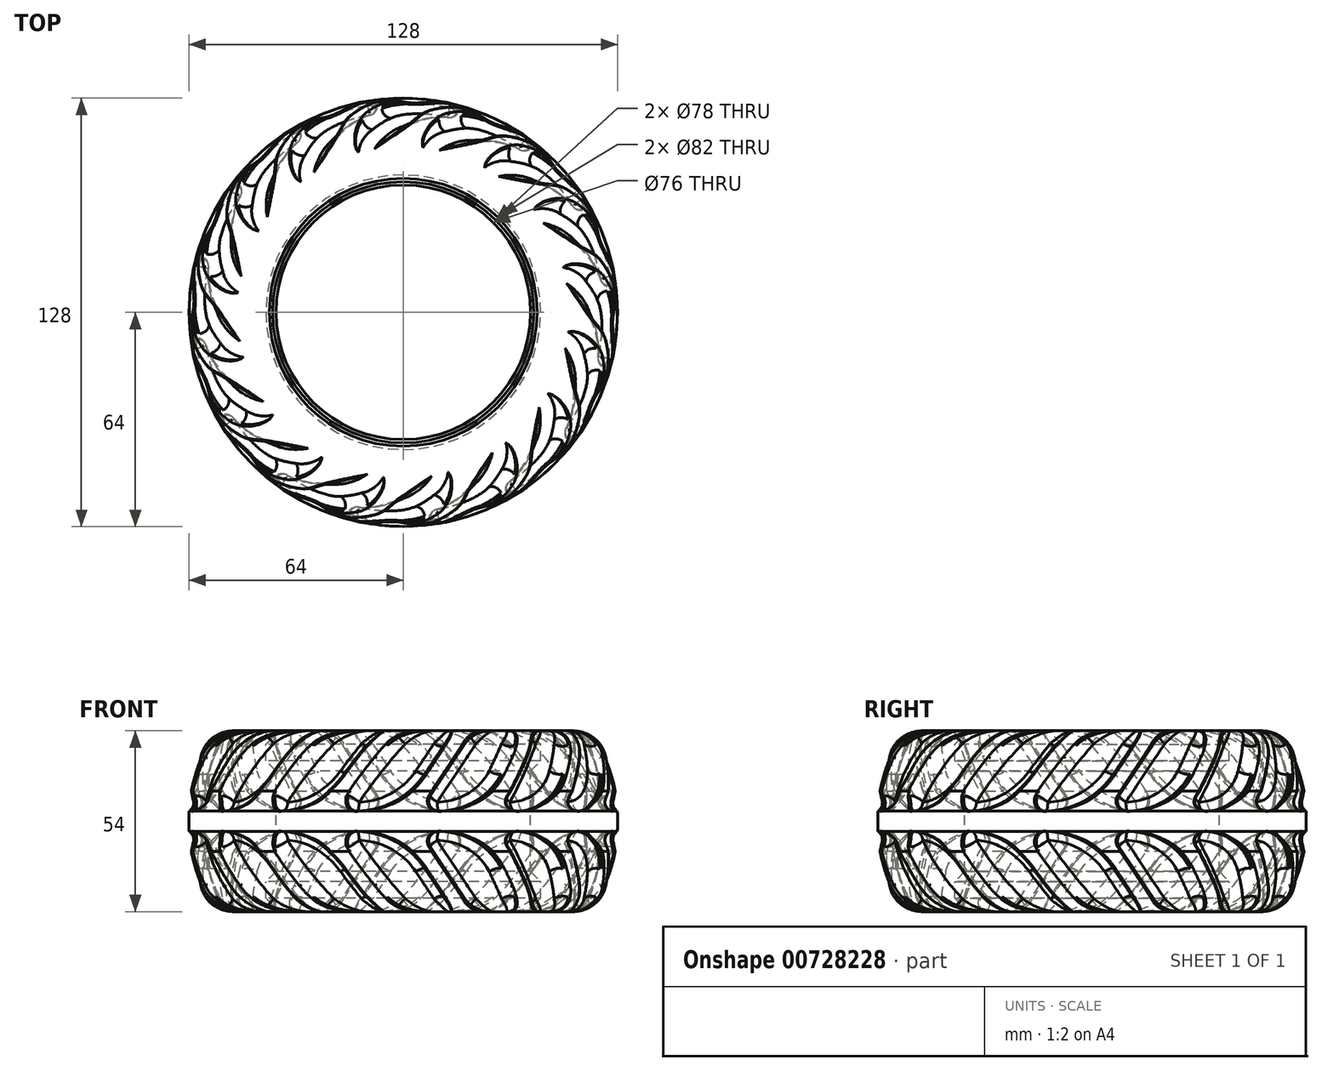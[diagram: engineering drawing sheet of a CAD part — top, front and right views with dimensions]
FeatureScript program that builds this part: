
annotation { "Feature Type Name" : "Feature", "Feature Type Description" : "" }
export const myFeature = defineFeature(function(context is Context, id is Id, definition is map)
    precondition{}
    {
        {
            var Q0;
            Q0=qCreatedBy(makeId("Front.planeOp"),FACE);
            var sketch = newSketch(context, id + "F0", { "sketchPlane" : qUnion([Q0])});
            skLineSegment(sketch, "E0", {"start": v(-39, 25) * mm, "end": v(-39, 27) * mm});
            skLineSegment(sketch, "E1", {"start": v(-39, 25) * mm, "end": v(-41, 23) * mm});
            skLineSegment(sketch, "E2", {"start": v(-41, 23) * mm, "end": v(-41, 18) * mm});
            skLineSegment(sketch, "E3", {"start": v(-41, 18) * mm, "end": v(-38, 15) * mm});
            skLineSegment(sketch, "E4", {"start": v(-38, -15) * mm, "end": v(-41, -18) * mm});
            skLineSegment(sketch, "E5", {"start": v(-41, -18) * mm, "end": v(-41, -23) * mm});
            skLineSegment(sketch, "E6", {"start": v(-41, -23) * mm, "end": v(-39, -25) * mm});
            skLineSegment(sketch, "E7", {"start": v(-39, -25) * mm, "end": v(-39, -27) * mm});
            skLineSegment(sketch, "E8", {"start": v(-38, 15) * mm, "end": v(-38, -15) * mm});
            skLineSegment(sketch, "E9", {"start": v(-38, 0) * mm, "end": v(-62.9, 0) * mm, "construction": true});
            skCircle(sketch, "E10", {"center": v(-49.58, 20.75) * mm, "radius": 6.25 * mm});
            skCircle(sketch, "E11", {"center": v(0, 0) * mm, "radius": 66 * mm});
            skCircle(sketch, "E12", {"center": v(-49.58, -20.75) * mm, "radius": 6.25 * mm});
            skCircle(sketch, "E13", {"center": v(0, 0) * mm, "radius": 60 * mm});
            skLineSegment(sketch, "E14", {"start": v(-39, 27) * mm, "end": v(-49.58, 27) * mm});
            skLineSegment(sketch, "E15", {"start": v(-39, -27) * mm, "end": v(-49.58, -27) * mm});
            skLineSegment(sketch, "E16", {"start": v(0, 89.19) * mm, "end": v(0, -93.9) * mm, "construction": true});
            skCircle(sketch, "E17", {"center": v(-49.58, 20.75) * mm, "radius": 12.25 * mm});
            skSolve(sketch);
        }
        {
            var Q0;
            Q0=makeQuery(id+"F0.imprint","IMPRINT",FACE,{"disambiguationData":[TD([[makeQuery(id+"F0.imprint","IMPRINT",EDGE,{"derivedFrom":sQuery(id+"F0.wireOp",EDGE,"E0")}),1.0]])]});
            var Q1;
            {var subQ0=sQuery(id+"F0.wireOp",EDGE,"E10");var subQ1=makeQuery(id+"F0.imprint","INTERSECT",VERTEX,{"derivedFrom":[subQ0,sQuery(id+"F0.wireOp",EDGE,"E14")]});Q1=makeQuery(id+"F0.imprint","IMPRINT",FACE,{"disambiguationData":[TD([[makeQuery(id+"F0.imprint","IMPRINT",EDGE,{"disambiguationData":[TD([[subQ1,-1.0]])],"derivedFrom":subQ0}),1.0]])]});}
            var Q2;
            {var subQ0=sQuery(id+"F0.wireOp",EDGE,"E12");var subQ1=makeQuery(id+"F0.imprint","INTERSECT",VERTEX,{"derivedFrom":[subQ0,sQuery(id+"F0.wireOp",EDGE,"E15")]});Q2=makeQuery(id+"F0.imprint","IMPRINT",FACE,{"disambiguationData":[TD([[makeQuery(id+"F0.imprint","IMPRINT",EDGE,{"disambiguationData":[TD([[subQ1,1.0]])],"derivedFrom":subQ0}),1.0]])]});}
            var Q3;
            {var subQ6=sQuery(id+"F0.wireOp",EDGE,"E2");Q3=makeQuery(id+"F0.imprint","IMPRINT",FACE,{"disambiguationData":[TD([[makeQuery(id+"F0.imprint","IMPRINT",EDGE,{"derivedFrom":subQ6}),-1.0]])]});}
            var Q4;
            Q4=makeQuery(id+"F0.imprint","IMPRINT",FACE,{"disambiguationData":[TD([[makeQuery(id+"F0.imprint","IMPRINT",EDGE,{"derivedFrom":sQuery(id+"F0.wireOp",EDGE,"E4")}),-1.0]])]});
            var Q5;
            Q5=sQuery(id+"F0.wireOp",EDGE,"E16");
            revolve(context, id + "F1", {"entities" : qUnion([Q0, Q1, Q2, Q3, Q4]), "axis" : qUnion([Q5]), "revolveType" : RevolveType.FULL});
        }
        {
            var Q0;
            Q0=qCreatedBy(makeId("Top.planeOp"),FACE);
            cPlane(context, id + "F2", {"entities" : qUnion([Q0]), "cplaneType" : CPlaneType.OFFSET, "offset" : 27 * mm, "width" : 150 * mm, "height" : 150 * mm});
        }
        {
            var Q0;
            Q0=qCreatedBy(makeId("Top.planeOp"),FACE);
            var sketch = newSketch(context, id + "F3", { "sketchPlane" : qUnion([Q0])});
            skLineSegment(sketch, "E18.bottom", {"start": v(-3, 51) * mm, "end": v(3, 51) * mm});
            skLineSegment(sketch, "E18.top", {"start": v(-3, 66) * mm, "end": v(3, 66) * mm});
            skLineSegment(sketch, "E18.left", {"start": v(-3, 51) * mm, "end": v(-3, 66) * mm});
            skLineSegment(sketch, "E18.right", {"start": v(3, 51) * mm, "end": v(3, 66) * mm});
            skLineSegment(sketch, "E19", {"start": v(0, 113.7) * mm, "end": v(0, -99.56) * mm, "construction": true});
            skLineSegment(sketch, "E20.1.0", {"start": v(-22.29, 45.97) * mm, "end": v(-28.03, 59.83) * mm});
            skLineSegment(sketch, "E20.1.1", {"start": v(-28.03, 59.83) * mm, "end": v(-22.49, 62.12) * mm});
            skLineSegment(sketch, "E20.1.2", {"start": v(-16.75, 48.27) * mm, "end": v(-22.49, 62.12) * mm});
            skLineSegment(sketch, "E20.1.3", {"start": v(-22.29, 45.97) * mm, "end": v(-16.75, 48.27) * mm});
            skLineSegment(sketch, "E20.2.0", {"start": v(-38.18, 33.94) * mm, "end": v(-48.8, 44.55) * mm});
            skLineSegment(sketch, "E20.2.1", {"start": v(-48.8, 44.55) * mm, "end": v(-44.55, 48.8) * mm});
            skLineSegment(sketch, "E20.2.2", {"start": v(-33.94, 38.18) * mm, "end": v(-44.55, 48.8) * mm});
            skLineSegment(sketch, "E20.2.3", {"start": v(-38.18, 33.94) * mm, "end": v(-33.94, 38.18) * mm});
            skLineSegment(sketch, "E20.3.0", {"start": v(-48.27, 16.75) * mm, "end": v(-62.12, 22.49) * mm});
            skLineSegment(sketch, "E20.3.1", {"start": v(-62.12, 22.49) * mm, "end": v(-59.83, 28.03) * mm});
            skLineSegment(sketch, "E20.3.2", {"start": v(-45.97, 22.29) * mm, "end": v(-59.83, 28.03) * mm});
            skLineSegment(sketch, "E20.3.3", {"start": v(-48.27, 16.75) * mm, "end": v(-45.97, 22.29) * mm});
            skLineSegment(sketch, "E20.4.0", {"start": v(-51, -3) * mm, "end": v(-66, -3) * mm});
            skLineSegment(sketch, "E20.4.1", {"start": v(-66, -3) * mm, "end": v(-66, 3) * mm});
            skLineSegment(sketch, "E20.4.2", {"start": v(-51, 3) * mm, "end": v(-66, 3) * mm});
            skLineSegment(sketch, "E20.4.3", {"start": v(-51, -3) * mm, "end": v(-51, 3) * mm});
            skLineSegment(sketch, "E20.5.0", {"start": v(-45.97, -22.29) * mm, "end": v(-59.83, -28.03) * mm});
            skLineSegment(sketch, "E20.5.1", {"start": v(-59.83, -28.03) * mm, "end": v(-62.12, -22.49) * mm});
            skLineSegment(sketch, "E20.5.2", {"start": v(-48.27, -16.75) * mm, "end": v(-62.12, -22.49) * mm});
            skLineSegment(sketch, "E20.5.3", {"start": v(-45.97, -22.29) * mm, "end": v(-48.27, -16.75) * mm});
            skLineSegment(sketch, "E20.6.0", {"start": v(-33.94, -38.18) * mm, "end": v(-44.55, -48.8) * mm});
            skLineSegment(sketch, "E20.6.1", {"start": v(-44.55, -48.8) * mm, "end": v(-48.8, -44.55) * mm});
            skLineSegment(sketch, "E20.6.2", {"start": v(-38.18, -33.94) * mm, "end": v(-48.8, -44.55) * mm});
            skLineSegment(sketch, "E20.6.3", {"start": v(-33.94, -38.18) * mm, "end": v(-38.18, -33.94) * mm});
            skLineSegment(sketch, "E20.7.0", {"start": v(-16.75, -48.27) * mm, "end": v(-22.49, -62.12) * mm});
            skLineSegment(sketch, "E20.7.1", {"start": v(-22.49, -62.12) * mm, "end": v(-28.03, -59.83) * mm});
            skLineSegment(sketch, "E20.7.2", {"start": v(-22.29, -45.97) * mm, "end": v(-28.03, -59.83) * mm});
            skLineSegment(sketch, "E20.7.3", {"start": v(-16.75, -48.27) * mm, "end": v(-22.29, -45.97) * mm});
            skLineSegment(sketch, "E20.8.0", {"start": v(3, -51) * mm, "end": v(3, -66) * mm});
            skLineSegment(sketch, "E20.8.1", {"start": v(3, -66) * mm, "end": v(-3, -66) * mm});
            skLineSegment(sketch, "E20.8.2", {"start": v(-3, -51) * mm, "end": v(-3, -66) * mm});
            skLineSegment(sketch, "E20.8.3", {"start": v(3, -51) * mm, "end": v(-3, -51) * mm});
            skLineSegment(sketch, "E20.9.0", {"start": v(22.29, -45.97) * mm, "end": v(28.03, -59.83) * mm});
            skLineSegment(sketch, "E20.9.1", {"start": v(28.03, -59.83) * mm, "end": v(22.49, -62.12) * mm});
            skLineSegment(sketch, "E20.9.2", {"start": v(16.75, -48.27) * mm, "end": v(22.49, -62.12) * mm});
            skLineSegment(sketch, "E20.9.3", {"start": v(22.29, -45.97) * mm, "end": v(16.75, -48.27) * mm});
            skLineSegment(sketch, "E20.10.0", {"start": v(38.18, -33.94) * mm, "end": v(48.8, -44.55) * mm});
            skLineSegment(sketch, "E20.10.1", {"start": v(48.8, -44.55) * mm, "end": v(44.55, -48.8) * mm});
            skLineSegment(sketch, "E20.10.2", {"start": v(33.94, -38.18) * mm, "end": v(44.55, -48.8) * mm});
            skLineSegment(sketch, "E20.10.3", {"start": v(38.18, -33.94) * mm, "end": v(33.94, -38.18) * mm});
            skLineSegment(sketch, "E20.11.0", {"start": v(48.27, -16.75) * mm, "end": v(62.12, -22.49) * mm});
            skLineSegment(sketch, "E20.11.1", {"start": v(62.12, -22.49) * mm, "end": v(59.83, -28.03) * mm});
            skLineSegment(sketch, "E20.11.2", {"start": v(45.97, -22.29) * mm, "end": v(59.83, -28.03) * mm});
            skLineSegment(sketch, "E20.11.3", {"start": v(48.27, -16.75) * mm, "end": v(45.97, -22.29) * mm});
            skLineSegment(sketch, "E20.12.0", {"start": v(51, 3) * mm, "end": v(66, 3) * mm});
            skLineSegment(sketch, "E20.12.1", {"start": v(66, 3) * mm, "end": v(66, -3) * mm});
            skLineSegment(sketch, "E20.12.2", {"start": v(51, -3) * mm, "end": v(66, -3) * mm});
            skLineSegment(sketch, "E20.12.3", {"start": v(51, 3) * mm, "end": v(51, -3) * mm});
            skLineSegment(sketch, "E20.13.0", {"start": v(45.97, 22.29) * mm, "end": v(59.83, 28.03) * mm});
            skLineSegment(sketch, "E20.13.1", {"start": v(59.83, 28.03) * mm, "end": v(62.12, 22.49) * mm});
            skLineSegment(sketch, "E20.13.2", {"start": v(48.27, 16.75) * mm, "end": v(62.12, 22.49) * mm});
            skLineSegment(sketch, "E20.13.3", {"start": v(45.97, 22.29) * mm, "end": v(48.27, 16.75) * mm});
            skLineSegment(sketch, "E20.14.0", {"start": v(33.94, 38.18) * mm, "end": v(44.55, 48.8) * mm});
            skLineSegment(sketch, "E20.14.1", {"start": v(44.55, 48.8) * mm, "end": v(48.8, 44.55) * mm});
            skLineSegment(sketch, "E20.14.2", {"start": v(38.18, 33.94) * mm, "end": v(48.8, 44.55) * mm});
            skLineSegment(sketch, "E20.14.3", {"start": v(33.94, 38.18) * mm, "end": v(38.18, 33.94) * mm});
            skLineSegment(sketch, "E20.15.0", {"start": v(16.75, 48.27) * mm, "end": v(22.49, 62.12) * mm});
            skLineSegment(sketch, "E20.15.1", {"start": v(22.49, 62.12) * mm, "end": v(28.03, 59.83) * mm});
            skLineSegment(sketch, "E20.15.2", {"start": v(22.29, 45.97) * mm, "end": v(28.03, 59.83) * mm});
            skLineSegment(sketch, "E20.15.3", {"start": v(16.75, 48.27) * mm, "end": v(22.29, 45.97) * mm});
            skPoint(sketch, "E20.center", {"position": v(0, 0) * mm});
            skSolve(sketch);
        }
        {
            var Q0;
            Q0=qCreatedBy(id+"F2.planeOp",FACE);
            var sketch = newSketch(context, id + "F4", { "sketchPlane" : qUnion([Q0])});
            skLineSegment(sketch, "E21", {"start": v(-21, 70) * mm, "end": v(-21, 45) * mm});
            skLineSegment(sketch, "E22", {"start": v(-21, 45) * mm, "end": v(-15, 45) * mm});
            skLineSegment(sketch, "E23", {"start": v(-21, 70) * mm, "end": v(-15, 70) * mm});
            skLineSegment(sketch, "E24", {"start": v(-15, 70) * mm, "end": v(-15, 45) * mm});
            skLineSegment(sketch, "E25", {"start": v(0, 99.7) * mm, "end": v(0, -107.8) * mm, "construction": true});
            skLineSegment(sketch, "E26.1.0", {"start": v(-46.19, 56.64) * mm, "end": v(-36.62, 33.54) * mm});
            skLineSegment(sketch, "E26.1.1", {"start": v(-40.65, 58.93) * mm, "end": v(-31.08, 35.83) * mm});
            skLineSegment(sketch, "E26.1.2", {"start": v(-36.62, 33.54) * mm, "end": v(-31.08, 35.83) * mm});
            skLineSegment(sketch, "E26.1.3", {"start": v(-46.19, 56.64) * mm, "end": v(-40.65, 58.93) * mm});
            skLineSegment(sketch, "E26.2.0", {"start": v(-64.35, 34.65) * mm, "end": v(-46.67, 16.97) * mm});
            skLineSegment(sketch, "E26.2.1", {"start": v(-60.1, 38.9) * mm, "end": v(-42.43, 21.21) * mm});
            skLineSegment(sketch, "E26.2.2", {"start": v(-46.67, 16.97) * mm, "end": v(-42.43, 21.21) * mm});
            skLineSegment(sketch, "E26.2.3", {"start": v(-64.35, 34.65) * mm, "end": v(-60.1, 38.9) * mm});
            skLineSegment(sketch, "E26.3.0", {"start": v(-72.7, 7.39) * mm, "end": v(-49.61, -2.18) * mm});
            skLineSegment(sketch, "E26.3.1", {"start": v(-70.41, 12.93) * mm, "end": v(-47.31, 3.36) * mm});
            skLineSegment(sketch, "E26.3.2", {"start": v(-49.61, -2.18) * mm, "end": v(-47.31, 3.36) * mm});
            skLineSegment(sketch, "E26.3.3", {"start": v(-72.7, 7.39) * mm, "end": v(-70.41, 12.93) * mm});
            skLineSegment(sketch, "E26.4.0", {"start": v(-70, -21) * mm, "end": v(-45, -21) * mm});
            skLineSegment(sketch, "E26.4.1", {"start": v(-70, -15) * mm, "end": v(-45, -15) * mm});
            skLineSegment(sketch, "E26.4.2", {"start": v(-45, -21) * mm, "end": v(-45, -15) * mm});
            skLineSegment(sketch, "E26.4.3", {"start": v(-70, -21) * mm, "end": v(-70, -15) * mm});
            skLineSegment(sketch, "E26.5.0", {"start": v(-56.64, -46.19) * mm, "end": v(-33.54, -36.62) * mm});
            skLineSegment(sketch, "E26.5.1", {"start": v(-58.93, -40.65) * mm, "end": v(-35.83, -31.08) * mm});
            skLineSegment(sketch, "E26.5.2", {"start": v(-33.54, -36.62) * mm, "end": v(-35.83, -31.08) * mm});
            skLineSegment(sketch, "E26.5.3", {"start": v(-56.64, -46.19) * mm, "end": v(-58.93, -40.65) * mm});
            skLineSegment(sketch, "E26.6.0", {"start": v(-34.65, -64.35) * mm, "end": v(-16.97, -46.67) * mm});
            skLineSegment(sketch, "E26.6.1", {"start": v(-38.9, -60.1) * mm, "end": v(-21.21, -42.43) * mm});
            skLineSegment(sketch, "E26.6.2", {"start": v(-16.97, -46.67) * mm, "end": v(-21.21, -42.43) * mm});
            skLineSegment(sketch, "E26.6.3", {"start": v(-34.65, -64.35) * mm, "end": v(-38.9, -60.1) * mm});
            skLineSegment(sketch, "E26.7.0", {"start": v(-7.39, -72.7) * mm, "end": v(2.18, -49.61) * mm});
            skLineSegment(sketch, "E26.7.1", {"start": v(-12.93, -70.41) * mm, "end": v(-3.36, -47.31) * mm});
            skLineSegment(sketch, "E26.7.2", {"start": v(2.18, -49.61) * mm, "end": v(-3.36, -47.31) * mm});
            skLineSegment(sketch, "E26.7.3", {"start": v(-7.39, -72.7) * mm, "end": v(-12.93, -70.41) * mm});
            skLineSegment(sketch, "E26.8.0", {"start": v(21, -70) * mm, "end": v(21, -45) * mm});
            skLineSegment(sketch, "E26.8.1", {"start": v(15, -70) * mm, "end": v(15, -45) * mm});
            skLineSegment(sketch, "E26.8.2", {"start": v(21, -45) * mm, "end": v(15, -45) * mm});
            skLineSegment(sketch, "E26.8.3", {"start": v(21, -70) * mm, "end": v(15, -70) * mm});
            skLineSegment(sketch, "E26.9.0", {"start": v(46.19, -56.64) * mm, "end": v(36.62, -33.54) * mm});
            skLineSegment(sketch, "E26.9.1", {"start": v(40.65, -58.93) * mm, "end": v(31.08, -35.83) * mm});
            skLineSegment(sketch, "E26.9.2", {"start": v(36.62, -33.54) * mm, "end": v(31.08, -35.83) * mm});
            skLineSegment(sketch, "E26.9.3", {"start": v(46.19, -56.64) * mm, "end": v(40.65, -58.93) * mm});
            skLineSegment(sketch, "E26.10.0", {"start": v(64.35, -34.65) * mm, "end": v(46.67, -16.97) * mm});
            skLineSegment(sketch, "E26.10.1", {"start": v(60.1, -38.9) * mm, "end": v(42.43, -21.21) * mm});
            skLineSegment(sketch, "E26.10.2", {"start": v(46.67, -16.97) * mm, "end": v(42.43, -21.21) * mm});
            skLineSegment(sketch, "E26.10.3", {"start": v(64.35, -34.65) * mm, "end": v(60.1, -38.9) * mm});
            skLineSegment(sketch, "E26.11.0", {"start": v(72.7, -7.39) * mm, "end": v(49.61, 2.18) * mm});
            skLineSegment(sketch, "E26.11.1", {"start": v(70.41, -12.93) * mm, "end": v(47.31, -3.36) * mm});
            skLineSegment(sketch, "E26.11.2", {"start": v(49.61, 2.18) * mm, "end": v(47.31, -3.36) * mm});
            skLineSegment(sketch, "E26.11.3", {"start": v(72.7, -7.39) * mm, "end": v(70.41, -12.93) * mm});
            skLineSegment(sketch, "E26.12.0", {"start": v(70, 21) * mm, "end": v(45, 21) * mm});
            skLineSegment(sketch, "E26.12.1", {"start": v(70, 15) * mm, "end": v(45, 15) * mm});
            skLineSegment(sketch, "E26.12.2", {"start": v(45, 21) * mm, "end": v(45, 15) * mm});
            skLineSegment(sketch, "E26.12.3", {"start": v(70, 21) * mm, "end": v(70, 15) * mm});
            skLineSegment(sketch, "E26.13.0", {"start": v(56.64, 46.19) * mm, "end": v(33.54, 36.62) * mm});
            skLineSegment(sketch, "E26.13.1", {"start": v(58.93, 40.65) * mm, "end": v(35.83, 31.08) * mm});
            skLineSegment(sketch, "E26.13.2", {"start": v(33.54, 36.62) * mm, "end": v(35.83, 31.08) * mm});
            skLineSegment(sketch, "E26.13.3", {"start": v(56.64, 46.19) * mm, "end": v(58.93, 40.65) * mm});
            skLineSegment(sketch, "E26.14.0", {"start": v(34.65, 64.35) * mm, "end": v(16.97, 46.67) * mm});
            skLineSegment(sketch, "E26.14.1", {"start": v(38.9, 60.1) * mm, "end": v(21.21, 42.43) * mm});
            skLineSegment(sketch, "E26.14.2", {"start": v(16.97, 46.67) * mm, "end": v(21.21, 42.43) * mm});
            skLineSegment(sketch, "E26.14.3", {"start": v(34.65, 64.35) * mm, "end": v(38.9, 60.1) * mm});
            skLineSegment(sketch, "E26.15.0", {"start": v(7.39, 72.7) * mm, "end": v(-2.18, 49.61) * mm});
            skLineSegment(sketch, "E26.15.1", {"start": v(12.93, 70.41) * mm, "end": v(3.36, 47.31) * mm});
            skLineSegment(sketch, "E26.15.2", {"start": v(-2.18, 49.61) * mm, "end": v(3.36, 47.31) * mm});
            skLineSegment(sketch, "E26.15.3", {"start": v(7.39, 72.7) * mm, "end": v(12.93, 70.41) * mm});
            skPoint(sketch, "E26.center", {"position": v(0, 0) * mm});
            skSolve(sketch);
        }
        {
            var Q1;
            Q1=makeQuery(id+"F3.imprint","IMPRINT",FACE,{"disambiguationData":[TD([[makeQuery(id+"F3.imprint","IMPRINT",EDGE,{"derivedFrom":sQuery(id+"F3.wireOp",EDGE,"E18.bottom")}),1.0]])]});
            var Q2;
            Q2=makeQuery(id+"F4.imprint","IMPRINT",FACE,{"disambiguationData":[TD([[makeQuery(id+"F4.imprint","IMPRINT",EDGE,{"derivedFrom":sQuery(id+"F4.wireOp",EDGE,"E21")}),1.0]])]});
            loft(context, id + "F5", {"operationType" : NewBodyOperationType.ADD, "sheetProfilesArray" : [{ "sheetProfileEntities" : qUnion([Q1]) }, { "sheetProfileEntities" : qUnion([Q2]) }]});
        }
        {
            var Q1;
            Q1=makeQuery(id+"F3.imprint","IMPRINT",FACE,{"disambiguationData":[TD([[makeQuery(id+"F3.imprint","IMPRINT",EDGE,{"derivedFrom":sQuery(id+"F3.wireOp",EDGE,"E20.15.0")}),-1.0]])]});
            var Q2;
            Q2=makeQuery(id+"F4.imprint","IMPRINT",FACE,{"disambiguationData":[TD([[makeQuery(id+"F4.imprint","IMPRINT",EDGE,{"derivedFrom":sQuery(id+"F4.wireOp",EDGE,"E26.15.0")}),1.0]])]});
            loft(context, id + "F6", {"operationType" : NewBodyOperationType.ADD, "sheetProfilesArray" : [{ "sheetProfileEntities" : qUnion([Q1]) }, { "sheetProfileEntities" : qUnion([Q2]) }]});
        }
        {
            var Q1;
            Q1=makeQuery(id+"F3.imprint","IMPRINT",FACE,{"disambiguationData":[TD([[makeQuery(id+"F3.imprint","IMPRINT",EDGE,{"derivedFrom":sQuery(id+"F3.wireOp",EDGE,"E20.14.0")}),-1.0]])]});
            var Q2;
            Q2=makeQuery(id+"F4.imprint","IMPRINT",FACE,{"disambiguationData":[TD([[makeQuery(id+"F4.imprint","IMPRINT",EDGE,{"derivedFrom":sQuery(id+"F4.wireOp",EDGE,"E26.14.0")}),1.0]])]});
            loft(context, id + "F7", {"operationType" : NewBodyOperationType.ADD, "sheetProfilesArray" : [{ "sheetProfileEntities" : qUnion([Q1]) }, { "sheetProfileEntities" : qUnion([Q2]) }]});
        }
        {
            var Q1;
            Q1=makeQuery(id+"F3.imprint","IMPRINT",FACE,{"disambiguationData":[TD([[makeQuery(id+"F3.imprint","IMPRINT",EDGE,{"derivedFrom":sQuery(id+"F3.wireOp",EDGE,"E20.13.0")}),-1.0]])]});
            var Q2;
            Q2=makeQuery(id+"F4.imprint","IMPRINT",FACE,{"disambiguationData":[TD([[makeQuery(id+"F4.imprint","IMPRINT",EDGE,{"derivedFrom":sQuery(id+"F4.wireOp",EDGE,"E26.13.0")}),1.0]])]});
            loft(context, id + "F8", {"operationType" : NewBodyOperationType.ADD, "sheetProfilesArray" : [{ "sheetProfileEntities" : qUnion([Q1]) }, { "sheetProfileEntities" : qUnion([Q2]) }]});
        }
        {
            var Q1;
            Q1=makeQuery(id+"F3.imprint","IMPRINT",FACE,{"disambiguationData":[TD([[makeQuery(id+"F3.imprint","IMPRINT",EDGE,{"derivedFrom":sQuery(id+"F3.wireOp",EDGE,"E20.12.0")}),-1.0]])]});
            var Q2;
            Q2=makeQuery(id+"F4.imprint","IMPRINT",FACE,{"disambiguationData":[TD([[makeQuery(id+"F4.imprint","IMPRINT",EDGE,{"derivedFrom":sQuery(id+"F4.wireOp",EDGE,"E26.12.0")}),1.0]])]});
            loft(context, id + "F9", {"operationType" : NewBodyOperationType.ADD, "sheetProfilesArray" : [{ "sheetProfileEntities" : qUnion([Q1]) }, { "sheetProfileEntities" : qUnion([Q2]) }]});
        }
        {
            var Q1;
            Q1=makeQuery(id+"F3.imprint","IMPRINT",FACE,{"disambiguationData":[TD([[makeQuery(id+"F3.imprint","IMPRINT",EDGE,{"derivedFrom":sQuery(id+"F3.wireOp",EDGE,"E20.11.0")}),-1.0]])]});
            var Q2;
            Q2=makeQuery(id+"F4.imprint","IMPRINT",FACE,{"disambiguationData":[TD([[makeQuery(id+"F4.imprint","IMPRINT",EDGE,{"derivedFrom":sQuery(id+"F4.wireOp",EDGE,"E26.11.0")}),1.0]])]});
            loft(context, id + "F10", {"operationType" : NewBodyOperationType.ADD, "sheetProfilesArray" : [{ "sheetProfileEntities" : qUnion([Q1]) }, { "sheetProfileEntities" : qUnion([Q2]) }]});
        }
        {
            var Q1;
            Q1=makeQuery(id+"F3.imprint","IMPRINT",FACE,{"disambiguationData":[TD([[makeQuery(id+"F3.imprint","IMPRINT",EDGE,{"derivedFrom":sQuery(id+"F3.wireOp",EDGE,"E20.10.0")}),-1.0]])]});
            var Q2;
            Q2=makeQuery(id+"F4.imprint","IMPRINT",FACE,{"disambiguationData":[TD([[makeQuery(id+"F4.imprint","IMPRINT",EDGE,{"derivedFrom":sQuery(id+"F4.wireOp",EDGE,"E26.10.0")}),1.0]])]});
            loft(context, id + "F11", {"operationType" : NewBodyOperationType.ADD, "sheetProfilesArray" : [{ "sheetProfileEntities" : qUnion([Q1]) }, { "sheetProfileEntities" : qUnion([Q2]) }]});
        }
        {
            var Q1;
            Q1=makeQuery(id+"F3.imprint","IMPRINT",FACE,{"disambiguationData":[TD([[makeQuery(id+"F3.imprint","IMPRINT",EDGE,{"derivedFrom":sQuery(id+"F3.wireOp",EDGE,"E20.9.0")}),-1.0]])]});
            var Q2;
            Q2=makeQuery(id+"F4.imprint","IMPRINT",FACE,{"disambiguationData":[TD([[makeQuery(id+"F4.imprint","IMPRINT",EDGE,{"derivedFrom":sQuery(id+"F4.wireOp",EDGE,"E26.9.0")}),1.0]])]});
            loft(context, id + "F12", {"operationType" : NewBodyOperationType.ADD, "sheetProfilesArray" : [{ "sheetProfileEntities" : qUnion([Q1]) }, { "sheetProfileEntities" : qUnion([Q2]) }]});
        }
        {
            var Q1;
            Q1=makeQuery(id+"F3.imprint","IMPRINT",FACE,{"disambiguationData":[TD([[makeQuery(id+"F3.imprint","IMPRINT",EDGE,{"derivedFrom":sQuery(id+"F3.wireOp",EDGE,"E20.8.0")}),-1.0]])]});
            var Q2;
            Q2=makeQuery(id+"F4.imprint","IMPRINT",FACE,{"disambiguationData":[TD([[makeQuery(id+"F4.imprint","IMPRINT",EDGE,{"derivedFrom":sQuery(id+"F4.wireOp",EDGE,"E26.8.0")}),1.0]])]});
            loft(context, id + "F13", {"operationType" : NewBodyOperationType.ADD, "sheetProfilesArray" : [{ "sheetProfileEntities" : qUnion([Q1]) }, { "sheetProfileEntities" : qUnion([Q2]) }]});
        }
        {
            var Q1;
            Q1=makeQuery(id+"F3.imprint","IMPRINT",FACE,{"disambiguationData":[TD([[makeQuery(id+"F3.imprint","IMPRINT",EDGE,{"derivedFrom":sQuery(id+"F3.wireOp",EDGE,"E20.7.0")}),-1.0]])]});
            var Q2;
            Q2=makeQuery(id+"F4.imprint","IMPRINT",FACE,{"disambiguationData":[TD([[makeQuery(id+"F4.imprint","IMPRINT",EDGE,{"derivedFrom":sQuery(id+"F4.wireOp",EDGE,"E26.7.0")}),1.0]])]});
            loft(context, id + "F14", {"operationType" : NewBodyOperationType.ADD, "sheetProfilesArray" : [{ "sheetProfileEntities" : qUnion([Q1]) }, { "sheetProfileEntities" : qUnion([Q2]) }]});
        }
        {
            var Q1;
            Q1=makeQuery(id+"F3.imprint","IMPRINT",FACE,{"disambiguationData":[TD([[makeQuery(id+"F3.imprint","IMPRINT",EDGE,{"derivedFrom":sQuery(id+"F3.wireOp",EDGE,"E20.6.0")}),-1.0]])]});
            var Q2;
            Q2=makeQuery(id+"F4.imprint","IMPRINT",FACE,{"disambiguationData":[TD([[makeQuery(id+"F4.imprint","IMPRINT",EDGE,{"derivedFrom":sQuery(id+"F4.wireOp",EDGE,"E26.6.0")}),1.0]])]});
            loft(context, id + "F15", {"operationType" : NewBodyOperationType.ADD, "sheetProfilesArray" : [{ "sheetProfileEntities" : qUnion([Q1]) }, { "sheetProfileEntities" : qUnion([Q2]) }]});
        }
        {
            var Q1;
            Q1=makeQuery(id+"F3.imprint","IMPRINT",FACE,{"disambiguationData":[TD([[makeQuery(id+"F3.imprint","IMPRINT",EDGE,{"derivedFrom":sQuery(id+"F3.wireOp",EDGE,"E20.5.0")}),-1.0]])]});
            var Q2;
            Q2=makeQuery(id+"F4.imprint","IMPRINT",FACE,{"disambiguationData":[TD([[makeQuery(id+"F4.imprint","IMPRINT",EDGE,{"derivedFrom":sQuery(id+"F4.wireOp",EDGE,"E26.5.0")}),1.0]])]});
            loft(context, id + "F16", {"operationType" : NewBodyOperationType.ADD, "sheetProfilesArray" : [{ "sheetProfileEntities" : qUnion([Q1]) }, { "sheetProfileEntities" : qUnion([Q2]) }]});
        }
        {
            var Q1;
            Q1=makeQuery(id+"F4.imprint","IMPRINT",FACE,{"disambiguationData":[TD([[makeQuery(id+"F4.imprint","IMPRINT",EDGE,{"derivedFrom":sQuery(id+"F4.wireOp",EDGE,"E26.4.0")}),1.0]])]});
            var Q2;
            Q2=makeQuery(id+"F3.imprint","IMPRINT",FACE,{"disambiguationData":[TD([[makeQuery(id+"F3.imprint","IMPRINT",EDGE,{"derivedFrom":sQuery(id+"F3.wireOp",EDGE,"E20.4.0")}),-1.0]])]});
            loft(context, id + "F17", {"operationType" : NewBodyOperationType.ADD, "sheetProfilesArray" : [{ "sheetProfileEntities" : qUnion([Q1]) }, { "sheetProfileEntities" : qUnion([Q2]) }]});
        }
        {
            var Q1;
            Q1=makeQuery(id+"F3.imprint","IMPRINT",FACE,{"disambiguationData":[TD([[makeQuery(id+"F3.imprint","IMPRINT",EDGE,{"derivedFrom":sQuery(id+"F3.wireOp",EDGE,"E20.3.0")}),-1.0]])]});
            var Q2;
            Q2=makeQuery(id+"F4.imprint","IMPRINT",FACE,{"disambiguationData":[TD([[makeQuery(id+"F4.imprint","IMPRINT",EDGE,{"derivedFrom":sQuery(id+"F4.wireOp",EDGE,"E26.3.0")}),1.0]])]});
            loft(context, id + "F18", {"operationType" : NewBodyOperationType.ADD, "sheetProfilesArray" : [{ "sheetProfileEntities" : qUnion([Q1]) }, { "sheetProfileEntities" : qUnion([Q2]) }]});
        }
        {
            var Q1;
            Q1=makeQuery(id+"F3.imprint","IMPRINT",FACE,{"disambiguationData":[TD([[makeQuery(id+"F3.imprint","IMPRINT",EDGE,{"derivedFrom":sQuery(id+"F3.wireOp",EDGE,"E20.2.0")}),-1.0]])]});
            var Q2;
            Q2=makeQuery(id+"F4.imprint","IMPRINT",FACE,{"disambiguationData":[TD([[makeQuery(id+"F4.imprint","IMPRINT",EDGE,{"derivedFrom":sQuery(id+"F4.wireOp",EDGE,"E26.2.0")}),1.0]])]});
            loft(context, id + "F19", {"operationType" : NewBodyOperationType.ADD, "sheetProfilesArray" : [{ "sheetProfileEntities" : qUnion([Q1]) }, { "sheetProfileEntities" : qUnion([Q2]) }]});
        }
        {
            var Q1;
            Q1=makeQuery(id+"F3.imprint","IMPRINT",FACE,{"disambiguationData":[TD([[makeQuery(id+"F3.imprint","IMPRINT",EDGE,{"derivedFrom":sQuery(id+"F3.wireOp",EDGE,"E20.1.0")}),-1.0]])]});
            var Q2;
            Q2=makeQuery(id+"F4.imprint","IMPRINT",FACE,{"disambiguationData":[TD([[makeQuery(id+"F4.imprint","IMPRINT",EDGE,{"derivedFrom":sQuery(id+"F4.wireOp",EDGE,"E26.1.0")}),1.0]])]});
            loft(context, id + "F20", {"operationType" : NewBodyOperationType.ADD, "sheetProfilesArray" : [{ "sheetProfileEntities" : qUnion([Q1]) }, { "sheetProfileEntities" : qUnion([Q2]) }]});
        }
        {
            var Q0;
            Q0=qCreatedBy(makeId("Top.planeOp"),FACE);
            cPlane(context, id + "F21", {"entities" : qUnion([Q0]), "cplaneType" : CPlaneType.OFFSET, "offset" : 27 * mm, "oppositeDirection" : true, "width" : 150 * mm, "height" : 150 * mm});
        }
        {
            var Q0;
            Q0=qCreatedBy(id+"F21.planeOp",FACE);
            var sketch = newSketch(context, id + "F22", { "sketchPlane" : qUnion([Q0])});
            skLineSegment(sketch, "E27.bottom", {"start": v(15, -70) * mm, "end": v(21, -70) * mm});
            skLineSegment(sketch, "E27.top", {"start": v(15, -45) * mm, "end": v(21, -45) * mm});
            skLineSegment(sketch, "E27.left", {"start": v(15, -70) * mm, "end": v(15, -45) * mm});
            skLineSegment(sketch, "E27.right", {"start": v(21, -70) * mm, "end": v(21, -45) * mm});
            skLineSegment(sketch, "E28.1.0", {"start": v(40.65, -58.93) * mm, "end": v(31.08, -35.83) * mm});
            skLineSegment(sketch, "E28.1.1", {"start": v(46.19, -56.64) * mm, "end": v(36.62, -33.54) * mm});
            skLineSegment(sketch, "E28.1.2", {"start": v(40.65, -58.93) * mm, "end": v(46.19, -56.64) * mm});
            skLineSegment(sketch, "E28.1.3", {"start": v(31.08, -35.83) * mm, "end": v(36.62, -33.54) * mm});
            skLineSegment(sketch, "E28.2.0", {"start": v(60.1, -38.9) * mm, "end": v(42.43, -21.21) * mm});
            skLineSegment(sketch, "E28.2.1", {"start": v(64.35, -34.65) * mm, "end": v(46.67, -16.97) * mm});
            skLineSegment(sketch, "E28.2.2", {"start": v(60.1, -38.9) * mm, "end": v(64.35, -34.65) * mm});
            skLineSegment(sketch, "E28.2.3", {"start": v(42.43, -21.21) * mm, "end": v(46.67, -16.97) * mm});
            skLineSegment(sketch, "E28.3.0", {"start": v(70.41, -12.93) * mm, "end": v(47.31, -3.36) * mm});
            skLineSegment(sketch, "E28.3.1", {"start": v(72.7, -7.39) * mm, "end": v(49.61, 2.18) * mm});
            skLineSegment(sketch, "E28.3.2", {"start": v(70.41, -12.93) * mm, "end": v(72.7, -7.39) * mm});
            skLineSegment(sketch, "E28.3.3", {"start": v(47.31, -3.36) * mm, "end": v(49.61, 2.18) * mm});
            skLineSegment(sketch, "E28.4.0", {"start": v(70, 15) * mm, "end": v(45, 15) * mm});
            skLineSegment(sketch, "E28.4.1", {"start": v(70, 21) * mm, "end": v(45, 21) * mm});
            skLineSegment(sketch, "E28.4.2", {"start": v(70, 15) * mm, "end": v(70, 21) * mm});
            skLineSegment(sketch, "E28.4.3", {"start": v(45, 15) * mm, "end": v(45, 21) * mm});
            skLineSegment(sketch, "E28.5.0", {"start": v(58.93, 40.65) * mm, "end": v(35.83, 31.08) * mm});
            skLineSegment(sketch, "E28.5.1", {"start": v(56.64, 46.19) * mm, "end": v(33.54, 36.62) * mm});
            skLineSegment(sketch, "E28.5.2", {"start": v(58.93, 40.65) * mm, "end": v(56.64, 46.19) * mm});
            skLineSegment(sketch, "E28.5.3", {"start": v(35.83, 31.08) * mm, "end": v(33.54, 36.62) * mm});
            skLineSegment(sketch, "E28.6.0", {"start": v(38.9, 60.1) * mm, "end": v(21.21, 42.43) * mm});
            skLineSegment(sketch, "E28.6.1", {"start": v(34.65, 64.35) * mm, "end": v(16.97, 46.67) * mm});
            skLineSegment(sketch, "E28.6.2", {"start": v(38.9, 60.1) * mm, "end": v(34.65, 64.35) * mm});
            skLineSegment(sketch, "E28.6.3", {"start": v(21.21, 42.43) * mm, "end": v(16.97, 46.67) * mm});
            skLineSegment(sketch, "E28.7.0", {"start": v(12.93, 70.41) * mm, "end": v(3.36, 47.31) * mm});
            skLineSegment(sketch, "E28.7.1", {"start": v(7.39, 72.7) * mm, "end": v(-2.18, 49.61) * mm});
            skLineSegment(sketch, "E28.7.2", {"start": v(12.93, 70.41) * mm, "end": v(7.39, 72.7) * mm});
            skLineSegment(sketch, "E28.7.3", {"start": v(3.36, 47.31) * mm, "end": v(-2.18, 49.61) * mm});
            skLineSegment(sketch, "E28.8.0", {"start": v(-15, 70) * mm, "end": v(-15, 45) * mm});
            skLineSegment(sketch, "E28.8.1", {"start": v(-21, 70) * mm, "end": v(-21, 45) * mm});
            skLineSegment(sketch, "E28.8.2", {"start": v(-15, 70) * mm, "end": v(-21, 70) * mm});
            skLineSegment(sketch, "E28.8.3", {"start": v(-15, 45) * mm, "end": v(-21, 45) * mm});
            skLineSegment(sketch, "E28.9.0", {"start": v(-40.65, 58.93) * mm, "end": v(-31.08, 35.83) * mm});
            skLineSegment(sketch, "E28.9.1", {"start": v(-46.19, 56.64) * mm, "end": v(-36.62, 33.54) * mm});
            skLineSegment(sketch, "E28.9.2", {"start": v(-40.65, 58.93) * mm, "end": v(-46.19, 56.64) * mm});
            skLineSegment(sketch, "E28.9.3", {"start": v(-31.08, 35.83) * mm, "end": v(-36.62, 33.54) * mm});
            skLineSegment(sketch, "E28.10.0", {"start": v(-60.1, 38.9) * mm, "end": v(-42.43, 21.21) * mm});
            skLineSegment(sketch, "E28.10.1", {"start": v(-64.35, 34.65) * mm, "end": v(-46.67, 16.97) * mm});
            skLineSegment(sketch, "E28.10.2", {"start": v(-60.1, 38.9) * mm, "end": v(-64.35, 34.65) * mm});
            skLineSegment(sketch, "E28.10.3", {"start": v(-42.43, 21.21) * mm, "end": v(-46.67, 16.97) * mm});
            skLineSegment(sketch, "E28.11.0", {"start": v(-70.41, 12.93) * mm, "end": v(-47.31, 3.36) * mm});
            skLineSegment(sketch, "E28.11.1", {"start": v(-72.7, 7.39) * mm, "end": v(-49.61, -2.18) * mm});
            skLineSegment(sketch, "E28.11.2", {"start": v(-70.41, 12.93) * mm, "end": v(-72.7, 7.39) * mm});
            skLineSegment(sketch, "E28.11.3", {"start": v(-47.31, 3.36) * mm, "end": v(-49.61, -2.18) * mm});
            skLineSegment(sketch, "E28.12.0", {"start": v(-70, -15) * mm, "end": v(-45, -15) * mm});
            skLineSegment(sketch, "E28.12.1", {"start": v(-70, -21) * mm, "end": v(-45, -21) * mm});
            skLineSegment(sketch, "E28.12.2", {"start": v(-70, -15) * mm, "end": v(-70, -21) * mm});
            skLineSegment(sketch, "E28.12.3", {"start": v(-45, -15) * mm, "end": v(-45, -21) * mm});
            skLineSegment(sketch, "E28.13.0", {"start": v(-58.93, -40.65) * mm, "end": v(-35.83, -31.08) * mm});
            skLineSegment(sketch, "E28.13.1", {"start": v(-56.64, -46.19) * mm, "end": v(-33.54, -36.62) * mm});
            skLineSegment(sketch, "E28.13.2", {"start": v(-58.93, -40.65) * mm, "end": v(-56.64, -46.19) * mm});
            skLineSegment(sketch, "E28.13.3", {"start": v(-35.83, -31.08) * mm, "end": v(-33.54, -36.62) * mm});
            skLineSegment(sketch, "E28.14.0", {"start": v(-38.9, -60.1) * mm, "end": v(-21.21, -42.43) * mm});
            skLineSegment(sketch, "E28.14.1", {"start": v(-34.65, -64.35) * mm, "end": v(-16.97, -46.67) * mm});
            skLineSegment(sketch, "E28.14.2", {"start": v(-38.9, -60.1) * mm, "end": v(-34.65, -64.35) * mm});
            skLineSegment(sketch, "E28.14.3", {"start": v(-21.21, -42.43) * mm, "end": v(-16.97, -46.67) * mm});
            skLineSegment(sketch, "E28.15.0", {"start": v(-12.93, -70.41) * mm, "end": v(-3.36, -47.31) * mm});
            skLineSegment(sketch, "E28.15.1", {"start": v(-7.39, -72.7) * mm, "end": v(2.18, -49.61) * mm});
            skLineSegment(sketch, "E28.15.2", {"start": v(-12.93, -70.41) * mm, "end": v(-7.39, -72.7) * mm});
            skLineSegment(sketch, "E28.15.3", {"start": v(-3.36, -47.31) * mm, "end": v(2.18, -49.61) * mm});
            skPoint(sketch, "E28.center", {"position": v(0, 0) * mm});
            skSolve(sketch);
        }
        {
            var Q1;
            Q1=makeQuery(id+"F22.imprint","IMPRINT",FACE,{"disambiguationData":[TD([[makeQuery(id+"F22.imprint","IMPRINT",EDGE,{"derivedFrom":sQuery(id+"F22.wireOp",EDGE,"E27.bottom")}),1.0]])]});
            var Q2;
            Q2=makeQuery(id+"F3.imprint","IMPRINT",FACE,{"disambiguationData":[TD([[makeQuery(id+"F3.imprint","IMPRINT",EDGE,{"derivedFrom":sQuery(id+"F3.wireOp",EDGE,"E20.8.0")}),-1.0]])]});
            loft(context, id + "F23", {"operationType" : NewBodyOperationType.ADD, "sheetProfilesArray" : [{ "sheetProfileEntities" : qUnion([Q1]) }, { "sheetProfileEntities" : qUnion([Q2]) }]});
        }
        {
            var Q1;
            Q1=makeQuery(id+"F22.imprint","IMPRINT",FACE,{"disambiguationData":[TD([[makeQuery(id+"F22.imprint","IMPRINT",EDGE,{"derivedFrom":sQuery(id+"F22.wireOp",EDGE,"E28.1.0")}),-1.0]])]});
            var Q2;
            Q2=makeQuery(id+"F3.imprint","IMPRINT",FACE,{"disambiguationData":[TD([[makeQuery(id+"F3.imprint","IMPRINT",EDGE,{"derivedFrom":sQuery(id+"F3.wireOp",EDGE,"E20.9.0")}),-1.0]])]});
            loft(context, id + "F24", {"operationType" : NewBodyOperationType.ADD, "sheetProfilesArray" : [{ "sheetProfileEntities" : qUnion([Q1]) }, { "sheetProfileEntities" : qUnion([Q2]) }]});
        }
        {
            var Q1;
            Q1=makeQuery(id+"F22.imprint","IMPRINT",FACE,{"disambiguationData":[TD([[makeQuery(id+"F22.imprint","IMPRINT",EDGE,{"derivedFrom":sQuery(id+"F22.wireOp",EDGE,"E28.2.0")}),-1.0]])]});
            var Q2;
            Q2=makeQuery(id+"F3.imprint","IMPRINT",FACE,{"disambiguationData":[TD([[makeQuery(id+"F3.imprint","IMPRINT",EDGE,{"derivedFrom":sQuery(id+"F3.wireOp",EDGE,"E20.10.0")}),-1.0]])]});
            loft(context, id + "F25", {"operationType" : NewBodyOperationType.ADD, "sheetProfilesArray" : [{ "sheetProfileEntities" : qUnion([Q1]) }, { "sheetProfileEntities" : qUnion([Q2]) }]});
        }
        {
            var Q1;
            Q1=makeQuery(id+"F22.imprint","IMPRINT",FACE,{"disambiguationData":[TD([[makeQuery(id+"F22.imprint","IMPRINT",EDGE,{"derivedFrom":sQuery(id+"F22.wireOp",EDGE,"E28.3.0")}),-1.0]])]});
            var Q2;
            Q2=makeQuery(id+"F3.imprint","IMPRINT",FACE,{"disambiguationData":[TD([[makeQuery(id+"F3.imprint","IMPRINT",EDGE,{"derivedFrom":sQuery(id+"F3.wireOp",EDGE,"E20.11.0")}),-1.0]])]});
            loft(context, id + "F26", {"operationType" : NewBodyOperationType.ADD, "sheetProfilesArray" : [{ "sheetProfileEntities" : qUnion([Q1]) }, { "sheetProfileEntities" : qUnion([Q2]) }]});
        }
        {
            var Q1;
            Q1=makeQuery(id+"F22.imprint","IMPRINT",FACE,{"disambiguationData":[TD([[makeQuery(id+"F22.imprint","IMPRINT",EDGE,{"derivedFrom":sQuery(id+"F22.wireOp",EDGE,"E28.4.0")}),-1.0]])]});
            var Q2;
            Q2=makeQuery(id+"F3.imprint","IMPRINT",FACE,{"disambiguationData":[TD([[makeQuery(id+"F3.imprint","IMPRINT",EDGE,{"derivedFrom":sQuery(id+"F3.wireOp",EDGE,"E20.12.0")}),-1.0]])]});
            loft(context, id + "F27", {"operationType" : NewBodyOperationType.ADD, "sheetProfilesArray" : [{ "sheetProfileEntities" : qUnion([Q1]) }, { "sheetProfileEntities" : qUnion([Q2]) }]});
        }
        {
            var Q1;
            Q1=makeQuery(id+"F22.imprint","IMPRINT",FACE,{"disambiguationData":[TD([[makeQuery(id+"F22.imprint","IMPRINT",EDGE,{"derivedFrom":sQuery(id+"F22.wireOp",EDGE,"E28.5.0")}),-1.0]])]});
            var Q2;
            Q2=makeQuery(id+"F3.imprint","IMPRINT",FACE,{"disambiguationData":[TD([[makeQuery(id+"F3.imprint","IMPRINT",EDGE,{"derivedFrom":sQuery(id+"F3.wireOp",EDGE,"E20.13.0")}),-1.0]])]});
            loft(context, id + "F28", {"operationType" : NewBodyOperationType.ADD, "sheetProfilesArray" : [{ "sheetProfileEntities" : qUnion([Q1]) }, { "sheetProfileEntities" : qUnion([Q2]) }]});
        }
        {
            var Q1;
            Q1=makeQuery(id+"F22.imprint","IMPRINT",FACE,{"disambiguationData":[TD([[makeQuery(id+"F22.imprint","IMPRINT",EDGE,{"derivedFrom":sQuery(id+"F22.wireOp",EDGE,"E28.6.0")}),-1.0]])]});
            var Q2;
            Q2=makeQuery(id+"F3.imprint","IMPRINT",FACE,{"disambiguationData":[TD([[makeQuery(id+"F3.imprint","IMPRINT",EDGE,{"derivedFrom":sQuery(id+"F3.wireOp",EDGE,"E20.14.0")}),-1.0]])]});
            loft(context, id + "F29", {"operationType" : NewBodyOperationType.ADD, "sheetProfilesArray" : [{ "sheetProfileEntities" : qUnion([Q1]) }, { "sheetProfileEntities" : qUnion([Q2]) }]});
        }
        {
            var Q1;
            Q1=makeQuery(id+"F22.imprint","IMPRINT",FACE,{"disambiguationData":[TD([[makeQuery(id+"F22.imprint","IMPRINT",EDGE,{"derivedFrom":sQuery(id+"F22.wireOp",EDGE,"E28.7.0")}),-1.0]])]});
            var Q2;
            Q2=makeQuery(id+"F3.imprint","IMPRINT",FACE,{"disambiguationData":[TD([[makeQuery(id+"F3.imprint","IMPRINT",EDGE,{"derivedFrom":sQuery(id+"F3.wireOp",EDGE,"E20.15.0")}),-1.0]])]});
            loft(context, id + "F30", {"operationType" : NewBodyOperationType.ADD, "sheetProfilesArray" : [{ "sheetProfileEntities" : qUnion([Q1]) }, { "sheetProfileEntities" : qUnion([Q2]) }]});
        }
        {
            var Q1;
            Q1=makeQuery(id+"F22.imprint","IMPRINT",FACE,{"disambiguationData":[TD([[makeQuery(id+"F22.imprint","IMPRINT",EDGE,{"derivedFrom":sQuery(id+"F22.wireOp",EDGE,"E28.8.0")}),-1.0]])]});
            var Q2;
            Q2=makeQuery(id+"F3.imprint","IMPRINT",FACE,{"disambiguationData":[TD([[makeQuery(id+"F3.imprint","IMPRINT",EDGE,{"derivedFrom":sQuery(id+"F3.wireOp",EDGE,"E18.bottom")}),1.0]])]});
            loft(context, id + "F31", {"operationType" : NewBodyOperationType.ADD, "sheetProfilesArray" : [{ "sheetProfileEntities" : qUnion([Q1]) }, { "sheetProfileEntities" : qUnion([Q2]) }]});
        }
        {
            var Q1;
            Q1=makeQuery(id+"F22.imprint","IMPRINT",FACE,{"disambiguationData":[TD([[makeQuery(id+"F22.imprint","IMPRINT",EDGE,{"derivedFrom":sQuery(id+"F22.wireOp",EDGE,"E28.9.0")}),-1.0]])]});
            var Q2;
            Q2=makeQuery(id+"F3.imprint","IMPRINT",FACE,{"disambiguationData":[TD([[makeQuery(id+"F3.imprint","IMPRINT",EDGE,{"derivedFrom":sQuery(id+"F3.wireOp",EDGE,"E20.1.0")}),-1.0]])]});
            loft(context, id + "F32", {"operationType" : NewBodyOperationType.ADD, "sheetProfilesArray" : [{ "sheetProfileEntities" : qUnion([Q1]) }, { "sheetProfileEntities" : qUnion([Q2]) }]});
        }
        {
            var Q1;
            Q1=makeQuery(id+"F22.imprint","IMPRINT",FACE,{"disambiguationData":[TD([[makeQuery(id+"F22.imprint","IMPRINT",EDGE,{"derivedFrom":sQuery(id+"F22.wireOp",EDGE,"E28.10.0")}),-1.0]])]});
            var Q2;
            Q2=makeQuery(id+"F3.imprint","IMPRINT",FACE,{"disambiguationData":[TD([[makeQuery(id+"F3.imprint","IMPRINT",EDGE,{"derivedFrom":sQuery(id+"F3.wireOp",EDGE,"E20.2.0")}),-1.0]])]});
            loft(context, id + "F33", {"operationType" : NewBodyOperationType.ADD, "sheetProfilesArray" : [{ "sheetProfileEntities" : qUnion([Q1]) }, { "sheetProfileEntities" : qUnion([Q2]) }]});
        }
        {
            var Q1;
            Q1=makeQuery(id+"F22.imprint","IMPRINT",FACE,{"disambiguationData":[TD([[makeQuery(id+"F22.imprint","IMPRINT",EDGE,{"derivedFrom":sQuery(id+"F22.wireOp",EDGE,"E28.11.0")}),-1.0]])]});
            var Q2;
            Q2=makeQuery(id+"F3.imprint","IMPRINT",FACE,{"disambiguationData":[TD([[makeQuery(id+"F3.imprint","IMPRINT",EDGE,{"derivedFrom":sQuery(id+"F3.wireOp",EDGE,"E20.3.0")}),-1.0]])]});
            loft(context, id + "F34", {"operationType" : NewBodyOperationType.ADD, "sheetProfilesArray" : [{ "sheetProfileEntities" : qUnion([Q1]) }, { "sheetProfileEntities" : qUnion([Q2]) }]});
        }
        {
            var Q1;
            Q1=makeQuery(id+"F22.imprint","IMPRINT",FACE,{"disambiguationData":[TD([[makeQuery(id+"F22.imprint","IMPRINT",EDGE,{"derivedFrom":sQuery(id+"F22.wireOp",EDGE,"E28.12.0")}),-1.0]])]});
            var Q2;
            Q2=makeQuery(id+"F3.imprint","IMPRINT",FACE,{"disambiguationData":[TD([[makeQuery(id+"F3.imprint","IMPRINT",EDGE,{"derivedFrom":sQuery(id+"F3.wireOp",EDGE,"E20.4.0")}),-1.0]])]});
            loft(context, id + "F35", {"operationType" : NewBodyOperationType.ADD, "sheetProfilesArray" : [{ "sheetProfileEntities" : qUnion([Q1]) }, { "sheetProfileEntities" : qUnion([Q2]) }]});
        }
        {
            var Q1;
            Q1=makeQuery(id+"F22.imprint","IMPRINT",FACE,{"disambiguationData":[TD([[makeQuery(id+"F22.imprint","IMPRINT",EDGE,{"derivedFrom":sQuery(id+"F22.wireOp",EDGE,"E28.13.0")}),-1.0]])]});
            var Q2;
            Q2=makeQuery(id+"F3.imprint","IMPRINT",FACE,{"disambiguationData":[TD([[makeQuery(id+"F3.imprint","IMPRINT",EDGE,{"derivedFrom":sQuery(id+"F3.wireOp",EDGE,"E20.5.0")}),-1.0]])]});
            loft(context, id + "F36", {"operationType" : NewBodyOperationType.ADD, "sheetProfilesArray" : [{ "sheetProfileEntities" : qUnion([Q1]) }, { "sheetProfileEntities" : qUnion([Q2]) }]});
        }
        {
            var Q1;
            Q1=makeQuery(id+"F22.imprint","IMPRINT",FACE,{"disambiguationData":[TD([[makeQuery(id+"F22.imprint","IMPRINT",EDGE,{"derivedFrom":sQuery(id+"F22.wireOp",EDGE,"E28.14.0")}),-1.0]])]});
            var Q2;
            Q2=makeQuery(id+"F3.imprint","IMPRINT",FACE,{"disambiguationData":[TD([[makeQuery(id+"F3.imprint","IMPRINT",EDGE,{"derivedFrom":sQuery(id+"F3.wireOp",EDGE,"E20.6.0")}),-1.0]])]});
            loft(context, id + "F37", {"operationType" : NewBodyOperationType.ADD, "sheetProfilesArray" : [{ "sheetProfileEntities" : qUnion([Q1]) }, { "sheetProfileEntities" : qUnion([Q2]) }]});
        }
        {
            var Q1;
            Q1=makeQuery(id+"F22.imprint","IMPRINT",FACE,{"disambiguationData":[TD([[makeQuery(id+"F22.imprint","IMPRINT",EDGE,{"derivedFrom":sQuery(id+"F22.wireOp",EDGE,"E28.15.0")}),-1.0]])]});
            var Q2;
            Q2=makeQuery(id+"F3.imprint","IMPRINT",FACE,{"disambiguationData":[TD([[makeQuery(id+"F3.imprint","IMPRINT",EDGE,{"derivedFrom":sQuery(id+"F3.wireOp",EDGE,"E20.7.0")}),-1.0]])]});
            loft(context, id + "F38", {"operationType" : NewBodyOperationType.ADD, "sheetProfilesArray" : [{ "sheetProfileEntities" : qUnion([Q1]) }, { "sheetProfileEntities" : qUnion([Q2]) }]});
        }
        {
            var Q0;
            Q0=qCreatedBy(makeId("Top.planeOp"),FACE);
            var sketch = newSketch(context, id + "F39", { "sketchPlane" : qUnion([Q0])});
            skCircle(sketch, "E29", {"center": v(0, 0) * mm, "radius": 57.35 * mm});
            skCircle(sketch, "E30", {"center": v(0, 0) * mm, "radius": 67.35 * mm});
            skSolve(sketch);
        }
        {
            var Q0;
            Q0=makeQuery(id+"F39.imprint","IMPRINT",FACE,{"disambiguationData":[TD([[makeQuery(id+"F39.imprint","IMPRINT",EDGE,{"derivedFrom":sQuery(id+"F39.wireOp",EDGE,"E29")}),-1.0]])]});
            extrude(context, id + "F40", {"entities" : qUnion([Q0]), "operationType" : NewBodyOperationType.ADD, "endBound" : BoundingType.SYMMETRIC, "depth" : 6 * mm});
        }
        {
            var Q0;
            Q0=qCreatedBy(makeId("Right.planeOp"),FACE);
            var sketch = newSketch(context, id + "F41", { "sketchPlane" : qUnion([Q0])});
            skLineSegment(sketch, "E31", {"start": v(0, 27) * mm, "end": v(0, -27) * mm, "construction": true});
            skCircle(sketch, "E32", {"center": v(0, 0) * mm, "radius": 64 * mm});
            skCircle(sketch, "E33", {"center": v(0, 0) * mm, "radius": 85 * mm});
            skLineSegment(sketch, "E34", {"start": v(0, 85) * mm, "end": v(0, -85) * mm});
            skLineSegment(sketch, "E35", {"start": v(63.36, 9) * mm, "end": v(61.93, 3) * mm});
            skLineSegment(sketch, "E36", {"start": v(61.93, 3) * mm, "end": v(63.93, 3) * mm});
            skLineSegment(sketch, "E37", {"start": v(63.93, -3) * mm, "end": v(61.93, -3) * mm});
            skLineSegment(sketch, "E38", {"start": v(61.93, -3) * mm, "end": v(63.36, -9) * mm});
            skSolve(sketch);
        }
        {
            var Q0;
            {var subQ0=sQuery(id+"F41.wireOp",EDGE,"E34");var subQ1=sQuery(id+"F41.wireOp",EDGE,"E32");var subQ2=makeQuery(id+"F41.imprint","INTERSECT",VERTEX,{"disambiguationData":[OD(0.0)],"derivedFrom":[subQ1,subQ0]});Q0=makeQuery(id+"F41.imprint","IMPRINT",FACE,{"disambiguationData":[TD([[makeQuery(id+"F41.imprint","IMPRINT",EDGE,{"disambiguationData":[TD([[subQ2,-1.0]])],"derivedFrom":subQ1}),-1.0]])]});}
            var Q1;
            {var subQ0=sQuery(id+"F41.wireOp",EDGE,"E37");Q1=makeQuery(id+"F41.imprint","IMPRINT",FACE,{"disambiguationData":[TD([[makeQuery(id+"F41.imprint","IMPRINT",EDGE,{"derivedFrom":subQ0}),1.0]])]});}
            var Q2;
            {var subQ0=sQuery(id+"F41.wireOp",EDGE,"E35");Q2=makeQuery(id+"F41.imprint","IMPRINT",FACE,{"disambiguationData":[TD([[makeQuery(id+"F41.imprint","IMPRINT",EDGE,{"derivedFrom":subQ0}),1.0]])]});}
            var Q3;
            Q3=sQuery(id+"F41.wireOp",EDGE,"E31");
            revolve(context, id + "F42", {"operationType" : NewBodyOperationType.REMOVE, "entities" : qUnion([Q0, Q1, Q2]), "axis" : qUnion([Q3]), "revolveType" : RevolveType.FULL, "oppositeDirection" : true});
        }
        {
            var Q0;
            Q0=makeQuery(id+"F42.boolean.opBoolean","INTERSECT",EDGE,{"disambiguationData":[OD(5.0)],"derivedFrom":[makeQuery(id+"F20.boolean.opBoolean","MERGE",FACE,{"derivedFrom":[makeQuery(id+"F19.boolean.opBoolean","MERGE",FACE,{"derivedFrom":[makeQuery(id+"F18.boolean.opBoolean","MERGE",FACE,{"derivedFrom":[makeQuery(id+"F17.boolean.opBoolean","MERGE",FACE,{"derivedFrom":[makeQuery(id+"F16.boolean.opBoolean","MERGE",FACE,{"derivedFrom":[makeQuery(id+"F15.boolean.opBoolean","MERGE",FACE,{"derivedFrom":[makeQuery(id+"F14.boolean.opBoolean","MERGE",FACE,{"derivedFrom":[makeQuery(id+"F13.boolean.opBoolean","MERGE",FACE,{"derivedFrom":[makeQuery(id+"F12.boolean.opBoolean","MERGE",FACE,{"derivedFrom":[makeQuery(id+"F11.boolean.opBoolean","MERGE",FACE,{"derivedFrom":[makeQuery(id+"F10.boolean.opBoolean","MERGE",FACE,{"derivedFrom":[makeQuery(id+"F9.boolean.opBoolean","MERGE",FACE,{"derivedFrom":[makeQuery(id+"F8.boolean.opBoolean","MERGE",FACE,{"derivedFrom":[makeQuery(id+"F7.boolean.opBoolean","MERGE",FACE,{"derivedFrom":[makeQuery(id+"F6.boolean.opBoolean","MERGE",FACE,{"derivedFrom":[makeQuery(id+"F5.boolean.opBoolean","MERGE",FACE,{"derivedFrom":[makeQuery(id+"F1.opRevolve","SWEPT_FACE",FACE,{"disambiguationData":[OSD([sQuery(id+"F0.wireOp",EDGE,"E14")])]}),makeQuery(id+"F5.opLoft","CAP_FACE",FACE,{"disambiguationData":[OSD([makeQuery(id+"F4.imprint","IMPRINT",FACE,{"disambiguationData":[TD([[makeQuery(id+"F4.imprint","IMPRINT",EDGE,{"derivedFrom":sQuery(id+"F4.wireOp",EDGE,"E21")}),1.0]])]})])],"isStart":true})]}),makeQuery(id+"F6.opLoft","CAP_FACE",FACE,{"disambiguationData":[OSD([makeQuery(id+"F4.imprint","IMPRINT",FACE,{"disambiguationData":[TD([[makeQuery(id+"F4.imprint","IMPRINT",EDGE,{"derivedFrom":sQuery(id+"F4.wireOp",EDGE,"E26.15.0")}),1.0]])]})])],"isStart":true})]}),makeQuery(id+"F7.opLoft","CAP_FACE",FACE,{"disambiguationData":[OSD([makeQuery(id+"F4.imprint","IMPRINT",FACE,{"disambiguationData":[TD([[makeQuery(id+"F4.imprint","IMPRINT",EDGE,{"derivedFrom":sQuery(id+"F4.wireOp",EDGE,"E26.14.0")}),1.0]])]})])],"isStart":true})]}),makeQuery(id+"F8.opLoft","CAP_FACE",FACE,{"disambiguationData":[OSD([makeQuery(id+"F4.imprint","IMPRINT",FACE,{"disambiguationData":[TD([[makeQuery(id+"F4.imprint","IMPRINT",EDGE,{"derivedFrom":sQuery(id+"F4.wireOp",EDGE,"E26.13.0")}),1.0]])]})])],"isStart":true})]}),makeQuery(id+"F9.opLoft","CAP_FACE",FACE,{"disambiguationData":[OSD([makeQuery(id+"F4.imprint","IMPRINT",FACE,{"disambiguationData":[TD([[makeQuery(id+"F4.imprint","IMPRINT",EDGE,{"derivedFrom":sQuery(id+"F4.wireOp",EDGE,"E26.12.0")}),1.0]])]})])],"isStart":true})]}),makeQuery(id+"F10.opLoft","CAP_FACE",FACE,{"disambiguationData":[OSD([makeQuery(id+"F4.imprint","IMPRINT",FACE,{"disambiguationData":[TD([[makeQuery(id+"F4.imprint","IMPRINT",EDGE,{"derivedFrom":sQuery(id+"F4.wireOp",EDGE,"E26.11.0")}),1.0]])]})])],"isStart":true})]}),makeQuery(id+"F11.opLoft","CAP_FACE",FACE,{"disambiguationData":[OSD([makeQuery(id+"F4.imprint","IMPRINT",FACE,{"disambiguationData":[TD([[makeQuery(id+"F4.imprint","IMPRINT",EDGE,{"derivedFrom":sQuery(id+"F4.wireOp",EDGE,"E26.10.0")}),1.0]])]})])],"isStart":true})]}),makeQuery(id+"F12.opLoft","CAP_FACE",FACE,{"disambiguationData":[OSD([makeQuery(id+"F4.imprint","IMPRINT",FACE,{"disambiguationData":[TD([[makeQuery(id+"F4.imprint","IMPRINT",EDGE,{"derivedFrom":sQuery(id+"F4.wireOp",EDGE,"E26.9.0")}),1.0]])]})])],"isStart":true})]}),makeQuery(id+"F13.opLoft","CAP_FACE",FACE,{"disambiguationData":[OSD([makeQuery(id+"F4.imprint","IMPRINT",FACE,{"disambiguationData":[TD([[makeQuery(id+"F4.imprint","IMPRINT",EDGE,{"derivedFrom":sQuery(id+"F4.wireOp",EDGE,"E26.8.0")}),1.0]])]})])],"isStart":true})]}),makeQuery(id+"F14.opLoft","CAP_FACE",FACE,{"disambiguationData":[OSD([makeQuery(id+"F4.imprint","IMPRINT",FACE,{"disambiguationData":[TD([[makeQuery(id+"F4.imprint","IMPRINT",EDGE,{"derivedFrom":sQuery(id+"F4.wireOp",EDGE,"E26.7.0")}),1.0]])]})])],"isStart":true})]}),makeQuery(id+"F15.opLoft","CAP_FACE",FACE,{"disambiguationData":[OSD([makeQuery(id+"F4.imprint","IMPRINT",FACE,{"disambiguationData":[TD([[makeQuery(id+"F4.imprint","IMPRINT",EDGE,{"derivedFrom":sQuery(id+"F4.wireOp",EDGE,"E26.6.0")}),1.0]])]})])],"isStart":true})]}),makeQuery(id+"F16.opLoft","CAP_FACE",FACE,{"disambiguationData":[OSD([makeQuery(id+"F4.imprint","IMPRINT",FACE,{"disambiguationData":[TD([[makeQuery(id+"F4.imprint","IMPRINT",EDGE,{"derivedFrom":sQuery(id+"F4.wireOp",EDGE,"E26.5.0")}),1.0]])]})])],"isStart":true})]}),makeQuery(id+"F17.opLoft","CAP_FACE",FACE,{"disambiguationData":[OSD([makeQuery(id+"F4.imprint","IMPRINT",FACE,{"disambiguationData":[TD([[makeQuery(id+"F4.imprint","IMPRINT",EDGE,{"derivedFrom":sQuery(id+"F4.wireOp",EDGE,"E26.4.0")}),1.0]])]})])],"isStart":true})]}),makeQuery(id+"F18.opLoft","CAP_FACE",FACE,{"disambiguationData":[OSD([makeQuery(id+"F4.imprint","IMPRINT",FACE,{"disambiguationData":[TD([[makeQuery(id+"F4.imprint","IMPRINT",EDGE,{"derivedFrom":sQuery(id+"F4.wireOp",EDGE,"E26.3.0")}),1.0]])]})])],"isStart":true})]}),makeQuery(id+"F19.opLoft","CAP_FACE",FACE,{"disambiguationData":[OSD([makeQuery(id+"F4.imprint","IMPRINT",FACE,{"disambiguationData":[TD([[makeQuery(id+"F4.imprint","IMPRINT",EDGE,{"derivedFrom":sQuery(id+"F4.wireOp",EDGE,"E26.2.0")}),1.0]])]})])],"isStart":true})]}),makeQuery(id+"F20.opLoft","CAP_FACE",FACE,{"disambiguationData":[OSD([makeQuery(id+"F4.imprint","IMPRINT",FACE,{"disambiguationData":[TD([[makeQuery(id+"F4.imprint","IMPRINT",EDGE,{"derivedFrom":sQuery(id+"F4.wireOp",EDGE,"E26.1.0")}),1.0]])]})])],"isStart":true})]}),makeQuery(id+"F42.opRevolve","SWEPT_FACE",FACE,{"disambiguationData":[OSD([sQuery(id+"F41.wireOp",EDGE,"E32")])]})]});
            var Q1;
            Q1=makeQuery(id+"F42.boolean.opBoolean","INTERSECT",EDGE,{"disambiguationData":[OD(4.0)],"derivedFrom":[makeQuery(id+"F20.boolean.opBoolean","MERGE",FACE,{"derivedFrom":[makeQuery(id+"F19.boolean.opBoolean","MERGE",FACE,{"derivedFrom":[makeQuery(id+"F18.boolean.opBoolean","MERGE",FACE,{"derivedFrom":[makeQuery(id+"F17.boolean.opBoolean","MERGE",FACE,{"derivedFrom":[makeQuery(id+"F16.boolean.opBoolean","MERGE",FACE,{"derivedFrom":[makeQuery(id+"F15.boolean.opBoolean","MERGE",FACE,{"derivedFrom":[makeQuery(id+"F14.boolean.opBoolean","MERGE",FACE,{"derivedFrom":[makeQuery(id+"F13.boolean.opBoolean","MERGE",FACE,{"derivedFrom":[makeQuery(id+"F12.boolean.opBoolean","MERGE",FACE,{"derivedFrom":[makeQuery(id+"F11.boolean.opBoolean","MERGE",FACE,{"derivedFrom":[makeQuery(id+"F10.boolean.opBoolean","MERGE",FACE,{"derivedFrom":[makeQuery(id+"F9.boolean.opBoolean","MERGE",FACE,{"derivedFrom":[makeQuery(id+"F8.boolean.opBoolean","MERGE",FACE,{"derivedFrom":[makeQuery(id+"F7.boolean.opBoolean","MERGE",FACE,{"derivedFrom":[makeQuery(id+"F6.boolean.opBoolean","MERGE",FACE,{"derivedFrom":[makeQuery(id+"F5.boolean.opBoolean","MERGE",FACE,{"derivedFrom":[makeQuery(id+"F1.opRevolve","SWEPT_FACE",FACE,{"disambiguationData":[OSD([sQuery(id+"F0.wireOp",EDGE,"E14")])]}),makeQuery(id+"F5.opLoft","CAP_FACE",FACE,{"disambiguationData":[OSD([makeQuery(id+"F4.imprint","IMPRINT",FACE,{"disambiguationData":[TD([[makeQuery(id+"F4.imprint","IMPRINT",EDGE,{"derivedFrom":sQuery(id+"F4.wireOp",EDGE,"E21")}),1.0]])]})])],"isStart":true})]}),makeQuery(id+"F6.opLoft","CAP_FACE",FACE,{"disambiguationData":[OSD([makeQuery(id+"F4.imprint","IMPRINT",FACE,{"disambiguationData":[TD([[makeQuery(id+"F4.imprint","IMPRINT",EDGE,{"derivedFrom":sQuery(id+"F4.wireOp",EDGE,"E26.15.0")}),1.0]])]})])],"isStart":true})]}),makeQuery(id+"F7.opLoft","CAP_FACE",FACE,{"disambiguationData":[OSD([makeQuery(id+"F4.imprint","IMPRINT",FACE,{"disambiguationData":[TD([[makeQuery(id+"F4.imprint","IMPRINT",EDGE,{"derivedFrom":sQuery(id+"F4.wireOp",EDGE,"E26.14.0")}),1.0]])]})])],"isStart":true})]}),makeQuery(id+"F8.opLoft","CAP_FACE",FACE,{"disambiguationData":[OSD([makeQuery(id+"F4.imprint","IMPRINT",FACE,{"disambiguationData":[TD([[makeQuery(id+"F4.imprint","IMPRINT",EDGE,{"derivedFrom":sQuery(id+"F4.wireOp",EDGE,"E26.13.0")}),1.0]])]})])],"isStart":true})]}),makeQuery(id+"F9.opLoft","CAP_FACE",FACE,{"disambiguationData":[OSD([makeQuery(id+"F4.imprint","IMPRINT",FACE,{"disambiguationData":[TD([[makeQuery(id+"F4.imprint","IMPRINT",EDGE,{"derivedFrom":sQuery(id+"F4.wireOp",EDGE,"E26.12.0")}),1.0]])]})])],"isStart":true})]}),makeQuery(id+"F10.opLoft","CAP_FACE",FACE,{"disambiguationData":[OSD([makeQuery(id+"F4.imprint","IMPRINT",FACE,{"disambiguationData":[TD([[makeQuery(id+"F4.imprint","IMPRINT",EDGE,{"derivedFrom":sQuery(id+"F4.wireOp",EDGE,"E26.11.0")}),1.0]])]})])],"isStart":true})]}),makeQuery(id+"F11.opLoft","CAP_FACE",FACE,{"disambiguationData":[OSD([makeQuery(id+"F4.imprint","IMPRINT",FACE,{"disambiguationData":[TD([[makeQuery(id+"F4.imprint","IMPRINT",EDGE,{"derivedFrom":sQuery(id+"F4.wireOp",EDGE,"E26.10.0")}),1.0]])]})])],"isStart":true})]}),makeQuery(id+"F12.opLoft","CAP_FACE",FACE,{"disambiguationData":[OSD([makeQuery(id+"F4.imprint","IMPRINT",FACE,{"disambiguationData":[TD([[makeQuery(id+"F4.imprint","IMPRINT",EDGE,{"derivedFrom":sQuery(id+"F4.wireOp",EDGE,"E26.9.0")}),1.0]])]})])],"isStart":true})]}),makeQuery(id+"F13.opLoft","CAP_FACE",FACE,{"disambiguationData":[OSD([makeQuery(id+"F4.imprint","IMPRINT",FACE,{"disambiguationData":[TD([[makeQuery(id+"F4.imprint","IMPRINT",EDGE,{"derivedFrom":sQuery(id+"F4.wireOp",EDGE,"E26.8.0")}),1.0]])]})])],"isStart":true})]}),makeQuery(id+"F14.opLoft","CAP_FACE",FACE,{"disambiguationData":[OSD([makeQuery(id+"F4.imprint","IMPRINT",FACE,{"disambiguationData":[TD([[makeQuery(id+"F4.imprint","IMPRINT",EDGE,{"derivedFrom":sQuery(id+"F4.wireOp",EDGE,"E26.7.0")}),1.0]])]})])],"isStart":true})]}),makeQuery(id+"F15.opLoft","CAP_FACE",FACE,{"disambiguationData":[OSD([makeQuery(id+"F4.imprint","IMPRINT",FACE,{"disambiguationData":[TD([[makeQuery(id+"F4.imprint","IMPRINT",EDGE,{"derivedFrom":sQuery(id+"F4.wireOp",EDGE,"E26.6.0")}),1.0]])]})])],"isStart":true})]}),makeQuery(id+"F16.opLoft","CAP_FACE",FACE,{"disambiguationData":[OSD([makeQuery(id+"F4.imprint","IMPRINT",FACE,{"disambiguationData":[TD([[makeQuery(id+"F4.imprint","IMPRINT",EDGE,{"derivedFrom":sQuery(id+"F4.wireOp",EDGE,"E26.5.0")}),1.0]])]})])],"isStart":true})]}),makeQuery(id+"F17.opLoft","CAP_FACE",FACE,{"disambiguationData":[OSD([makeQuery(id+"F4.imprint","IMPRINT",FACE,{"disambiguationData":[TD([[makeQuery(id+"F4.imprint","IMPRINT",EDGE,{"derivedFrom":sQuery(id+"F4.wireOp",EDGE,"E26.4.0")}),1.0]])]})])],"isStart":true})]}),makeQuery(id+"F18.opLoft","CAP_FACE",FACE,{"disambiguationData":[OSD([makeQuery(id+"F4.imprint","IMPRINT",FACE,{"disambiguationData":[TD([[makeQuery(id+"F4.imprint","IMPRINT",EDGE,{"derivedFrom":sQuery(id+"F4.wireOp",EDGE,"E26.3.0")}),1.0]])]})])],"isStart":true})]}),makeQuery(id+"F19.opLoft","CAP_FACE",FACE,{"disambiguationData":[OSD([makeQuery(id+"F4.imprint","IMPRINT",FACE,{"disambiguationData":[TD([[makeQuery(id+"F4.imprint","IMPRINT",EDGE,{"derivedFrom":sQuery(id+"F4.wireOp",EDGE,"E26.2.0")}),1.0]])]})])],"isStart":true})]}),makeQuery(id+"F20.opLoft","CAP_FACE",FACE,{"disambiguationData":[OSD([makeQuery(id+"F4.imprint","IMPRINT",FACE,{"disambiguationData":[TD([[makeQuery(id+"F4.imprint","IMPRINT",EDGE,{"derivedFrom":sQuery(id+"F4.wireOp",EDGE,"E26.1.0")}),1.0]])]})])],"isStart":true})]}),makeQuery(id+"F42.opRevolve","SWEPT_FACE",FACE,{"disambiguationData":[OSD([sQuery(id+"F41.wireOp",EDGE,"E32")])]})]});
            var Q2;
            Q2=makeQuery(id+"F42.boolean.opBoolean","INTERSECT",EDGE,{"disambiguationData":[OD(3.0)],"derivedFrom":[makeQuery(id+"F20.boolean.opBoolean","MERGE",FACE,{"derivedFrom":[makeQuery(id+"F19.boolean.opBoolean","MERGE",FACE,{"derivedFrom":[makeQuery(id+"F18.boolean.opBoolean","MERGE",FACE,{"derivedFrom":[makeQuery(id+"F17.boolean.opBoolean","MERGE",FACE,{"derivedFrom":[makeQuery(id+"F16.boolean.opBoolean","MERGE",FACE,{"derivedFrom":[makeQuery(id+"F15.boolean.opBoolean","MERGE",FACE,{"derivedFrom":[makeQuery(id+"F14.boolean.opBoolean","MERGE",FACE,{"derivedFrom":[makeQuery(id+"F13.boolean.opBoolean","MERGE",FACE,{"derivedFrom":[makeQuery(id+"F12.boolean.opBoolean","MERGE",FACE,{"derivedFrom":[makeQuery(id+"F11.boolean.opBoolean","MERGE",FACE,{"derivedFrom":[makeQuery(id+"F10.boolean.opBoolean","MERGE",FACE,{"derivedFrom":[makeQuery(id+"F9.boolean.opBoolean","MERGE",FACE,{"derivedFrom":[makeQuery(id+"F8.boolean.opBoolean","MERGE",FACE,{"derivedFrom":[makeQuery(id+"F7.boolean.opBoolean","MERGE",FACE,{"derivedFrom":[makeQuery(id+"F6.boolean.opBoolean","MERGE",FACE,{"derivedFrom":[makeQuery(id+"F5.boolean.opBoolean","MERGE",FACE,{"derivedFrom":[makeQuery(id+"F1.opRevolve","SWEPT_FACE",FACE,{"disambiguationData":[OSD([sQuery(id+"F0.wireOp",EDGE,"E14")])]}),makeQuery(id+"F5.opLoft","CAP_FACE",FACE,{"disambiguationData":[OSD([makeQuery(id+"F4.imprint","IMPRINT",FACE,{"disambiguationData":[TD([[makeQuery(id+"F4.imprint","IMPRINT",EDGE,{"derivedFrom":sQuery(id+"F4.wireOp",EDGE,"E21")}),1.0]])]})])],"isStart":true})]}),makeQuery(id+"F6.opLoft","CAP_FACE",FACE,{"disambiguationData":[OSD([makeQuery(id+"F4.imprint","IMPRINT",FACE,{"disambiguationData":[TD([[makeQuery(id+"F4.imprint","IMPRINT",EDGE,{"derivedFrom":sQuery(id+"F4.wireOp",EDGE,"E26.15.0")}),1.0]])]})])],"isStart":true})]}),makeQuery(id+"F7.opLoft","CAP_FACE",FACE,{"disambiguationData":[OSD([makeQuery(id+"F4.imprint","IMPRINT",FACE,{"disambiguationData":[TD([[makeQuery(id+"F4.imprint","IMPRINT",EDGE,{"derivedFrom":sQuery(id+"F4.wireOp",EDGE,"E26.14.0")}),1.0]])]})])],"isStart":true})]}),makeQuery(id+"F8.opLoft","CAP_FACE",FACE,{"disambiguationData":[OSD([makeQuery(id+"F4.imprint","IMPRINT",FACE,{"disambiguationData":[TD([[makeQuery(id+"F4.imprint","IMPRINT",EDGE,{"derivedFrom":sQuery(id+"F4.wireOp",EDGE,"E26.13.0")}),1.0]])]})])],"isStart":true})]}),makeQuery(id+"F9.opLoft","CAP_FACE",FACE,{"disambiguationData":[OSD([makeQuery(id+"F4.imprint","IMPRINT",FACE,{"disambiguationData":[TD([[makeQuery(id+"F4.imprint","IMPRINT",EDGE,{"derivedFrom":sQuery(id+"F4.wireOp",EDGE,"E26.12.0")}),1.0]])]})])],"isStart":true})]}),makeQuery(id+"F10.opLoft","CAP_FACE",FACE,{"disambiguationData":[OSD([makeQuery(id+"F4.imprint","IMPRINT",FACE,{"disambiguationData":[TD([[makeQuery(id+"F4.imprint","IMPRINT",EDGE,{"derivedFrom":sQuery(id+"F4.wireOp",EDGE,"E26.11.0")}),1.0]])]})])],"isStart":true})]}),makeQuery(id+"F11.opLoft","CAP_FACE",FACE,{"disambiguationData":[OSD([makeQuery(id+"F4.imprint","IMPRINT",FACE,{"disambiguationData":[TD([[makeQuery(id+"F4.imprint","IMPRINT",EDGE,{"derivedFrom":sQuery(id+"F4.wireOp",EDGE,"E26.10.0")}),1.0]])]})])],"isStart":true})]}),makeQuery(id+"F12.opLoft","CAP_FACE",FACE,{"disambiguationData":[OSD([makeQuery(id+"F4.imprint","IMPRINT",FACE,{"disambiguationData":[TD([[makeQuery(id+"F4.imprint","IMPRINT",EDGE,{"derivedFrom":sQuery(id+"F4.wireOp",EDGE,"E26.9.0")}),1.0]])]})])],"isStart":true})]}),makeQuery(id+"F13.opLoft","CAP_FACE",FACE,{"disambiguationData":[OSD([makeQuery(id+"F4.imprint","IMPRINT",FACE,{"disambiguationData":[TD([[makeQuery(id+"F4.imprint","IMPRINT",EDGE,{"derivedFrom":sQuery(id+"F4.wireOp",EDGE,"E26.8.0")}),1.0]])]})])],"isStart":true})]}),makeQuery(id+"F14.opLoft","CAP_FACE",FACE,{"disambiguationData":[OSD([makeQuery(id+"F4.imprint","IMPRINT",FACE,{"disambiguationData":[TD([[makeQuery(id+"F4.imprint","IMPRINT",EDGE,{"derivedFrom":sQuery(id+"F4.wireOp",EDGE,"E26.7.0")}),1.0]])]})])],"isStart":true})]}),makeQuery(id+"F15.opLoft","CAP_FACE",FACE,{"disambiguationData":[OSD([makeQuery(id+"F4.imprint","IMPRINT",FACE,{"disambiguationData":[TD([[makeQuery(id+"F4.imprint","IMPRINT",EDGE,{"derivedFrom":sQuery(id+"F4.wireOp",EDGE,"E26.6.0")}),1.0]])]})])],"isStart":true})]}),makeQuery(id+"F16.opLoft","CAP_FACE",FACE,{"disambiguationData":[OSD([makeQuery(id+"F4.imprint","IMPRINT",FACE,{"disambiguationData":[TD([[makeQuery(id+"F4.imprint","IMPRINT",EDGE,{"derivedFrom":sQuery(id+"F4.wireOp",EDGE,"E26.5.0")}),1.0]])]})])],"isStart":true})]}),makeQuery(id+"F17.opLoft","CAP_FACE",FACE,{"disambiguationData":[OSD([makeQuery(id+"F4.imprint","IMPRINT",FACE,{"disambiguationData":[TD([[makeQuery(id+"F4.imprint","IMPRINT",EDGE,{"derivedFrom":sQuery(id+"F4.wireOp",EDGE,"E26.4.0")}),1.0]])]})])],"isStart":true})]}),makeQuery(id+"F18.opLoft","CAP_FACE",FACE,{"disambiguationData":[OSD([makeQuery(id+"F4.imprint","IMPRINT",FACE,{"disambiguationData":[TD([[makeQuery(id+"F4.imprint","IMPRINT",EDGE,{"derivedFrom":sQuery(id+"F4.wireOp",EDGE,"E26.3.0")}),1.0]])]})])],"isStart":true})]}),makeQuery(id+"F19.opLoft","CAP_FACE",FACE,{"disambiguationData":[OSD([makeQuery(id+"F4.imprint","IMPRINT",FACE,{"disambiguationData":[TD([[makeQuery(id+"F4.imprint","IMPRINT",EDGE,{"derivedFrom":sQuery(id+"F4.wireOp",EDGE,"E26.2.0")}),1.0]])]})])],"isStart":true})]}),makeQuery(id+"F20.opLoft","CAP_FACE",FACE,{"disambiguationData":[OSD([makeQuery(id+"F4.imprint","IMPRINT",FACE,{"disambiguationData":[TD([[makeQuery(id+"F4.imprint","IMPRINT",EDGE,{"derivedFrom":sQuery(id+"F4.wireOp",EDGE,"E26.1.0")}),1.0]])]})])],"isStart":true})]}),makeQuery(id+"F42.opRevolve","SWEPT_FACE",FACE,{"disambiguationData":[OSD([sQuery(id+"F41.wireOp",EDGE,"E32")])]})]});
            var Q3;
            Q3=makeQuery(id+"F42.boolean.opBoolean","INTERSECT",EDGE,{"disambiguationData":[OD(2.0)],"derivedFrom":[makeQuery(id+"F20.boolean.opBoolean","MERGE",FACE,{"derivedFrom":[makeQuery(id+"F19.boolean.opBoolean","MERGE",FACE,{"derivedFrom":[makeQuery(id+"F18.boolean.opBoolean","MERGE",FACE,{"derivedFrom":[makeQuery(id+"F17.boolean.opBoolean","MERGE",FACE,{"derivedFrom":[makeQuery(id+"F16.boolean.opBoolean","MERGE",FACE,{"derivedFrom":[makeQuery(id+"F15.boolean.opBoolean","MERGE",FACE,{"derivedFrom":[makeQuery(id+"F14.boolean.opBoolean","MERGE",FACE,{"derivedFrom":[makeQuery(id+"F13.boolean.opBoolean","MERGE",FACE,{"derivedFrom":[makeQuery(id+"F12.boolean.opBoolean","MERGE",FACE,{"derivedFrom":[makeQuery(id+"F11.boolean.opBoolean","MERGE",FACE,{"derivedFrom":[makeQuery(id+"F10.boolean.opBoolean","MERGE",FACE,{"derivedFrom":[makeQuery(id+"F9.boolean.opBoolean","MERGE",FACE,{"derivedFrom":[makeQuery(id+"F8.boolean.opBoolean","MERGE",FACE,{"derivedFrom":[makeQuery(id+"F7.boolean.opBoolean","MERGE",FACE,{"derivedFrom":[makeQuery(id+"F6.boolean.opBoolean","MERGE",FACE,{"derivedFrom":[makeQuery(id+"F5.boolean.opBoolean","MERGE",FACE,{"derivedFrom":[makeQuery(id+"F1.opRevolve","SWEPT_FACE",FACE,{"disambiguationData":[OSD([sQuery(id+"F0.wireOp",EDGE,"E14")])]}),makeQuery(id+"F5.opLoft","CAP_FACE",FACE,{"disambiguationData":[OSD([makeQuery(id+"F4.imprint","IMPRINT",FACE,{"disambiguationData":[TD([[makeQuery(id+"F4.imprint","IMPRINT",EDGE,{"derivedFrom":sQuery(id+"F4.wireOp",EDGE,"E21")}),1.0]])]})])],"isStart":true})]}),makeQuery(id+"F6.opLoft","CAP_FACE",FACE,{"disambiguationData":[OSD([makeQuery(id+"F4.imprint","IMPRINT",FACE,{"disambiguationData":[TD([[makeQuery(id+"F4.imprint","IMPRINT",EDGE,{"derivedFrom":sQuery(id+"F4.wireOp",EDGE,"E26.15.0")}),1.0]])]})])],"isStart":true})]}),makeQuery(id+"F7.opLoft","CAP_FACE",FACE,{"disambiguationData":[OSD([makeQuery(id+"F4.imprint","IMPRINT",FACE,{"disambiguationData":[TD([[makeQuery(id+"F4.imprint","IMPRINT",EDGE,{"derivedFrom":sQuery(id+"F4.wireOp",EDGE,"E26.14.0")}),1.0]])]})])],"isStart":true})]}),makeQuery(id+"F8.opLoft","CAP_FACE",FACE,{"disambiguationData":[OSD([makeQuery(id+"F4.imprint","IMPRINT",FACE,{"disambiguationData":[TD([[makeQuery(id+"F4.imprint","IMPRINT",EDGE,{"derivedFrom":sQuery(id+"F4.wireOp",EDGE,"E26.13.0")}),1.0]])]})])],"isStart":true})]}),makeQuery(id+"F9.opLoft","CAP_FACE",FACE,{"disambiguationData":[OSD([makeQuery(id+"F4.imprint","IMPRINT",FACE,{"disambiguationData":[TD([[makeQuery(id+"F4.imprint","IMPRINT",EDGE,{"derivedFrom":sQuery(id+"F4.wireOp",EDGE,"E26.12.0")}),1.0]])]})])],"isStart":true})]}),makeQuery(id+"F10.opLoft","CAP_FACE",FACE,{"disambiguationData":[OSD([makeQuery(id+"F4.imprint","IMPRINT",FACE,{"disambiguationData":[TD([[makeQuery(id+"F4.imprint","IMPRINT",EDGE,{"derivedFrom":sQuery(id+"F4.wireOp",EDGE,"E26.11.0")}),1.0]])]})])],"isStart":true})]}),makeQuery(id+"F11.opLoft","CAP_FACE",FACE,{"disambiguationData":[OSD([makeQuery(id+"F4.imprint","IMPRINT",FACE,{"disambiguationData":[TD([[makeQuery(id+"F4.imprint","IMPRINT",EDGE,{"derivedFrom":sQuery(id+"F4.wireOp",EDGE,"E26.10.0")}),1.0]])]})])],"isStart":true})]}),makeQuery(id+"F12.opLoft","CAP_FACE",FACE,{"disambiguationData":[OSD([makeQuery(id+"F4.imprint","IMPRINT",FACE,{"disambiguationData":[TD([[makeQuery(id+"F4.imprint","IMPRINT",EDGE,{"derivedFrom":sQuery(id+"F4.wireOp",EDGE,"E26.9.0")}),1.0]])]})])],"isStart":true})]}),makeQuery(id+"F13.opLoft","CAP_FACE",FACE,{"disambiguationData":[OSD([makeQuery(id+"F4.imprint","IMPRINT",FACE,{"disambiguationData":[TD([[makeQuery(id+"F4.imprint","IMPRINT",EDGE,{"derivedFrom":sQuery(id+"F4.wireOp",EDGE,"E26.8.0")}),1.0]])]})])],"isStart":true})]}),makeQuery(id+"F14.opLoft","CAP_FACE",FACE,{"disambiguationData":[OSD([makeQuery(id+"F4.imprint","IMPRINT",FACE,{"disambiguationData":[TD([[makeQuery(id+"F4.imprint","IMPRINT",EDGE,{"derivedFrom":sQuery(id+"F4.wireOp",EDGE,"E26.7.0")}),1.0]])]})])],"isStart":true})]}),makeQuery(id+"F15.opLoft","CAP_FACE",FACE,{"disambiguationData":[OSD([makeQuery(id+"F4.imprint","IMPRINT",FACE,{"disambiguationData":[TD([[makeQuery(id+"F4.imprint","IMPRINT",EDGE,{"derivedFrom":sQuery(id+"F4.wireOp",EDGE,"E26.6.0")}),1.0]])]})])],"isStart":true})]}),makeQuery(id+"F16.opLoft","CAP_FACE",FACE,{"disambiguationData":[OSD([makeQuery(id+"F4.imprint","IMPRINT",FACE,{"disambiguationData":[TD([[makeQuery(id+"F4.imprint","IMPRINT",EDGE,{"derivedFrom":sQuery(id+"F4.wireOp",EDGE,"E26.5.0")}),1.0]])]})])],"isStart":true})]}),makeQuery(id+"F17.opLoft","CAP_FACE",FACE,{"disambiguationData":[OSD([makeQuery(id+"F4.imprint","IMPRINT",FACE,{"disambiguationData":[TD([[makeQuery(id+"F4.imprint","IMPRINT",EDGE,{"derivedFrom":sQuery(id+"F4.wireOp",EDGE,"E26.4.0")}),1.0]])]})])],"isStart":true})]}),makeQuery(id+"F18.opLoft","CAP_FACE",FACE,{"disambiguationData":[OSD([makeQuery(id+"F4.imprint","IMPRINT",FACE,{"disambiguationData":[TD([[makeQuery(id+"F4.imprint","IMPRINT",EDGE,{"derivedFrom":sQuery(id+"F4.wireOp",EDGE,"E26.3.0")}),1.0]])]})])],"isStart":true})]}),makeQuery(id+"F19.opLoft","CAP_FACE",FACE,{"disambiguationData":[OSD([makeQuery(id+"F4.imprint","IMPRINT",FACE,{"disambiguationData":[TD([[makeQuery(id+"F4.imprint","IMPRINT",EDGE,{"derivedFrom":sQuery(id+"F4.wireOp",EDGE,"E26.2.0")}),1.0]])]})])],"isStart":true})]}),makeQuery(id+"F20.opLoft","CAP_FACE",FACE,{"disambiguationData":[OSD([makeQuery(id+"F4.imprint","IMPRINT",FACE,{"disambiguationData":[TD([[makeQuery(id+"F4.imprint","IMPRINT",EDGE,{"derivedFrom":sQuery(id+"F4.wireOp",EDGE,"E26.1.0")}),1.0]])]})])],"isStart":true})]}),makeQuery(id+"F42.opRevolve","SWEPT_FACE",FACE,{"disambiguationData":[OSD([sQuery(id+"F41.wireOp",EDGE,"E32")])]})]});
            var Q4;
            Q4=makeQuery(id+"F42.boolean.opBoolean","INTERSECT",EDGE,{"disambiguationData":[OD(1.0)],"derivedFrom":[makeQuery(id+"F20.boolean.opBoolean","MERGE",FACE,{"derivedFrom":[makeQuery(id+"F19.boolean.opBoolean","MERGE",FACE,{"derivedFrom":[makeQuery(id+"F18.boolean.opBoolean","MERGE",FACE,{"derivedFrom":[makeQuery(id+"F17.boolean.opBoolean","MERGE",FACE,{"derivedFrom":[makeQuery(id+"F16.boolean.opBoolean","MERGE",FACE,{"derivedFrom":[makeQuery(id+"F15.boolean.opBoolean","MERGE",FACE,{"derivedFrom":[makeQuery(id+"F14.boolean.opBoolean","MERGE",FACE,{"derivedFrom":[makeQuery(id+"F13.boolean.opBoolean","MERGE",FACE,{"derivedFrom":[makeQuery(id+"F12.boolean.opBoolean","MERGE",FACE,{"derivedFrom":[makeQuery(id+"F11.boolean.opBoolean","MERGE",FACE,{"derivedFrom":[makeQuery(id+"F10.boolean.opBoolean","MERGE",FACE,{"derivedFrom":[makeQuery(id+"F9.boolean.opBoolean","MERGE",FACE,{"derivedFrom":[makeQuery(id+"F8.boolean.opBoolean","MERGE",FACE,{"derivedFrom":[makeQuery(id+"F7.boolean.opBoolean","MERGE",FACE,{"derivedFrom":[makeQuery(id+"F6.boolean.opBoolean","MERGE",FACE,{"derivedFrom":[makeQuery(id+"F5.boolean.opBoolean","MERGE",FACE,{"derivedFrom":[makeQuery(id+"F1.opRevolve","SWEPT_FACE",FACE,{"disambiguationData":[OSD([sQuery(id+"F0.wireOp",EDGE,"E14")])]}),makeQuery(id+"F5.opLoft","CAP_FACE",FACE,{"disambiguationData":[OSD([makeQuery(id+"F4.imprint","IMPRINT",FACE,{"disambiguationData":[TD([[makeQuery(id+"F4.imprint","IMPRINT",EDGE,{"derivedFrom":sQuery(id+"F4.wireOp",EDGE,"E21")}),1.0]])]})])],"isStart":true})]}),makeQuery(id+"F6.opLoft","CAP_FACE",FACE,{"disambiguationData":[OSD([makeQuery(id+"F4.imprint","IMPRINT",FACE,{"disambiguationData":[TD([[makeQuery(id+"F4.imprint","IMPRINT",EDGE,{"derivedFrom":sQuery(id+"F4.wireOp",EDGE,"E26.15.0")}),1.0]])]})])],"isStart":true})]}),makeQuery(id+"F7.opLoft","CAP_FACE",FACE,{"disambiguationData":[OSD([makeQuery(id+"F4.imprint","IMPRINT",FACE,{"disambiguationData":[TD([[makeQuery(id+"F4.imprint","IMPRINT",EDGE,{"derivedFrom":sQuery(id+"F4.wireOp",EDGE,"E26.14.0")}),1.0]])]})])],"isStart":true})]}),makeQuery(id+"F8.opLoft","CAP_FACE",FACE,{"disambiguationData":[OSD([makeQuery(id+"F4.imprint","IMPRINT",FACE,{"disambiguationData":[TD([[makeQuery(id+"F4.imprint","IMPRINT",EDGE,{"derivedFrom":sQuery(id+"F4.wireOp",EDGE,"E26.13.0")}),1.0]])]})])],"isStart":true})]}),makeQuery(id+"F9.opLoft","CAP_FACE",FACE,{"disambiguationData":[OSD([makeQuery(id+"F4.imprint","IMPRINT",FACE,{"disambiguationData":[TD([[makeQuery(id+"F4.imprint","IMPRINT",EDGE,{"derivedFrom":sQuery(id+"F4.wireOp",EDGE,"E26.12.0")}),1.0]])]})])],"isStart":true})]}),makeQuery(id+"F10.opLoft","CAP_FACE",FACE,{"disambiguationData":[OSD([makeQuery(id+"F4.imprint","IMPRINT",FACE,{"disambiguationData":[TD([[makeQuery(id+"F4.imprint","IMPRINT",EDGE,{"derivedFrom":sQuery(id+"F4.wireOp",EDGE,"E26.11.0")}),1.0]])]})])],"isStart":true})]}),makeQuery(id+"F11.opLoft","CAP_FACE",FACE,{"disambiguationData":[OSD([makeQuery(id+"F4.imprint","IMPRINT",FACE,{"disambiguationData":[TD([[makeQuery(id+"F4.imprint","IMPRINT",EDGE,{"derivedFrom":sQuery(id+"F4.wireOp",EDGE,"E26.10.0")}),1.0]])]})])],"isStart":true})]}),makeQuery(id+"F12.opLoft","CAP_FACE",FACE,{"disambiguationData":[OSD([makeQuery(id+"F4.imprint","IMPRINT",FACE,{"disambiguationData":[TD([[makeQuery(id+"F4.imprint","IMPRINT",EDGE,{"derivedFrom":sQuery(id+"F4.wireOp",EDGE,"E26.9.0")}),1.0]])]})])],"isStart":true})]}),makeQuery(id+"F13.opLoft","CAP_FACE",FACE,{"disambiguationData":[OSD([makeQuery(id+"F4.imprint","IMPRINT",FACE,{"disambiguationData":[TD([[makeQuery(id+"F4.imprint","IMPRINT",EDGE,{"derivedFrom":sQuery(id+"F4.wireOp",EDGE,"E26.8.0")}),1.0]])]})])],"isStart":true})]}),makeQuery(id+"F14.opLoft","CAP_FACE",FACE,{"disambiguationData":[OSD([makeQuery(id+"F4.imprint","IMPRINT",FACE,{"disambiguationData":[TD([[makeQuery(id+"F4.imprint","IMPRINT",EDGE,{"derivedFrom":sQuery(id+"F4.wireOp",EDGE,"E26.7.0")}),1.0]])]})])],"isStart":true})]}),makeQuery(id+"F15.opLoft","CAP_FACE",FACE,{"disambiguationData":[OSD([makeQuery(id+"F4.imprint","IMPRINT",FACE,{"disambiguationData":[TD([[makeQuery(id+"F4.imprint","IMPRINT",EDGE,{"derivedFrom":sQuery(id+"F4.wireOp",EDGE,"E26.6.0")}),1.0]])]})])],"isStart":true})]}),makeQuery(id+"F16.opLoft","CAP_FACE",FACE,{"disambiguationData":[OSD([makeQuery(id+"F4.imprint","IMPRINT",FACE,{"disambiguationData":[TD([[makeQuery(id+"F4.imprint","IMPRINT",EDGE,{"derivedFrom":sQuery(id+"F4.wireOp",EDGE,"E26.5.0")}),1.0]])]})])],"isStart":true})]}),makeQuery(id+"F17.opLoft","CAP_FACE",FACE,{"disambiguationData":[OSD([makeQuery(id+"F4.imprint","IMPRINT",FACE,{"disambiguationData":[TD([[makeQuery(id+"F4.imprint","IMPRINT",EDGE,{"derivedFrom":sQuery(id+"F4.wireOp",EDGE,"E26.4.0")}),1.0]])]})])],"isStart":true})]}),makeQuery(id+"F18.opLoft","CAP_FACE",FACE,{"disambiguationData":[OSD([makeQuery(id+"F4.imprint","IMPRINT",FACE,{"disambiguationData":[TD([[makeQuery(id+"F4.imprint","IMPRINT",EDGE,{"derivedFrom":sQuery(id+"F4.wireOp",EDGE,"E26.3.0")}),1.0]])]})])],"isStart":true})]}),makeQuery(id+"F19.opLoft","CAP_FACE",FACE,{"disambiguationData":[OSD([makeQuery(id+"F4.imprint","IMPRINT",FACE,{"disambiguationData":[TD([[makeQuery(id+"F4.imprint","IMPRINT",EDGE,{"derivedFrom":sQuery(id+"F4.wireOp",EDGE,"E26.2.0")}),1.0]])]})])],"isStart":true})]}),makeQuery(id+"F20.opLoft","CAP_FACE",FACE,{"disambiguationData":[OSD([makeQuery(id+"F4.imprint","IMPRINT",FACE,{"disambiguationData":[TD([[makeQuery(id+"F4.imprint","IMPRINT",EDGE,{"derivedFrom":sQuery(id+"F4.wireOp",EDGE,"E26.1.0")}),1.0]])]})])],"isStart":true})]}),makeQuery(id+"F42.opRevolve","SWEPT_FACE",FACE,{"disambiguationData":[OSD([sQuery(id+"F41.wireOp",EDGE,"E32")])]})]});
            var Q5;
            Q5=makeQuery(id+"F42.boolean.opBoolean","INTERSECT",EDGE,{"disambiguationData":[OD(0.0)],"derivedFrom":[makeQuery(id+"F20.boolean.opBoolean","MERGE",FACE,{"derivedFrom":[makeQuery(id+"F19.boolean.opBoolean","MERGE",FACE,{"derivedFrom":[makeQuery(id+"F18.boolean.opBoolean","MERGE",FACE,{"derivedFrom":[makeQuery(id+"F17.boolean.opBoolean","MERGE",FACE,{"derivedFrom":[makeQuery(id+"F16.boolean.opBoolean","MERGE",FACE,{"derivedFrom":[makeQuery(id+"F15.boolean.opBoolean","MERGE",FACE,{"derivedFrom":[makeQuery(id+"F14.boolean.opBoolean","MERGE",FACE,{"derivedFrom":[makeQuery(id+"F13.boolean.opBoolean","MERGE",FACE,{"derivedFrom":[makeQuery(id+"F12.boolean.opBoolean","MERGE",FACE,{"derivedFrom":[makeQuery(id+"F11.boolean.opBoolean","MERGE",FACE,{"derivedFrom":[makeQuery(id+"F10.boolean.opBoolean","MERGE",FACE,{"derivedFrom":[makeQuery(id+"F9.boolean.opBoolean","MERGE",FACE,{"derivedFrom":[makeQuery(id+"F8.boolean.opBoolean","MERGE",FACE,{"derivedFrom":[makeQuery(id+"F7.boolean.opBoolean","MERGE",FACE,{"derivedFrom":[makeQuery(id+"F6.boolean.opBoolean","MERGE",FACE,{"derivedFrom":[makeQuery(id+"F5.boolean.opBoolean","MERGE",FACE,{"derivedFrom":[makeQuery(id+"F1.opRevolve","SWEPT_FACE",FACE,{"disambiguationData":[OSD([sQuery(id+"F0.wireOp",EDGE,"E14")])]}),makeQuery(id+"F5.opLoft","CAP_FACE",FACE,{"disambiguationData":[OSD([makeQuery(id+"F4.imprint","IMPRINT",FACE,{"disambiguationData":[TD([[makeQuery(id+"F4.imprint","IMPRINT",EDGE,{"derivedFrom":sQuery(id+"F4.wireOp",EDGE,"E21")}),1.0]])]})])],"isStart":true})]}),makeQuery(id+"F6.opLoft","CAP_FACE",FACE,{"disambiguationData":[OSD([makeQuery(id+"F4.imprint","IMPRINT",FACE,{"disambiguationData":[TD([[makeQuery(id+"F4.imprint","IMPRINT",EDGE,{"derivedFrom":sQuery(id+"F4.wireOp",EDGE,"E26.15.0")}),1.0]])]})])],"isStart":true})]}),makeQuery(id+"F7.opLoft","CAP_FACE",FACE,{"disambiguationData":[OSD([makeQuery(id+"F4.imprint","IMPRINT",FACE,{"disambiguationData":[TD([[makeQuery(id+"F4.imprint","IMPRINT",EDGE,{"derivedFrom":sQuery(id+"F4.wireOp",EDGE,"E26.14.0")}),1.0]])]})])],"isStart":true})]}),makeQuery(id+"F8.opLoft","CAP_FACE",FACE,{"disambiguationData":[OSD([makeQuery(id+"F4.imprint","IMPRINT",FACE,{"disambiguationData":[TD([[makeQuery(id+"F4.imprint","IMPRINT",EDGE,{"derivedFrom":sQuery(id+"F4.wireOp",EDGE,"E26.13.0")}),1.0]])]})])],"isStart":true})]}),makeQuery(id+"F9.opLoft","CAP_FACE",FACE,{"disambiguationData":[OSD([makeQuery(id+"F4.imprint","IMPRINT",FACE,{"disambiguationData":[TD([[makeQuery(id+"F4.imprint","IMPRINT",EDGE,{"derivedFrom":sQuery(id+"F4.wireOp",EDGE,"E26.12.0")}),1.0]])]})])],"isStart":true})]}),makeQuery(id+"F10.opLoft","CAP_FACE",FACE,{"disambiguationData":[OSD([makeQuery(id+"F4.imprint","IMPRINT",FACE,{"disambiguationData":[TD([[makeQuery(id+"F4.imprint","IMPRINT",EDGE,{"derivedFrom":sQuery(id+"F4.wireOp",EDGE,"E26.11.0")}),1.0]])]})])],"isStart":true})]}),makeQuery(id+"F11.opLoft","CAP_FACE",FACE,{"disambiguationData":[OSD([makeQuery(id+"F4.imprint","IMPRINT",FACE,{"disambiguationData":[TD([[makeQuery(id+"F4.imprint","IMPRINT",EDGE,{"derivedFrom":sQuery(id+"F4.wireOp",EDGE,"E26.10.0")}),1.0]])]})])],"isStart":true})]}),makeQuery(id+"F12.opLoft","CAP_FACE",FACE,{"disambiguationData":[OSD([makeQuery(id+"F4.imprint","IMPRINT",FACE,{"disambiguationData":[TD([[makeQuery(id+"F4.imprint","IMPRINT",EDGE,{"derivedFrom":sQuery(id+"F4.wireOp",EDGE,"E26.9.0")}),1.0]])]})])],"isStart":true})]}),makeQuery(id+"F13.opLoft","CAP_FACE",FACE,{"disambiguationData":[OSD([makeQuery(id+"F4.imprint","IMPRINT",FACE,{"disambiguationData":[TD([[makeQuery(id+"F4.imprint","IMPRINT",EDGE,{"derivedFrom":sQuery(id+"F4.wireOp",EDGE,"E26.8.0")}),1.0]])]})])],"isStart":true})]}),makeQuery(id+"F14.opLoft","CAP_FACE",FACE,{"disambiguationData":[OSD([makeQuery(id+"F4.imprint","IMPRINT",FACE,{"disambiguationData":[TD([[makeQuery(id+"F4.imprint","IMPRINT",EDGE,{"derivedFrom":sQuery(id+"F4.wireOp",EDGE,"E26.7.0")}),1.0]])]})])],"isStart":true})]}),makeQuery(id+"F15.opLoft","CAP_FACE",FACE,{"disambiguationData":[OSD([makeQuery(id+"F4.imprint","IMPRINT",FACE,{"disambiguationData":[TD([[makeQuery(id+"F4.imprint","IMPRINT",EDGE,{"derivedFrom":sQuery(id+"F4.wireOp",EDGE,"E26.6.0")}),1.0]])]})])],"isStart":true})]}),makeQuery(id+"F16.opLoft","CAP_FACE",FACE,{"disambiguationData":[OSD([makeQuery(id+"F4.imprint","IMPRINT",FACE,{"disambiguationData":[TD([[makeQuery(id+"F4.imprint","IMPRINT",EDGE,{"derivedFrom":sQuery(id+"F4.wireOp",EDGE,"E26.5.0")}),1.0]])]})])],"isStart":true})]}),makeQuery(id+"F17.opLoft","CAP_FACE",FACE,{"disambiguationData":[OSD([makeQuery(id+"F4.imprint","IMPRINT",FACE,{"disambiguationData":[TD([[makeQuery(id+"F4.imprint","IMPRINT",EDGE,{"derivedFrom":sQuery(id+"F4.wireOp",EDGE,"E26.4.0")}),1.0]])]})])],"isStart":true})]}),makeQuery(id+"F18.opLoft","CAP_FACE",FACE,{"disambiguationData":[OSD([makeQuery(id+"F4.imprint","IMPRINT",FACE,{"disambiguationData":[TD([[makeQuery(id+"F4.imprint","IMPRINT",EDGE,{"derivedFrom":sQuery(id+"F4.wireOp",EDGE,"E26.3.0")}),1.0]])]})])],"isStart":true})]}),makeQuery(id+"F19.opLoft","CAP_FACE",FACE,{"disambiguationData":[OSD([makeQuery(id+"F4.imprint","IMPRINT",FACE,{"disambiguationData":[TD([[makeQuery(id+"F4.imprint","IMPRINT",EDGE,{"derivedFrom":sQuery(id+"F4.wireOp",EDGE,"E26.2.0")}),1.0]])]})])],"isStart":true})]}),makeQuery(id+"F20.opLoft","CAP_FACE",FACE,{"disambiguationData":[OSD([makeQuery(id+"F4.imprint","IMPRINT",FACE,{"disambiguationData":[TD([[makeQuery(id+"F4.imprint","IMPRINT",EDGE,{"derivedFrom":sQuery(id+"F4.wireOp",EDGE,"E26.1.0")}),1.0]])]})])],"isStart":true})]}),makeQuery(id+"F42.opRevolve","SWEPT_FACE",FACE,{"disambiguationData":[OSD([sQuery(id+"F41.wireOp",EDGE,"E32")])]})]});
            var Q6;
            Q6=makeQuery(id+"F42.boolean.opBoolean","INTERSECT",EDGE,{"disambiguationData":[OD(15.0)],"derivedFrom":[makeQuery(id+"F20.boolean.opBoolean","MERGE",FACE,{"derivedFrom":[makeQuery(id+"F19.boolean.opBoolean","MERGE",FACE,{"derivedFrom":[makeQuery(id+"F18.boolean.opBoolean","MERGE",FACE,{"derivedFrom":[makeQuery(id+"F17.boolean.opBoolean","MERGE",FACE,{"derivedFrom":[makeQuery(id+"F16.boolean.opBoolean","MERGE",FACE,{"derivedFrom":[makeQuery(id+"F15.boolean.opBoolean","MERGE",FACE,{"derivedFrom":[makeQuery(id+"F14.boolean.opBoolean","MERGE",FACE,{"derivedFrom":[makeQuery(id+"F13.boolean.opBoolean","MERGE",FACE,{"derivedFrom":[makeQuery(id+"F12.boolean.opBoolean","MERGE",FACE,{"derivedFrom":[makeQuery(id+"F11.boolean.opBoolean","MERGE",FACE,{"derivedFrom":[makeQuery(id+"F10.boolean.opBoolean","MERGE",FACE,{"derivedFrom":[makeQuery(id+"F9.boolean.opBoolean","MERGE",FACE,{"derivedFrom":[makeQuery(id+"F8.boolean.opBoolean","MERGE",FACE,{"derivedFrom":[makeQuery(id+"F7.boolean.opBoolean","MERGE",FACE,{"derivedFrom":[makeQuery(id+"F6.boolean.opBoolean","MERGE",FACE,{"derivedFrom":[makeQuery(id+"F5.boolean.opBoolean","MERGE",FACE,{"derivedFrom":[makeQuery(id+"F1.opRevolve","SWEPT_FACE",FACE,{"disambiguationData":[OSD([sQuery(id+"F0.wireOp",EDGE,"E14")])]}),makeQuery(id+"F5.opLoft","CAP_FACE",FACE,{"disambiguationData":[OSD([makeQuery(id+"F4.imprint","IMPRINT",FACE,{"disambiguationData":[TD([[makeQuery(id+"F4.imprint","IMPRINT",EDGE,{"derivedFrom":sQuery(id+"F4.wireOp",EDGE,"E21")}),1.0]])]})])],"isStart":true})]}),makeQuery(id+"F6.opLoft","CAP_FACE",FACE,{"disambiguationData":[OSD([makeQuery(id+"F4.imprint","IMPRINT",FACE,{"disambiguationData":[TD([[makeQuery(id+"F4.imprint","IMPRINT",EDGE,{"derivedFrom":sQuery(id+"F4.wireOp",EDGE,"E26.15.0")}),1.0]])]})])],"isStart":true})]}),makeQuery(id+"F7.opLoft","CAP_FACE",FACE,{"disambiguationData":[OSD([makeQuery(id+"F4.imprint","IMPRINT",FACE,{"disambiguationData":[TD([[makeQuery(id+"F4.imprint","IMPRINT",EDGE,{"derivedFrom":sQuery(id+"F4.wireOp",EDGE,"E26.14.0")}),1.0]])]})])],"isStart":true})]}),makeQuery(id+"F8.opLoft","CAP_FACE",FACE,{"disambiguationData":[OSD([makeQuery(id+"F4.imprint","IMPRINT",FACE,{"disambiguationData":[TD([[makeQuery(id+"F4.imprint","IMPRINT",EDGE,{"derivedFrom":sQuery(id+"F4.wireOp",EDGE,"E26.13.0")}),1.0]])]})])],"isStart":true})]}),makeQuery(id+"F9.opLoft","CAP_FACE",FACE,{"disambiguationData":[OSD([makeQuery(id+"F4.imprint","IMPRINT",FACE,{"disambiguationData":[TD([[makeQuery(id+"F4.imprint","IMPRINT",EDGE,{"derivedFrom":sQuery(id+"F4.wireOp",EDGE,"E26.12.0")}),1.0]])]})])],"isStart":true})]}),makeQuery(id+"F10.opLoft","CAP_FACE",FACE,{"disambiguationData":[OSD([makeQuery(id+"F4.imprint","IMPRINT",FACE,{"disambiguationData":[TD([[makeQuery(id+"F4.imprint","IMPRINT",EDGE,{"derivedFrom":sQuery(id+"F4.wireOp",EDGE,"E26.11.0")}),1.0]])]})])],"isStart":true})]}),makeQuery(id+"F11.opLoft","CAP_FACE",FACE,{"disambiguationData":[OSD([makeQuery(id+"F4.imprint","IMPRINT",FACE,{"disambiguationData":[TD([[makeQuery(id+"F4.imprint","IMPRINT",EDGE,{"derivedFrom":sQuery(id+"F4.wireOp",EDGE,"E26.10.0")}),1.0]])]})])],"isStart":true})]}),makeQuery(id+"F12.opLoft","CAP_FACE",FACE,{"disambiguationData":[OSD([makeQuery(id+"F4.imprint","IMPRINT",FACE,{"disambiguationData":[TD([[makeQuery(id+"F4.imprint","IMPRINT",EDGE,{"derivedFrom":sQuery(id+"F4.wireOp",EDGE,"E26.9.0")}),1.0]])]})])],"isStart":true})]}),makeQuery(id+"F13.opLoft","CAP_FACE",FACE,{"disambiguationData":[OSD([makeQuery(id+"F4.imprint","IMPRINT",FACE,{"disambiguationData":[TD([[makeQuery(id+"F4.imprint","IMPRINT",EDGE,{"derivedFrom":sQuery(id+"F4.wireOp",EDGE,"E26.8.0")}),1.0]])]})])],"isStart":true})]}),makeQuery(id+"F14.opLoft","CAP_FACE",FACE,{"disambiguationData":[OSD([makeQuery(id+"F4.imprint","IMPRINT",FACE,{"disambiguationData":[TD([[makeQuery(id+"F4.imprint","IMPRINT",EDGE,{"derivedFrom":sQuery(id+"F4.wireOp",EDGE,"E26.7.0")}),1.0]])]})])],"isStart":true})]}),makeQuery(id+"F15.opLoft","CAP_FACE",FACE,{"disambiguationData":[OSD([makeQuery(id+"F4.imprint","IMPRINT",FACE,{"disambiguationData":[TD([[makeQuery(id+"F4.imprint","IMPRINT",EDGE,{"derivedFrom":sQuery(id+"F4.wireOp",EDGE,"E26.6.0")}),1.0]])]})])],"isStart":true})]}),makeQuery(id+"F16.opLoft","CAP_FACE",FACE,{"disambiguationData":[OSD([makeQuery(id+"F4.imprint","IMPRINT",FACE,{"disambiguationData":[TD([[makeQuery(id+"F4.imprint","IMPRINT",EDGE,{"derivedFrom":sQuery(id+"F4.wireOp",EDGE,"E26.5.0")}),1.0]])]})])],"isStart":true})]}),makeQuery(id+"F17.opLoft","CAP_FACE",FACE,{"disambiguationData":[OSD([makeQuery(id+"F4.imprint","IMPRINT",FACE,{"disambiguationData":[TD([[makeQuery(id+"F4.imprint","IMPRINT",EDGE,{"derivedFrom":sQuery(id+"F4.wireOp",EDGE,"E26.4.0")}),1.0]])]})])],"isStart":true})]}),makeQuery(id+"F18.opLoft","CAP_FACE",FACE,{"disambiguationData":[OSD([makeQuery(id+"F4.imprint","IMPRINT",FACE,{"disambiguationData":[TD([[makeQuery(id+"F4.imprint","IMPRINT",EDGE,{"derivedFrom":sQuery(id+"F4.wireOp",EDGE,"E26.3.0")}),1.0]])]})])],"isStart":true})]}),makeQuery(id+"F19.opLoft","CAP_FACE",FACE,{"disambiguationData":[OSD([makeQuery(id+"F4.imprint","IMPRINT",FACE,{"disambiguationData":[TD([[makeQuery(id+"F4.imprint","IMPRINT",EDGE,{"derivedFrom":sQuery(id+"F4.wireOp",EDGE,"E26.2.0")}),1.0]])]})])],"isStart":true})]}),makeQuery(id+"F20.opLoft","CAP_FACE",FACE,{"disambiguationData":[OSD([makeQuery(id+"F4.imprint","IMPRINT",FACE,{"disambiguationData":[TD([[makeQuery(id+"F4.imprint","IMPRINT",EDGE,{"derivedFrom":sQuery(id+"F4.wireOp",EDGE,"E26.1.0")}),1.0]])]})])],"isStart":true})]}),makeQuery(id+"F42.opRevolve","SWEPT_FACE",FACE,{"disambiguationData":[OSD([sQuery(id+"F41.wireOp",EDGE,"E32")])]})]});
            var Q7;
            Q7=makeQuery(id+"F42.boolean.opBoolean","INTERSECT",EDGE,{"disambiguationData":[OD(14.0)],"derivedFrom":[makeQuery(id+"F20.boolean.opBoolean","MERGE",FACE,{"derivedFrom":[makeQuery(id+"F19.boolean.opBoolean","MERGE",FACE,{"derivedFrom":[makeQuery(id+"F18.boolean.opBoolean","MERGE",FACE,{"derivedFrom":[makeQuery(id+"F17.boolean.opBoolean","MERGE",FACE,{"derivedFrom":[makeQuery(id+"F16.boolean.opBoolean","MERGE",FACE,{"derivedFrom":[makeQuery(id+"F15.boolean.opBoolean","MERGE",FACE,{"derivedFrom":[makeQuery(id+"F14.boolean.opBoolean","MERGE",FACE,{"derivedFrom":[makeQuery(id+"F13.boolean.opBoolean","MERGE",FACE,{"derivedFrom":[makeQuery(id+"F12.boolean.opBoolean","MERGE",FACE,{"derivedFrom":[makeQuery(id+"F11.boolean.opBoolean","MERGE",FACE,{"derivedFrom":[makeQuery(id+"F10.boolean.opBoolean","MERGE",FACE,{"derivedFrom":[makeQuery(id+"F9.boolean.opBoolean","MERGE",FACE,{"derivedFrom":[makeQuery(id+"F8.boolean.opBoolean","MERGE",FACE,{"derivedFrom":[makeQuery(id+"F7.boolean.opBoolean","MERGE",FACE,{"derivedFrom":[makeQuery(id+"F6.boolean.opBoolean","MERGE",FACE,{"derivedFrom":[makeQuery(id+"F5.boolean.opBoolean","MERGE",FACE,{"derivedFrom":[makeQuery(id+"F1.opRevolve","SWEPT_FACE",FACE,{"disambiguationData":[OSD([sQuery(id+"F0.wireOp",EDGE,"E14")])]}),makeQuery(id+"F5.opLoft","CAP_FACE",FACE,{"disambiguationData":[OSD([makeQuery(id+"F4.imprint","IMPRINT",FACE,{"disambiguationData":[TD([[makeQuery(id+"F4.imprint","IMPRINT",EDGE,{"derivedFrom":sQuery(id+"F4.wireOp",EDGE,"E21")}),1.0]])]})])],"isStart":true})]}),makeQuery(id+"F6.opLoft","CAP_FACE",FACE,{"disambiguationData":[OSD([makeQuery(id+"F4.imprint","IMPRINT",FACE,{"disambiguationData":[TD([[makeQuery(id+"F4.imprint","IMPRINT",EDGE,{"derivedFrom":sQuery(id+"F4.wireOp",EDGE,"E26.15.0")}),1.0]])]})])],"isStart":true})]}),makeQuery(id+"F7.opLoft","CAP_FACE",FACE,{"disambiguationData":[OSD([makeQuery(id+"F4.imprint","IMPRINT",FACE,{"disambiguationData":[TD([[makeQuery(id+"F4.imprint","IMPRINT",EDGE,{"derivedFrom":sQuery(id+"F4.wireOp",EDGE,"E26.14.0")}),1.0]])]})])],"isStart":true})]}),makeQuery(id+"F8.opLoft","CAP_FACE",FACE,{"disambiguationData":[OSD([makeQuery(id+"F4.imprint","IMPRINT",FACE,{"disambiguationData":[TD([[makeQuery(id+"F4.imprint","IMPRINT",EDGE,{"derivedFrom":sQuery(id+"F4.wireOp",EDGE,"E26.13.0")}),1.0]])]})])],"isStart":true})]}),makeQuery(id+"F9.opLoft","CAP_FACE",FACE,{"disambiguationData":[OSD([makeQuery(id+"F4.imprint","IMPRINT",FACE,{"disambiguationData":[TD([[makeQuery(id+"F4.imprint","IMPRINT",EDGE,{"derivedFrom":sQuery(id+"F4.wireOp",EDGE,"E26.12.0")}),1.0]])]})])],"isStart":true})]}),makeQuery(id+"F10.opLoft","CAP_FACE",FACE,{"disambiguationData":[OSD([makeQuery(id+"F4.imprint","IMPRINT",FACE,{"disambiguationData":[TD([[makeQuery(id+"F4.imprint","IMPRINT",EDGE,{"derivedFrom":sQuery(id+"F4.wireOp",EDGE,"E26.11.0")}),1.0]])]})])],"isStart":true})]}),makeQuery(id+"F11.opLoft","CAP_FACE",FACE,{"disambiguationData":[OSD([makeQuery(id+"F4.imprint","IMPRINT",FACE,{"disambiguationData":[TD([[makeQuery(id+"F4.imprint","IMPRINT",EDGE,{"derivedFrom":sQuery(id+"F4.wireOp",EDGE,"E26.10.0")}),1.0]])]})])],"isStart":true})]}),makeQuery(id+"F12.opLoft","CAP_FACE",FACE,{"disambiguationData":[OSD([makeQuery(id+"F4.imprint","IMPRINT",FACE,{"disambiguationData":[TD([[makeQuery(id+"F4.imprint","IMPRINT",EDGE,{"derivedFrom":sQuery(id+"F4.wireOp",EDGE,"E26.9.0")}),1.0]])]})])],"isStart":true})]}),makeQuery(id+"F13.opLoft","CAP_FACE",FACE,{"disambiguationData":[OSD([makeQuery(id+"F4.imprint","IMPRINT",FACE,{"disambiguationData":[TD([[makeQuery(id+"F4.imprint","IMPRINT",EDGE,{"derivedFrom":sQuery(id+"F4.wireOp",EDGE,"E26.8.0")}),1.0]])]})])],"isStart":true})]}),makeQuery(id+"F14.opLoft","CAP_FACE",FACE,{"disambiguationData":[OSD([makeQuery(id+"F4.imprint","IMPRINT",FACE,{"disambiguationData":[TD([[makeQuery(id+"F4.imprint","IMPRINT",EDGE,{"derivedFrom":sQuery(id+"F4.wireOp",EDGE,"E26.7.0")}),1.0]])]})])],"isStart":true})]}),makeQuery(id+"F15.opLoft","CAP_FACE",FACE,{"disambiguationData":[OSD([makeQuery(id+"F4.imprint","IMPRINT",FACE,{"disambiguationData":[TD([[makeQuery(id+"F4.imprint","IMPRINT",EDGE,{"derivedFrom":sQuery(id+"F4.wireOp",EDGE,"E26.6.0")}),1.0]])]})])],"isStart":true})]}),makeQuery(id+"F16.opLoft","CAP_FACE",FACE,{"disambiguationData":[OSD([makeQuery(id+"F4.imprint","IMPRINT",FACE,{"disambiguationData":[TD([[makeQuery(id+"F4.imprint","IMPRINT",EDGE,{"derivedFrom":sQuery(id+"F4.wireOp",EDGE,"E26.5.0")}),1.0]])]})])],"isStart":true})]}),makeQuery(id+"F17.opLoft","CAP_FACE",FACE,{"disambiguationData":[OSD([makeQuery(id+"F4.imprint","IMPRINT",FACE,{"disambiguationData":[TD([[makeQuery(id+"F4.imprint","IMPRINT",EDGE,{"derivedFrom":sQuery(id+"F4.wireOp",EDGE,"E26.4.0")}),1.0]])]})])],"isStart":true})]}),makeQuery(id+"F18.opLoft","CAP_FACE",FACE,{"disambiguationData":[OSD([makeQuery(id+"F4.imprint","IMPRINT",FACE,{"disambiguationData":[TD([[makeQuery(id+"F4.imprint","IMPRINT",EDGE,{"derivedFrom":sQuery(id+"F4.wireOp",EDGE,"E26.3.0")}),1.0]])]})])],"isStart":true})]}),makeQuery(id+"F19.opLoft","CAP_FACE",FACE,{"disambiguationData":[OSD([makeQuery(id+"F4.imprint","IMPRINT",FACE,{"disambiguationData":[TD([[makeQuery(id+"F4.imprint","IMPRINT",EDGE,{"derivedFrom":sQuery(id+"F4.wireOp",EDGE,"E26.2.0")}),1.0]])]})])],"isStart":true})]}),makeQuery(id+"F20.opLoft","CAP_FACE",FACE,{"disambiguationData":[OSD([makeQuery(id+"F4.imprint","IMPRINT",FACE,{"disambiguationData":[TD([[makeQuery(id+"F4.imprint","IMPRINT",EDGE,{"derivedFrom":sQuery(id+"F4.wireOp",EDGE,"E26.1.0")}),1.0]])]})])],"isStart":true})]}),makeQuery(id+"F42.opRevolve","SWEPT_FACE",FACE,{"disambiguationData":[OSD([sQuery(id+"F41.wireOp",EDGE,"E32")])]})]});
            var Q8;
            Q8=makeQuery(id+"F42.boolean.opBoolean","INTERSECT",EDGE,{"disambiguationData":[OD(13.0)],"derivedFrom":[makeQuery(id+"F20.boolean.opBoolean","MERGE",FACE,{"derivedFrom":[makeQuery(id+"F19.boolean.opBoolean","MERGE",FACE,{"derivedFrom":[makeQuery(id+"F18.boolean.opBoolean","MERGE",FACE,{"derivedFrom":[makeQuery(id+"F17.boolean.opBoolean","MERGE",FACE,{"derivedFrom":[makeQuery(id+"F16.boolean.opBoolean","MERGE",FACE,{"derivedFrom":[makeQuery(id+"F15.boolean.opBoolean","MERGE",FACE,{"derivedFrom":[makeQuery(id+"F14.boolean.opBoolean","MERGE",FACE,{"derivedFrom":[makeQuery(id+"F13.boolean.opBoolean","MERGE",FACE,{"derivedFrom":[makeQuery(id+"F12.boolean.opBoolean","MERGE",FACE,{"derivedFrom":[makeQuery(id+"F11.boolean.opBoolean","MERGE",FACE,{"derivedFrom":[makeQuery(id+"F10.boolean.opBoolean","MERGE",FACE,{"derivedFrom":[makeQuery(id+"F9.boolean.opBoolean","MERGE",FACE,{"derivedFrom":[makeQuery(id+"F8.boolean.opBoolean","MERGE",FACE,{"derivedFrom":[makeQuery(id+"F7.boolean.opBoolean","MERGE",FACE,{"derivedFrom":[makeQuery(id+"F6.boolean.opBoolean","MERGE",FACE,{"derivedFrom":[makeQuery(id+"F5.boolean.opBoolean","MERGE",FACE,{"derivedFrom":[makeQuery(id+"F1.opRevolve","SWEPT_FACE",FACE,{"disambiguationData":[OSD([sQuery(id+"F0.wireOp",EDGE,"E14")])]}),makeQuery(id+"F5.opLoft","CAP_FACE",FACE,{"disambiguationData":[OSD([makeQuery(id+"F4.imprint","IMPRINT",FACE,{"disambiguationData":[TD([[makeQuery(id+"F4.imprint","IMPRINT",EDGE,{"derivedFrom":sQuery(id+"F4.wireOp",EDGE,"E21")}),1.0]])]})])],"isStart":true})]}),makeQuery(id+"F6.opLoft","CAP_FACE",FACE,{"disambiguationData":[OSD([makeQuery(id+"F4.imprint","IMPRINT",FACE,{"disambiguationData":[TD([[makeQuery(id+"F4.imprint","IMPRINT",EDGE,{"derivedFrom":sQuery(id+"F4.wireOp",EDGE,"E26.15.0")}),1.0]])]})])],"isStart":true})]}),makeQuery(id+"F7.opLoft","CAP_FACE",FACE,{"disambiguationData":[OSD([makeQuery(id+"F4.imprint","IMPRINT",FACE,{"disambiguationData":[TD([[makeQuery(id+"F4.imprint","IMPRINT",EDGE,{"derivedFrom":sQuery(id+"F4.wireOp",EDGE,"E26.14.0")}),1.0]])]})])],"isStart":true})]}),makeQuery(id+"F8.opLoft","CAP_FACE",FACE,{"disambiguationData":[OSD([makeQuery(id+"F4.imprint","IMPRINT",FACE,{"disambiguationData":[TD([[makeQuery(id+"F4.imprint","IMPRINT",EDGE,{"derivedFrom":sQuery(id+"F4.wireOp",EDGE,"E26.13.0")}),1.0]])]})])],"isStart":true})]}),makeQuery(id+"F9.opLoft","CAP_FACE",FACE,{"disambiguationData":[OSD([makeQuery(id+"F4.imprint","IMPRINT",FACE,{"disambiguationData":[TD([[makeQuery(id+"F4.imprint","IMPRINT",EDGE,{"derivedFrom":sQuery(id+"F4.wireOp",EDGE,"E26.12.0")}),1.0]])]})])],"isStart":true})]}),makeQuery(id+"F10.opLoft","CAP_FACE",FACE,{"disambiguationData":[OSD([makeQuery(id+"F4.imprint","IMPRINT",FACE,{"disambiguationData":[TD([[makeQuery(id+"F4.imprint","IMPRINT",EDGE,{"derivedFrom":sQuery(id+"F4.wireOp",EDGE,"E26.11.0")}),1.0]])]})])],"isStart":true})]}),makeQuery(id+"F11.opLoft","CAP_FACE",FACE,{"disambiguationData":[OSD([makeQuery(id+"F4.imprint","IMPRINT",FACE,{"disambiguationData":[TD([[makeQuery(id+"F4.imprint","IMPRINT",EDGE,{"derivedFrom":sQuery(id+"F4.wireOp",EDGE,"E26.10.0")}),1.0]])]})])],"isStart":true})]}),makeQuery(id+"F12.opLoft","CAP_FACE",FACE,{"disambiguationData":[OSD([makeQuery(id+"F4.imprint","IMPRINT",FACE,{"disambiguationData":[TD([[makeQuery(id+"F4.imprint","IMPRINT",EDGE,{"derivedFrom":sQuery(id+"F4.wireOp",EDGE,"E26.9.0")}),1.0]])]})])],"isStart":true})]}),makeQuery(id+"F13.opLoft","CAP_FACE",FACE,{"disambiguationData":[OSD([makeQuery(id+"F4.imprint","IMPRINT",FACE,{"disambiguationData":[TD([[makeQuery(id+"F4.imprint","IMPRINT",EDGE,{"derivedFrom":sQuery(id+"F4.wireOp",EDGE,"E26.8.0")}),1.0]])]})])],"isStart":true})]}),makeQuery(id+"F14.opLoft","CAP_FACE",FACE,{"disambiguationData":[OSD([makeQuery(id+"F4.imprint","IMPRINT",FACE,{"disambiguationData":[TD([[makeQuery(id+"F4.imprint","IMPRINT",EDGE,{"derivedFrom":sQuery(id+"F4.wireOp",EDGE,"E26.7.0")}),1.0]])]})])],"isStart":true})]}),makeQuery(id+"F15.opLoft","CAP_FACE",FACE,{"disambiguationData":[OSD([makeQuery(id+"F4.imprint","IMPRINT",FACE,{"disambiguationData":[TD([[makeQuery(id+"F4.imprint","IMPRINT",EDGE,{"derivedFrom":sQuery(id+"F4.wireOp",EDGE,"E26.6.0")}),1.0]])]})])],"isStart":true})]}),makeQuery(id+"F16.opLoft","CAP_FACE",FACE,{"disambiguationData":[OSD([makeQuery(id+"F4.imprint","IMPRINT",FACE,{"disambiguationData":[TD([[makeQuery(id+"F4.imprint","IMPRINT",EDGE,{"derivedFrom":sQuery(id+"F4.wireOp",EDGE,"E26.5.0")}),1.0]])]})])],"isStart":true})]}),makeQuery(id+"F17.opLoft","CAP_FACE",FACE,{"disambiguationData":[OSD([makeQuery(id+"F4.imprint","IMPRINT",FACE,{"disambiguationData":[TD([[makeQuery(id+"F4.imprint","IMPRINT",EDGE,{"derivedFrom":sQuery(id+"F4.wireOp",EDGE,"E26.4.0")}),1.0]])]})])],"isStart":true})]}),makeQuery(id+"F18.opLoft","CAP_FACE",FACE,{"disambiguationData":[OSD([makeQuery(id+"F4.imprint","IMPRINT",FACE,{"disambiguationData":[TD([[makeQuery(id+"F4.imprint","IMPRINT",EDGE,{"derivedFrom":sQuery(id+"F4.wireOp",EDGE,"E26.3.0")}),1.0]])]})])],"isStart":true})]}),makeQuery(id+"F19.opLoft","CAP_FACE",FACE,{"disambiguationData":[OSD([makeQuery(id+"F4.imprint","IMPRINT",FACE,{"disambiguationData":[TD([[makeQuery(id+"F4.imprint","IMPRINT",EDGE,{"derivedFrom":sQuery(id+"F4.wireOp",EDGE,"E26.2.0")}),1.0]])]})])],"isStart":true})]}),makeQuery(id+"F20.opLoft","CAP_FACE",FACE,{"disambiguationData":[OSD([makeQuery(id+"F4.imprint","IMPRINT",FACE,{"disambiguationData":[TD([[makeQuery(id+"F4.imprint","IMPRINT",EDGE,{"derivedFrom":sQuery(id+"F4.wireOp",EDGE,"E26.1.0")}),1.0]])]})])],"isStart":true})]}),makeQuery(id+"F42.opRevolve","SWEPT_FACE",FACE,{"disambiguationData":[OSD([sQuery(id+"F41.wireOp",EDGE,"E32")])]})]});
            var Q9;
            Q9=makeQuery(id+"F42.boolean.opBoolean","INTERSECT",EDGE,{"disambiguationData":[OD(12.0)],"derivedFrom":[makeQuery(id+"F20.boolean.opBoolean","MERGE",FACE,{"derivedFrom":[makeQuery(id+"F19.boolean.opBoolean","MERGE",FACE,{"derivedFrom":[makeQuery(id+"F18.boolean.opBoolean","MERGE",FACE,{"derivedFrom":[makeQuery(id+"F17.boolean.opBoolean","MERGE",FACE,{"derivedFrom":[makeQuery(id+"F16.boolean.opBoolean","MERGE",FACE,{"derivedFrom":[makeQuery(id+"F15.boolean.opBoolean","MERGE",FACE,{"derivedFrom":[makeQuery(id+"F14.boolean.opBoolean","MERGE",FACE,{"derivedFrom":[makeQuery(id+"F13.boolean.opBoolean","MERGE",FACE,{"derivedFrom":[makeQuery(id+"F12.boolean.opBoolean","MERGE",FACE,{"derivedFrom":[makeQuery(id+"F11.boolean.opBoolean","MERGE",FACE,{"derivedFrom":[makeQuery(id+"F10.boolean.opBoolean","MERGE",FACE,{"derivedFrom":[makeQuery(id+"F9.boolean.opBoolean","MERGE",FACE,{"derivedFrom":[makeQuery(id+"F8.boolean.opBoolean","MERGE",FACE,{"derivedFrom":[makeQuery(id+"F7.boolean.opBoolean","MERGE",FACE,{"derivedFrom":[makeQuery(id+"F6.boolean.opBoolean","MERGE",FACE,{"derivedFrom":[makeQuery(id+"F5.boolean.opBoolean","MERGE",FACE,{"derivedFrom":[makeQuery(id+"F1.opRevolve","SWEPT_FACE",FACE,{"disambiguationData":[OSD([sQuery(id+"F0.wireOp",EDGE,"E14")])]}),makeQuery(id+"F5.opLoft","CAP_FACE",FACE,{"disambiguationData":[OSD([makeQuery(id+"F4.imprint","IMPRINT",FACE,{"disambiguationData":[TD([[makeQuery(id+"F4.imprint","IMPRINT",EDGE,{"derivedFrom":sQuery(id+"F4.wireOp",EDGE,"E21")}),1.0]])]})])],"isStart":true})]}),makeQuery(id+"F6.opLoft","CAP_FACE",FACE,{"disambiguationData":[OSD([makeQuery(id+"F4.imprint","IMPRINT",FACE,{"disambiguationData":[TD([[makeQuery(id+"F4.imprint","IMPRINT",EDGE,{"derivedFrom":sQuery(id+"F4.wireOp",EDGE,"E26.15.0")}),1.0]])]})])],"isStart":true})]}),makeQuery(id+"F7.opLoft","CAP_FACE",FACE,{"disambiguationData":[OSD([makeQuery(id+"F4.imprint","IMPRINT",FACE,{"disambiguationData":[TD([[makeQuery(id+"F4.imprint","IMPRINT",EDGE,{"derivedFrom":sQuery(id+"F4.wireOp",EDGE,"E26.14.0")}),1.0]])]})])],"isStart":true})]}),makeQuery(id+"F8.opLoft","CAP_FACE",FACE,{"disambiguationData":[OSD([makeQuery(id+"F4.imprint","IMPRINT",FACE,{"disambiguationData":[TD([[makeQuery(id+"F4.imprint","IMPRINT",EDGE,{"derivedFrom":sQuery(id+"F4.wireOp",EDGE,"E26.13.0")}),1.0]])]})])],"isStart":true})]}),makeQuery(id+"F9.opLoft","CAP_FACE",FACE,{"disambiguationData":[OSD([makeQuery(id+"F4.imprint","IMPRINT",FACE,{"disambiguationData":[TD([[makeQuery(id+"F4.imprint","IMPRINT",EDGE,{"derivedFrom":sQuery(id+"F4.wireOp",EDGE,"E26.12.0")}),1.0]])]})])],"isStart":true})]}),makeQuery(id+"F10.opLoft","CAP_FACE",FACE,{"disambiguationData":[OSD([makeQuery(id+"F4.imprint","IMPRINT",FACE,{"disambiguationData":[TD([[makeQuery(id+"F4.imprint","IMPRINT",EDGE,{"derivedFrom":sQuery(id+"F4.wireOp",EDGE,"E26.11.0")}),1.0]])]})])],"isStart":true})]}),makeQuery(id+"F11.opLoft","CAP_FACE",FACE,{"disambiguationData":[OSD([makeQuery(id+"F4.imprint","IMPRINT",FACE,{"disambiguationData":[TD([[makeQuery(id+"F4.imprint","IMPRINT",EDGE,{"derivedFrom":sQuery(id+"F4.wireOp",EDGE,"E26.10.0")}),1.0]])]})])],"isStart":true})]}),makeQuery(id+"F12.opLoft","CAP_FACE",FACE,{"disambiguationData":[OSD([makeQuery(id+"F4.imprint","IMPRINT",FACE,{"disambiguationData":[TD([[makeQuery(id+"F4.imprint","IMPRINT",EDGE,{"derivedFrom":sQuery(id+"F4.wireOp",EDGE,"E26.9.0")}),1.0]])]})])],"isStart":true})]}),makeQuery(id+"F13.opLoft","CAP_FACE",FACE,{"disambiguationData":[OSD([makeQuery(id+"F4.imprint","IMPRINT",FACE,{"disambiguationData":[TD([[makeQuery(id+"F4.imprint","IMPRINT",EDGE,{"derivedFrom":sQuery(id+"F4.wireOp",EDGE,"E26.8.0")}),1.0]])]})])],"isStart":true})]}),makeQuery(id+"F14.opLoft","CAP_FACE",FACE,{"disambiguationData":[OSD([makeQuery(id+"F4.imprint","IMPRINT",FACE,{"disambiguationData":[TD([[makeQuery(id+"F4.imprint","IMPRINT",EDGE,{"derivedFrom":sQuery(id+"F4.wireOp",EDGE,"E26.7.0")}),1.0]])]})])],"isStart":true})]}),makeQuery(id+"F15.opLoft","CAP_FACE",FACE,{"disambiguationData":[OSD([makeQuery(id+"F4.imprint","IMPRINT",FACE,{"disambiguationData":[TD([[makeQuery(id+"F4.imprint","IMPRINT",EDGE,{"derivedFrom":sQuery(id+"F4.wireOp",EDGE,"E26.6.0")}),1.0]])]})])],"isStart":true})]}),makeQuery(id+"F16.opLoft","CAP_FACE",FACE,{"disambiguationData":[OSD([makeQuery(id+"F4.imprint","IMPRINT",FACE,{"disambiguationData":[TD([[makeQuery(id+"F4.imprint","IMPRINT",EDGE,{"derivedFrom":sQuery(id+"F4.wireOp",EDGE,"E26.5.0")}),1.0]])]})])],"isStart":true})]}),makeQuery(id+"F17.opLoft","CAP_FACE",FACE,{"disambiguationData":[OSD([makeQuery(id+"F4.imprint","IMPRINT",FACE,{"disambiguationData":[TD([[makeQuery(id+"F4.imprint","IMPRINT",EDGE,{"derivedFrom":sQuery(id+"F4.wireOp",EDGE,"E26.4.0")}),1.0]])]})])],"isStart":true})]}),makeQuery(id+"F18.opLoft","CAP_FACE",FACE,{"disambiguationData":[OSD([makeQuery(id+"F4.imprint","IMPRINT",FACE,{"disambiguationData":[TD([[makeQuery(id+"F4.imprint","IMPRINT",EDGE,{"derivedFrom":sQuery(id+"F4.wireOp",EDGE,"E26.3.0")}),1.0]])]})])],"isStart":true})]}),makeQuery(id+"F19.opLoft","CAP_FACE",FACE,{"disambiguationData":[OSD([makeQuery(id+"F4.imprint","IMPRINT",FACE,{"disambiguationData":[TD([[makeQuery(id+"F4.imprint","IMPRINT",EDGE,{"derivedFrom":sQuery(id+"F4.wireOp",EDGE,"E26.2.0")}),1.0]])]})])],"isStart":true})]}),makeQuery(id+"F20.opLoft","CAP_FACE",FACE,{"disambiguationData":[OSD([makeQuery(id+"F4.imprint","IMPRINT",FACE,{"disambiguationData":[TD([[makeQuery(id+"F4.imprint","IMPRINT",EDGE,{"derivedFrom":sQuery(id+"F4.wireOp",EDGE,"E26.1.0")}),1.0]])]})])],"isStart":true})]}),makeQuery(id+"F42.opRevolve","SWEPT_FACE",FACE,{"disambiguationData":[OSD([sQuery(id+"F41.wireOp",EDGE,"E32")])]})]});
            var Q10;
            Q10=makeQuery(id+"F42.boolean.opBoolean","INTERSECT",EDGE,{"disambiguationData":[OD(11.0)],"derivedFrom":[makeQuery(id+"F20.boolean.opBoolean","MERGE",FACE,{"derivedFrom":[makeQuery(id+"F19.boolean.opBoolean","MERGE",FACE,{"derivedFrom":[makeQuery(id+"F18.boolean.opBoolean","MERGE",FACE,{"derivedFrom":[makeQuery(id+"F17.boolean.opBoolean","MERGE",FACE,{"derivedFrom":[makeQuery(id+"F16.boolean.opBoolean","MERGE",FACE,{"derivedFrom":[makeQuery(id+"F15.boolean.opBoolean","MERGE",FACE,{"derivedFrom":[makeQuery(id+"F14.boolean.opBoolean","MERGE",FACE,{"derivedFrom":[makeQuery(id+"F13.boolean.opBoolean","MERGE",FACE,{"derivedFrom":[makeQuery(id+"F12.boolean.opBoolean","MERGE",FACE,{"derivedFrom":[makeQuery(id+"F11.boolean.opBoolean","MERGE",FACE,{"derivedFrom":[makeQuery(id+"F10.boolean.opBoolean","MERGE",FACE,{"derivedFrom":[makeQuery(id+"F9.boolean.opBoolean","MERGE",FACE,{"derivedFrom":[makeQuery(id+"F8.boolean.opBoolean","MERGE",FACE,{"derivedFrom":[makeQuery(id+"F7.boolean.opBoolean","MERGE",FACE,{"derivedFrom":[makeQuery(id+"F6.boolean.opBoolean","MERGE",FACE,{"derivedFrom":[makeQuery(id+"F5.boolean.opBoolean","MERGE",FACE,{"derivedFrom":[makeQuery(id+"F1.opRevolve","SWEPT_FACE",FACE,{"disambiguationData":[OSD([sQuery(id+"F0.wireOp",EDGE,"E14")])]}),makeQuery(id+"F5.opLoft","CAP_FACE",FACE,{"disambiguationData":[OSD([makeQuery(id+"F4.imprint","IMPRINT",FACE,{"disambiguationData":[TD([[makeQuery(id+"F4.imprint","IMPRINT",EDGE,{"derivedFrom":sQuery(id+"F4.wireOp",EDGE,"E21")}),1.0]])]})])],"isStart":true})]}),makeQuery(id+"F6.opLoft","CAP_FACE",FACE,{"disambiguationData":[OSD([makeQuery(id+"F4.imprint","IMPRINT",FACE,{"disambiguationData":[TD([[makeQuery(id+"F4.imprint","IMPRINT",EDGE,{"derivedFrom":sQuery(id+"F4.wireOp",EDGE,"E26.15.0")}),1.0]])]})])],"isStart":true})]}),makeQuery(id+"F7.opLoft","CAP_FACE",FACE,{"disambiguationData":[OSD([makeQuery(id+"F4.imprint","IMPRINT",FACE,{"disambiguationData":[TD([[makeQuery(id+"F4.imprint","IMPRINT",EDGE,{"derivedFrom":sQuery(id+"F4.wireOp",EDGE,"E26.14.0")}),1.0]])]})])],"isStart":true})]}),makeQuery(id+"F8.opLoft","CAP_FACE",FACE,{"disambiguationData":[OSD([makeQuery(id+"F4.imprint","IMPRINT",FACE,{"disambiguationData":[TD([[makeQuery(id+"F4.imprint","IMPRINT",EDGE,{"derivedFrom":sQuery(id+"F4.wireOp",EDGE,"E26.13.0")}),1.0]])]})])],"isStart":true})]}),makeQuery(id+"F9.opLoft","CAP_FACE",FACE,{"disambiguationData":[OSD([makeQuery(id+"F4.imprint","IMPRINT",FACE,{"disambiguationData":[TD([[makeQuery(id+"F4.imprint","IMPRINT",EDGE,{"derivedFrom":sQuery(id+"F4.wireOp",EDGE,"E26.12.0")}),1.0]])]})])],"isStart":true})]}),makeQuery(id+"F10.opLoft","CAP_FACE",FACE,{"disambiguationData":[OSD([makeQuery(id+"F4.imprint","IMPRINT",FACE,{"disambiguationData":[TD([[makeQuery(id+"F4.imprint","IMPRINT",EDGE,{"derivedFrom":sQuery(id+"F4.wireOp",EDGE,"E26.11.0")}),1.0]])]})])],"isStart":true})]}),makeQuery(id+"F11.opLoft","CAP_FACE",FACE,{"disambiguationData":[OSD([makeQuery(id+"F4.imprint","IMPRINT",FACE,{"disambiguationData":[TD([[makeQuery(id+"F4.imprint","IMPRINT",EDGE,{"derivedFrom":sQuery(id+"F4.wireOp",EDGE,"E26.10.0")}),1.0]])]})])],"isStart":true})]}),makeQuery(id+"F12.opLoft","CAP_FACE",FACE,{"disambiguationData":[OSD([makeQuery(id+"F4.imprint","IMPRINT",FACE,{"disambiguationData":[TD([[makeQuery(id+"F4.imprint","IMPRINT",EDGE,{"derivedFrom":sQuery(id+"F4.wireOp",EDGE,"E26.9.0")}),1.0]])]})])],"isStart":true})]}),makeQuery(id+"F13.opLoft","CAP_FACE",FACE,{"disambiguationData":[OSD([makeQuery(id+"F4.imprint","IMPRINT",FACE,{"disambiguationData":[TD([[makeQuery(id+"F4.imprint","IMPRINT",EDGE,{"derivedFrom":sQuery(id+"F4.wireOp",EDGE,"E26.8.0")}),1.0]])]})])],"isStart":true})]}),makeQuery(id+"F14.opLoft","CAP_FACE",FACE,{"disambiguationData":[OSD([makeQuery(id+"F4.imprint","IMPRINT",FACE,{"disambiguationData":[TD([[makeQuery(id+"F4.imprint","IMPRINT",EDGE,{"derivedFrom":sQuery(id+"F4.wireOp",EDGE,"E26.7.0")}),1.0]])]})])],"isStart":true})]}),makeQuery(id+"F15.opLoft","CAP_FACE",FACE,{"disambiguationData":[OSD([makeQuery(id+"F4.imprint","IMPRINT",FACE,{"disambiguationData":[TD([[makeQuery(id+"F4.imprint","IMPRINT",EDGE,{"derivedFrom":sQuery(id+"F4.wireOp",EDGE,"E26.6.0")}),1.0]])]})])],"isStart":true})]}),makeQuery(id+"F16.opLoft","CAP_FACE",FACE,{"disambiguationData":[OSD([makeQuery(id+"F4.imprint","IMPRINT",FACE,{"disambiguationData":[TD([[makeQuery(id+"F4.imprint","IMPRINT",EDGE,{"derivedFrom":sQuery(id+"F4.wireOp",EDGE,"E26.5.0")}),1.0]])]})])],"isStart":true})]}),makeQuery(id+"F17.opLoft","CAP_FACE",FACE,{"disambiguationData":[OSD([makeQuery(id+"F4.imprint","IMPRINT",FACE,{"disambiguationData":[TD([[makeQuery(id+"F4.imprint","IMPRINT",EDGE,{"derivedFrom":sQuery(id+"F4.wireOp",EDGE,"E26.4.0")}),1.0]])]})])],"isStart":true})]}),makeQuery(id+"F18.opLoft","CAP_FACE",FACE,{"disambiguationData":[OSD([makeQuery(id+"F4.imprint","IMPRINT",FACE,{"disambiguationData":[TD([[makeQuery(id+"F4.imprint","IMPRINT",EDGE,{"derivedFrom":sQuery(id+"F4.wireOp",EDGE,"E26.3.0")}),1.0]])]})])],"isStart":true})]}),makeQuery(id+"F19.opLoft","CAP_FACE",FACE,{"disambiguationData":[OSD([makeQuery(id+"F4.imprint","IMPRINT",FACE,{"disambiguationData":[TD([[makeQuery(id+"F4.imprint","IMPRINT",EDGE,{"derivedFrom":sQuery(id+"F4.wireOp",EDGE,"E26.2.0")}),1.0]])]})])],"isStart":true})]}),makeQuery(id+"F20.opLoft","CAP_FACE",FACE,{"disambiguationData":[OSD([makeQuery(id+"F4.imprint","IMPRINT",FACE,{"disambiguationData":[TD([[makeQuery(id+"F4.imprint","IMPRINT",EDGE,{"derivedFrom":sQuery(id+"F4.wireOp",EDGE,"E26.1.0")}),1.0]])]})])],"isStart":true})]}),makeQuery(id+"F42.opRevolve","SWEPT_FACE",FACE,{"disambiguationData":[OSD([sQuery(id+"F41.wireOp",EDGE,"E32")])]})]});
            var Q11;
            Q11=makeQuery(id+"F42.boolean.opBoolean","INTERSECT",EDGE,{"disambiguationData":[OD(10.0)],"derivedFrom":[makeQuery(id+"F20.boolean.opBoolean","MERGE",FACE,{"derivedFrom":[makeQuery(id+"F19.boolean.opBoolean","MERGE",FACE,{"derivedFrom":[makeQuery(id+"F18.boolean.opBoolean","MERGE",FACE,{"derivedFrom":[makeQuery(id+"F17.boolean.opBoolean","MERGE",FACE,{"derivedFrom":[makeQuery(id+"F16.boolean.opBoolean","MERGE",FACE,{"derivedFrom":[makeQuery(id+"F15.boolean.opBoolean","MERGE",FACE,{"derivedFrom":[makeQuery(id+"F14.boolean.opBoolean","MERGE",FACE,{"derivedFrom":[makeQuery(id+"F13.boolean.opBoolean","MERGE",FACE,{"derivedFrom":[makeQuery(id+"F12.boolean.opBoolean","MERGE",FACE,{"derivedFrom":[makeQuery(id+"F11.boolean.opBoolean","MERGE",FACE,{"derivedFrom":[makeQuery(id+"F10.boolean.opBoolean","MERGE",FACE,{"derivedFrom":[makeQuery(id+"F9.boolean.opBoolean","MERGE",FACE,{"derivedFrom":[makeQuery(id+"F8.boolean.opBoolean","MERGE",FACE,{"derivedFrom":[makeQuery(id+"F7.boolean.opBoolean","MERGE",FACE,{"derivedFrom":[makeQuery(id+"F6.boolean.opBoolean","MERGE",FACE,{"derivedFrom":[makeQuery(id+"F5.boolean.opBoolean","MERGE",FACE,{"derivedFrom":[makeQuery(id+"F1.opRevolve","SWEPT_FACE",FACE,{"disambiguationData":[OSD([sQuery(id+"F0.wireOp",EDGE,"E14")])]}),makeQuery(id+"F5.opLoft","CAP_FACE",FACE,{"disambiguationData":[OSD([makeQuery(id+"F4.imprint","IMPRINT",FACE,{"disambiguationData":[TD([[makeQuery(id+"F4.imprint","IMPRINT",EDGE,{"derivedFrom":sQuery(id+"F4.wireOp",EDGE,"E21")}),1.0]])]})])],"isStart":true})]}),makeQuery(id+"F6.opLoft","CAP_FACE",FACE,{"disambiguationData":[OSD([makeQuery(id+"F4.imprint","IMPRINT",FACE,{"disambiguationData":[TD([[makeQuery(id+"F4.imprint","IMPRINT",EDGE,{"derivedFrom":sQuery(id+"F4.wireOp",EDGE,"E26.15.0")}),1.0]])]})])],"isStart":true})]}),makeQuery(id+"F7.opLoft","CAP_FACE",FACE,{"disambiguationData":[OSD([makeQuery(id+"F4.imprint","IMPRINT",FACE,{"disambiguationData":[TD([[makeQuery(id+"F4.imprint","IMPRINT",EDGE,{"derivedFrom":sQuery(id+"F4.wireOp",EDGE,"E26.14.0")}),1.0]])]})])],"isStart":true})]}),makeQuery(id+"F8.opLoft","CAP_FACE",FACE,{"disambiguationData":[OSD([makeQuery(id+"F4.imprint","IMPRINT",FACE,{"disambiguationData":[TD([[makeQuery(id+"F4.imprint","IMPRINT",EDGE,{"derivedFrom":sQuery(id+"F4.wireOp",EDGE,"E26.13.0")}),1.0]])]})])],"isStart":true})]}),makeQuery(id+"F9.opLoft","CAP_FACE",FACE,{"disambiguationData":[OSD([makeQuery(id+"F4.imprint","IMPRINT",FACE,{"disambiguationData":[TD([[makeQuery(id+"F4.imprint","IMPRINT",EDGE,{"derivedFrom":sQuery(id+"F4.wireOp",EDGE,"E26.12.0")}),1.0]])]})])],"isStart":true})]}),makeQuery(id+"F10.opLoft","CAP_FACE",FACE,{"disambiguationData":[OSD([makeQuery(id+"F4.imprint","IMPRINT",FACE,{"disambiguationData":[TD([[makeQuery(id+"F4.imprint","IMPRINT",EDGE,{"derivedFrom":sQuery(id+"F4.wireOp",EDGE,"E26.11.0")}),1.0]])]})])],"isStart":true})]}),makeQuery(id+"F11.opLoft","CAP_FACE",FACE,{"disambiguationData":[OSD([makeQuery(id+"F4.imprint","IMPRINT",FACE,{"disambiguationData":[TD([[makeQuery(id+"F4.imprint","IMPRINT",EDGE,{"derivedFrom":sQuery(id+"F4.wireOp",EDGE,"E26.10.0")}),1.0]])]})])],"isStart":true})]}),makeQuery(id+"F12.opLoft","CAP_FACE",FACE,{"disambiguationData":[OSD([makeQuery(id+"F4.imprint","IMPRINT",FACE,{"disambiguationData":[TD([[makeQuery(id+"F4.imprint","IMPRINT",EDGE,{"derivedFrom":sQuery(id+"F4.wireOp",EDGE,"E26.9.0")}),1.0]])]})])],"isStart":true})]}),makeQuery(id+"F13.opLoft","CAP_FACE",FACE,{"disambiguationData":[OSD([makeQuery(id+"F4.imprint","IMPRINT",FACE,{"disambiguationData":[TD([[makeQuery(id+"F4.imprint","IMPRINT",EDGE,{"derivedFrom":sQuery(id+"F4.wireOp",EDGE,"E26.8.0")}),1.0]])]})])],"isStart":true})]}),makeQuery(id+"F14.opLoft","CAP_FACE",FACE,{"disambiguationData":[OSD([makeQuery(id+"F4.imprint","IMPRINT",FACE,{"disambiguationData":[TD([[makeQuery(id+"F4.imprint","IMPRINT",EDGE,{"derivedFrom":sQuery(id+"F4.wireOp",EDGE,"E26.7.0")}),1.0]])]})])],"isStart":true})]}),makeQuery(id+"F15.opLoft","CAP_FACE",FACE,{"disambiguationData":[OSD([makeQuery(id+"F4.imprint","IMPRINT",FACE,{"disambiguationData":[TD([[makeQuery(id+"F4.imprint","IMPRINT",EDGE,{"derivedFrom":sQuery(id+"F4.wireOp",EDGE,"E26.6.0")}),1.0]])]})])],"isStart":true})]}),makeQuery(id+"F16.opLoft","CAP_FACE",FACE,{"disambiguationData":[OSD([makeQuery(id+"F4.imprint","IMPRINT",FACE,{"disambiguationData":[TD([[makeQuery(id+"F4.imprint","IMPRINT",EDGE,{"derivedFrom":sQuery(id+"F4.wireOp",EDGE,"E26.5.0")}),1.0]])]})])],"isStart":true})]}),makeQuery(id+"F17.opLoft","CAP_FACE",FACE,{"disambiguationData":[OSD([makeQuery(id+"F4.imprint","IMPRINT",FACE,{"disambiguationData":[TD([[makeQuery(id+"F4.imprint","IMPRINT",EDGE,{"derivedFrom":sQuery(id+"F4.wireOp",EDGE,"E26.4.0")}),1.0]])]})])],"isStart":true})]}),makeQuery(id+"F18.opLoft","CAP_FACE",FACE,{"disambiguationData":[OSD([makeQuery(id+"F4.imprint","IMPRINT",FACE,{"disambiguationData":[TD([[makeQuery(id+"F4.imprint","IMPRINT",EDGE,{"derivedFrom":sQuery(id+"F4.wireOp",EDGE,"E26.3.0")}),1.0]])]})])],"isStart":true})]}),makeQuery(id+"F19.opLoft","CAP_FACE",FACE,{"disambiguationData":[OSD([makeQuery(id+"F4.imprint","IMPRINT",FACE,{"disambiguationData":[TD([[makeQuery(id+"F4.imprint","IMPRINT",EDGE,{"derivedFrom":sQuery(id+"F4.wireOp",EDGE,"E26.2.0")}),1.0]])]})])],"isStart":true})]}),makeQuery(id+"F20.opLoft","CAP_FACE",FACE,{"disambiguationData":[OSD([makeQuery(id+"F4.imprint","IMPRINT",FACE,{"disambiguationData":[TD([[makeQuery(id+"F4.imprint","IMPRINT",EDGE,{"derivedFrom":sQuery(id+"F4.wireOp",EDGE,"E26.1.0")}),1.0]])]})])],"isStart":true})]}),makeQuery(id+"F42.opRevolve","SWEPT_FACE",FACE,{"disambiguationData":[OSD([sQuery(id+"F41.wireOp",EDGE,"E32")])]})]});
            var Q12;
            Q12=makeQuery(id+"F42.boolean.opBoolean","INTERSECT",EDGE,{"disambiguationData":[OD(9.0)],"derivedFrom":[makeQuery(id+"F20.boolean.opBoolean","MERGE",FACE,{"derivedFrom":[makeQuery(id+"F19.boolean.opBoolean","MERGE",FACE,{"derivedFrom":[makeQuery(id+"F18.boolean.opBoolean","MERGE",FACE,{"derivedFrom":[makeQuery(id+"F17.boolean.opBoolean","MERGE",FACE,{"derivedFrom":[makeQuery(id+"F16.boolean.opBoolean","MERGE",FACE,{"derivedFrom":[makeQuery(id+"F15.boolean.opBoolean","MERGE",FACE,{"derivedFrom":[makeQuery(id+"F14.boolean.opBoolean","MERGE",FACE,{"derivedFrom":[makeQuery(id+"F13.boolean.opBoolean","MERGE",FACE,{"derivedFrom":[makeQuery(id+"F12.boolean.opBoolean","MERGE",FACE,{"derivedFrom":[makeQuery(id+"F11.boolean.opBoolean","MERGE",FACE,{"derivedFrom":[makeQuery(id+"F10.boolean.opBoolean","MERGE",FACE,{"derivedFrom":[makeQuery(id+"F9.boolean.opBoolean","MERGE",FACE,{"derivedFrom":[makeQuery(id+"F8.boolean.opBoolean","MERGE",FACE,{"derivedFrom":[makeQuery(id+"F7.boolean.opBoolean","MERGE",FACE,{"derivedFrom":[makeQuery(id+"F6.boolean.opBoolean","MERGE",FACE,{"derivedFrom":[makeQuery(id+"F5.boolean.opBoolean","MERGE",FACE,{"derivedFrom":[makeQuery(id+"F1.opRevolve","SWEPT_FACE",FACE,{"disambiguationData":[OSD([sQuery(id+"F0.wireOp",EDGE,"E14")])]}),makeQuery(id+"F5.opLoft","CAP_FACE",FACE,{"disambiguationData":[OSD([makeQuery(id+"F4.imprint","IMPRINT",FACE,{"disambiguationData":[TD([[makeQuery(id+"F4.imprint","IMPRINT",EDGE,{"derivedFrom":sQuery(id+"F4.wireOp",EDGE,"E21")}),1.0]])]})])],"isStart":true})]}),makeQuery(id+"F6.opLoft","CAP_FACE",FACE,{"disambiguationData":[OSD([makeQuery(id+"F4.imprint","IMPRINT",FACE,{"disambiguationData":[TD([[makeQuery(id+"F4.imprint","IMPRINT",EDGE,{"derivedFrom":sQuery(id+"F4.wireOp",EDGE,"E26.15.0")}),1.0]])]})])],"isStart":true})]}),makeQuery(id+"F7.opLoft","CAP_FACE",FACE,{"disambiguationData":[OSD([makeQuery(id+"F4.imprint","IMPRINT",FACE,{"disambiguationData":[TD([[makeQuery(id+"F4.imprint","IMPRINT",EDGE,{"derivedFrom":sQuery(id+"F4.wireOp",EDGE,"E26.14.0")}),1.0]])]})])],"isStart":true})]}),makeQuery(id+"F8.opLoft","CAP_FACE",FACE,{"disambiguationData":[OSD([makeQuery(id+"F4.imprint","IMPRINT",FACE,{"disambiguationData":[TD([[makeQuery(id+"F4.imprint","IMPRINT",EDGE,{"derivedFrom":sQuery(id+"F4.wireOp",EDGE,"E26.13.0")}),1.0]])]})])],"isStart":true})]}),makeQuery(id+"F9.opLoft","CAP_FACE",FACE,{"disambiguationData":[OSD([makeQuery(id+"F4.imprint","IMPRINT",FACE,{"disambiguationData":[TD([[makeQuery(id+"F4.imprint","IMPRINT",EDGE,{"derivedFrom":sQuery(id+"F4.wireOp",EDGE,"E26.12.0")}),1.0]])]})])],"isStart":true})]}),makeQuery(id+"F10.opLoft","CAP_FACE",FACE,{"disambiguationData":[OSD([makeQuery(id+"F4.imprint","IMPRINT",FACE,{"disambiguationData":[TD([[makeQuery(id+"F4.imprint","IMPRINT",EDGE,{"derivedFrom":sQuery(id+"F4.wireOp",EDGE,"E26.11.0")}),1.0]])]})])],"isStart":true})]}),makeQuery(id+"F11.opLoft","CAP_FACE",FACE,{"disambiguationData":[OSD([makeQuery(id+"F4.imprint","IMPRINT",FACE,{"disambiguationData":[TD([[makeQuery(id+"F4.imprint","IMPRINT",EDGE,{"derivedFrom":sQuery(id+"F4.wireOp",EDGE,"E26.10.0")}),1.0]])]})])],"isStart":true})]}),makeQuery(id+"F12.opLoft","CAP_FACE",FACE,{"disambiguationData":[OSD([makeQuery(id+"F4.imprint","IMPRINT",FACE,{"disambiguationData":[TD([[makeQuery(id+"F4.imprint","IMPRINT",EDGE,{"derivedFrom":sQuery(id+"F4.wireOp",EDGE,"E26.9.0")}),1.0]])]})])],"isStart":true})]}),makeQuery(id+"F13.opLoft","CAP_FACE",FACE,{"disambiguationData":[OSD([makeQuery(id+"F4.imprint","IMPRINT",FACE,{"disambiguationData":[TD([[makeQuery(id+"F4.imprint","IMPRINT",EDGE,{"derivedFrom":sQuery(id+"F4.wireOp",EDGE,"E26.8.0")}),1.0]])]})])],"isStart":true})]}),makeQuery(id+"F14.opLoft","CAP_FACE",FACE,{"disambiguationData":[OSD([makeQuery(id+"F4.imprint","IMPRINT",FACE,{"disambiguationData":[TD([[makeQuery(id+"F4.imprint","IMPRINT",EDGE,{"derivedFrom":sQuery(id+"F4.wireOp",EDGE,"E26.7.0")}),1.0]])]})])],"isStart":true})]}),makeQuery(id+"F15.opLoft","CAP_FACE",FACE,{"disambiguationData":[OSD([makeQuery(id+"F4.imprint","IMPRINT",FACE,{"disambiguationData":[TD([[makeQuery(id+"F4.imprint","IMPRINT",EDGE,{"derivedFrom":sQuery(id+"F4.wireOp",EDGE,"E26.6.0")}),1.0]])]})])],"isStart":true})]}),makeQuery(id+"F16.opLoft","CAP_FACE",FACE,{"disambiguationData":[OSD([makeQuery(id+"F4.imprint","IMPRINT",FACE,{"disambiguationData":[TD([[makeQuery(id+"F4.imprint","IMPRINT",EDGE,{"derivedFrom":sQuery(id+"F4.wireOp",EDGE,"E26.5.0")}),1.0]])]})])],"isStart":true})]}),makeQuery(id+"F17.opLoft","CAP_FACE",FACE,{"disambiguationData":[OSD([makeQuery(id+"F4.imprint","IMPRINT",FACE,{"disambiguationData":[TD([[makeQuery(id+"F4.imprint","IMPRINT",EDGE,{"derivedFrom":sQuery(id+"F4.wireOp",EDGE,"E26.4.0")}),1.0]])]})])],"isStart":true})]}),makeQuery(id+"F18.opLoft","CAP_FACE",FACE,{"disambiguationData":[OSD([makeQuery(id+"F4.imprint","IMPRINT",FACE,{"disambiguationData":[TD([[makeQuery(id+"F4.imprint","IMPRINT",EDGE,{"derivedFrom":sQuery(id+"F4.wireOp",EDGE,"E26.3.0")}),1.0]])]})])],"isStart":true})]}),makeQuery(id+"F19.opLoft","CAP_FACE",FACE,{"disambiguationData":[OSD([makeQuery(id+"F4.imprint","IMPRINT",FACE,{"disambiguationData":[TD([[makeQuery(id+"F4.imprint","IMPRINT",EDGE,{"derivedFrom":sQuery(id+"F4.wireOp",EDGE,"E26.2.0")}),1.0]])]})])],"isStart":true})]}),makeQuery(id+"F20.opLoft","CAP_FACE",FACE,{"disambiguationData":[OSD([makeQuery(id+"F4.imprint","IMPRINT",FACE,{"disambiguationData":[TD([[makeQuery(id+"F4.imprint","IMPRINT",EDGE,{"derivedFrom":sQuery(id+"F4.wireOp",EDGE,"E26.1.0")}),1.0]])]})])],"isStart":true})]}),makeQuery(id+"F42.opRevolve","SWEPT_FACE",FACE,{"disambiguationData":[OSD([sQuery(id+"F41.wireOp",EDGE,"E32")])]})]});
            var Q13;
            Q13=makeQuery(id+"F42.boolean.opBoolean","INTERSECT",EDGE,{"disambiguationData":[OD(8.0)],"derivedFrom":[makeQuery(id+"F20.boolean.opBoolean","MERGE",FACE,{"derivedFrom":[makeQuery(id+"F19.boolean.opBoolean","MERGE",FACE,{"derivedFrom":[makeQuery(id+"F18.boolean.opBoolean","MERGE",FACE,{"derivedFrom":[makeQuery(id+"F17.boolean.opBoolean","MERGE",FACE,{"derivedFrom":[makeQuery(id+"F16.boolean.opBoolean","MERGE",FACE,{"derivedFrom":[makeQuery(id+"F15.boolean.opBoolean","MERGE",FACE,{"derivedFrom":[makeQuery(id+"F14.boolean.opBoolean","MERGE",FACE,{"derivedFrom":[makeQuery(id+"F13.boolean.opBoolean","MERGE",FACE,{"derivedFrom":[makeQuery(id+"F12.boolean.opBoolean","MERGE",FACE,{"derivedFrom":[makeQuery(id+"F11.boolean.opBoolean","MERGE",FACE,{"derivedFrom":[makeQuery(id+"F10.boolean.opBoolean","MERGE",FACE,{"derivedFrom":[makeQuery(id+"F9.boolean.opBoolean","MERGE",FACE,{"derivedFrom":[makeQuery(id+"F8.boolean.opBoolean","MERGE",FACE,{"derivedFrom":[makeQuery(id+"F7.boolean.opBoolean","MERGE",FACE,{"derivedFrom":[makeQuery(id+"F6.boolean.opBoolean","MERGE",FACE,{"derivedFrom":[makeQuery(id+"F5.boolean.opBoolean","MERGE",FACE,{"derivedFrom":[makeQuery(id+"F1.opRevolve","SWEPT_FACE",FACE,{"disambiguationData":[OSD([sQuery(id+"F0.wireOp",EDGE,"E14")])]}),makeQuery(id+"F5.opLoft","CAP_FACE",FACE,{"disambiguationData":[OSD([makeQuery(id+"F4.imprint","IMPRINT",FACE,{"disambiguationData":[TD([[makeQuery(id+"F4.imprint","IMPRINT",EDGE,{"derivedFrom":sQuery(id+"F4.wireOp",EDGE,"E21")}),1.0]])]})])],"isStart":true})]}),makeQuery(id+"F6.opLoft","CAP_FACE",FACE,{"disambiguationData":[OSD([makeQuery(id+"F4.imprint","IMPRINT",FACE,{"disambiguationData":[TD([[makeQuery(id+"F4.imprint","IMPRINT",EDGE,{"derivedFrom":sQuery(id+"F4.wireOp",EDGE,"E26.15.0")}),1.0]])]})])],"isStart":true})]}),makeQuery(id+"F7.opLoft","CAP_FACE",FACE,{"disambiguationData":[OSD([makeQuery(id+"F4.imprint","IMPRINT",FACE,{"disambiguationData":[TD([[makeQuery(id+"F4.imprint","IMPRINT",EDGE,{"derivedFrom":sQuery(id+"F4.wireOp",EDGE,"E26.14.0")}),1.0]])]})])],"isStart":true})]}),makeQuery(id+"F8.opLoft","CAP_FACE",FACE,{"disambiguationData":[OSD([makeQuery(id+"F4.imprint","IMPRINT",FACE,{"disambiguationData":[TD([[makeQuery(id+"F4.imprint","IMPRINT",EDGE,{"derivedFrom":sQuery(id+"F4.wireOp",EDGE,"E26.13.0")}),1.0]])]})])],"isStart":true})]}),makeQuery(id+"F9.opLoft","CAP_FACE",FACE,{"disambiguationData":[OSD([makeQuery(id+"F4.imprint","IMPRINT",FACE,{"disambiguationData":[TD([[makeQuery(id+"F4.imprint","IMPRINT",EDGE,{"derivedFrom":sQuery(id+"F4.wireOp",EDGE,"E26.12.0")}),1.0]])]})])],"isStart":true})]}),makeQuery(id+"F10.opLoft","CAP_FACE",FACE,{"disambiguationData":[OSD([makeQuery(id+"F4.imprint","IMPRINT",FACE,{"disambiguationData":[TD([[makeQuery(id+"F4.imprint","IMPRINT",EDGE,{"derivedFrom":sQuery(id+"F4.wireOp",EDGE,"E26.11.0")}),1.0]])]})])],"isStart":true})]}),makeQuery(id+"F11.opLoft","CAP_FACE",FACE,{"disambiguationData":[OSD([makeQuery(id+"F4.imprint","IMPRINT",FACE,{"disambiguationData":[TD([[makeQuery(id+"F4.imprint","IMPRINT",EDGE,{"derivedFrom":sQuery(id+"F4.wireOp",EDGE,"E26.10.0")}),1.0]])]})])],"isStart":true})]}),makeQuery(id+"F12.opLoft","CAP_FACE",FACE,{"disambiguationData":[OSD([makeQuery(id+"F4.imprint","IMPRINT",FACE,{"disambiguationData":[TD([[makeQuery(id+"F4.imprint","IMPRINT",EDGE,{"derivedFrom":sQuery(id+"F4.wireOp",EDGE,"E26.9.0")}),1.0]])]})])],"isStart":true})]}),makeQuery(id+"F13.opLoft","CAP_FACE",FACE,{"disambiguationData":[OSD([makeQuery(id+"F4.imprint","IMPRINT",FACE,{"disambiguationData":[TD([[makeQuery(id+"F4.imprint","IMPRINT",EDGE,{"derivedFrom":sQuery(id+"F4.wireOp",EDGE,"E26.8.0")}),1.0]])]})])],"isStart":true})]}),makeQuery(id+"F14.opLoft","CAP_FACE",FACE,{"disambiguationData":[OSD([makeQuery(id+"F4.imprint","IMPRINT",FACE,{"disambiguationData":[TD([[makeQuery(id+"F4.imprint","IMPRINT",EDGE,{"derivedFrom":sQuery(id+"F4.wireOp",EDGE,"E26.7.0")}),1.0]])]})])],"isStart":true})]}),makeQuery(id+"F15.opLoft","CAP_FACE",FACE,{"disambiguationData":[OSD([makeQuery(id+"F4.imprint","IMPRINT",FACE,{"disambiguationData":[TD([[makeQuery(id+"F4.imprint","IMPRINT",EDGE,{"derivedFrom":sQuery(id+"F4.wireOp",EDGE,"E26.6.0")}),1.0]])]})])],"isStart":true})]}),makeQuery(id+"F16.opLoft","CAP_FACE",FACE,{"disambiguationData":[OSD([makeQuery(id+"F4.imprint","IMPRINT",FACE,{"disambiguationData":[TD([[makeQuery(id+"F4.imprint","IMPRINT",EDGE,{"derivedFrom":sQuery(id+"F4.wireOp",EDGE,"E26.5.0")}),1.0]])]})])],"isStart":true})]}),makeQuery(id+"F17.opLoft","CAP_FACE",FACE,{"disambiguationData":[OSD([makeQuery(id+"F4.imprint","IMPRINT",FACE,{"disambiguationData":[TD([[makeQuery(id+"F4.imprint","IMPRINT",EDGE,{"derivedFrom":sQuery(id+"F4.wireOp",EDGE,"E26.4.0")}),1.0]])]})])],"isStart":true})]}),makeQuery(id+"F18.opLoft","CAP_FACE",FACE,{"disambiguationData":[OSD([makeQuery(id+"F4.imprint","IMPRINT",FACE,{"disambiguationData":[TD([[makeQuery(id+"F4.imprint","IMPRINT",EDGE,{"derivedFrom":sQuery(id+"F4.wireOp",EDGE,"E26.3.0")}),1.0]])]})])],"isStart":true})]}),makeQuery(id+"F19.opLoft","CAP_FACE",FACE,{"disambiguationData":[OSD([makeQuery(id+"F4.imprint","IMPRINT",FACE,{"disambiguationData":[TD([[makeQuery(id+"F4.imprint","IMPRINT",EDGE,{"derivedFrom":sQuery(id+"F4.wireOp",EDGE,"E26.2.0")}),1.0]])]})])],"isStart":true})]}),makeQuery(id+"F20.opLoft","CAP_FACE",FACE,{"disambiguationData":[OSD([makeQuery(id+"F4.imprint","IMPRINT",FACE,{"disambiguationData":[TD([[makeQuery(id+"F4.imprint","IMPRINT",EDGE,{"derivedFrom":sQuery(id+"F4.wireOp",EDGE,"E26.1.0")}),1.0]])]})])],"isStart":true})]}),makeQuery(id+"F42.opRevolve","SWEPT_FACE",FACE,{"disambiguationData":[OSD([sQuery(id+"F41.wireOp",EDGE,"E32")])]})]});
            var Q14;
            Q14=makeQuery(id+"F42.boolean.opBoolean","INTERSECT",EDGE,{"disambiguationData":[OD(7.0)],"derivedFrom":[makeQuery(id+"F20.boolean.opBoolean","MERGE",FACE,{"derivedFrom":[makeQuery(id+"F19.boolean.opBoolean","MERGE",FACE,{"derivedFrom":[makeQuery(id+"F18.boolean.opBoolean","MERGE",FACE,{"derivedFrom":[makeQuery(id+"F17.boolean.opBoolean","MERGE",FACE,{"derivedFrom":[makeQuery(id+"F16.boolean.opBoolean","MERGE",FACE,{"derivedFrom":[makeQuery(id+"F15.boolean.opBoolean","MERGE",FACE,{"derivedFrom":[makeQuery(id+"F14.boolean.opBoolean","MERGE",FACE,{"derivedFrom":[makeQuery(id+"F13.boolean.opBoolean","MERGE",FACE,{"derivedFrom":[makeQuery(id+"F12.boolean.opBoolean","MERGE",FACE,{"derivedFrom":[makeQuery(id+"F11.boolean.opBoolean","MERGE",FACE,{"derivedFrom":[makeQuery(id+"F10.boolean.opBoolean","MERGE",FACE,{"derivedFrom":[makeQuery(id+"F9.boolean.opBoolean","MERGE",FACE,{"derivedFrom":[makeQuery(id+"F8.boolean.opBoolean","MERGE",FACE,{"derivedFrom":[makeQuery(id+"F7.boolean.opBoolean","MERGE",FACE,{"derivedFrom":[makeQuery(id+"F6.boolean.opBoolean","MERGE",FACE,{"derivedFrom":[makeQuery(id+"F5.boolean.opBoolean","MERGE",FACE,{"derivedFrom":[makeQuery(id+"F1.opRevolve","SWEPT_FACE",FACE,{"disambiguationData":[OSD([sQuery(id+"F0.wireOp",EDGE,"E14")])]}),makeQuery(id+"F5.opLoft","CAP_FACE",FACE,{"disambiguationData":[OSD([makeQuery(id+"F4.imprint","IMPRINT",FACE,{"disambiguationData":[TD([[makeQuery(id+"F4.imprint","IMPRINT",EDGE,{"derivedFrom":sQuery(id+"F4.wireOp",EDGE,"E21")}),1.0]])]})])],"isStart":true})]}),makeQuery(id+"F6.opLoft","CAP_FACE",FACE,{"disambiguationData":[OSD([makeQuery(id+"F4.imprint","IMPRINT",FACE,{"disambiguationData":[TD([[makeQuery(id+"F4.imprint","IMPRINT",EDGE,{"derivedFrom":sQuery(id+"F4.wireOp",EDGE,"E26.15.0")}),1.0]])]})])],"isStart":true})]}),makeQuery(id+"F7.opLoft","CAP_FACE",FACE,{"disambiguationData":[OSD([makeQuery(id+"F4.imprint","IMPRINT",FACE,{"disambiguationData":[TD([[makeQuery(id+"F4.imprint","IMPRINT",EDGE,{"derivedFrom":sQuery(id+"F4.wireOp",EDGE,"E26.14.0")}),1.0]])]})])],"isStart":true})]}),makeQuery(id+"F8.opLoft","CAP_FACE",FACE,{"disambiguationData":[OSD([makeQuery(id+"F4.imprint","IMPRINT",FACE,{"disambiguationData":[TD([[makeQuery(id+"F4.imprint","IMPRINT",EDGE,{"derivedFrom":sQuery(id+"F4.wireOp",EDGE,"E26.13.0")}),1.0]])]})])],"isStart":true})]}),makeQuery(id+"F9.opLoft","CAP_FACE",FACE,{"disambiguationData":[OSD([makeQuery(id+"F4.imprint","IMPRINT",FACE,{"disambiguationData":[TD([[makeQuery(id+"F4.imprint","IMPRINT",EDGE,{"derivedFrom":sQuery(id+"F4.wireOp",EDGE,"E26.12.0")}),1.0]])]})])],"isStart":true})]}),makeQuery(id+"F10.opLoft","CAP_FACE",FACE,{"disambiguationData":[OSD([makeQuery(id+"F4.imprint","IMPRINT",FACE,{"disambiguationData":[TD([[makeQuery(id+"F4.imprint","IMPRINT",EDGE,{"derivedFrom":sQuery(id+"F4.wireOp",EDGE,"E26.11.0")}),1.0]])]})])],"isStart":true})]}),makeQuery(id+"F11.opLoft","CAP_FACE",FACE,{"disambiguationData":[OSD([makeQuery(id+"F4.imprint","IMPRINT",FACE,{"disambiguationData":[TD([[makeQuery(id+"F4.imprint","IMPRINT",EDGE,{"derivedFrom":sQuery(id+"F4.wireOp",EDGE,"E26.10.0")}),1.0]])]})])],"isStart":true})]}),makeQuery(id+"F12.opLoft","CAP_FACE",FACE,{"disambiguationData":[OSD([makeQuery(id+"F4.imprint","IMPRINT",FACE,{"disambiguationData":[TD([[makeQuery(id+"F4.imprint","IMPRINT",EDGE,{"derivedFrom":sQuery(id+"F4.wireOp",EDGE,"E26.9.0")}),1.0]])]})])],"isStart":true})]}),makeQuery(id+"F13.opLoft","CAP_FACE",FACE,{"disambiguationData":[OSD([makeQuery(id+"F4.imprint","IMPRINT",FACE,{"disambiguationData":[TD([[makeQuery(id+"F4.imprint","IMPRINT",EDGE,{"derivedFrom":sQuery(id+"F4.wireOp",EDGE,"E26.8.0")}),1.0]])]})])],"isStart":true})]}),makeQuery(id+"F14.opLoft","CAP_FACE",FACE,{"disambiguationData":[OSD([makeQuery(id+"F4.imprint","IMPRINT",FACE,{"disambiguationData":[TD([[makeQuery(id+"F4.imprint","IMPRINT",EDGE,{"derivedFrom":sQuery(id+"F4.wireOp",EDGE,"E26.7.0")}),1.0]])]})])],"isStart":true})]}),makeQuery(id+"F15.opLoft","CAP_FACE",FACE,{"disambiguationData":[OSD([makeQuery(id+"F4.imprint","IMPRINT",FACE,{"disambiguationData":[TD([[makeQuery(id+"F4.imprint","IMPRINT",EDGE,{"derivedFrom":sQuery(id+"F4.wireOp",EDGE,"E26.6.0")}),1.0]])]})])],"isStart":true})]}),makeQuery(id+"F16.opLoft","CAP_FACE",FACE,{"disambiguationData":[OSD([makeQuery(id+"F4.imprint","IMPRINT",FACE,{"disambiguationData":[TD([[makeQuery(id+"F4.imprint","IMPRINT",EDGE,{"derivedFrom":sQuery(id+"F4.wireOp",EDGE,"E26.5.0")}),1.0]])]})])],"isStart":true})]}),makeQuery(id+"F17.opLoft","CAP_FACE",FACE,{"disambiguationData":[OSD([makeQuery(id+"F4.imprint","IMPRINT",FACE,{"disambiguationData":[TD([[makeQuery(id+"F4.imprint","IMPRINT",EDGE,{"derivedFrom":sQuery(id+"F4.wireOp",EDGE,"E26.4.0")}),1.0]])]})])],"isStart":true})]}),makeQuery(id+"F18.opLoft","CAP_FACE",FACE,{"disambiguationData":[OSD([makeQuery(id+"F4.imprint","IMPRINT",FACE,{"disambiguationData":[TD([[makeQuery(id+"F4.imprint","IMPRINT",EDGE,{"derivedFrom":sQuery(id+"F4.wireOp",EDGE,"E26.3.0")}),1.0]])]})])],"isStart":true})]}),makeQuery(id+"F19.opLoft","CAP_FACE",FACE,{"disambiguationData":[OSD([makeQuery(id+"F4.imprint","IMPRINT",FACE,{"disambiguationData":[TD([[makeQuery(id+"F4.imprint","IMPRINT",EDGE,{"derivedFrom":sQuery(id+"F4.wireOp",EDGE,"E26.2.0")}),1.0]])]})])],"isStart":true})]}),makeQuery(id+"F20.opLoft","CAP_FACE",FACE,{"disambiguationData":[OSD([makeQuery(id+"F4.imprint","IMPRINT",FACE,{"disambiguationData":[TD([[makeQuery(id+"F4.imprint","IMPRINT",EDGE,{"derivedFrom":sQuery(id+"F4.wireOp",EDGE,"E26.1.0")}),1.0]])]})])],"isStart":true})]}),makeQuery(id+"F42.opRevolve","SWEPT_FACE",FACE,{"disambiguationData":[OSD([sQuery(id+"F41.wireOp",EDGE,"E32")])]})]});
            var Q15;
            Q15=makeQuery(id+"F42.boolean.opBoolean","INTERSECT",EDGE,{"disambiguationData":[OD(6.0)],"derivedFrom":[makeQuery(id+"F20.boolean.opBoolean","MERGE",FACE,{"derivedFrom":[makeQuery(id+"F19.boolean.opBoolean","MERGE",FACE,{"derivedFrom":[makeQuery(id+"F18.boolean.opBoolean","MERGE",FACE,{"derivedFrom":[makeQuery(id+"F17.boolean.opBoolean","MERGE",FACE,{"derivedFrom":[makeQuery(id+"F16.boolean.opBoolean","MERGE",FACE,{"derivedFrom":[makeQuery(id+"F15.boolean.opBoolean","MERGE",FACE,{"derivedFrom":[makeQuery(id+"F14.boolean.opBoolean","MERGE",FACE,{"derivedFrom":[makeQuery(id+"F13.boolean.opBoolean","MERGE",FACE,{"derivedFrom":[makeQuery(id+"F12.boolean.opBoolean","MERGE",FACE,{"derivedFrom":[makeQuery(id+"F11.boolean.opBoolean","MERGE",FACE,{"derivedFrom":[makeQuery(id+"F10.boolean.opBoolean","MERGE",FACE,{"derivedFrom":[makeQuery(id+"F9.boolean.opBoolean","MERGE",FACE,{"derivedFrom":[makeQuery(id+"F8.boolean.opBoolean","MERGE",FACE,{"derivedFrom":[makeQuery(id+"F7.boolean.opBoolean","MERGE",FACE,{"derivedFrom":[makeQuery(id+"F6.boolean.opBoolean","MERGE",FACE,{"derivedFrom":[makeQuery(id+"F5.boolean.opBoolean","MERGE",FACE,{"derivedFrom":[makeQuery(id+"F1.opRevolve","SWEPT_FACE",FACE,{"disambiguationData":[OSD([sQuery(id+"F0.wireOp",EDGE,"E14")])]}),makeQuery(id+"F5.opLoft","CAP_FACE",FACE,{"disambiguationData":[OSD([makeQuery(id+"F4.imprint","IMPRINT",FACE,{"disambiguationData":[TD([[makeQuery(id+"F4.imprint","IMPRINT",EDGE,{"derivedFrom":sQuery(id+"F4.wireOp",EDGE,"E21")}),1.0]])]})])],"isStart":true})]}),makeQuery(id+"F6.opLoft","CAP_FACE",FACE,{"disambiguationData":[OSD([makeQuery(id+"F4.imprint","IMPRINT",FACE,{"disambiguationData":[TD([[makeQuery(id+"F4.imprint","IMPRINT",EDGE,{"derivedFrom":sQuery(id+"F4.wireOp",EDGE,"E26.15.0")}),1.0]])]})])],"isStart":true})]}),makeQuery(id+"F7.opLoft","CAP_FACE",FACE,{"disambiguationData":[OSD([makeQuery(id+"F4.imprint","IMPRINT",FACE,{"disambiguationData":[TD([[makeQuery(id+"F4.imprint","IMPRINT",EDGE,{"derivedFrom":sQuery(id+"F4.wireOp",EDGE,"E26.14.0")}),1.0]])]})])],"isStart":true})]}),makeQuery(id+"F8.opLoft","CAP_FACE",FACE,{"disambiguationData":[OSD([makeQuery(id+"F4.imprint","IMPRINT",FACE,{"disambiguationData":[TD([[makeQuery(id+"F4.imprint","IMPRINT",EDGE,{"derivedFrom":sQuery(id+"F4.wireOp",EDGE,"E26.13.0")}),1.0]])]})])],"isStart":true})]}),makeQuery(id+"F9.opLoft","CAP_FACE",FACE,{"disambiguationData":[OSD([makeQuery(id+"F4.imprint","IMPRINT",FACE,{"disambiguationData":[TD([[makeQuery(id+"F4.imprint","IMPRINT",EDGE,{"derivedFrom":sQuery(id+"F4.wireOp",EDGE,"E26.12.0")}),1.0]])]})])],"isStart":true})]}),makeQuery(id+"F10.opLoft","CAP_FACE",FACE,{"disambiguationData":[OSD([makeQuery(id+"F4.imprint","IMPRINT",FACE,{"disambiguationData":[TD([[makeQuery(id+"F4.imprint","IMPRINT",EDGE,{"derivedFrom":sQuery(id+"F4.wireOp",EDGE,"E26.11.0")}),1.0]])]})])],"isStart":true})]}),makeQuery(id+"F11.opLoft","CAP_FACE",FACE,{"disambiguationData":[OSD([makeQuery(id+"F4.imprint","IMPRINT",FACE,{"disambiguationData":[TD([[makeQuery(id+"F4.imprint","IMPRINT",EDGE,{"derivedFrom":sQuery(id+"F4.wireOp",EDGE,"E26.10.0")}),1.0]])]})])],"isStart":true})]}),makeQuery(id+"F12.opLoft","CAP_FACE",FACE,{"disambiguationData":[OSD([makeQuery(id+"F4.imprint","IMPRINT",FACE,{"disambiguationData":[TD([[makeQuery(id+"F4.imprint","IMPRINT",EDGE,{"derivedFrom":sQuery(id+"F4.wireOp",EDGE,"E26.9.0")}),1.0]])]})])],"isStart":true})]}),makeQuery(id+"F13.opLoft","CAP_FACE",FACE,{"disambiguationData":[OSD([makeQuery(id+"F4.imprint","IMPRINT",FACE,{"disambiguationData":[TD([[makeQuery(id+"F4.imprint","IMPRINT",EDGE,{"derivedFrom":sQuery(id+"F4.wireOp",EDGE,"E26.8.0")}),1.0]])]})])],"isStart":true})]}),makeQuery(id+"F14.opLoft","CAP_FACE",FACE,{"disambiguationData":[OSD([makeQuery(id+"F4.imprint","IMPRINT",FACE,{"disambiguationData":[TD([[makeQuery(id+"F4.imprint","IMPRINT",EDGE,{"derivedFrom":sQuery(id+"F4.wireOp",EDGE,"E26.7.0")}),1.0]])]})])],"isStart":true})]}),makeQuery(id+"F15.opLoft","CAP_FACE",FACE,{"disambiguationData":[OSD([makeQuery(id+"F4.imprint","IMPRINT",FACE,{"disambiguationData":[TD([[makeQuery(id+"F4.imprint","IMPRINT",EDGE,{"derivedFrom":sQuery(id+"F4.wireOp",EDGE,"E26.6.0")}),1.0]])]})])],"isStart":true})]}),makeQuery(id+"F16.opLoft","CAP_FACE",FACE,{"disambiguationData":[OSD([makeQuery(id+"F4.imprint","IMPRINT",FACE,{"disambiguationData":[TD([[makeQuery(id+"F4.imprint","IMPRINT",EDGE,{"derivedFrom":sQuery(id+"F4.wireOp",EDGE,"E26.5.0")}),1.0]])]})])],"isStart":true})]}),makeQuery(id+"F17.opLoft","CAP_FACE",FACE,{"disambiguationData":[OSD([makeQuery(id+"F4.imprint","IMPRINT",FACE,{"disambiguationData":[TD([[makeQuery(id+"F4.imprint","IMPRINT",EDGE,{"derivedFrom":sQuery(id+"F4.wireOp",EDGE,"E26.4.0")}),1.0]])]})])],"isStart":true})]}),makeQuery(id+"F18.opLoft","CAP_FACE",FACE,{"disambiguationData":[OSD([makeQuery(id+"F4.imprint","IMPRINT",FACE,{"disambiguationData":[TD([[makeQuery(id+"F4.imprint","IMPRINT",EDGE,{"derivedFrom":sQuery(id+"F4.wireOp",EDGE,"E26.3.0")}),1.0]])]})])],"isStart":true})]}),makeQuery(id+"F19.opLoft","CAP_FACE",FACE,{"disambiguationData":[OSD([makeQuery(id+"F4.imprint","IMPRINT",FACE,{"disambiguationData":[TD([[makeQuery(id+"F4.imprint","IMPRINT",EDGE,{"derivedFrom":sQuery(id+"F4.wireOp",EDGE,"E26.2.0")}),1.0]])]})])],"isStart":true})]}),makeQuery(id+"F20.opLoft","CAP_FACE",FACE,{"disambiguationData":[OSD([makeQuery(id+"F4.imprint","IMPRINT",FACE,{"disambiguationData":[TD([[makeQuery(id+"F4.imprint","IMPRINT",EDGE,{"derivedFrom":sQuery(id+"F4.wireOp",EDGE,"E26.1.0")}),1.0]])]})])],"isStart":true})]}),makeQuery(id+"F42.opRevolve","SWEPT_FACE",FACE,{"disambiguationData":[OSD([sQuery(id+"F41.wireOp",EDGE,"E32")])]})]});
            var Q16;
            Q16=makeQuery(id+"F42.boolean.opBoolean","INTERSECT",EDGE,{"derivedFrom":[makeQuery(id+"F27.opLoft","CAP_FACE",FACE,{"disambiguationData":[OSD([makeQuery(id+"F22.imprint","IMPRINT",FACE,{"disambiguationData":[TD([[makeQuery(id+"F22.imprint","IMPRINT",EDGE,{"derivedFrom":sQuery(id+"F22.wireOp",EDGE,"E28.4.0")}),-1.0]])]})])],"isStart":true}),makeQuery(id+"F42.opRevolve","SWEPT_FACE",FACE,{"disambiguationData":[OSD([sQuery(id+"F41.wireOp",EDGE,"E32")])]})]});
            var Q17;
            Q17=makeQuery(id+"F42.boolean.opBoolean","INTERSECT",EDGE,{"derivedFrom":[makeQuery(id+"F26.opLoft","CAP_FACE",FACE,{"disambiguationData":[OSD([makeQuery(id+"F22.imprint","IMPRINT",FACE,{"disambiguationData":[TD([[makeQuery(id+"F22.imprint","IMPRINT",EDGE,{"derivedFrom":sQuery(id+"F22.wireOp",EDGE,"E28.3.0")}),-1.0]])]})])],"isStart":true}),makeQuery(id+"F42.opRevolve","SWEPT_FACE",FACE,{"disambiguationData":[OSD([sQuery(id+"F41.wireOp",EDGE,"E32")])]})]});
            var Q18;
            Q18=makeQuery(id+"F42.boolean.opBoolean","INTERSECT",EDGE,{"derivedFrom":[makeQuery(id+"F25.opLoft","CAP_FACE",FACE,{"disambiguationData":[OSD([makeQuery(id+"F22.imprint","IMPRINT",FACE,{"disambiguationData":[TD([[makeQuery(id+"F22.imprint","IMPRINT",EDGE,{"derivedFrom":sQuery(id+"F22.wireOp",EDGE,"E28.2.0")}),-1.0]])]})])],"isStart":true}),makeQuery(id+"F42.opRevolve","SWEPT_FACE",FACE,{"disambiguationData":[OSD([sQuery(id+"F41.wireOp",EDGE,"E32")])]})]});
            var Q19;
            Q19=makeQuery(id+"F42.boolean.opBoolean","INTERSECT",EDGE,{"derivedFrom":[makeQuery(id+"F24.opLoft","CAP_FACE",FACE,{"disambiguationData":[OSD([makeQuery(id+"F22.imprint","IMPRINT",FACE,{"disambiguationData":[TD([[makeQuery(id+"F22.imprint","IMPRINT",EDGE,{"derivedFrom":sQuery(id+"F22.wireOp",EDGE,"E28.1.0")}),-1.0]])]})])],"isStart":true}),makeQuery(id+"F42.opRevolve","SWEPT_FACE",FACE,{"disambiguationData":[OSD([sQuery(id+"F41.wireOp",EDGE,"E32")])]})]});
            var Q20;
            Q20=makeQuery(id+"F42.boolean.opBoolean","INTERSECT",EDGE,{"derivedFrom":[makeQuery(id+"F23.opLoft","CAP_FACE",FACE,{"disambiguationData":[OSD([makeQuery(id+"F22.imprint","IMPRINT",FACE,{"disambiguationData":[TD([[makeQuery(id+"F22.imprint","IMPRINT",EDGE,{"derivedFrom":sQuery(id+"F22.wireOp",EDGE,"E27.bottom")}),1.0]])]})])],"isStart":true}),makeQuery(id+"F42.opRevolve","SWEPT_FACE",FACE,{"disambiguationData":[OSD([sQuery(id+"F41.wireOp",EDGE,"E32")])]})]});
            var Q21;
            Q21=makeQuery(id+"F42.boolean.opBoolean","INTERSECT",EDGE,{"derivedFrom":[makeQuery(id+"F38.opLoft","CAP_FACE",FACE,{"disambiguationData":[OSD([makeQuery(id+"F22.imprint","IMPRINT",FACE,{"disambiguationData":[TD([[makeQuery(id+"F22.imprint","IMPRINT",EDGE,{"derivedFrom":sQuery(id+"F22.wireOp",EDGE,"E28.15.0")}),-1.0]])]})])],"isStart":true}),makeQuery(id+"F42.opRevolve","SWEPT_FACE",FACE,{"disambiguationData":[OSD([sQuery(id+"F41.wireOp",EDGE,"E32")])]})]});
            var Q22;
            Q22=makeQuery(id+"F42.boolean.opBoolean","INTERSECT",EDGE,{"derivedFrom":[makeQuery(id+"F37.opLoft","CAP_FACE",FACE,{"disambiguationData":[OSD([makeQuery(id+"F22.imprint","IMPRINT",FACE,{"disambiguationData":[TD([[makeQuery(id+"F22.imprint","IMPRINT",EDGE,{"derivedFrom":sQuery(id+"F22.wireOp",EDGE,"E28.14.0")}),-1.0]])]})])],"isStart":true}),makeQuery(id+"F42.opRevolve","SWEPT_FACE",FACE,{"disambiguationData":[OSD([sQuery(id+"F41.wireOp",EDGE,"E32")])]})]});
            var Q23;
            Q23=makeQuery(id+"F42.boolean.opBoolean","INTERSECT",EDGE,{"derivedFrom":[makeQuery(id+"F36.opLoft","CAP_FACE",FACE,{"disambiguationData":[OSD([makeQuery(id+"F22.imprint","IMPRINT",FACE,{"disambiguationData":[TD([[makeQuery(id+"F22.imprint","IMPRINT",EDGE,{"derivedFrom":sQuery(id+"F22.wireOp",EDGE,"E28.13.0")}),-1.0]])]})])],"isStart":true}),makeQuery(id+"F42.opRevolve","SWEPT_FACE",FACE,{"disambiguationData":[OSD([sQuery(id+"F41.wireOp",EDGE,"E32")])]})]});
            var Q24;
            Q24=makeQuery(id+"F42.boolean.opBoolean","INTERSECT",EDGE,{"derivedFrom":[makeQuery(id+"F35.opLoft","CAP_FACE",FACE,{"disambiguationData":[OSD([makeQuery(id+"F22.imprint","IMPRINT",FACE,{"disambiguationData":[TD([[makeQuery(id+"F22.imprint","IMPRINT",EDGE,{"derivedFrom":sQuery(id+"F22.wireOp",EDGE,"E28.12.0")}),-1.0]])]})])],"isStart":true}),makeQuery(id+"F42.opRevolve","SWEPT_FACE",FACE,{"disambiguationData":[OSD([sQuery(id+"F41.wireOp",EDGE,"E32")])]})]});
            var Q25;
            Q25=makeQuery(id+"F42.boolean.opBoolean","INTERSECT",EDGE,{"derivedFrom":[makeQuery(id+"F34.opLoft","CAP_FACE",FACE,{"disambiguationData":[OSD([makeQuery(id+"F22.imprint","IMPRINT",FACE,{"disambiguationData":[TD([[makeQuery(id+"F22.imprint","IMPRINT",EDGE,{"derivedFrom":sQuery(id+"F22.wireOp",EDGE,"E28.11.0")}),-1.0]])]})])],"isStart":true}),makeQuery(id+"F42.opRevolve","SWEPT_FACE",FACE,{"disambiguationData":[OSD([sQuery(id+"F41.wireOp",EDGE,"E32")])]})]});
            var Q26;
            Q26=makeQuery(id+"F42.boolean.opBoolean","INTERSECT",EDGE,{"derivedFrom":[makeQuery(id+"F33.opLoft","CAP_FACE",FACE,{"disambiguationData":[OSD([makeQuery(id+"F22.imprint","IMPRINT",FACE,{"disambiguationData":[TD([[makeQuery(id+"F22.imprint","IMPRINT",EDGE,{"derivedFrom":sQuery(id+"F22.wireOp",EDGE,"E28.10.0")}),-1.0]])]})])],"isStart":true}),makeQuery(id+"F42.opRevolve","SWEPT_FACE",FACE,{"disambiguationData":[OSD([sQuery(id+"F41.wireOp",EDGE,"E32")])]})]});
            var Q27;
            Q27=makeQuery(id+"F42.boolean.opBoolean","INTERSECT",EDGE,{"derivedFrom":[makeQuery(id+"F32.opLoft","CAP_FACE",FACE,{"disambiguationData":[OSD([makeQuery(id+"F22.imprint","IMPRINT",FACE,{"disambiguationData":[TD([[makeQuery(id+"F22.imprint","IMPRINT",EDGE,{"derivedFrom":sQuery(id+"F22.wireOp",EDGE,"E28.9.0")}),-1.0]])]})])],"isStart":true}),makeQuery(id+"F42.opRevolve","SWEPT_FACE",FACE,{"disambiguationData":[OSD([sQuery(id+"F41.wireOp",EDGE,"E32")])]})]});
            var Q28;
            Q28=makeQuery(id+"F42.boolean.opBoolean","INTERSECT",EDGE,{"derivedFrom":[makeQuery(id+"F31.opLoft","CAP_FACE",FACE,{"disambiguationData":[OSD([makeQuery(id+"F22.imprint","IMPRINT",FACE,{"disambiguationData":[TD([[makeQuery(id+"F22.imprint","IMPRINT",EDGE,{"derivedFrom":sQuery(id+"F22.wireOp",EDGE,"E28.8.0")}),-1.0]])]})])],"isStart":true}),makeQuery(id+"F42.opRevolve","SWEPT_FACE",FACE,{"disambiguationData":[OSD([sQuery(id+"F41.wireOp",EDGE,"E32")])]})]});
            var Q29;
            Q29=makeQuery(id+"F42.boolean.opBoolean","INTERSECT",EDGE,{"derivedFrom":[makeQuery(id+"F30.opLoft","CAP_FACE",FACE,{"disambiguationData":[OSD([makeQuery(id+"F22.imprint","IMPRINT",FACE,{"disambiguationData":[TD([[makeQuery(id+"F22.imprint","IMPRINT",EDGE,{"derivedFrom":sQuery(id+"F22.wireOp",EDGE,"E28.7.0")}),-1.0]])]})])],"isStart":true}),makeQuery(id+"F42.opRevolve","SWEPT_FACE",FACE,{"disambiguationData":[OSD([sQuery(id+"F41.wireOp",EDGE,"E32")])]})]});
            var Q30;
            Q30=makeQuery(id+"F42.boolean.opBoolean","INTERSECT",EDGE,{"derivedFrom":[makeQuery(id+"F29.opLoft","CAP_FACE",FACE,{"disambiguationData":[OSD([makeQuery(id+"F22.imprint","IMPRINT",FACE,{"disambiguationData":[TD([[makeQuery(id+"F22.imprint","IMPRINT",EDGE,{"derivedFrom":sQuery(id+"F22.wireOp",EDGE,"E28.6.0")}),-1.0]])]})])],"isStart":true}),makeQuery(id+"F42.opRevolve","SWEPT_FACE",FACE,{"disambiguationData":[OSD([sQuery(id+"F41.wireOp",EDGE,"E32")])]})]});
            var Q31;
            Q31=makeQuery(id+"F42.boolean.opBoolean","INTERSECT",EDGE,{"derivedFrom":[makeQuery(id+"F28.opLoft","CAP_FACE",FACE,{"disambiguationData":[OSD([makeQuery(id+"F22.imprint","IMPRINT",FACE,{"disambiguationData":[TD([[makeQuery(id+"F22.imprint","IMPRINT",EDGE,{"derivedFrom":sQuery(id+"F22.wireOp",EDGE,"E28.5.0")}),-1.0]])]})])],"isStart":true}),makeQuery(id+"F42.opRevolve","SWEPT_FACE",FACE,{"disambiguationData":[OSD([sQuery(id+"F41.wireOp",EDGE,"E32")])]})]});
            fillet(context, id + "F43", {"entities" : qUnion([Q0, Q1, Q2, Q3, Q4, Q5, Q6, Q7, Q8, Q9, Q10, Q11, Q12, Q13, Q14, Q15, Q16, Q17, Q18, Q19, Q20, Q21, Q22, Q23, Q24, Q25, Q26, Q27, Q28, Q29, Q30, Q31]), "radius" : 11 * mm, "tangentPropagation" : true, "allowEdgeOverflow" : false});
        }
        {
            var Q0;
            Q0=makeQuery(id+"F40.boolean.opBoolean","INTERSECT",EDGE,{"derivedFrom":[makeQuery(id+"F20.opLoft","SWEPT_FACE",FACE,{"disambiguationData":[OSD([sQuery(id+"F3.wireOp",EDGE,"E20.1.1"),sQuery(id+"F3.wireOp",EDGE,"E20.1.2"),sQuery(id+"F3.wireOp",EDGE,"E20.1.3"),sQuery(id+"F4.wireOp",EDGE,"E26.1.1"),sQuery(id+"F4.wireOp",EDGE,"E26.1.2"),sQuery(id+"F4.wireOp",EDGE,"E26.1.3")])]}),makeQuery(id+"F40.opExtrude","CAP_FACE",FACE,{"disambiguationData":[OSD([sQuery(id+"F39.wireOp",EDGE,"E29"),sQuery(id+"F39.wireOp",EDGE,"E30")])],"isStart":false})]});
            var Q1;
            Q1=makeQuery(id+"F40.boolean.opBoolean","INTERSECT",EDGE,{"derivedFrom":[makeQuery(id+"F32.opLoft","SWEPT_FACE",FACE,{"disambiguationData":[OSD([sQuery(id+"F3.wireOp",EDGE,"E20.1.1"),sQuery(id+"F3.wireOp",EDGE,"E20.1.2"),sQuery(id+"F3.wireOp",EDGE,"E20.1.3"),sQuery(id+"F22.wireOp",EDGE,"E28.9.0"),sQuery(id+"F22.wireOp",EDGE,"E28.9.2"),sQuery(id+"F22.wireOp",EDGE,"E28.9.3")])]}),makeQuery(id+"F40.opExtrude","CAP_FACE",FACE,{"disambiguationData":[OSD([sQuery(id+"F39.wireOp",EDGE,"E29"),sQuery(id+"F39.wireOp",EDGE,"E30")])],"isStart":true})]});
            var Q2;
            Q2=makeQuery(id+"F40.boolean.opBoolean","INTERSECT",EDGE,{"derivedFrom":[makeQuery(id+"F5.opLoft","SWEPT_FACE",FACE,{"disambiguationData":[OSD([sQuery(id+"F3.wireOp",EDGE,"E18.bottom"),sQuery(id+"F3.wireOp",EDGE,"E18.top"),sQuery(id+"F3.wireOp",EDGE,"E18.right"),sQuery(id+"F4.wireOp",EDGE,"E22"),sQuery(id+"F4.wireOp",EDGE,"E23"),sQuery(id+"F4.wireOp",EDGE,"E24")])]}),makeQuery(id+"F40.opExtrude","CAP_FACE",FACE,{"disambiguationData":[OSD([sQuery(id+"F39.wireOp",EDGE,"E29"),sQuery(id+"F39.wireOp",EDGE,"E30")])],"isStart":false})]});
            var Q3;
            Q3=makeQuery(id+"F40.boolean.opBoolean","INTERSECT",EDGE,{"derivedFrom":[makeQuery(id+"F31.opLoft","SWEPT_FACE",FACE,{"disambiguationData":[OSD([sQuery(id+"F3.wireOp",EDGE,"E18.bottom"),sQuery(id+"F3.wireOp",EDGE,"E18.top"),sQuery(id+"F3.wireOp",EDGE,"E18.right"),sQuery(id+"F22.wireOp",EDGE,"E28.8.0"),sQuery(id+"F22.wireOp",EDGE,"E28.8.2"),sQuery(id+"F22.wireOp",EDGE,"E28.8.3")])]}),makeQuery(id+"F40.opExtrude","CAP_FACE",FACE,{"disambiguationData":[OSD([sQuery(id+"F39.wireOp",EDGE,"E29"),sQuery(id+"F39.wireOp",EDGE,"E30")])],"isStart":true})]});
            var Q4;
            Q4=makeQuery(id+"F40.boolean.opBoolean","INTERSECT",EDGE,{"derivedFrom":[makeQuery(id+"F6.opLoft","SWEPT_FACE",FACE,{"disambiguationData":[OSD([sQuery(id+"F3.wireOp",EDGE,"E20.15.1"),sQuery(id+"F3.wireOp",EDGE,"E20.15.2"),sQuery(id+"F3.wireOp",EDGE,"E20.15.3"),sQuery(id+"F4.wireOp",EDGE,"E26.15.1"),sQuery(id+"F4.wireOp",EDGE,"E26.15.2"),sQuery(id+"F4.wireOp",EDGE,"E26.15.3")])]}),makeQuery(id+"F40.opExtrude","CAP_FACE",FACE,{"disambiguationData":[OSD([sQuery(id+"F39.wireOp",EDGE,"E29"),sQuery(id+"F39.wireOp",EDGE,"E30")])],"isStart":false})]});
            var Q5;
            Q5=makeQuery(id+"F40.boolean.opBoolean","INTERSECT",EDGE,{"derivedFrom":[makeQuery(id+"F30.opLoft","SWEPT_FACE",FACE,{"disambiguationData":[OSD([sQuery(id+"F3.wireOp",EDGE,"E20.15.1"),sQuery(id+"F3.wireOp",EDGE,"E20.15.2"),sQuery(id+"F3.wireOp",EDGE,"E20.15.3"),sQuery(id+"F22.wireOp",EDGE,"E28.7.0"),sQuery(id+"F22.wireOp",EDGE,"E28.7.2"),sQuery(id+"F22.wireOp",EDGE,"E28.7.3")])]}),makeQuery(id+"F40.opExtrude","CAP_FACE",FACE,{"disambiguationData":[OSD([sQuery(id+"F39.wireOp",EDGE,"E29"),sQuery(id+"F39.wireOp",EDGE,"E30")])],"isStart":true})]});
            var Q6;
            Q6=makeQuery(id+"F40.boolean.opBoolean","INTERSECT",EDGE,{"derivedFrom":[makeQuery(id+"F29.opLoft","SWEPT_FACE",FACE,{"disambiguationData":[OSD([sQuery(id+"F3.wireOp",EDGE,"E20.14.1"),sQuery(id+"F3.wireOp",EDGE,"E20.14.2"),sQuery(id+"F3.wireOp",EDGE,"E20.14.3"),sQuery(id+"F22.wireOp",EDGE,"E28.6.0"),sQuery(id+"F22.wireOp",EDGE,"E28.6.2"),sQuery(id+"F22.wireOp",EDGE,"E28.6.3")])]}),makeQuery(id+"F40.opExtrude","CAP_FACE",FACE,{"disambiguationData":[OSD([sQuery(id+"F39.wireOp",EDGE,"E29"),sQuery(id+"F39.wireOp",EDGE,"E30")])],"isStart":true})]});
            var Q7;
            Q7=makeQuery(id+"F40.boolean.opBoolean","INTERSECT",EDGE,{"derivedFrom":[makeQuery(id+"F28.opLoft","SWEPT_FACE",FACE,{"disambiguationData":[OSD([sQuery(id+"F3.wireOp",EDGE,"E20.13.1"),sQuery(id+"F3.wireOp",EDGE,"E20.13.2"),sQuery(id+"F3.wireOp",EDGE,"E20.13.3"),sQuery(id+"F22.wireOp",EDGE,"E28.5.0"),sQuery(id+"F22.wireOp",EDGE,"E28.5.2"),sQuery(id+"F22.wireOp",EDGE,"E28.5.3")])]}),makeQuery(id+"F40.opExtrude","CAP_FACE",FACE,{"disambiguationData":[OSD([sQuery(id+"F39.wireOp",EDGE,"E29"),sQuery(id+"F39.wireOp",EDGE,"E30")])],"isStart":true})]});
            var Q8;
            Q8=makeQuery(id+"F40.boolean.opBoolean","INTERSECT",EDGE,{"derivedFrom":[makeQuery(id+"F27.opLoft","SWEPT_FACE",FACE,{"disambiguationData":[OSD([sQuery(id+"F3.wireOp",EDGE,"E20.12.1"),sQuery(id+"F3.wireOp",EDGE,"E20.12.2"),sQuery(id+"F3.wireOp",EDGE,"E20.12.3"),sQuery(id+"F22.wireOp",EDGE,"E28.4.0"),sQuery(id+"F22.wireOp",EDGE,"E28.4.2"),sQuery(id+"F22.wireOp",EDGE,"E28.4.3")])]}),makeQuery(id+"F40.opExtrude","CAP_FACE",FACE,{"disambiguationData":[OSD([sQuery(id+"F39.wireOp",EDGE,"E29"),sQuery(id+"F39.wireOp",EDGE,"E30")])],"isStart":true})]});
            var Q9;
            Q9=makeQuery(id+"F40.boolean.opBoolean","INTERSECT",EDGE,{"derivedFrom":[makeQuery(id+"F26.opLoft","SWEPT_FACE",FACE,{"disambiguationData":[OSD([sQuery(id+"F3.wireOp",EDGE,"E20.11.1"),sQuery(id+"F3.wireOp",EDGE,"E20.11.2"),sQuery(id+"F3.wireOp",EDGE,"E20.11.3"),sQuery(id+"F22.wireOp",EDGE,"E28.3.0"),sQuery(id+"F22.wireOp",EDGE,"E28.3.2"),sQuery(id+"F22.wireOp",EDGE,"E28.3.3")])]}),makeQuery(id+"F40.opExtrude","CAP_FACE",FACE,{"disambiguationData":[OSD([sQuery(id+"F39.wireOp",EDGE,"E29"),sQuery(id+"F39.wireOp",EDGE,"E30")])],"isStart":true})]});
            var Q10;
            Q10=makeQuery(id+"F40.boolean.opBoolean","INTERSECT",EDGE,{"derivedFrom":[makeQuery(id+"F25.opLoft","SWEPT_FACE",FACE,{"disambiguationData":[OSD([sQuery(id+"F3.wireOp",EDGE,"E20.10.1"),sQuery(id+"F3.wireOp",EDGE,"E20.10.2"),sQuery(id+"F3.wireOp",EDGE,"E20.10.3"),sQuery(id+"F22.wireOp",EDGE,"E28.2.0"),sQuery(id+"F22.wireOp",EDGE,"E28.2.2"),sQuery(id+"F22.wireOp",EDGE,"E28.2.3")])]}),makeQuery(id+"F40.opExtrude","CAP_FACE",FACE,{"disambiguationData":[OSD([sQuery(id+"F39.wireOp",EDGE,"E29"),sQuery(id+"F39.wireOp",EDGE,"E30")])],"isStart":true})]});
            var Q11;
            Q11=makeQuery(id+"F40.boolean.opBoolean","INTERSECT",EDGE,{"derivedFrom":[makeQuery(id+"F24.opLoft","SWEPT_FACE",FACE,{"disambiguationData":[OSD([sQuery(id+"F3.wireOp",EDGE,"E20.9.1"),sQuery(id+"F3.wireOp",EDGE,"E20.9.2"),sQuery(id+"F3.wireOp",EDGE,"E20.9.3"),sQuery(id+"F22.wireOp",EDGE,"E28.1.0"),sQuery(id+"F22.wireOp",EDGE,"E28.1.2"),sQuery(id+"F22.wireOp",EDGE,"E28.1.3")])]}),makeQuery(id+"F40.opExtrude","CAP_FACE",FACE,{"disambiguationData":[OSD([sQuery(id+"F39.wireOp",EDGE,"E29"),sQuery(id+"F39.wireOp",EDGE,"E30")])],"isStart":true})]});
            var Q12;
            Q12=makeQuery(id+"F40.boolean.opBoolean","INTERSECT",EDGE,{"derivedFrom":[makeQuery(id+"F23.opLoft","SWEPT_FACE",FACE,{"disambiguationData":[OSD([sQuery(id+"F3.wireOp",EDGE,"E20.8.1"),sQuery(id+"F3.wireOp",EDGE,"E20.8.2"),sQuery(id+"F3.wireOp",EDGE,"E20.8.3"),sQuery(id+"F22.wireOp",EDGE,"E27.bottom"),sQuery(id+"F22.wireOp",EDGE,"E27.top"),sQuery(id+"F22.wireOp",EDGE,"E27.left")])]}),makeQuery(id+"F40.opExtrude","CAP_FACE",FACE,{"disambiguationData":[OSD([sQuery(id+"F39.wireOp",EDGE,"E29"),sQuery(id+"F39.wireOp",EDGE,"E30")])],"isStart":true})]});
            var Q13;
            Q13=makeQuery(id+"F40.boolean.opBoolean","INTERSECT",EDGE,{"derivedFrom":[makeQuery(id+"F38.opLoft","SWEPT_FACE",FACE,{"disambiguationData":[OSD([sQuery(id+"F3.wireOp",EDGE,"E20.7.1"),sQuery(id+"F3.wireOp",EDGE,"E20.7.2"),sQuery(id+"F3.wireOp",EDGE,"E20.7.3"),sQuery(id+"F22.wireOp",EDGE,"E28.15.0"),sQuery(id+"F22.wireOp",EDGE,"E28.15.2"),sQuery(id+"F22.wireOp",EDGE,"E28.15.3")])]}),makeQuery(id+"F40.opExtrude","CAP_FACE",FACE,{"disambiguationData":[OSD([sQuery(id+"F39.wireOp",EDGE,"E29"),sQuery(id+"F39.wireOp",EDGE,"E30")])],"isStart":true})]});
            var Q14;
            Q14=makeQuery(id+"F40.boolean.opBoolean","INTERSECT",EDGE,{"derivedFrom":[makeQuery(id+"F37.opLoft","SWEPT_FACE",FACE,{"disambiguationData":[OSD([sQuery(id+"F3.wireOp",EDGE,"E20.6.1"),sQuery(id+"F3.wireOp",EDGE,"E20.6.2"),sQuery(id+"F3.wireOp",EDGE,"E20.6.3"),sQuery(id+"F22.wireOp",EDGE,"E28.14.0"),sQuery(id+"F22.wireOp",EDGE,"E28.14.2"),sQuery(id+"F22.wireOp",EDGE,"E28.14.3")])]}),makeQuery(id+"F40.opExtrude","CAP_FACE",FACE,{"disambiguationData":[OSD([sQuery(id+"F39.wireOp",EDGE,"E29"),sQuery(id+"F39.wireOp",EDGE,"E30")])],"isStart":true})]});
            var Q15;
            Q15=makeQuery(id+"F40.boolean.opBoolean","INTERSECT",EDGE,{"derivedFrom":[makeQuery(id+"F36.opLoft","SWEPT_FACE",FACE,{"disambiguationData":[OSD([sQuery(id+"F3.wireOp",EDGE,"E20.5.1"),sQuery(id+"F3.wireOp",EDGE,"E20.5.2"),sQuery(id+"F3.wireOp",EDGE,"E20.5.3"),sQuery(id+"F22.wireOp",EDGE,"E28.13.0"),sQuery(id+"F22.wireOp",EDGE,"E28.13.2"),sQuery(id+"F22.wireOp",EDGE,"E28.13.3")])]}),makeQuery(id+"F40.opExtrude","CAP_FACE",FACE,{"disambiguationData":[OSD([sQuery(id+"F39.wireOp",EDGE,"E29"),sQuery(id+"F39.wireOp",EDGE,"E30")])],"isStart":true})]});
            var Q16;
            Q16=makeQuery(id+"F40.boolean.opBoolean","INTERSECT",EDGE,{"derivedFrom":[makeQuery(id+"F35.opLoft","SWEPT_FACE",FACE,{"disambiguationData":[OSD([sQuery(id+"F3.wireOp",EDGE,"E20.4.1"),sQuery(id+"F3.wireOp",EDGE,"E20.4.2"),sQuery(id+"F3.wireOp",EDGE,"E20.4.3"),sQuery(id+"F22.wireOp",EDGE,"E28.12.0"),sQuery(id+"F22.wireOp",EDGE,"E28.12.2"),sQuery(id+"F22.wireOp",EDGE,"E28.12.3")])]}),makeQuery(id+"F40.opExtrude","CAP_FACE",FACE,{"disambiguationData":[OSD([sQuery(id+"F39.wireOp",EDGE,"E29"),sQuery(id+"F39.wireOp",EDGE,"E30")])],"isStart":true})]});
            var Q17;
            Q17=makeQuery(id+"F40.boolean.opBoolean","INTERSECT",EDGE,{"derivedFrom":[makeQuery(id+"F34.opLoft","SWEPT_FACE",FACE,{"disambiguationData":[OSD([sQuery(id+"F3.wireOp",EDGE,"E20.3.1"),sQuery(id+"F3.wireOp",EDGE,"E20.3.2"),sQuery(id+"F3.wireOp",EDGE,"E20.3.3"),sQuery(id+"F22.wireOp",EDGE,"E28.11.0"),sQuery(id+"F22.wireOp",EDGE,"E28.11.2"),sQuery(id+"F22.wireOp",EDGE,"E28.11.3")])]}),makeQuery(id+"F40.opExtrude","CAP_FACE",FACE,{"disambiguationData":[OSD([sQuery(id+"F39.wireOp",EDGE,"E29"),sQuery(id+"F39.wireOp",EDGE,"E30")])],"isStart":true})]});
            var Q18;
            Q18=makeQuery(id+"F40.boolean.opBoolean","INTERSECT",EDGE,{"derivedFrom":[makeQuery(id+"F33.opLoft","SWEPT_FACE",FACE,{"disambiguationData":[OSD([sQuery(id+"F3.wireOp",EDGE,"E20.2.1"),sQuery(id+"F3.wireOp",EDGE,"E20.2.2"),sQuery(id+"F3.wireOp",EDGE,"E20.2.3"),sQuery(id+"F22.wireOp",EDGE,"E28.10.0"),sQuery(id+"F22.wireOp",EDGE,"E28.10.2"),sQuery(id+"F22.wireOp",EDGE,"E28.10.3")])]}),makeQuery(id+"F40.opExtrude","CAP_FACE",FACE,{"disambiguationData":[OSD([sQuery(id+"F39.wireOp",EDGE,"E29"),sQuery(id+"F39.wireOp",EDGE,"E30")])],"isStart":true})]});
            var Q19;
            Q19=makeQuery(id+"F40.boolean.opBoolean","INTERSECT",EDGE,{"derivedFrom":[makeQuery(id+"F19.opLoft","SWEPT_FACE",FACE,{"disambiguationData":[OSD([sQuery(id+"F3.wireOp",EDGE,"E20.2.1"),sQuery(id+"F3.wireOp",EDGE,"E20.2.2"),sQuery(id+"F3.wireOp",EDGE,"E20.2.3"),sQuery(id+"F4.wireOp",EDGE,"E26.2.1"),sQuery(id+"F4.wireOp",EDGE,"E26.2.2"),sQuery(id+"F4.wireOp",EDGE,"E26.2.3")])]}),makeQuery(id+"F40.opExtrude","CAP_FACE",FACE,{"disambiguationData":[OSD([sQuery(id+"F39.wireOp",EDGE,"E29"),sQuery(id+"F39.wireOp",EDGE,"E30")])],"isStart":false})]});
            var Q20;
            Q20=makeQuery(id+"F40.boolean.opBoolean","INTERSECT",EDGE,{"derivedFrom":[makeQuery(id+"F18.opLoft","SWEPT_FACE",FACE,{"disambiguationData":[OSD([sQuery(id+"F3.wireOp",EDGE,"E20.3.1"),sQuery(id+"F3.wireOp",EDGE,"E20.3.2"),sQuery(id+"F3.wireOp",EDGE,"E20.3.3"),sQuery(id+"F4.wireOp",EDGE,"E26.3.1"),sQuery(id+"F4.wireOp",EDGE,"E26.3.2"),sQuery(id+"F4.wireOp",EDGE,"E26.3.3")])]}),makeQuery(id+"F40.opExtrude","CAP_FACE",FACE,{"disambiguationData":[OSD([sQuery(id+"F39.wireOp",EDGE,"E29"),sQuery(id+"F39.wireOp",EDGE,"E30")])],"isStart":false})]});
            var Q21;
            Q21=makeQuery(id+"F40.boolean.opBoolean","INTERSECT",EDGE,{"derivedFrom":[makeQuery(id+"F17.opLoft","SWEPT_FACE",FACE,{"disambiguationData":[OSD([sQuery(id+"F3.wireOp",EDGE,"E20.4.1"),sQuery(id+"F3.wireOp",EDGE,"E20.4.2"),sQuery(id+"F3.wireOp",EDGE,"E20.4.3"),sQuery(id+"F4.wireOp",EDGE,"E26.4.1"),sQuery(id+"F4.wireOp",EDGE,"E26.4.2"),sQuery(id+"F4.wireOp",EDGE,"E26.4.3")])]}),makeQuery(id+"F40.opExtrude","CAP_FACE",FACE,{"disambiguationData":[OSD([sQuery(id+"F39.wireOp",EDGE,"E29"),sQuery(id+"F39.wireOp",EDGE,"E30")])],"isStart":false})]});
            var Q22;
            Q22=makeQuery(id+"F40.boolean.opBoolean","INTERSECT",EDGE,{"derivedFrom":[makeQuery(id+"F16.opLoft","SWEPT_FACE",FACE,{"disambiguationData":[OSD([sQuery(id+"F3.wireOp",EDGE,"E20.5.1"),sQuery(id+"F3.wireOp",EDGE,"E20.5.2"),sQuery(id+"F3.wireOp",EDGE,"E20.5.3"),sQuery(id+"F4.wireOp",EDGE,"E26.5.1"),sQuery(id+"F4.wireOp",EDGE,"E26.5.2"),sQuery(id+"F4.wireOp",EDGE,"E26.5.3")])]}),makeQuery(id+"F40.opExtrude","CAP_FACE",FACE,{"disambiguationData":[OSD([sQuery(id+"F39.wireOp",EDGE,"E29"),sQuery(id+"F39.wireOp",EDGE,"E30")])],"isStart":false})]});
            var Q23;
            Q23=makeQuery(id+"F40.boolean.opBoolean","INTERSECT",EDGE,{"derivedFrom":[makeQuery(id+"F15.opLoft","SWEPT_FACE",FACE,{"disambiguationData":[OSD([sQuery(id+"F3.wireOp",EDGE,"E20.6.1"),sQuery(id+"F3.wireOp",EDGE,"E20.6.2"),sQuery(id+"F3.wireOp",EDGE,"E20.6.3"),sQuery(id+"F4.wireOp",EDGE,"E26.6.1"),sQuery(id+"F4.wireOp",EDGE,"E26.6.2"),sQuery(id+"F4.wireOp",EDGE,"E26.6.3")])]}),makeQuery(id+"F40.opExtrude","CAP_FACE",FACE,{"disambiguationData":[OSD([sQuery(id+"F39.wireOp",EDGE,"E29"),sQuery(id+"F39.wireOp",EDGE,"E30")])],"isStart":false})]});
            var Q24;
            Q24=makeQuery(id+"F40.boolean.opBoolean","INTERSECT",EDGE,{"derivedFrom":[makeQuery(id+"F14.opLoft","SWEPT_FACE",FACE,{"disambiguationData":[OSD([sQuery(id+"F3.wireOp",EDGE,"E20.7.1"),sQuery(id+"F3.wireOp",EDGE,"E20.7.2"),sQuery(id+"F3.wireOp",EDGE,"E20.7.3"),sQuery(id+"F4.wireOp",EDGE,"E26.7.1"),sQuery(id+"F4.wireOp",EDGE,"E26.7.2"),sQuery(id+"F4.wireOp",EDGE,"E26.7.3")])]}),makeQuery(id+"F40.opExtrude","CAP_FACE",FACE,{"disambiguationData":[OSD([sQuery(id+"F39.wireOp",EDGE,"E29"),sQuery(id+"F39.wireOp",EDGE,"E30")])],"isStart":false})]});
            var Q25;
            Q25=makeQuery(id+"F40.boolean.opBoolean","INTERSECT",EDGE,{"derivedFrom":[makeQuery(id+"F13.opLoft","SWEPT_FACE",FACE,{"disambiguationData":[OSD([sQuery(id+"F3.wireOp",EDGE,"E20.8.1"),sQuery(id+"F3.wireOp",EDGE,"E20.8.2"),sQuery(id+"F3.wireOp",EDGE,"E20.8.3"),sQuery(id+"F4.wireOp",EDGE,"E26.8.1"),sQuery(id+"F4.wireOp",EDGE,"E26.8.2"),sQuery(id+"F4.wireOp",EDGE,"E26.8.3")])]}),makeQuery(id+"F40.opExtrude","CAP_FACE",FACE,{"disambiguationData":[OSD([sQuery(id+"F39.wireOp",EDGE,"E29"),sQuery(id+"F39.wireOp",EDGE,"E30")])],"isStart":false})]});
            var Q26;
            Q26=makeQuery(id+"F40.boolean.opBoolean","INTERSECT",EDGE,{"derivedFrom":[makeQuery(id+"F12.opLoft","SWEPT_FACE",FACE,{"disambiguationData":[OSD([sQuery(id+"F3.wireOp",EDGE,"E20.9.1"),sQuery(id+"F3.wireOp",EDGE,"E20.9.2"),sQuery(id+"F3.wireOp",EDGE,"E20.9.3"),sQuery(id+"F4.wireOp",EDGE,"E26.9.1"),sQuery(id+"F4.wireOp",EDGE,"E26.9.2"),sQuery(id+"F4.wireOp",EDGE,"E26.9.3")])]}),makeQuery(id+"F40.opExtrude","CAP_FACE",FACE,{"disambiguationData":[OSD([sQuery(id+"F39.wireOp",EDGE,"E29"),sQuery(id+"F39.wireOp",EDGE,"E30")])],"isStart":false})]});
            var Q27;
            Q27=makeQuery(id+"F40.boolean.opBoolean","INTERSECT",EDGE,{"derivedFrom":[makeQuery(id+"F11.opLoft","SWEPT_FACE",FACE,{"disambiguationData":[OSD([sQuery(id+"F3.wireOp",EDGE,"E20.10.1"),sQuery(id+"F3.wireOp",EDGE,"E20.10.2"),sQuery(id+"F3.wireOp",EDGE,"E20.10.3"),sQuery(id+"F4.wireOp",EDGE,"E26.10.1"),sQuery(id+"F4.wireOp",EDGE,"E26.10.2"),sQuery(id+"F4.wireOp",EDGE,"E26.10.3")])]}),makeQuery(id+"F40.opExtrude","CAP_FACE",FACE,{"disambiguationData":[OSD([sQuery(id+"F39.wireOp",EDGE,"E29"),sQuery(id+"F39.wireOp",EDGE,"E30")])],"isStart":false})]});
            var Q28;
            Q28=makeQuery(id+"F40.boolean.opBoolean","INTERSECT",EDGE,{"derivedFrom":[makeQuery(id+"F10.opLoft","SWEPT_FACE",FACE,{"disambiguationData":[OSD([sQuery(id+"F3.wireOp",EDGE,"E20.11.1"),sQuery(id+"F3.wireOp",EDGE,"E20.11.2"),sQuery(id+"F3.wireOp",EDGE,"E20.11.3"),sQuery(id+"F4.wireOp",EDGE,"E26.11.1"),sQuery(id+"F4.wireOp",EDGE,"E26.11.2"),sQuery(id+"F4.wireOp",EDGE,"E26.11.3")])]}),makeQuery(id+"F40.opExtrude","CAP_FACE",FACE,{"disambiguationData":[OSD([sQuery(id+"F39.wireOp",EDGE,"E29"),sQuery(id+"F39.wireOp",EDGE,"E30")])],"isStart":false})]});
            var Q29;
            Q29=makeQuery(id+"F40.boolean.opBoolean","INTERSECT",EDGE,{"derivedFrom":[makeQuery(id+"F9.opLoft","SWEPT_FACE",FACE,{"disambiguationData":[OSD([sQuery(id+"F3.wireOp",EDGE,"E20.12.1"),sQuery(id+"F3.wireOp",EDGE,"E20.12.2"),sQuery(id+"F3.wireOp",EDGE,"E20.12.3"),sQuery(id+"F4.wireOp",EDGE,"E26.12.1"),sQuery(id+"F4.wireOp",EDGE,"E26.12.2"),sQuery(id+"F4.wireOp",EDGE,"E26.12.3")])]}),makeQuery(id+"F40.opExtrude","CAP_FACE",FACE,{"disambiguationData":[OSD([sQuery(id+"F39.wireOp",EDGE,"E29"),sQuery(id+"F39.wireOp",EDGE,"E30")])],"isStart":false})]});
            var Q30;
            Q30=makeQuery(id+"F40.boolean.opBoolean","INTERSECT",EDGE,{"derivedFrom":[makeQuery(id+"F8.opLoft","SWEPT_FACE",FACE,{"disambiguationData":[OSD([sQuery(id+"F3.wireOp",EDGE,"E20.13.1"),sQuery(id+"F3.wireOp",EDGE,"E20.13.2"),sQuery(id+"F3.wireOp",EDGE,"E20.13.3"),sQuery(id+"F4.wireOp",EDGE,"E26.13.1"),sQuery(id+"F4.wireOp",EDGE,"E26.13.2"),sQuery(id+"F4.wireOp",EDGE,"E26.13.3")])]}),makeQuery(id+"F40.opExtrude","CAP_FACE",FACE,{"disambiguationData":[OSD([sQuery(id+"F39.wireOp",EDGE,"E29"),sQuery(id+"F39.wireOp",EDGE,"E30")])],"isStart":false})]});
            var Q31;
            Q31=makeQuery(id+"F40.boolean.opBoolean","INTERSECT",EDGE,{"derivedFrom":[makeQuery(id+"F7.opLoft","SWEPT_FACE",FACE,{"disambiguationData":[OSD([sQuery(id+"F3.wireOp",EDGE,"E20.14.1"),sQuery(id+"F3.wireOp",EDGE,"E20.14.2"),sQuery(id+"F3.wireOp",EDGE,"E20.14.3"),sQuery(id+"F4.wireOp",EDGE,"E26.14.1"),sQuery(id+"F4.wireOp",EDGE,"E26.14.2"),sQuery(id+"F4.wireOp",EDGE,"E26.14.3")])]}),makeQuery(id+"F40.opExtrude","CAP_FACE",FACE,{"disambiguationData":[OSD([sQuery(id+"F39.wireOp",EDGE,"E29"),sQuery(id+"F39.wireOp",EDGE,"E30")])],"isStart":false})]});
            fillet(context, id + "F44", {"entities" : qUnion([Q0, Q1, Q2, Q3, Q4, Q5, Q6, Q7, Q8, Q9, Q10, Q11, Q12, Q13, Q14, Q15, Q16, Q17, Q18, Q19, Q20, Q21, Q22, Q23, Q24, Q25, Q26, Q27, Q28, Q29, Q30, Q31]), "radius" : 25 * mm, "tangentPropagation" : true, "allowEdgeOverflow" : false});
        }
        {
            var Q0;
            Q0=makeQuery(id+"F19.boolean.opBoolean","INTERSECT",EDGE,{"derivedFrom":[makeQuery(id+"F1.opRevolve","SWEPT_FACE",FACE,{"disambiguationData":[OSD([sQuery(id+"F0.wireOp",EDGE,"E13")])]}),makeQuery(id+"F19.opLoft","SWEPT_FACE",FACE,{"disambiguationData":[OSD([sQuery(id+"F3.wireOp",EDGE,"E20.2.0"),sQuery(id+"F3.wireOp",EDGE,"E20.2.1"),sQuery(id+"F3.wireOp",EDGE,"E20.2.3"),sQuery(id+"F4.wireOp",EDGE,"E26.2.0"),sQuery(id+"F4.wireOp",EDGE,"E26.2.2"),sQuery(id+"F4.wireOp",EDGE,"E26.2.3")])]})]});
            var Q1;
            Q1=makeQuery(id+"F20.boolean.opBoolean","INTERSECT",EDGE,{"derivedFrom":[makeQuery(id+"F1.opRevolve","SWEPT_FACE",FACE,{"disambiguationData":[OSD([sQuery(id+"F0.wireOp",EDGE,"E13")])]}),makeQuery(id+"F20.opLoft","SWEPT_FACE",FACE,{"disambiguationData":[OSD([sQuery(id+"F3.wireOp",EDGE,"E20.1.0"),sQuery(id+"F3.wireOp",EDGE,"E20.1.1"),sQuery(id+"F3.wireOp",EDGE,"E20.1.3"),sQuery(id+"F4.wireOp",EDGE,"E26.1.0"),sQuery(id+"F4.wireOp",EDGE,"E26.1.2"),sQuery(id+"F4.wireOp",EDGE,"E26.1.3")])]})]});
            var Q2;
            {var subQ0=sQuery(id+"F3.wireOp",EDGE,"E20.1.3");var subQ1=sQuery(id+"F3.wireOp",EDGE,"E20.1.1");var subQ2=sQuery(id+"F3.wireOp",EDGE,"E20.1.0");var subQ51=sQuery(id+"F3.wireOp",EDGE,"E18.bottom");var subQ62=sQuery(id+"F3.wireOp",EDGE,"E20.7.0");var subQ70=makeQuery(id+"F14.opLoft","CAP_FACE",FACE,{"disambiguationData":[OSD([makeQuery(id+"F3.imprint","IMPRINT",FACE,{"disambiguationData":[TD([[makeQuery(id+"F3.imprint","IMPRINT",EDGE,{"derivedFrom":subQ62}),-1.0]])]})])],"isStart":true});var subQ78=makeQuery(id+"F5.opLoft","CAP_FACE",FACE,{"disambiguationData":[OSD([makeQuery(id+"F3.imprint","IMPRINT",FACE,{"disambiguationData":[TD([[makeQuery(id+"F3.imprint","IMPRINT",EDGE,{"derivedFrom":subQ51}),1.0]])]})])],"isStart":true});Q2=makeQuery(id+"F32.boolean.opBoolean","INTERSECT",EDGE,{"derivedFrom":[makeQuery(id+"F31.boolean.opBoolean","SPLIT",FACE,{"disambiguationData":[TD([subQ70])],"derivedFrom":makeQuery(id+"F30.boolean.opBoolean","SPLIT",FACE,{"disambiguationData":[TD([subQ78])],"derivedFrom":makeQuery(id+"F29.boolean.opBoolean","SPLIT",FACE,{"disambiguationData":[TD([subQ78])],"derivedFrom":makeQuery(id+"F28.boolean.opBoolean","SPLIT",FACE,{"disambiguationData":[TD([subQ78])],"derivedFrom":makeQuery(id+"F27.boolean.opBoolean","SPLIT",FACE,{"disambiguationData":[TD([subQ78])],"derivedFrom":makeQuery(id+"F26.boolean.opBoolean","SPLIT",FACE,{"disambiguationData":[TD([subQ78])],"derivedFrom":makeQuery(id+"F25.boolean.opBoolean","SPLIT",FACE,{"disambiguationData":[TD([subQ78])],"derivedFrom":makeQuery(id+"F24.boolean.opBoolean","SPLIT",FACE,{"disambiguationData":[TD([subQ78])],"derivedFrom":makeQuery(id+"F1.opRevolve","SWEPT_FACE",FACE,{"disambiguationData":[OSD([sQuery(id+"F0.wireOp",EDGE,"E13")])]})})})})})})})})}),makeQuery(id+"F32.opLoft","SWEPT_FACE",FACE,{"disambiguationData":[OSD([subQ2,subQ1,subQ0,sQuery(id+"F22.wireOp",EDGE,"E28.9.1"),sQuery(id+"F22.wireOp",EDGE,"E28.9.2"),sQuery(id+"F22.wireOp",EDGE,"E28.9.3")])]})]});}
            var Q3;
            {var subQ0=sQuery(id+"F3.wireOp",EDGE,"E20.2.3");var subQ1=sQuery(id+"F3.wireOp",EDGE,"E20.2.1");var subQ2=sQuery(id+"F3.wireOp",EDGE,"E20.2.0");var subQ51=sQuery(id+"F3.wireOp",EDGE,"E20.7.0");var subQ60=makeQuery(id+"F14.opLoft","CAP_FACE",FACE,{"disambiguationData":[OSD([makeQuery(id+"F3.imprint","IMPRINT",FACE,{"disambiguationData":[TD([[makeQuery(id+"F3.imprint","IMPRINT",EDGE,{"derivedFrom":subQ51}),-1.0]])]})])],"isStart":true});var subQ73=sQuery(id+"F3.wireOp",EDGE,"E18.bottom");var subQ78=makeQuery(id+"F5.opLoft","CAP_FACE",FACE,{"disambiguationData":[OSD([makeQuery(id+"F3.imprint","IMPRINT",FACE,{"disambiguationData":[TD([[makeQuery(id+"F3.imprint","IMPRINT",EDGE,{"derivedFrom":subQ73}),1.0]])]})])],"isStart":true});Q3=makeQuery(id+"F33.boolean.opBoolean","INTERSECT",EDGE,{"derivedFrom":[makeQuery(id+"F32.boolean.opBoolean","SPLIT",FACE,{"disambiguationData":[TD([subQ60])],"derivedFrom":makeQuery(id+"F31.boolean.opBoolean","SPLIT",FACE,{"disambiguationData":[TD([subQ60])],"derivedFrom":makeQuery(id+"F30.boolean.opBoolean","SPLIT",FACE,{"disambiguationData":[TD([subQ78])],"derivedFrom":makeQuery(id+"F29.boolean.opBoolean","SPLIT",FACE,{"disambiguationData":[TD([subQ78])],"derivedFrom":makeQuery(id+"F28.boolean.opBoolean","SPLIT",FACE,{"disambiguationData":[TD([subQ78])],"derivedFrom":makeQuery(id+"F27.boolean.opBoolean","SPLIT",FACE,{"disambiguationData":[TD([subQ78])],"derivedFrom":makeQuery(id+"F26.boolean.opBoolean","SPLIT",FACE,{"disambiguationData":[TD([subQ78])],"derivedFrom":makeQuery(id+"F25.boolean.opBoolean","SPLIT",FACE,{"disambiguationData":[TD([subQ78])],"derivedFrom":makeQuery(id+"F24.boolean.opBoolean","SPLIT",FACE,{"disambiguationData":[TD([subQ78])],"derivedFrom":makeQuery(id+"F1.opRevolve","SWEPT_FACE",FACE,{"disambiguationData":[OSD([sQuery(id+"F0.wireOp",EDGE,"E13")])]})})})})})})})})})}),makeQuery(id+"F33.opLoft","SWEPT_FACE",FACE,{"disambiguationData":[OSD([subQ2,subQ1,subQ0,sQuery(id+"F22.wireOp",EDGE,"E28.10.1"),sQuery(id+"F22.wireOp",EDGE,"E28.10.2"),sQuery(id+"F22.wireOp",EDGE,"E28.10.3")])]})]});}
            var Q4;
            {var subQ0=sQuery(id+"F3.wireOp",EDGE,"E20.3.3");var subQ1=sQuery(id+"F3.wireOp",EDGE,"E20.3.1");var subQ2=sQuery(id+"F3.wireOp",EDGE,"E20.3.0");var subQ22=sQuery(id+"F3.wireOp",EDGE,"E20.7.0");var subQ26=makeQuery(id+"F14.opLoft","CAP_FACE",FACE,{"disambiguationData":[OSD([makeQuery(id+"F3.imprint","IMPRINT",FACE,{"disambiguationData":[TD([[makeQuery(id+"F3.imprint","IMPRINT",EDGE,{"derivedFrom":subQ22}),-1.0]])]})])],"isStart":true});var subQ73=sQuery(id+"F3.wireOp",EDGE,"E18.bottom");var subQ78=makeQuery(id+"F5.opLoft","CAP_FACE",FACE,{"disambiguationData":[OSD([makeQuery(id+"F3.imprint","IMPRINT",FACE,{"disambiguationData":[TD([[makeQuery(id+"F3.imprint","IMPRINT",EDGE,{"derivedFrom":subQ73}),1.0]])]})])],"isStart":true});Q4=makeQuery(id+"F34.boolean.opBoolean","INTERSECT",EDGE,{"derivedFrom":[makeQuery(id+"F33.boolean.opBoolean","SPLIT",FACE,{"disambiguationData":[TD([subQ26])],"derivedFrom":makeQuery(id+"F32.boolean.opBoolean","SPLIT",FACE,{"disambiguationData":[TD([subQ26])],"derivedFrom":makeQuery(id+"F31.boolean.opBoolean","SPLIT",FACE,{"disambiguationData":[TD([subQ26])],"derivedFrom":makeQuery(id+"F30.boolean.opBoolean","SPLIT",FACE,{"disambiguationData":[TD([subQ78])],"derivedFrom":makeQuery(id+"F29.boolean.opBoolean","SPLIT",FACE,{"disambiguationData":[TD([subQ78])],"derivedFrom":makeQuery(id+"F28.boolean.opBoolean","SPLIT",FACE,{"disambiguationData":[TD([subQ78])],"derivedFrom":makeQuery(id+"F27.boolean.opBoolean","SPLIT",FACE,{"disambiguationData":[TD([subQ78])],"derivedFrom":makeQuery(id+"F26.boolean.opBoolean","SPLIT",FACE,{"disambiguationData":[TD([subQ78])],"derivedFrom":makeQuery(id+"F25.boolean.opBoolean","SPLIT",FACE,{"disambiguationData":[TD([subQ78])],"derivedFrom":makeQuery(id+"F24.boolean.opBoolean","SPLIT",FACE,{"disambiguationData":[TD([subQ78])],"derivedFrom":makeQuery(id+"F1.opRevolve","SWEPT_FACE",FACE,{"disambiguationData":[OSD([sQuery(id+"F0.wireOp",EDGE,"E13")])]})})})})})})})})})})}),makeQuery(id+"F34.opLoft","SWEPT_FACE",FACE,{"disambiguationData":[OSD([subQ2,subQ1,subQ0,sQuery(id+"F22.wireOp",EDGE,"E28.11.1"),sQuery(id+"F22.wireOp",EDGE,"E28.11.2"),sQuery(id+"F22.wireOp",EDGE,"E28.11.3")])]})]});}
            var Q5;
            {var subQ0=sQuery(id+"F3.wireOp",EDGE,"E20.4.3");var subQ1=sQuery(id+"F3.wireOp",EDGE,"E20.4.1");var subQ2=sQuery(id+"F3.wireOp",EDGE,"E20.4.0");var subQ19=sQuery(id+"F3.wireOp",EDGE,"E20.7.0");var subQ23=makeQuery(id+"F14.opLoft","CAP_FACE",FACE,{"disambiguationData":[OSD([makeQuery(id+"F3.imprint","IMPRINT",FACE,{"disambiguationData":[TD([[makeQuery(id+"F3.imprint","IMPRINT",EDGE,{"derivedFrom":subQ19}),-1.0]])]})])],"isStart":true});var subQ73=sQuery(id+"F3.wireOp",EDGE,"E18.bottom");var subQ78=makeQuery(id+"F5.opLoft","CAP_FACE",FACE,{"disambiguationData":[OSD([makeQuery(id+"F3.imprint","IMPRINT",FACE,{"disambiguationData":[TD([[makeQuery(id+"F3.imprint","IMPRINT",EDGE,{"derivedFrom":subQ73}),1.0]])]})])],"isStart":true});Q5=makeQuery(id+"F35.boolean.opBoolean","INTERSECT",EDGE,{"derivedFrom":[makeQuery(id+"F34.boolean.opBoolean","SPLIT",FACE,{"disambiguationData":[TD([subQ23])],"derivedFrom":makeQuery(id+"F33.boolean.opBoolean","SPLIT",FACE,{"disambiguationData":[TD([subQ23])],"derivedFrom":makeQuery(id+"F32.boolean.opBoolean","SPLIT",FACE,{"disambiguationData":[TD([subQ23])],"derivedFrom":makeQuery(id+"F31.boolean.opBoolean","SPLIT",FACE,{"disambiguationData":[TD([subQ23])],"derivedFrom":makeQuery(id+"F30.boolean.opBoolean","SPLIT",FACE,{"disambiguationData":[TD([subQ78])],"derivedFrom":makeQuery(id+"F29.boolean.opBoolean","SPLIT",FACE,{"disambiguationData":[TD([subQ78])],"derivedFrom":makeQuery(id+"F28.boolean.opBoolean","SPLIT",FACE,{"disambiguationData":[TD([subQ78])],"derivedFrom":makeQuery(id+"F27.boolean.opBoolean","SPLIT",FACE,{"disambiguationData":[TD([subQ78])],"derivedFrom":makeQuery(id+"F26.boolean.opBoolean","SPLIT",FACE,{"disambiguationData":[TD([subQ78])],"derivedFrom":makeQuery(id+"F25.boolean.opBoolean","SPLIT",FACE,{"disambiguationData":[TD([subQ78])],"derivedFrom":makeQuery(id+"F24.boolean.opBoolean","SPLIT",FACE,{"disambiguationData":[TD([subQ78])],"derivedFrom":makeQuery(id+"F1.opRevolve","SWEPT_FACE",FACE,{"disambiguationData":[OSD([sQuery(id+"F0.wireOp",EDGE,"E13")])]})})})})})})})})})})})}),makeQuery(id+"F35.opLoft","SWEPT_FACE",FACE,{"disambiguationData":[OSD([subQ2,subQ1,subQ0,sQuery(id+"F22.wireOp",EDGE,"E28.12.1"),sQuery(id+"F22.wireOp",EDGE,"E28.12.2"),sQuery(id+"F22.wireOp",EDGE,"E28.12.3")])]})]});}
            var Q6;
            {var subQ0=sQuery(id+"F3.wireOp",EDGE,"E20.5.3");var subQ1=sQuery(id+"F3.wireOp",EDGE,"E20.5.1");var subQ2=sQuery(id+"F3.wireOp",EDGE,"E20.5.0");var subQ14=sQuery(id+"F3.wireOp",EDGE,"E20.7.0");var subQ18=makeQuery(id+"F14.opLoft","CAP_FACE",FACE,{"disambiguationData":[OSD([makeQuery(id+"F3.imprint","IMPRINT",FACE,{"disambiguationData":[TD([[makeQuery(id+"F3.imprint","IMPRINT",EDGE,{"derivedFrom":subQ14}),-1.0]])]})])],"isStart":true});var subQ73=sQuery(id+"F3.wireOp",EDGE,"E18.bottom");var subQ78=makeQuery(id+"F5.opLoft","CAP_FACE",FACE,{"disambiguationData":[OSD([makeQuery(id+"F3.imprint","IMPRINT",FACE,{"disambiguationData":[TD([[makeQuery(id+"F3.imprint","IMPRINT",EDGE,{"derivedFrom":subQ73}),1.0]])]})])],"isStart":true});Q6=makeQuery(id+"F36.boolean.opBoolean","INTERSECT",EDGE,{"derivedFrom":[makeQuery(id+"F35.boolean.opBoolean","SPLIT",FACE,{"disambiguationData":[TD([subQ18])],"derivedFrom":makeQuery(id+"F34.boolean.opBoolean","SPLIT",FACE,{"disambiguationData":[TD([subQ18])],"derivedFrom":makeQuery(id+"F33.boolean.opBoolean","SPLIT",FACE,{"disambiguationData":[TD([subQ18])],"derivedFrom":makeQuery(id+"F32.boolean.opBoolean","SPLIT",FACE,{"disambiguationData":[TD([subQ18])],"derivedFrom":makeQuery(id+"F31.boolean.opBoolean","SPLIT",FACE,{"disambiguationData":[TD([subQ18])],"derivedFrom":makeQuery(id+"F30.boolean.opBoolean","SPLIT",FACE,{"disambiguationData":[TD([subQ78])],"derivedFrom":makeQuery(id+"F29.boolean.opBoolean","SPLIT",FACE,{"disambiguationData":[TD([subQ78])],"derivedFrom":makeQuery(id+"F28.boolean.opBoolean","SPLIT",FACE,{"disambiguationData":[TD([subQ78])],"derivedFrom":makeQuery(id+"F27.boolean.opBoolean","SPLIT",FACE,{"disambiguationData":[TD([subQ78])],"derivedFrom":makeQuery(id+"F26.boolean.opBoolean","SPLIT",FACE,{"disambiguationData":[TD([subQ78])],"derivedFrom":makeQuery(id+"F25.boolean.opBoolean","SPLIT",FACE,{"disambiguationData":[TD([subQ78])],"derivedFrom":makeQuery(id+"F24.boolean.opBoolean","SPLIT",FACE,{"disambiguationData":[TD([subQ78])],"derivedFrom":makeQuery(id+"F1.opRevolve","SWEPT_FACE",FACE,{"disambiguationData":[OSD([sQuery(id+"F0.wireOp",EDGE,"E13")])]})})})})})})})})})})})})}),makeQuery(id+"F36.opLoft","SWEPT_FACE",FACE,{"disambiguationData":[OSD([subQ2,subQ1,subQ0,sQuery(id+"F22.wireOp",EDGE,"E28.13.1"),sQuery(id+"F22.wireOp",EDGE,"E28.13.2"),sQuery(id+"F22.wireOp",EDGE,"E28.13.3")])]})]});}
            var Q7;
            {var subQ0=sQuery(id+"F3.wireOp",EDGE,"E20.6.3");var subQ1=sQuery(id+"F3.wireOp",EDGE,"E20.6.1");var subQ2=sQuery(id+"F3.wireOp",EDGE,"E20.6.0");var subQ14=sQuery(id+"F3.wireOp",EDGE,"E20.7.0");var subQ18=makeQuery(id+"F14.opLoft","CAP_FACE",FACE,{"disambiguationData":[OSD([makeQuery(id+"F3.imprint","IMPRINT",FACE,{"disambiguationData":[TD([[makeQuery(id+"F3.imprint","IMPRINT",EDGE,{"derivedFrom":subQ14}),-1.0]])]})])],"isStart":true});var subQ73=sQuery(id+"F3.wireOp",EDGE,"E18.bottom");var subQ78=makeQuery(id+"F5.opLoft","CAP_FACE",FACE,{"disambiguationData":[OSD([makeQuery(id+"F3.imprint","IMPRINT",FACE,{"disambiguationData":[TD([[makeQuery(id+"F3.imprint","IMPRINT",EDGE,{"derivedFrom":subQ73}),1.0]])]})])],"isStart":true});Q7=makeQuery(id+"F37.boolean.opBoolean","INTERSECT",EDGE,{"derivedFrom":[makeQuery(id+"F36.boolean.opBoolean","SPLIT",FACE,{"disambiguationData":[TD([subQ18])],"derivedFrom":makeQuery(id+"F35.boolean.opBoolean","SPLIT",FACE,{"disambiguationData":[TD([subQ18])],"derivedFrom":makeQuery(id+"F34.boolean.opBoolean","SPLIT",FACE,{"disambiguationData":[TD([subQ18])],"derivedFrom":makeQuery(id+"F33.boolean.opBoolean","SPLIT",FACE,{"disambiguationData":[TD([subQ18])],"derivedFrom":makeQuery(id+"F32.boolean.opBoolean","SPLIT",FACE,{"disambiguationData":[TD([subQ18])],"derivedFrom":makeQuery(id+"F31.boolean.opBoolean","SPLIT",FACE,{"disambiguationData":[TD([subQ18])],"derivedFrom":makeQuery(id+"F30.boolean.opBoolean","SPLIT",FACE,{"disambiguationData":[TD([subQ78])],"derivedFrom":makeQuery(id+"F29.boolean.opBoolean","SPLIT",FACE,{"disambiguationData":[TD([subQ78])],"derivedFrom":makeQuery(id+"F28.boolean.opBoolean","SPLIT",FACE,{"disambiguationData":[TD([subQ78])],"derivedFrom":makeQuery(id+"F27.boolean.opBoolean","SPLIT",FACE,{"disambiguationData":[TD([subQ78])],"derivedFrom":makeQuery(id+"F26.boolean.opBoolean","SPLIT",FACE,{"disambiguationData":[TD([subQ78])],"derivedFrom":makeQuery(id+"F25.boolean.opBoolean","SPLIT",FACE,{"disambiguationData":[TD([subQ78])],"derivedFrom":makeQuery(id+"F24.boolean.opBoolean","SPLIT",FACE,{"disambiguationData":[TD([subQ78])],"derivedFrom":makeQuery(id+"F1.opRevolve","SWEPT_FACE",FACE,{"disambiguationData":[OSD([sQuery(id+"F0.wireOp",EDGE,"E13")])]})})})})})})})})})})})})})}),makeQuery(id+"F37.opLoft","SWEPT_FACE",FACE,{"disambiguationData":[OSD([subQ2,subQ1,subQ0,sQuery(id+"F22.wireOp",EDGE,"E28.14.1"),sQuery(id+"F22.wireOp",EDGE,"E28.14.2"),sQuery(id+"F22.wireOp",EDGE,"E28.14.3")])]})]});}
            var Q8;
            {var subQ0=sQuery(id+"F3.wireOp",EDGE,"E20.7.3");var subQ1=sQuery(id+"F3.wireOp",EDGE,"E20.7.1");var subQ2=sQuery(id+"F3.wireOp",EDGE,"E20.7.0");var subQ14=makeQuery(id+"F14.opLoft","CAP_FACE",FACE,{"disambiguationData":[OSD([makeQuery(id+"F3.imprint","IMPRINT",FACE,{"disambiguationData":[TD([[makeQuery(id+"F3.imprint","IMPRINT",EDGE,{"derivedFrom":subQ2}),-1.0]])]})])],"isStart":true});var subQ73=sQuery(id+"F3.wireOp",EDGE,"E18.bottom");var subQ78=makeQuery(id+"F5.opLoft","CAP_FACE",FACE,{"disambiguationData":[OSD([makeQuery(id+"F3.imprint","IMPRINT",FACE,{"disambiguationData":[TD([[makeQuery(id+"F3.imprint","IMPRINT",EDGE,{"derivedFrom":subQ73}),1.0]])]})])],"isStart":true});Q8=makeQuery(id+"F38.boolean.opBoolean","INTERSECT",EDGE,{"derivedFrom":[makeQuery(id+"F37.boolean.opBoolean","SPLIT",FACE,{"disambiguationData":[TD([subQ14])],"derivedFrom":makeQuery(id+"F36.boolean.opBoolean","SPLIT",FACE,{"disambiguationData":[TD([subQ14])],"derivedFrom":makeQuery(id+"F35.boolean.opBoolean","SPLIT",FACE,{"disambiguationData":[TD([subQ14])],"derivedFrom":makeQuery(id+"F34.boolean.opBoolean","SPLIT",FACE,{"disambiguationData":[TD([subQ14])],"derivedFrom":makeQuery(id+"F33.boolean.opBoolean","SPLIT",FACE,{"disambiguationData":[TD([subQ14])],"derivedFrom":makeQuery(id+"F32.boolean.opBoolean","SPLIT",FACE,{"disambiguationData":[TD([subQ14])],"derivedFrom":makeQuery(id+"F31.boolean.opBoolean","SPLIT",FACE,{"disambiguationData":[TD([subQ14])],"derivedFrom":makeQuery(id+"F30.boolean.opBoolean","SPLIT",FACE,{"disambiguationData":[TD([subQ78])],"derivedFrom":makeQuery(id+"F29.boolean.opBoolean","SPLIT",FACE,{"disambiguationData":[TD([subQ78])],"derivedFrom":makeQuery(id+"F28.boolean.opBoolean","SPLIT",FACE,{"disambiguationData":[TD([subQ78])],"derivedFrom":makeQuery(id+"F27.boolean.opBoolean","SPLIT",FACE,{"disambiguationData":[TD([subQ78])],"derivedFrom":makeQuery(id+"F26.boolean.opBoolean","SPLIT",FACE,{"disambiguationData":[TD([subQ78])],"derivedFrom":makeQuery(id+"F25.boolean.opBoolean","SPLIT",FACE,{"disambiguationData":[TD([subQ78])],"derivedFrom":makeQuery(id+"F24.boolean.opBoolean","SPLIT",FACE,{"disambiguationData":[TD([subQ78])],"derivedFrom":makeQuery(id+"F1.opRevolve","SWEPT_FACE",FACE,{"disambiguationData":[OSD([sQuery(id+"F0.wireOp",EDGE,"E13")])]})})})})})})})})})})})})})})}),makeQuery(id+"F38.opLoft","SWEPT_FACE",FACE,{"disambiguationData":[OSD([subQ2,subQ1,subQ0,sQuery(id+"F22.wireOp",EDGE,"E28.15.1"),sQuery(id+"F22.wireOp",EDGE,"E28.15.2"),sQuery(id+"F22.wireOp",EDGE,"E28.15.3")])]})]});}
            var Q9;
            Q9=makeQuery(id+"F23.boolean.opBoolean","INTERSECT",EDGE,{"derivedFrom":[makeQuery(id+"F1.opRevolve","SWEPT_FACE",FACE,{"disambiguationData":[OSD([sQuery(id+"F0.wireOp",EDGE,"E13")])]}),makeQuery(id+"F23.opLoft","SWEPT_FACE",FACE,{"disambiguationData":[OSD([sQuery(id+"F3.wireOp",EDGE,"E20.8.0"),sQuery(id+"F3.wireOp",EDGE,"E20.8.1"),sQuery(id+"F3.wireOp",EDGE,"E20.8.3"),sQuery(id+"F22.wireOp",EDGE,"E27.bottom"),sQuery(id+"F22.wireOp",EDGE,"E27.top"),sQuery(id+"F22.wireOp",EDGE,"E27.right")])]})]});
            var Q10;
            Q10=makeQuery(id+"F24.boolean.opBoolean","INTERSECT",EDGE,{"derivedFrom":[makeQuery(id+"F1.opRevolve","SWEPT_FACE",FACE,{"disambiguationData":[OSD([sQuery(id+"F0.wireOp",EDGE,"E13")])]}),makeQuery(id+"F24.opLoft","SWEPT_FACE",FACE,{"disambiguationData":[OSD([sQuery(id+"F3.wireOp",EDGE,"E20.9.0"),sQuery(id+"F3.wireOp",EDGE,"E20.9.1"),sQuery(id+"F3.wireOp",EDGE,"E20.9.3"),sQuery(id+"F22.wireOp",EDGE,"E28.1.1"),sQuery(id+"F22.wireOp",EDGE,"E28.1.2"),sQuery(id+"F22.wireOp",EDGE,"E28.1.3")])]})]});
            var Q11;
            {var subQ0=sQuery(id+"F3.wireOp",EDGE,"E20.10.3");var subQ1=sQuery(id+"F3.wireOp",EDGE,"E20.10.1");var subQ2=sQuery(id+"F3.wireOp",EDGE,"E20.10.0");var subQ81=sQuery(id+"F3.wireOp",EDGE,"E18.bottom");Q11=makeQuery(id+"F25.boolean.opBoolean","INTERSECT",EDGE,{"derivedFrom":[makeQuery(id+"F24.boolean.opBoolean","SPLIT",FACE,{"disambiguationData":[TD([makeQuery(id+"F5.opLoft","CAP_FACE",FACE,{"disambiguationData":[OSD([makeQuery(id+"F3.imprint","IMPRINT",FACE,{"disambiguationData":[TD([[makeQuery(id+"F3.imprint","IMPRINT",EDGE,{"derivedFrom":subQ81}),1.0]])]})])],"isStart":true})])],"derivedFrom":makeQuery(id+"F1.opRevolve","SWEPT_FACE",FACE,{"disambiguationData":[OSD([sQuery(id+"F0.wireOp",EDGE,"E13")])]})}),makeQuery(id+"F25.opLoft","SWEPT_FACE",FACE,{"disambiguationData":[OSD([subQ2,subQ1,subQ0,sQuery(id+"F22.wireOp",EDGE,"E28.2.1"),sQuery(id+"F22.wireOp",EDGE,"E28.2.2"),sQuery(id+"F22.wireOp",EDGE,"E28.2.3")])]})]});}
            var Q12;
            {var subQ0=sQuery(id+"F3.wireOp",EDGE,"E20.11.3");var subQ1=sQuery(id+"F3.wireOp",EDGE,"E20.11.1");var subQ2=sQuery(id+"F3.wireOp",EDGE,"E20.11.0");var subQ74=sQuery(id+"F3.wireOp",EDGE,"E18.bottom");var subQ77=makeQuery(id+"F5.opLoft","CAP_FACE",FACE,{"disambiguationData":[OSD([makeQuery(id+"F3.imprint","IMPRINT",FACE,{"disambiguationData":[TD([[makeQuery(id+"F3.imprint","IMPRINT",EDGE,{"derivedFrom":subQ74}),1.0]])]})])],"isStart":true});Q12=makeQuery(id+"F26.boolean.opBoolean","INTERSECT",EDGE,{"derivedFrom":[makeQuery(id+"F25.boolean.opBoolean","SPLIT",FACE,{"disambiguationData":[TD([subQ77])],"derivedFrom":makeQuery(id+"F24.boolean.opBoolean","SPLIT",FACE,{"disambiguationData":[TD([subQ77])],"derivedFrom":makeQuery(id+"F1.opRevolve","SWEPT_FACE",FACE,{"disambiguationData":[OSD([sQuery(id+"F0.wireOp",EDGE,"E13")])]})})}),makeQuery(id+"F26.opLoft","SWEPT_FACE",FACE,{"disambiguationData":[OSD([subQ2,subQ1,subQ0,sQuery(id+"F22.wireOp",EDGE,"E28.3.1"),sQuery(id+"F22.wireOp",EDGE,"E28.3.2"),sQuery(id+"F22.wireOp",EDGE,"E28.3.3")])]})]});}
            var Q13;
            {var subQ0=sQuery(id+"F3.wireOp",EDGE,"E20.12.3");var subQ1=sQuery(id+"F3.wireOp",EDGE,"E20.12.1");var subQ2=sQuery(id+"F3.wireOp",EDGE,"E20.12.0");var subQ70=sQuery(id+"F3.wireOp",EDGE,"E18.bottom");var subQ73=makeQuery(id+"F5.opLoft","CAP_FACE",FACE,{"disambiguationData":[OSD([makeQuery(id+"F3.imprint","IMPRINT",FACE,{"disambiguationData":[TD([[makeQuery(id+"F3.imprint","IMPRINT",EDGE,{"derivedFrom":subQ70}),1.0]])]})])],"isStart":true});Q13=makeQuery(id+"F27.boolean.opBoolean","INTERSECT",EDGE,{"derivedFrom":[makeQuery(id+"F26.boolean.opBoolean","SPLIT",FACE,{"disambiguationData":[TD([subQ73])],"derivedFrom":makeQuery(id+"F25.boolean.opBoolean","SPLIT",FACE,{"disambiguationData":[TD([subQ73])],"derivedFrom":makeQuery(id+"F24.boolean.opBoolean","SPLIT",FACE,{"disambiguationData":[TD([subQ73])],"derivedFrom":makeQuery(id+"F1.opRevolve","SWEPT_FACE",FACE,{"disambiguationData":[OSD([sQuery(id+"F0.wireOp",EDGE,"E13")])]})})})}),makeQuery(id+"F27.opLoft","SWEPT_FACE",FACE,{"disambiguationData":[OSD([subQ2,subQ1,subQ0,sQuery(id+"F22.wireOp",EDGE,"E28.4.1"),sQuery(id+"F22.wireOp",EDGE,"E28.4.2"),sQuery(id+"F22.wireOp",EDGE,"E28.4.3")])]})]});}
            var Q14;
            {var subQ0=sQuery(id+"F3.wireOp",EDGE,"E20.13.3");var subQ1=sQuery(id+"F3.wireOp",EDGE,"E20.13.1");var subQ2=sQuery(id+"F3.wireOp",EDGE,"E20.13.0");var subQ52=sQuery(id+"F3.wireOp",EDGE,"E18.bottom");var subQ55=makeQuery(id+"F5.opLoft","CAP_FACE",FACE,{"disambiguationData":[OSD([makeQuery(id+"F3.imprint","IMPRINT",FACE,{"disambiguationData":[TD([[makeQuery(id+"F3.imprint","IMPRINT",EDGE,{"derivedFrom":subQ52}),1.0]])]})])],"isStart":true});Q14=makeQuery(id+"F28.boolean.opBoolean","INTERSECT",EDGE,{"derivedFrom":[makeQuery(id+"F27.boolean.opBoolean","SPLIT",FACE,{"disambiguationData":[TD([subQ55])],"derivedFrom":makeQuery(id+"F26.boolean.opBoolean","SPLIT",FACE,{"disambiguationData":[TD([subQ55])],"derivedFrom":makeQuery(id+"F25.boolean.opBoolean","SPLIT",FACE,{"disambiguationData":[TD([subQ55])],"derivedFrom":makeQuery(id+"F24.boolean.opBoolean","SPLIT",FACE,{"disambiguationData":[TD([subQ55])],"derivedFrom":makeQuery(id+"F1.opRevolve","SWEPT_FACE",FACE,{"disambiguationData":[OSD([sQuery(id+"F0.wireOp",EDGE,"E13")])]})})})})}),makeQuery(id+"F28.opLoft","SWEPT_FACE",FACE,{"disambiguationData":[OSD([subQ2,subQ1,subQ0,sQuery(id+"F22.wireOp",EDGE,"E28.5.1"),sQuery(id+"F22.wireOp",EDGE,"E28.5.2"),sQuery(id+"F22.wireOp",EDGE,"E28.5.3")])]})]});}
            var Q15;
            {var subQ0=sQuery(id+"F3.wireOp",EDGE,"E20.14.3");var subQ1=sQuery(id+"F3.wireOp",EDGE,"E20.14.1");var subQ2=sQuery(id+"F3.wireOp",EDGE,"E20.14.0");var subQ41=sQuery(id+"F3.wireOp",EDGE,"E18.bottom");var subQ44=makeQuery(id+"F5.opLoft","CAP_FACE",FACE,{"disambiguationData":[OSD([makeQuery(id+"F3.imprint","IMPRINT",FACE,{"disambiguationData":[TD([[makeQuery(id+"F3.imprint","IMPRINT",EDGE,{"derivedFrom":subQ41}),1.0]])]})])],"isStart":true});Q15=makeQuery(id+"F29.boolean.opBoolean","INTERSECT",EDGE,{"derivedFrom":[makeQuery(id+"F28.boolean.opBoolean","SPLIT",FACE,{"disambiguationData":[TD([subQ44])],"derivedFrom":makeQuery(id+"F27.boolean.opBoolean","SPLIT",FACE,{"disambiguationData":[TD([subQ44])],"derivedFrom":makeQuery(id+"F26.boolean.opBoolean","SPLIT",FACE,{"disambiguationData":[TD([subQ44])],"derivedFrom":makeQuery(id+"F25.boolean.opBoolean","SPLIT",FACE,{"disambiguationData":[TD([subQ44])],"derivedFrom":makeQuery(id+"F24.boolean.opBoolean","SPLIT",FACE,{"disambiguationData":[TD([subQ44])],"derivedFrom":makeQuery(id+"F1.opRevolve","SWEPT_FACE",FACE,{"disambiguationData":[OSD([sQuery(id+"F0.wireOp",EDGE,"E13")])]})})})})})}),makeQuery(id+"F29.opLoft","SWEPT_FACE",FACE,{"disambiguationData":[OSD([subQ2,subQ1,subQ0,sQuery(id+"F22.wireOp",EDGE,"E28.6.1"),sQuery(id+"F22.wireOp",EDGE,"E28.6.2"),sQuery(id+"F22.wireOp",EDGE,"E28.6.3")])]})]});}
            var Q16;
            {var subQ0=sQuery(id+"F3.wireOp",EDGE,"E20.15.3");var subQ1=sQuery(id+"F3.wireOp",EDGE,"E20.15.1");var subQ2=sQuery(id+"F3.wireOp",EDGE,"E20.15.0");var subQ34=sQuery(id+"F3.wireOp",EDGE,"E18.bottom");var subQ37=makeQuery(id+"F5.opLoft","CAP_FACE",FACE,{"disambiguationData":[OSD([makeQuery(id+"F3.imprint","IMPRINT",FACE,{"disambiguationData":[TD([[makeQuery(id+"F3.imprint","IMPRINT",EDGE,{"derivedFrom":subQ34}),1.0]])]})])],"isStart":true});Q16=makeQuery(id+"F30.boolean.opBoolean","INTERSECT",EDGE,{"derivedFrom":[makeQuery(id+"F29.boolean.opBoolean","SPLIT",FACE,{"disambiguationData":[TD([subQ37])],"derivedFrom":makeQuery(id+"F28.boolean.opBoolean","SPLIT",FACE,{"disambiguationData":[TD([subQ37])],"derivedFrom":makeQuery(id+"F27.boolean.opBoolean","SPLIT",FACE,{"disambiguationData":[TD([subQ37])],"derivedFrom":makeQuery(id+"F26.boolean.opBoolean","SPLIT",FACE,{"disambiguationData":[TD([subQ37])],"derivedFrom":makeQuery(id+"F25.boolean.opBoolean","SPLIT",FACE,{"disambiguationData":[TD([subQ37])],"derivedFrom":makeQuery(id+"F24.boolean.opBoolean","SPLIT",FACE,{"disambiguationData":[TD([subQ37])],"derivedFrom":makeQuery(id+"F1.opRevolve","SWEPT_FACE",FACE,{"disambiguationData":[OSD([sQuery(id+"F0.wireOp",EDGE,"E13")])]})})})})})})}),makeQuery(id+"F30.opLoft","SWEPT_FACE",FACE,{"disambiguationData":[OSD([subQ2,subQ1,subQ0,sQuery(id+"F22.wireOp",EDGE,"E28.7.1"),sQuery(id+"F22.wireOp",EDGE,"E28.7.2"),sQuery(id+"F22.wireOp",EDGE,"E28.7.3")])]})]});}
            var Q17;
            {var subQ0=sQuery(id+"F3.wireOp",EDGE,"E18.left");var subQ1=sQuery(id+"F3.wireOp",EDGE,"E18.top");var subQ2=sQuery(id+"F3.wireOp",EDGE,"E18.bottom");var subQ48=makeQuery(id+"F5.opLoft","CAP_FACE",FACE,{"disambiguationData":[OSD([makeQuery(id+"F3.imprint","IMPRINT",FACE,{"disambiguationData":[TD([[makeQuery(id+"F3.imprint","IMPRINT",EDGE,{"derivedFrom":subQ2}),1.0]])]})])],"isStart":true});Q17=makeQuery(id+"F31.boolean.opBoolean","INTERSECT",EDGE,{"derivedFrom":[makeQuery(id+"F30.boolean.opBoolean","SPLIT",FACE,{"disambiguationData":[TD([subQ48])],"derivedFrom":makeQuery(id+"F29.boolean.opBoolean","SPLIT",FACE,{"disambiguationData":[TD([subQ48])],"derivedFrom":makeQuery(id+"F28.boolean.opBoolean","SPLIT",FACE,{"disambiguationData":[TD([subQ48])],"derivedFrom":makeQuery(id+"F27.boolean.opBoolean","SPLIT",FACE,{"disambiguationData":[TD([subQ48])],"derivedFrom":makeQuery(id+"F26.boolean.opBoolean","SPLIT",FACE,{"disambiguationData":[TD([subQ48])],"derivedFrom":makeQuery(id+"F25.boolean.opBoolean","SPLIT",FACE,{"disambiguationData":[TD([subQ48])],"derivedFrom":makeQuery(id+"F24.boolean.opBoolean","SPLIT",FACE,{"disambiguationData":[TD([subQ48])],"derivedFrom":makeQuery(id+"F1.opRevolve","SWEPT_FACE",FACE,{"disambiguationData":[OSD([sQuery(id+"F0.wireOp",EDGE,"E13")])]})})})})})})})}),makeQuery(id+"F31.opLoft","SWEPT_FACE",FACE,{"disambiguationData":[OSD([subQ2,subQ1,subQ0,sQuery(id+"F22.wireOp",EDGE,"E28.8.1"),sQuery(id+"F22.wireOp",EDGE,"E28.8.2"),sQuery(id+"F22.wireOp",EDGE,"E28.8.3")])]})]});}
            var Q18;
            Q18=makeQuery(id+"F5.boolean.opBoolean","INTERSECT",EDGE,{"derivedFrom":[makeQuery(id+"F1.opRevolve","SWEPT_FACE",FACE,{"disambiguationData":[OSD([sQuery(id+"F0.wireOp",EDGE,"E13")])]}),makeQuery(id+"F5.opLoft","SWEPT_FACE",FACE,{"disambiguationData":[OSD([sQuery(id+"F3.wireOp",EDGE,"E18.bottom"),sQuery(id+"F3.wireOp",EDGE,"E18.top"),sQuery(id+"F3.wireOp",EDGE,"E18.left"),sQuery(id+"F4.wireOp",EDGE,"E21"),sQuery(id+"F4.wireOp",EDGE,"E22"),sQuery(id+"F4.wireOp",EDGE,"E23")])]})]});
            var Q19;
            Q19=makeQuery(id+"F6.boolean.opBoolean","INTERSECT",EDGE,{"derivedFrom":[makeQuery(id+"F1.opRevolve","SWEPT_FACE",FACE,{"disambiguationData":[OSD([sQuery(id+"F0.wireOp",EDGE,"E13")])]}),makeQuery(id+"F6.opLoft","SWEPT_FACE",FACE,{"disambiguationData":[OSD([sQuery(id+"F3.wireOp",EDGE,"E20.15.0"),sQuery(id+"F3.wireOp",EDGE,"E20.15.1"),sQuery(id+"F3.wireOp",EDGE,"E20.15.3"),sQuery(id+"F4.wireOp",EDGE,"E26.15.0"),sQuery(id+"F4.wireOp",EDGE,"E26.15.2"),sQuery(id+"F4.wireOp",EDGE,"E26.15.3")])]})]});
            var Q20;
            Q20=makeQuery(id+"F7.boolean.opBoolean","INTERSECT",EDGE,{"derivedFrom":[makeQuery(id+"F1.opRevolve","SWEPT_FACE",FACE,{"disambiguationData":[OSD([sQuery(id+"F0.wireOp",EDGE,"E13")])]}),makeQuery(id+"F7.opLoft","SWEPT_FACE",FACE,{"disambiguationData":[OSD([sQuery(id+"F3.wireOp",EDGE,"E20.14.0"),sQuery(id+"F3.wireOp",EDGE,"E20.14.1"),sQuery(id+"F3.wireOp",EDGE,"E20.14.3"),sQuery(id+"F4.wireOp",EDGE,"E26.14.0"),sQuery(id+"F4.wireOp",EDGE,"E26.14.2"),sQuery(id+"F4.wireOp",EDGE,"E26.14.3")])]})]});
            var Q21;
            Q21=makeQuery(id+"F8.boolean.opBoolean","INTERSECT",EDGE,{"derivedFrom":[makeQuery(id+"F1.opRevolve","SWEPT_FACE",FACE,{"disambiguationData":[OSD([sQuery(id+"F0.wireOp",EDGE,"E13")])]}),makeQuery(id+"F8.opLoft","SWEPT_FACE",FACE,{"disambiguationData":[OSD([sQuery(id+"F3.wireOp",EDGE,"E20.13.0"),sQuery(id+"F3.wireOp",EDGE,"E20.13.1"),sQuery(id+"F3.wireOp",EDGE,"E20.13.3"),sQuery(id+"F4.wireOp",EDGE,"E26.13.0"),sQuery(id+"F4.wireOp",EDGE,"E26.13.2"),sQuery(id+"F4.wireOp",EDGE,"E26.13.3")])]})]});
            var Q22;
            Q22=makeQuery(id+"F9.boolean.opBoolean","INTERSECT",EDGE,{"derivedFrom":[makeQuery(id+"F1.opRevolve","SWEPT_FACE",FACE,{"disambiguationData":[OSD([sQuery(id+"F0.wireOp",EDGE,"E13")])]}),makeQuery(id+"F9.opLoft","SWEPT_FACE",FACE,{"disambiguationData":[OSD([sQuery(id+"F3.wireOp",EDGE,"E20.12.0"),sQuery(id+"F3.wireOp",EDGE,"E20.12.1"),sQuery(id+"F3.wireOp",EDGE,"E20.12.3"),sQuery(id+"F4.wireOp",EDGE,"E26.12.0"),sQuery(id+"F4.wireOp",EDGE,"E26.12.2"),sQuery(id+"F4.wireOp",EDGE,"E26.12.3")])]})]});
            var Q23;
            Q23=makeQuery(id+"F10.boolean.opBoolean","INTERSECT",EDGE,{"derivedFrom":[makeQuery(id+"F1.opRevolve","SWEPT_FACE",FACE,{"disambiguationData":[OSD([sQuery(id+"F0.wireOp",EDGE,"E13")])]}),makeQuery(id+"F10.opLoft","SWEPT_FACE",FACE,{"disambiguationData":[OSD([sQuery(id+"F3.wireOp",EDGE,"E20.11.0"),sQuery(id+"F3.wireOp",EDGE,"E20.11.1"),sQuery(id+"F3.wireOp",EDGE,"E20.11.3"),sQuery(id+"F4.wireOp",EDGE,"E26.11.0"),sQuery(id+"F4.wireOp",EDGE,"E26.11.2"),sQuery(id+"F4.wireOp",EDGE,"E26.11.3")])]})]});
            var Q24;
            Q24=makeQuery(id+"F11.boolean.opBoolean","INTERSECT",EDGE,{"derivedFrom":[makeQuery(id+"F1.opRevolve","SWEPT_FACE",FACE,{"disambiguationData":[OSD([sQuery(id+"F0.wireOp",EDGE,"E13")])]}),makeQuery(id+"F11.opLoft","SWEPT_FACE",FACE,{"disambiguationData":[OSD([sQuery(id+"F3.wireOp",EDGE,"E20.10.0"),sQuery(id+"F3.wireOp",EDGE,"E20.10.1"),sQuery(id+"F3.wireOp",EDGE,"E20.10.3"),sQuery(id+"F4.wireOp",EDGE,"E26.10.0"),sQuery(id+"F4.wireOp",EDGE,"E26.10.2"),sQuery(id+"F4.wireOp",EDGE,"E26.10.3")])]})]});
            var Q25;
            Q25=makeQuery(id+"F12.boolean.opBoolean","INTERSECT",EDGE,{"derivedFrom":[makeQuery(id+"F1.opRevolve","SWEPT_FACE",FACE,{"disambiguationData":[OSD([sQuery(id+"F0.wireOp",EDGE,"E13")])]}),makeQuery(id+"F12.opLoft","SWEPT_FACE",FACE,{"disambiguationData":[OSD([sQuery(id+"F3.wireOp",EDGE,"E20.9.0"),sQuery(id+"F3.wireOp",EDGE,"E20.9.1"),sQuery(id+"F3.wireOp",EDGE,"E20.9.3"),sQuery(id+"F4.wireOp",EDGE,"E26.9.0"),sQuery(id+"F4.wireOp",EDGE,"E26.9.2"),sQuery(id+"F4.wireOp",EDGE,"E26.9.3")])]})]});
            var Q26;
            Q26=makeQuery(id+"F13.boolean.opBoolean","INTERSECT",EDGE,{"derivedFrom":[makeQuery(id+"F1.opRevolve","SWEPT_FACE",FACE,{"disambiguationData":[OSD([sQuery(id+"F0.wireOp",EDGE,"E13")])]}),makeQuery(id+"F13.opLoft","SWEPT_FACE",FACE,{"disambiguationData":[OSD([sQuery(id+"F3.wireOp",EDGE,"E20.8.0"),sQuery(id+"F3.wireOp",EDGE,"E20.8.1"),sQuery(id+"F3.wireOp",EDGE,"E20.8.3"),sQuery(id+"F4.wireOp",EDGE,"E26.8.0"),sQuery(id+"F4.wireOp",EDGE,"E26.8.2"),sQuery(id+"F4.wireOp",EDGE,"E26.8.3")])]})]});
            var Q27;
            Q27=makeQuery(id+"F14.boolean.opBoolean","INTERSECT",EDGE,{"derivedFrom":[makeQuery(id+"F1.opRevolve","SWEPT_FACE",FACE,{"disambiguationData":[OSD([sQuery(id+"F0.wireOp",EDGE,"E13")])]}),makeQuery(id+"F14.opLoft","SWEPT_FACE",FACE,{"disambiguationData":[OSD([sQuery(id+"F3.wireOp",EDGE,"E20.7.0"),sQuery(id+"F3.wireOp",EDGE,"E20.7.1"),sQuery(id+"F3.wireOp",EDGE,"E20.7.3"),sQuery(id+"F4.wireOp",EDGE,"E26.7.0"),sQuery(id+"F4.wireOp",EDGE,"E26.7.2"),sQuery(id+"F4.wireOp",EDGE,"E26.7.3")])]})]});
            var Q28;
            Q28=makeQuery(id+"F15.boolean.opBoolean","INTERSECT",EDGE,{"derivedFrom":[makeQuery(id+"F1.opRevolve","SWEPT_FACE",FACE,{"disambiguationData":[OSD([sQuery(id+"F0.wireOp",EDGE,"E13")])]}),makeQuery(id+"F15.opLoft","SWEPT_FACE",FACE,{"disambiguationData":[OSD([sQuery(id+"F3.wireOp",EDGE,"E20.6.0"),sQuery(id+"F3.wireOp",EDGE,"E20.6.1"),sQuery(id+"F3.wireOp",EDGE,"E20.6.3"),sQuery(id+"F4.wireOp",EDGE,"E26.6.0"),sQuery(id+"F4.wireOp",EDGE,"E26.6.2"),sQuery(id+"F4.wireOp",EDGE,"E26.6.3")])]})]});
            var Q29;
            Q29=makeQuery(id+"F16.boolean.opBoolean","INTERSECT",EDGE,{"derivedFrom":[makeQuery(id+"F1.opRevolve","SWEPT_FACE",FACE,{"disambiguationData":[OSD([sQuery(id+"F0.wireOp",EDGE,"E13")])]}),makeQuery(id+"F16.opLoft","SWEPT_FACE",FACE,{"disambiguationData":[OSD([sQuery(id+"F3.wireOp",EDGE,"E20.5.0"),sQuery(id+"F3.wireOp",EDGE,"E20.5.1"),sQuery(id+"F3.wireOp",EDGE,"E20.5.3"),sQuery(id+"F4.wireOp",EDGE,"E26.5.0"),sQuery(id+"F4.wireOp",EDGE,"E26.5.2"),sQuery(id+"F4.wireOp",EDGE,"E26.5.3")])]})]});
            var Q30;
            Q30=makeQuery(id+"F17.boolean.opBoolean","INTERSECT",EDGE,{"derivedFrom":[makeQuery(id+"F1.opRevolve","SWEPT_FACE",FACE,{"disambiguationData":[OSD([sQuery(id+"F0.wireOp",EDGE,"E13")])]}),makeQuery(id+"F17.opLoft","SWEPT_FACE",FACE,{"disambiguationData":[OSD([sQuery(id+"F3.wireOp",EDGE,"E20.4.0"),sQuery(id+"F3.wireOp",EDGE,"E20.4.1"),sQuery(id+"F3.wireOp",EDGE,"E20.4.3"),sQuery(id+"F4.wireOp",EDGE,"E26.4.0"),sQuery(id+"F4.wireOp",EDGE,"E26.4.2"),sQuery(id+"F4.wireOp",EDGE,"E26.4.3")])]})]});
            var Q31;
            Q31=makeQuery(id+"F18.boolean.opBoolean","INTERSECT",EDGE,{"derivedFrom":[makeQuery(id+"F1.opRevolve","SWEPT_FACE",FACE,{"disambiguationData":[OSD([sQuery(id+"F0.wireOp",EDGE,"E13")])]}),makeQuery(id+"F18.opLoft","SWEPT_FACE",FACE,{"disambiguationData":[OSD([sQuery(id+"F3.wireOp",EDGE,"E20.3.0"),sQuery(id+"F3.wireOp",EDGE,"E20.3.1"),sQuery(id+"F3.wireOp",EDGE,"E20.3.3"),sQuery(id+"F4.wireOp",EDGE,"E26.3.0"),sQuery(id+"F4.wireOp",EDGE,"E26.3.2"),sQuery(id+"F4.wireOp",EDGE,"E26.3.3")])]})]});
            fillet(context, id + "F45", {"entities" : qUnion([Q0, Q1, Q2, Q3, Q4, Q5, Q6, Q7, Q8, Q9, Q10, Q11, Q12, Q13, Q14, Q15, Q16, Q17, Q18, Q19, Q20, Q21, Q22, Q23, Q24, Q25, Q26, Q27, Q28, Q29, Q30, Q31]), "radius" : 3 * mm, "tangentPropagation" : true, "allowEdgeOverflow" : false});
        }
        {
            var Q0;
            Q0=makeQuery(id+"F1.opRevolve","SWEPT_EDGE",EDGE,{"disambiguationData":[OSD([sQuery(id+"F0.wireOp",EDGE,"E0"),sQuery(id+"F0.wireOp",EDGE,"E14")])]});
            var Q1;
            Q1=makeQuery(id+"F1.opRevolve","SWEPT_EDGE",EDGE,{"disambiguationData":[OSD([sQuery(id+"F0.wireOp",EDGE,"E7"),sQuery(id+"F0.wireOp",EDGE,"E15")])]});
            chamfer(context, id + "F46", {"entities" : qUnion([Q0, Q1]), "width" : 1 * mm, "tangentPropagation" : true});
        }
        {
            var Q0;
            {var subQ0=sQuery(id+"F41.wireOp",EDGE,"E35");var subQ1=sQuery(id+"F4.wireOp",EDGE,"E26.3.3");var subQ2=sQuery(id+"F4.wireOp",EDGE,"E26.3.2");var subQ3=sQuery(id+"F3.wireOp",EDGE,"E20.3.3");var subQ4=sQuery(id+"F3.wireOp",EDGE,"E20.3.1");var subQ5=sQuery(id+"F41.wireOp",EDGE,"E36");Q0=makeQuery(id+"F42.boolean.opBoolean","COPY",EDGE,{"disambiguationData":[TD([makeQuery(id+"F18.opLoft","SWEPT_FACE",FACE,{"disambiguationData":[OSD([sQuery(id+"F3.wireOp",EDGE,"E20.3.0"),subQ4,subQ3,sQuery(id+"F4.wireOp",EDGE,"E26.3.0"),subQ2,subQ1])]})])],"derivedFrom":makeQuery(id+"F42.opRevolve","SWEPT_EDGE",EDGE,{"disambiguationData":[OSD([subQ0,subQ5])]})});}
            var Q1;
            {var subQ0=sQuery(id+"F4.wireOp",EDGE,"E26.2.3");var subQ1=sQuery(id+"F4.wireOp",EDGE,"E26.2.2");var subQ2=sQuery(id+"F3.wireOp",EDGE,"E20.2.3");var subQ3=sQuery(id+"F3.wireOp",EDGE,"E20.2.1");var subQ4=sQuery(id+"F41.wireOp",EDGE,"E36");var subQ5=sQuery(id+"F41.wireOp",EDGE,"E35");Q1=makeQuery(id+"F42.boolean.opBoolean","COPY",EDGE,{"disambiguationData":[TD([makeQuery(id+"F19.opLoft","SWEPT_FACE",FACE,{"disambiguationData":[OSD([sQuery(id+"F3.wireOp",EDGE,"E20.2.0"),subQ3,subQ2,sQuery(id+"F4.wireOp",EDGE,"E26.2.0"),subQ1,subQ0])]})])],"derivedFrom":makeQuery(id+"F42.opRevolve","SWEPT_EDGE",EDGE,{"disambiguationData":[OSD([subQ5,subQ4])]})});}
            var Q2;
            {var subQ0=sQuery(id+"F4.wireOp",EDGE,"E26.1.3");var subQ1=sQuery(id+"F4.wireOp",EDGE,"E26.1.2");var subQ2=sQuery(id+"F3.wireOp",EDGE,"E20.1.3");var subQ3=sQuery(id+"F3.wireOp",EDGE,"E20.1.1");var subQ4=sQuery(id+"F41.wireOp",EDGE,"E35");var subQ5=sQuery(id+"F41.wireOp",EDGE,"E36");Q2=makeQuery(id+"F42.boolean.opBoolean","COPY",EDGE,{"disambiguationData":[TD([makeQuery(id+"F20.opLoft","SWEPT_FACE",FACE,{"disambiguationData":[OSD([sQuery(id+"F3.wireOp",EDGE,"E20.1.0"),subQ3,subQ2,sQuery(id+"F4.wireOp",EDGE,"E26.1.0"),subQ1,subQ0])]})])],"derivedFrom":makeQuery(id+"F42.opRevolve","SWEPT_EDGE",EDGE,{"disambiguationData":[OSD([subQ4,subQ5])]})});}
            var Q3;
            {var subQ0=sQuery(id+"F41.wireOp",EDGE,"E35");var subQ1=sQuery(id+"F4.wireOp",EDGE,"E23");var subQ2=sQuery(id+"F4.wireOp",EDGE,"E22");var subQ3=sQuery(id+"F3.wireOp",EDGE,"E18.top");var subQ4=sQuery(id+"F3.wireOp",EDGE,"E18.bottom");var subQ5=sQuery(id+"F41.wireOp",EDGE,"E36");Q3=makeQuery(id+"F42.boolean.opBoolean","COPY",EDGE,{"disambiguationData":[TD([makeQuery(id+"F5.opLoft","SWEPT_FACE",FACE,{"disambiguationData":[OSD([subQ4,subQ3,sQuery(id+"F3.wireOp",EDGE,"E18.left"),sQuery(id+"F4.wireOp",EDGE,"E21"),subQ2,subQ1])]})])],"derivedFrom":makeQuery(id+"F42.opRevolve","SWEPT_EDGE",EDGE,{"disambiguationData":[OSD([subQ0,subQ5])]})});}
            var Q4;
            {var subQ0=sQuery(id+"F41.wireOp",EDGE,"E35");var subQ1=sQuery(id+"F4.wireOp",EDGE,"E26.4.3");var subQ2=sQuery(id+"F4.wireOp",EDGE,"E26.4.2");var subQ3=sQuery(id+"F3.wireOp",EDGE,"E20.4.3");var subQ4=sQuery(id+"F3.wireOp",EDGE,"E20.4.1");var subQ5=sQuery(id+"F41.wireOp",EDGE,"E36");Q4=makeQuery(id+"F42.boolean.opBoolean","COPY",EDGE,{"disambiguationData":[TD([makeQuery(id+"F17.opLoft","SWEPT_FACE",FACE,{"disambiguationData":[OSD([sQuery(id+"F3.wireOp",EDGE,"E20.4.0"),subQ4,subQ3,sQuery(id+"F4.wireOp",EDGE,"E26.4.0"),subQ2,subQ1])]})])],"derivedFrom":makeQuery(id+"F42.opRevolve","SWEPT_EDGE",EDGE,{"disambiguationData":[OSD([subQ0,subQ5])]})});}
            var Q5;
            {var subQ0=sQuery(id+"F41.wireOp",EDGE,"E35");var subQ1=sQuery(id+"F4.wireOp",EDGE,"E26.5.3");var subQ2=sQuery(id+"F4.wireOp",EDGE,"E26.5.2");var subQ3=sQuery(id+"F3.wireOp",EDGE,"E20.5.3");var subQ4=sQuery(id+"F3.wireOp",EDGE,"E20.5.1");var subQ5=sQuery(id+"F41.wireOp",EDGE,"E36");Q5=makeQuery(id+"F42.boolean.opBoolean","COPY",EDGE,{"disambiguationData":[TD([makeQuery(id+"F16.opLoft","SWEPT_FACE",FACE,{"disambiguationData":[OSD([sQuery(id+"F3.wireOp",EDGE,"E20.5.0"),subQ4,subQ3,sQuery(id+"F4.wireOp",EDGE,"E26.5.0"),subQ2,subQ1])]})])],"derivedFrom":makeQuery(id+"F42.opRevolve","SWEPT_EDGE",EDGE,{"disambiguationData":[OSD([subQ0,subQ5])]})});}
            var Q6;
            {var subQ0=sQuery(id+"F41.wireOp",EDGE,"E35");var subQ1=sQuery(id+"F4.wireOp",EDGE,"E26.6.3");var subQ2=sQuery(id+"F4.wireOp",EDGE,"E26.6.2");var subQ3=sQuery(id+"F3.wireOp",EDGE,"E20.6.3");var subQ4=sQuery(id+"F3.wireOp",EDGE,"E20.6.1");var subQ5=sQuery(id+"F41.wireOp",EDGE,"E36");Q6=makeQuery(id+"F42.boolean.opBoolean","COPY",EDGE,{"disambiguationData":[TD([makeQuery(id+"F15.opLoft","SWEPT_FACE",FACE,{"disambiguationData":[OSD([sQuery(id+"F3.wireOp",EDGE,"E20.6.0"),subQ4,subQ3,sQuery(id+"F4.wireOp",EDGE,"E26.6.0"),subQ2,subQ1])]})])],"derivedFrom":makeQuery(id+"F42.opRevolve","SWEPT_EDGE",EDGE,{"disambiguationData":[OSD([subQ0,subQ5])]})});}
            var Q7;
            {var subQ0=sQuery(id+"F41.wireOp",EDGE,"E35");var subQ1=sQuery(id+"F4.wireOp",EDGE,"E26.7.3");var subQ2=sQuery(id+"F4.wireOp",EDGE,"E26.7.2");var subQ3=sQuery(id+"F3.wireOp",EDGE,"E20.7.3");var subQ4=sQuery(id+"F3.wireOp",EDGE,"E20.7.1");var subQ5=sQuery(id+"F41.wireOp",EDGE,"E36");Q7=makeQuery(id+"F42.boolean.opBoolean","COPY",EDGE,{"disambiguationData":[TD([makeQuery(id+"F14.opLoft","SWEPT_FACE",FACE,{"disambiguationData":[OSD([sQuery(id+"F3.wireOp",EDGE,"E20.7.0"),subQ4,subQ3,sQuery(id+"F4.wireOp",EDGE,"E26.7.0"),subQ2,subQ1])]})])],"derivedFrom":makeQuery(id+"F42.opRevolve","SWEPT_EDGE",EDGE,{"disambiguationData":[OSD([subQ0,subQ5])]})});}
            var Q8;
            {var subQ0=sQuery(id+"F41.wireOp",EDGE,"E35");var subQ1=sQuery(id+"F4.wireOp",EDGE,"E26.8.3");var subQ2=sQuery(id+"F4.wireOp",EDGE,"E26.8.2");var subQ3=sQuery(id+"F3.wireOp",EDGE,"E20.8.3");var subQ4=sQuery(id+"F3.wireOp",EDGE,"E20.8.1");var subQ5=sQuery(id+"F41.wireOp",EDGE,"E36");Q8=makeQuery(id+"F42.boolean.opBoolean","COPY",EDGE,{"disambiguationData":[TD([makeQuery(id+"F13.opLoft","SWEPT_FACE",FACE,{"disambiguationData":[OSD([sQuery(id+"F3.wireOp",EDGE,"E20.8.0"),subQ4,subQ3,sQuery(id+"F4.wireOp",EDGE,"E26.8.0"),subQ2,subQ1])]})])],"derivedFrom":makeQuery(id+"F42.opRevolve","SWEPT_EDGE",EDGE,{"disambiguationData":[OSD([subQ0,subQ5])]})});}
            var Q9;
            {var subQ0=sQuery(id+"F41.wireOp",EDGE,"E35");var subQ1=sQuery(id+"F4.wireOp",EDGE,"E26.9.3");var subQ2=sQuery(id+"F4.wireOp",EDGE,"E26.9.2");var subQ3=sQuery(id+"F3.wireOp",EDGE,"E20.9.3");var subQ4=sQuery(id+"F3.wireOp",EDGE,"E20.9.1");var subQ5=sQuery(id+"F41.wireOp",EDGE,"E36");Q9=makeQuery(id+"F42.boolean.opBoolean","COPY",EDGE,{"disambiguationData":[TD([makeQuery(id+"F12.opLoft","SWEPT_FACE",FACE,{"disambiguationData":[OSD([sQuery(id+"F3.wireOp",EDGE,"E20.9.0"),subQ4,subQ3,sQuery(id+"F4.wireOp",EDGE,"E26.9.0"),subQ2,subQ1])]})])],"derivedFrom":makeQuery(id+"F42.opRevolve","SWEPT_EDGE",EDGE,{"disambiguationData":[OSD([subQ0,subQ5])]})});}
            var Q10;
            {var subQ0=sQuery(id+"F41.wireOp",EDGE,"E35");var subQ1=sQuery(id+"F4.wireOp",EDGE,"E26.10.3");var subQ2=sQuery(id+"F4.wireOp",EDGE,"E26.10.2");var subQ3=sQuery(id+"F3.wireOp",EDGE,"E20.10.3");var subQ4=sQuery(id+"F3.wireOp",EDGE,"E20.10.1");var subQ5=sQuery(id+"F41.wireOp",EDGE,"E36");Q10=makeQuery(id+"F42.boolean.opBoolean","COPY",EDGE,{"disambiguationData":[TD([makeQuery(id+"F11.opLoft","SWEPT_FACE",FACE,{"disambiguationData":[OSD([sQuery(id+"F3.wireOp",EDGE,"E20.10.0"),subQ4,subQ3,sQuery(id+"F4.wireOp",EDGE,"E26.10.0"),subQ2,subQ1])]})])],"derivedFrom":makeQuery(id+"F42.opRevolve","SWEPT_EDGE",EDGE,{"disambiguationData":[OSD([subQ0,subQ5])]})});}
            var Q11;
            {var subQ0=sQuery(id+"F4.wireOp",EDGE,"E26.11.3");var subQ1=sQuery(id+"F4.wireOp",EDGE,"E26.11.2");var subQ2=sQuery(id+"F3.wireOp",EDGE,"E20.11.3");var subQ3=sQuery(id+"F3.wireOp",EDGE,"E20.11.1");var subQ4=sQuery(id+"F41.wireOp",EDGE,"E35");var subQ5=sQuery(id+"F41.wireOp",EDGE,"E36");Q11=makeQuery(id+"F42.boolean.opBoolean","COPY",EDGE,{"disambiguationData":[TD([makeQuery(id+"F10.opLoft","SWEPT_FACE",FACE,{"disambiguationData":[OSD([sQuery(id+"F3.wireOp",EDGE,"E20.11.0"),subQ3,subQ2,sQuery(id+"F4.wireOp",EDGE,"E26.11.0"),subQ1,subQ0])]})])],"derivedFrom":makeQuery(id+"F42.opRevolve","SWEPT_EDGE",EDGE,{"disambiguationData":[OSD([subQ4,subQ5])]})});}
            var Q12;
            {var subQ0=sQuery(id+"F4.wireOp",EDGE,"E26.12.3");var subQ1=sQuery(id+"F4.wireOp",EDGE,"E26.12.2");var subQ2=sQuery(id+"F3.wireOp",EDGE,"E20.12.3");var subQ3=sQuery(id+"F3.wireOp",EDGE,"E20.12.1");var subQ4=sQuery(id+"F41.wireOp",EDGE,"E35");var subQ5=sQuery(id+"F41.wireOp",EDGE,"E36");Q12=makeQuery(id+"F42.boolean.opBoolean","COPY",EDGE,{"disambiguationData":[TD([makeQuery(id+"F9.opLoft","SWEPT_FACE",FACE,{"disambiguationData":[OSD([sQuery(id+"F3.wireOp",EDGE,"E20.12.0"),subQ3,subQ2,sQuery(id+"F4.wireOp",EDGE,"E26.12.0"),subQ1,subQ0])]})])],"derivedFrom":makeQuery(id+"F42.opRevolve","SWEPT_EDGE",EDGE,{"disambiguationData":[OSD([subQ4,subQ5])]})});}
            var Q13;
            {var subQ0=sQuery(id+"F41.wireOp",EDGE,"E35");var subQ1=sQuery(id+"F4.wireOp",EDGE,"E26.13.3");var subQ2=sQuery(id+"F4.wireOp",EDGE,"E26.13.2");var subQ3=sQuery(id+"F3.wireOp",EDGE,"E20.13.3");var subQ4=sQuery(id+"F3.wireOp",EDGE,"E20.13.1");var subQ5=sQuery(id+"F41.wireOp",EDGE,"E36");Q13=makeQuery(id+"F42.boolean.opBoolean","COPY",EDGE,{"disambiguationData":[TD([makeQuery(id+"F8.opLoft","SWEPT_FACE",FACE,{"disambiguationData":[OSD([sQuery(id+"F3.wireOp",EDGE,"E20.13.0"),subQ4,subQ3,sQuery(id+"F4.wireOp",EDGE,"E26.13.0"),subQ2,subQ1])]})])],"derivedFrom":makeQuery(id+"F42.opRevolve","SWEPT_EDGE",EDGE,{"disambiguationData":[OSD([subQ0,subQ5])]})});}
            var Q14;
            {var subQ0=sQuery(id+"F41.wireOp",EDGE,"E35");var subQ1=sQuery(id+"F4.wireOp",EDGE,"E26.14.3");var subQ2=sQuery(id+"F4.wireOp",EDGE,"E26.14.2");var subQ3=sQuery(id+"F3.wireOp",EDGE,"E20.14.3");var subQ4=sQuery(id+"F3.wireOp",EDGE,"E20.14.1");var subQ5=sQuery(id+"F41.wireOp",EDGE,"E36");Q14=makeQuery(id+"F42.boolean.opBoolean","COPY",EDGE,{"disambiguationData":[TD([makeQuery(id+"F7.opLoft","SWEPT_FACE",FACE,{"disambiguationData":[OSD([sQuery(id+"F3.wireOp",EDGE,"E20.14.0"),subQ4,subQ3,sQuery(id+"F4.wireOp",EDGE,"E26.14.0"),subQ2,subQ1])]})])],"derivedFrom":makeQuery(id+"F42.opRevolve","SWEPT_EDGE",EDGE,{"disambiguationData":[OSD([subQ0,subQ5])]})});}
            var Q15;
            {var subQ0=sQuery(id+"F4.wireOp",EDGE,"E26.15.3");var subQ1=sQuery(id+"F4.wireOp",EDGE,"E26.15.2");var subQ2=sQuery(id+"F3.wireOp",EDGE,"E20.15.3");var subQ3=sQuery(id+"F3.wireOp",EDGE,"E20.15.1");var subQ4=sQuery(id+"F41.wireOp",EDGE,"E35");var subQ5=sQuery(id+"F41.wireOp",EDGE,"E36");Q15=makeQuery(id+"F42.boolean.opBoolean","COPY",EDGE,{"disambiguationData":[TD([makeQuery(id+"F6.opLoft","SWEPT_FACE",FACE,{"disambiguationData":[OSD([sQuery(id+"F3.wireOp",EDGE,"E20.15.0"),subQ3,subQ2,sQuery(id+"F4.wireOp",EDGE,"E26.15.0"),subQ1,subQ0])]})])],"derivedFrom":makeQuery(id+"F42.opRevolve","SWEPT_EDGE",EDGE,{"disambiguationData":[OSD([subQ4,subQ5])]})});}
            var Q16;
            {var subQ0=sQuery(id+"F41.wireOp",EDGE,"E37");var subQ1=sQuery(id+"F22.wireOp",EDGE,"E28.7.3");var subQ2=sQuery(id+"F22.wireOp",EDGE,"E28.7.2");var subQ3=sQuery(id+"F3.wireOp",EDGE,"E20.15.3");var subQ4=sQuery(id+"F3.wireOp",EDGE,"E20.15.1");var subQ5=sQuery(id+"F41.wireOp",EDGE,"E38");Q16=makeQuery(id+"F42.boolean.opBoolean","COPY",EDGE,{"disambiguationData":[TD([makeQuery(id+"F30.opLoft","SWEPT_FACE",FACE,{"disambiguationData":[OSD([sQuery(id+"F3.wireOp",EDGE,"E20.15.0"),subQ4,subQ3,sQuery(id+"F22.wireOp",EDGE,"E28.7.1"),subQ2,subQ1])]})])],"derivedFrom":makeQuery(id+"F42.opRevolve","SWEPT_EDGE",EDGE,{"disambiguationData":[OSD([subQ0,subQ5])]})});}
            var Q17;
            {var subQ0=sQuery(id+"F41.wireOp",EDGE,"E37");var subQ1=sQuery(id+"F22.wireOp",EDGE,"E28.6.3");var subQ2=sQuery(id+"F22.wireOp",EDGE,"E28.6.2");var subQ3=sQuery(id+"F3.wireOp",EDGE,"E20.14.3");var subQ4=sQuery(id+"F3.wireOp",EDGE,"E20.14.1");var subQ5=sQuery(id+"F41.wireOp",EDGE,"E38");Q17=makeQuery(id+"F42.boolean.opBoolean","COPY",EDGE,{"disambiguationData":[TD([makeQuery(id+"F29.opLoft","SWEPT_FACE",FACE,{"disambiguationData":[OSD([sQuery(id+"F3.wireOp",EDGE,"E20.14.0"),subQ4,subQ3,sQuery(id+"F22.wireOp",EDGE,"E28.6.1"),subQ2,subQ1])]})])],"derivedFrom":makeQuery(id+"F42.opRevolve","SWEPT_EDGE",EDGE,{"disambiguationData":[OSD([subQ0,subQ5])]})});}
            var Q18;
            {var subQ0=sQuery(id+"F41.wireOp",EDGE,"E37");var subQ1=sQuery(id+"F22.wireOp",EDGE,"E28.5.3");var subQ2=sQuery(id+"F22.wireOp",EDGE,"E28.5.2");var subQ3=sQuery(id+"F3.wireOp",EDGE,"E20.13.3");var subQ4=sQuery(id+"F3.wireOp",EDGE,"E20.13.1");var subQ5=sQuery(id+"F41.wireOp",EDGE,"E38");Q18=makeQuery(id+"F42.boolean.opBoolean","COPY",EDGE,{"disambiguationData":[TD([makeQuery(id+"F28.opLoft","SWEPT_FACE",FACE,{"disambiguationData":[OSD([sQuery(id+"F3.wireOp",EDGE,"E20.13.0"),subQ4,subQ3,sQuery(id+"F22.wireOp",EDGE,"E28.5.1"),subQ2,subQ1])]})])],"derivedFrom":makeQuery(id+"F42.opRevolve","SWEPT_EDGE",EDGE,{"disambiguationData":[OSD([subQ0,subQ5])]})});}
            var Q19;
            {var subQ0=sQuery(id+"F41.wireOp",EDGE,"E37");var subQ1=sQuery(id+"F22.wireOp",EDGE,"E28.4.3");var subQ2=sQuery(id+"F22.wireOp",EDGE,"E28.4.2");var subQ3=sQuery(id+"F3.wireOp",EDGE,"E20.12.3");var subQ4=sQuery(id+"F3.wireOp",EDGE,"E20.12.1");var subQ5=sQuery(id+"F41.wireOp",EDGE,"E38");Q19=makeQuery(id+"F42.boolean.opBoolean","COPY",EDGE,{"disambiguationData":[TD([makeQuery(id+"F27.opLoft","SWEPT_FACE",FACE,{"disambiguationData":[OSD([sQuery(id+"F3.wireOp",EDGE,"E20.12.0"),subQ4,subQ3,sQuery(id+"F22.wireOp",EDGE,"E28.4.1"),subQ2,subQ1])]})])],"derivedFrom":makeQuery(id+"F42.opRevolve","SWEPT_EDGE",EDGE,{"disambiguationData":[OSD([subQ0,subQ5])]})});}
            var Q20;
            {var subQ0=sQuery(id+"F41.wireOp",EDGE,"E37");var subQ1=sQuery(id+"F22.wireOp",EDGE,"E28.3.3");var subQ2=sQuery(id+"F22.wireOp",EDGE,"E28.3.2");var subQ3=sQuery(id+"F3.wireOp",EDGE,"E20.11.3");var subQ4=sQuery(id+"F3.wireOp",EDGE,"E20.11.1");var subQ5=sQuery(id+"F41.wireOp",EDGE,"E38");Q20=makeQuery(id+"F42.boolean.opBoolean","COPY",EDGE,{"disambiguationData":[TD([makeQuery(id+"F26.opLoft","SWEPT_FACE",FACE,{"disambiguationData":[OSD([sQuery(id+"F3.wireOp",EDGE,"E20.11.0"),subQ4,subQ3,sQuery(id+"F22.wireOp",EDGE,"E28.3.1"),subQ2,subQ1])]})])],"derivedFrom":makeQuery(id+"F42.opRevolve","SWEPT_EDGE",EDGE,{"disambiguationData":[OSD([subQ0,subQ5])]})});}
            var Q21;
            {var subQ0=sQuery(id+"F41.wireOp",EDGE,"E37");var subQ1=sQuery(id+"F22.wireOp",EDGE,"E28.2.3");var subQ2=sQuery(id+"F22.wireOp",EDGE,"E28.2.2");var subQ3=sQuery(id+"F3.wireOp",EDGE,"E20.10.3");var subQ4=sQuery(id+"F3.wireOp",EDGE,"E20.10.1");var subQ5=sQuery(id+"F41.wireOp",EDGE,"E38");Q21=makeQuery(id+"F42.boolean.opBoolean","COPY",EDGE,{"disambiguationData":[TD([makeQuery(id+"F25.opLoft","SWEPT_FACE",FACE,{"disambiguationData":[OSD([sQuery(id+"F3.wireOp",EDGE,"E20.10.0"),subQ4,subQ3,sQuery(id+"F22.wireOp",EDGE,"E28.2.1"),subQ2,subQ1])]})])],"derivedFrom":makeQuery(id+"F42.opRevolve","SWEPT_EDGE",EDGE,{"disambiguationData":[OSD([subQ0,subQ5])]})});}
            var Q22;
            {var subQ0=sQuery(id+"F41.wireOp",EDGE,"E37");var subQ1=sQuery(id+"F22.wireOp",EDGE,"E28.1.3");var subQ2=sQuery(id+"F22.wireOp",EDGE,"E28.1.2");var subQ3=sQuery(id+"F3.wireOp",EDGE,"E20.9.3");var subQ4=sQuery(id+"F3.wireOp",EDGE,"E20.9.1");var subQ5=sQuery(id+"F41.wireOp",EDGE,"E38");Q22=makeQuery(id+"F42.boolean.opBoolean","COPY",EDGE,{"disambiguationData":[TD([makeQuery(id+"F24.opLoft","SWEPT_FACE",FACE,{"disambiguationData":[OSD([sQuery(id+"F3.wireOp",EDGE,"E20.9.0"),subQ4,subQ3,sQuery(id+"F22.wireOp",EDGE,"E28.1.1"),subQ2,subQ1])]})])],"derivedFrom":makeQuery(id+"F42.opRevolve","SWEPT_EDGE",EDGE,{"disambiguationData":[OSD([subQ0,subQ5])]})});}
            var Q23;
            {var subQ0=sQuery(id+"F22.wireOp",EDGE,"E27.top");var subQ1=sQuery(id+"F22.wireOp",EDGE,"E27.bottom");var subQ2=sQuery(id+"F3.wireOp",EDGE,"E20.8.3");var subQ3=sQuery(id+"F3.wireOp",EDGE,"E20.8.1");var subQ4=sQuery(id+"F41.wireOp",EDGE,"E37");var subQ5=sQuery(id+"F41.wireOp",EDGE,"E38");Q23=makeQuery(id+"F42.boolean.opBoolean","COPY",EDGE,{"disambiguationData":[TD([makeQuery(id+"F23.opLoft","SWEPT_FACE",FACE,{"disambiguationData":[OSD([sQuery(id+"F3.wireOp",EDGE,"E20.8.0"),subQ3,subQ2,subQ1,subQ0,sQuery(id+"F22.wireOp",EDGE,"E27.right")])]})])],"derivedFrom":makeQuery(id+"F42.opRevolve","SWEPT_EDGE",EDGE,{"disambiguationData":[OSD([subQ4,subQ5])]})});}
            var Q24;
            {var subQ0=sQuery(id+"F41.wireOp",EDGE,"E37");var subQ1=sQuery(id+"F22.wireOp",EDGE,"E28.15.3");var subQ2=sQuery(id+"F22.wireOp",EDGE,"E28.15.2");var subQ3=sQuery(id+"F3.wireOp",EDGE,"E20.7.3");var subQ4=sQuery(id+"F3.wireOp",EDGE,"E20.7.1");var subQ5=sQuery(id+"F41.wireOp",EDGE,"E38");Q24=makeQuery(id+"F42.boolean.opBoolean","COPY",EDGE,{"disambiguationData":[TD([makeQuery(id+"F38.opLoft","SWEPT_FACE",FACE,{"disambiguationData":[OSD([sQuery(id+"F3.wireOp",EDGE,"E20.7.0"),subQ4,subQ3,sQuery(id+"F22.wireOp",EDGE,"E28.15.1"),subQ2,subQ1])]})])],"derivedFrom":makeQuery(id+"F42.opRevolve","SWEPT_EDGE",EDGE,{"disambiguationData":[OSD([subQ0,subQ5])]})});}
            var Q25;
            {var subQ0=sQuery(id+"F41.wireOp",EDGE,"E37");var subQ1=sQuery(id+"F22.wireOp",EDGE,"E28.14.3");var subQ2=sQuery(id+"F22.wireOp",EDGE,"E28.14.2");var subQ3=sQuery(id+"F3.wireOp",EDGE,"E20.6.3");var subQ4=sQuery(id+"F3.wireOp",EDGE,"E20.6.1");var subQ5=sQuery(id+"F41.wireOp",EDGE,"E38");Q25=makeQuery(id+"F42.boolean.opBoolean","COPY",EDGE,{"disambiguationData":[TD([makeQuery(id+"F37.opLoft","SWEPT_FACE",FACE,{"disambiguationData":[OSD([sQuery(id+"F3.wireOp",EDGE,"E20.6.0"),subQ4,subQ3,sQuery(id+"F22.wireOp",EDGE,"E28.14.1"),subQ2,subQ1])]})])],"derivedFrom":makeQuery(id+"F42.opRevolve","SWEPT_EDGE",EDGE,{"disambiguationData":[OSD([subQ0,subQ5])]})});}
            var Q26;
            {var subQ0=sQuery(id+"F41.wireOp",EDGE,"E37");var subQ1=sQuery(id+"F22.wireOp",EDGE,"E28.13.3");var subQ2=sQuery(id+"F22.wireOp",EDGE,"E28.13.2");var subQ3=sQuery(id+"F3.wireOp",EDGE,"E20.5.3");var subQ4=sQuery(id+"F3.wireOp",EDGE,"E20.5.1");var subQ5=sQuery(id+"F41.wireOp",EDGE,"E38");Q26=makeQuery(id+"F42.boolean.opBoolean","COPY",EDGE,{"disambiguationData":[TD([makeQuery(id+"F36.opLoft","SWEPT_FACE",FACE,{"disambiguationData":[OSD([sQuery(id+"F3.wireOp",EDGE,"E20.5.0"),subQ4,subQ3,sQuery(id+"F22.wireOp",EDGE,"E28.13.1"),subQ2,subQ1])]})])],"derivedFrom":makeQuery(id+"F42.opRevolve","SWEPT_EDGE",EDGE,{"disambiguationData":[OSD([subQ0,subQ5])]})});}
            var Q27;
            {var subQ0=sQuery(id+"F41.wireOp",EDGE,"E37");var subQ1=sQuery(id+"F22.wireOp",EDGE,"E28.12.3");var subQ2=sQuery(id+"F22.wireOp",EDGE,"E28.12.2");var subQ3=sQuery(id+"F3.wireOp",EDGE,"E20.4.3");var subQ4=sQuery(id+"F3.wireOp",EDGE,"E20.4.1");var subQ5=sQuery(id+"F41.wireOp",EDGE,"E38");Q27=makeQuery(id+"F42.boolean.opBoolean","COPY",EDGE,{"disambiguationData":[TD([makeQuery(id+"F35.opLoft","SWEPT_FACE",FACE,{"disambiguationData":[OSD([sQuery(id+"F3.wireOp",EDGE,"E20.4.0"),subQ4,subQ3,sQuery(id+"F22.wireOp",EDGE,"E28.12.1"),subQ2,subQ1])]})])],"derivedFrom":makeQuery(id+"F42.opRevolve","SWEPT_EDGE",EDGE,{"disambiguationData":[OSD([subQ0,subQ5])]})});}
            var Q28;
            {var subQ0=sQuery(id+"F41.wireOp",EDGE,"E37");var subQ1=sQuery(id+"F22.wireOp",EDGE,"E28.11.3");var subQ2=sQuery(id+"F22.wireOp",EDGE,"E28.11.2");var subQ3=sQuery(id+"F3.wireOp",EDGE,"E20.3.3");var subQ4=sQuery(id+"F3.wireOp",EDGE,"E20.3.1");var subQ5=sQuery(id+"F41.wireOp",EDGE,"E38");Q28=makeQuery(id+"F42.boolean.opBoolean","COPY",EDGE,{"disambiguationData":[TD([makeQuery(id+"F34.opLoft","SWEPT_FACE",FACE,{"disambiguationData":[OSD([sQuery(id+"F3.wireOp",EDGE,"E20.3.0"),subQ4,subQ3,sQuery(id+"F22.wireOp",EDGE,"E28.11.1"),subQ2,subQ1])]})])],"derivedFrom":makeQuery(id+"F42.opRevolve","SWEPT_EDGE",EDGE,{"disambiguationData":[OSD([subQ0,subQ5])]})});}
            var Q29;
            {var subQ0=sQuery(id+"F41.wireOp",EDGE,"E37");var subQ1=sQuery(id+"F22.wireOp",EDGE,"E28.10.3");var subQ2=sQuery(id+"F22.wireOp",EDGE,"E28.10.2");var subQ3=sQuery(id+"F3.wireOp",EDGE,"E20.2.3");var subQ4=sQuery(id+"F3.wireOp",EDGE,"E20.2.1");var subQ5=sQuery(id+"F41.wireOp",EDGE,"E38");Q29=makeQuery(id+"F42.boolean.opBoolean","COPY",EDGE,{"disambiguationData":[TD([makeQuery(id+"F33.opLoft","SWEPT_FACE",FACE,{"disambiguationData":[OSD([sQuery(id+"F3.wireOp",EDGE,"E20.2.0"),subQ4,subQ3,sQuery(id+"F22.wireOp",EDGE,"E28.10.1"),subQ2,subQ1])]})])],"derivedFrom":makeQuery(id+"F42.opRevolve","SWEPT_EDGE",EDGE,{"disambiguationData":[OSD([subQ0,subQ5])]})});}
            var Q30;
            {var subQ0=sQuery(id+"F22.wireOp",EDGE,"E28.9.3");var subQ1=sQuery(id+"F22.wireOp",EDGE,"E28.9.2");var subQ2=sQuery(id+"F3.wireOp",EDGE,"E20.1.3");var subQ3=sQuery(id+"F3.wireOp",EDGE,"E20.1.1");var subQ4=sQuery(id+"F41.wireOp",EDGE,"E37");var subQ5=sQuery(id+"F41.wireOp",EDGE,"E38");Q30=makeQuery(id+"F42.boolean.opBoolean","COPY",EDGE,{"disambiguationData":[TD([makeQuery(id+"F32.opLoft","SWEPT_FACE",FACE,{"disambiguationData":[OSD([sQuery(id+"F3.wireOp",EDGE,"E20.1.0"),subQ3,subQ2,sQuery(id+"F22.wireOp",EDGE,"E28.9.1"),subQ1,subQ0])]})])],"derivedFrom":makeQuery(id+"F42.opRevolve","SWEPT_EDGE",EDGE,{"disambiguationData":[OSD([subQ4,subQ5])]})});}
            var Q31;
            {var subQ0=sQuery(id+"F22.wireOp",EDGE,"E28.8.3");var subQ1=sQuery(id+"F22.wireOp",EDGE,"E28.8.2");var subQ2=sQuery(id+"F3.wireOp",EDGE,"E18.top");var subQ3=sQuery(id+"F3.wireOp",EDGE,"E18.bottom");var subQ4=sQuery(id+"F41.wireOp",EDGE,"E37");var subQ5=sQuery(id+"F41.wireOp",EDGE,"E38");Q31=makeQuery(id+"F42.boolean.opBoolean","COPY",EDGE,{"disambiguationData":[TD([makeQuery(id+"F31.opLoft","SWEPT_FACE",FACE,{"disambiguationData":[OSD([subQ3,subQ2,sQuery(id+"F3.wireOp",EDGE,"E18.left"),sQuery(id+"F22.wireOp",EDGE,"E28.8.1"),subQ1,subQ0])]})])],"derivedFrom":makeQuery(id+"F42.opRevolve","SWEPT_EDGE",EDGE,{"disambiguationData":[OSD([subQ4,subQ5])]})});}
            fillet(context, id + "F47", {"entities" : qUnion([Q0, Q1, Q2, Q3, Q4, Q5, Q6, Q7, Q8, Q9, Q10, Q11, Q12, Q13, Q14, Q15, Q16, Q17, Q18, Q19, Q20, Q21, Q22, Q23, Q24, Q25, Q26, Q27, Q28, Q29, Q30, Q31]), "radius" : 3 * mm, "tangentPropagation" : true, "allowEdgeOverflow" : false});
        }
        {
            var Q0;
            {var subQ0=makeQuery(id+"F1.opRevolve","SWEPT_FACE",FACE,{"disambiguationData":[OSD([sQuery(id+"F0.wireOp",EDGE,"E10")])]});var subQ1=sQuery(id+"F3.wireOp",EDGE,"E20.9.3");var subQ2=sQuery(id+"F3.wireOp",EDGE,"E20.9.2");var subQ3=sQuery(id+"F3.wireOp",EDGE,"E20.9.1");var subQ4=makeQuery(id+"F12.opLoft","SWEPT_FACE",FACE,{"disambiguationData":[OSD([subQ3,subQ2,subQ1,sQuery(id+"F4.wireOp",EDGE,"E26.9.1"),sQuery(id+"F4.wireOp",EDGE,"E26.9.2"),sQuery(id+"F4.wireOp",EDGE,"E26.9.3")])]});var subQ9=makeQuery(id+"F40.opExtrude","CAP_FACE",FACE,{"disambiguationData":[OSD([sQuery(id+"F39.wireOp",EDGE,"E29"),sQuery(id+"F39.wireOp",EDGE,"E30")])],"isStart":false});Q0=makeQuery(id+"F44.opFillet","BLEND_EDGE",EDGE,{"blendedFrom":[makeQuery(id+"F40.boolean.opBoolean","INTERSECT",EDGE,{"derivedFrom":[subQ4,subQ9]}),makeQuery(id+"F40.boolean.opBoolean","SPLIT",FACE,{"disambiguationData":[TD([subQ0])],"derivedFrom":makeQuery(id+"F24.boolean.opBoolean","SPLIT",FACE,{"disambiguationData":[TD([subQ4])],"derivedFrom":makeQuery(id+"F1.opRevolve","SWEPT_FACE",FACE,{"disambiguationData":[OSD([sQuery(id+"F0.wireOp",EDGE,"E13")])]})})})],"blendedInto":[makeQuery(id+"F40.boolean.opBoolean","SPLIT",FACE,{"disambiguationData":[TD([subQ0])],"derivedFrom":makeQuery(id+"F24.boolean.opBoolean","SPLIT",FACE,{"disambiguationData":[TD([subQ4])],"derivedFrom":makeQuery(id+"F1.opRevolve","SWEPT_FACE",FACE,{"disambiguationData":[OSD([sQuery(id+"F0.wireOp",EDGE,"E13")])]})})})]});}
            var Q1;
            {var subQ0=makeQuery(id+"F1.opRevolve","SWEPT_FACE",FACE,{"disambiguationData":[OSD([sQuery(id+"F0.wireOp",EDGE,"E10")])]});var subQ1=sQuery(id+"F4.wireOp",EDGE,"E26.10.3");var subQ2=sQuery(id+"F4.wireOp",EDGE,"E26.10.2");var subQ3=sQuery(id+"F3.wireOp",EDGE,"E20.10.3");var subQ4=sQuery(id+"F3.wireOp",EDGE,"E20.10.2");var subQ5=sQuery(id+"F3.wireOp",EDGE,"E20.10.1");var subQ6=makeQuery(id+"F11.opLoft","SWEPT_FACE",FACE,{"disambiguationData":[OSD([subQ5,subQ4,subQ3,sQuery(id+"F4.wireOp",EDGE,"E26.10.1"),subQ2,subQ1])]});var subQ11=makeQuery(id+"F40.opExtrude","CAP_FACE",FACE,{"disambiguationData":[OSD([sQuery(id+"F39.wireOp",EDGE,"E29"),sQuery(id+"F39.wireOp",EDGE,"E30")])],"isStart":false});var subQ89=sQuery(id+"F3.wireOp",EDGE,"E18.bottom");Q1=makeQuery(id+"F44.opFillet","BLEND_EDGE",EDGE,{"blendedFrom":[makeQuery(id+"F40.boolean.opBoolean","INTERSECT",EDGE,{"derivedFrom":[subQ6,subQ11]}),makeQuery(id+"F40.boolean.opBoolean","SPLIT",FACE,{"disambiguationData":[TD([subQ0])],"derivedFrom":makeQuery(id+"F25.boolean.opBoolean","SPLIT",FACE,{"disambiguationData":[TD([subQ6])],"derivedFrom":makeQuery(id+"F24.boolean.opBoolean","SPLIT",FACE,{"disambiguationData":[TD([makeQuery(id+"F5.opLoft","CAP_FACE",FACE,{"disambiguationData":[OSD([makeQuery(id+"F3.imprint","IMPRINT",FACE,{"disambiguationData":[TD([[makeQuery(id+"F3.imprint","IMPRINT",EDGE,{"derivedFrom":subQ89}),1.0]])]})])],"isStart":true})])],"derivedFrom":makeQuery(id+"F1.opRevolve","SWEPT_FACE",FACE,{"disambiguationData":[OSD([sQuery(id+"F0.wireOp",EDGE,"E13")])]})})})})],"blendedInto":[makeQuery(id+"F40.boolean.opBoolean","SPLIT",FACE,{"disambiguationData":[TD([subQ0])],"derivedFrom":makeQuery(id+"F25.boolean.opBoolean","SPLIT",FACE,{"disambiguationData":[TD([subQ6])],"derivedFrom":makeQuery(id+"F24.boolean.opBoolean","SPLIT",FACE,{"disambiguationData":[TD([makeQuery(id+"F5.opLoft","CAP_FACE",FACE,{"disambiguationData":[OSD([makeQuery(id+"F3.imprint","IMPRINT",FACE,{"disambiguationData":[TD([[makeQuery(id+"F3.imprint","IMPRINT",EDGE,{"derivedFrom":subQ89}),1.0]])]})])],"isStart":true})])],"derivedFrom":makeQuery(id+"F1.opRevolve","SWEPT_FACE",FACE,{"disambiguationData":[OSD([sQuery(id+"F0.wireOp",EDGE,"E13")])]})})})})]});}
            var Q2;
            {var subQ0=makeQuery(id+"F1.opRevolve","SWEPT_FACE",FACE,{"disambiguationData":[OSD([sQuery(id+"F0.wireOp",EDGE,"E10")])]});var subQ1=sQuery(id+"F4.wireOp",EDGE,"E26.11.3");var subQ2=sQuery(id+"F4.wireOp",EDGE,"E26.11.2");var subQ3=sQuery(id+"F3.wireOp",EDGE,"E20.11.3");var subQ4=sQuery(id+"F3.wireOp",EDGE,"E20.11.2");var subQ5=sQuery(id+"F3.wireOp",EDGE,"E20.11.1");var subQ6=makeQuery(id+"F10.opLoft","SWEPT_FACE",FACE,{"disambiguationData":[OSD([subQ5,subQ4,subQ3,sQuery(id+"F4.wireOp",EDGE,"E26.11.1"),subQ2,subQ1])]});var subQ13=makeQuery(id+"F40.opExtrude","CAP_FACE",FACE,{"disambiguationData":[OSD([sQuery(id+"F39.wireOp",EDGE,"E29"),sQuery(id+"F39.wireOp",EDGE,"E30")])],"isStart":false});var subQ79=sQuery(id+"F3.wireOp",EDGE,"E18.bottom");var subQ82=makeQuery(id+"F5.opLoft","CAP_FACE",FACE,{"disambiguationData":[OSD([makeQuery(id+"F3.imprint","IMPRINT",FACE,{"disambiguationData":[TD([[makeQuery(id+"F3.imprint","IMPRINT",EDGE,{"derivedFrom":subQ79}),1.0]])]})])],"isStart":true});Q2=makeQuery(id+"F44.opFillet","BLEND_EDGE",EDGE,{"blendedFrom":[makeQuery(id+"F40.boolean.opBoolean","INTERSECT",EDGE,{"derivedFrom":[subQ6,subQ13]}),makeQuery(id+"F40.boolean.opBoolean","SPLIT",FACE,{"disambiguationData":[TD([subQ0])],"derivedFrom":makeQuery(id+"F26.boolean.opBoolean","SPLIT",FACE,{"disambiguationData":[TD([subQ6])],"derivedFrom":makeQuery(id+"F25.boolean.opBoolean","SPLIT",FACE,{"disambiguationData":[TD([subQ82])],"derivedFrom":makeQuery(id+"F24.boolean.opBoolean","SPLIT",FACE,{"disambiguationData":[TD([subQ82])],"derivedFrom":makeQuery(id+"F1.opRevolve","SWEPT_FACE",FACE,{"disambiguationData":[OSD([sQuery(id+"F0.wireOp",EDGE,"E13")])]})})})})})],"blendedInto":[makeQuery(id+"F40.boolean.opBoolean","SPLIT",FACE,{"disambiguationData":[TD([subQ0])],"derivedFrom":makeQuery(id+"F26.boolean.opBoolean","SPLIT",FACE,{"disambiguationData":[TD([subQ6])],"derivedFrom":makeQuery(id+"F25.boolean.opBoolean","SPLIT",FACE,{"disambiguationData":[TD([subQ82])],"derivedFrom":makeQuery(id+"F24.boolean.opBoolean","SPLIT",FACE,{"disambiguationData":[TD([subQ82])],"derivedFrom":makeQuery(id+"F1.opRevolve","SWEPT_FACE",FACE,{"disambiguationData":[OSD([sQuery(id+"F0.wireOp",EDGE,"E13")])]})})})})})]});}
            var Q3;
            {var subQ0=makeQuery(id+"F1.opRevolve","SWEPT_FACE",FACE,{"disambiguationData":[OSD([sQuery(id+"F0.wireOp",EDGE,"E10")])]});var subQ1=sQuery(id+"F4.wireOp",EDGE,"E26.12.3");var subQ2=sQuery(id+"F4.wireOp",EDGE,"E26.12.2");var subQ3=sQuery(id+"F3.wireOp",EDGE,"E20.12.3");var subQ4=sQuery(id+"F3.wireOp",EDGE,"E20.12.2");var subQ5=sQuery(id+"F3.wireOp",EDGE,"E20.12.1");var subQ6=makeQuery(id+"F9.opLoft","SWEPT_FACE",FACE,{"disambiguationData":[OSD([subQ5,subQ4,subQ3,sQuery(id+"F4.wireOp",EDGE,"E26.12.1"),subQ2,subQ1])]});var subQ7=makeQuery(id+"F40.opExtrude","CAP_FACE",FACE,{"disambiguationData":[OSD([sQuery(id+"F39.wireOp",EDGE,"E29"),sQuery(id+"F39.wireOp",EDGE,"E30")])],"isStart":false});var subQ74=sQuery(id+"F3.wireOp",EDGE,"E18.bottom");var subQ77=makeQuery(id+"F5.opLoft","CAP_FACE",FACE,{"disambiguationData":[OSD([makeQuery(id+"F3.imprint","IMPRINT",FACE,{"disambiguationData":[TD([[makeQuery(id+"F3.imprint","IMPRINT",EDGE,{"derivedFrom":subQ74}),1.0]])]})])],"isStart":true});Q3=makeQuery(id+"F44.opFillet","BLEND_EDGE",EDGE,{"blendedFrom":[makeQuery(id+"F40.boolean.opBoolean","INTERSECT",EDGE,{"derivedFrom":[subQ6,subQ7]}),makeQuery(id+"F40.boolean.opBoolean","SPLIT",FACE,{"disambiguationData":[TD([subQ0])],"derivedFrom":makeQuery(id+"F27.boolean.opBoolean","SPLIT",FACE,{"disambiguationData":[TD([subQ6])],"derivedFrom":makeQuery(id+"F26.boolean.opBoolean","SPLIT",FACE,{"disambiguationData":[TD([subQ77])],"derivedFrom":makeQuery(id+"F25.boolean.opBoolean","SPLIT",FACE,{"disambiguationData":[TD([subQ77])],"derivedFrom":makeQuery(id+"F24.boolean.opBoolean","SPLIT",FACE,{"disambiguationData":[TD([subQ77])],"derivedFrom":makeQuery(id+"F1.opRevolve","SWEPT_FACE",FACE,{"disambiguationData":[OSD([sQuery(id+"F0.wireOp",EDGE,"E13")])]})})})})})})],"blendedInto":[makeQuery(id+"F40.boolean.opBoolean","SPLIT",FACE,{"disambiguationData":[TD([subQ0])],"derivedFrom":makeQuery(id+"F27.boolean.opBoolean","SPLIT",FACE,{"disambiguationData":[TD([subQ6])],"derivedFrom":makeQuery(id+"F26.boolean.opBoolean","SPLIT",FACE,{"disambiguationData":[TD([subQ77])],"derivedFrom":makeQuery(id+"F25.boolean.opBoolean","SPLIT",FACE,{"disambiguationData":[TD([subQ77])],"derivedFrom":makeQuery(id+"F24.boolean.opBoolean","SPLIT",FACE,{"disambiguationData":[TD([subQ77])],"derivedFrom":makeQuery(id+"F1.opRevolve","SWEPT_FACE",FACE,{"disambiguationData":[OSD([sQuery(id+"F0.wireOp",EDGE,"E13")])]})})})})})})]});}
            var Q4;
            {var subQ0=makeQuery(id+"F1.opRevolve","SWEPT_FACE",FACE,{"disambiguationData":[OSD([sQuery(id+"F0.wireOp",EDGE,"E10")])]});var subQ1=sQuery(id+"F4.wireOp",EDGE,"E26.13.3");var subQ2=sQuery(id+"F4.wireOp",EDGE,"E26.13.2");var subQ3=sQuery(id+"F3.wireOp",EDGE,"E20.13.3");var subQ4=sQuery(id+"F3.wireOp",EDGE,"E20.13.2");var subQ5=sQuery(id+"F3.wireOp",EDGE,"E20.13.1");var subQ6=makeQuery(id+"F8.opLoft","SWEPT_FACE",FACE,{"disambiguationData":[OSD([subQ5,subQ4,subQ3,sQuery(id+"F4.wireOp",EDGE,"E26.13.1"),subQ2,subQ1])]});var subQ13=makeQuery(id+"F40.opExtrude","CAP_FACE",FACE,{"disambiguationData":[OSD([sQuery(id+"F39.wireOp",EDGE,"E29"),sQuery(id+"F39.wireOp",EDGE,"E30")])],"isStart":false});var subQ56=sQuery(id+"F3.wireOp",EDGE,"E18.bottom");var subQ59=makeQuery(id+"F5.opLoft","CAP_FACE",FACE,{"disambiguationData":[OSD([makeQuery(id+"F3.imprint","IMPRINT",FACE,{"disambiguationData":[TD([[makeQuery(id+"F3.imprint","IMPRINT",EDGE,{"derivedFrom":subQ56}),1.0]])]})])],"isStart":true});Q4=makeQuery(id+"F44.opFillet","BLEND_EDGE",EDGE,{"blendedFrom":[makeQuery(id+"F40.boolean.opBoolean","INTERSECT",EDGE,{"derivedFrom":[subQ6,subQ13]}),makeQuery(id+"F40.boolean.opBoolean","SPLIT",FACE,{"disambiguationData":[TD([subQ0])],"derivedFrom":makeQuery(id+"F28.boolean.opBoolean","SPLIT",FACE,{"disambiguationData":[TD([subQ6])],"derivedFrom":makeQuery(id+"F27.boolean.opBoolean","SPLIT",FACE,{"disambiguationData":[TD([subQ59])],"derivedFrom":makeQuery(id+"F26.boolean.opBoolean","SPLIT",FACE,{"disambiguationData":[TD([subQ59])],"derivedFrom":makeQuery(id+"F25.boolean.opBoolean","SPLIT",FACE,{"disambiguationData":[TD([subQ59])],"derivedFrom":makeQuery(id+"F24.boolean.opBoolean","SPLIT",FACE,{"disambiguationData":[TD([subQ59])],"derivedFrom":makeQuery(id+"F1.opRevolve","SWEPT_FACE",FACE,{"disambiguationData":[OSD([sQuery(id+"F0.wireOp",EDGE,"E13")])]})})})})})})})],"blendedInto":[makeQuery(id+"F40.boolean.opBoolean","SPLIT",FACE,{"disambiguationData":[TD([subQ0])],"derivedFrom":makeQuery(id+"F28.boolean.opBoolean","SPLIT",FACE,{"disambiguationData":[TD([subQ6])],"derivedFrom":makeQuery(id+"F27.boolean.opBoolean","SPLIT",FACE,{"disambiguationData":[TD([subQ59])],"derivedFrom":makeQuery(id+"F26.boolean.opBoolean","SPLIT",FACE,{"disambiguationData":[TD([subQ59])],"derivedFrom":makeQuery(id+"F25.boolean.opBoolean","SPLIT",FACE,{"disambiguationData":[TD([subQ59])],"derivedFrom":makeQuery(id+"F24.boolean.opBoolean","SPLIT",FACE,{"disambiguationData":[TD([subQ59])],"derivedFrom":makeQuery(id+"F1.opRevolve","SWEPT_FACE",FACE,{"disambiguationData":[OSD([sQuery(id+"F0.wireOp",EDGE,"E13")])]})})})})})})})]});}
            var Q5;
            {var subQ0=makeQuery(id+"F1.opRevolve","SWEPT_FACE",FACE,{"disambiguationData":[OSD([sQuery(id+"F0.wireOp",EDGE,"E10")])]});var subQ1=sQuery(id+"F4.wireOp",EDGE,"E26.14.3");var subQ2=sQuery(id+"F4.wireOp",EDGE,"E26.14.2");var subQ3=sQuery(id+"F3.wireOp",EDGE,"E20.14.3");var subQ4=sQuery(id+"F3.wireOp",EDGE,"E20.14.2");var subQ5=sQuery(id+"F3.wireOp",EDGE,"E20.14.1");var subQ6=makeQuery(id+"F7.opLoft","SWEPT_FACE",FACE,{"disambiguationData":[OSD([subQ5,subQ4,subQ3,sQuery(id+"F4.wireOp",EDGE,"E26.14.1"),subQ2,subQ1])]});var subQ13=makeQuery(id+"F40.opExtrude","CAP_FACE",FACE,{"disambiguationData":[OSD([sQuery(id+"F39.wireOp",EDGE,"E29"),sQuery(id+"F39.wireOp",EDGE,"E30")])],"isStart":false});var subQ48=sQuery(id+"F3.wireOp",EDGE,"E18.bottom");var subQ51=makeQuery(id+"F5.opLoft","CAP_FACE",FACE,{"disambiguationData":[OSD([makeQuery(id+"F3.imprint","IMPRINT",FACE,{"disambiguationData":[TD([[makeQuery(id+"F3.imprint","IMPRINT",EDGE,{"derivedFrom":subQ48}),1.0]])]})])],"isStart":true});Q5=makeQuery(id+"F44.opFillet","BLEND_EDGE",EDGE,{"blendedFrom":[makeQuery(id+"F40.boolean.opBoolean","INTERSECT",EDGE,{"derivedFrom":[subQ6,subQ13]}),makeQuery(id+"F40.boolean.opBoolean","SPLIT",FACE,{"disambiguationData":[TD([subQ0])],"derivedFrom":makeQuery(id+"F29.boolean.opBoolean","SPLIT",FACE,{"disambiguationData":[TD([subQ6])],"derivedFrom":makeQuery(id+"F28.boolean.opBoolean","SPLIT",FACE,{"disambiguationData":[TD([subQ51])],"derivedFrom":makeQuery(id+"F27.boolean.opBoolean","SPLIT",FACE,{"disambiguationData":[TD([subQ51])],"derivedFrom":makeQuery(id+"F26.boolean.opBoolean","SPLIT",FACE,{"disambiguationData":[TD([subQ51])],"derivedFrom":makeQuery(id+"F25.boolean.opBoolean","SPLIT",FACE,{"disambiguationData":[TD([subQ51])],"derivedFrom":makeQuery(id+"F24.boolean.opBoolean","SPLIT",FACE,{"disambiguationData":[TD([subQ51])],"derivedFrom":makeQuery(id+"F1.opRevolve","SWEPT_FACE",FACE,{"disambiguationData":[OSD([sQuery(id+"F0.wireOp",EDGE,"E13")])]})})})})})})})})],"blendedInto":[makeQuery(id+"F40.boolean.opBoolean","SPLIT",FACE,{"disambiguationData":[TD([subQ0])],"derivedFrom":makeQuery(id+"F29.boolean.opBoolean","SPLIT",FACE,{"disambiguationData":[TD([subQ6])],"derivedFrom":makeQuery(id+"F28.boolean.opBoolean","SPLIT",FACE,{"disambiguationData":[TD([subQ51])],"derivedFrom":makeQuery(id+"F27.boolean.opBoolean","SPLIT",FACE,{"disambiguationData":[TD([subQ51])],"derivedFrom":makeQuery(id+"F26.boolean.opBoolean","SPLIT",FACE,{"disambiguationData":[TD([subQ51])],"derivedFrom":makeQuery(id+"F25.boolean.opBoolean","SPLIT",FACE,{"disambiguationData":[TD([subQ51])],"derivedFrom":makeQuery(id+"F24.boolean.opBoolean","SPLIT",FACE,{"disambiguationData":[TD([subQ51])],"derivedFrom":makeQuery(id+"F1.opRevolve","SWEPT_FACE",FACE,{"disambiguationData":[OSD([sQuery(id+"F0.wireOp",EDGE,"E13")])]})})})})})})})})]});}
            var Q6;
            {var subQ0=makeQuery(id+"F1.opRevolve","SWEPT_FACE",FACE,{"disambiguationData":[OSD([sQuery(id+"F0.wireOp",EDGE,"E10")])]});var subQ7=sQuery(id+"F4.wireOp",EDGE,"E26.15.3");var subQ8=sQuery(id+"F4.wireOp",EDGE,"E26.15.2");var subQ9=sQuery(id+"F3.wireOp",EDGE,"E20.15.3");var subQ10=sQuery(id+"F3.wireOp",EDGE,"E20.15.2");var subQ11=sQuery(id+"F3.wireOp",EDGE,"E20.15.1");var subQ12=makeQuery(id+"F6.opLoft","SWEPT_FACE",FACE,{"disambiguationData":[OSD([subQ11,subQ10,subQ9,sQuery(id+"F4.wireOp",EDGE,"E26.15.1"),subQ8,subQ7])]});var subQ13=makeQuery(id+"F40.opExtrude","CAP_FACE",FACE,{"disambiguationData":[OSD([sQuery(id+"F39.wireOp",EDGE,"E29"),sQuery(id+"F39.wireOp",EDGE,"E30")])],"isStart":false});var subQ47=sQuery(id+"F3.wireOp",EDGE,"E18.bottom");var subQ50=makeQuery(id+"F5.opLoft","CAP_FACE",FACE,{"disambiguationData":[OSD([makeQuery(id+"F3.imprint","IMPRINT",FACE,{"disambiguationData":[TD([[makeQuery(id+"F3.imprint","IMPRINT",EDGE,{"derivedFrom":subQ47}),1.0]])]})])],"isStart":true});Q6=makeQuery(id+"F44.opFillet","BLEND_EDGE",EDGE,{"blendedFrom":[makeQuery(id+"F40.boolean.opBoolean","INTERSECT",EDGE,{"derivedFrom":[subQ12,subQ13]}),makeQuery(id+"F40.boolean.opBoolean","SPLIT",FACE,{"disambiguationData":[TD([subQ0])],"derivedFrom":makeQuery(id+"F30.boolean.opBoolean","SPLIT",FACE,{"disambiguationData":[TD([subQ12])],"derivedFrom":makeQuery(id+"F29.boolean.opBoolean","SPLIT",FACE,{"disambiguationData":[TD([subQ50])],"derivedFrom":makeQuery(id+"F28.boolean.opBoolean","SPLIT",FACE,{"disambiguationData":[TD([subQ50])],"derivedFrom":makeQuery(id+"F27.boolean.opBoolean","SPLIT",FACE,{"disambiguationData":[TD([subQ50])],"derivedFrom":makeQuery(id+"F26.boolean.opBoolean","SPLIT",FACE,{"disambiguationData":[TD([subQ50])],"derivedFrom":makeQuery(id+"F25.boolean.opBoolean","SPLIT",FACE,{"disambiguationData":[TD([subQ50])],"derivedFrom":makeQuery(id+"F24.boolean.opBoolean","SPLIT",FACE,{"disambiguationData":[TD([subQ50])],"derivedFrom":makeQuery(id+"F1.opRevolve","SWEPT_FACE",FACE,{"disambiguationData":[OSD([sQuery(id+"F0.wireOp",EDGE,"E13")])]})})})})})})})})})],"blendedInto":[makeQuery(id+"F40.boolean.opBoolean","SPLIT",FACE,{"disambiguationData":[TD([subQ0])],"derivedFrom":makeQuery(id+"F30.boolean.opBoolean","SPLIT",FACE,{"disambiguationData":[TD([subQ12])],"derivedFrom":makeQuery(id+"F29.boolean.opBoolean","SPLIT",FACE,{"disambiguationData":[TD([subQ50])],"derivedFrom":makeQuery(id+"F28.boolean.opBoolean","SPLIT",FACE,{"disambiguationData":[TD([subQ50])],"derivedFrom":makeQuery(id+"F27.boolean.opBoolean","SPLIT",FACE,{"disambiguationData":[TD([subQ50])],"derivedFrom":makeQuery(id+"F26.boolean.opBoolean","SPLIT",FACE,{"disambiguationData":[TD([subQ50])],"derivedFrom":makeQuery(id+"F25.boolean.opBoolean","SPLIT",FACE,{"disambiguationData":[TD([subQ50])],"derivedFrom":makeQuery(id+"F24.boolean.opBoolean","SPLIT",FACE,{"disambiguationData":[TD([subQ50])],"derivedFrom":makeQuery(id+"F1.opRevolve","SWEPT_FACE",FACE,{"disambiguationData":[OSD([sQuery(id+"F0.wireOp",EDGE,"E13")])]})})})})})})})})})]});}
            var Q7;
            {var subQ0=makeQuery(id+"F1.opRevolve","SWEPT_FACE",FACE,{"disambiguationData":[OSD([sQuery(id+"F0.wireOp",EDGE,"E10")])]});var subQ1=sQuery(id+"F4.wireOp",EDGE,"E23");var subQ2=sQuery(id+"F4.wireOp",EDGE,"E22");var subQ3=sQuery(id+"F3.wireOp",EDGE,"E18.right");var subQ4=sQuery(id+"F3.wireOp",EDGE,"E18.top");var subQ5=sQuery(id+"F3.wireOp",EDGE,"E18.bottom");var subQ6=makeQuery(id+"F5.opLoft","SWEPT_FACE",FACE,{"disambiguationData":[OSD([subQ5,subQ4,subQ3,subQ2,subQ1,sQuery(id+"F4.wireOp",EDGE,"E24")])]});var subQ13=makeQuery(id+"F40.opExtrude","CAP_FACE",FACE,{"disambiguationData":[OSD([sQuery(id+"F39.wireOp",EDGE,"E29"),sQuery(id+"F39.wireOp",EDGE,"E30")])],"isStart":false});var subQ58=makeQuery(id+"F5.opLoft","CAP_FACE",FACE,{"disambiguationData":[OSD([makeQuery(id+"F3.imprint","IMPRINT",FACE,{"disambiguationData":[TD([[makeQuery(id+"F3.imprint","IMPRINT",EDGE,{"derivedFrom":subQ5}),1.0]])]})])],"isStart":true});Q7=makeQuery(id+"F44.opFillet","BLEND_EDGE",EDGE,{"blendedFrom":[makeQuery(id+"F40.boolean.opBoolean","INTERSECT",EDGE,{"derivedFrom":[subQ6,subQ13]}),makeQuery(id+"F40.boolean.opBoolean","SPLIT",FACE,{"disambiguationData":[TD([subQ0])],"derivedFrom":makeQuery(id+"F31.boolean.opBoolean","SPLIT",FACE,{"disambiguationData":[TD([subQ6])],"derivedFrom":makeQuery(id+"F30.boolean.opBoolean","SPLIT",FACE,{"disambiguationData":[TD([subQ58])],"derivedFrom":makeQuery(id+"F29.boolean.opBoolean","SPLIT",FACE,{"disambiguationData":[TD([subQ58])],"derivedFrom":makeQuery(id+"F28.boolean.opBoolean","SPLIT",FACE,{"disambiguationData":[TD([subQ58])],"derivedFrom":makeQuery(id+"F27.boolean.opBoolean","SPLIT",FACE,{"disambiguationData":[TD([subQ58])],"derivedFrom":makeQuery(id+"F26.boolean.opBoolean","SPLIT",FACE,{"disambiguationData":[TD([subQ58])],"derivedFrom":makeQuery(id+"F25.boolean.opBoolean","SPLIT",FACE,{"disambiguationData":[TD([subQ58])],"derivedFrom":makeQuery(id+"F24.boolean.opBoolean","SPLIT",FACE,{"disambiguationData":[TD([subQ58])],"derivedFrom":makeQuery(id+"F1.opRevolve","SWEPT_FACE",FACE,{"disambiguationData":[OSD([sQuery(id+"F0.wireOp",EDGE,"E13")])]})})})})})})})})})})],"blendedInto":[makeQuery(id+"F40.boolean.opBoolean","SPLIT",FACE,{"disambiguationData":[TD([subQ0])],"derivedFrom":makeQuery(id+"F31.boolean.opBoolean","SPLIT",FACE,{"disambiguationData":[TD([subQ6])],"derivedFrom":makeQuery(id+"F30.boolean.opBoolean","SPLIT",FACE,{"disambiguationData":[TD([subQ58])],"derivedFrom":makeQuery(id+"F29.boolean.opBoolean","SPLIT",FACE,{"disambiguationData":[TD([subQ58])],"derivedFrom":makeQuery(id+"F28.boolean.opBoolean","SPLIT",FACE,{"disambiguationData":[TD([subQ58])],"derivedFrom":makeQuery(id+"F27.boolean.opBoolean","SPLIT",FACE,{"disambiguationData":[TD([subQ58])],"derivedFrom":makeQuery(id+"F26.boolean.opBoolean","SPLIT",FACE,{"disambiguationData":[TD([subQ58])],"derivedFrom":makeQuery(id+"F25.boolean.opBoolean","SPLIT",FACE,{"disambiguationData":[TD([subQ58])],"derivedFrom":makeQuery(id+"F24.boolean.opBoolean","SPLIT",FACE,{"disambiguationData":[TD([subQ58])],"derivedFrom":makeQuery(id+"F1.opRevolve","SWEPT_FACE",FACE,{"disambiguationData":[OSD([sQuery(id+"F0.wireOp",EDGE,"E13")])]})})})})})})})})})})]});}
            var Q8;
            {var subQ0=makeQuery(id+"F1.opRevolve","SWEPT_FACE",FACE,{"disambiguationData":[OSD([sQuery(id+"F0.wireOp",EDGE,"E10")])]});var subQ1=sQuery(id+"F4.wireOp",EDGE,"E23");var subQ2=sQuery(id+"F4.wireOp",EDGE,"E22");var subQ3=sQuery(id+"F3.wireOp",EDGE,"E18.left");var subQ4=sQuery(id+"F3.wireOp",EDGE,"E18.top");var subQ5=sQuery(id+"F3.wireOp",EDGE,"E18.bottom");var subQ6=makeQuery(id+"F5.opLoft","SWEPT_FACE",FACE,{"disambiguationData":[OSD([subQ5,subQ4,subQ3,sQuery(id+"F4.wireOp",EDGE,"E21"),subQ2,subQ1])]});var subQ7=sQuery(id+"F4.wireOp",EDGE,"E26.1.3");var subQ8=sQuery(id+"F4.wireOp",EDGE,"E26.1.2");var subQ9=sQuery(id+"F3.wireOp",EDGE,"E20.1.3");var subQ10=sQuery(id+"F3.wireOp",EDGE,"E20.1.2");var subQ11=sQuery(id+"F3.wireOp",EDGE,"E20.1.1");var subQ12=makeQuery(id+"F20.opLoft","SWEPT_FACE",FACE,{"disambiguationData":[OSD([subQ11,subQ10,subQ9,sQuery(id+"F4.wireOp",EDGE,"E26.1.1"),subQ8,subQ7])]});var subQ13=makeQuery(id+"F40.opExtrude","CAP_FACE",FACE,{"disambiguationData":[OSD([sQuery(id+"F39.wireOp",EDGE,"E29"),sQuery(id+"F39.wireOp",EDGE,"E30")])],"isStart":false});var subQ64=sQuery(id+"F3.wireOp",EDGE,"E20.7.0");var subQ72=makeQuery(id+"F14.opLoft","CAP_FACE",FACE,{"disambiguationData":[OSD([makeQuery(id+"F3.imprint","IMPRINT",FACE,{"disambiguationData":[TD([[makeQuery(id+"F3.imprint","IMPRINT",EDGE,{"derivedFrom":subQ64}),-1.0]])]})])],"isStart":true});var subQ80=makeQuery(id+"F5.opLoft","CAP_FACE",FACE,{"disambiguationData":[OSD([makeQuery(id+"F3.imprint","IMPRINT",FACE,{"disambiguationData":[TD([[makeQuery(id+"F3.imprint","IMPRINT",EDGE,{"derivedFrom":subQ5}),1.0]])]})])],"isStart":true});Q8=makeQuery(id+"F44.opFillet","BLEND_EDGE",EDGE,{"blendedFrom":[makeQuery(id+"F40.boolean.opBoolean","INTERSECT",EDGE,{"derivedFrom":[subQ12,subQ13]}),makeQuery(id+"F40.boolean.opBoolean","SPLIT",FACE,{"disambiguationData":[TD([subQ0])],"derivedFrom":makeQuery(id+"F32.boolean.opBoolean","SPLIT",FACE,{"disambiguationData":[TD([subQ6])],"derivedFrom":makeQuery(id+"F31.boolean.opBoolean","SPLIT",FACE,{"disambiguationData":[TD([subQ72])],"derivedFrom":makeQuery(id+"F30.boolean.opBoolean","SPLIT",FACE,{"disambiguationData":[TD([subQ80])],"derivedFrom":makeQuery(id+"F29.boolean.opBoolean","SPLIT",FACE,{"disambiguationData":[TD([subQ80])],"derivedFrom":makeQuery(id+"F28.boolean.opBoolean","SPLIT",FACE,{"disambiguationData":[TD([subQ80])],"derivedFrom":makeQuery(id+"F27.boolean.opBoolean","SPLIT",FACE,{"disambiguationData":[TD([subQ80])],"derivedFrom":makeQuery(id+"F26.boolean.opBoolean","SPLIT",FACE,{"disambiguationData":[TD([subQ80])],"derivedFrom":makeQuery(id+"F25.boolean.opBoolean","SPLIT",FACE,{"disambiguationData":[TD([subQ80])],"derivedFrom":makeQuery(id+"F24.boolean.opBoolean","SPLIT",FACE,{"disambiguationData":[TD([subQ80])],"derivedFrom":makeQuery(id+"F1.opRevolve","SWEPT_FACE",FACE,{"disambiguationData":[OSD([sQuery(id+"F0.wireOp",EDGE,"E13")])]})})})})})})})})})})})],"blendedInto":[makeQuery(id+"F40.boolean.opBoolean","SPLIT",FACE,{"disambiguationData":[TD([subQ0])],"derivedFrom":makeQuery(id+"F32.boolean.opBoolean","SPLIT",FACE,{"disambiguationData":[TD([subQ6])],"derivedFrom":makeQuery(id+"F31.boolean.opBoolean","SPLIT",FACE,{"disambiguationData":[TD([subQ72])],"derivedFrom":makeQuery(id+"F30.boolean.opBoolean","SPLIT",FACE,{"disambiguationData":[TD([subQ80])],"derivedFrom":makeQuery(id+"F29.boolean.opBoolean","SPLIT",FACE,{"disambiguationData":[TD([subQ80])],"derivedFrom":makeQuery(id+"F28.boolean.opBoolean","SPLIT",FACE,{"disambiguationData":[TD([subQ80])],"derivedFrom":makeQuery(id+"F27.boolean.opBoolean","SPLIT",FACE,{"disambiguationData":[TD([subQ80])],"derivedFrom":makeQuery(id+"F26.boolean.opBoolean","SPLIT",FACE,{"disambiguationData":[TD([subQ80])],"derivedFrom":makeQuery(id+"F25.boolean.opBoolean","SPLIT",FACE,{"disambiguationData":[TD([subQ80])],"derivedFrom":makeQuery(id+"F24.boolean.opBoolean","SPLIT",FACE,{"disambiguationData":[TD([subQ80])],"derivedFrom":makeQuery(id+"F1.opRevolve","SWEPT_FACE",FACE,{"disambiguationData":[OSD([sQuery(id+"F0.wireOp",EDGE,"E13")])]})})})})})})})})})})})]});}
            var Q9;
            {var subQ0=makeQuery(id+"F1.opRevolve","SWEPT_FACE",FACE,{"disambiguationData":[OSD([sQuery(id+"F0.wireOp",EDGE,"E10")])]});var subQ1=sQuery(id+"F4.wireOp",EDGE,"E26.2.3");var subQ2=sQuery(id+"F4.wireOp",EDGE,"E26.2.2");var subQ3=sQuery(id+"F3.wireOp",EDGE,"E20.2.3");var subQ4=sQuery(id+"F3.wireOp",EDGE,"E20.2.2");var subQ5=sQuery(id+"F3.wireOp",EDGE,"E20.2.1");var subQ6=makeQuery(id+"F19.opLoft","SWEPT_FACE",FACE,{"disambiguationData":[OSD([subQ5,subQ4,subQ3,sQuery(id+"F4.wireOp",EDGE,"E26.2.1"),subQ2,subQ1])]});var subQ13=makeQuery(id+"F40.opExtrude","CAP_FACE",FACE,{"disambiguationData":[OSD([sQuery(id+"F39.wireOp",EDGE,"E29"),sQuery(id+"F39.wireOp",EDGE,"E30")])],"isStart":false});var subQ55=sQuery(id+"F3.wireOp",EDGE,"E20.7.0");var subQ62=makeQuery(id+"F14.opLoft","CAP_FACE",FACE,{"disambiguationData":[OSD([makeQuery(id+"F3.imprint","IMPRINT",FACE,{"disambiguationData":[TD([[makeQuery(id+"F3.imprint","IMPRINT",EDGE,{"derivedFrom":subQ55}),-1.0]])]})])],"isStart":true});var subQ75=sQuery(id+"F3.wireOp",EDGE,"E18.bottom");var subQ80=makeQuery(id+"F5.opLoft","CAP_FACE",FACE,{"disambiguationData":[OSD([makeQuery(id+"F3.imprint","IMPRINT",FACE,{"disambiguationData":[TD([[makeQuery(id+"F3.imprint","IMPRINT",EDGE,{"derivedFrom":subQ75}),1.0]])]})])],"isStart":true});Q9=makeQuery(id+"F44.opFillet","BLEND_EDGE",EDGE,{"blendedFrom":[makeQuery(id+"F40.boolean.opBoolean","INTERSECT",EDGE,{"derivedFrom":[subQ6,subQ13]}),makeQuery(id+"F40.boolean.opBoolean","SPLIT",FACE,{"disambiguationData":[TD([subQ0])],"derivedFrom":makeQuery(id+"F33.boolean.opBoolean","SPLIT",FACE,{"disambiguationData":[TD([subQ6])],"derivedFrom":makeQuery(id+"F32.boolean.opBoolean","SPLIT",FACE,{"disambiguationData":[TD([subQ62])],"derivedFrom":makeQuery(id+"F31.boolean.opBoolean","SPLIT",FACE,{"disambiguationData":[TD([subQ62])],"derivedFrom":makeQuery(id+"F30.boolean.opBoolean","SPLIT",FACE,{"disambiguationData":[TD([subQ80])],"derivedFrom":makeQuery(id+"F29.boolean.opBoolean","SPLIT",FACE,{"disambiguationData":[TD([subQ80])],"derivedFrom":makeQuery(id+"F28.boolean.opBoolean","SPLIT",FACE,{"disambiguationData":[TD([subQ80])],"derivedFrom":makeQuery(id+"F27.boolean.opBoolean","SPLIT",FACE,{"disambiguationData":[TD([subQ80])],"derivedFrom":makeQuery(id+"F26.boolean.opBoolean","SPLIT",FACE,{"disambiguationData":[TD([subQ80])],"derivedFrom":makeQuery(id+"F25.boolean.opBoolean","SPLIT",FACE,{"disambiguationData":[TD([subQ80])],"derivedFrom":makeQuery(id+"F24.boolean.opBoolean","SPLIT",FACE,{"disambiguationData":[TD([subQ80])],"derivedFrom":makeQuery(id+"F1.opRevolve","SWEPT_FACE",FACE,{"disambiguationData":[OSD([sQuery(id+"F0.wireOp",EDGE,"E13")])]})})})})})})})})})})})})],"blendedInto":[makeQuery(id+"F40.boolean.opBoolean","SPLIT",FACE,{"disambiguationData":[TD([subQ0])],"derivedFrom":makeQuery(id+"F33.boolean.opBoolean","SPLIT",FACE,{"disambiguationData":[TD([subQ6])],"derivedFrom":makeQuery(id+"F32.boolean.opBoolean","SPLIT",FACE,{"disambiguationData":[TD([subQ62])],"derivedFrom":makeQuery(id+"F31.boolean.opBoolean","SPLIT",FACE,{"disambiguationData":[TD([subQ62])],"derivedFrom":makeQuery(id+"F30.boolean.opBoolean","SPLIT",FACE,{"disambiguationData":[TD([subQ80])],"derivedFrom":makeQuery(id+"F29.boolean.opBoolean","SPLIT",FACE,{"disambiguationData":[TD([subQ80])],"derivedFrom":makeQuery(id+"F28.boolean.opBoolean","SPLIT",FACE,{"disambiguationData":[TD([subQ80])],"derivedFrom":makeQuery(id+"F27.boolean.opBoolean","SPLIT",FACE,{"disambiguationData":[TD([subQ80])],"derivedFrom":makeQuery(id+"F26.boolean.opBoolean","SPLIT",FACE,{"disambiguationData":[TD([subQ80])],"derivedFrom":makeQuery(id+"F25.boolean.opBoolean","SPLIT",FACE,{"disambiguationData":[TD([subQ80])],"derivedFrom":makeQuery(id+"F24.boolean.opBoolean","SPLIT",FACE,{"disambiguationData":[TD([subQ80])],"derivedFrom":makeQuery(id+"F1.opRevolve","SWEPT_FACE",FACE,{"disambiguationData":[OSD([sQuery(id+"F0.wireOp",EDGE,"E13")])]})})})})})})})})})})})})]});}
            var Q10;
            {var subQ0=makeQuery(id+"F1.opRevolve","SWEPT_FACE",FACE,{"disambiguationData":[OSD([sQuery(id+"F0.wireOp",EDGE,"E10")])]});var subQ1=sQuery(id+"F4.wireOp",EDGE,"E26.3.3");var subQ2=sQuery(id+"F4.wireOp",EDGE,"E26.3.2");var subQ3=sQuery(id+"F3.wireOp",EDGE,"E20.3.3");var subQ4=sQuery(id+"F3.wireOp",EDGE,"E20.3.2");var subQ5=sQuery(id+"F3.wireOp",EDGE,"E20.3.1");var subQ6=makeQuery(id+"F18.opLoft","SWEPT_FACE",FACE,{"disambiguationData":[OSD([subQ5,subQ4,subQ3,sQuery(id+"F4.wireOp",EDGE,"E26.3.1"),subQ2,subQ1])]});var subQ13=makeQuery(id+"F40.opExtrude","CAP_FACE",FACE,{"disambiguationData":[OSD([sQuery(id+"F39.wireOp",EDGE,"E29"),sQuery(id+"F39.wireOp",EDGE,"E30")])],"isStart":false});var subQ35=sQuery(id+"F3.wireOp",EDGE,"E20.7.0");var subQ39=makeQuery(id+"F14.opLoft","CAP_FACE",FACE,{"disambiguationData":[OSD([makeQuery(id+"F3.imprint","IMPRINT",FACE,{"disambiguationData":[TD([[makeQuery(id+"F3.imprint","IMPRINT",EDGE,{"derivedFrom":subQ35}),-1.0]])]})])],"isStart":true});var subQ75=sQuery(id+"F3.wireOp",EDGE,"E18.bottom");var subQ80=makeQuery(id+"F5.opLoft","CAP_FACE",FACE,{"disambiguationData":[OSD([makeQuery(id+"F3.imprint","IMPRINT",FACE,{"disambiguationData":[TD([[makeQuery(id+"F3.imprint","IMPRINT",EDGE,{"derivedFrom":subQ75}),1.0]])]})])],"isStart":true});Q10=makeQuery(id+"F44.opFillet","BLEND_EDGE",EDGE,{"blendedFrom":[makeQuery(id+"F40.boolean.opBoolean","INTERSECT",EDGE,{"derivedFrom":[subQ6,subQ13]}),makeQuery(id+"F40.boolean.opBoolean","SPLIT",FACE,{"disambiguationData":[TD([subQ0])],"derivedFrom":makeQuery(id+"F34.boolean.opBoolean","SPLIT",FACE,{"disambiguationData":[TD([subQ6])],"derivedFrom":makeQuery(id+"F33.boolean.opBoolean","SPLIT",FACE,{"disambiguationData":[TD([subQ39])],"derivedFrom":makeQuery(id+"F32.boolean.opBoolean","SPLIT",FACE,{"disambiguationData":[TD([subQ39])],"derivedFrom":makeQuery(id+"F31.boolean.opBoolean","SPLIT",FACE,{"disambiguationData":[TD([subQ39])],"derivedFrom":makeQuery(id+"F30.boolean.opBoolean","SPLIT",FACE,{"disambiguationData":[TD([subQ80])],"derivedFrom":makeQuery(id+"F29.boolean.opBoolean","SPLIT",FACE,{"disambiguationData":[TD([subQ80])],"derivedFrom":makeQuery(id+"F28.boolean.opBoolean","SPLIT",FACE,{"disambiguationData":[TD([subQ80])],"derivedFrom":makeQuery(id+"F27.boolean.opBoolean","SPLIT",FACE,{"disambiguationData":[TD([subQ80])],"derivedFrom":makeQuery(id+"F26.boolean.opBoolean","SPLIT",FACE,{"disambiguationData":[TD([subQ80])],"derivedFrom":makeQuery(id+"F25.boolean.opBoolean","SPLIT",FACE,{"disambiguationData":[TD([subQ80])],"derivedFrom":makeQuery(id+"F24.boolean.opBoolean","SPLIT",FACE,{"disambiguationData":[TD([subQ80])],"derivedFrom":makeQuery(id+"F1.opRevolve","SWEPT_FACE",FACE,{"disambiguationData":[OSD([sQuery(id+"F0.wireOp",EDGE,"E13")])]})})})})})})})})})})})})})],"blendedInto":[makeQuery(id+"F40.boolean.opBoolean","SPLIT",FACE,{"disambiguationData":[TD([subQ0])],"derivedFrom":makeQuery(id+"F34.boolean.opBoolean","SPLIT",FACE,{"disambiguationData":[TD([subQ6])],"derivedFrom":makeQuery(id+"F33.boolean.opBoolean","SPLIT",FACE,{"disambiguationData":[TD([subQ39])],"derivedFrom":makeQuery(id+"F32.boolean.opBoolean","SPLIT",FACE,{"disambiguationData":[TD([subQ39])],"derivedFrom":makeQuery(id+"F31.boolean.opBoolean","SPLIT",FACE,{"disambiguationData":[TD([subQ39])],"derivedFrom":makeQuery(id+"F30.boolean.opBoolean","SPLIT",FACE,{"disambiguationData":[TD([subQ80])],"derivedFrom":makeQuery(id+"F29.boolean.opBoolean","SPLIT",FACE,{"disambiguationData":[TD([subQ80])],"derivedFrom":makeQuery(id+"F28.boolean.opBoolean","SPLIT",FACE,{"disambiguationData":[TD([subQ80])],"derivedFrom":makeQuery(id+"F27.boolean.opBoolean","SPLIT",FACE,{"disambiguationData":[TD([subQ80])],"derivedFrom":makeQuery(id+"F26.boolean.opBoolean","SPLIT",FACE,{"disambiguationData":[TD([subQ80])],"derivedFrom":makeQuery(id+"F25.boolean.opBoolean","SPLIT",FACE,{"disambiguationData":[TD([subQ80])],"derivedFrom":makeQuery(id+"F24.boolean.opBoolean","SPLIT",FACE,{"disambiguationData":[TD([subQ80])],"derivedFrom":makeQuery(id+"F1.opRevolve","SWEPT_FACE",FACE,{"disambiguationData":[OSD([sQuery(id+"F0.wireOp",EDGE,"E13")])]})})})})})})})})})})})})})]});}
            var Q11;
            {var subQ0=makeQuery(id+"F1.opRevolve","SWEPT_FACE",FACE,{"disambiguationData":[OSD([sQuery(id+"F0.wireOp",EDGE,"E10")])]});var subQ7=sQuery(id+"F4.wireOp",EDGE,"E26.4.3");var subQ8=sQuery(id+"F4.wireOp",EDGE,"E26.4.2");var subQ9=sQuery(id+"F3.wireOp",EDGE,"E20.4.3");var subQ10=sQuery(id+"F3.wireOp",EDGE,"E20.4.2");var subQ11=sQuery(id+"F3.wireOp",EDGE,"E20.4.1");var subQ12=makeQuery(id+"F17.opLoft","SWEPT_FACE",FACE,{"disambiguationData":[OSD([subQ11,subQ10,subQ9,sQuery(id+"F4.wireOp",EDGE,"E26.4.1"),subQ8,subQ7])]});var subQ13=makeQuery(id+"F40.opExtrude","CAP_FACE",FACE,{"disambiguationData":[OSD([sQuery(id+"F39.wireOp",EDGE,"E29"),sQuery(id+"F39.wireOp",EDGE,"E30")])],"isStart":false});var subQ32=sQuery(id+"F3.wireOp",EDGE,"E20.7.0");var subQ36=makeQuery(id+"F14.opLoft","CAP_FACE",FACE,{"disambiguationData":[OSD([makeQuery(id+"F3.imprint","IMPRINT",FACE,{"disambiguationData":[TD([[makeQuery(id+"F3.imprint","IMPRINT",EDGE,{"derivedFrom":subQ32}),-1.0]])]})])],"isStart":true});var subQ75=sQuery(id+"F3.wireOp",EDGE,"E18.bottom");var subQ80=makeQuery(id+"F5.opLoft","CAP_FACE",FACE,{"disambiguationData":[OSD([makeQuery(id+"F3.imprint","IMPRINT",FACE,{"disambiguationData":[TD([[makeQuery(id+"F3.imprint","IMPRINT",EDGE,{"derivedFrom":subQ75}),1.0]])]})])],"isStart":true});Q11=makeQuery(id+"F44.opFillet","BLEND_EDGE",EDGE,{"blendedFrom":[makeQuery(id+"F40.boolean.opBoolean","INTERSECT",EDGE,{"derivedFrom":[subQ12,subQ13]}),makeQuery(id+"F40.boolean.opBoolean","SPLIT",FACE,{"disambiguationData":[TD([subQ0])],"derivedFrom":makeQuery(id+"F35.boolean.opBoolean","SPLIT",FACE,{"disambiguationData":[TD([subQ12])],"derivedFrom":makeQuery(id+"F34.boolean.opBoolean","SPLIT",FACE,{"disambiguationData":[TD([subQ36])],"derivedFrom":makeQuery(id+"F33.boolean.opBoolean","SPLIT",FACE,{"disambiguationData":[TD([subQ36])],"derivedFrom":makeQuery(id+"F32.boolean.opBoolean","SPLIT",FACE,{"disambiguationData":[TD([subQ36])],"derivedFrom":makeQuery(id+"F31.boolean.opBoolean","SPLIT",FACE,{"disambiguationData":[TD([subQ36])],"derivedFrom":makeQuery(id+"F30.boolean.opBoolean","SPLIT",FACE,{"disambiguationData":[TD([subQ80])],"derivedFrom":makeQuery(id+"F29.boolean.opBoolean","SPLIT",FACE,{"disambiguationData":[TD([subQ80])],"derivedFrom":makeQuery(id+"F28.boolean.opBoolean","SPLIT",FACE,{"disambiguationData":[TD([subQ80])],"derivedFrom":makeQuery(id+"F27.boolean.opBoolean","SPLIT",FACE,{"disambiguationData":[TD([subQ80])],"derivedFrom":makeQuery(id+"F26.boolean.opBoolean","SPLIT",FACE,{"disambiguationData":[TD([subQ80])],"derivedFrom":makeQuery(id+"F25.boolean.opBoolean","SPLIT",FACE,{"disambiguationData":[TD([subQ80])],"derivedFrom":makeQuery(id+"F24.boolean.opBoolean","SPLIT",FACE,{"disambiguationData":[TD([subQ80])],"derivedFrom":makeQuery(id+"F1.opRevolve","SWEPT_FACE",FACE,{"disambiguationData":[OSD([sQuery(id+"F0.wireOp",EDGE,"E13")])]})})})})})})})})})})})})})})],"blendedInto":[makeQuery(id+"F40.boolean.opBoolean","SPLIT",FACE,{"disambiguationData":[TD([subQ0])],"derivedFrom":makeQuery(id+"F35.boolean.opBoolean","SPLIT",FACE,{"disambiguationData":[TD([subQ12])],"derivedFrom":makeQuery(id+"F34.boolean.opBoolean","SPLIT",FACE,{"disambiguationData":[TD([subQ36])],"derivedFrom":makeQuery(id+"F33.boolean.opBoolean","SPLIT",FACE,{"disambiguationData":[TD([subQ36])],"derivedFrom":makeQuery(id+"F32.boolean.opBoolean","SPLIT",FACE,{"disambiguationData":[TD([subQ36])],"derivedFrom":makeQuery(id+"F31.boolean.opBoolean","SPLIT",FACE,{"disambiguationData":[TD([subQ36])],"derivedFrom":makeQuery(id+"F30.boolean.opBoolean","SPLIT",FACE,{"disambiguationData":[TD([subQ80])],"derivedFrom":makeQuery(id+"F29.boolean.opBoolean","SPLIT",FACE,{"disambiguationData":[TD([subQ80])],"derivedFrom":makeQuery(id+"F28.boolean.opBoolean","SPLIT",FACE,{"disambiguationData":[TD([subQ80])],"derivedFrom":makeQuery(id+"F27.boolean.opBoolean","SPLIT",FACE,{"disambiguationData":[TD([subQ80])],"derivedFrom":makeQuery(id+"F26.boolean.opBoolean","SPLIT",FACE,{"disambiguationData":[TD([subQ80])],"derivedFrom":makeQuery(id+"F25.boolean.opBoolean","SPLIT",FACE,{"disambiguationData":[TD([subQ80])],"derivedFrom":makeQuery(id+"F24.boolean.opBoolean","SPLIT",FACE,{"disambiguationData":[TD([subQ80])],"derivedFrom":makeQuery(id+"F1.opRevolve","SWEPT_FACE",FACE,{"disambiguationData":[OSD([sQuery(id+"F0.wireOp",EDGE,"E13")])]})})})})})})})})})})})})})})]});}
            var Q12;
            {var subQ0=makeQuery(id+"F1.opRevolve","SWEPT_FACE",FACE,{"disambiguationData":[OSD([sQuery(id+"F0.wireOp",EDGE,"E10")])]});var subQ7=sQuery(id+"F4.wireOp",EDGE,"E26.5.3");var subQ8=sQuery(id+"F4.wireOp",EDGE,"E26.5.2");var subQ9=sQuery(id+"F3.wireOp",EDGE,"E20.5.3");var subQ10=sQuery(id+"F3.wireOp",EDGE,"E20.5.2");var subQ11=sQuery(id+"F3.wireOp",EDGE,"E20.5.1");var subQ12=makeQuery(id+"F16.opLoft","SWEPT_FACE",FACE,{"disambiguationData":[OSD([subQ11,subQ10,subQ9,sQuery(id+"F4.wireOp",EDGE,"E26.5.1"),subQ8,subQ7])]});var subQ13=makeQuery(id+"F40.opExtrude","CAP_FACE",FACE,{"disambiguationData":[OSD([sQuery(id+"F39.wireOp",EDGE,"E29"),sQuery(id+"F39.wireOp",EDGE,"E30")])],"isStart":false});var subQ26=sQuery(id+"F3.wireOp",EDGE,"E20.7.0");var subQ30=makeQuery(id+"F14.opLoft","CAP_FACE",FACE,{"disambiguationData":[OSD([makeQuery(id+"F3.imprint","IMPRINT",FACE,{"disambiguationData":[TD([[makeQuery(id+"F3.imprint","IMPRINT",EDGE,{"derivedFrom":subQ26}),-1.0]])]})])],"isStart":true});var subQ75=sQuery(id+"F3.wireOp",EDGE,"E18.bottom");var subQ80=makeQuery(id+"F5.opLoft","CAP_FACE",FACE,{"disambiguationData":[OSD([makeQuery(id+"F3.imprint","IMPRINT",FACE,{"disambiguationData":[TD([[makeQuery(id+"F3.imprint","IMPRINT",EDGE,{"derivedFrom":subQ75}),1.0]])]})])],"isStart":true});Q12=makeQuery(id+"F44.opFillet","BLEND_EDGE",EDGE,{"blendedFrom":[makeQuery(id+"F40.boolean.opBoolean","INTERSECT",EDGE,{"derivedFrom":[subQ12,subQ13]}),makeQuery(id+"F40.boolean.opBoolean","SPLIT",FACE,{"disambiguationData":[TD([subQ0])],"derivedFrom":makeQuery(id+"F36.boolean.opBoolean","SPLIT",FACE,{"disambiguationData":[TD([subQ12])],"derivedFrom":makeQuery(id+"F35.boolean.opBoolean","SPLIT",FACE,{"disambiguationData":[TD([subQ30])],"derivedFrom":makeQuery(id+"F34.boolean.opBoolean","SPLIT",FACE,{"disambiguationData":[TD([subQ30])],"derivedFrom":makeQuery(id+"F33.boolean.opBoolean","SPLIT",FACE,{"disambiguationData":[TD([subQ30])],"derivedFrom":makeQuery(id+"F32.boolean.opBoolean","SPLIT",FACE,{"disambiguationData":[TD([subQ30])],"derivedFrom":makeQuery(id+"F31.boolean.opBoolean","SPLIT",FACE,{"disambiguationData":[TD([subQ30])],"derivedFrom":makeQuery(id+"F30.boolean.opBoolean","SPLIT",FACE,{"disambiguationData":[TD([subQ80])],"derivedFrom":makeQuery(id+"F29.boolean.opBoolean","SPLIT",FACE,{"disambiguationData":[TD([subQ80])],"derivedFrom":makeQuery(id+"F28.boolean.opBoolean","SPLIT",FACE,{"disambiguationData":[TD([subQ80])],"derivedFrom":makeQuery(id+"F27.boolean.opBoolean","SPLIT",FACE,{"disambiguationData":[TD([subQ80])],"derivedFrom":makeQuery(id+"F26.boolean.opBoolean","SPLIT",FACE,{"disambiguationData":[TD([subQ80])],"derivedFrom":makeQuery(id+"F25.boolean.opBoolean","SPLIT",FACE,{"disambiguationData":[TD([subQ80])],"derivedFrom":makeQuery(id+"F24.boolean.opBoolean","SPLIT",FACE,{"disambiguationData":[TD([subQ80])],"derivedFrom":makeQuery(id+"F1.opRevolve","SWEPT_FACE",FACE,{"disambiguationData":[OSD([sQuery(id+"F0.wireOp",EDGE,"E13")])]})})})})})})})})})})})})})})})],"blendedInto":[makeQuery(id+"F40.boolean.opBoolean","SPLIT",FACE,{"disambiguationData":[TD([subQ0])],"derivedFrom":makeQuery(id+"F36.boolean.opBoolean","SPLIT",FACE,{"disambiguationData":[TD([subQ12])],"derivedFrom":makeQuery(id+"F35.boolean.opBoolean","SPLIT",FACE,{"disambiguationData":[TD([subQ30])],"derivedFrom":makeQuery(id+"F34.boolean.opBoolean","SPLIT",FACE,{"disambiguationData":[TD([subQ30])],"derivedFrom":makeQuery(id+"F33.boolean.opBoolean","SPLIT",FACE,{"disambiguationData":[TD([subQ30])],"derivedFrom":makeQuery(id+"F32.boolean.opBoolean","SPLIT",FACE,{"disambiguationData":[TD([subQ30])],"derivedFrom":makeQuery(id+"F31.boolean.opBoolean","SPLIT",FACE,{"disambiguationData":[TD([subQ30])],"derivedFrom":makeQuery(id+"F30.boolean.opBoolean","SPLIT",FACE,{"disambiguationData":[TD([subQ80])],"derivedFrom":makeQuery(id+"F29.boolean.opBoolean","SPLIT",FACE,{"disambiguationData":[TD([subQ80])],"derivedFrom":makeQuery(id+"F28.boolean.opBoolean","SPLIT",FACE,{"disambiguationData":[TD([subQ80])],"derivedFrom":makeQuery(id+"F27.boolean.opBoolean","SPLIT",FACE,{"disambiguationData":[TD([subQ80])],"derivedFrom":makeQuery(id+"F26.boolean.opBoolean","SPLIT",FACE,{"disambiguationData":[TD([subQ80])],"derivedFrom":makeQuery(id+"F25.boolean.opBoolean","SPLIT",FACE,{"disambiguationData":[TD([subQ80])],"derivedFrom":makeQuery(id+"F24.boolean.opBoolean","SPLIT",FACE,{"disambiguationData":[TD([subQ80])],"derivedFrom":makeQuery(id+"F1.opRevolve","SWEPT_FACE",FACE,{"disambiguationData":[OSD([sQuery(id+"F0.wireOp",EDGE,"E13")])]})})})})})})})})})})})})})})})]});}
            var Q13;
            {var subQ0=makeQuery(id+"F1.opRevolve","SWEPT_FACE",FACE,{"disambiguationData":[OSD([sQuery(id+"F0.wireOp",EDGE,"E10")])]});var subQ1=sQuery(id+"F4.wireOp",EDGE,"E26.6.3");var subQ2=sQuery(id+"F4.wireOp",EDGE,"E26.6.2");var subQ3=sQuery(id+"F3.wireOp",EDGE,"E20.6.3");var subQ4=sQuery(id+"F3.wireOp",EDGE,"E20.6.2");var subQ5=sQuery(id+"F3.wireOp",EDGE,"E20.6.1");var subQ6=makeQuery(id+"F15.opLoft","SWEPT_FACE",FACE,{"disambiguationData":[OSD([subQ5,subQ4,subQ3,sQuery(id+"F4.wireOp",EDGE,"E26.6.1"),subQ2,subQ1])]});var subQ13=makeQuery(id+"F40.opExtrude","CAP_FACE",FACE,{"disambiguationData":[OSD([sQuery(id+"F39.wireOp",EDGE,"E29"),sQuery(id+"F39.wireOp",EDGE,"E30")])],"isStart":false});var subQ19=sQuery(id+"F3.wireOp",EDGE,"E20.7.0");var subQ23=makeQuery(id+"F14.opLoft","CAP_FACE",FACE,{"disambiguationData":[OSD([makeQuery(id+"F3.imprint","IMPRINT",FACE,{"disambiguationData":[TD([[makeQuery(id+"F3.imprint","IMPRINT",EDGE,{"derivedFrom":subQ19}),-1.0]])]})])],"isStart":true});var subQ75=sQuery(id+"F3.wireOp",EDGE,"E18.bottom");var subQ80=makeQuery(id+"F5.opLoft","CAP_FACE",FACE,{"disambiguationData":[OSD([makeQuery(id+"F3.imprint","IMPRINT",FACE,{"disambiguationData":[TD([[makeQuery(id+"F3.imprint","IMPRINT",EDGE,{"derivedFrom":subQ75}),1.0]])]})])],"isStart":true});Q13=makeQuery(id+"F44.opFillet","BLEND_EDGE",EDGE,{"blendedFrom":[makeQuery(id+"F40.boolean.opBoolean","INTERSECT",EDGE,{"derivedFrom":[subQ6,subQ13]}),makeQuery(id+"F40.boolean.opBoolean","SPLIT",FACE,{"disambiguationData":[TD([subQ0])],"derivedFrom":makeQuery(id+"F37.boolean.opBoolean","SPLIT",FACE,{"disambiguationData":[TD([subQ6])],"derivedFrom":makeQuery(id+"F36.boolean.opBoolean","SPLIT",FACE,{"disambiguationData":[TD([subQ23])],"derivedFrom":makeQuery(id+"F35.boolean.opBoolean","SPLIT",FACE,{"disambiguationData":[TD([subQ23])],"derivedFrom":makeQuery(id+"F34.boolean.opBoolean","SPLIT",FACE,{"disambiguationData":[TD([subQ23])],"derivedFrom":makeQuery(id+"F33.boolean.opBoolean","SPLIT",FACE,{"disambiguationData":[TD([subQ23])],"derivedFrom":makeQuery(id+"F32.boolean.opBoolean","SPLIT",FACE,{"disambiguationData":[TD([subQ23])],"derivedFrom":makeQuery(id+"F31.boolean.opBoolean","SPLIT",FACE,{"disambiguationData":[TD([subQ23])],"derivedFrom":makeQuery(id+"F30.boolean.opBoolean","SPLIT",FACE,{"disambiguationData":[TD([subQ80])],"derivedFrom":makeQuery(id+"F29.boolean.opBoolean","SPLIT",FACE,{"disambiguationData":[TD([subQ80])],"derivedFrom":makeQuery(id+"F28.boolean.opBoolean","SPLIT",FACE,{"disambiguationData":[TD([subQ80])],"derivedFrom":makeQuery(id+"F27.boolean.opBoolean","SPLIT",FACE,{"disambiguationData":[TD([subQ80])],"derivedFrom":makeQuery(id+"F26.boolean.opBoolean","SPLIT",FACE,{"disambiguationData":[TD([subQ80])],"derivedFrom":makeQuery(id+"F25.boolean.opBoolean","SPLIT",FACE,{"disambiguationData":[TD([subQ80])],"derivedFrom":makeQuery(id+"F24.boolean.opBoolean","SPLIT",FACE,{"disambiguationData":[TD([subQ80])],"derivedFrom":makeQuery(id+"F1.opRevolve","SWEPT_FACE",FACE,{"disambiguationData":[OSD([sQuery(id+"F0.wireOp",EDGE,"E13")])]})})})})})})})})})})})})})})})})],"blendedInto":[makeQuery(id+"F40.boolean.opBoolean","SPLIT",FACE,{"disambiguationData":[TD([subQ0])],"derivedFrom":makeQuery(id+"F37.boolean.opBoolean","SPLIT",FACE,{"disambiguationData":[TD([subQ6])],"derivedFrom":makeQuery(id+"F36.boolean.opBoolean","SPLIT",FACE,{"disambiguationData":[TD([subQ23])],"derivedFrom":makeQuery(id+"F35.boolean.opBoolean","SPLIT",FACE,{"disambiguationData":[TD([subQ23])],"derivedFrom":makeQuery(id+"F34.boolean.opBoolean","SPLIT",FACE,{"disambiguationData":[TD([subQ23])],"derivedFrom":makeQuery(id+"F33.boolean.opBoolean","SPLIT",FACE,{"disambiguationData":[TD([subQ23])],"derivedFrom":makeQuery(id+"F32.boolean.opBoolean","SPLIT",FACE,{"disambiguationData":[TD([subQ23])],"derivedFrom":makeQuery(id+"F31.boolean.opBoolean","SPLIT",FACE,{"disambiguationData":[TD([subQ23])],"derivedFrom":makeQuery(id+"F30.boolean.opBoolean","SPLIT",FACE,{"disambiguationData":[TD([subQ80])],"derivedFrom":makeQuery(id+"F29.boolean.opBoolean","SPLIT",FACE,{"disambiguationData":[TD([subQ80])],"derivedFrom":makeQuery(id+"F28.boolean.opBoolean","SPLIT",FACE,{"disambiguationData":[TD([subQ80])],"derivedFrom":makeQuery(id+"F27.boolean.opBoolean","SPLIT",FACE,{"disambiguationData":[TD([subQ80])],"derivedFrom":makeQuery(id+"F26.boolean.opBoolean","SPLIT",FACE,{"disambiguationData":[TD([subQ80])],"derivedFrom":makeQuery(id+"F25.boolean.opBoolean","SPLIT",FACE,{"disambiguationData":[TD([subQ80])],"derivedFrom":makeQuery(id+"F24.boolean.opBoolean","SPLIT",FACE,{"disambiguationData":[TD([subQ80])],"derivedFrom":makeQuery(id+"F1.opRevolve","SWEPT_FACE",FACE,{"disambiguationData":[OSD([sQuery(id+"F0.wireOp",EDGE,"E13")])]})})})})})})})})})})})})})})})})]});}
            var Q14;
            {var subQ0=makeQuery(id+"F1.opRevolve","SWEPT_FACE",FACE,{"disambiguationData":[OSD([sQuery(id+"F0.wireOp",EDGE,"E10")])]});var subQ7=sQuery(id+"F4.wireOp",EDGE,"E26.5.3");var subQ8=sQuery(id+"F4.wireOp",EDGE,"E26.5.2");var subQ9=sQuery(id+"F3.wireOp",EDGE,"E20.5.3");var subQ10=sQuery(id+"F3.wireOp",EDGE,"E20.5.2");var subQ11=sQuery(id+"F3.wireOp",EDGE,"E20.5.1");var subQ12=makeQuery(id+"F16.opLoft","SWEPT_FACE",FACE,{"disambiguationData":[OSD([subQ11,subQ10,subQ9,sQuery(id+"F4.wireOp",EDGE,"E26.5.1"),subQ8,subQ7])]});var subQ13=makeQuery(id+"F40.opExtrude","CAP_FACE",FACE,{"disambiguationData":[OSD([sQuery(id+"F39.wireOp",EDGE,"E29"),sQuery(id+"F39.wireOp",EDGE,"E30")])],"isStart":false});var subQ26=sQuery(id+"F3.wireOp",EDGE,"E20.7.0");var subQ30=makeQuery(id+"F14.opLoft","CAP_FACE",FACE,{"disambiguationData":[OSD([makeQuery(id+"F3.imprint","IMPRINT",FACE,{"disambiguationData":[TD([[makeQuery(id+"F3.imprint","IMPRINT",EDGE,{"derivedFrom":subQ26}),-1.0]])]})])],"isStart":true});var subQ75=sQuery(id+"F3.wireOp",EDGE,"E18.bottom");var subQ80=makeQuery(id+"F5.opLoft","CAP_FACE",FACE,{"disambiguationData":[OSD([makeQuery(id+"F3.imprint","IMPRINT",FACE,{"disambiguationData":[TD([[makeQuery(id+"F3.imprint","IMPRINT",EDGE,{"derivedFrom":subQ75}),1.0]])]})])],"isStart":true});Q14=makeQuery(id+"F44.opFillet","BLEND_EDGE",EDGE,{"blendedFrom":[makeQuery(id+"F40.boolean.opBoolean","INTERSECT",EDGE,{"derivedFrom":[subQ12,subQ13]}),makeQuery(id+"F40.boolean.opBoolean","SPLIT",FACE,{"disambiguationData":[TD([subQ0])],"derivedFrom":makeQuery(id+"F36.boolean.opBoolean","SPLIT",FACE,{"disambiguationData":[TD([subQ12])],"derivedFrom":makeQuery(id+"F35.boolean.opBoolean","SPLIT",FACE,{"disambiguationData":[TD([subQ30])],"derivedFrom":makeQuery(id+"F34.boolean.opBoolean","SPLIT",FACE,{"disambiguationData":[TD([subQ30])],"derivedFrom":makeQuery(id+"F33.boolean.opBoolean","SPLIT",FACE,{"disambiguationData":[TD([subQ30])],"derivedFrom":makeQuery(id+"F32.boolean.opBoolean","SPLIT",FACE,{"disambiguationData":[TD([subQ30])],"derivedFrom":makeQuery(id+"F31.boolean.opBoolean","SPLIT",FACE,{"disambiguationData":[TD([subQ30])],"derivedFrom":makeQuery(id+"F30.boolean.opBoolean","SPLIT",FACE,{"disambiguationData":[TD([subQ80])],"derivedFrom":makeQuery(id+"F29.boolean.opBoolean","SPLIT",FACE,{"disambiguationData":[TD([subQ80])],"derivedFrom":makeQuery(id+"F28.boolean.opBoolean","SPLIT",FACE,{"disambiguationData":[TD([subQ80])],"derivedFrom":makeQuery(id+"F27.boolean.opBoolean","SPLIT",FACE,{"disambiguationData":[TD([subQ80])],"derivedFrom":makeQuery(id+"F26.boolean.opBoolean","SPLIT",FACE,{"disambiguationData":[TD([subQ80])],"derivedFrom":makeQuery(id+"F25.boolean.opBoolean","SPLIT",FACE,{"disambiguationData":[TD([subQ80])],"derivedFrom":makeQuery(id+"F24.boolean.opBoolean","SPLIT",FACE,{"disambiguationData":[TD([subQ80])],"derivedFrom":makeQuery(id+"F1.opRevolve","SWEPT_FACE",FACE,{"disambiguationData":[OSD([sQuery(id+"F0.wireOp",EDGE,"E13")])]})})})})})})})})})})})})})})})],"blendedInto":[makeQuery(id+"F40.boolean.opBoolean","SPLIT",FACE,{"disambiguationData":[TD([subQ0])],"derivedFrom":makeQuery(id+"F36.boolean.opBoolean","SPLIT",FACE,{"disambiguationData":[TD([subQ12])],"derivedFrom":makeQuery(id+"F35.boolean.opBoolean","SPLIT",FACE,{"disambiguationData":[TD([subQ30])],"derivedFrom":makeQuery(id+"F34.boolean.opBoolean","SPLIT",FACE,{"disambiguationData":[TD([subQ30])],"derivedFrom":makeQuery(id+"F33.boolean.opBoolean","SPLIT",FACE,{"disambiguationData":[TD([subQ30])],"derivedFrom":makeQuery(id+"F32.boolean.opBoolean","SPLIT",FACE,{"disambiguationData":[TD([subQ30])],"derivedFrom":makeQuery(id+"F31.boolean.opBoolean","SPLIT",FACE,{"disambiguationData":[TD([subQ30])],"derivedFrom":makeQuery(id+"F30.boolean.opBoolean","SPLIT",FACE,{"disambiguationData":[TD([subQ80])],"derivedFrom":makeQuery(id+"F29.boolean.opBoolean","SPLIT",FACE,{"disambiguationData":[TD([subQ80])],"derivedFrom":makeQuery(id+"F28.boolean.opBoolean","SPLIT",FACE,{"disambiguationData":[TD([subQ80])],"derivedFrom":makeQuery(id+"F27.boolean.opBoolean","SPLIT",FACE,{"disambiguationData":[TD([subQ80])],"derivedFrom":makeQuery(id+"F26.boolean.opBoolean","SPLIT",FACE,{"disambiguationData":[TD([subQ80])],"derivedFrom":makeQuery(id+"F25.boolean.opBoolean","SPLIT",FACE,{"disambiguationData":[TD([subQ80])],"derivedFrom":makeQuery(id+"F24.boolean.opBoolean","SPLIT",FACE,{"disambiguationData":[TD([subQ80])],"derivedFrom":makeQuery(id+"F1.opRevolve","SWEPT_FACE",FACE,{"disambiguationData":[OSD([sQuery(id+"F0.wireOp",EDGE,"E13")])]})})})})})})})})})})})})})})})]});}
            var Q15;
            {var subQ0=makeQuery(id+"F1.opRevolve","SWEPT_FACE",FACE,{"disambiguationData":[OSD([sQuery(id+"F0.wireOp",EDGE,"E10")])]});var subQ1=sQuery(id+"F4.wireOp",EDGE,"E26.7.3");var subQ2=sQuery(id+"F4.wireOp",EDGE,"E26.7.2");var subQ3=sQuery(id+"F3.wireOp",EDGE,"E20.7.3");var subQ4=sQuery(id+"F3.wireOp",EDGE,"E20.7.2");var subQ5=sQuery(id+"F3.wireOp",EDGE,"E20.7.1");var subQ6=makeQuery(id+"F14.opLoft","SWEPT_FACE",FACE,{"disambiguationData":[OSD([subQ5,subQ4,subQ3,sQuery(id+"F4.wireOp",EDGE,"E26.7.1"),subQ2,subQ1])]});var subQ13=makeQuery(id+"F40.opExtrude","CAP_FACE",FACE,{"disambiguationData":[OSD([sQuery(id+"F39.wireOp",EDGE,"E29"),sQuery(id+"F39.wireOp",EDGE,"E30")])],"isStart":false});var subQ20=sQuery(id+"F3.wireOp",EDGE,"E20.7.0");var subQ22=makeQuery(id+"F14.opLoft","CAP_FACE",FACE,{"disambiguationData":[OSD([makeQuery(id+"F3.imprint","IMPRINT",FACE,{"disambiguationData":[TD([[makeQuery(id+"F3.imprint","IMPRINT",EDGE,{"derivedFrom":subQ20}),-1.0]])]})])],"isStart":true});var subQ75=sQuery(id+"F3.wireOp",EDGE,"E18.bottom");var subQ80=makeQuery(id+"F5.opLoft","CAP_FACE",FACE,{"disambiguationData":[OSD([makeQuery(id+"F3.imprint","IMPRINT",FACE,{"disambiguationData":[TD([[makeQuery(id+"F3.imprint","IMPRINT",EDGE,{"derivedFrom":subQ75}),1.0]])]})])],"isStart":true});Q15=makeQuery(id+"F44.opFillet","BLEND_EDGE",EDGE,{"blendedFrom":[makeQuery(id+"F40.boolean.opBoolean","INTERSECT",EDGE,{"derivedFrom":[subQ6,subQ13]}),makeQuery(id+"F40.boolean.opBoolean","SPLIT",FACE,{"disambiguationData":[TD([subQ0])],"derivedFrom":makeQuery(id+"F38.boolean.opBoolean","SPLIT",FACE,{"disambiguationData":[TD([subQ6])],"derivedFrom":makeQuery(id+"F37.boolean.opBoolean","SPLIT",FACE,{"disambiguationData":[TD([subQ22])],"derivedFrom":makeQuery(id+"F36.boolean.opBoolean","SPLIT",FACE,{"disambiguationData":[TD([subQ22])],"derivedFrom":makeQuery(id+"F35.boolean.opBoolean","SPLIT",FACE,{"disambiguationData":[TD([subQ22])],"derivedFrom":makeQuery(id+"F34.boolean.opBoolean","SPLIT",FACE,{"disambiguationData":[TD([subQ22])],"derivedFrom":makeQuery(id+"F33.boolean.opBoolean","SPLIT",FACE,{"disambiguationData":[TD([subQ22])],"derivedFrom":makeQuery(id+"F32.boolean.opBoolean","SPLIT",FACE,{"disambiguationData":[TD([subQ22])],"derivedFrom":makeQuery(id+"F31.boolean.opBoolean","SPLIT",FACE,{"disambiguationData":[TD([subQ22])],"derivedFrom":makeQuery(id+"F30.boolean.opBoolean","SPLIT",FACE,{"disambiguationData":[TD([subQ80])],"derivedFrom":makeQuery(id+"F29.boolean.opBoolean","SPLIT",FACE,{"disambiguationData":[TD([subQ80])],"derivedFrom":makeQuery(id+"F28.boolean.opBoolean","SPLIT",FACE,{"disambiguationData":[TD([subQ80])],"derivedFrom":makeQuery(id+"F27.boolean.opBoolean","SPLIT",FACE,{"disambiguationData":[TD([subQ80])],"derivedFrom":makeQuery(id+"F26.boolean.opBoolean","SPLIT",FACE,{"disambiguationData":[TD([subQ80])],"derivedFrom":makeQuery(id+"F25.boolean.opBoolean","SPLIT",FACE,{"disambiguationData":[TD([subQ80])],"derivedFrom":makeQuery(id+"F24.boolean.opBoolean","SPLIT",FACE,{"disambiguationData":[TD([subQ80])],"derivedFrom":makeQuery(id+"F1.opRevolve","SWEPT_FACE",FACE,{"disambiguationData":[OSD([sQuery(id+"F0.wireOp",EDGE,"E13")])]})})})})})})})})})})})})})})})})})],"blendedInto":[makeQuery(id+"F40.boolean.opBoolean","SPLIT",FACE,{"disambiguationData":[TD([subQ0])],"derivedFrom":makeQuery(id+"F38.boolean.opBoolean","SPLIT",FACE,{"disambiguationData":[TD([subQ6])],"derivedFrom":makeQuery(id+"F37.boolean.opBoolean","SPLIT",FACE,{"disambiguationData":[TD([subQ22])],"derivedFrom":makeQuery(id+"F36.boolean.opBoolean","SPLIT",FACE,{"disambiguationData":[TD([subQ22])],"derivedFrom":makeQuery(id+"F35.boolean.opBoolean","SPLIT",FACE,{"disambiguationData":[TD([subQ22])],"derivedFrom":makeQuery(id+"F34.boolean.opBoolean","SPLIT",FACE,{"disambiguationData":[TD([subQ22])],"derivedFrom":makeQuery(id+"F33.boolean.opBoolean","SPLIT",FACE,{"disambiguationData":[TD([subQ22])],"derivedFrom":makeQuery(id+"F32.boolean.opBoolean","SPLIT",FACE,{"disambiguationData":[TD([subQ22])],"derivedFrom":makeQuery(id+"F31.boolean.opBoolean","SPLIT",FACE,{"disambiguationData":[TD([subQ22])],"derivedFrom":makeQuery(id+"F30.boolean.opBoolean","SPLIT",FACE,{"disambiguationData":[TD([subQ80])],"derivedFrom":makeQuery(id+"F29.boolean.opBoolean","SPLIT",FACE,{"disambiguationData":[TD([subQ80])],"derivedFrom":makeQuery(id+"F28.boolean.opBoolean","SPLIT",FACE,{"disambiguationData":[TD([subQ80])],"derivedFrom":makeQuery(id+"F27.boolean.opBoolean","SPLIT",FACE,{"disambiguationData":[TD([subQ80])],"derivedFrom":makeQuery(id+"F26.boolean.opBoolean","SPLIT",FACE,{"disambiguationData":[TD([subQ80])],"derivedFrom":makeQuery(id+"F25.boolean.opBoolean","SPLIT",FACE,{"disambiguationData":[TD([subQ80])],"derivedFrom":makeQuery(id+"F24.boolean.opBoolean","SPLIT",FACE,{"disambiguationData":[TD([subQ80])],"derivedFrom":makeQuery(id+"F1.opRevolve","SWEPT_FACE",FACE,{"disambiguationData":[OSD([sQuery(id+"F0.wireOp",EDGE,"E13")])]})})})})})})})})})})})})})})})})})]});}
            var Q16;
            {var subQ0=makeQuery(id+"F1.opRevolve","SWEPT_FACE",FACE,{"disambiguationData":[OSD([sQuery(id+"F0.wireOp",EDGE,"E10")])]});var subQ1=sQuery(id+"F3.wireOp",EDGE,"E20.8.3");var subQ2=sQuery(id+"F3.wireOp",EDGE,"E20.8.2");var subQ3=sQuery(id+"F3.wireOp",EDGE,"E20.8.1");var subQ4=makeQuery(id+"F13.opLoft","SWEPT_FACE",FACE,{"disambiguationData":[OSD([subQ3,subQ2,subQ1,sQuery(id+"F4.wireOp",EDGE,"E26.8.1"),sQuery(id+"F4.wireOp",EDGE,"E26.8.2"),sQuery(id+"F4.wireOp",EDGE,"E26.8.3")])]});var subQ5=makeQuery(id+"F40.opExtrude","CAP_FACE",FACE,{"disambiguationData":[OSD([sQuery(id+"F39.wireOp",EDGE,"E29"),sQuery(id+"F39.wireOp",EDGE,"E30")])],"isStart":false});var subQ10=sQuery(id+"F3.wireOp",EDGE,"E20.7.0");var subQ16=makeQuery(id+"F14.opLoft","CAP_FACE",FACE,{"disambiguationData":[OSD([makeQuery(id+"F3.imprint","IMPRINT",FACE,{"disambiguationData":[TD([[makeQuery(id+"F3.imprint","IMPRINT",EDGE,{"derivedFrom":subQ10}),-1.0]])]})])],"isStart":true});var subQ74=sQuery(id+"F3.wireOp",EDGE,"E18.bottom");var subQ79=makeQuery(id+"F5.opLoft","CAP_FACE",FACE,{"disambiguationData":[OSD([makeQuery(id+"F3.imprint","IMPRINT",FACE,{"disambiguationData":[TD([[makeQuery(id+"F3.imprint","IMPRINT",EDGE,{"derivedFrom":subQ74}),1.0]])]})])],"isStart":true});Q16=makeQuery(id+"F44.opFillet","BLEND_EDGE",EDGE,{"blendedFrom":[makeQuery(id+"F40.boolean.opBoolean","INTERSECT",EDGE,{"derivedFrom":[subQ4,subQ5]}),makeQuery(id+"F40.boolean.opBoolean","SPLIT",FACE,{"disambiguationData":[TD([subQ0])],"derivedFrom":makeQuery(id+"F38.boolean.opBoolean","SPLIT",FACE,{"disambiguationData":[TD([subQ4])],"derivedFrom":makeQuery(id+"F37.boolean.opBoolean","SPLIT",FACE,{"disambiguationData":[TD([subQ16])],"derivedFrom":makeQuery(id+"F36.boolean.opBoolean","SPLIT",FACE,{"disambiguationData":[TD([subQ16])],"derivedFrom":makeQuery(id+"F35.boolean.opBoolean","SPLIT",FACE,{"disambiguationData":[TD([subQ16])],"derivedFrom":makeQuery(id+"F34.boolean.opBoolean","SPLIT",FACE,{"disambiguationData":[TD([subQ16])],"derivedFrom":makeQuery(id+"F33.boolean.opBoolean","SPLIT",FACE,{"disambiguationData":[TD([subQ16])],"derivedFrom":makeQuery(id+"F32.boolean.opBoolean","SPLIT",FACE,{"disambiguationData":[TD([subQ16])],"derivedFrom":makeQuery(id+"F31.boolean.opBoolean","SPLIT",FACE,{"disambiguationData":[TD([subQ16])],"derivedFrom":makeQuery(id+"F30.boolean.opBoolean","SPLIT",FACE,{"disambiguationData":[TD([subQ79])],"derivedFrom":makeQuery(id+"F29.boolean.opBoolean","SPLIT",FACE,{"disambiguationData":[TD([subQ79])],"derivedFrom":makeQuery(id+"F28.boolean.opBoolean","SPLIT",FACE,{"disambiguationData":[TD([subQ79])],"derivedFrom":makeQuery(id+"F27.boolean.opBoolean","SPLIT",FACE,{"disambiguationData":[TD([subQ79])],"derivedFrom":makeQuery(id+"F26.boolean.opBoolean","SPLIT",FACE,{"disambiguationData":[TD([subQ79])],"derivedFrom":makeQuery(id+"F25.boolean.opBoolean","SPLIT",FACE,{"disambiguationData":[TD([subQ79])],"derivedFrom":makeQuery(id+"F24.boolean.opBoolean","SPLIT",FACE,{"disambiguationData":[TD([subQ79])],"derivedFrom":makeQuery(id+"F1.opRevolve","SWEPT_FACE",FACE,{"disambiguationData":[OSD([sQuery(id+"F0.wireOp",EDGE,"E13")])]})})})})})})})})})})})})})})})})})],"blendedInto":[makeQuery(id+"F40.boolean.opBoolean","SPLIT",FACE,{"disambiguationData":[TD([subQ0])],"derivedFrom":makeQuery(id+"F38.boolean.opBoolean","SPLIT",FACE,{"disambiguationData":[TD([subQ4])],"derivedFrom":makeQuery(id+"F37.boolean.opBoolean","SPLIT",FACE,{"disambiguationData":[TD([subQ16])],"derivedFrom":makeQuery(id+"F36.boolean.opBoolean","SPLIT",FACE,{"disambiguationData":[TD([subQ16])],"derivedFrom":makeQuery(id+"F35.boolean.opBoolean","SPLIT",FACE,{"disambiguationData":[TD([subQ16])],"derivedFrom":makeQuery(id+"F34.boolean.opBoolean","SPLIT",FACE,{"disambiguationData":[TD([subQ16])],"derivedFrom":makeQuery(id+"F33.boolean.opBoolean","SPLIT",FACE,{"disambiguationData":[TD([subQ16])],"derivedFrom":makeQuery(id+"F32.boolean.opBoolean","SPLIT",FACE,{"disambiguationData":[TD([subQ16])],"derivedFrom":makeQuery(id+"F31.boolean.opBoolean","SPLIT",FACE,{"disambiguationData":[TD([subQ16])],"derivedFrom":makeQuery(id+"F30.boolean.opBoolean","SPLIT",FACE,{"disambiguationData":[TD([subQ79])],"derivedFrom":makeQuery(id+"F29.boolean.opBoolean","SPLIT",FACE,{"disambiguationData":[TD([subQ79])],"derivedFrom":makeQuery(id+"F28.boolean.opBoolean","SPLIT",FACE,{"disambiguationData":[TD([subQ79])],"derivedFrom":makeQuery(id+"F27.boolean.opBoolean","SPLIT",FACE,{"disambiguationData":[TD([subQ79])],"derivedFrom":makeQuery(id+"F26.boolean.opBoolean","SPLIT",FACE,{"disambiguationData":[TD([subQ79])],"derivedFrom":makeQuery(id+"F25.boolean.opBoolean","SPLIT",FACE,{"disambiguationData":[TD([subQ79])],"derivedFrom":makeQuery(id+"F24.boolean.opBoolean","SPLIT",FACE,{"disambiguationData":[TD([subQ79])],"derivedFrom":makeQuery(id+"F1.opRevolve","SWEPT_FACE",FACE,{"disambiguationData":[OSD([sQuery(id+"F0.wireOp",EDGE,"E13")])]})})})})})})})})})})})})})})})})})]});}
            var Q17;
            {var subQ0=makeQuery(id+"F1.opRevolve","SWEPT_FACE",FACE,{"disambiguationData":[OSD([sQuery(id+"F0.wireOp",EDGE,"E12")])]});var subQ1=sQuery(id+"F3.wireOp",EDGE,"E20.8.3");var subQ2=sQuery(id+"F3.wireOp",EDGE,"E20.8.2");var subQ3=sQuery(id+"F3.wireOp",EDGE,"E20.8.1");var subQ4=makeQuery(id+"F23.opLoft","SWEPT_FACE",FACE,{"disambiguationData":[OSD([subQ3,subQ2,subQ1,sQuery(id+"F22.wireOp",EDGE,"E27.bottom"),sQuery(id+"F22.wireOp",EDGE,"E27.top"),sQuery(id+"F22.wireOp",EDGE,"E27.left")])]});var subQ7=sQuery(id+"F3.wireOp",EDGE,"E20.7.0");var subQ9=makeQuery(id+"F40.opExtrude","CAP_FACE",FACE,{"disambiguationData":[OSD([sQuery(id+"F39.wireOp",EDGE,"E29"),sQuery(id+"F39.wireOp",EDGE,"E30")])],"isStart":true});var subQ10=makeQuery(id+"F13.opLoft","SWEPT_FACE",FACE,{"disambiguationData":[OSD([subQ3,subQ2,subQ1,sQuery(id+"F4.wireOp",EDGE,"E26.8.1"),sQuery(id+"F4.wireOp",EDGE,"E26.8.2"),sQuery(id+"F4.wireOp",EDGE,"E26.8.3")])]});var subQ17=makeQuery(id+"F14.opLoft","CAP_FACE",FACE,{"disambiguationData":[OSD([makeQuery(id+"F3.imprint","IMPRINT",FACE,{"disambiguationData":[TD([[makeQuery(id+"F3.imprint","IMPRINT",EDGE,{"derivedFrom":subQ7}),-1.0]])]})])],"isStart":true});var subQ75=sQuery(id+"F3.wireOp",EDGE,"E18.bottom");var subQ80=makeQuery(id+"F5.opLoft","CAP_FACE",FACE,{"disambiguationData":[OSD([makeQuery(id+"F3.imprint","IMPRINT",FACE,{"disambiguationData":[TD([[makeQuery(id+"F3.imprint","IMPRINT",EDGE,{"derivedFrom":subQ75}),1.0]])]})])],"isStart":true});Q17=makeQuery(id+"F44.opFillet","BLEND_EDGE",EDGE,{"blendedFrom":[makeQuery(id+"F40.boolean.opBoolean","INTERSECT",EDGE,{"derivedFrom":[subQ4,subQ9]}),makeQuery(id+"F40.boolean.opBoolean","SPLIT",FACE,{"disambiguationData":[TD([subQ0])],"derivedFrom":makeQuery(id+"F38.boolean.opBoolean","SPLIT",FACE,{"disambiguationData":[TD([subQ10])],"derivedFrom":makeQuery(id+"F37.boolean.opBoolean","SPLIT",FACE,{"disambiguationData":[TD([subQ17])],"derivedFrom":makeQuery(id+"F36.boolean.opBoolean","SPLIT",FACE,{"disambiguationData":[TD([subQ17])],"derivedFrom":makeQuery(id+"F35.boolean.opBoolean","SPLIT",FACE,{"disambiguationData":[TD([subQ17])],"derivedFrom":makeQuery(id+"F34.boolean.opBoolean","SPLIT",FACE,{"disambiguationData":[TD([subQ17])],"derivedFrom":makeQuery(id+"F33.boolean.opBoolean","SPLIT",FACE,{"disambiguationData":[TD([subQ17])],"derivedFrom":makeQuery(id+"F32.boolean.opBoolean","SPLIT",FACE,{"disambiguationData":[TD([subQ17])],"derivedFrom":makeQuery(id+"F31.boolean.opBoolean","SPLIT",FACE,{"disambiguationData":[TD([subQ17])],"derivedFrom":makeQuery(id+"F30.boolean.opBoolean","SPLIT",FACE,{"disambiguationData":[TD([subQ80])],"derivedFrom":makeQuery(id+"F29.boolean.opBoolean","SPLIT",FACE,{"disambiguationData":[TD([subQ80])],"derivedFrom":makeQuery(id+"F28.boolean.opBoolean","SPLIT",FACE,{"disambiguationData":[TD([subQ80])],"derivedFrom":makeQuery(id+"F27.boolean.opBoolean","SPLIT",FACE,{"disambiguationData":[TD([subQ80])],"derivedFrom":makeQuery(id+"F26.boolean.opBoolean","SPLIT",FACE,{"disambiguationData":[TD([subQ80])],"derivedFrom":makeQuery(id+"F25.boolean.opBoolean","SPLIT",FACE,{"disambiguationData":[TD([subQ80])],"derivedFrom":makeQuery(id+"F24.boolean.opBoolean","SPLIT",FACE,{"disambiguationData":[TD([subQ80])],"derivedFrom":makeQuery(id+"F1.opRevolve","SWEPT_FACE",FACE,{"disambiguationData":[OSD([sQuery(id+"F0.wireOp",EDGE,"E13")])]})})})})})})})})})})})})})})})})})],"blendedInto":[makeQuery(id+"F40.boolean.opBoolean","SPLIT",FACE,{"disambiguationData":[TD([subQ0])],"derivedFrom":makeQuery(id+"F38.boolean.opBoolean","SPLIT",FACE,{"disambiguationData":[TD([subQ10])],"derivedFrom":makeQuery(id+"F37.boolean.opBoolean","SPLIT",FACE,{"disambiguationData":[TD([subQ17])],"derivedFrom":makeQuery(id+"F36.boolean.opBoolean","SPLIT",FACE,{"disambiguationData":[TD([subQ17])],"derivedFrom":makeQuery(id+"F35.boolean.opBoolean","SPLIT",FACE,{"disambiguationData":[TD([subQ17])],"derivedFrom":makeQuery(id+"F34.boolean.opBoolean","SPLIT",FACE,{"disambiguationData":[TD([subQ17])],"derivedFrom":makeQuery(id+"F33.boolean.opBoolean","SPLIT",FACE,{"disambiguationData":[TD([subQ17])],"derivedFrom":makeQuery(id+"F32.boolean.opBoolean","SPLIT",FACE,{"disambiguationData":[TD([subQ17])],"derivedFrom":makeQuery(id+"F31.boolean.opBoolean","SPLIT",FACE,{"disambiguationData":[TD([subQ17])],"derivedFrom":makeQuery(id+"F30.boolean.opBoolean","SPLIT",FACE,{"disambiguationData":[TD([subQ80])],"derivedFrom":makeQuery(id+"F29.boolean.opBoolean","SPLIT",FACE,{"disambiguationData":[TD([subQ80])],"derivedFrom":makeQuery(id+"F28.boolean.opBoolean","SPLIT",FACE,{"disambiguationData":[TD([subQ80])],"derivedFrom":makeQuery(id+"F27.boolean.opBoolean","SPLIT",FACE,{"disambiguationData":[TD([subQ80])],"derivedFrom":makeQuery(id+"F26.boolean.opBoolean","SPLIT",FACE,{"disambiguationData":[TD([subQ80])],"derivedFrom":makeQuery(id+"F25.boolean.opBoolean","SPLIT",FACE,{"disambiguationData":[TD([subQ80])],"derivedFrom":makeQuery(id+"F24.boolean.opBoolean","SPLIT",FACE,{"disambiguationData":[TD([subQ80])],"derivedFrom":makeQuery(id+"F1.opRevolve","SWEPT_FACE",FACE,{"disambiguationData":[OSD([sQuery(id+"F0.wireOp",EDGE,"E13")])]})})})})})})})})})})})})})})})})})]});}
            var Q18;
            {var subQ0=makeQuery(id+"F1.opRevolve","SWEPT_FACE",FACE,{"disambiguationData":[OSD([sQuery(id+"F0.wireOp",EDGE,"E12")])]});var subQ5=sQuery(id+"F3.wireOp",EDGE,"E20.7.3");var subQ6=sQuery(id+"F3.wireOp",EDGE,"E20.7.2");var subQ7=sQuery(id+"F3.wireOp",EDGE,"E20.7.1");var subQ8=makeQuery(id+"F38.opLoft","SWEPT_FACE",FACE,{"disambiguationData":[OSD([subQ7,subQ6,subQ5,sQuery(id+"F22.wireOp",EDGE,"E28.15.0"),sQuery(id+"F22.wireOp",EDGE,"E28.15.2"),sQuery(id+"F22.wireOp",EDGE,"E28.15.3")])]});var subQ9=makeQuery(id+"F40.opExtrude","CAP_FACE",FACE,{"disambiguationData":[OSD([sQuery(id+"F39.wireOp",EDGE,"E29"),sQuery(id+"F39.wireOp",EDGE,"E30")])],"isStart":true});var subQ13=sQuery(id+"F4.wireOp",EDGE,"E26.7.3");var subQ14=sQuery(id+"F4.wireOp",EDGE,"E26.7.2");var subQ15=makeQuery(id+"F14.opLoft","SWEPT_FACE",FACE,{"disambiguationData":[OSD([subQ7,subQ6,subQ5,sQuery(id+"F4.wireOp",EDGE,"E26.7.1"),subQ14,subQ13])]});var subQ21=sQuery(id+"F3.wireOp",EDGE,"E20.7.0");var subQ23=makeQuery(id+"F14.opLoft","CAP_FACE",FACE,{"disambiguationData":[OSD([makeQuery(id+"F3.imprint","IMPRINT",FACE,{"disambiguationData":[TD([[makeQuery(id+"F3.imprint","IMPRINT",EDGE,{"derivedFrom":subQ21}),-1.0]])]})])],"isStart":true});var subQ76=sQuery(id+"F3.wireOp",EDGE,"E18.bottom");var subQ81=makeQuery(id+"F5.opLoft","CAP_FACE",FACE,{"disambiguationData":[OSD([makeQuery(id+"F3.imprint","IMPRINT",FACE,{"disambiguationData":[TD([[makeQuery(id+"F3.imprint","IMPRINT",EDGE,{"derivedFrom":subQ76}),1.0]])]})])],"isStart":true});Q18=makeQuery(id+"F44.opFillet","BLEND_EDGE",EDGE,{"blendedFrom":[makeQuery(id+"F40.boolean.opBoolean","INTERSECT",EDGE,{"derivedFrom":[subQ8,subQ9]}),makeQuery(id+"F40.boolean.opBoolean","SPLIT",FACE,{"disambiguationData":[TD([subQ0])],"derivedFrom":makeQuery(id+"F38.boolean.opBoolean","SPLIT",FACE,{"disambiguationData":[TD([subQ15])],"derivedFrom":makeQuery(id+"F37.boolean.opBoolean","SPLIT",FACE,{"disambiguationData":[TD([subQ23])],"derivedFrom":makeQuery(id+"F36.boolean.opBoolean","SPLIT",FACE,{"disambiguationData":[TD([subQ23])],"derivedFrom":makeQuery(id+"F35.boolean.opBoolean","SPLIT",FACE,{"disambiguationData":[TD([subQ23])],"derivedFrom":makeQuery(id+"F34.boolean.opBoolean","SPLIT",FACE,{"disambiguationData":[TD([subQ23])],"derivedFrom":makeQuery(id+"F33.boolean.opBoolean","SPLIT",FACE,{"disambiguationData":[TD([subQ23])],"derivedFrom":makeQuery(id+"F32.boolean.opBoolean","SPLIT",FACE,{"disambiguationData":[TD([subQ23])],"derivedFrom":makeQuery(id+"F31.boolean.opBoolean","SPLIT",FACE,{"disambiguationData":[TD([subQ23])],"derivedFrom":makeQuery(id+"F30.boolean.opBoolean","SPLIT",FACE,{"disambiguationData":[TD([subQ81])],"derivedFrom":makeQuery(id+"F29.boolean.opBoolean","SPLIT",FACE,{"disambiguationData":[TD([subQ81])],"derivedFrom":makeQuery(id+"F28.boolean.opBoolean","SPLIT",FACE,{"disambiguationData":[TD([subQ81])],"derivedFrom":makeQuery(id+"F27.boolean.opBoolean","SPLIT",FACE,{"disambiguationData":[TD([subQ81])],"derivedFrom":makeQuery(id+"F26.boolean.opBoolean","SPLIT",FACE,{"disambiguationData":[TD([subQ81])],"derivedFrom":makeQuery(id+"F25.boolean.opBoolean","SPLIT",FACE,{"disambiguationData":[TD([subQ81])],"derivedFrom":makeQuery(id+"F24.boolean.opBoolean","SPLIT",FACE,{"disambiguationData":[TD([subQ81])],"derivedFrom":makeQuery(id+"F1.opRevolve","SWEPT_FACE",FACE,{"disambiguationData":[OSD([sQuery(id+"F0.wireOp",EDGE,"E13")])]})})})})})})})})})})})})})})})})})],"blendedInto":[makeQuery(id+"F40.boolean.opBoolean","SPLIT",FACE,{"disambiguationData":[TD([subQ0])],"derivedFrom":makeQuery(id+"F38.boolean.opBoolean","SPLIT",FACE,{"disambiguationData":[TD([subQ15])],"derivedFrom":makeQuery(id+"F37.boolean.opBoolean","SPLIT",FACE,{"disambiguationData":[TD([subQ23])],"derivedFrom":makeQuery(id+"F36.boolean.opBoolean","SPLIT",FACE,{"disambiguationData":[TD([subQ23])],"derivedFrom":makeQuery(id+"F35.boolean.opBoolean","SPLIT",FACE,{"disambiguationData":[TD([subQ23])],"derivedFrom":makeQuery(id+"F34.boolean.opBoolean","SPLIT",FACE,{"disambiguationData":[TD([subQ23])],"derivedFrom":makeQuery(id+"F33.boolean.opBoolean","SPLIT",FACE,{"disambiguationData":[TD([subQ23])],"derivedFrom":makeQuery(id+"F32.boolean.opBoolean","SPLIT",FACE,{"disambiguationData":[TD([subQ23])],"derivedFrom":makeQuery(id+"F31.boolean.opBoolean","SPLIT",FACE,{"disambiguationData":[TD([subQ23])],"derivedFrom":makeQuery(id+"F30.boolean.opBoolean","SPLIT",FACE,{"disambiguationData":[TD([subQ81])],"derivedFrom":makeQuery(id+"F29.boolean.opBoolean","SPLIT",FACE,{"disambiguationData":[TD([subQ81])],"derivedFrom":makeQuery(id+"F28.boolean.opBoolean","SPLIT",FACE,{"disambiguationData":[TD([subQ81])],"derivedFrom":makeQuery(id+"F27.boolean.opBoolean","SPLIT",FACE,{"disambiguationData":[TD([subQ81])],"derivedFrom":makeQuery(id+"F26.boolean.opBoolean","SPLIT",FACE,{"disambiguationData":[TD([subQ81])],"derivedFrom":makeQuery(id+"F25.boolean.opBoolean","SPLIT",FACE,{"disambiguationData":[TD([subQ81])],"derivedFrom":makeQuery(id+"F24.boolean.opBoolean","SPLIT",FACE,{"disambiguationData":[TD([subQ81])],"derivedFrom":makeQuery(id+"F1.opRevolve","SWEPT_FACE",FACE,{"disambiguationData":[OSD([sQuery(id+"F0.wireOp",EDGE,"E13")])]})})})})})})})})})})})})})})})})})]});}
            var Q19;
            {var subQ0=makeQuery(id+"F1.opRevolve","SWEPT_FACE",FACE,{"disambiguationData":[OSD([sQuery(id+"F0.wireOp",EDGE,"E12")])]});var subQ5=sQuery(id+"F3.wireOp",EDGE,"E20.6.3");var subQ6=sQuery(id+"F3.wireOp",EDGE,"E20.6.2");var subQ7=sQuery(id+"F3.wireOp",EDGE,"E20.6.1");var subQ8=makeQuery(id+"F37.opLoft","SWEPT_FACE",FACE,{"disambiguationData":[OSD([subQ7,subQ6,subQ5,sQuery(id+"F22.wireOp",EDGE,"E28.14.0"),sQuery(id+"F22.wireOp",EDGE,"E28.14.2"),sQuery(id+"F22.wireOp",EDGE,"E28.14.3")])]});var subQ9=makeQuery(id+"F40.opExtrude","CAP_FACE",FACE,{"disambiguationData":[OSD([sQuery(id+"F39.wireOp",EDGE,"E29"),sQuery(id+"F39.wireOp",EDGE,"E30")])],"isStart":true});var subQ13=sQuery(id+"F4.wireOp",EDGE,"E26.6.3");var subQ14=sQuery(id+"F4.wireOp",EDGE,"E26.6.2");var subQ15=makeQuery(id+"F15.opLoft","SWEPT_FACE",FACE,{"disambiguationData":[OSD([subQ7,subQ6,subQ5,sQuery(id+"F4.wireOp",EDGE,"E26.6.1"),subQ14,subQ13])]});var subQ20=sQuery(id+"F3.wireOp",EDGE,"E20.7.0");var subQ24=makeQuery(id+"F14.opLoft","CAP_FACE",FACE,{"disambiguationData":[OSD([makeQuery(id+"F3.imprint","IMPRINT",FACE,{"disambiguationData":[TD([[makeQuery(id+"F3.imprint","IMPRINT",EDGE,{"derivedFrom":subQ20}),-1.0]])]})])],"isStart":true});var subQ76=sQuery(id+"F3.wireOp",EDGE,"E18.bottom");var subQ81=makeQuery(id+"F5.opLoft","CAP_FACE",FACE,{"disambiguationData":[OSD([makeQuery(id+"F3.imprint","IMPRINT",FACE,{"disambiguationData":[TD([[makeQuery(id+"F3.imprint","IMPRINT",EDGE,{"derivedFrom":subQ76}),1.0]])]})])],"isStart":true});Q19=makeQuery(id+"F44.opFillet","BLEND_EDGE",EDGE,{"blendedFrom":[makeQuery(id+"F40.boolean.opBoolean","INTERSECT",EDGE,{"derivedFrom":[subQ8,subQ9]}),makeQuery(id+"F40.boolean.opBoolean","SPLIT",FACE,{"disambiguationData":[TD([subQ0])],"derivedFrom":makeQuery(id+"F37.boolean.opBoolean","SPLIT",FACE,{"disambiguationData":[TD([subQ15])],"derivedFrom":makeQuery(id+"F36.boolean.opBoolean","SPLIT",FACE,{"disambiguationData":[TD([subQ24])],"derivedFrom":makeQuery(id+"F35.boolean.opBoolean","SPLIT",FACE,{"disambiguationData":[TD([subQ24])],"derivedFrom":makeQuery(id+"F34.boolean.opBoolean","SPLIT",FACE,{"disambiguationData":[TD([subQ24])],"derivedFrom":makeQuery(id+"F33.boolean.opBoolean","SPLIT",FACE,{"disambiguationData":[TD([subQ24])],"derivedFrom":makeQuery(id+"F32.boolean.opBoolean","SPLIT",FACE,{"disambiguationData":[TD([subQ24])],"derivedFrom":makeQuery(id+"F31.boolean.opBoolean","SPLIT",FACE,{"disambiguationData":[TD([subQ24])],"derivedFrom":makeQuery(id+"F30.boolean.opBoolean","SPLIT",FACE,{"disambiguationData":[TD([subQ81])],"derivedFrom":makeQuery(id+"F29.boolean.opBoolean","SPLIT",FACE,{"disambiguationData":[TD([subQ81])],"derivedFrom":makeQuery(id+"F28.boolean.opBoolean","SPLIT",FACE,{"disambiguationData":[TD([subQ81])],"derivedFrom":makeQuery(id+"F27.boolean.opBoolean","SPLIT",FACE,{"disambiguationData":[TD([subQ81])],"derivedFrom":makeQuery(id+"F26.boolean.opBoolean","SPLIT",FACE,{"disambiguationData":[TD([subQ81])],"derivedFrom":makeQuery(id+"F25.boolean.opBoolean","SPLIT",FACE,{"disambiguationData":[TD([subQ81])],"derivedFrom":makeQuery(id+"F24.boolean.opBoolean","SPLIT",FACE,{"disambiguationData":[TD([subQ81])],"derivedFrom":makeQuery(id+"F1.opRevolve","SWEPT_FACE",FACE,{"disambiguationData":[OSD([sQuery(id+"F0.wireOp",EDGE,"E13")])]})})})})})})})})})})})})})})})})],"blendedInto":[makeQuery(id+"F40.boolean.opBoolean","SPLIT",FACE,{"disambiguationData":[TD([subQ0])],"derivedFrom":makeQuery(id+"F37.boolean.opBoolean","SPLIT",FACE,{"disambiguationData":[TD([subQ15])],"derivedFrom":makeQuery(id+"F36.boolean.opBoolean","SPLIT",FACE,{"disambiguationData":[TD([subQ24])],"derivedFrom":makeQuery(id+"F35.boolean.opBoolean","SPLIT",FACE,{"disambiguationData":[TD([subQ24])],"derivedFrom":makeQuery(id+"F34.boolean.opBoolean","SPLIT",FACE,{"disambiguationData":[TD([subQ24])],"derivedFrom":makeQuery(id+"F33.boolean.opBoolean","SPLIT",FACE,{"disambiguationData":[TD([subQ24])],"derivedFrom":makeQuery(id+"F32.boolean.opBoolean","SPLIT",FACE,{"disambiguationData":[TD([subQ24])],"derivedFrom":makeQuery(id+"F31.boolean.opBoolean","SPLIT",FACE,{"disambiguationData":[TD([subQ24])],"derivedFrom":makeQuery(id+"F30.boolean.opBoolean","SPLIT",FACE,{"disambiguationData":[TD([subQ81])],"derivedFrom":makeQuery(id+"F29.boolean.opBoolean","SPLIT",FACE,{"disambiguationData":[TD([subQ81])],"derivedFrom":makeQuery(id+"F28.boolean.opBoolean","SPLIT",FACE,{"disambiguationData":[TD([subQ81])],"derivedFrom":makeQuery(id+"F27.boolean.opBoolean","SPLIT",FACE,{"disambiguationData":[TD([subQ81])],"derivedFrom":makeQuery(id+"F26.boolean.opBoolean","SPLIT",FACE,{"disambiguationData":[TD([subQ81])],"derivedFrom":makeQuery(id+"F25.boolean.opBoolean","SPLIT",FACE,{"disambiguationData":[TD([subQ81])],"derivedFrom":makeQuery(id+"F24.boolean.opBoolean","SPLIT",FACE,{"disambiguationData":[TD([subQ81])],"derivedFrom":makeQuery(id+"F1.opRevolve","SWEPT_FACE",FACE,{"disambiguationData":[OSD([sQuery(id+"F0.wireOp",EDGE,"E13")])]})})})})})})})})})})})})})})})})]});}
            var Q20;
            {var subQ0=makeQuery(id+"F1.opRevolve","SWEPT_FACE",FACE,{"disambiguationData":[OSD([sQuery(id+"F0.wireOp",EDGE,"E12")])]});var subQ1=sQuery(id+"F3.wireOp",EDGE,"E20.5.3");var subQ2=sQuery(id+"F3.wireOp",EDGE,"E20.5.2");var subQ3=sQuery(id+"F3.wireOp",EDGE,"E20.5.1");var subQ4=makeQuery(id+"F36.opLoft","SWEPT_FACE",FACE,{"disambiguationData":[OSD([subQ3,subQ2,subQ1,sQuery(id+"F22.wireOp",EDGE,"E28.13.0"),sQuery(id+"F22.wireOp",EDGE,"E28.13.2"),sQuery(id+"F22.wireOp",EDGE,"E28.13.3")])]});var subQ9=makeQuery(id+"F40.opExtrude","CAP_FACE",FACE,{"disambiguationData":[OSD([sQuery(id+"F39.wireOp",EDGE,"E29"),sQuery(id+"F39.wireOp",EDGE,"E30")])],"isStart":true});var subQ10=sQuery(id+"F4.wireOp",EDGE,"E26.5.3");var subQ11=sQuery(id+"F4.wireOp",EDGE,"E26.5.2");var subQ12=makeQuery(id+"F16.opLoft","SWEPT_FACE",FACE,{"disambiguationData":[OSD([subQ3,subQ2,subQ1,sQuery(id+"F4.wireOp",EDGE,"E26.5.1"),subQ11,subQ10])]});var subQ27=sQuery(id+"F3.wireOp",EDGE,"E20.7.0");var subQ31=makeQuery(id+"F14.opLoft","CAP_FACE",FACE,{"disambiguationData":[OSD([makeQuery(id+"F3.imprint","IMPRINT",FACE,{"disambiguationData":[TD([[makeQuery(id+"F3.imprint","IMPRINT",EDGE,{"derivedFrom":subQ27}),-1.0]])]})])],"isStart":true});var subQ76=sQuery(id+"F3.wireOp",EDGE,"E18.bottom");var subQ81=makeQuery(id+"F5.opLoft","CAP_FACE",FACE,{"disambiguationData":[OSD([makeQuery(id+"F3.imprint","IMPRINT",FACE,{"disambiguationData":[TD([[makeQuery(id+"F3.imprint","IMPRINT",EDGE,{"derivedFrom":subQ76}),1.0]])]})])],"isStart":true});Q20=makeQuery(id+"F44.opFillet","BLEND_EDGE",EDGE,{"blendedFrom":[makeQuery(id+"F40.boolean.opBoolean","INTERSECT",EDGE,{"derivedFrom":[subQ4,subQ9]}),makeQuery(id+"F40.boolean.opBoolean","SPLIT",FACE,{"disambiguationData":[TD([subQ0])],"derivedFrom":makeQuery(id+"F36.boolean.opBoolean","SPLIT",FACE,{"disambiguationData":[TD([subQ12])],"derivedFrom":makeQuery(id+"F35.boolean.opBoolean","SPLIT",FACE,{"disambiguationData":[TD([subQ31])],"derivedFrom":makeQuery(id+"F34.boolean.opBoolean","SPLIT",FACE,{"disambiguationData":[TD([subQ31])],"derivedFrom":makeQuery(id+"F33.boolean.opBoolean","SPLIT",FACE,{"disambiguationData":[TD([subQ31])],"derivedFrom":makeQuery(id+"F32.boolean.opBoolean","SPLIT",FACE,{"disambiguationData":[TD([subQ31])],"derivedFrom":makeQuery(id+"F31.boolean.opBoolean","SPLIT",FACE,{"disambiguationData":[TD([subQ31])],"derivedFrom":makeQuery(id+"F30.boolean.opBoolean","SPLIT",FACE,{"disambiguationData":[TD([subQ81])],"derivedFrom":makeQuery(id+"F29.boolean.opBoolean","SPLIT",FACE,{"disambiguationData":[TD([subQ81])],"derivedFrom":makeQuery(id+"F28.boolean.opBoolean","SPLIT",FACE,{"disambiguationData":[TD([subQ81])],"derivedFrom":makeQuery(id+"F27.boolean.opBoolean","SPLIT",FACE,{"disambiguationData":[TD([subQ81])],"derivedFrom":makeQuery(id+"F26.boolean.opBoolean","SPLIT",FACE,{"disambiguationData":[TD([subQ81])],"derivedFrom":makeQuery(id+"F25.boolean.opBoolean","SPLIT",FACE,{"disambiguationData":[TD([subQ81])],"derivedFrom":makeQuery(id+"F24.boolean.opBoolean","SPLIT",FACE,{"disambiguationData":[TD([subQ81])],"derivedFrom":makeQuery(id+"F1.opRevolve","SWEPT_FACE",FACE,{"disambiguationData":[OSD([sQuery(id+"F0.wireOp",EDGE,"E13")])]})})})})})})})})})})})})})})})],"blendedInto":[makeQuery(id+"F40.boolean.opBoolean","SPLIT",FACE,{"disambiguationData":[TD([subQ0])],"derivedFrom":makeQuery(id+"F36.boolean.opBoolean","SPLIT",FACE,{"disambiguationData":[TD([subQ12])],"derivedFrom":makeQuery(id+"F35.boolean.opBoolean","SPLIT",FACE,{"disambiguationData":[TD([subQ31])],"derivedFrom":makeQuery(id+"F34.boolean.opBoolean","SPLIT",FACE,{"disambiguationData":[TD([subQ31])],"derivedFrom":makeQuery(id+"F33.boolean.opBoolean","SPLIT",FACE,{"disambiguationData":[TD([subQ31])],"derivedFrom":makeQuery(id+"F32.boolean.opBoolean","SPLIT",FACE,{"disambiguationData":[TD([subQ31])],"derivedFrom":makeQuery(id+"F31.boolean.opBoolean","SPLIT",FACE,{"disambiguationData":[TD([subQ31])],"derivedFrom":makeQuery(id+"F30.boolean.opBoolean","SPLIT",FACE,{"disambiguationData":[TD([subQ81])],"derivedFrom":makeQuery(id+"F29.boolean.opBoolean","SPLIT",FACE,{"disambiguationData":[TD([subQ81])],"derivedFrom":makeQuery(id+"F28.boolean.opBoolean","SPLIT",FACE,{"disambiguationData":[TD([subQ81])],"derivedFrom":makeQuery(id+"F27.boolean.opBoolean","SPLIT",FACE,{"disambiguationData":[TD([subQ81])],"derivedFrom":makeQuery(id+"F26.boolean.opBoolean","SPLIT",FACE,{"disambiguationData":[TD([subQ81])],"derivedFrom":makeQuery(id+"F25.boolean.opBoolean","SPLIT",FACE,{"disambiguationData":[TD([subQ81])],"derivedFrom":makeQuery(id+"F24.boolean.opBoolean","SPLIT",FACE,{"disambiguationData":[TD([subQ81])],"derivedFrom":makeQuery(id+"F1.opRevolve","SWEPT_FACE",FACE,{"disambiguationData":[OSD([sQuery(id+"F0.wireOp",EDGE,"E13")])]})})})})})})})})})})})})})})})]});}
            var Q21;
            {var subQ0=makeQuery(id+"F1.opRevolve","SWEPT_FACE",FACE,{"disambiguationData":[OSD([sQuery(id+"F0.wireOp",EDGE,"E12")])]});var subQ5=sQuery(id+"F3.wireOp",EDGE,"E20.4.3");var subQ6=sQuery(id+"F3.wireOp",EDGE,"E20.4.2");var subQ7=sQuery(id+"F3.wireOp",EDGE,"E20.4.1");var subQ8=makeQuery(id+"F35.opLoft","SWEPT_FACE",FACE,{"disambiguationData":[OSD([subQ7,subQ6,subQ5,sQuery(id+"F22.wireOp",EDGE,"E28.12.0"),sQuery(id+"F22.wireOp",EDGE,"E28.12.2"),sQuery(id+"F22.wireOp",EDGE,"E28.12.3")])]});var subQ9=makeQuery(id+"F40.opExtrude","CAP_FACE",FACE,{"disambiguationData":[OSD([sQuery(id+"F39.wireOp",EDGE,"E29"),sQuery(id+"F39.wireOp",EDGE,"E30")])],"isStart":true});var subQ10=sQuery(id+"F4.wireOp",EDGE,"E26.4.3");var subQ11=sQuery(id+"F4.wireOp",EDGE,"E26.4.2");var subQ12=makeQuery(id+"F17.opLoft","SWEPT_FACE",FACE,{"disambiguationData":[OSD([subQ7,subQ6,subQ5,sQuery(id+"F4.wireOp",EDGE,"E26.4.1"),subQ11,subQ10])]});var subQ33=sQuery(id+"F3.wireOp",EDGE,"E20.7.0");var subQ37=makeQuery(id+"F14.opLoft","CAP_FACE",FACE,{"disambiguationData":[OSD([makeQuery(id+"F3.imprint","IMPRINT",FACE,{"disambiguationData":[TD([[makeQuery(id+"F3.imprint","IMPRINT",EDGE,{"derivedFrom":subQ33}),-1.0]])]})])],"isStart":true});var subQ76=sQuery(id+"F3.wireOp",EDGE,"E18.bottom");var subQ81=makeQuery(id+"F5.opLoft","CAP_FACE",FACE,{"disambiguationData":[OSD([makeQuery(id+"F3.imprint","IMPRINT",FACE,{"disambiguationData":[TD([[makeQuery(id+"F3.imprint","IMPRINT",EDGE,{"derivedFrom":subQ76}),1.0]])]})])],"isStart":true});Q21=makeQuery(id+"F44.opFillet","BLEND_EDGE",EDGE,{"blendedFrom":[makeQuery(id+"F40.boolean.opBoolean","INTERSECT",EDGE,{"derivedFrom":[subQ8,subQ9]}),makeQuery(id+"F40.boolean.opBoolean","SPLIT",FACE,{"disambiguationData":[TD([subQ0])],"derivedFrom":makeQuery(id+"F35.boolean.opBoolean","SPLIT",FACE,{"disambiguationData":[TD([subQ12])],"derivedFrom":makeQuery(id+"F34.boolean.opBoolean","SPLIT",FACE,{"disambiguationData":[TD([subQ37])],"derivedFrom":makeQuery(id+"F33.boolean.opBoolean","SPLIT",FACE,{"disambiguationData":[TD([subQ37])],"derivedFrom":makeQuery(id+"F32.boolean.opBoolean","SPLIT",FACE,{"disambiguationData":[TD([subQ37])],"derivedFrom":makeQuery(id+"F31.boolean.opBoolean","SPLIT",FACE,{"disambiguationData":[TD([subQ37])],"derivedFrom":makeQuery(id+"F30.boolean.opBoolean","SPLIT",FACE,{"disambiguationData":[TD([subQ81])],"derivedFrom":makeQuery(id+"F29.boolean.opBoolean","SPLIT",FACE,{"disambiguationData":[TD([subQ81])],"derivedFrom":makeQuery(id+"F28.boolean.opBoolean","SPLIT",FACE,{"disambiguationData":[TD([subQ81])],"derivedFrom":makeQuery(id+"F27.boolean.opBoolean","SPLIT",FACE,{"disambiguationData":[TD([subQ81])],"derivedFrom":makeQuery(id+"F26.boolean.opBoolean","SPLIT",FACE,{"disambiguationData":[TD([subQ81])],"derivedFrom":makeQuery(id+"F25.boolean.opBoolean","SPLIT",FACE,{"disambiguationData":[TD([subQ81])],"derivedFrom":makeQuery(id+"F24.boolean.opBoolean","SPLIT",FACE,{"disambiguationData":[TD([subQ81])],"derivedFrom":makeQuery(id+"F1.opRevolve","SWEPT_FACE",FACE,{"disambiguationData":[OSD([sQuery(id+"F0.wireOp",EDGE,"E13")])]})})})})})})})})})})})})})})],"blendedInto":[makeQuery(id+"F40.boolean.opBoolean","SPLIT",FACE,{"disambiguationData":[TD([subQ0])],"derivedFrom":makeQuery(id+"F35.boolean.opBoolean","SPLIT",FACE,{"disambiguationData":[TD([subQ12])],"derivedFrom":makeQuery(id+"F34.boolean.opBoolean","SPLIT",FACE,{"disambiguationData":[TD([subQ37])],"derivedFrom":makeQuery(id+"F33.boolean.opBoolean","SPLIT",FACE,{"disambiguationData":[TD([subQ37])],"derivedFrom":makeQuery(id+"F32.boolean.opBoolean","SPLIT",FACE,{"disambiguationData":[TD([subQ37])],"derivedFrom":makeQuery(id+"F31.boolean.opBoolean","SPLIT",FACE,{"disambiguationData":[TD([subQ37])],"derivedFrom":makeQuery(id+"F30.boolean.opBoolean","SPLIT",FACE,{"disambiguationData":[TD([subQ81])],"derivedFrom":makeQuery(id+"F29.boolean.opBoolean","SPLIT",FACE,{"disambiguationData":[TD([subQ81])],"derivedFrom":makeQuery(id+"F28.boolean.opBoolean","SPLIT",FACE,{"disambiguationData":[TD([subQ81])],"derivedFrom":makeQuery(id+"F27.boolean.opBoolean","SPLIT",FACE,{"disambiguationData":[TD([subQ81])],"derivedFrom":makeQuery(id+"F26.boolean.opBoolean","SPLIT",FACE,{"disambiguationData":[TD([subQ81])],"derivedFrom":makeQuery(id+"F25.boolean.opBoolean","SPLIT",FACE,{"disambiguationData":[TD([subQ81])],"derivedFrom":makeQuery(id+"F24.boolean.opBoolean","SPLIT",FACE,{"disambiguationData":[TD([subQ81])],"derivedFrom":makeQuery(id+"F1.opRevolve","SWEPT_FACE",FACE,{"disambiguationData":[OSD([sQuery(id+"F0.wireOp",EDGE,"E13")])]})})})})})})})})})})})})})})]});}
            var Q22;
            {var subQ0=makeQuery(id+"F1.opRevolve","SWEPT_FACE",FACE,{"disambiguationData":[OSD([sQuery(id+"F0.wireOp",EDGE,"E12")])]});var subQ5=makeQuery(id+"F40.opExtrude","CAP_FACE",FACE,{"disambiguationData":[OSD([sQuery(id+"F39.wireOp",EDGE,"E29"),sQuery(id+"F39.wireOp",EDGE,"E30")])],"isStart":true});var subQ6=sQuery(id+"F3.wireOp",EDGE,"E20.3.3");var subQ7=sQuery(id+"F3.wireOp",EDGE,"E20.3.2");var subQ8=sQuery(id+"F3.wireOp",EDGE,"E20.3.1");var subQ9=makeQuery(id+"F34.opLoft","SWEPT_FACE",FACE,{"disambiguationData":[OSD([subQ8,subQ7,subQ6,sQuery(id+"F22.wireOp",EDGE,"E28.11.0"),sQuery(id+"F22.wireOp",EDGE,"E28.11.2"),sQuery(id+"F22.wireOp",EDGE,"E28.11.3")])]});var subQ13=sQuery(id+"F4.wireOp",EDGE,"E26.3.3");var subQ14=sQuery(id+"F4.wireOp",EDGE,"E26.3.2");var subQ15=makeQuery(id+"F18.opLoft","SWEPT_FACE",FACE,{"disambiguationData":[OSD([subQ8,subQ7,subQ6,sQuery(id+"F4.wireOp",EDGE,"E26.3.1"),subQ14,subQ13])]});var subQ36=sQuery(id+"F3.wireOp",EDGE,"E20.7.0");var subQ40=makeQuery(id+"F14.opLoft","CAP_FACE",FACE,{"disambiguationData":[OSD([makeQuery(id+"F3.imprint","IMPRINT",FACE,{"disambiguationData":[TD([[makeQuery(id+"F3.imprint","IMPRINT",EDGE,{"derivedFrom":subQ36}),-1.0]])]})])],"isStart":true});var subQ76=sQuery(id+"F3.wireOp",EDGE,"E18.bottom");var subQ81=makeQuery(id+"F5.opLoft","CAP_FACE",FACE,{"disambiguationData":[OSD([makeQuery(id+"F3.imprint","IMPRINT",FACE,{"disambiguationData":[TD([[makeQuery(id+"F3.imprint","IMPRINT",EDGE,{"derivedFrom":subQ76}),1.0]])]})])],"isStart":true});Q22=makeQuery(id+"F44.opFillet","BLEND_EDGE",EDGE,{"blendedFrom":[makeQuery(id+"F40.boolean.opBoolean","INTERSECT",EDGE,{"derivedFrom":[subQ9,subQ5]}),makeQuery(id+"F40.boolean.opBoolean","SPLIT",FACE,{"disambiguationData":[TD([subQ0])],"derivedFrom":makeQuery(id+"F34.boolean.opBoolean","SPLIT",FACE,{"disambiguationData":[TD([subQ15])],"derivedFrom":makeQuery(id+"F33.boolean.opBoolean","SPLIT",FACE,{"disambiguationData":[TD([subQ40])],"derivedFrom":makeQuery(id+"F32.boolean.opBoolean","SPLIT",FACE,{"disambiguationData":[TD([subQ40])],"derivedFrom":makeQuery(id+"F31.boolean.opBoolean","SPLIT",FACE,{"disambiguationData":[TD([subQ40])],"derivedFrom":makeQuery(id+"F30.boolean.opBoolean","SPLIT",FACE,{"disambiguationData":[TD([subQ81])],"derivedFrom":makeQuery(id+"F29.boolean.opBoolean","SPLIT",FACE,{"disambiguationData":[TD([subQ81])],"derivedFrom":makeQuery(id+"F28.boolean.opBoolean","SPLIT",FACE,{"disambiguationData":[TD([subQ81])],"derivedFrom":makeQuery(id+"F27.boolean.opBoolean","SPLIT",FACE,{"disambiguationData":[TD([subQ81])],"derivedFrom":makeQuery(id+"F26.boolean.opBoolean","SPLIT",FACE,{"disambiguationData":[TD([subQ81])],"derivedFrom":makeQuery(id+"F25.boolean.opBoolean","SPLIT",FACE,{"disambiguationData":[TD([subQ81])],"derivedFrom":makeQuery(id+"F24.boolean.opBoolean","SPLIT",FACE,{"disambiguationData":[TD([subQ81])],"derivedFrom":makeQuery(id+"F1.opRevolve","SWEPT_FACE",FACE,{"disambiguationData":[OSD([sQuery(id+"F0.wireOp",EDGE,"E13")])]})})})})})})})})})})})})})],"blendedInto":[makeQuery(id+"F40.boolean.opBoolean","SPLIT",FACE,{"disambiguationData":[TD([subQ0])],"derivedFrom":makeQuery(id+"F34.boolean.opBoolean","SPLIT",FACE,{"disambiguationData":[TD([subQ15])],"derivedFrom":makeQuery(id+"F33.boolean.opBoolean","SPLIT",FACE,{"disambiguationData":[TD([subQ40])],"derivedFrom":makeQuery(id+"F32.boolean.opBoolean","SPLIT",FACE,{"disambiguationData":[TD([subQ40])],"derivedFrom":makeQuery(id+"F31.boolean.opBoolean","SPLIT",FACE,{"disambiguationData":[TD([subQ40])],"derivedFrom":makeQuery(id+"F30.boolean.opBoolean","SPLIT",FACE,{"disambiguationData":[TD([subQ81])],"derivedFrom":makeQuery(id+"F29.boolean.opBoolean","SPLIT",FACE,{"disambiguationData":[TD([subQ81])],"derivedFrom":makeQuery(id+"F28.boolean.opBoolean","SPLIT",FACE,{"disambiguationData":[TD([subQ81])],"derivedFrom":makeQuery(id+"F27.boolean.opBoolean","SPLIT",FACE,{"disambiguationData":[TD([subQ81])],"derivedFrom":makeQuery(id+"F26.boolean.opBoolean","SPLIT",FACE,{"disambiguationData":[TD([subQ81])],"derivedFrom":makeQuery(id+"F25.boolean.opBoolean","SPLIT",FACE,{"disambiguationData":[TD([subQ81])],"derivedFrom":makeQuery(id+"F24.boolean.opBoolean","SPLIT",FACE,{"disambiguationData":[TD([subQ81])],"derivedFrom":makeQuery(id+"F1.opRevolve","SWEPT_FACE",FACE,{"disambiguationData":[OSD([sQuery(id+"F0.wireOp",EDGE,"E13")])]})})})})})})})})})})})})})]});}
            var Q23;
            {var subQ0=makeQuery(id+"F1.opRevolve","SWEPT_FACE",FACE,{"disambiguationData":[OSD([sQuery(id+"F0.wireOp",EDGE,"E12")])]});var subQ5=sQuery(id+"F3.wireOp",EDGE,"E20.2.3");var subQ6=sQuery(id+"F3.wireOp",EDGE,"E20.2.2");var subQ7=sQuery(id+"F3.wireOp",EDGE,"E20.2.1");var subQ8=makeQuery(id+"F33.opLoft","SWEPT_FACE",FACE,{"disambiguationData":[OSD([subQ7,subQ6,subQ5,sQuery(id+"F22.wireOp",EDGE,"E28.10.0"),sQuery(id+"F22.wireOp",EDGE,"E28.10.2"),sQuery(id+"F22.wireOp",EDGE,"E28.10.3")])]});var subQ9=makeQuery(id+"F40.opExtrude","CAP_FACE",FACE,{"disambiguationData":[OSD([sQuery(id+"F39.wireOp",EDGE,"E29"),sQuery(id+"F39.wireOp",EDGE,"E30")])],"isStart":true});var subQ13=sQuery(id+"F4.wireOp",EDGE,"E26.2.3");var subQ14=sQuery(id+"F4.wireOp",EDGE,"E26.2.2");var subQ15=makeQuery(id+"F19.opLoft","SWEPT_FACE",FACE,{"disambiguationData":[OSD([subQ7,subQ6,subQ5,sQuery(id+"F4.wireOp",EDGE,"E26.2.1"),subQ14,subQ13])]});var subQ56=sQuery(id+"F3.wireOp",EDGE,"E20.7.0");var subQ63=makeQuery(id+"F14.opLoft","CAP_FACE",FACE,{"disambiguationData":[OSD([makeQuery(id+"F3.imprint","IMPRINT",FACE,{"disambiguationData":[TD([[makeQuery(id+"F3.imprint","IMPRINT",EDGE,{"derivedFrom":subQ56}),-1.0]])]})])],"isStart":true});var subQ76=sQuery(id+"F3.wireOp",EDGE,"E18.bottom");var subQ81=makeQuery(id+"F5.opLoft","CAP_FACE",FACE,{"disambiguationData":[OSD([makeQuery(id+"F3.imprint","IMPRINT",FACE,{"disambiguationData":[TD([[makeQuery(id+"F3.imprint","IMPRINT",EDGE,{"derivedFrom":subQ76}),1.0]])]})])],"isStart":true});Q23=makeQuery(id+"F44.opFillet","BLEND_EDGE",EDGE,{"blendedFrom":[makeQuery(id+"F40.boolean.opBoolean","INTERSECT",EDGE,{"derivedFrom":[subQ8,subQ9]}),makeQuery(id+"F40.boolean.opBoolean","SPLIT",FACE,{"disambiguationData":[TD([subQ0])],"derivedFrom":makeQuery(id+"F33.boolean.opBoolean","SPLIT",FACE,{"disambiguationData":[TD([subQ15])],"derivedFrom":makeQuery(id+"F32.boolean.opBoolean","SPLIT",FACE,{"disambiguationData":[TD([subQ63])],"derivedFrom":makeQuery(id+"F31.boolean.opBoolean","SPLIT",FACE,{"disambiguationData":[TD([subQ63])],"derivedFrom":makeQuery(id+"F30.boolean.opBoolean","SPLIT",FACE,{"disambiguationData":[TD([subQ81])],"derivedFrom":makeQuery(id+"F29.boolean.opBoolean","SPLIT",FACE,{"disambiguationData":[TD([subQ81])],"derivedFrom":makeQuery(id+"F28.boolean.opBoolean","SPLIT",FACE,{"disambiguationData":[TD([subQ81])],"derivedFrom":makeQuery(id+"F27.boolean.opBoolean","SPLIT",FACE,{"disambiguationData":[TD([subQ81])],"derivedFrom":makeQuery(id+"F26.boolean.opBoolean","SPLIT",FACE,{"disambiguationData":[TD([subQ81])],"derivedFrom":makeQuery(id+"F25.boolean.opBoolean","SPLIT",FACE,{"disambiguationData":[TD([subQ81])],"derivedFrom":makeQuery(id+"F24.boolean.opBoolean","SPLIT",FACE,{"disambiguationData":[TD([subQ81])],"derivedFrom":makeQuery(id+"F1.opRevolve","SWEPT_FACE",FACE,{"disambiguationData":[OSD([sQuery(id+"F0.wireOp",EDGE,"E13")])]})})})})})})})})})})})})],"blendedInto":[makeQuery(id+"F40.boolean.opBoolean","SPLIT",FACE,{"disambiguationData":[TD([subQ0])],"derivedFrom":makeQuery(id+"F33.boolean.opBoolean","SPLIT",FACE,{"disambiguationData":[TD([subQ15])],"derivedFrom":makeQuery(id+"F32.boolean.opBoolean","SPLIT",FACE,{"disambiguationData":[TD([subQ63])],"derivedFrom":makeQuery(id+"F31.boolean.opBoolean","SPLIT",FACE,{"disambiguationData":[TD([subQ63])],"derivedFrom":makeQuery(id+"F30.boolean.opBoolean","SPLIT",FACE,{"disambiguationData":[TD([subQ81])],"derivedFrom":makeQuery(id+"F29.boolean.opBoolean","SPLIT",FACE,{"disambiguationData":[TD([subQ81])],"derivedFrom":makeQuery(id+"F28.boolean.opBoolean","SPLIT",FACE,{"disambiguationData":[TD([subQ81])],"derivedFrom":makeQuery(id+"F27.boolean.opBoolean","SPLIT",FACE,{"disambiguationData":[TD([subQ81])],"derivedFrom":makeQuery(id+"F26.boolean.opBoolean","SPLIT",FACE,{"disambiguationData":[TD([subQ81])],"derivedFrom":makeQuery(id+"F25.boolean.opBoolean","SPLIT",FACE,{"disambiguationData":[TD([subQ81])],"derivedFrom":makeQuery(id+"F24.boolean.opBoolean","SPLIT",FACE,{"disambiguationData":[TD([subQ81])],"derivedFrom":makeQuery(id+"F1.opRevolve","SWEPT_FACE",FACE,{"disambiguationData":[OSD([sQuery(id+"F0.wireOp",EDGE,"E13")])]})})})})})})})})})})})})]});}
            var Q24;
            {var subQ0=makeQuery(id+"F1.opRevolve","SWEPT_FACE",FACE,{"disambiguationData":[OSD([sQuery(id+"F0.wireOp",EDGE,"E12")])]});var subQ1=sQuery(id+"F3.wireOp",EDGE,"E20.1.3");var subQ2=sQuery(id+"F3.wireOp",EDGE,"E20.1.2");var subQ3=sQuery(id+"F3.wireOp",EDGE,"E20.1.1");var subQ4=makeQuery(id+"F32.opLoft","SWEPT_FACE",FACE,{"disambiguationData":[OSD([subQ3,subQ2,subQ1,sQuery(id+"F22.wireOp",EDGE,"E28.9.0"),sQuery(id+"F22.wireOp",EDGE,"E28.9.2"),sQuery(id+"F22.wireOp",EDGE,"E28.9.3")])]});var subQ5=sQuery(id+"F3.wireOp",EDGE,"E18.left");var subQ6=sQuery(id+"F3.wireOp",EDGE,"E18.top");var subQ7=sQuery(id+"F3.wireOp",EDGE,"E18.bottom");var subQ9=makeQuery(id+"F40.opExtrude","CAP_FACE",FACE,{"disambiguationData":[OSD([sQuery(id+"F39.wireOp",EDGE,"E29"),sQuery(id+"F39.wireOp",EDGE,"E30")])],"isStart":true});var subQ13=sQuery(id+"F4.wireOp",EDGE,"E23");var subQ14=sQuery(id+"F4.wireOp",EDGE,"E22");var subQ15=makeQuery(id+"F5.opLoft","SWEPT_FACE",FACE,{"disambiguationData":[OSD([subQ7,subQ6,subQ5,sQuery(id+"F4.wireOp",EDGE,"E21"),subQ14,subQ13])]});var subQ65=sQuery(id+"F3.wireOp",EDGE,"E20.7.0");var subQ73=makeQuery(id+"F14.opLoft","CAP_FACE",FACE,{"disambiguationData":[OSD([makeQuery(id+"F3.imprint","IMPRINT",FACE,{"disambiguationData":[TD([[makeQuery(id+"F3.imprint","IMPRINT",EDGE,{"derivedFrom":subQ65}),-1.0]])]})])],"isStart":true});var subQ81=makeQuery(id+"F5.opLoft","CAP_FACE",FACE,{"disambiguationData":[OSD([makeQuery(id+"F3.imprint","IMPRINT",FACE,{"disambiguationData":[TD([[makeQuery(id+"F3.imprint","IMPRINT",EDGE,{"derivedFrom":subQ7}),1.0]])]})])],"isStart":true});Q24=makeQuery(id+"F44.opFillet","BLEND_EDGE",EDGE,{"blendedFrom":[makeQuery(id+"F40.boolean.opBoolean","INTERSECT",EDGE,{"derivedFrom":[subQ4,subQ9]}),makeQuery(id+"F40.boolean.opBoolean","SPLIT",FACE,{"disambiguationData":[TD([subQ0])],"derivedFrom":makeQuery(id+"F32.boolean.opBoolean","SPLIT",FACE,{"disambiguationData":[TD([subQ15])],"derivedFrom":makeQuery(id+"F31.boolean.opBoolean","SPLIT",FACE,{"disambiguationData":[TD([subQ73])],"derivedFrom":makeQuery(id+"F30.boolean.opBoolean","SPLIT",FACE,{"disambiguationData":[TD([subQ81])],"derivedFrom":makeQuery(id+"F29.boolean.opBoolean","SPLIT",FACE,{"disambiguationData":[TD([subQ81])],"derivedFrom":makeQuery(id+"F28.boolean.opBoolean","SPLIT",FACE,{"disambiguationData":[TD([subQ81])],"derivedFrom":makeQuery(id+"F27.boolean.opBoolean","SPLIT",FACE,{"disambiguationData":[TD([subQ81])],"derivedFrom":makeQuery(id+"F26.boolean.opBoolean","SPLIT",FACE,{"disambiguationData":[TD([subQ81])],"derivedFrom":makeQuery(id+"F25.boolean.opBoolean","SPLIT",FACE,{"disambiguationData":[TD([subQ81])],"derivedFrom":makeQuery(id+"F24.boolean.opBoolean","SPLIT",FACE,{"disambiguationData":[TD([subQ81])],"derivedFrom":makeQuery(id+"F1.opRevolve","SWEPT_FACE",FACE,{"disambiguationData":[OSD([sQuery(id+"F0.wireOp",EDGE,"E13")])]})})})})})})})})})})})],"blendedInto":[makeQuery(id+"F40.boolean.opBoolean","SPLIT",FACE,{"disambiguationData":[TD([subQ0])],"derivedFrom":makeQuery(id+"F32.boolean.opBoolean","SPLIT",FACE,{"disambiguationData":[TD([subQ15])],"derivedFrom":makeQuery(id+"F31.boolean.opBoolean","SPLIT",FACE,{"disambiguationData":[TD([subQ73])],"derivedFrom":makeQuery(id+"F30.boolean.opBoolean","SPLIT",FACE,{"disambiguationData":[TD([subQ81])],"derivedFrom":makeQuery(id+"F29.boolean.opBoolean","SPLIT",FACE,{"disambiguationData":[TD([subQ81])],"derivedFrom":makeQuery(id+"F28.boolean.opBoolean","SPLIT",FACE,{"disambiguationData":[TD([subQ81])],"derivedFrom":makeQuery(id+"F27.boolean.opBoolean","SPLIT",FACE,{"disambiguationData":[TD([subQ81])],"derivedFrom":makeQuery(id+"F26.boolean.opBoolean","SPLIT",FACE,{"disambiguationData":[TD([subQ81])],"derivedFrom":makeQuery(id+"F25.boolean.opBoolean","SPLIT",FACE,{"disambiguationData":[TD([subQ81])],"derivedFrom":makeQuery(id+"F24.boolean.opBoolean","SPLIT",FACE,{"disambiguationData":[TD([subQ81])],"derivedFrom":makeQuery(id+"F1.opRevolve","SWEPT_FACE",FACE,{"disambiguationData":[OSD([sQuery(id+"F0.wireOp",EDGE,"E13")])]})})})})})})})})})})})]});}
            var Q25;
            {var subQ0=makeQuery(id+"F1.opRevolve","SWEPT_FACE",FACE,{"disambiguationData":[OSD([sQuery(id+"F0.wireOp",EDGE,"E12")])]});var subQ1=sQuery(id+"F3.wireOp",EDGE,"E18.right");var subQ2=sQuery(id+"F3.wireOp",EDGE,"E18.top");var subQ3=sQuery(id+"F3.wireOp",EDGE,"E18.bottom");var subQ4=makeQuery(id+"F31.opLoft","SWEPT_FACE",FACE,{"disambiguationData":[OSD([subQ3,subQ2,subQ1,sQuery(id+"F22.wireOp",EDGE,"E28.8.0"),sQuery(id+"F22.wireOp",EDGE,"E28.8.2"),sQuery(id+"F22.wireOp",EDGE,"E28.8.3")])]});var subQ9=makeQuery(id+"F40.opExtrude","CAP_FACE",FACE,{"disambiguationData":[OSD([sQuery(id+"F39.wireOp",EDGE,"E29"),sQuery(id+"F39.wireOp",EDGE,"E30")])],"isStart":true});var subQ13=sQuery(id+"F4.wireOp",EDGE,"E23");var subQ14=sQuery(id+"F4.wireOp",EDGE,"E22");var subQ15=makeQuery(id+"F5.opLoft","SWEPT_FACE",FACE,{"disambiguationData":[OSD([subQ3,subQ2,subQ1,subQ14,subQ13,sQuery(id+"F4.wireOp",EDGE,"E24")])]});var subQ59=makeQuery(id+"F5.opLoft","CAP_FACE",FACE,{"disambiguationData":[OSD([makeQuery(id+"F3.imprint","IMPRINT",FACE,{"disambiguationData":[TD([[makeQuery(id+"F3.imprint","IMPRINT",EDGE,{"derivedFrom":subQ3}),1.0]])]})])],"isStart":true});Q25=makeQuery(id+"F44.opFillet","BLEND_EDGE",EDGE,{"blendedFrom":[makeQuery(id+"F40.boolean.opBoolean","INTERSECT",EDGE,{"derivedFrom":[subQ4,subQ9]}),makeQuery(id+"F40.boolean.opBoolean","SPLIT",FACE,{"disambiguationData":[TD([subQ0])],"derivedFrom":makeQuery(id+"F31.boolean.opBoolean","SPLIT",FACE,{"disambiguationData":[TD([subQ15])],"derivedFrom":makeQuery(id+"F30.boolean.opBoolean","SPLIT",FACE,{"disambiguationData":[TD([subQ59])],"derivedFrom":makeQuery(id+"F29.boolean.opBoolean","SPLIT",FACE,{"disambiguationData":[TD([subQ59])],"derivedFrom":makeQuery(id+"F28.boolean.opBoolean","SPLIT",FACE,{"disambiguationData":[TD([subQ59])],"derivedFrom":makeQuery(id+"F27.boolean.opBoolean","SPLIT",FACE,{"disambiguationData":[TD([subQ59])],"derivedFrom":makeQuery(id+"F26.boolean.opBoolean","SPLIT",FACE,{"disambiguationData":[TD([subQ59])],"derivedFrom":makeQuery(id+"F25.boolean.opBoolean","SPLIT",FACE,{"disambiguationData":[TD([subQ59])],"derivedFrom":makeQuery(id+"F24.boolean.opBoolean","SPLIT",FACE,{"disambiguationData":[TD([subQ59])],"derivedFrom":makeQuery(id+"F1.opRevolve","SWEPT_FACE",FACE,{"disambiguationData":[OSD([sQuery(id+"F0.wireOp",EDGE,"E13")])]})})})})})})})})})})],"blendedInto":[makeQuery(id+"F40.boolean.opBoolean","SPLIT",FACE,{"disambiguationData":[TD([subQ0])],"derivedFrom":makeQuery(id+"F31.boolean.opBoolean","SPLIT",FACE,{"disambiguationData":[TD([subQ15])],"derivedFrom":makeQuery(id+"F30.boolean.opBoolean","SPLIT",FACE,{"disambiguationData":[TD([subQ59])],"derivedFrom":makeQuery(id+"F29.boolean.opBoolean","SPLIT",FACE,{"disambiguationData":[TD([subQ59])],"derivedFrom":makeQuery(id+"F28.boolean.opBoolean","SPLIT",FACE,{"disambiguationData":[TD([subQ59])],"derivedFrom":makeQuery(id+"F27.boolean.opBoolean","SPLIT",FACE,{"disambiguationData":[TD([subQ59])],"derivedFrom":makeQuery(id+"F26.boolean.opBoolean","SPLIT",FACE,{"disambiguationData":[TD([subQ59])],"derivedFrom":makeQuery(id+"F25.boolean.opBoolean","SPLIT",FACE,{"disambiguationData":[TD([subQ59])],"derivedFrom":makeQuery(id+"F24.boolean.opBoolean","SPLIT",FACE,{"disambiguationData":[TD([subQ59])],"derivedFrom":makeQuery(id+"F1.opRevolve","SWEPT_FACE",FACE,{"disambiguationData":[OSD([sQuery(id+"F0.wireOp",EDGE,"E13")])]})})})})})})})})})})]});}
            var Q26;
            {var subQ0=makeQuery(id+"F1.opRevolve","SWEPT_FACE",FACE,{"disambiguationData":[OSD([sQuery(id+"F0.wireOp",EDGE,"E12")])]});var subQ5=sQuery(id+"F3.wireOp",EDGE,"E20.15.3");var subQ6=sQuery(id+"F3.wireOp",EDGE,"E20.15.2");var subQ7=sQuery(id+"F3.wireOp",EDGE,"E20.15.1");var subQ8=makeQuery(id+"F30.opLoft","SWEPT_FACE",FACE,{"disambiguationData":[OSD([subQ7,subQ6,subQ5,sQuery(id+"F22.wireOp",EDGE,"E28.7.0"),sQuery(id+"F22.wireOp",EDGE,"E28.7.2"),sQuery(id+"F22.wireOp",EDGE,"E28.7.3")])]});var subQ9=makeQuery(id+"F40.opExtrude","CAP_FACE",FACE,{"disambiguationData":[OSD([sQuery(id+"F39.wireOp",EDGE,"E29"),sQuery(id+"F39.wireOp",EDGE,"E30")])],"isStart":true});var subQ10=sQuery(id+"F4.wireOp",EDGE,"E26.15.3");var subQ11=sQuery(id+"F4.wireOp",EDGE,"E26.15.2");var subQ12=makeQuery(id+"F6.opLoft","SWEPT_FACE",FACE,{"disambiguationData":[OSD([subQ7,subQ6,subQ5,sQuery(id+"F4.wireOp",EDGE,"E26.15.1"),subQ11,subQ10])]});var subQ48=sQuery(id+"F3.wireOp",EDGE,"E18.bottom");var subQ51=makeQuery(id+"F5.opLoft","CAP_FACE",FACE,{"disambiguationData":[OSD([makeQuery(id+"F3.imprint","IMPRINT",FACE,{"disambiguationData":[TD([[makeQuery(id+"F3.imprint","IMPRINT",EDGE,{"derivedFrom":subQ48}),1.0]])]})])],"isStart":true});Q26=makeQuery(id+"F44.opFillet","BLEND_EDGE",EDGE,{"blendedFrom":[makeQuery(id+"F40.boolean.opBoolean","INTERSECT",EDGE,{"derivedFrom":[subQ8,subQ9]}),makeQuery(id+"F40.boolean.opBoolean","SPLIT",FACE,{"disambiguationData":[TD([subQ0])],"derivedFrom":makeQuery(id+"F30.boolean.opBoolean","SPLIT",FACE,{"disambiguationData":[TD([subQ12])],"derivedFrom":makeQuery(id+"F29.boolean.opBoolean","SPLIT",FACE,{"disambiguationData":[TD([subQ51])],"derivedFrom":makeQuery(id+"F28.boolean.opBoolean","SPLIT",FACE,{"disambiguationData":[TD([subQ51])],"derivedFrom":makeQuery(id+"F27.boolean.opBoolean","SPLIT",FACE,{"disambiguationData":[TD([subQ51])],"derivedFrom":makeQuery(id+"F26.boolean.opBoolean","SPLIT",FACE,{"disambiguationData":[TD([subQ51])],"derivedFrom":makeQuery(id+"F25.boolean.opBoolean","SPLIT",FACE,{"disambiguationData":[TD([subQ51])],"derivedFrom":makeQuery(id+"F24.boolean.opBoolean","SPLIT",FACE,{"disambiguationData":[TD([subQ51])],"derivedFrom":makeQuery(id+"F1.opRevolve","SWEPT_FACE",FACE,{"disambiguationData":[OSD([sQuery(id+"F0.wireOp",EDGE,"E13")])]})})})})})})})})})],"blendedInto":[makeQuery(id+"F40.boolean.opBoolean","SPLIT",FACE,{"disambiguationData":[TD([subQ0])],"derivedFrom":makeQuery(id+"F30.boolean.opBoolean","SPLIT",FACE,{"disambiguationData":[TD([subQ12])],"derivedFrom":makeQuery(id+"F29.boolean.opBoolean","SPLIT",FACE,{"disambiguationData":[TD([subQ51])],"derivedFrom":makeQuery(id+"F28.boolean.opBoolean","SPLIT",FACE,{"disambiguationData":[TD([subQ51])],"derivedFrom":makeQuery(id+"F27.boolean.opBoolean","SPLIT",FACE,{"disambiguationData":[TD([subQ51])],"derivedFrom":makeQuery(id+"F26.boolean.opBoolean","SPLIT",FACE,{"disambiguationData":[TD([subQ51])],"derivedFrom":makeQuery(id+"F25.boolean.opBoolean","SPLIT",FACE,{"disambiguationData":[TD([subQ51])],"derivedFrom":makeQuery(id+"F24.boolean.opBoolean","SPLIT",FACE,{"disambiguationData":[TD([subQ51])],"derivedFrom":makeQuery(id+"F1.opRevolve","SWEPT_FACE",FACE,{"disambiguationData":[OSD([sQuery(id+"F0.wireOp",EDGE,"E13")])]})})})})})})})})})]});}
            var Q27;
            {var subQ0=makeQuery(id+"F1.opRevolve","SWEPT_FACE",FACE,{"disambiguationData":[OSD([sQuery(id+"F0.wireOp",EDGE,"E12")])]});var subQ5=sQuery(id+"F3.wireOp",EDGE,"E20.14.3");var subQ6=sQuery(id+"F3.wireOp",EDGE,"E20.14.2");var subQ7=sQuery(id+"F3.wireOp",EDGE,"E20.14.1");var subQ8=makeQuery(id+"F29.opLoft","SWEPT_FACE",FACE,{"disambiguationData":[OSD([subQ7,subQ6,subQ5,sQuery(id+"F22.wireOp",EDGE,"E28.6.0"),sQuery(id+"F22.wireOp",EDGE,"E28.6.2"),sQuery(id+"F22.wireOp",EDGE,"E28.6.3")])]});var subQ9=makeQuery(id+"F40.opExtrude","CAP_FACE",FACE,{"disambiguationData":[OSD([sQuery(id+"F39.wireOp",EDGE,"E29"),sQuery(id+"F39.wireOp",EDGE,"E30")])],"isStart":true});var subQ13=sQuery(id+"F4.wireOp",EDGE,"E26.14.3");var subQ14=sQuery(id+"F4.wireOp",EDGE,"E26.14.2");var subQ15=makeQuery(id+"F7.opLoft","SWEPT_FACE",FACE,{"disambiguationData":[OSD([subQ7,subQ6,subQ5,sQuery(id+"F4.wireOp",EDGE,"E26.14.1"),subQ14,subQ13])]});var subQ49=sQuery(id+"F3.wireOp",EDGE,"E18.bottom");var subQ52=makeQuery(id+"F5.opLoft","CAP_FACE",FACE,{"disambiguationData":[OSD([makeQuery(id+"F3.imprint","IMPRINT",FACE,{"disambiguationData":[TD([[makeQuery(id+"F3.imprint","IMPRINT",EDGE,{"derivedFrom":subQ49}),1.0]])]})])],"isStart":true});Q27=makeQuery(id+"F44.opFillet","BLEND_EDGE",EDGE,{"blendedFrom":[makeQuery(id+"F40.boolean.opBoolean","INTERSECT",EDGE,{"derivedFrom":[subQ8,subQ9]}),makeQuery(id+"F40.boolean.opBoolean","SPLIT",FACE,{"disambiguationData":[TD([subQ0])],"derivedFrom":makeQuery(id+"F29.boolean.opBoolean","SPLIT",FACE,{"disambiguationData":[TD([subQ15])],"derivedFrom":makeQuery(id+"F28.boolean.opBoolean","SPLIT",FACE,{"disambiguationData":[TD([subQ52])],"derivedFrom":makeQuery(id+"F27.boolean.opBoolean","SPLIT",FACE,{"disambiguationData":[TD([subQ52])],"derivedFrom":makeQuery(id+"F26.boolean.opBoolean","SPLIT",FACE,{"disambiguationData":[TD([subQ52])],"derivedFrom":makeQuery(id+"F25.boolean.opBoolean","SPLIT",FACE,{"disambiguationData":[TD([subQ52])],"derivedFrom":makeQuery(id+"F24.boolean.opBoolean","SPLIT",FACE,{"disambiguationData":[TD([subQ52])],"derivedFrom":makeQuery(id+"F1.opRevolve","SWEPT_FACE",FACE,{"disambiguationData":[OSD([sQuery(id+"F0.wireOp",EDGE,"E13")])]})})})})})})})})],"blendedInto":[makeQuery(id+"F40.boolean.opBoolean","SPLIT",FACE,{"disambiguationData":[TD([subQ0])],"derivedFrom":makeQuery(id+"F29.boolean.opBoolean","SPLIT",FACE,{"disambiguationData":[TD([subQ15])],"derivedFrom":makeQuery(id+"F28.boolean.opBoolean","SPLIT",FACE,{"disambiguationData":[TD([subQ52])],"derivedFrom":makeQuery(id+"F27.boolean.opBoolean","SPLIT",FACE,{"disambiguationData":[TD([subQ52])],"derivedFrom":makeQuery(id+"F26.boolean.opBoolean","SPLIT",FACE,{"disambiguationData":[TD([subQ52])],"derivedFrom":makeQuery(id+"F25.boolean.opBoolean","SPLIT",FACE,{"disambiguationData":[TD([subQ52])],"derivedFrom":makeQuery(id+"F24.boolean.opBoolean","SPLIT",FACE,{"disambiguationData":[TD([subQ52])],"derivedFrom":makeQuery(id+"F1.opRevolve","SWEPT_FACE",FACE,{"disambiguationData":[OSD([sQuery(id+"F0.wireOp",EDGE,"E13")])]})})})})})})})})]});}
            var Q28;
            {var subQ0=makeQuery(id+"F1.opRevolve","SWEPT_FACE",FACE,{"disambiguationData":[OSD([sQuery(id+"F0.wireOp",EDGE,"E12")])]});var subQ5=sQuery(id+"F3.wireOp",EDGE,"E20.13.3");var subQ6=sQuery(id+"F3.wireOp",EDGE,"E20.13.2");var subQ7=sQuery(id+"F3.wireOp",EDGE,"E20.13.1");var subQ8=makeQuery(id+"F28.opLoft","SWEPT_FACE",FACE,{"disambiguationData":[OSD([subQ7,subQ6,subQ5,sQuery(id+"F22.wireOp",EDGE,"E28.5.0"),sQuery(id+"F22.wireOp",EDGE,"E28.5.2"),sQuery(id+"F22.wireOp",EDGE,"E28.5.3")])]});var subQ9=makeQuery(id+"F40.opExtrude","CAP_FACE",FACE,{"disambiguationData":[OSD([sQuery(id+"F39.wireOp",EDGE,"E29"),sQuery(id+"F39.wireOp",EDGE,"E30")])],"isStart":true});var subQ13=sQuery(id+"F4.wireOp",EDGE,"E26.13.3");var subQ14=sQuery(id+"F4.wireOp",EDGE,"E26.13.2");var subQ15=makeQuery(id+"F8.opLoft","SWEPT_FACE",FACE,{"disambiguationData":[OSD([subQ7,subQ6,subQ5,sQuery(id+"F4.wireOp",EDGE,"E26.13.1"),subQ14,subQ13])]});var subQ57=sQuery(id+"F3.wireOp",EDGE,"E18.bottom");var subQ60=makeQuery(id+"F5.opLoft","CAP_FACE",FACE,{"disambiguationData":[OSD([makeQuery(id+"F3.imprint","IMPRINT",FACE,{"disambiguationData":[TD([[makeQuery(id+"F3.imprint","IMPRINT",EDGE,{"derivedFrom":subQ57}),1.0]])]})])],"isStart":true});Q28=makeQuery(id+"F44.opFillet","BLEND_EDGE",EDGE,{"blendedFrom":[makeQuery(id+"F40.boolean.opBoolean","INTERSECT",EDGE,{"derivedFrom":[subQ8,subQ9]}),makeQuery(id+"F40.boolean.opBoolean","SPLIT",FACE,{"disambiguationData":[TD([subQ0])],"derivedFrom":makeQuery(id+"F28.boolean.opBoolean","SPLIT",FACE,{"disambiguationData":[TD([subQ15])],"derivedFrom":makeQuery(id+"F27.boolean.opBoolean","SPLIT",FACE,{"disambiguationData":[TD([subQ60])],"derivedFrom":makeQuery(id+"F26.boolean.opBoolean","SPLIT",FACE,{"disambiguationData":[TD([subQ60])],"derivedFrom":makeQuery(id+"F25.boolean.opBoolean","SPLIT",FACE,{"disambiguationData":[TD([subQ60])],"derivedFrom":makeQuery(id+"F24.boolean.opBoolean","SPLIT",FACE,{"disambiguationData":[TD([subQ60])],"derivedFrom":makeQuery(id+"F1.opRevolve","SWEPT_FACE",FACE,{"disambiguationData":[OSD([sQuery(id+"F0.wireOp",EDGE,"E13")])]})})})})})})})],"blendedInto":[makeQuery(id+"F40.boolean.opBoolean","SPLIT",FACE,{"disambiguationData":[TD([subQ0])],"derivedFrom":makeQuery(id+"F28.boolean.opBoolean","SPLIT",FACE,{"disambiguationData":[TD([subQ15])],"derivedFrom":makeQuery(id+"F27.boolean.opBoolean","SPLIT",FACE,{"disambiguationData":[TD([subQ60])],"derivedFrom":makeQuery(id+"F26.boolean.opBoolean","SPLIT",FACE,{"disambiguationData":[TD([subQ60])],"derivedFrom":makeQuery(id+"F25.boolean.opBoolean","SPLIT",FACE,{"disambiguationData":[TD([subQ60])],"derivedFrom":makeQuery(id+"F24.boolean.opBoolean","SPLIT",FACE,{"disambiguationData":[TD([subQ60])],"derivedFrom":makeQuery(id+"F1.opRevolve","SWEPT_FACE",FACE,{"disambiguationData":[OSD([sQuery(id+"F0.wireOp",EDGE,"E13")])]})})})})})})})]});}
            var Q29;
            {var subQ0=makeQuery(id+"F1.opRevolve","SWEPT_FACE",FACE,{"disambiguationData":[OSD([sQuery(id+"F0.wireOp",EDGE,"E12")])]});var subQ5=sQuery(id+"F3.wireOp",EDGE,"E20.12.3");var subQ6=sQuery(id+"F3.wireOp",EDGE,"E20.12.2");var subQ7=sQuery(id+"F3.wireOp",EDGE,"E20.12.1");var subQ8=makeQuery(id+"F27.opLoft","SWEPT_FACE",FACE,{"disambiguationData":[OSD([subQ7,subQ6,subQ5,sQuery(id+"F22.wireOp",EDGE,"E28.4.0"),sQuery(id+"F22.wireOp",EDGE,"E28.4.2"),sQuery(id+"F22.wireOp",EDGE,"E28.4.3")])]});var subQ9=makeQuery(id+"F40.opExtrude","CAP_FACE",FACE,{"disambiguationData":[OSD([sQuery(id+"F39.wireOp",EDGE,"E29"),sQuery(id+"F39.wireOp",EDGE,"E30")])],"isStart":true});var subQ13=sQuery(id+"F4.wireOp",EDGE,"E26.12.3");var subQ14=sQuery(id+"F4.wireOp",EDGE,"E26.12.2");var subQ15=makeQuery(id+"F9.opLoft","SWEPT_FACE",FACE,{"disambiguationData":[OSD([subQ7,subQ6,subQ5,sQuery(id+"F4.wireOp",EDGE,"E26.12.1"),subQ14,subQ13])]});var subQ75=sQuery(id+"F3.wireOp",EDGE,"E18.bottom");var subQ78=makeQuery(id+"F5.opLoft","CAP_FACE",FACE,{"disambiguationData":[OSD([makeQuery(id+"F3.imprint","IMPRINT",FACE,{"disambiguationData":[TD([[makeQuery(id+"F3.imprint","IMPRINT",EDGE,{"derivedFrom":subQ75}),1.0]])]})])],"isStart":true});Q29=makeQuery(id+"F44.opFillet","BLEND_EDGE",EDGE,{"blendedFrom":[makeQuery(id+"F40.boolean.opBoolean","INTERSECT",EDGE,{"derivedFrom":[subQ8,subQ9]}),makeQuery(id+"F40.boolean.opBoolean","SPLIT",FACE,{"disambiguationData":[TD([subQ0])],"derivedFrom":makeQuery(id+"F27.boolean.opBoolean","SPLIT",FACE,{"disambiguationData":[TD([subQ15])],"derivedFrom":makeQuery(id+"F26.boolean.opBoolean","SPLIT",FACE,{"disambiguationData":[TD([subQ78])],"derivedFrom":makeQuery(id+"F25.boolean.opBoolean","SPLIT",FACE,{"disambiguationData":[TD([subQ78])],"derivedFrom":makeQuery(id+"F24.boolean.opBoolean","SPLIT",FACE,{"disambiguationData":[TD([subQ78])],"derivedFrom":makeQuery(id+"F1.opRevolve","SWEPT_FACE",FACE,{"disambiguationData":[OSD([sQuery(id+"F0.wireOp",EDGE,"E13")])]})})})})})})],"blendedInto":[makeQuery(id+"F40.boolean.opBoolean","SPLIT",FACE,{"disambiguationData":[TD([subQ0])],"derivedFrom":makeQuery(id+"F27.boolean.opBoolean","SPLIT",FACE,{"disambiguationData":[TD([subQ15])],"derivedFrom":makeQuery(id+"F26.boolean.opBoolean","SPLIT",FACE,{"disambiguationData":[TD([subQ78])],"derivedFrom":makeQuery(id+"F25.boolean.opBoolean","SPLIT",FACE,{"disambiguationData":[TD([subQ78])],"derivedFrom":makeQuery(id+"F24.boolean.opBoolean","SPLIT",FACE,{"disambiguationData":[TD([subQ78])],"derivedFrom":makeQuery(id+"F1.opRevolve","SWEPT_FACE",FACE,{"disambiguationData":[OSD([sQuery(id+"F0.wireOp",EDGE,"E13")])]})})})})})})]});}
            var Q30;
            {var subQ0=makeQuery(id+"F1.opRevolve","SWEPT_FACE",FACE,{"disambiguationData":[OSD([sQuery(id+"F0.wireOp",EDGE,"E12")])]});var subQ5=sQuery(id+"F3.wireOp",EDGE,"E20.11.3");var subQ6=sQuery(id+"F3.wireOp",EDGE,"E20.11.2");var subQ7=sQuery(id+"F3.wireOp",EDGE,"E20.11.1");var subQ8=makeQuery(id+"F26.opLoft","SWEPT_FACE",FACE,{"disambiguationData":[OSD([subQ7,subQ6,subQ5,sQuery(id+"F22.wireOp",EDGE,"E28.3.0"),sQuery(id+"F22.wireOp",EDGE,"E28.3.2"),sQuery(id+"F22.wireOp",EDGE,"E28.3.3")])]});var subQ9=makeQuery(id+"F40.opExtrude","CAP_FACE",FACE,{"disambiguationData":[OSD([sQuery(id+"F39.wireOp",EDGE,"E29"),sQuery(id+"F39.wireOp",EDGE,"E30")])],"isStart":true});var subQ13=sQuery(id+"F4.wireOp",EDGE,"E26.11.3");var subQ14=sQuery(id+"F4.wireOp",EDGE,"E26.11.2");var subQ15=makeQuery(id+"F10.opLoft","SWEPT_FACE",FACE,{"disambiguationData":[OSD([subQ7,subQ6,subQ5,sQuery(id+"F4.wireOp",EDGE,"E26.11.1"),subQ14,subQ13])]});var subQ80=sQuery(id+"F3.wireOp",EDGE,"E18.bottom");var subQ83=makeQuery(id+"F5.opLoft","CAP_FACE",FACE,{"disambiguationData":[OSD([makeQuery(id+"F3.imprint","IMPRINT",FACE,{"disambiguationData":[TD([[makeQuery(id+"F3.imprint","IMPRINT",EDGE,{"derivedFrom":subQ80}),1.0]])]})])],"isStart":true});Q30=makeQuery(id+"F44.opFillet","BLEND_EDGE",EDGE,{"blendedFrom":[makeQuery(id+"F40.boolean.opBoolean","INTERSECT",EDGE,{"derivedFrom":[subQ8,subQ9]}),makeQuery(id+"F40.boolean.opBoolean","SPLIT",FACE,{"disambiguationData":[TD([subQ0])],"derivedFrom":makeQuery(id+"F26.boolean.opBoolean","SPLIT",FACE,{"disambiguationData":[TD([subQ15])],"derivedFrom":makeQuery(id+"F25.boolean.opBoolean","SPLIT",FACE,{"disambiguationData":[TD([subQ83])],"derivedFrom":makeQuery(id+"F24.boolean.opBoolean","SPLIT",FACE,{"disambiguationData":[TD([subQ83])],"derivedFrom":makeQuery(id+"F1.opRevolve","SWEPT_FACE",FACE,{"disambiguationData":[OSD([sQuery(id+"F0.wireOp",EDGE,"E13")])]})})})})})],"blendedInto":[makeQuery(id+"F40.boolean.opBoolean","SPLIT",FACE,{"disambiguationData":[TD([subQ0])],"derivedFrom":makeQuery(id+"F26.boolean.opBoolean","SPLIT",FACE,{"disambiguationData":[TD([subQ15])],"derivedFrom":makeQuery(id+"F25.boolean.opBoolean","SPLIT",FACE,{"disambiguationData":[TD([subQ83])],"derivedFrom":makeQuery(id+"F24.boolean.opBoolean","SPLIT",FACE,{"disambiguationData":[TD([subQ83])],"derivedFrom":makeQuery(id+"F1.opRevolve","SWEPT_FACE",FACE,{"disambiguationData":[OSD([sQuery(id+"F0.wireOp",EDGE,"E13")])]})})})})})]});}
            var Q31;
            {var subQ0=makeQuery(id+"F1.opRevolve","SWEPT_FACE",FACE,{"disambiguationData":[OSD([sQuery(id+"F0.wireOp",EDGE,"E12")])]});var subQ5=sQuery(id+"F3.wireOp",EDGE,"E20.10.3");var subQ6=sQuery(id+"F3.wireOp",EDGE,"E20.10.2");var subQ7=sQuery(id+"F3.wireOp",EDGE,"E20.10.1");var subQ8=makeQuery(id+"F25.opLoft","SWEPT_FACE",FACE,{"disambiguationData":[OSD([subQ7,subQ6,subQ5,sQuery(id+"F22.wireOp",EDGE,"E28.2.0"),sQuery(id+"F22.wireOp",EDGE,"E28.2.2"),sQuery(id+"F22.wireOp",EDGE,"E28.2.3")])]});var subQ9=makeQuery(id+"F40.opExtrude","CAP_FACE",FACE,{"disambiguationData":[OSD([sQuery(id+"F39.wireOp",EDGE,"E29"),sQuery(id+"F39.wireOp",EDGE,"E30")])],"isStart":true});var subQ12=sQuery(id+"F4.wireOp",EDGE,"E26.10.3");var subQ13=sQuery(id+"F4.wireOp",EDGE,"E26.10.2");var subQ14=makeQuery(id+"F11.opLoft","SWEPT_FACE",FACE,{"disambiguationData":[OSD([subQ7,subQ6,subQ5,sQuery(id+"F4.wireOp",EDGE,"E26.10.1"),subQ13,subQ12])]});var subQ90=sQuery(id+"F3.wireOp",EDGE,"E18.bottom");Q31=makeQuery(id+"F44.opFillet","BLEND_EDGE",EDGE,{"blendedFrom":[makeQuery(id+"F40.boolean.opBoolean","INTERSECT",EDGE,{"derivedFrom":[subQ8,subQ9]}),makeQuery(id+"F40.boolean.opBoolean","SPLIT",FACE,{"disambiguationData":[TD([subQ0])],"derivedFrom":makeQuery(id+"F25.boolean.opBoolean","SPLIT",FACE,{"disambiguationData":[TD([subQ14])],"derivedFrom":makeQuery(id+"F24.boolean.opBoolean","SPLIT",FACE,{"disambiguationData":[TD([makeQuery(id+"F5.opLoft","CAP_FACE",FACE,{"disambiguationData":[OSD([makeQuery(id+"F3.imprint","IMPRINT",FACE,{"disambiguationData":[TD([[makeQuery(id+"F3.imprint","IMPRINT",EDGE,{"derivedFrom":subQ90}),1.0]])]})])],"isStart":true})])],"derivedFrom":makeQuery(id+"F1.opRevolve","SWEPT_FACE",FACE,{"disambiguationData":[OSD([sQuery(id+"F0.wireOp",EDGE,"E13")])]})})})})],"blendedInto":[makeQuery(id+"F40.boolean.opBoolean","SPLIT",FACE,{"disambiguationData":[TD([subQ0])],"derivedFrom":makeQuery(id+"F25.boolean.opBoolean","SPLIT",FACE,{"disambiguationData":[TD([subQ14])],"derivedFrom":makeQuery(id+"F24.boolean.opBoolean","SPLIT",FACE,{"disambiguationData":[TD([makeQuery(id+"F5.opLoft","CAP_FACE",FACE,{"disambiguationData":[OSD([makeQuery(id+"F3.imprint","IMPRINT",FACE,{"disambiguationData":[TD([[makeQuery(id+"F3.imprint","IMPRINT",EDGE,{"derivedFrom":subQ90}),1.0]])]})])],"isStart":true})])],"derivedFrom":makeQuery(id+"F1.opRevolve","SWEPT_FACE",FACE,{"disambiguationData":[OSD([sQuery(id+"F0.wireOp",EDGE,"E13")])]})})})})]});}
            var Q32;
            {var subQ0=makeQuery(id+"F1.opRevolve","SWEPT_FACE",FACE,{"disambiguationData":[OSD([sQuery(id+"F0.wireOp",EDGE,"E12")])]});var subQ1=sQuery(id+"F3.wireOp",EDGE,"E20.9.3");var subQ2=sQuery(id+"F3.wireOp",EDGE,"E20.9.2");var subQ3=sQuery(id+"F3.wireOp",EDGE,"E20.9.1");var subQ4=makeQuery(id+"F24.opLoft","SWEPT_FACE",FACE,{"disambiguationData":[OSD([subQ3,subQ2,subQ1,sQuery(id+"F22.wireOp",EDGE,"E28.1.0"),sQuery(id+"F22.wireOp",EDGE,"E28.1.2"),sQuery(id+"F22.wireOp",EDGE,"E28.1.3")])]});var subQ9=makeQuery(id+"F40.opExtrude","CAP_FACE",FACE,{"disambiguationData":[OSD([sQuery(id+"F39.wireOp",EDGE,"E29"),sQuery(id+"F39.wireOp",EDGE,"E30")])],"isStart":true});Q32=makeQuery(id+"F44.opFillet","BLEND_EDGE",EDGE,{"blendedFrom":[makeQuery(id+"F40.boolean.opBoolean","INTERSECT",EDGE,{"derivedFrom":[subQ4,subQ9]}),makeQuery(id+"F40.boolean.opBoolean","SPLIT",FACE,{"disambiguationData":[TD([subQ0])],"derivedFrom":makeQuery(id+"F24.boolean.opBoolean","SPLIT",FACE,{"disambiguationData":[TD([makeQuery(id+"F12.opLoft","SWEPT_FACE",FACE,{"disambiguationData":[OSD([subQ3,subQ2,subQ1,sQuery(id+"F4.wireOp",EDGE,"E26.9.1"),sQuery(id+"F4.wireOp",EDGE,"E26.9.2"),sQuery(id+"F4.wireOp",EDGE,"E26.9.3")])]})])],"derivedFrom":makeQuery(id+"F1.opRevolve","SWEPT_FACE",FACE,{"disambiguationData":[OSD([sQuery(id+"F0.wireOp",EDGE,"E13")])]})})})],"blendedInto":[makeQuery(id+"F40.boolean.opBoolean","SPLIT",FACE,{"disambiguationData":[TD([subQ0])],"derivedFrom":makeQuery(id+"F24.boolean.opBoolean","SPLIT",FACE,{"disambiguationData":[TD([makeQuery(id+"F12.opLoft","SWEPT_FACE",FACE,{"disambiguationData":[OSD([subQ3,subQ2,subQ1,sQuery(id+"F4.wireOp",EDGE,"E26.9.1"),sQuery(id+"F4.wireOp",EDGE,"E26.9.2"),sQuery(id+"F4.wireOp",EDGE,"E26.9.3")])]})])],"derivedFrom":makeQuery(id+"F1.opRevolve","SWEPT_FACE",FACE,{"disambiguationData":[OSD([sQuery(id+"F0.wireOp",EDGE,"E13")])]})})})]});}
            fillet(context, id + "F48", {"entities" : qUnion([Q0, Q1, Q2, Q3, Q4, Q5, Q6, Q7, Q8, Q9, Q10, Q11, Q12, Q13, Q14, Q15, Q16, Q17, Q18, Q19, Q20, Q21, Q22, Q23, Q24, Q25, Q26, Q27, Q28, Q29, Q30, Q31, Q32]), "radius" : 3 * mm, "tangentPropagation" : true, "allowEdgeOverflow" : false});
        }
        {
            var Q0;
            {var subQ0=sQuery(id+"F41.wireOp",EDGE,"E34");var subQ1=sQuery(id+"F41.wireOp",EDGE,"E32");Q0=makeQuery(id+"F42.boolean.opBoolean","INTERSECT",EDGE,{"derivedFrom":[makeQuery(id+"F35.opLoft","SWEPT_FACE",FACE,{"disambiguationData":[OSD([sQuery(id+"F3.wireOp",EDGE,"E20.4.0"),sQuery(id+"F3.wireOp",EDGE,"E20.4.1"),sQuery(id+"F3.wireOp",EDGE,"E20.4.3"),sQuery(id+"F22.wireOp",EDGE,"E28.12.1"),sQuery(id+"F22.wireOp",EDGE,"E28.12.2"),sQuery(id+"F22.wireOp",EDGE,"E28.12.3")])]}),makeQuery(id+"F42.opRevolve","SWEPT_FACE",FACE,{"disambiguationData":[OSD([subQ1]),TDD([makeQuery(id+"F41.imprint","IMPRINT",EDGE,{"disambiguationData":[TD([[makeQuery(id+"F41.imprint","INTERSECT",VERTEX,{"disambiguationData":[OD(0.0)],"derivedFrom":[subQ1,subQ0]}),-1.0]])],"derivedFrom":subQ1})])]})]});}
            var Q1;
            {var subQ0=sQuery(id+"F22.wireOp",EDGE,"E28.12.3");var subQ1=sQuery(id+"F22.wireOp",EDGE,"E28.12.2");var subQ2=sQuery(id+"F22.wireOp",EDGE,"E28.12.0");var subQ3=sQuery(id+"F3.wireOp",EDGE,"E20.4.3");var subQ4=sQuery(id+"F3.wireOp",EDGE,"E20.4.1");var subQ5=makeQuery(id+"F35.opLoft","SWEPT_FACE",FACE,{"disambiguationData":[OSD([subQ4,sQuery(id+"F3.wireOp",EDGE,"E20.4.2"),subQ3,subQ2,subQ1,subQ0])]});var subQ6=sQuery(id+"F22.wireOp",EDGE,"E28.12.1");var subQ7=sQuery(id+"F41.wireOp",EDGE,"E34");var subQ8=sQuery(id+"F41.wireOp",EDGE,"E32");Q1=makeQuery(id+"F44.opFillet","BLEND_EDGE",EDGE,{"blendedFrom":[makeQuery(id+"F40.boolean.opBoolean","INTERSECT",EDGE,{"derivedFrom":[subQ5,makeQuery(id+"F40.opExtrude","CAP_FACE",FACE,{"disambiguationData":[OSD([sQuery(id+"F39.wireOp",EDGE,"E29"),sQuery(id+"F39.wireOp",EDGE,"E30")])],"isStart":true})]}),makeQuery(id+"F42.boolean.opBoolean","COPY",FACE,{"disambiguationData":[TD([makeQuery(id+"F35.opLoft","SWEPT_FACE",FACE,{"disambiguationData":[OSD([sQuery(id+"F3.wireOp",EDGE,"E20.4.0"),subQ4,subQ3,subQ6,subQ1,subQ0])]})])],"derivedFrom":makeQuery(id+"F42.opRevolve","SWEPT_FACE",FACE,{"disambiguationData":[OSD([subQ8]),TDD([makeQuery(id+"F41.imprint","IMPRINT",EDGE,{"disambiguationData":[TD([[makeQuery(id+"F41.imprint","INTERSECT",VERTEX,{"disambiguationData":[OD(0.0)],"derivedFrom":[subQ8,subQ7]}),-1.0]])],"derivedFrom":subQ8})])]})})],"blendedInto":[makeQuery(id+"F42.boolean.opBoolean","COPY",FACE,{"disambiguationData":[TD([makeQuery(id+"F35.opLoft","SWEPT_FACE",FACE,{"disambiguationData":[OSD([sQuery(id+"F3.wireOp",EDGE,"E20.4.0"),subQ4,subQ3,subQ6,subQ1,subQ0])]})])],"derivedFrom":makeQuery(id+"F42.opRevolve","SWEPT_FACE",FACE,{"disambiguationData":[OSD([subQ8]),TDD([makeQuery(id+"F41.imprint","IMPRINT",EDGE,{"disambiguationData":[TD([[makeQuery(id+"F41.imprint","INTERSECT",VERTEX,{"disambiguationData":[OD(0.0)],"derivedFrom":[subQ8,subQ7]}),-1.0]])],"derivedFrom":subQ8})])]})})]});}
            var Q2;
            {var subQ0=sQuery(id+"F41.wireOp",EDGE,"E37");var subQ1=makeQuery(id+"F42.opRevolve","SWEPT_FACE",FACE,{"disambiguationData":[OSD([subQ0])]});var subQ2=makeQuery(id+"F40.opExtrude","CAP_FACE",FACE,{"disambiguationData":[OSD([sQuery(id+"F39.wireOp",EDGE,"E29"),sQuery(id+"F39.wireOp",EDGE,"E30")])],"isStart":true});var subQ3=sQuery(id+"F22.wireOp",EDGE,"E28.15.3");var subQ4=sQuery(id+"F22.wireOp",EDGE,"E28.15.2");var subQ5=sQuery(id+"F3.wireOp",EDGE,"E20.7.3");var subQ7=sQuery(id+"F3.wireOp",EDGE,"E20.7.1");var subQ8=sQuery(id+"F3.wireOp",EDGE,"E20.7.0");var subQ9=sQuery(id+"F41.wireOp",EDGE,"E38");var subQ10=makeQuery(id+"F42.opRevolve","SWEPT_FACE",FACE,{"disambiguationData":[OSD([subQ9])]});var subQ11=makeQuery(id+"F42.opRevolve","SWEPT_EDGE",EDGE,{"disambiguationData":[OSD([subQ0,subQ9])]});var subQ12=sQuery(id+"F22.wireOp",EDGE,"E28.14.3");var subQ13=sQuery(id+"F22.wireOp",EDGE,"E28.14.2");var subQ14=sQuery(id+"F3.wireOp",EDGE,"E20.6.3");var subQ15=sQuery(id+"F3.wireOp",EDGE,"E20.6.1");var subQ16=sQuery(id+"F3.wireOp",EDGE,"E20.6.0");var subQ18=sQuery(id+"F22.wireOp",EDGE,"E28.13.3");var subQ19=sQuery(id+"F22.wireOp",EDGE,"E28.13.2");var subQ20=sQuery(id+"F3.wireOp",EDGE,"E20.5.3");var subQ22=sQuery(id+"F3.wireOp",EDGE,"E20.5.1");var subQ23=sQuery(id+"F3.wireOp",EDGE,"E20.5.0");var subQ24=sQuery(id+"F22.wireOp",EDGE,"E28.12.3");var subQ25=sQuery(id+"F22.wireOp",EDGE,"E28.12.2");var subQ26=sQuery(id+"F3.wireOp",EDGE,"E20.4.3");var subQ28=sQuery(id+"F3.wireOp",EDGE,"E20.4.1");var subQ30=sQuery(id+"F3.wireOp",EDGE,"E20.4.0");var subQ31=makeQuery(id+"F35.opLoft","SWEPT_FACE",FACE,{"disambiguationData":[OSD([subQ30,subQ28,subQ26,sQuery(id+"F22.wireOp",EDGE,"E28.12.1"),subQ25,subQ24])]});var subQ32=sQuery(id+"F22.wireOp",EDGE,"E28.11.3");var subQ33=sQuery(id+"F22.wireOp",EDGE,"E28.11.2");var subQ34=sQuery(id+"F3.wireOp",EDGE,"E20.3.3");var subQ36=sQuery(id+"F3.wireOp",EDGE,"E20.3.1");var subQ37=sQuery(id+"F3.wireOp",EDGE,"E20.3.0");var subQ38=makeQuery(id+"F34.opLoft","SWEPT_FACE",FACE,{"disambiguationData":[OSD([subQ37,subQ36,subQ34,sQuery(id+"F22.wireOp",EDGE,"E28.11.1"),subQ33,subQ32])]});var subQ39=sQuery(id+"F22.wireOp",EDGE,"E28.10.3");var subQ40=sQuery(id+"F22.wireOp",EDGE,"E28.10.2");var subQ41=sQuery(id+"F3.wireOp",EDGE,"E20.2.3");var subQ43=sQuery(id+"F3.wireOp",EDGE,"E20.2.1");var subQ44=sQuery(id+"F3.wireOp",EDGE,"E20.2.0");var subQ45=makeQuery(id+"F33.opLoft","SWEPT_FACE",FACE,{"disambiguationData":[OSD([subQ44,subQ43,subQ41,sQuery(id+"F22.wireOp",EDGE,"E28.10.1"),subQ40,subQ39])]});var subQ46=sQuery(id+"F22.wireOp",EDGE,"E28.9.3");var subQ47=sQuery(id+"F22.wireOp",EDGE,"E28.9.2");var subQ48=sQuery(id+"F3.wireOp",EDGE,"E20.1.3");var subQ50=sQuery(id+"F3.wireOp",EDGE,"E20.1.1");var subQ51=sQuery(id+"F3.wireOp",EDGE,"E20.1.0");var subQ52=makeQuery(id+"F32.opLoft","SWEPT_FACE",FACE,{"disambiguationData":[OSD([subQ51,subQ50,subQ48,sQuery(id+"F22.wireOp",EDGE,"E28.9.1"),subQ47,subQ46])]});var subQ53=sQuery(id+"F22.wireOp",EDGE,"E28.8.3");var subQ54=sQuery(id+"F22.wireOp",EDGE,"E28.8.2");var subQ56=sQuery(id+"F3.wireOp",EDGE,"E18.top");var subQ57=sQuery(id+"F3.wireOp",EDGE,"E18.bottom");var subQ58=sQuery(id+"F3.wireOp",EDGE,"E18.left");var subQ59=makeQuery(id+"F31.opLoft","SWEPT_FACE",FACE,{"disambiguationData":[OSD([subQ57,subQ56,subQ58,sQuery(id+"F22.wireOp",EDGE,"E28.8.1"),subQ54,subQ53])]});var subQ60=sQuery(id+"F22.wireOp",EDGE,"E28.7.3");var subQ61=sQuery(id+"F22.wireOp",EDGE,"E28.7.2");var subQ62=sQuery(id+"F3.wireOp",EDGE,"E20.15.3");var subQ63=sQuery(id+"F3.wireOp",EDGE,"E20.15.1");var subQ64=sQuery(id+"F3.wireOp",EDGE,"E20.15.0");var subQ65=makeQuery(id+"F30.opLoft","SWEPT_FACE",FACE,{"disambiguationData":[OSD([subQ64,subQ63,subQ62,sQuery(id+"F22.wireOp",EDGE,"E28.7.1"),subQ61,subQ60])]});var subQ67=sQuery(id+"F22.wireOp",EDGE,"E28.6.3");var subQ68=sQuery(id+"F22.wireOp",EDGE,"E28.6.2");var subQ69=sQuery(id+"F3.wireOp",EDGE,"E20.14.3");var subQ71=sQuery(id+"F3.wireOp",EDGE,"E20.14.1");var subQ72=sQuery(id+"F3.wireOp",EDGE,"E20.14.0");var subQ73=makeQuery(id+"F29.opLoft","SWEPT_FACE",FACE,{"disambiguationData":[OSD([subQ72,subQ71,subQ69,sQuery(id+"F22.wireOp",EDGE,"E28.6.1"),subQ68,subQ67])]});var subQ74=sQuery(id+"F22.wireOp",EDGE,"E28.5.3");var subQ75=sQuery(id+"F22.wireOp",EDGE,"E28.5.2");var subQ76=sQuery(id+"F3.wireOp",EDGE,"E20.13.3");var subQ78=sQuery(id+"F3.wireOp",EDGE,"E20.13.1");var subQ79=sQuery(id+"F3.wireOp",EDGE,"E20.13.0");var subQ80=makeQuery(id+"F28.opLoft","SWEPT_FACE",FACE,{"disambiguationData":[OSD([subQ79,subQ78,subQ76,sQuery(id+"F22.wireOp",EDGE,"E28.5.1"),subQ75,subQ74])]});var subQ81=sQuery(id+"F22.wireOp",EDGE,"E28.4.3");var subQ82=sQuery(id+"F22.wireOp",EDGE,"E28.4.2");var subQ83=sQuery(id+"F3.wireOp",EDGE,"E20.12.3");var subQ85=sQuery(id+"F3.wireOp",EDGE,"E20.12.1");var subQ86=sQuery(id+"F3.wireOp",EDGE,"E20.12.0");var subQ87=makeQuery(id+"F27.opLoft","SWEPT_FACE",FACE,{"disambiguationData":[OSD([subQ86,subQ85,subQ83,sQuery(id+"F22.wireOp",EDGE,"E28.4.1"),subQ82,subQ81])]});var subQ88=sQuery(id+"F22.wireOp",EDGE,"E28.3.3");var subQ89=sQuery(id+"F22.wireOp",EDGE,"E28.3.2");var subQ90=sQuery(id+"F3.wireOp",EDGE,"E20.11.3");var subQ92=sQuery(id+"F3.wireOp",EDGE,"E20.11.1");var subQ93=sQuery(id+"F3.wireOp",EDGE,"E20.11.0");var subQ94=makeQuery(id+"F26.opLoft","SWEPT_FACE",FACE,{"disambiguationData":[OSD([subQ93,subQ92,subQ90,sQuery(id+"F22.wireOp",EDGE,"E28.3.1"),subQ89,subQ88])]});var subQ95=sQuery(id+"F22.wireOp",EDGE,"E28.2.3");var subQ96=sQuery(id+"F22.wireOp",EDGE,"E28.2.2");var subQ97=sQuery(id+"F3.wireOp",EDGE,"E20.10.3");var subQ98=sQuery(id+"F3.wireOp",EDGE,"E20.10.1");var subQ99=sQuery(id+"F3.wireOp",EDGE,"E20.10.0");var subQ100=makeQuery(id+"F25.opLoft","SWEPT_FACE",FACE,{"disambiguationData":[OSD([subQ99,subQ98,subQ97,sQuery(id+"F22.wireOp",EDGE,"E28.2.1"),subQ96,subQ95])]});var subQ102=sQuery(id+"F22.wireOp",EDGE,"E28.1.3");var subQ103=sQuery(id+"F22.wireOp",EDGE,"E28.1.2");var subQ104=sQuery(id+"F3.wireOp",EDGE,"E20.9.3");var subQ105=sQuery(id+"F3.wireOp",EDGE,"E20.9.1");var subQ106=sQuery(id+"F3.wireOp",EDGE,"E20.9.0");var subQ107=makeQuery(id+"F24.opLoft","SWEPT_FACE",FACE,{"disambiguationData":[OSD([subQ106,subQ105,subQ104,sQuery(id+"F22.wireOp",EDGE,"E28.1.1"),subQ103,subQ102])]});var subQ108=sQuery(id+"F22.wireOp",EDGE,"E27.top");var subQ109=sQuery(id+"F22.wireOp",EDGE,"E27.bottom");var subQ110=sQuery(id+"F3.wireOp",EDGE,"E20.8.3");var subQ112=sQuery(id+"F3.wireOp",EDGE,"E20.8.1");var subQ116=makeQuery(id+"F42.boolean.opBoolean","COPY",FACE,{"disambiguationData":[TD([subQ31])],"derivedFrom":subQ10});var subQ125=makeQuery(id+"F14.opLoft","CAP_FACE",FACE,{"disambiguationData":[OSD([makeQuery(id+"F3.imprint","IMPRINT",FACE,{"disambiguationData":[TD([[makeQuery(id+"F3.imprint","IMPRINT",EDGE,{"derivedFrom":subQ8}),-1.0]])]})])],"isStart":true});var subQ159=makeQuery(id+"F5.opLoft","CAP_FACE",FACE,{"disambiguationData":[OSD([makeQuery(id+"F3.imprint","IMPRINT",FACE,{"disambiguationData":[TD([[makeQuery(id+"F3.imprint","IMPRINT",EDGE,{"derivedFrom":subQ57}),1.0]])]})])],"isStart":true});var subQ188=makeQuery(id+"F35.boolean.opBoolean","INTERSECT",EDGE,{"derivedFrom":[makeQuery(id+"F34.boolean.opBoolean","SPLIT",FACE,{"disambiguationData":[TD([subQ125])],"derivedFrom":makeQuery(id+"F33.boolean.opBoolean","SPLIT",FACE,{"disambiguationData":[TD([subQ125])],"derivedFrom":makeQuery(id+"F32.boolean.opBoolean","SPLIT",FACE,{"disambiguationData":[TD([subQ125])],"derivedFrom":makeQuery(id+"F31.boolean.opBoolean","SPLIT",FACE,{"disambiguationData":[TD([subQ125])],"derivedFrom":makeQuery(id+"F30.boolean.opBoolean","SPLIT",FACE,{"disambiguationData":[TD([subQ159])],"derivedFrom":makeQuery(id+"F29.boolean.opBoolean","SPLIT",FACE,{"disambiguationData":[TD([subQ159])],"derivedFrom":makeQuery(id+"F28.boolean.opBoolean","SPLIT",FACE,{"disambiguationData":[TD([subQ159])],"derivedFrom":makeQuery(id+"F27.boolean.opBoolean","SPLIT",FACE,{"disambiguationData":[TD([subQ159])],"derivedFrom":makeQuery(id+"F26.boolean.opBoolean","SPLIT",FACE,{"disambiguationData":[TD([subQ159])],"derivedFrom":makeQuery(id+"F25.boolean.opBoolean","SPLIT",FACE,{"disambiguationData":[TD([subQ159])],"derivedFrom":makeQuery(id+"F24.boolean.opBoolean","SPLIT",FACE,{"disambiguationData":[TD([subQ159])],"derivedFrom":makeQuery(id+"F1.opRevolve","SWEPT_FACE",FACE,{"disambiguationData":[OSD([sQuery(id+"F0.wireOp",EDGE,"E13")])]})})})})})})})})})})})}),subQ31]});Q2=makeQuery(id+"F48.opFillet","BLEND_EDGE",EDGE,{"blendedFrom":[makeQuery(id+"F47.opFillet","TWEAK_EDGE",EDGE,{"derivedFrom":[makeQuery(id+"F45.opFillet","BLEND_VERTEX",VERTEX,{"blendedFrom":[subQ188,subQ31,subQ116],"blendedInto":[subQ31,subQ116]}),makeQuery(id+"F45.opFillet","BLEND_VERTEX",VERTEX,{"blendedFrom":[subQ188,makeQuery(id+"F42.boolean.opBoolean","MERGE",FACE,{"derivedFrom":[subQ2,subQ1]}),subQ116],"blendedInto":[makeQuery(id+"F42.boolean.opBoolean","MERGE",FACE,{"derivedFrom":[subQ2,subQ1]}),subQ116]})]}),makeQuery(id+"F47.opFillet","BLEND_FACE",FACE,{"disambiguationData":[OSD([subQ0,subQ9]),TDD([makeQuery(id+"F42.boolean.opBoolean","COPY",EDGE,{"disambiguationData":[TD([makeQuery(id+"F23.opLoft","SWEPT_FACE",FACE,{"disambiguationData":[OSD([sQuery(id+"F3.wireOp",EDGE,"E20.8.0"),subQ112,subQ110,subQ109,subQ108,sQuery(id+"F22.wireOp",EDGE,"E27.right")])]})])],"derivedFrom":subQ11})])]}),makeQuery(id+"F47.opFillet","BLEND_FACE",FACE,{"disambiguationData":[OSD([subQ0,subQ9]),TDD([makeQuery(id+"F42.boolean.opBoolean","COPY",EDGE,{"disambiguationData":[TD([subQ107])],"derivedFrom":subQ11})])]}),makeQuery(id+"F47.opFillet","BLEND_FACE",FACE,{"disambiguationData":[OSD([subQ0,subQ9]),TDD([makeQuery(id+"F42.boolean.opBoolean","COPY",EDGE,{"disambiguationData":[TD([subQ100])],"derivedFrom":subQ11})])]}),makeQuery(id+"F47.opFillet","BLEND_FACE",FACE,{"disambiguationData":[OSD([subQ0,subQ9]),TDD([makeQuery(id+"F42.boolean.opBoolean","COPY",EDGE,{"disambiguationData":[TD([subQ94])],"derivedFrom":subQ11})])]}),makeQuery(id+"F47.opFillet","BLEND_FACE",FACE,{"disambiguationData":[OSD([subQ0,subQ9]),TDD([makeQuery(id+"F42.boolean.opBoolean","COPY",EDGE,{"disambiguationData":[TD([subQ87])],"derivedFrom":subQ11})])]}),makeQuery(id+"F47.opFillet","BLEND_FACE",FACE,{"disambiguationData":[OSD([subQ0,subQ9]),TDD([makeQuery(id+"F42.boolean.opBoolean","COPY",EDGE,{"disambiguationData":[TD([subQ80])],"derivedFrom":subQ11})])]}),makeQuery(id+"F47.opFillet","BLEND_FACE",FACE,{"disambiguationData":[OSD([subQ0,subQ9]),TDD([makeQuery(id+"F42.boolean.opBoolean","COPY",EDGE,{"disambiguationData":[TD([subQ73])],"derivedFrom":subQ11})])]}),makeQuery(id+"F47.opFillet","BLEND_FACE",FACE,{"disambiguationData":[OSD([subQ0,subQ9]),TDD([makeQuery(id+"F42.boolean.opBoolean","COPY",EDGE,{"disambiguationData":[TD([subQ65])],"derivedFrom":subQ11})])]}),makeQuery(id+"F47.opFillet","BLEND_FACE",FACE,{"disambiguationData":[OSD([subQ0,subQ9]),TDD([makeQuery(id+"F42.boolean.opBoolean","COPY",EDGE,{"disambiguationData":[TD([subQ59])],"derivedFrom":subQ11})])]}),makeQuery(id+"F47.opFillet","BLEND_FACE",FACE,{"disambiguationData":[OSD([subQ0,subQ9]),TDD([makeQuery(id+"F42.boolean.opBoolean","COPY",EDGE,{"disambiguationData":[TD([subQ52])],"derivedFrom":subQ11})])]}),makeQuery(id+"F47.opFillet","BLEND_FACE",FACE,{"disambiguationData":[OSD([subQ0,subQ9]),TDD([makeQuery(id+"F42.boolean.opBoolean","COPY",EDGE,{"disambiguationData":[TD([subQ45])],"derivedFrom":subQ11})])]}),makeQuery(id+"F47.opFillet","BLEND_FACE",FACE,{"disambiguationData":[OSD([subQ0,subQ9]),TDD([makeQuery(id+"F42.boolean.opBoolean","COPY",EDGE,{"disambiguationData":[TD([subQ38])],"derivedFrom":subQ11})])]}),makeQuery(id+"F47.opFillet","BLEND_FACE",FACE,{"disambiguationData":[OSD([subQ0,subQ9]),TDD([makeQuery(id+"F42.boolean.opBoolean","COPY",EDGE,{"disambiguationData":[TD([subQ31])],"derivedFrom":subQ11})])]}),makeQuery(id+"F47.opFillet","BLEND_FACE",FACE,{"disambiguationData":[OSD([subQ0,subQ9]),TDD([makeQuery(id+"F42.boolean.opBoolean","COPY",EDGE,{"disambiguationData":[TD([makeQuery(id+"F36.opLoft","SWEPT_FACE",FACE,{"disambiguationData":[OSD([subQ23,subQ22,subQ20,sQuery(id+"F22.wireOp",EDGE,"E28.13.1"),subQ19,subQ18])]})])],"derivedFrom":subQ11})])]}),makeQuery(id+"F47.opFillet","BLEND_FACE",FACE,{"disambiguationData":[OSD([subQ0,subQ9]),TDD([makeQuery(id+"F42.boolean.opBoolean","COPY",EDGE,{"disambiguationData":[TD([makeQuery(id+"F37.opLoft","SWEPT_FACE",FACE,{"disambiguationData":[OSD([subQ16,subQ15,subQ14,sQuery(id+"F22.wireOp",EDGE,"E28.14.1"),subQ13,subQ12])]})])],"derivedFrom":subQ11})])]}),makeQuery(id+"F47.opFillet","BLEND_FACE",FACE,{"disambiguationData":[OSD([subQ0,subQ9]),TDD([makeQuery(id+"F42.boolean.opBoolean","COPY",EDGE,{"disambiguationData":[TD([makeQuery(id+"F38.opLoft","SWEPT_FACE",FACE,{"disambiguationData":[OSD([subQ8,subQ7,subQ5,sQuery(id+"F22.wireOp",EDGE,"E28.15.1"),subQ4,subQ3])]})])],"derivedFrom":subQ11})])]})],"blendedInto":[makeQuery(id+"F47.opFillet","BLEND_FACE",FACE,{"disambiguationData":[OSD([subQ0,subQ9]),TDD([makeQuery(id+"F42.boolean.opBoolean","COPY",EDGE,{"disambiguationData":[TD([makeQuery(id+"F23.opLoft","SWEPT_FACE",FACE,{"disambiguationData":[OSD([sQuery(id+"F3.wireOp",EDGE,"E20.8.0"),subQ112,subQ110,subQ109,subQ108,sQuery(id+"F22.wireOp",EDGE,"E27.right")])]})])],"derivedFrom":subQ11})])]}),makeQuery(id+"F47.opFillet","BLEND_FACE",FACE,{"disambiguationData":[OSD([subQ0,subQ9]),TDD([makeQuery(id+"F42.boolean.opBoolean","COPY",EDGE,{"disambiguationData":[TD([subQ107])],"derivedFrom":subQ11})])]}),makeQuery(id+"F47.opFillet","BLEND_FACE",FACE,{"disambiguationData":[OSD([subQ0,subQ9]),TDD([makeQuery(id+"F42.boolean.opBoolean","COPY",EDGE,{"disambiguationData":[TD([subQ100])],"derivedFrom":subQ11})])]}),makeQuery(id+"F47.opFillet","BLEND_FACE",FACE,{"disambiguationData":[OSD([subQ0,subQ9]),TDD([makeQuery(id+"F42.boolean.opBoolean","COPY",EDGE,{"disambiguationData":[TD([subQ94])],"derivedFrom":subQ11})])]}),makeQuery(id+"F47.opFillet","BLEND_FACE",FACE,{"disambiguationData":[OSD([subQ0,subQ9]),TDD([makeQuery(id+"F42.boolean.opBoolean","COPY",EDGE,{"disambiguationData":[TD([subQ87])],"derivedFrom":subQ11})])]}),makeQuery(id+"F47.opFillet","BLEND_FACE",FACE,{"disambiguationData":[OSD([subQ0,subQ9]),TDD([makeQuery(id+"F42.boolean.opBoolean","COPY",EDGE,{"disambiguationData":[TD([subQ80])],"derivedFrom":subQ11})])]}),makeQuery(id+"F47.opFillet","BLEND_FACE",FACE,{"disambiguationData":[OSD([subQ0,subQ9]),TDD([makeQuery(id+"F42.boolean.opBoolean","COPY",EDGE,{"disambiguationData":[TD([subQ73])],"derivedFrom":subQ11})])]}),makeQuery(id+"F47.opFillet","BLEND_FACE",FACE,{"disambiguationData":[OSD([subQ0,subQ9]),TDD([makeQuery(id+"F42.boolean.opBoolean","COPY",EDGE,{"disambiguationData":[TD([subQ65])],"derivedFrom":subQ11})])]}),makeQuery(id+"F47.opFillet","BLEND_FACE",FACE,{"disambiguationData":[OSD([subQ0,subQ9]),TDD([makeQuery(id+"F42.boolean.opBoolean","COPY",EDGE,{"disambiguationData":[TD([subQ59])],"derivedFrom":subQ11})])]}),makeQuery(id+"F47.opFillet","BLEND_FACE",FACE,{"disambiguationData":[OSD([subQ0,subQ9]),TDD([makeQuery(id+"F42.boolean.opBoolean","COPY",EDGE,{"disambiguationData":[TD([subQ52])],"derivedFrom":subQ11})])]}),makeQuery(id+"F47.opFillet","BLEND_FACE",FACE,{"disambiguationData":[OSD([subQ0,subQ9]),TDD([makeQuery(id+"F42.boolean.opBoolean","COPY",EDGE,{"disambiguationData":[TD([subQ45])],"derivedFrom":subQ11})])]}),makeQuery(id+"F47.opFillet","BLEND_FACE",FACE,{"disambiguationData":[OSD([subQ0,subQ9]),TDD([makeQuery(id+"F42.boolean.opBoolean","COPY",EDGE,{"disambiguationData":[TD([subQ38])],"derivedFrom":subQ11})])]}),makeQuery(id+"F47.opFillet","BLEND_FACE",FACE,{"disambiguationData":[OSD([subQ0,subQ9]),TDD([makeQuery(id+"F42.boolean.opBoolean","COPY",EDGE,{"disambiguationData":[TD([subQ31])],"derivedFrom":subQ11})])]}),makeQuery(id+"F47.opFillet","BLEND_FACE",FACE,{"disambiguationData":[OSD([subQ0,subQ9]),TDD([makeQuery(id+"F42.boolean.opBoolean","COPY",EDGE,{"disambiguationData":[TD([makeQuery(id+"F36.opLoft","SWEPT_FACE",FACE,{"disambiguationData":[OSD([subQ23,subQ22,subQ20,sQuery(id+"F22.wireOp",EDGE,"E28.13.1"),subQ19,subQ18])]})])],"derivedFrom":subQ11})])]}),makeQuery(id+"F47.opFillet","BLEND_FACE",FACE,{"disambiguationData":[OSD([subQ0,subQ9]),TDD([makeQuery(id+"F42.boolean.opBoolean","COPY",EDGE,{"disambiguationData":[TD([makeQuery(id+"F37.opLoft","SWEPT_FACE",FACE,{"disambiguationData":[OSD([subQ16,subQ15,subQ14,sQuery(id+"F22.wireOp",EDGE,"E28.14.1"),subQ13,subQ12])]})])],"derivedFrom":subQ11})])]}),makeQuery(id+"F47.opFillet","BLEND_FACE",FACE,{"disambiguationData":[OSD([subQ0,subQ9]),TDD([makeQuery(id+"F42.boolean.opBoolean","COPY",EDGE,{"disambiguationData":[TD([makeQuery(id+"F38.opLoft","SWEPT_FACE",FACE,{"disambiguationData":[OSD([subQ8,subQ7,subQ5,sQuery(id+"F22.wireOp",EDGE,"E28.15.1"),subQ4,subQ3])]})])],"derivedFrom":subQ11})])]})]});}
            var Q3;
            {var subQ0=sQuery(id+"F22.wireOp",EDGE,"E28.13.3");var subQ1=sQuery(id+"F22.wireOp",EDGE,"E28.13.2");var subQ2=sQuery(id+"F22.wireOp",EDGE,"E28.13.0");var subQ3=sQuery(id+"F3.wireOp",EDGE,"E20.5.3");var subQ4=sQuery(id+"F3.wireOp",EDGE,"E20.5.1");var subQ5=makeQuery(id+"F36.opLoft","SWEPT_FACE",FACE,{"disambiguationData":[OSD([subQ4,sQuery(id+"F3.wireOp",EDGE,"E20.5.2"),subQ3,subQ2,subQ1,subQ0])]});var subQ6=sQuery(id+"F22.wireOp",EDGE,"E28.13.1");var subQ7=sQuery(id+"F41.wireOp",EDGE,"E34");var subQ8=sQuery(id+"F41.wireOp",EDGE,"E32");Q3=makeQuery(id+"F44.opFillet","BLEND_EDGE",EDGE,{"blendedFrom":[makeQuery(id+"F40.boolean.opBoolean","INTERSECT",EDGE,{"derivedFrom":[subQ5,makeQuery(id+"F40.opExtrude","CAP_FACE",FACE,{"disambiguationData":[OSD([sQuery(id+"F39.wireOp",EDGE,"E29"),sQuery(id+"F39.wireOp",EDGE,"E30")])],"isStart":true})]}),makeQuery(id+"F42.boolean.opBoolean","COPY",FACE,{"disambiguationData":[TD([makeQuery(id+"F36.opLoft","SWEPT_FACE",FACE,{"disambiguationData":[OSD([sQuery(id+"F3.wireOp",EDGE,"E20.5.0"),subQ4,subQ3,subQ6,subQ1,subQ0])]})])],"derivedFrom":makeQuery(id+"F42.opRevolve","SWEPT_FACE",FACE,{"disambiguationData":[OSD([subQ8]),TDD([makeQuery(id+"F41.imprint","IMPRINT",EDGE,{"disambiguationData":[TD([[makeQuery(id+"F41.imprint","INTERSECT",VERTEX,{"disambiguationData":[OD(0.0)],"derivedFrom":[subQ8,subQ7]}),-1.0]])],"derivedFrom":subQ8})])]})})],"blendedInto":[makeQuery(id+"F42.boolean.opBoolean","COPY",FACE,{"disambiguationData":[TD([makeQuery(id+"F36.opLoft","SWEPT_FACE",FACE,{"disambiguationData":[OSD([sQuery(id+"F3.wireOp",EDGE,"E20.5.0"),subQ4,subQ3,subQ6,subQ1,subQ0])]})])],"derivedFrom":makeQuery(id+"F42.opRevolve","SWEPT_FACE",FACE,{"disambiguationData":[OSD([subQ8]),TDD([makeQuery(id+"F41.imprint","IMPRINT",EDGE,{"disambiguationData":[TD([[makeQuery(id+"F41.imprint","INTERSECT",VERTEX,{"disambiguationData":[OD(0.0)],"derivedFrom":[subQ8,subQ7]}),-1.0]])],"derivedFrom":subQ8})])]})})]});}
            var Q4;
            {var subQ0=sQuery(id+"F41.wireOp",EDGE,"E34");var subQ1=sQuery(id+"F41.wireOp",EDGE,"E32");Q4=makeQuery(id+"F42.boolean.opBoolean","INTERSECT",EDGE,{"derivedFrom":[makeQuery(id+"F36.opLoft","SWEPT_FACE",FACE,{"disambiguationData":[OSD([sQuery(id+"F3.wireOp",EDGE,"E20.5.0"),sQuery(id+"F3.wireOp",EDGE,"E20.5.1"),sQuery(id+"F3.wireOp",EDGE,"E20.5.3"),sQuery(id+"F22.wireOp",EDGE,"E28.13.1"),sQuery(id+"F22.wireOp",EDGE,"E28.13.2"),sQuery(id+"F22.wireOp",EDGE,"E28.13.3")])]}),makeQuery(id+"F42.opRevolve","SWEPT_FACE",FACE,{"disambiguationData":[OSD([subQ1]),TDD([makeQuery(id+"F41.imprint","IMPRINT",EDGE,{"disambiguationData":[TD([[makeQuery(id+"F41.imprint","INTERSECT",VERTEX,{"disambiguationData":[OD(0.0)],"derivedFrom":[subQ1,subQ0]}),-1.0]])],"derivedFrom":subQ1})])]})]});}
            var Q5;
            {var subQ0=sQuery(id+"F41.wireOp",EDGE,"E37");var subQ1=makeQuery(id+"F42.opRevolve","SWEPT_FACE",FACE,{"disambiguationData":[OSD([subQ0])]});var subQ2=makeQuery(id+"F40.opExtrude","CAP_FACE",FACE,{"disambiguationData":[OSD([sQuery(id+"F39.wireOp",EDGE,"E29"),sQuery(id+"F39.wireOp",EDGE,"E30")])],"isStart":true});var subQ3=sQuery(id+"F22.wireOp",EDGE,"E28.15.3");var subQ4=sQuery(id+"F22.wireOp",EDGE,"E28.15.2");var subQ5=sQuery(id+"F3.wireOp",EDGE,"E20.7.3");var subQ7=sQuery(id+"F3.wireOp",EDGE,"E20.7.1");var subQ8=sQuery(id+"F3.wireOp",EDGE,"E20.7.0");var subQ9=sQuery(id+"F41.wireOp",EDGE,"E38");var subQ10=makeQuery(id+"F42.opRevolve","SWEPT_FACE",FACE,{"disambiguationData":[OSD([subQ9])]});var subQ11=makeQuery(id+"F42.opRevolve","SWEPT_EDGE",EDGE,{"disambiguationData":[OSD([subQ0,subQ9])]});var subQ12=sQuery(id+"F22.wireOp",EDGE,"E28.14.3");var subQ13=sQuery(id+"F22.wireOp",EDGE,"E28.14.2");var subQ14=sQuery(id+"F3.wireOp",EDGE,"E20.6.3");var subQ15=sQuery(id+"F3.wireOp",EDGE,"E20.6.1");var subQ16=sQuery(id+"F3.wireOp",EDGE,"E20.6.0");var subQ18=sQuery(id+"F22.wireOp",EDGE,"E28.13.3");var subQ19=sQuery(id+"F22.wireOp",EDGE,"E28.13.2");var subQ20=sQuery(id+"F3.wireOp",EDGE,"E20.5.3");var subQ22=sQuery(id+"F3.wireOp",EDGE,"E20.5.1");var subQ24=sQuery(id+"F3.wireOp",EDGE,"E20.5.0");var subQ25=makeQuery(id+"F36.opLoft","SWEPT_FACE",FACE,{"disambiguationData":[OSD([subQ24,subQ22,subQ20,sQuery(id+"F22.wireOp",EDGE,"E28.13.1"),subQ19,subQ18])]});var subQ26=sQuery(id+"F22.wireOp",EDGE,"E28.12.3");var subQ27=sQuery(id+"F22.wireOp",EDGE,"E28.12.2");var subQ28=sQuery(id+"F3.wireOp",EDGE,"E20.4.3");var subQ30=sQuery(id+"F3.wireOp",EDGE,"E20.4.1");var subQ31=sQuery(id+"F3.wireOp",EDGE,"E20.4.0");var subQ32=makeQuery(id+"F35.opLoft","SWEPT_FACE",FACE,{"disambiguationData":[OSD([subQ31,subQ30,subQ28,sQuery(id+"F22.wireOp",EDGE,"E28.12.1"),subQ27,subQ26])]});var subQ33=sQuery(id+"F22.wireOp",EDGE,"E28.11.3");var subQ34=sQuery(id+"F22.wireOp",EDGE,"E28.11.2");var subQ35=sQuery(id+"F3.wireOp",EDGE,"E20.3.3");var subQ37=sQuery(id+"F3.wireOp",EDGE,"E20.3.1");var subQ38=sQuery(id+"F3.wireOp",EDGE,"E20.3.0");var subQ39=makeQuery(id+"F34.opLoft","SWEPT_FACE",FACE,{"disambiguationData":[OSD([subQ38,subQ37,subQ35,sQuery(id+"F22.wireOp",EDGE,"E28.11.1"),subQ34,subQ33])]});var subQ40=sQuery(id+"F22.wireOp",EDGE,"E28.10.3");var subQ41=sQuery(id+"F22.wireOp",EDGE,"E28.10.2");var subQ42=sQuery(id+"F3.wireOp",EDGE,"E20.2.3");var subQ44=sQuery(id+"F3.wireOp",EDGE,"E20.2.1");var subQ45=sQuery(id+"F3.wireOp",EDGE,"E20.2.0");var subQ46=makeQuery(id+"F33.opLoft","SWEPT_FACE",FACE,{"disambiguationData":[OSD([subQ45,subQ44,subQ42,sQuery(id+"F22.wireOp",EDGE,"E28.10.1"),subQ41,subQ40])]});var subQ47=sQuery(id+"F22.wireOp",EDGE,"E28.9.3");var subQ48=sQuery(id+"F22.wireOp",EDGE,"E28.9.2");var subQ49=sQuery(id+"F3.wireOp",EDGE,"E20.1.3");var subQ51=sQuery(id+"F3.wireOp",EDGE,"E20.1.1");var subQ52=sQuery(id+"F3.wireOp",EDGE,"E20.1.0");var subQ53=makeQuery(id+"F32.opLoft","SWEPT_FACE",FACE,{"disambiguationData":[OSD([subQ52,subQ51,subQ49,sQuery(id+"F22.wireOp",EDGE,"E28.9.1"),subQ48,subQ47])]});var subQ54=sQuery(id+"F22.wireOp",EDGE,"E28.8.3");var subQ55=sQuery(id+"F22.wireOp",EDGE,"E28.8.2");var subQ57=sQuery(id+"F3.wireOp",EDGE,"E18.top");var subQ58=sQuery(id+"F3.wireOp",EDGE,"E18.bottom");var subQ59=sQuery(id+"F3.wireOp",EDGE,"E18.left");var subQ60=makeQuery(id+"F31.opLoft","SWEPT_FACE",FACE,{"disambiguationData":[OSD([subQ58,subQ57,subQ59,sQuery(id+"F22.wireOp",EDGE,"E28.8.1"),subQ55,subQ54])]});var subQ61=sQuery(id+"F22.wireOp",EDGE,"E28.7.3");var subQ62=sQuery(id+"F22.wireOp",EDGE,"E28.7.2");var subQ63=sQuery(id+"F3.wireOp",EDGE,"E20.15.3");var subQ64=sQuery(id+"F3.wireOp",EDGE,"E20.15.1");var subQ65=sQuery(id+"F3.wireOp",EDGE,"E20.15.0");var subQ66=makeQuery(id+"F30.opLoft","SWEPT_FACE",FACE,{"disambiguationData":[OSD([subQ65,subQ64,subQ63,sQuery(id+"F22.wireOp",EDGE,"E28.7.1"),subQ62,subQ61])]});var subQ68=sQuery(id+"F22.wireOp",EDGE,"E28.6.3");var subQ69=sQuery(id+"F22.wireOp",EDGE,"E28.6.2");var subQ70=sQuery(id+"F3.wireOp",EDGE,"E20.14.3");var subQ72=sQuery(id+"F3.wireOp",EDGE,"E20.14.1");var subQ73=sQuery(id+"F3.wireOp",EDGE,"E20.14.0");var subQ74=makeQuery(id+"F29.opLoft","SWEPT_FACE",FACE,{"disambiguationData":[OSD([subQ73,subQ72,subQ70,sQuery(id+"F22.wireOp",EDGE,"E28.6.1"),subQ69,subQ68])]});var subQ75=sQuery(id+"F22.wireOp",EDGE,"E28.5.3");var subQ76=sQuery(id+"F22.wireOp",EDGE,"E28.5.2");var subQ77=sQuery(id+"F3.wireOp",EDGE,"E20.13.3");var subQ79=sQuery(id+"F3.wireOp",EDGE,"E20.13.1");var subQ80=sQuery(id+"F3.wireOp",EDGE,"E20.13.0");var subQ81=makeQuery(id+"F28.opLoft","SWEPT_FACE",FACE,{"disambiguationData":[OSD([subQ80,subQ79,subQ77,sQuery(id+"F22.wireOp",EDGE,"E28.5.1"),subQ76,subQ75])]});var subQ82=sQuery(id+"F22.wireOp",EDGE,"E28.4.3");var subQ83=sQuery(id+"F22.wireOp",EDGE,"E28.4.2");var subQ84=sQuery(id+"F3.wireOp",EDGE,"E20.12.3");var subQ86=sQuery(id+"F3.wireOp",EDGE,"E20.12.1");var subQ87=sQuery(id+"F3.wireOp",EDGE,"E20.12.0");var subQ88=makeQuery(id+"F27.opLoft","SWEPT_FACE",FACE,{"disambiguationData":[OSD([subQ87,subQ86,subQ84,sQuery(id+"F22.wireOp",EDGE,"E28.4.1"),subQ83,subQ82])]});var subQ89=sQuery(id+"F22.wireOp",EDGE,"E28.3.3");var subQ90=sQuery(id+"F22.wireOp",EDGE,"E28.3.2");var subQ91=sQuery(id+"F3.wireOp",EDGE,"E20.11.3");var subQ93=sQuery(id+"F3.wireOp",EDGE,"E20.11.1");var subQ94=sQuery(id+"F3.wireOp",EDGE,"E20.11.0");var subQ95=makeQuery(id+"F26.opLoft","SWEPT_FACE",FACE,{"disambiguationData":[OSD([subQ94,subQ93,subQ91,sQuery(id+"F22.wireOp",EDGE,"E28.3.1"),subQ90,subQ89])]});var subQ96=sQuery(id+"F22.wireOp",EDGE,"E28.2.3");var subQ97=sQuery(id+"F22.wireOp",EDGE,"E28.2.2");var subQ98=sQuery(id+"F3.wireOp",EDGE,"E20.10.3");var subQ99=sQuery(id+"F3.wireOp",EDGE,"E20.10.1");var subQ100=sQuery(id+"F3.wireOp",EDGE,"E20.10.0");var subQ101=makeQuery(id+"F25.opLoft","SWEPT_FACE",FACE,{"disambiguationData":[OSD([subQ100,subQ99,subQ98,sQuery(id+"F22.wireOp",EDGE,"E28.2.1"),subQ97,subQ96])]});var subQ103=sQuery(id+"F22.wireOp",EDGE,"E28.1.3");var subQ104=sQuery(id+"F22.wireOp",EDGE,"E28.1.2");var subQ105=sQuery(id+"F3.wireOp",EDGE,"E20.9.3");var subQ106=sQuery(id+"F3.wireOp",EDGE,"E20.9.1");var subQ107=sQuery(id+"F3.wireOp",EDGE,"E20.9.0");var subQ108=makeQuery(id+"F24.opLoft","SWEPT_FACE",FACE,{"disambiguationData":[OSD([subQ107,subQ106,subQ105,sQuery(id+"F22.wireOp",EDGE,"E28.1.1"),subQ104,subQ103])]});var subQ109=sQuery(id+"F22.wireOp",EDGE,"E27.top");var subQ110=sQuery(id+"F22.wireOp",EDGE,"E27.bottom");var subQ111=sQuery(id+"F3.wireOp",EDGE,"E20.8.3");var subQ113=sQuery(id+"F3.wireOp",EDGE,"E20.8.1");var subQ117=makeQuery(id+"F42.boolean.opBoolean","COPY",FACE,{"disambiguationData":[TD([subQ25])],"derivedFrom":subQ10});var subQ125=makeQuery(id+"F14.opLoft","CAP_FACE",FACE,{"disambiguationData":[OSD([makeQuery(id+"F3.imprint","IMPRINT",FACE,{"disambiguationData":[TD([[makeQuery(id+"F3.imprint","IMPRINT",EDGE,{"derivedFrom":subQ8}),-1.0]])]})])],"isStart":true});var subQ160=makeQuery(id+"F5.opLoft","CAP_FACE",FACE,{"disambiguationData":[OSD([makeQuery(id+"F3.imprint","IMPRINT",FACE,{"disambiguationData":[TD([[makeQuery(id+"F3.imprint","IMPRINT",EDGE,{"derivedFrom":subQ58}),1.0]])]})])],"isStart":true});var subQ189=makeQuery(id+"F36.boolean.opBoolean","INTERSECT",EDGE,{"derivedFrom":[makeQuery(id+"F35.boolean.opBoolean","SPLIT",FACE,{"disambiguationData":[TD([subQ125])],"derivedFrom":makeQuery(id+"F34.boolean.opBoolean","SPLIT",FACE,{"disambiguationData":[TD([subQ125])],"derivedFrom":makeQuery(id+"F33.boolean.opBoolean","SPLIT",FACE,{"disambiguationData":[TD([subQ125])],"derivedFrom":makeQuery(id+"F32.boolean.opBoolean","SPLIT",FACE,{"disambiguationData":[TD([subQ125])],"derivedFrom":makeQuery(id+"F31.boolean.opBoolean","SPLIT",FACE,{"disambiguationData":[TD([subQ125])],"derivedFrom":makeQuery(id+"F30.boolean.opBoolean","SPLIT",FACE,{"disambiguationData":[TD([subQ160])],"derivedFrom":makeQuery(id+"F29.boolean.opBoolean","SPLIT",FACE,{"disambiguationData":[TD([subQ160])],"derivedFrom":makeQuery(id+"F28.boolean.opBoolean","SPLIT",FACE,{"disambiguationData":[TD([subQ160])],"derivedFrom":makeQuery(id+"F27.boolean.opBoolean","SPLIT",FACE,{"disambiguationData":[TD([subQ160])],"derivedFrom":makeQuery(id+"F26.boolean.opBoolean","SPLIT",FACE,{"disambiguationData":[TD([subQ160])],"derivedFrom":makeQuery(id+"F25.boolean.opBoolean","SPLIT",FACE,{"disambiguationData":[TD([subQ160])],"derivedFrom":makeQuery(id+"F24.boolean.opBoolean","SPLIT",FACE,{"disambiguationData":[TD([subQ160])],"derivedFrom":makeQuery(id+"F1.opRevolve","SWEPT_FACE",FACE,{"disambiguationData":[OSD([sQuery(id+"F0.wireOp",EDGE,"E13")])]})})})})})})})})})})})})}),subQ25]});Q5=makeQuery(id+"F48.opFillet","BLEND_EDGE",EDGE,{"blendedFrom":[makeQuery(id+"F47.opFillet","TWEAK_EDGE",EDGE,{"derivedFrom":[makeQuery(id+"F45.opFillet","BLEND_VERTEX",VERTEX,{"blendedFrom":[subQ189,subQ25,subQ117],"blendedInto":[subQ25,subQ117]}),makeQuery(id+"F45.opFillet","BLEND_VERTEX",VERTEX,{"blendedFrom":[subQ189,makeQuery(id+"F42.boolean.opBoolean","MERGE",FACE,{"derivedFrom":[subQ2,subQ1]}),subQ117],"blendedInto":[makeQuery(id+"F42.boolean.opBoolean","MERGE",FACE,{"derivedFrom":[subQ2,subQ1]}),subQ117]})]}),makeQuery(id+"F47.opFillet","BLEND_FACE",FACE,{"disambiguationData":[OSD([subQ0,subQ9]),TDD([makeQuery(id+"F42.boolean.opBoolean","COPY",EDGE,{"disambiguationData":[TD([makeQuery(id+"F23.opLoft","SWEPT_FACE",FACE,{"disambiguationData":[OSD([sQuery(id+"F3.wireOp",EDGE,"E20.8.0"),subQ113,subQ111,subQ110,subQ109,sQuery(id+"F22.wireOp",EDGE,"E27.right")])]})])],"derivedFrom":subQ11})])]}),makeQuery(id+"F47.opFillet","BLEND_FACE",FACE,{"disambiguationData":[OSD([subQ0,subQ9]),TDD([makeQuery(id+"F42.boolean.opBoolean","COPY",EDGE,{"disambiguationData":[TD([subQ108])],"derivedFrom":subQ11})])]}),makeQuery(id+"F47.opFillet","BLEND_FACE",FACE,{"disambiguationData":[OSD([subQ0,subQ9]),TDD([makeQuery(id+"F42.boolean.opBoolean","COPY",EDGE,{"disambiguationData":[TD([subQ101])],"derivedFrom":subQ11})])]}),makeQuery(id+"F47.opFillet","BLEND_FACE",FACE,{"disambiguationData":[OSD([subQ0,subQ9]),TDD([makeQuery(id+"F42.boolean.opBoolean","COPY",EDGE,{"disambiguationData":[TD([subQ95])],"derivedFrom":subQ11})])]}),makeQuery(id+"F47.opFillet","BLEND_FACE",FACE,{"disambiguationData":[OSD([subQ0,subQ9]),TDD([makeQuery(id+"F42.boolean.opBoolean","COPY",EDGE,{"disambiguationData":[TD([subQ88])],"derivedFrom":subQ11})])]}),makeQuery(id+"F47.opFillet","BLEND_FACE",FACE,{"disambiguationData":[OSD([subQ0,subQ9]),TDD([makeQuery(id+"F42.boolean.opBoolean","COPY",EDGE,{"disambiguationData":[TD([subQ81])],"derivedFrom":subQ11})])]}),makeQuery(id+"F47.opFillet","BLEND_FACE",FACE,{"disambiguationData":[OSD([subQ0,subQ9]),TDD([makeQuery(id+"F42.boolean.opBoolean","COPY",EDGE,{"disambiguationData":[TD([subQ74])],"derivedFrom":subQ11})])]}),makeQuery(id+"F47.opFillet","BLEND_FACE",FACE,{"disambiguationData":[OSD([subQ0,subQ9]),TDD([makeQuery(id+"F42.boolean.opBoolean","COPY",EDGE,{"disambiguationData":[TD([subQ66])],"derivedFrom":subQ11})])]}),makeQuery(id+"F47.opFillet","BLEND_FACE",FACE,{"disambiguationData":[OSD([subQ0,subQ9]),TDD([makeQuery(id+"F42.boolean.opBoolean","COPY",EDGE,{"disambiguationData":[TD([subQ60])],"derivedFrom":subQ11})])]}),makeQuery(id+"F47.opFillet","BLEND_FACE",FACE,{"disambiguationData":[OSD([subQ0,subQ9]),TDD([makeQuery(id+"F42.boolean.opBoolean","COPY",EDGE,{"disambiguationData":[TD([subQ53])],"derivedFrom":subQ11})])]}),makeQuery(id+"F47.opFillet","BLEND_FACE",FACE,{"disambiguationData":[OSD([subQ0,subQ9]),TDD([makeQuery(id+"F42.boolean.opBoolean","COPY",EDGE,{"disambiguationData":[TD([subQ46])],"derivedFrom":subQ11})])]}),makeQuery(id+"F47.opFillet","BLEND_FACE",FACE,{"disambiguationData":[OSD([subQ0,subQ9]),TDD([makeQuery(id+"F42.boolean.opBoolean","COPY",EDGE,{"disambiguationData":[TD([subQ39])],"derivedFrom":subQ11})])]}),makeQuery(id+"F47.opFillet","BLEND_FACE",FACE,{"disambiguationData":[OSD([subQ0,subQ9]),TDD([makeQuery(id+"F42.boolean.opBoolean","COPY",EDGE,{"disambiguationData":[TD([subQ32])],"derivedFrom":subQ11})])]}),makeQuery(id+"F47.opFillet","BLEND_FACE",FACE,{"disambiguationData":[OSD([subQ0,subQ9]),TDD([makeQuery(id+"F42.boolean.opBoolean","COPY",EDGE,{"disambiguationData":[TD([subQ25])],"derivedFrom":subQ11})])]}),makeQuery(id+"F47.opFillet","BLEND_FACE",FACE,{"disambiguationData":[OSD([subQ0,subQ9]),TDD([makeQuery(id+"F42.boolean.opBoolean","COPY",EDGE,{"disambiguationData":[TD([makeQuery(id+"F37.opLoft","SWEPT_FACE",FACE,{"disambiguationData":[OSD([subQ16,subQ15,subQ14,sQuery(id+"F22.wireOp",EDGE,"E28.14.1"),subQ13,subQ12])]})])],"derivedFrom":subQ11})])]}),makeQuery(id+"F47.opFillet","BLEND_FACE",FACE,{"disambiguationData":[OSD([subQ0,subQ9]),TDD([makeQuery(id+"F42.boolean.opBoolean","COPY",EDGE,{"disambiguationData":[TD([makeQuery(id+"F38.opLoft","SWEPT_FACE",FACE,{"disambiguationData":[OSD([subQ8,subQ7,subQ5,sQuery(id+"F22.wireOp",EDGE,"E28.15.1"),subQ4,subQ3])]})])],"derivedFrom":subQ11})])]})],"blendedInto":[makeQuery(id+"F47.opFillet","BLEND_FACE",FACE,{"disambiguationData":[OSD([subQ0,subQ9]),TDD([makeQuery(id+"F42.boolean.opBoolean","COPY",EDGE,{"disambiguationData":[TD([makeQuery(id+"F23.opLoft","SWEPT_FACE",FACE,{"disambiguationData":[OSD([sQuery(id+"F3.wireOp",EDGE,"E20.8.0"),subQ113,subQ111,subQ110,subQ109,sQuery(id+"F22.wireOp",EDGE,"E27.right")])]})])],"derivedFrom":subQ11})])]}),makeQuery(id+"F47.opFillet","BLEND_FACE",FACE,{"disambiguationData":[OSD([subQ0,subQ9]),TDD([makeQuery(id+"F42.boolean.opBoolean","COPY",EDGE,{"disambiguationData":[TD([subQ108])],"derivedFrom":subQ11})])]}),makeQuery(id+"F47.opFillet","BLEND_FACE",FACE,{"disambiguationData":[OSD([subQ0,subQ9]),TDD([makeQuery(id+"F42.boolean.opBoolean","COPY",EDGE,{"disambiguationData":[TD([subQ101])],"derivedFrom":subQ11})])]}),makeQuery(id+"F47.opFillet","BLEND_FACE",FACE,{"disambiguationData":[OSD([subQ0,subQ9]),TDD([makeQuery(id+"F42.boolean.opBoolean","COPY",EDGE,{"disambiguationData":[TD([subQ95])],"derivedFrom":subQ11})])]}),makeQuery(id+"F47.opFillet","BLEND_FACE",FACE,{"disambiguationData":[OSD([subQ0,subQ9]),TDD([makeQuery(id+"F42.boolean.opBoolean","COPY",EDGE,{"disambiguationData":[TD([subQ88])],"derivedFrom":subQ11})])]}),makeQuery(id+"F47.opFillet","BLEND_FACE",FACE,{"disambiguationData":[OSD([subQ0,subQ9]),TDD([makeQuery(id+"F42.boolean.opBoolean","COPY",EDGE,{"disambiguationData":[TD([subQ81])],"derivedFrom":subQ11})])]}),makeQuery(id+"F47.opFillet","BLEND_FACE",FACE,{"disambiguationData":[OSD([subQ0,subQ9]),TDD([makeQuery(id+"F42.boolean.opBoolean","COPY",EDGE,{"disambiguationData":[TD([subQ74])],"derivedFrom":subQ11})])]}),makeQuery(id+"F47.opFillet","BLEND_FACE",FACE,{"disambiguationData":[OSD([subQ0,subQ9]),TDD([makeQuery(id+"F42.boolean.opBoolean","COPY",EDGE,{"disambiguationData":[TD([subQ66])],"derivedFrom":subQ11})])]}),makeQuery(id+"F47.opFillet","BLEND_FACE",FACE,{"disambiguationData":[OSD([subQ0,subQ9]),TDD([makeQuery(id+"F42.boolean.opBoolean","COPY",EDGE,{"disambiguationData":[TD([subQ60])],"derivedFrom":subQ11})])]}),makeQuery(id+"F47.opFillet","BLEND_FACE",FACE,{"disambiguationData":[OSD([subQ0,subQ9]),TDD([makeQuery(id+"F42.boolean.opBoolean","COPY",EDGE,{"disambiguationData":[TD([subQ53])],"derivedFrom":subQ11})])]}),makeQuery(id+"F47.opFillet","BLEND_FACE",FACE,{"disambiguationData":[OSD([subQ0,subQ9]),TDD([makeQuery(id+"F42.boolean.opBoolean","COPY",EDGE,{"disambiguationData":[TD([subQ46])],"derivedFrom":subQ11})])]}),makeQuery(id+"F47.opFillet","BLEND_FACE",FACE,{"disambiguationData":[OSD([subQ0,subQ9]),TDD([makeQuery(id+"F42.boolean.opBoolean","COPY",EDGE,{"disambiguationData":[TD([subQ39])],"derivedFrom":subQ11})])]}),makeQuery(id+"F47.opFillet","BLEND_FACE",FACE,{"disambiguationData":[OSD([subQ0,subQ9]),TDD([makeQuery(id+"F42.boolean.opBoolean","COPY",EDGE,{"disambiguationData":[TD([subQ32])],"derivedFrom":subQ11})])]}),makeQuery(id+"F47.opFillet","BLEND_FACE",FACE,{"disambiguationData":[OSD([subQ0,subQ9]),TDD([makeQuery(id+"F42.boolean.opBoolean","COPY",EDGE,{"disambiguationData":[TD([subQ25])],"derivedFrom":subQ11})])]}),makeQuery(id+"F47.opFillet","BLEND_FACE",FACE,{"disambiguationData":[OSD([subQ0,subQ9]),TDD([makeQuery(id+"F42.boolean.opBoolean","COPY",EDGE,{"disambiguationData":[TD([makeQuery(id+"F37.opLoft","SWEPT_FACE",FACE,{"disambiguationData":[OSD([subQ16,subQ15,subQ14,sQuery(id+"F22.wireOp",EDGE,"E28.14.1"),subQ13,subQ12])]})])],"derivedFrom":subQ11})])]}),makeQuery(id+"F47.opFillet","BLEND_FACE",FACE,{"disambiguationData":[OSD([subQ0,subQ9]),TDD([makeQuery(id+"F42.boolean.opBoolean","COPY",EDGE,{"disambiguationData":[TD([makeQuery(id+"F38.opLoft","SWEPT_FACE",FACE,{"disambiguationData":[OSD([subQ8,subQ7,subQ5,sQuery(id+"F22.wireOp",EDGE,"E28.15.1"),subQ4,subQ3])]})])],"derivedFrom":subQ11})])]})]});}
            var Q6;
            {var subQ0=sQuery(id+"F22.wireOp",EDGE,"E28.14.0");var subQ1=sQuery(id+"F22.wireOp",EDGE,"E28.14.3");var subQ2=sQuery(id+"F22.wireOp",EDGE,"E28.14.1");var subQ3=sQuery(id+"F22.wireOp",EDGE,"E28.14.2");var subQ4=sQuery(id+"F3.wireOp",EDGE,"E20.6.3");var subQ5=sQuery(id+"F3.wireOp",EDGE,"E20.6.1");var subQ6=makeQuery(id+"F37.opLoft","SWEPT_FACE",FACE,{"disambiguationData":[OSD([subQ5,sQuery(id+"F3.wireOp",EDGE,"E20.6.2"),subQ4,subQ0,subQ3,subQ1])]});var subQ7=sQuery(id+"F41.wireOp",EDGE,"E34");var subQ8=sQuery(id+"F41.wireOp",EDGE,"E32");Q6=makeQuery(id+"F44.opFillet","BLEND_EDGE",EDGE,{"blendedFrom":[makeQuery(id+"F40.boolean.opBoolean","INTERSECT",EDGE,{"derivedFrom":[subQ6,makeQuery(id+"F40.opExtrude","CAP_FACE",FACE,{"disambiguationData":[OSD([sQuery(id+"F39.wireOp",EDGE,"E29"),sQuery(id+"F39.wireOp",EDGE,"E30")])],"isStart":true})]}),makeQuery(id+"F42.boolean.opBoolean","COPY",FACE,{"disambiguationData":[TD([makeQuery(id+"F37.opLoft","SWEPT_FACE",FACE,{"disambiguationData":[OSD([sQuery(id+"F3.wireOp",EDGE,"E20.6.0"),subQ5,subQ4,subQ2,subQ3,subQ1])]})])],"derivedFrom":makeQuery(id+"F42.opRevolve","SWEPT_FACE",FACE,{"disambiguationData":[OSD([subQ8]),TDD([makeQuery(id+"F41.imprint","IMPRINT",EDGE,{"disambiguationData":[TD([[makeQuery(id+"F41.imprint","INTERSECT",VERTEX,{"disambiguationData":[OD(0.0)],"derivedFrom":[subQ8,subQ7]}),-1.0]])],"derivedFrom":subQ8})])]})})],"blendedInto":[makeQuery(id+"F42.boolean.opBoolean","COPY",FACE,{"disambiguationData":[TD([makeQuery(id+"F37.opLoft","SWEPT_FACE",FACE,{"disambiguationData":[OSD([sQuery(id+"F3.wireOp",EDGE,"E20.6.0"),subQ5,subQ4,subQ2,subQ3,subQ1])]})])],"derivedFrom":makeQuery(id+"F42.opRevolve","SWEPT_FACE",FACE,{"disambiguationData":[OSD([subQ8]),TDD([makeQuery(id+"F41.imprint","IMPRINT",EDGE,{"disambiguationData":[TD([[makeQuery(id+"F41.imprint","INTERSECT",VERTEX,{"disambiguationData":[OD(0.0)],"derivedFrom":[subQ8,subQ7]}),-1.0]])],"derivedFrom":subQ8})])]})})]});}
            var Q7;
            {var subQ0=sQuery(id+"F41.wireOp",EDGE,"E37");var subQ1=makeQuery(id+"F42.opRevolve","SWEPT_FACE",FACE,{"disambiguationData":[OSD([subQ0])]});var subQ2=makeQuery(id+"F40.opExtrude","CAP_FACE",FACE,{"disambiguationData":[OSD([sQuery(id+"F39.wireOp",EDGE,"E29"),sQuery(id+"F39.wireOp",EDGE,"E30")])],"isStart":true});var subQ3=sQuery(id+"F22.wireOp",EDGE,"E28.15.3");var subQ4=sQuery(id+"F22.wireOp",EDGE,"E28.15.2");var subQ5=sQuery(id+"F3.wireOp",EDGE,"E20.7.3");var subQ7=sQuery(id+"F3.wireOp",EDGE,"E20.7.1");var subQ8=sQuery(id+"F3.wireOp",EDGE,"E20.7.0");var subQ9=sQuery(id+"F41.wireOp",EDGE,"E38");var subQ10=makeQuery(id+"F42.opRevolve","SWEPT_FACE",FACE,{"disambiguationData":[OSD([subQ9])]});var subQ11=makeQuery(id+"F42.opRevolve","SWEPT_EDGE",EDGE,{"disambiguationData":[OSD([subQ0,subQ9])]});var subQ12=sQuery(id+"F22.wireOp",EDGE,"E28.14.3");var subQ13=sQuery(id+"F22.wireOp",EDGE,"E28.14.2");var subQ14=sQuery(id+"F3.wireOp",EDGE,"E20.6.3");var subQ15=sQuery(id+"F3.wireOp",EDGE,"E20.6.1");var subQ16=sQuery(id+"F3.wireOp",EDGE,"E20.6.0");var subQ18=sQuery(id+"F22.wireOp",EDGE,"E28.13.3");var subQ19=sQuery(id+"F22.wireOp",EDGE,"E28.13.2");var subQ20=sQuery(id+"F3.wireOp",EDGE,"E20.5.3");var subQ22=sQuery(id+"F3.wireOp",EDGE,"E20.5.1");var subQ23=sQuery(id+"F3.wireOp",EDGE,"E20.5.0");var subQ24=sQuery(id+"F22.wireOp",EDGE,"E28.12.3");var subQ25=sQuery(id+"F22.wireOp",EDGE,"E28.12.2");var subQ26=sQuery(id+"F3.wireOp",EDGE,"E20.4.3");var subQ28=sQuery(id+"F3.wireOp",EDGE,"E20.4.1");var subQ29=sQuery(id+"F3.wireOp",EDGE,"E20.4.0");var subQ30=sQuery(id+"F22.wireOp",EDGE,"E28.11.3");var subQ31=sQuery(id+"F22.wireOp",EDGE,"E28.11.2");var subQ32=sQuery(id+"F3.wireOp",EDGE,"E20.3.3");var subQ34=sQuery(id+"F3.wireOp",EDGE,"E20.3.1");var subQ36=sQuery(id+"F3.wireOp",EDGE,"E20.3.0");var subQ37=makeQuery(id+"F34.opLoft","SWEPT_FACE",FACE,{"disambiguationData":[OSD([subQ36,subQ34,subQ32,sQuery(id+"F22.wireOp",EDGE,"E28.11.1"),subQ31,subQ30])]});var subQ38=sQuery(id+"F22.wireOp",EDGE,"E28.10.3");var subQ39=sQuery(id+"F22.wireOp",EDGE,"E28.10.2");var subQ40=sQuery(id+"F3.wireOp",EDGE,"E20.2.3");var subQ42=sQuery(id+"F3.wireOp",EDGE,"E20.2.1");var subQ43=sQuery(id+"F3.wireOp",EDGE,"E20.2.0");var subQ44=makeQuery(id+"F33.opLoft","SWEPT_FACE",FACE,{"disambiguationData":[OSD([subQ43,subQ42,subQ40,sQuery(id+"F22.wireOp",EDGE,"E28.10.1"),subQ39,subQ38])]});var subQ45=sQuery(id+"F22.wireOp",EDGE,"E28.9.3");var subQ46=sQuery(id+"F22.wireOp",EDGE,"E28.9.2");var subQ47=sQuery(id+"F3.wireOp",EDGE,"E20.1.3");var subQ49=sQuery(id+"F3.wireOp",EDGE,"E20.1.1");var subQ50=sQuery(id+"F3.wireOp",EDGE,"E20.1.0");var subQ51=makeQuery(id+"F32.opLoft","SWEPT_FACE",FACE,{"disambiguationData":[OSD([subQ50,subQ49,subQ47,sQuery(id+"F22.wireOp",EDGE,"E28.9.1"),subQ46,subQ45])]});var subQ52=sQuery(id+"F22.wireOp",EDGE,"E28.8.3");var subQ53=sQuery(id+"F22.wireOp",EDGE,"E28.8.2");var subQ55=sQuery(id+"F3.wireOp",EDGE,"E18.top");var subQ56=sQuery(id+"F3.wireOp",EDGE,"E18.bottom");var subQ57=sQuery(id+"F3.wireOp",EDGE,"E18.left");var subQ58=makeQuery(id+"F31.opLoft","SWEPT_FACE",FACE,{"disambiguationData":[OSD([subQ56,subQ55,subQ57,sQuery(id+"F22.wireOp",EDGE,"E28.8.1"),subQ53,subQ52])]});var subQ59=sQuery(id+"F22.wireOp",EDGE,"E28.7.3");var subQ60=sQuery(id+"F22.wireOp",EDGE,"E28.7.2");var subQ61=sQuery(id+"F3.wireOp",EDGE,"E20.15.3");var subQ62=sQuery(id+"F3.wireOp",EDGE,"E20.15.1");var subQ63=sQuery(id+"F3.wireOp",EDGE,"E20.15.0");var subQ64=makeQuery(id+"F30.opLoft","SWEPT_FACE",FACE,{"disambiguationData":[OSD([subQ63,subQ62,subQ61,sQuery(id+"F22.wireOp",EDGE,"E28.7.1"),subQ60,subQ59])]});var subQ66=sQuery(id+"F22.wireOp",EDGE,"E28.6.3");var subQ67=sQuery(id+"F22.wireOp",EDGE,"E28.6.2");var subQ68=sQuery(id+"F3.wireOp",EDGE,"E20.14.3");var subQ70=sQuery(id+"F3.wireOp",EDGE,"E20.14.1");var subQ71=sQuery(id+"F3.wireOp",EDGE,"E20.14.0");var subQ72=makeQuery(id+"F29.opLoft","SWEPT_FACE",FACE,{"disambiguationData":[OSD([subQ71,subQ70,subQ68,sQuery(id+"F22.wireOp",EDGE,"E28.6.1"),subQ67,subQ66])]});var subQ73=sQuery(id+"F22.wireOp",EDGE,"E28.5.3");var subQ74=sQuery(id+"F22.wireOp",EDGE,"E28.5.2");var subQ75=sQuery(id+"F3.wireOp",EDGE,"E20.13.3");var subQ77=sQuery(id+"F3.wireOp",EDGE,"E20.13.1");var subQ78=sQuery(id+"F3.wireOp",EDGE,"E20.13.0");var subQ79=makeQuery(id+"F28.opLoft","SWEPT_FACE",FACE,{"disambiguationData":[OSD([subQ78,subQ77,subQ75,sQuery(id+"F22.wireOp",EDGE,"E28.5.1"),subQ74,subQ73])]});var subQ80=sQuery(id+"F22.wireOp",EDGE,"E28.4.3");var subQ81=sQuery(id+"F22.wireOp",EDGE,"E28.4.2");var subQ82=sQuery(id+"F3.wireOp",EDGE,"E20.12.3");var subQ84=sQuery(id+"F3.wireOp",EDGE,"E20.12.1");var subQ85=sQuery(id+"F3.wireOp",EDGE,"E20.12.0");var subQ86=makeQuery(id+"F27.opLoft","SWEPT_FACE",FACE,{"disambiguationData":[OSD([subQ85,subQ84,subQ82,sQuery(id+"F22.wireOp",EDGE,"E28.4.1"),subQ81,subQ80])]});var subQ87=sQuery(id+"F22.wireOp",EDGE,"E28.3.3");var subQ88=sQuery(id+"F22.wireOp",EDGE,"E28.3.2");var subQ89=sQuery(id+"F3.wireOp",EDGE,"E20.11.3");var subQ91=sQuery(id+"F3.wireOp",EDGE,"E20.11.1");var subQ92=sQuery(id+"F3.wireOp",EDGE,"E20.11.0");var subQ93=makeQuery(id+"F26.opLoft","SWEPT_FACE",FACE,{"disambiguationData":[OSD([subQ92,subQ91,subQ89,sQuery(id+"F22.wireOp",EDGE,"E28.3.1"),subQ88,subQ87])]});var subQ94=sQuery(id+"F22.wireOp",EDGE,"E28.2.3");var subQ95=sQuery(id+"F22.wireOp",EDGE,"E28.2.2");var subQ96=sQuery(id+"F3.wireOp",EDGE,"E20.10.3");var subQ97=sQuery(id+"F3.wireOp",EDGE,"E20.10.1");var subQ98=sQuery(id+"F3.wireOp",EDGE,"E20.10.0");var subQ99=makeQuery(id+"F25.opLoft","SWEPT_FACE",FACE,{"disambiguationData":[OSD([subQ98,subQ97,subQ96,sQuery(id+"F22.wireOp",EDGE,"E28.2.1"),subQ95,subQ94])]});var subQ101=sQuery(id+"F22.wireOp",EDGE,"E28.1.3");var subQ102=sQuery(id+"F22.wireOp",EDGE,"E28.1.2");var subQ103=sQuery(id+"F3.wireOp",EDGE,"E20.9.3");var subQ104=sQuery(id+"F3.wireOp",EDGE,"E20.9.1");var subQ105=sQuery(id+"F3.wireOp",EDGE,"E20.9.0");var subQ106=makeQuery(id+"F24.opLoft","SWEPT_FACE",FACE,{"disambiguationData":[OSD([subQ105,subQ104,subQ103,sQuery(id+"F22.wireOp",EDGE,"E28.1.1"),subQ102,subQ101])]});var subQ107=sQuery(id+"F22.wireOp",EDGE,"E27.top");var subQ108=sQuery(id+"F22.wireOp",EDGE,"E27.bottom");var subQ109=sQuery(id+"F3.wireOp",EDGE,"E20.8.3");var subQ111=sQuery(id+"F3.wireOp",EDGE,"E20.8.1");var subQ115=makeQuery(id+"F42.boolean.opBoolean","COPY",FACE,{"disambiguationData":[TD([subQ37])],"derivedFrom":subQ10});var subQ124=makeQuery(id+"F14.opLoft","CAP_FACE",FACE,{"disambiguationData":[OSD([makeQuery(id+"F3.imprint","IMPRINT",FACE,{"disambiguationData":[TD([[makeQuery(id+"F3.imprint","IMPRINT",EDGE,{"derivedFrom":subQ8}),-1.0]])]})])],"isStart":true});var subQ158=makeQuery(id+"F5.opLoft","CAP_FACE",FACE,{"disambiguationData":[OSD([makeQuery(id+"F3.imprint","IMPRINT",FACE,{"disambiguationData":[TD([[makeQuery(id+"F3.imprint","IMPRINT",EDGE,{"derivedFrom":subQ56}),1.0]])]})])],"isStart":true});var subQ187=makeQuery(id+"F34.boolean.opBoolean","INTERSECT",EDGE,{"derivedFrom":[makeQuery(id+"F33.boolean.opBoolean","SPLIT",FACE,{"disambiguationData":[TD([subQ124])],"derivedFrom":makeQuery(id+"F32.boolean.opBoolean","SPLIT",FACE,{"disambiguationData":[TD([subQ124])],"derivedFrom":makeQuery(id+"F31.boolean.opBoolean","SPLIT",FACE,{"disambiguationData":[TD([subQ124])],"derivedFrom":makeQuery(id+"F30.boolean.opBoolean","SPLIT",FACE,{"disambiguationData":[TD([subQ158])],"derivedFrom":makeQuery(id+"F29.boolean.opBoolean","SPLIT",FACE,{"disambiguationData":[TD([subQ158])],"derivedFrom":makeQuery(id+"F28.boolean.opBoolean","SPLIT",FACE,{"disambiguationData":[TD([subQ158])],"derivedFrom":makeQuery(id+"F27.boolean.opBoolean","SPLIT",FACE,{"disambiguationData":[TD([subQ158])],"derivedFrom":makeQuery(id+"F26.boolean.opBoolean","SPLIT",FACE,{"disambiguationData":[TD([subQ158])],"derivedFrom":makeQuery(id+"F25.boolean.opBoolean","SPLIT",FACE,{"disambiguationData":[TD([subQ158])],"derivedFrom":makeQuery(id+"F24.boolean.opBoolean","SPLIT",FACE,{"disambiguationData":[TD([subQ158])],"derivedFrom":makeQuery(id+"F1.opRevolve","SWEPT_FACE",FACE,{"disambiguationData":[OSD([sQuery(id+"F0.wireOp",EDGE,"E13")])]})})})})})})})})})})}),subQ37]});Q7=makeQuery(id+"F48.opFillet","BLEND_EDGE",EDGE,{"blendedFrom":[makeQuery(id+"F47.opFillet","TWEAK_EDGE",EDGE,{"derivedFrom":[makeQuery(id+"F45.opFillet","BLEND_VERTEX",VERTEX,{"blendedFrom":[subQ187,subQ37,subQ115],"blendedInto":[subQ37,subQ115]}),makeQuery(id+"F45.opFillet","BLEND_VERTEX",VERTEX,{"blendedFrom":[subQ187,makeQuery(id+"F42.boolean.opBoolean","MERGE",FACE,{"derivedFrom":[subQ2,subQ1]}),subQ115],"blendedInto":[makeQuery(id+"F42.boolean.opBoolean","MERGE",FACE,{"derivedFrom":[subQ2,subQ1]}),subQ115]})]}),makeQuery(id+"F47.opFillet","BLEND_FACE",FACE,{"disambiguationData":[OSD([subQ0,subQ9]),TDD([makeQuery(id+"F42.boolean.opBoolean","COPY",EDGE,{"disambiguationData":[TD([makeQuery(id+"F23.opLoft","SWEPT_FACE",FACE,{"disambiguationData":[OSD([sQuery(id+"F3.wireOp",EDGE,"E20.8.0"),subQ111,subQ109,subQ108,subQ107,sQuery(id+"F22.wireOp",EDGE,"E27.right")])]})])],"derivedFrom":subQ11})])]}),makeQuery(id+"F47.opFillet","BLEND_FACE",FACE,{"disambiguationData":[OSD([subQ0,subQ9]),TDD([makeQuery(id+"F42.boolean.opBoolean","COPY",EDGE,{"disambiguationData":[TD([subQ106])],"derivedFrom":subQ11})])]}),makeQuery(id+"F47.opFillet","BLEND_FACE",FACE,{"disambiguationData":[OSD([subQ0,subQ9]),TDD([makeQuery(id+"F42.boolean.opBoolean","COPY",EDGE,{"disambiguationData":[TD([subQ99])],"derivedFrom":subQ11})])]}),makeQuery(id+"F47.opFillet","BLEND_FACE",FACE,{"disambiguationData":[OSD([subQ0,subQ9]),TDD([makeQuery(id+"F42.boolean.opBoolean","COPY",EDGE,{"disambiguationData":[TD([subQ93])],"derivedFrom":subQ11})])]}),makeQuery(id+"F47.opFillet","BLEND_FACE",FACE,{"disambiguationData":[OSD([subQ0,subQ9]),TDD([makeQuery(id+"F42.boolean.opBoolean","COPY",EDGE,{"disambiguationData":[TD([subQ86])],"derivedFrom":subQ11})])]}),makeQuery(id+"F47.opFillet","BLEND_FACE",FACE,{"disambiguationData":[OSD([subQ0,subQ9]),TDD([makeQuery(id+"F42.boolean.opBoolean","COPY",EDGE,{"disambiguationData":[TD([subQ79])],"derivedFrom":subQ11})])]}),makeQuery(id+"F47.opFillet","BLEND_FACE",FACE,{"disambiguationData":[OSD([subQ0,subQ9]),TDD([makeQuery(id+"F42.boolean.opBoolean","COPY",EDGE,{"disambiguationData":[TD([subQ72])],"derivedFrom":subQ11})])]}),makeQuery(id+"F47.opFillet","BLEND_FACE",FACE,{"disambiguationData":[OSD([subQ0,subQ9]),TDD([makeQuery(id+"F42.boolean.opBoolean","COPY",EDGE,{"disambiguationData":[TD([subQ64])],"derivedFrom":subQ11})])]}),makeQuery(id+"F47.opFillet","BLEND_FACE",FACE,{"disambiguationData":[OSD([subQ0,subQ9]),TDD([makeQuery(id+"F42.boolean.opBoolean","COPY",EDGE,{"disambiguationData":[TD([subQ58])],"derivedFrom":subQ11})])]}),makeQuery(id+"F47.opFillet","BLEND_FACE",FACE,{"disambiguationData":[OSD([subQ0,subQ9]),TDD([makeQuery(id+"F42.boolean.opBoolean","COPY",EDGE,{"disambiguationData":[TD([subQ51])],"derivedFrom":subQ11})])]}),makeQuery(id+"F47.opFillet","BLEND_FACE",FACE,{"disambiguationData":[OSD([subQ0,subQ9]),TDD([makeQuery(id+"F42.boolean.opBoolean","COPY",EDGE,{"disambiguationData":[TD([subQ44])],"derivedFrom":subQ11})])]}),makeQuery(id+"F47.opFillet","BLEND_FACE",FACE,{"disambiguationData":[OSD([subQ0,subQ9]),TDD([makeQuery(id+"F42.boolean.opBoolean","COPY",EDGE,{"disambiguationData":[TD([subQ37])],"derivedFrom":subQ11})])]}),makeQuery(id+"F47.opFillet","BLEND_FACE",FACE,{"disambiguationData":[OSD([subQ0,subQ9]),TDD([makeQuery(id+"F42.boolean.opBoolean","COPY",EDGE,{"disambiguationData":[TD([makeQuery(id+"F35.opLoft","SWEPT_FACE",FACE,{"disambiguationData":[OSD([subQ29,subQ28,subQ26,sQuery(id+"F22.wireOp",EDGE,"E28.12.1"),subQ25,subQ24])]})])],"derivedFrom":subQ11})])]}),makeQuery(id+"F47.opFillet","BLEND_FACE",FACE,{"disambiguationData":[OSD([subQ0,subQ9]),TDD([makeQuery(id+"F42.boolean.opBoolean","COPY",EDGE,{"disambiguationData":[TD([makeQuery(id+"F36.opLoft","SWEPT_FACE",FACE,{"disambiguationData":[OSD([subQ23,subQ22,subQ20,sQuery(id+"F22.wireOp",EDGE,"E28.13.1"),subQ19,subQ18])]})])],"derivedFrom":subQ11})])]}),makeQuery(id+"F47.opFillet","BLEND_FACE",FACE,{"disambiguationData":[OSD([subQ0,subQ9]),TDD([makeQuery(id+"F42.boolean.opBoolean","COPY",EDGE,{"disambiguationData":[TD([makeQuery(id+"F37.opLoft","SWEPT_FACE",FACE,{"disambiguationData":[OSD([subQ16,subQ15,subQ14,sQuery(id+"F22.wireOp",EDGE,"E28.14.1"),subQ13,subQ12])]})])],"derivedFrom":subQ11})])]}),makeQuery(id+"F47.opFillet","BLEND_FACE",FACE,{"disambiguationData":[OSD([subQ0,subQ9]),TDD([makeQuery(id+"F42.boolean.opBoolean","COPY",EDGE,{"disambiguationData":[TD([makeQuery(id+"F38.opLoft","SWEPT_FACE",FACE,{"disambiguationData":[OSD([subQ8,subQ7,subQ5,sQuery(id+"F22.wireOp",EDGE,"E28.15.1"),subQ4,subQ3])]})])],"derivedFrom":subQ11})])]})],"blendedInto":[makeQuery(id+"F47.opFillet","BLEND_FACE",FACE,{"disambiguationData":[OSD([subQ0,subQ9]),TDD([makeQuery(id+"F42.boolean.opBoolean","COPY",EDGE,{"disambiguationData":[TD([makeQuery(id+"F23.opLoft","SWEPT_FACE",FACE,{"disambiguationData":[OSD([sQuery(id+"F3.wireOp",EDGE,"E20.8.0"),subQ111,subQ109,subQ108,subQ107,sQuery(id+"F22.wireOp",EDGE,"E27.right")])]})])],"derivedFrom":subQ11})])]}),makeQuery(id+"F47.opFillet","BLEND_FACE",FACE,{"disambiguationData":[OSD([subQ0,subQ9]),TDD([makeQuery(id+"F42.boolean.opBoolean","COPY",EDGE,{"disambiguationData":[TD([subQ106])],"derivedFrom":subQ11})])]}),makeQuery(id+"F47.opFillet","BLEND_FACE",FACE,{"disambiguationData":[OSD([subQ0,subQ9]),TDD([makeQuery(id+"F42.boolean.opBoolean","COPY",EDGE,{"disambiguationData":[TD([subQ99])],"derivedFrom":subQ11})])]}),makeQuery(id+"F47.opFillet","BLEND_FACE",FACE,{"disambiguationData":[OSD([subQ0,subQ9]),TDD([makeQuery(id+"F42.boolean.opBoolean","COPY",EDGE,{"disambiguationData":[TD([subQ93])],"derivedFrom":subQ11})])]}),makeQuery(id+"F47.opFillet","BLEND_FACE",FACE,{"disambiguationData":[OSD([subQ0,subQ9]),TDD([makeQuery(id+"F42.boolean.opBoolean","COPY",EDGE,{"disambiguationData":[TD([subQ86])],"derivedFrom":subQ11})])]}),makeQuery(id+"F47.opFillet","BLEND_FACE",FACE,{"disambiguationData":[OSD([subQ0,subQ9]),TDD([makeQuery(id+"F42.boolean.opBoolean","COPY",EDGE,{"disambiguationData":[TD([subQ79])],"derivedFrom":subQ11})])]}),makeQuery(id+"F47.opFillet","BLEND_FACE",FACE,{"disambiguationData":[OSD([subQ0,subQ9]),TDD([makeQuery(id+"F42.boolean.opBoolean","COPY",EDGE,{"disambiguationData":[TD([subQ72])],"derivedFrom":subQ11})])]}),makeQuery(id+"F47.opFillet","BLEND_FACE",FACE,{"disambiguationData":[OSD([subQ0,subQ9]),TDD([makeQuery(id+"F42.boolean.opBoolean","COPY",EDGE,{"disambiguationData":[TD([subQ64])],"derivedFrom":subQ11})])]}),makeQuery(id+"F47.opFillet","BLEND_FACE",FACE,{"disambiguationData":[OSD([subQ0,subQ9]),TDD([makeQuery(id+"F42.boolean.opBoolean","COPY",EDGE,{"disambiguationData":[TD([subQ58])],"derivedFrom":subQ11})])]}),makeQuery(id+"F47.opFillet","BLEND_FACE",FACE,{"disambiguationData":[OSD([subQ0,subQ9]),TDD([makeQuery(id+"F42.boolean.opBoolean","COPY",EDGE,{"disambiguationData":[TD([subQ51])],"derivedFrom":subQ11})])]}),makeQuery(id+"F47.opFillet","BLEND_FACE",FACE,{"disambiguationData":[OSD([subQ0,subQ9]),TDD([makeQuery(id+"F42.boolean.opBoolean","COPY",EDGE,{"disambiguationData":[TD([subQ44])],"derivedFrom":subQ11})])]}),makeQuery(id+"F47.opFillet","BLEND_FACE",FACE,{"disambiguationData":[OSD([subQ0,subQ9]),TDD([makeQuery(id+"F42.boolean.opBoolean","COPY",EDGE,{"disambiguationData":[TD([subQ37])],"derivedFrom":subQ11})])]}),makeQuery(id+"F47.opFillet","BLEND_FACE",FACE,{"disambiguationData":[OSD([subQ0,subQ9]),TDD([makeQuery(id+"F42.boolean.opBoolean","COPY",EDGE,{"disambiguationData":[TD([makeQuery(id+"F35.opLoft","SWEPT_FACE",FACE,{"disambiguationData":[OSD([subQ29,subQ28,subQ26,sQuery(id+"F22.wireOp",EDGE,"E28.12.1"),subQ25,subQ24])]})])],"derivedFrom":subQ11})])]}),makeQuery(id+"F47.opFillet","BLEND_FACE",FACE,{"disambiguationData":[OSD([subQ0,subQ9]),TDD([makeQuery(id+"F42.boolean.opBoolean","COPY",EDGE,{"disambiguationData":[TD([makeQuery(id+"F36.opLoft","SWEPT_FACE",FACE,{"disambiguationData":[OSD([subQ23,subQ22,subQ20,sQuery(id+"F22.wireOp",EDGE,"E28.13.1"),subQ19,subQ18])]})])],"derivedFrom":subQ11})])]}),makeQuery(id+"F47.opFillet","BLEND_FACE",FACE,{"disambiguationData":[OSD([subQ0,subQ9]),TDD([makeQuery(id+"F42.boolean.opBoolean","COPY",EDGE,{"disambiguationData":[TD([makeQuery(id+"F37.opLoft","SWEPT_FACE",FACE,{"disambiguationData":[OSD([subQ16,subQ15,subQ14,sQuery(id+"F22.wireOp",EDGE,"E28.14.1"),subQ13,subQ12])]})])],"derivedFrom":subQ11})])]}),makeQuery(id+"F47.opFillet","BLEND_FACE",FACE,{"disambiguationData":[OSD([subQ0,subQ9]),TDD([makeQuery(id+"F42.boolean.opBoolean","COPY",EDGE,{"disambiguationData":[TD([makeQuery(id+"F38.opLoft","SWEPT_FACE",FACE,{"disambiguationData":[OSD([subQ8,subQ7,subQ5,sQuery(id+"F22.wireOp",EDGE,"E28.15.1"),subQ4,subQ3])]})])],"derivedFrom":subQ11})])]})]});}
            var Q8;
            {var subQ0=sQuery(id+"F41.wireOp",EDGE,"E34");var subQ1=sQuery(id+"F41.wireOp",EDGE,"E32");Q8=makeQuery(id+"F42.boolean.opBoolean","INTERSECT",EDGE,{"derivedFrom":[makeQuery(id+"F34.opLoft","SWEPT_FACE",FACE,{"disambiguationData":[OSD([sQuery(id+"F3.wireOp",EDGE,"E20.3.0"),sQuery(id+"F3.wireOp",EDGE,"E20.3.1"),sQuery(id+"F3.wireOp",EDGE,"E20.3.3"),sQuery(id+"F22.wireOp",EDGE,"E28.11.1"),sQuery(id+"F22.wireOp",EDGE,"E28.11.2"),sQuery(id+"F22.wireOp",EDGE,"E28.11.3")])]}),makeQuery(id+"F42.opRevolve","SWEPT_FACE",FACE,{"disambiguationData":[OSD([subQ1]),TDD([makeQuery(id+"F41.imprint","IMPRINT",EDGE,{"disambiguationData":[TD([[makeQuery(id+"F41.imprint","INTERSECT",VERTEX,{"disambiguationData":[OD(0.0)],"derivedFrom":[subQ1,subQ0]}),-1.0]])],"derivedFrom":subQ1})])]})]});}
            var Q9;
            {var subQ0=sQuery(id+"F22.wireOp",EDGE,"E28.11.3");var subQ1=sQuery(id+"F22.wireOp",EDGE,"E28.11.2");var subQ2=sQuery(id+"F22.wireOp",EDGE,"E28.11.0");var subQ3=sQuery(id+"F3.wireOp",EDGE,"E20.3.3");var subQ4=sQuery(id+"F3.wireOp",EDGE,"E20.3.1");var subQ5=makeQuery(id+"F34.opLoft","SWEPT_FACE",FACE,{"disambiguationData":[OSD([subQ4,sQuery(id+"F3.wireOp",EDGE,"E20.3.2"),subQ3,subQ2,subQ1,subQ0])]});var subQ6=sQuery(id+"F22.wireOp",EDGE,"E28.11.1");var subQ7=sQuery(id+"F41.wireOp",EDGE,"E34");var subQ8=sQuery(id+"F41.wireOp",EDGE,"E32");Q9=makeQuery(id+"F44.opFillet","BLEND_EDGE",EDGE,{"blendedFrom":[makeQuery(id+"F40.boolean.opBoolean","INTERSECT",EDGE,{"derivedFrom":[subQ5,makeQuery(id+"F40.opExtrude","CAP_FACE",FACE,{"disambiguationData":[OSD([sQuery(id+"F39.wireOp",EDGE,"E29"),sQuery(id+"F39.wireOp",EDGE,"E30")])],"isStart":true})]}),makeQuery(id+"F42.boolean.opBoolean","COPY",FACE,{"disambiguationData":[TD([makeQuery(id+"F34.opLoft","SWEPT_FACE",FACE,{"disambiguationData":[OSD([sQuery(id+"F3.wireOp",EDGE,"E20.3.0"),subQ4,subQ3,subQ6,subQ1,subQ0])]})])],"derivedFrom":makeQuery(id+"F42.opRevolve","SWEPT_FACE",FACE,{"disambiguationData":[OSD([subQ8]),TDD([makeQuery(id+"F41.imprint","IMPRINT",EDGE,{"disambiguationData":[TD([[makeQuery(id+"F41.imprint","INTERSECT",VERTEX,{"disambiguationData":[OD(0.0)],"derivedFrom":[subQ8,subQ7]}),-1.0]])],"derivedFrom":subQ8})])]})})],"blendedInto":[makeQuery(id+"F42.boolean.opBoolean","COPY",FACE,{"disambiguationData":[TD([makeQuery(id+"F34.opLoft","SWEPT_FACE",FACE,{"disambiguationData":[OSD([sQuery(id+"F3.wireOp",EDGE,"E20.3.0"),subQ4,subQ3,subQ6,subQ1,subQ0])]})])],"derivedFrom":makeQuery(id+"F42.opRevolve","SWEPT_FACE",FACE,{"disambiguationData":[OSD([subQ8]),TDD([makeQuery(id+"F41.imprint","IMPRINT",EDGE,{"disambiguationData":[TD([[makeQuery(id+"F41.imprint","INTERSECT",VERTEX,{"disambiguationData":[OD(0.0)],"derivedFrom":[subQ8,subQ7]}),-1.0]])],"derivedFrom":subQ8})])]})})]});}
            var Q10;
            {var subQ0=sQuery(id+"F3.wireOp",EDGE,"E20.2.3");var subQ1=sQuery(id+"F3.wireOp",EDGE,"E20.2.1");var subQ2=sQuery(id+"F3.wireOp",EDGE,"E20.2.0");var subQ3=makeQuery(id+"F33.opLoft","SWEPT_FACE",FACE,{"disambiguationData":[OSD([subQ2,subQ1,subQ0,sQuery(id+"F22.wireOp",EDGE,"E28.10.1"),sQuery(id+"F22.wireOp",EDGE,"E28.10.2"),sQuery(id+"F22.wireOp",EDGE,"E28.10.3")])]});var subQ52=sQuery(id+"F3.wireOp",EDGE,"E20.7.0");var subQ61=makeQuery(id+"F14.opLoft","CAP_FACE",FACE,{"disambiguationData":[OSD([makeQuery(id+"F3.imprint","IMPRINT",FACE,{"disambiguationData":[TD([[makeQuery(id+"F3.imprint","IMPRINT",EDGE,{"derivedFrom":subQ52}),-1.0]])]})])],"isStart":true});var subQ74=sQuery(id+"F3.wireOp",EDGE,"E18.bottom");var subQ79=makeQuery(id+"F5.opLoft","CAP_FACE",FACE,{"disambiguationData":[OSD([makeQuery(id+"F3.imprint","IMPRINT",FACE,{"disambiguationData":[TD([[makeQuery(id+"F3.imprint","IMPRINT",EDGE,{"derivedFrom":subQ74}),1.0]])]})])],"isStart":true});Q10=makeQuery(id+"F45.opFillet","BLEND_EDGE",EDGE,{"blendedFrom":[makeQuery(id+"F33.boolean.opBoolean","INTERSECT",EDGE,{"derivedFrom":[makeQuery(id+"F32.boolean.opBoolean","SPLIT",FACE,{"disambiguationData":[TD([subQ61])],"derivedFrom":makeQuery(id+"F31.boolean.opBoolean","SPLIT",FACE,{"disambiguationData":[TD([subQ61])],"derivedFrom":makeQuery(id+"F30.boolean.opBoolean","SPLIT",FACE,{"disambiguationData":[TD([subQ79])],"derivedFrom":makeQuery(id+"F29.boolean.opBoolean","SPLIT",FACE,{"disambiguationData":[TD([subQ79])],"derivedFrom":makeQuery(id+"F28.boolean.opBoolean","SPLIT",FACE,{"disambiguationData":[TD([subQ79])],"derivedFrom":makeQuery(id+"F27.boolean.opBoolean","SPLIT",FACE,{"disambiguationData":[TD([subQ79])],"derivedFrom":makeQuery(id+"F26.boolean.opBoolean","SPLIT",FACE,{"disambiguationData":[TD([subQ79])],"derivedFrom":makeQuery(id+"F25.boolean.opBoolean","SPLIT",FACE,{"disambiguationData":[TD([subQ79])],"derivedFrom":makeQuery(id+"F24.boolean.opBoolean","SPLIT",FACE,{"disambiguationData":[TD([subQ79])],"derivedFrom":makeQuery(id+"F1.opRevolve","SWEPT_FACE",FACE,{"disambiguationData":[OSD([sQuery(id+"F0.wireOp",EDGE,"E13")])]})})})})})})})})})}),subQ3]}),subQ3],"blendedInto":[subQ3]});}
            var Q11;
            {var subQ0=sQuery(id+"F41.wireOp",EDGE,"E37");var subQ1=makeQuery(id+"F42.opRevolve","SWEPT_FACE",FACE,{"disambiguationData":[OSD([subQ0])]});var subQ2=makeQuery(id+"F40.opExtrude","CAP_FACE",FACE,{"disambiguationData":[OSD([sQuery(id+"F39.wireOp",EDGE,"E29"),sQuery(id+"F39.wireOp",EDGE,"E30")])],"isStart":true});var subQ3=sQuery(id+"F22.wireOp",EDGE,"E28.15.3");var subQ4=sQuery(id+"F22.wireOp",EDGE,"E28.15.2");var subQ5=sQuery(id+"F3.wireOp",EDGE,"E20.7.3");var subQ7=sQuery(id+"F3.wireOp",EDGE,"E20.7.1");var subQ8=sQuery(id+"F3.wireOp",EDGE,"E20.7.0");var subQ9=sQuery(id+"F41.wireOp",EDGE,"E38");var subQ10=makeQuery(id+"F42.opRevolve","SWEPT_FACE",FACE,{"disambiguationData":[OSD([subQ9])]});var subQ11=makeQuery(id+"F42.opRevolve","SWEPT_EDGE",EDGE,{"disambiguationData":[OSD([subQ0,subQ9])]});var subQ12=sQuery(id+"F22.wireOp",EDGE,"E28.14.3");var subQ13=sQuery(id+"F22.wireOp",EDGE,"E28.14.2");var subQ14=sQuery(id+"F3.wireOp",EDGE,"E20.6.3");var subQ15=sQuery(id+"F3.wireOp",EDGE,"E20.6.1");var subQ16=sQuery(id+"F3.wireOp",EDGE,"E20.6.0");var subQ18=sQuery(id+"F22.wireOp",EDGE,"E28.13.3");var subQ19=sQuery(id+"F22.wireOp",EDGE,"E28.13.2");var subQ20=sQuery(id+"F3.wireOp",EDGE,"E20.5.3");var subQ22=sQuery(id+"F3.wireOp",EDGE,"E20.5.1");var subQ23=sQuery(id+"F3.wireOp",EDGE,"E20.5.0");var subQ24=sQuery(id+"F22.wireOp",EDGE,"E28.12.3");var subQ25=sQuery(id+"F22.wireOp",EDGE,"E28.12.2");var subQ26=sQuery(id+"F3.wireOp",EDGE,"E20.4.3");var subQ28=sQuery(id+"F3.wireOp",EDGE,"E20.4.1");var subQ29=sQuery(id+"F3.wireOp",EDGE,"E20.4.0");var subQ30=sQuery(id+"F22.wireOp",EDGE,"E28.11.3");var subQ31=sQuery(id+"F22.wireOp",EDGE,"E28.11.2");var subQ32=sQuery(id+"F3.wireOp",EDGE,"E20.3.3");var subQ34=sQuery(id+"F3.wireOp",EDGE,"E20.3.1");var subQ35=sQuery(id+"F3.wireOp",EDGE,"E20.3.0");var subQ36=sQuery(id+"F22.wireOp",EDGE,"E28.10.3");var subQ37=sQuery(id+"F22.wireOp",EDGE,"E28.10.2");var subQ38=sQuery(id+"F3.wireOp",EDGE,"E20.2.3");var subQ40=sQuery(id+"F3.wireOp",EDGE,"E20.2.1");var subQ42=sQuery(id+"F3.wireOp",EDGE,"E20.2.0");var subQ43=makeQuery(id+"F33.opLoft","SWEPT_FACE",FACE,{"disambiguationData":[OSD([subQ42,subQ40,subQ38,sQuery(id+"F22.wireOp",EDGE,"E28.10.1"),subQ37,subQ36])]});var subQ44=sQuery(id+"F22.wireOp",EDGE,"E28.9.3");var subQ45=sQuery(id+"F22.wireOp",EDGE,"E28.9.2");var subQ46=sQuery(id+"F3.wireOp",EDGE,"E20.1.3");var subQ48=sQuery(id+"F3.wireOp",EDGE,"E20.1.1");var subQ49=sQuery(id+"F3.wireOp",EDGE,"E20.1.0");var subQ50=makeQuery(id+"F32.opLoft","SWEPT_FACE",FACE,{"disambiguationData":[OSD([subQ49,subQ48,subQ46,sQuery(id+"F22.wireOp",EDGE,"E28.9.1"),subQ45,subQ44])]});var subQ51=sQuery(id+"F22.wireOp",EDGE,"E28.8.3");var subQ52=sQuery(id+"F22.wireOp",EDGE,"E28.8.2");var subQ54=sQuery(id+"F3.wireOp",EDGE,"E18.top");var subQ55=sQuery(id+"F3.wireOp",EDGE,"E18.bottom");var subQ56=sQuery(id+"F3.wireOp",EDGE,"E18.left");var subQ57=makeQuery(id+"F31.opLoft","SWEPT_FACE",FACE,{"disambiguationData":[OSD([subQ55,subQ54,subQ56,sQuery(id+"F22.wireOp",EDGE,"E28.8.1"),subQ52,subQ51])]});var subQ58=sQuery(id+"F22.wireOp",EDGE,"E28.7.3");var subQ59=sQuery(id+"F22.wireOp",EDGE,"E28.7.2");var subQ60=sQuery(id+"F3.wireOp",EDGE,"E20.15.3");var subQ61=sQuery(id+"F3.wireOp",EDGE,"E20.15.1");var subQ62=sQuery(id+"F3.wireOp",EDGE,"E20.15.0");var subQ63=makeQuery(id+"F30.opLoft","SWEPT_FACE",FACE,{"disambiguationData":[OSD([subQ62,subQ61,subQ60,sQuery(id+"F22.wireOp",EDGE,"E28.7.1"),subQ59,subQ58])]});var subQ65=sQuery(id+"F22.wireOp",EDGE,"E28.6.3");var subQ66=sQuery(id+"F22.wireOp",EDGE,"E28.6.2");var subQ67=sQuery(id+"F3.wireOp",EDGE,"E20.14.3");var subQ69=sQuery(id+"F3.wireOp",EDGE,"E20.14.1");var subQ70=sQuery(id+"F3.wireOp",EDGE,"E20.14.0");var subQ71=makeQuery(id+"F29.opLoft","SWEPT_FACE",FACE,{"disambiguationData":[OSD([subQ70,subQ69,subQ67,sQuery(id+"F22.wireOp",EDGE,"E28.6.1"),subQ66,subQ65])]});var subQ72=sQuery(id+"F22.wireOp",EDGE,"E28.5.3");var subQ73=sQuery(id+"F22.wireOp",EDGE,"E28.5.2");var subQ74=sQuery(id+"F3.wireOp",EDGE,"E20.13.3");var subQ76=sQuery(id+"F3.wireOp",EDGE,"E20.13.1");var subQ77=sQuery(id+"F3.wireOp",EDGE,"E20.13.0");var subQ78=makeQuery(id+"F28.opLoft","SWEPT_FACE",FACE,{"disambiguationData":[OSD([subQ77,subQ76,subQ74,sQuery(id+"F22.wireOp",EDGE,"E28.5.1"),subQ73,subQ72])]});var subQ79=sQuery(id+"F22.wireOp",EDGE,"E28.4.3");var subQ80=sQuery(id+"F22.wireOp",EDGE,"E28.4.2");var subQ81=sQuery(id+"F3.wireOp",EDGE,"E20.12.3");var subQ83=sQuery(id+"F3.wireOp",EDGE,"E20.12.1");var subQ84=sQuery(id+"F3.wireOp",EDGE,"E20.12.0");var subQ85=makeQuery(id+"F27.opLoft","SWEPT_FACE",FACE,{"disambiguationData":[OSD([subQ84,subQ83,subQ81,sQuery(id+"F22.wireOp",EDGE,"E28.4.1"),subQ80,subQ79])]});var subQ86=sQuery(id+"F22.wireOp",EDGE,"E28.3.3");var subQ87=sQuery(id+"F22.wireOp",EDGE,"E28.3.2");var subQ88=sQuery(id+"F3.wireOp",EDGE,"E20.11.3");var subQ90=sQuery(id+"F3.wireOp",EDGE,"E20.11.1");var subQ91=sQuery(id+"F3.wireOp",EDGE,"E20.11.0");var subQ92=makeQuery(id+"F26.opLoft","SWEPT_FACE",FACE,{"disambiguationData":[OSD([subQ91,subQ90,subQ88,sQuery(id+"F22.wireOp",EDGE,"E28.3.1"),subQ87,subQ86])]});var subQ93=sQuery(id+"F22.wireOp",EDGE,"E28.2.3");var subQ94=sQuery(id+"F22.wireOp",EDGE,"E28.2.2");var subQ95=sQuery(id+"F3.wireOp",EDGE,"E20.10.3");var subQ96=sQuery(id+"F3.wireOp",EDGE,"E20.10.1");var subQ97=sQuery(id+"F3.wireOp",EDGE,"E20.10.0");var subQ98=makeQuery(id+"F25.opLoft","SWEPT_FACE",FACE,{"disambiguationData":[OSD([subQ97,subQ96,subQ95,sQuery(id+"F22.wireOp",EDGE,"E28.2.1"),subQ94,subQ93])]});var subQ100=sQuery(id+"F22.wireOp",EDGE,"E28.1.3");var subQ101=sQuery(id+"F22.wireOp",EDGE,"E28.1.2");var subQ102=sQuery(id+"F3.wireOp",EDGE,"E20.9.3");var subQ103=sQuery(id+"F3.wireOp",EDGE,"E20.9.1");var subQ104=sQuery(id+"F3.wireOp",EDGE,"E20.9.0");var subQ105=makeQuery(id+"F24.opLoft","SWEPT_FACE",FACE,{"disambiguationData":[OSD([subQ104,subQ103,subQ102,sQuery(id+"F22.wireOp",EDGE,"E28.1.1"),subQ101,subQ100])]});var subQ106=sQuery(id+"F22.wireOp",EDGE,"E27.top");var subQ107=sQuery(id+"F22.wireOp",EDGE,"E27.bottom");var subQ108=sQuery(id+"F3.wireOp",EDGE,"E20.8.3");var subQ110=sQuery(id+"F3.wireOp",EDGE,"E20.8.1");var subQ114=makeQuery(id+"F42.boolean.opBoolean","COPY",FACE,{"disambiguationData":[TD([subQ43])],"derivedFrom":subQ10});var subQ146=makeQuery(id+"F14.opLoft","CAP_FACE",FACE,{"disambiguationData":[OSD([makeQuery(id+"F3.imprint","IMPRINT",FACE,{"disambiguationData":[TD([[makeQuery(id+"F3.imprint","IMPRINT",EDGE,{"derivedFrom":subQ8}),-1.0]])]})])],"isStart":true});var subQ157=makeQuery(id+"F5.opLoft","CAP_FACE",FACE,{"disambiguationData":[OSD([makeQuery(id+"F3.imprint","IMPRINT",FACE,{"disambiguationData":[TD([[makeQuery(id+"F3.imprint","IMPRINT",EDGE,{"derivedFrom":subQ55}),1.0]])]})])],"isStart":true});var subQ186=makeQuery(id+"F33.boolean.opBoolean","INTERSECT",EDGE,{"derivedFrom":[makeQuery(id+"F32.boolean.opBoolean","SPLIT",FACE,{"disambiguationData":[TD([subQ146])],"derivedFrom":makeQuery(id+"F31.boolean.opBoolean","SPLIT",FACE,{"disambiguationData":[TD([subQ146])],"derivedFrom":makeQuery(id+"F30.boolean.opBoolean","SPLIT",FACE,{"disambiguationData":[TD([subQ157])],"derivedFrom":makeQuery(id+"F29.boolean.opBoolean","SPLIT",FACE,{"disambiguationData":[TD([subQ157])],"derivedFrom":makeQuery(id+"F28.boolean.opBoolean","SPLIT",FACE,{"disambiguationData":[TD([subQ157])],"derivedFrom":makeQuery(id+"F27.boolean.opBoolean","SPLIT",FACE,{"disambiguationData":[TD([subQ157])],"derivedFrom":makeQuery(id+"F26.boolean.opBoolean","SPLIT",FACE,{"disambiguationData":[TD([subQ157])],"derivedFrom":makeQuery(id+"F25.boolean.opBoolean","SPLIT",FACE,{"disambiguationData":[TD([subQ157])],"derivedFrom":makeQuery(id+"F24.boolean.opBoolean","SPLIT",FACE,{"disambiguationData":[TD([subQ157])],"derivedFrom":makeQuery(id+"F1.opRevolve","SWEPT_FACE",FACE,{"disambiguationData":[OSD([sQuery(id+"F0.wireOp",EDGE,"E13")])]})})})})})})})})})}),subQ43]});Q11=makeQuery(id+"F48.opFillet","BLEND_EDGE",EDGE,{"blendedFrom":[makeQuery(id+"F47.opFillet","TWEAK_EDGE",EDGE,{"derivedFrom":[makeQuery(id+"F45.opFillet","BLEND_VERTEX",VERTEX,{"blendedFrom":[subQ186,subQ43,subQ114],"blendedInto":[subQ43,subQ114]}),makeQuery(id+"F45.opFillet","BLEND_VERTEX",VERTEX,{"blendedFrom":[subQ186,makeQuery(id+"F42.boolean.opBoolean","MERGE",FACE,{"derivedFrom":[subQ2,subQ1]}),subQ114],"blendedInto":[makeQuery(id+"F42.boolean.opBoolean","MERGE",FACE,{"derivedFrom":[subQ2,subQ1]}),subQ114]})]}),makeQuery(id+"F47.opFillet","BLEND_FACE",FACE,{"disambiguationData":[OSD([subQ0,subQ9]),TDD([makeQuery(id+"F42.boolean.opBoolean","COPY",EDGE,{"disambiguationData":[TD([makeQuery(id+"F23.opLoft","SWEPT_FACE",FACE,{"disambiguationData":[OSD([sQuery(id+"F3.wireOp",EDGE,"E20.8.0"),subQ110,subQ108,subQ107,subQ106,sQuery(id+"F22.wireOp",EDGE,"E27.right")])]})])],"derivedFrom":subQ11})])]}),makeQuery(id+"F47.opFillet","BLEND_FACE",FACE,{"disambiguationData":[OSD([subQ0,subQ9]),TDD([makeQuery(id+"F42.boolean.opBoolean","COPY",EDGE,{"disambiguationData":[TD([subQ105])],"derivedFrom":subQ11})])]}),makeQuery(id+"F47.opFillet","BLEND_FACE",FACE,{"disambiguationData":[OSD([subQ0,subQ9]),TDD([makeQuery(id+"F42.boolean.opBoolean","COPY",EDGE,{"disambiguationData":[TD([subQ98])],"derivedFrom":subQ11})])]}),makeQuery(id+"F47.opFillet","BLEND_FACE",FACE,{"disambiguationData":[OSD([subQ0,subQ9]),TDD([makeQuery(id+"F42.boolean.opBoolean","COPY",EDGE,{"disambiguationData":[TD([subQ92])],"derivedFrom":subQ11})])]}),makeQuery(id+"F47.opFillet","BLEND_FACE",FACE,{"disambiguationData":[OSD([subQ0,subQ9]),TDD([makeQuery(id+"F42.boolean.opBoolean","COPY",EDGE,{"disambiguationData":[TD([subQ85])],"derivedFrom":subQ11})])]}),makeQuery(id+"F47.opFillet","BLEND_FACE",FACE,{"disambiguationData":[OSD([subQ0,subQ9]),TDD([makeQuery(id+"F42.boolean.opBoolean","COPY",EDGE,{"disambiguationData":[TD([subQ78])],"derivedFrom":subQ11})])]}),makeQuery(id+"F47.opFillet","BLEND_FACE",FACE,{"disambiguationData":[OSD([subQ0,subQ9]),TDD([makeQuery(id+"F42.boolean.opBoolean","COPY",EDGE,{"disambiguationData":[TD([subQ71])],"derivedFrom":subQ11})])]}),makeQuery(id+"F47.opFillet","BLEND_FACE",FACE,{"disambiguationData":[OSD([subQ0,subQ9]),TDD([makeQuery(id+"F42.boolean.opBoolean","COPY",EDGE,{"disambiguationData":[TD([subQ63])],"derivedFrom":subQ11})])]}),makeQuery(id+"F47.opFillet","BLEND_FACE",FACE,{"disambiguationData":[OSD([subQ0,subQ9]),TDD([makeQuery(id+"F42.boolean.opBoolean","COPY",EDGE,{"disambiguationData":[TD([subQ57])],"derivedFrom":subQ11})])]}),makeQuery(id+"F47.opFillet","BLEND_FACE",FACE,{"disambiguationData":[OSD([subQ0,subQ9]),TDD([makeQuery(id+"F42.boolean.opBoolean","COPY",EDGE,{"disambiguationData":[TD([subQ50])],"derivedFrom":subQ11})])]}),makeQuery(id+"F47.opFillet","BLEND_FACE",FACE,{"disambiguationData":[OSD([subQ0,subQ9]),TDD([makeQuery(id+"F42.boolean.opBoolean","COPY",EDGE,{"disambiguationData":[TD([subQ43])],"derivedFrom":subQ11})])]}),makeQuery(id+"F47.opFillet","BLEND_FACE",FACE,{"disambiguationData":[OSD([subQ0,subQ9]),TDD([makeQuery(id+"F42.boolean.opBoolean","COPY",EDGE,{"disambiguationData":[TD([makeQuery(id+"F34.opLoft","SWEPT_FACE",FACE,{"disambiguationData":[OSD([subQ35,subQ34,subQ32,sQuery(id+"F22.wireOp",EDGE,"E28.11.1"),subQ31,subQ30])]})])],"derivedFrom":subQ11})])]}),makeQuery(id+"F47.opFillet","BLEND_FACE",FACE,{"disambiguationData":[OSD([subQ0,subQ9]),TDD([makeQuery(id+"F42.boolean.opBoolean","COPY",EDGE,{"disambiguationData":[TD([makeQuery(id+"F35.opLoft","SWEPT_FACE",FACE,{"disambiguationData":[OSD([subQ29,subQ28,subQ26,sQuery(id+"F22.wireOp",EDGE,"E28.12.1"),subQ25,subQ24])]})])],"derivedFrom":subQ11})])]}),makeQuery(id+"F47.opFillet","BLEND_FACE",FACE,{"disambiguationData":[OSD([subQ0,subQ9]),TDD([makeQuery(id+"F42.boolean.opBoolean","COPY",EDGE,{"disambiguationData":[TD([makeQuery(id+"F36.opLoft","SWEPT_FACE",FACE,{"disambiguationData":[OSD([subQ23,subQ22,subQ20,sQuery(id+"F22.wireOp",EDGE,"E28.13.1"),subQ19,subQ18])]})])],"derivedFrom":subQ11})])]}),makeQuery(id+"F47.opFillet","BLEND_FACE",FACE,{"disambiguationData":[OSD([subQ0,subQ9]),TDD([makeQuery(id+"F42.boolean.opBoolean","COPY",EDGE,{"disambiguationData":[TD([makeQuery(id+"F37.opLoft","SWEPT_FACE",FACE,{"disambiguationData":[OSD([subQ16,subQ15,subQ14,sQuery(id+"F22.wireOp",EDGE,"E28.14.1"),subQ13,subQ12])]})])],"derivedFrom":subQ11})])]}),makeQuery(id+"F47.opFillet","BLEND_FACE",FACE,{"disambiguationData":[OSD([subQ0,subQ9]),TDD([makeQuery(id+"F42.boolean.opBoolean","COPY",EDGE,{"disambiguationData":[TD([makeQuery(id+"F38.opLoft","SWEPT_FACE",FACE,{"disambiguationData":[OSD([subQ8,subQ7,subQ5,sQuery(id+"F22.wireOp",EDGE,"E28.15.1"),subQ4,subQ3])]})])],"derivedFrom":subQ11})])]})],"blendedInto":[makeQuery(id+"F47.opFillet","BLEND_FACE",FACE,{"disambiguationData":[OSD([subQ0,subQ9]),TDD([makeQuery(id+"F42.boolean.opBoolean","COPY",EDGE,{"disambiguationData":[TD([makeQuery(id+"F23.opLoft","SWEPT_FACE",FACE,{"disambiguationData":[OSD([sQuery(id+"F3.wireOp",EDGE,"E20.8.0"),subQ110,subQ108,subQ107,subQ106,sQuery(id+"F22.wireOp",EDGE,"E27.right")])]})])],"derivedFrom":subQ11})])]}),makeQuery(id+"F47.opFillet","BLEND_FACE",FACE,{"disambiguationData":[OSD([subQ0,subQ9]),TDD([makeQuery(id+"F42.boolean.opBoolean","COPY",EDGE,{"disambiguationData":[TD([subQ105])],"derivedFrom":subQ11})])]}),makeQuery(id+"F47.opFillet","BLEND_FACE",FACE,{"disambiguationData":[OSD([subQ0,subQ9]),TDD([makeQuery(id+"F42.boolean.opBoolean","COPY",EDGE,{"disambiguationData":[TD([subQ98])],"derivedFrom":subQ11})])]}),makeQuery(id+"F47.opFillet","BLEND_FACE",FACE,{"disambiguationData":[OSD([subQ0,subQ9]),TDD([makeQuery(id+"F42.boolean.opBoolean","COPY",EDGE,{"disambiguationData":[TD([subQ92])],"derivedFrom":subQ11})])]}),makeQuery(id+"F47.opFillet","BLEND_FACE",FACE,{"disambiguationData":[OSD([subQ0,subQ9]),TDD([makeQuery(id+"F42.boolean.opBoolean","COPY",EDGE,{"disambiguationData":[TD([subQ85])],"derivedFrom":subQ11})])]}),makeQuery(id+"F47.opFillet","BLEND_FACE",FACE,{"disambiguationData":[OSD([subQ0,subQ9]),TDD([makeQuery(id+"F42.boolean.opBoolean","COPY",EDGE,{"disambiguationData":[TD([subQ78])],"derivedFrom":subQ11})])]}),makeQuery(id+"F47.opFillet","BLEND_FACE",FACE,{"disambiguationData":[OSD([subQ0,subQ9]),TDD([makeQuery(id+"F42.boolean.opBoolean","COPY",EDGE,{"disambiguationData":[TD([subQ71])],"derivedFrom":subQ11})])]}),makeQuery(id+"F47.opFillet","BLEND_FACE",FACE,{"disambiguationData":[OSD([subQ0,subQ9]),TDD([makeQuery(id+"F42.boolean.opBoolean","COPY",EDGE,{"disambiguationData":[TD([subQ63])],"derivedFrom":subQ11})])]}),makeQuery(id+"F47.opFillet","BLEND_FACE",FACE,{"disambiguationData":[OSD([subQ0,subQ9]),TDD([makeQuery(id+"F42.boolean.opBoolean","COPY",EDGE,{"disambiguationData":[TD([subQ57])],"derivedFrom":subQ11})])]}),makeQuery(id+"F47.opFillet","BLEND_FACE",FACE,{"disambiguationData":[OSD([subQ0,subQ9]),TDD([makeQuery(id+"F42.boolean.opBoolean","COPY",EDGE,{"disambiguationData":[TD([subQ50])],"derivedFrom":subQ11})])]}),makeQuery(id+"F47.opFillet","BLEND_FACE",FACE,{"disambiguationData":[OSD([subQ0,subQ9]),TDD([makeQuery(id+"F42.boolean.opBoolean","COPY",EDGE,{"disambiguationData":[TD([subQ43])],"derivedFrom":subQ11})])]}),makeQuery(id+"F47.opFillet","BLEND_FACE",FACE,{"disambiguationData":[OSD([subQ0,subQ9]),TDD([makeQuery(id+"F42.boolean.opBoolean","COPY",EDGE,{"disambiguationData":[TD([makeQuery(id+"F34.opLoft","SWEPT_FACE",FACE,{"disambiguationData":[OSD([subQ35,subQ34,subQ32,sQuery(id+"F22.wireOp",EDGE,"E28.11.1"),subQ31,subQ30])]})])],"derivedFrom":subQ11})])]}),makeQuery(id+"F47.opFillet","BLEND_FACE",FACE,{"disambiguationData":[OSD([subQ0,subQ9]),TDD([makeQuery(id+"F42.boolean.opBoolean","COPY",EDGE,{"disambiguationData":[TD([makeQuery(id+"F35.opLoft","SWEPT_FACE",FACE,{"disambiguationData":[OSD([subQ29,subQ28,subQ26,sQuery(id+"F22.wireOp",EDGE,"E28.12.1"),subQ25,subQ24])]})])],"derivedFrom":subQ11})])]}),makeQuery(id+"F47.opFillet","BLEND_FACE",FACE,{"disambiguationData":[OSD([subQ0,subQ9]),TDD([makeQuery(id+"F42.boolean.opBoolean","COPY",EDGE,{"disambiguationData":[TD([makeQuery(id+"F36.opLoft","SWEPT_FACE",FACE,{"disambiguationData":[OSD([subQ23,subQ22,subQ20,sQuery(id+"F22.wireOp",EDGE,"E28.13.1"),subQ19,subQ18])]})])],"derivedFrom":subQ11})])]}),makeQuery(id+"F47.opFillet","BLEND_FACE",FACE,{"disambiguationData":[OSD([subQ0,subQ9]),TDD([makeQuery(id+"F42.boolean.opBoolean","COPY",EDGE,{"disambiguationData":[TD([makeQuery(id+"F37.opLoft","SWEPT_FACE",FACE,{"disambiguationData":[OSD([subQ16,subQ15,subQ14,sQuery(id+"F22.wireOp",EDGE,"E28.14.1"),subQ13,subQ12])]})])],"derivedFrom":subQ11})])]}),makeQuery(id+"F47.opFillet","BLEND_FACE",FACE,{"disambiguationData":[OSD([subQ0,subQ9]),TDD([makeQuery(id+"F42.boolean.opBoolean","COPY",EDGE,{"disambiguationData":[TD([makeQuery(id+"F38.opLoft","SWEPT_FACE",FACE,{"disambiguationData":[OSD([subQ8,subQ7,subQ5,sQuery(id+"F22.wireOp",EDGE,"E28.15.1"),subQ4,subQ3])]})])],"derivedFrom":subQ11})])]})]});}
            var Q12;
            {var subQ0=sQuery(id+"F22.wireOp",EDGE,"E28.10.0");var subQ1=sQuery(id+"F22.wireOp",EDGE,"E28.10.1");var subQ2=sQuery(id+"F22.wireOp",EDGE,"E28.10.2");var subQ3=sQuery(id+"F22.wireOp",EDGE,"E28.10.3");var subQ4=sQuery(id+"F3.wireOp",EDGE,"E20.2.3");var subQ5=sQuery(id+"F3.wireOp",EDGE,"E20.2.1");var subQ6=makeQuery(id+"F33.opLoft","SWEPT_FACE",FACE,{"disambiguationData":[OSD([subQ5,sQuery(id+"F3.wireOp",EDGE,"E20.2.2"),subQ4,subQ0,subQ2,subQ3])]});var subQ7=sQuery(id+"F41.wireOp",EDGE,"E34");var subQ8=sQuery(id+"F41.wireOp",EDGE,"E32");Q12=makeQuery(id+"F44.opFillet","BLEND_EDGE",EDGE,{"blendedFrom":[makeQuery(id+"F40.boolean.opBoolean","INTERSECT",EDGE,{"derivedFrom":[subQ6,makeQuery(id+"F40.opExtrude","CAP_FACE",FACE,{"disambiguationData":[OSD([sQuery(id+"F39.wireOp",EDGE,"E29"),sQuery(id+"F39.wireOp",EDGE,"E30")])],"isStart":true})]}),makeQuery(id+"F42.boolean.opBoolean","COPY",FACE,{"disambiguationData":[TD([makeQuery(id+"F33.opLoft","SWEPT_FACE",FACE,{"disambiguationData":[OSD([sQuery(id+"F3.wireOp",EDGE,"E20.2.0"),subQ5,subQ4,subQ1,subQ2,subQ3])]})])],"derivedFrom":makeQuery(id+"F42.opRevolve","SWEPT_FACE",FACE,{"disambiguationData":[OSD([subQ8]),TDD([makeQuery(id+"F41.imprint","IMPRINT",EDGE,{"disambiguationData":[TD([[makeQuery(id+"F41.imprint","INTERSECT",VERTEX,{"disambiguationData":[OD(0.0)],"derivedFrom":[subQ8,subQ7]}),-1.0]])],"derivedFrom":subQ8})])]})})],"blendedInto":[makeQuery(id+"F42.boolean.opBoolean","COPY",FACE,{"disambiguationData":[TD([makeQuery(id+"F33.opLoft","SWEPT_FACE",FACE,{"disambiguationData":[OSD([sQuery(id+"F3.wireOp",EDGE,"E20.2.0"),subQ5,subQ4,subQ1,subQ2,subQ3])]})])],"derivedFrom":makeQuery(id+"F42.opRevolve","SWEPT_FACE",FACE,{"disambiguationData":[OSD([subQ8]),TDD([makeQuery(id+"F41.imprint","IMPRINT",EDGE,{"disambiguationData":[TD([[makeQuery(id+"F41.imprint","INTERSECT",VERTEX,{"disambiguationData":[OD(0.0)],"derivedFrom":[subQ8,subQ7]}),-1.0]])],"derivedFrom":subQ8})])]})})]});}
            var Q13;
            {var subQ0=sQuery(id+"F41.wireOp",EDGE,"E34");var subQ1=sQuery(id+"F41.wireOp",EDGE,"E32");Q13=makeQuery(id+"F42.boolean.opBoolean","INTERSECT",EDGE,{"derivedFrom":[makeQuery(id+"F32.opLoft","SWEPT_FACE",FACE,{"disambiguationData":[OSD([sQuery(id+"F3.wireOp",EDGE,"E20.1.0"),sQuery(id+"F3.wireOp",EDGE,"E20.1.1"),sQuery(id+"F3.wireOp",EDGE,"E20.1.3"),sQuery(id+"F22.wireOp",EDGE,"E28.9.1"),sQuery(id+"F22.wireOp",EDGE,"E28.9.2"),sQuery(id+"F22.wireOp",EDGE,"E28.9.3")])]}),makeQuery(id+"F42.opRevolve","SWEPT_FACE",FACE,{"disambiguationData":[OSD([subQ1]),TDD([makeQuery(id+"F41.imprint","IMPRINT",EDGE,{"disambiguationData":[TD([[makeQuery(id+"F41.imprint","INTERSECT",VERTEX,{"disambiguationData":[OD(0.0)],"derivedFrom":[subQ1,subQ0]}),-1.0]])],"derivedFrom":subQ1})])]})]});}
            var Q14;
            {var subQ0=sQuery(id+"F41.wireOp",EDGE,"E37");var subQ1=makeQuery(id+"F42.opRevolve","SWEPT_FACE",FACE,{"disambiguationData":[OSD([subQ0])]});var subQ2=makeQuery(id+"F40.opExtrude","CAP_FACE",FACE,{"disambiguationData":[OSD([sQuery(id+"F39.wireOp",EDGE,"E29"),sQuery(id+"F39.wireOp",EDGE,"E30")])],"isStart":true});var subQ3=sQuery(id+"F22.wireOp",EDGE,"E28.15.3");var subQ4=sQuery(id+"F22.wireOp",EDGE,"E28.15.2");var subQ5=sQuery(id+"F3.wireOp",EDGE,"E20.7.3");var subQ7=sQuery(id+"F3.wireOp",EDGE,"E20.7.1");var subQ8=sQuery(id+"F3.wireOp",EDGE,"E20.7.0");var subQ9=sQuery(id+"F41.wireOp",EDGE,"E38");var subQ10=makeQuery(id+"F42.opRevolve","SWEPT_FACE",FACE,{"disambiguationData":[OSD([subQ9])]});var subQ11=makeQuery(id+"F42.opRevolve","SWEPT_EDGE",EDGE,{"disambiguationData":[OSD([subQ0,subQ9])]});var subQ12=sQuery(id+"F22.wireOp",EDGE,"E28.14.3");var subQ13=sQuery(id+"F22.wireOp",EDGE,"E28.14.2");var subQ14=sQuery(id+"F3.wireOp",EDGE,"E20.6.3");var subQ15=sQuery(id+"F3.wireOp",EDGE,"E20.6.1");var subQ16=sQuery(id+"F3.wireOp",EDGE,"E20.6.0");var subQ18=sQuery(id+"F22.wireOp",EDGE,"E28.13.3");var subQ19=sQuery(id+"F22.wireOp",EDGE,"E28.13.2");var subQ20=sQuery(id+"F3.wireOp",EDGE,"E20.5.3");var subQ22=sQuery(id+"F3.wireOp",EDGE,"E20.5.1");var subQ23=sQuery(id+"F3.wireOp",EDGE,"E20.5.0");var subQ24=sQuery(id+"F22.wireOp",EDGE,"E28.12.3");var subQ25=sQuery(id+"F22.wireOp",EDGE,"E28.12.2");var subQ26=sQuery(id+"F3.wireOp",EDGE,"E20.4.3");var subQ28=sQuery(id+"F3.wireOp",EDGE,"E20.4.1");var subQ29=sQuery(id+"F3.wireOp",EDGE,"E20.4.0");var subQ30=sQuery(id+"F22.wireOp",EDGE,"E28.11.3");var subQ31=sQuery(id+"F22.wireOp",EDGE,"E28.11.2");var subQ32=sQuery(id+"F3.wireOp",EDGE,"E20.3.3");var subQ34=sQuery(id+"F3.wireOp",EDGE,"E20.3.1");var subQ35=sQuery(id+"F3.wireOp",EDGE,"E20.3.0");var subQ36=sQuery(id+"F22.wireOp",EDGE,"E28.10.3");var subQ37=sQuery(id+"F22.wireOp",EDGE,"E28.10.2");var subQ38=sQuery(id+"F3.wireOp",EDGE,"E20.2.3");var subQ40=sQuery(id+"F3.wireOp",EDGE,"E20.2.1");var subQ41=sQuery(id+"F3.wireOp",EDGE,"E20.2.0");var subQ42=sQuery(id+"F22.wireOp",EDGE,"E28.9.3");var subQ43=sQuery(id+"F22.wireOp",EDGE,"E28.9.2");var subQ44=sQuery(id+"F3.wireOp",EDGE,"E20.1.3");var subQ46=sQuery(id+"F3.wireOp",EDGE,"E20.1.1");var subQ48=sQuery(id+"F3.wireOp",EDGE,"E20.1.0");var subQ49=makeQuery(id+"F32.opLoft","SWEPT_FACE",FACE,{"disambiguationData":[OSD([subQ48,subQ46,subQ44,sQuery(id+"F22.wireOp",EDGE,"E28.9.1"),subQ43,subQ42])]});var subQ50=sQuery(id+"F22.wireOp",EDGE,"E28.8.3");var subQ51=sQuery(id+"F22.wireOp",EDGE,"E28.8.2");var subQ53=sQuery(id+"F3.wireOp",EDGE,"E18.top");var subQ54=sQuery(id+"F3.wireOp",EDGE,"E18.bottom");var subQ55=sQuery(id+"F3.wireOp",EDGE,"E18.left");var subQ56=makeQuery(id+"F31.opLoft","SWEPT_FACE",FACE,{"disambiguationData":[OSD([subQ54,subQ53,subQ55,sQuery(id+"F22.wireOp",EDGE,"E28.8.1"),subQ51,subQ50])]});var subQ57=sQuery(id+"F22.wireOp",EDGE,"E28.7.3");var subQ58=sQuery(id+"F22.wireOp",EDGE,"E28.7.2");var subQ59=sQuery(id+"F3.wireOp",EDGE,"E20.15.3");var subQ60=sQuery(id+"F3.wireOp",EDGE,"E20.15.1");var subQ61=sQuery(id+"F3.wireOp",EDGE,"E20.15.0");var subQ62=makeQuery(id+"F30.opLoft","SWEPT_FACE",FACE,{"disambiguationData":[OSD([subQ61,subQ60,subQ59,sQuery(id+"F22.wireOp",EDGE,"E28.7.1"),subQ58,subQ57])]});var subQ64=sQuery(id+"F22.wireOp",EDGE,"E28.6.3");var subQ65=sQuery(id+"F22.wireOp",EDGE,"E28.6.2");var subQ66=sQuery(id+"F3.wireOp",EDGE,"E20.14.3");var subQ68=sQuery(id+"F3.wireOp",EDGE,"E20.14.1");var subQ69=sQuery(id+"F3.wireOp",EDGE,"E20.14.0");var subQ70=makeQuery(id+"F29.opLoft","SWEPT_FACE",FACE,{"disambiguationData":[OSD([subQ69,subQ68,subQ66,sQuery(id+"F22.wireOp",EDGE,"E28.6.1"),subQ65,subQ64])]});var subQ71=sQuery(id+"F22.wireOp",EDGE,"E28.5.3");var subQ72=sQuery(id+"F22.wireOp",EDGE,"E28.5.2");var subQ73=sQuery(id+"F3.wireOp",EDGE,"E20.13.3");var subQ75=sQuery(id+"F3.wireOp",EDGE,"E20.13.1");var subQ76=sQuery(id+"F3.wireOp",EDGE,"E20.13.0");var subQ77=makeQuery(id+"F28.opLoft","SWEPT_FACE",FACE,{"disambiguationData":[OSD([subQ76,subQ75,subQ73,sQuery(id+"F22.wireOp",EDGE,"E28.5.1"),subQ72,subQ71])]});var subQ78=sQuery(id+"F22.wireOp",EDGE,"E28.4.3");var subQ79=sQuery(id+"F22.wireOp",EDGE,"E28.4.2");var subQ80=sQuery(id+"F3.wireOp",EDGE,"E20.12.3");var subQ82=sQuery(id+"F3.wireOp",EDGE,"E20.12.1");var subQ83=sQuery(id+"F3.wireOp",EDGE,"E20.12.0");var subQ84=makeQuery(id+"F27.opLoft","SWEPT_FACE",FACE,{"disambiguationData":[OSD([subQ83,subQ82,subQ80,sQuery(id+"F22.wireOp",EDGE,"E28.4.1"),subQ79,subQ78])]});var subQ85=sQuery(id+"F22.wireOp",EDGE,"E28.3.3");var subQ86=sQuery(id+"F22.wireOp",EDGE,"E28.3.2");var subQ87=sQuery(id+"F3.wireOp",EDGE,"E20.11.3");var subQ89=sQuery(id+"F3.wireOp",EDGE,"E20.11.1");var subQ90=sQuery(id+"F3.wireOp",EDGE,"E20.11.0");var subQ91=makeQuery(id+"F26.opLoft","SWEPT_FACE",FACE,{"disambiguationData":[OSD([subQ90,subQ89,subQ87,sQuery(id+"F22.wireOp",EDGE,"E28.3.1"),subQ86,subQ85])]});var subQ92=sQuery(id+"F22.wireOp",EDGE,"E28.2.3");var subQ93=sQuery(id+"F22.wireOp",EDGE,"E28.2.2");var subQ94=sQuery(id+"F3.wireOp",EDGE,"E20.10.3");var subQ95=sQuery(id+"F3.wireOp",EDGE,"E20.10.1");var subQ96=sQuery(id+"F3.wireOp",EDGE,"E20.10.0");var subQ97=makeQuery(id+"F25.opLoft","SWEPT_FACE",FACE,{"disambiguationData":[OSD([subQ96,subQ95,subQ94,sQuery(id+"F22.wireOp",EDGE,"E28.2.1"),subQ93,subQ92])]});var subQ99=sQuery(id+"F22.wireOp",EDGE,"E28.1.3");var subQ100=sQuery(id+"F22.wireOp",EDGE,"E28.1.2");var subQ101=sQuery(id+"F3.wireOp",EDGE,"E20.9.3");var subQ102=sQuery(id+"F3.wireOp",EDGE,"E20.9.1");var subQ103=sQuery(id+"F3.wireOp",EDGE,"E20.9.0");var subQ104=makeQuery(id+"F24.opLoft","SWEPT_FACE",FACE,{"disambiguationData":[OSD([subQ103,subQ102,subQ101,sQuery(id+"F22.wireOp",EDGE,"E28.1.1"),subQ100,subQ99])]});var subQ105=sQuery(id+"F22.wireOp",EDGE,"E27.top");var subQ106=sQuery(id+"F22.wireOp",EDGE,"E27.bottom");var subQ107=sQuery(id+"F3.wireOp",EDGE,"E20.8.3");var subQ109=sQuery(id+"F3.wireOp",EDGE,"E20.8.1");var subQ113=makeQuery(id+"F42.boolean.opBoolean","COPY",FACE,{"disambiguationData":[TD([subQ49])],"derivedFrom":subQ10});var subQ151=makeQuery(id+"F14.opLoft","CAP_FACE",FACE,{"disambiguationData":[OSD([makeQuery(id+"F3.imprint","IMPRINT",FACE,{"disambiguationData":[TD([[makeQuery(id+"F3.imprint","IMPRINT",EDGE,{"derivedFrom":subQ8}),-1.0]])]})])],"isStart":true});var subQ156=makeQuery(id+"F5.opLoft","CAP_FACE",FACE,{"disambiguationData":[OSD([makeQuery(id+"F3.imprint","IMPRINT",FACE,{"disambiguationData":[TD([[makeQuery(id+"F3.imprint","IMPRINT",EDGE,{"derivedFrom":subQ54}),1.0]])]})])],"isStart":true});var subQ185=makeQuery(id+"F32.boolean.opBoolean","INTERSECT",EDGE,{"derivedFrom":[makeQuery(id+"F31.boolean.opBoolean","SPLIT",FACE,{"disambiguationData":[TD([subQ151])],"derivedFrom":makeQuery(id+"F30.boolean.opBoolean","SPLIT",FACE,{"disambiguationData":[TD([subQ156])],"derivedFrom":makeQuery(id+"F29.boolean.opBoolean","SPLIT",FACE,{"disambiguationData":[TD([subQ156])],"derivedFrom":makeQuery(id+"F28.boolean.opBoolean","SPLIT",FACE,{"disambiguationData":[TD([subQ156])],"derivedFrom":makeQuery(id+"F27.boolean.opBoolean","SPLIT",FACE,{"disambiguationData":[TD([subQ156])],"derivedFrom":makeQuery(id+"F26.boolean.opBoolean","SPLIT",FACE,{"disambiguationData":[TD([subQ156])],"derivedFrom":makeQuery(id+"F25.boolean.opBoolean","SPLIT",FACE,{"disambiguationData":[TD([subQ156])],"derivedFrom":makeQuery(id+"F24.boolean.opBoolean","SPLIT",FACE,{"disambiguationData":[TD([subQ156])],"derivedFrom":makeQuery(id+"F1.opRevolve","SWEPT_FACE",FACE,{"disambiguationData":[OSD([sQuery(id+"F0.wireOp",EDGE,"E13")])]})})})})})})})})}),subQ49]});Q14=makeQuery(id+"F48.opFillet","BLEND_EDGE",EDGE,{"blendedFrom":[makeQuery(id+"F47.opFillet","TWEAK_EDGE",EDGE,{"derivedFrom":[makeQuery(id+"F45.opFillet","BLEND_VERTEX",VERTEX,{"blendedFrom":[subQ185,subQ49,subQ113],"blendedInto":[subQ49,subQ113]}),makeQuery(id+"F45.opFillet","BLEND_VERTEX",VERTEX,{"blendedFrom":[subQ185,makeQuery(id+"F42.boolean.opBoolean","MERGE",FACE,{"derivedFrom":[subQ2,subQ1]}),subQ113],"blendedInto":[makeQuery(id+"F42.boolean.opBoolean","MERGE",FACE,{"derivedFrom":[subQ2,subQ1]}),subQ113]})]}),makeQuery(id+"F47.opFillet","BLEND_FACE",FACE,{"disambiguationData":[OSD([subQ0,subQ9]),TDD([makeQuery(id+"F42.boolean.opBoolean","COPY",EDGE,{"disambiguationData":[TD([makeQuery(id+"F23.opLoft","SWEPT_FACE",FACE,{"disambiguationData":[OSD([sQuery(id+"F3.wireOp",EDGE,"E20.8.0"),subQ109,subQ107,subQ106,subQ105,sQuery(id+"F22.wireOp",EDGE,"E27.right")])]})])],"derivedFrom":subQ11})])]}),makeQuery(id+"F47.opFillet","BLEND_FACE",FACE,{"disambiguationData":[OSD([subQ0,subQ9]),TDD([makeQuery(id+"F42.boolean.opBoolean","COPY",EDGE,{"disambiguationData":[TD([subQ104])],"derivedFrom":subQ11})])]}),makeQuery(id+"F47.opFillet","BLEND_FACE",FACE,{"disambiguationData":[OSD([subQ0,subQ9]),TDD([makeQuery(id+"F42.boolean.opBoolean","COPY",EDGE,{"disambiguationData":[TD([subQ97])],"derivedFrom":subQ11})])]}),makeQuery(id+"F47.opFillet","BLEND_FACE",FACE,{"disambiguationData":[OSD([subQ0,subQ9]),TDD([makeQuery(id+"F42.boolean.opBoolean","COPY",EDGE,{"disambiguationData":[TD([subQ91])],"derivedFrom":subQ11})])]}),makeQuery(id+"F47.opFillet","BLEND_FACE",FACE,{"disambiguationData":[OSD([subQ0,subQ9]),TDD([makeQuery(id+"F42.boolean.opBoolean","COPY",EDGE,{"disambiguationData":[TD([subQ84])],"derivedFrom":subQ11})])]}),makeQuery(id+"F47.opFillet","BLEND_FACE",FACE,{"disambiguationData":[OSD([subQ0,subQ9]),TDD([makeQuery(id+"F42.boolean.opBoolean","COPY",EDGE,{"disambiguationData":[TD([subQ77])],"derivedFrom":subQ11})])]}),makeQuery(id+"F47.opFillet","BLEND_FACE",FACE,{"disambiguationData":[OSD([subQ0,subQ9]),TDD([makeQuery(id+"F42.boolean.opBoolean","COPY",EDGE,{"disambiguationData":[TD([subQ70])],"derivedFrom":subQ11})])]}),makeQuery(id+"F47.opFillet","BLEND_FACE",FACE,{"disambiguationData":[OSD([subQ0,subQ9]),TDD([makeQuery(id+"F42.boolean.opBoolean","COPY",EDGE,{"disambiguationData":[TD([subQ62])],"derivedFrom":subQ11})])]}),makeQuery(id+"F47.opFillet","BLEND_FACE",FACE,{"disambiguationData":[OSD([subQ0,subQ9]),TDD([makeQuery(id+"F42.boolean.opBoolean","COPY",EDGE,{"disambiguationData":[TD([subQ56])],"derivedFrom":subQ11})])]}),makeQuery(id+"F47.opFillet","BLEND_FACE",FACE,{"disambiguationData":[OSD([subQ0,subQ9]),TDD([makeQuery(id+"F42.boolean.opBoolean","COPY",EDGE,{"disambiguationData":[TD([subQ49])],"derivedFrom":subQ11})])]}),makeQuery(id+"F47.opFillet","BLEND_FACE",FACE,{"disambiguationData":[OSD([subQ0,subQ9]),TDD([makeQuery(id+"F42.boolean.opBoolean","COPY",EDGE,{"disambiguationData":[TD([makeQuery(id+"F33.opLoft","SWEPT_FACE",FACE,{"disambiguationData":[OSD([subQ41,subQ40,subQ38,sQuery(id+"F22.wireOp",EDGE,"E28.10.1"),subQ37,subQ36])]})])],"derivedFrom":subQ11})])]}),makeQuery(id+"F47.opFillet","BLEND_FACE",FACE,{"disambiguationData":[OSD([subQ0,subQ9]),TDD([makeQuery(id+"F42.boolean.opBoolean","COPY",EDGE,{"disambiguationData":[TD([makeQuery(id+"F34.opLoft","SWEPT_FACE",FACE,{"disambiguationData":[OSD([subQ35,subQ34,subQ32,sQuery(id+"F22.wireOp",EDGE,"E28.11.1"),subQ31,subQ30])]})])],"derivedFrom":subQ11})])]}),makeQuery(id+"F47.opFillet","BLEND_FACE",FACE,{"disambiguationData":[OSD([subQ0,subQ9]),TDD([makeQuery(id+"F42.boolean.opBoolean","COPY",EDGE,{"disambiguationData":[TD([makeQuery(id+"F35.opLoft","SWEPT_FACE",FACE,{"disambiguationData":[OSD([subQ29,subQ28,subQ26,sQuery(id+"F22.wireOp",EDGE,"E28.12.1"),subQ25,subQ24])]})])],"derivedFrom":subQ11})])]}),makeQuery(id+"F47.opFillet","BLEND_FACE",FACE,{"disambiguationData":[OSD([subQ0,subQ9]),TDD([makeQuery(id+"F42.boolean.opBoolean","COPY",EDGE,{"disambiguationData":[TD([makeQuery(id+"F36.opLoft","SWEPT_FACE",FACE,{"disambiguationData":[OSD([subQ23,subQ22,subQ20,sQuery(id+"F22.wireOp",EDGE,"E28.13.1"),subQ19,subQ18])]})])],"derivedFrom":subQ11})])]}),makeQuery(id+"F47.opFillet","BLEND_FACE",FACE,{"disambiguationData":[OSD([subQ0,subQ9]),TDD([makeQuery(id+"F42.boolean.opBoolean","COPY",EDGE,{"disambiguationData":[TD([makeQuery(id+"F37.opLoft","SWEPT_FACE",FACE,{"disambiguationData":[OSD([subQ16,subQ15,subQ14,sQuery(id+"F22.wireOp",EDGE,"E28.14.1"),subQ13,subQ12])]})])],"derivedFrom":subQ11})])]}),makeQuery(id+"F47.opFillet","BLEND_FACE",FACE,{"disambiguationData":[OSD([subQ0,subQ9]),TDD([makeQuery(id+"F42.boolean.opBoolean","COPY",EDGE,{"disambiguationData":[TD([makeQuery(id+"F38.opLoft","SWEPT_FACE",FACE,{"disambiguationData":[OSD([subQ8,subQ7,subQ5,sQuery(id+"F22.wireOp",EDGE,"E28.15.1"),subQ4,subQ3])]})])],"derivedFrom":subQ11})])]})],"blendedInto":[makeQuery(id+"F47.opFillet","BLEND_FACE",FACE,{"disambiguationData":[OSD([subQ0,subQ9]),TDD([makeQuery(id+"F42.boolean.opBoolean","COPY",EDGE,{"disambiguationData":[TD([makeQuery(id+"F23.opLoft","SWEPT_FACE",FACE,{"disambiguationData":[OSD([sQuery(id+"F3.wireOp",EDGE,"E20.8.0"),subQ109,subQ107,subQ106,subQ105,sQuery(id+"F22.wireOp",EDGE,"E27.right")])]})])],"derivedFrom":subQ11})])]}),makeQuery(id+"F47.opFillet","BLEND_FACE",FACE,{"disambiguationData":[OSD([subQ0,subQ9]),TDD([makeQuery(id+"F42.boolean.opBoolean","COPY",EDGE,{"disambiguationData":[TD([subQ104])],"derivedFrom":subQ11})])]}),makeQuery(id+"F47.opFillet","BLEND_FACE",FACE,{"disambiguationData":[OSD([subQ0,subQ9]),TDD([makeQuery(id+"F42.boolean.opBoolean","COPY",EDGE,{"disambiguationData":[TD([subQ97])],"derivedFrom":subQ11})])]}),makeQuery(id+"F47.opFillet","BLEND_FACE",FACE,{"disambiguationData":[OSD([subQ0,subQ9]),TDD([makeQuery(id+"F42.boolean.opBoolean","COPY",EDGE,{"disambiguationData":[TD([subQ91])],"derivedFrom":subQ11})])]}),makeQuery(id+"F47.opFillet","BLEND_FACE",FACE,{"disambiguationData":[OSD([subQ0,subQ9]),TDD([makeQuery(id+"F42.boolean.opBoolean","COPY",EDGE,{"disambiguationData":[TD([subQ84])],"derivedFrom":subQ11})])]}),makeQuery(id+"F47.opFillet","BLEND_FACE",FACE,{"disambiguationData":[OSD([subQ0,subQ9]),TDD([makeQuery(id+"F42.boolean.opBoolean","COPY",EDGE,{"disambiguationData":[TD([subQ77])],"derivedFrom":subQ11})])]}),makeQuery(id+"F47.opFillet","BLEND_FACE",FACE,{"disambiguationData":[OSD([subQ0,subQ9]),TDD([makeQuery(id+"F42.boolean.opBoolean","COPY",EDGE,{"disambiguationData":[TD([subQ70])],"derivedFrom":subQ11})])]}),makeQuery(id+"F47.opFillet","BLEND_FACE",FACE,{"disambiguationData":[OSD([subQ0,subQ9]),TDD([makeQuery(id+"F42.boolean.opBoolean","COPY",EDGE,{"disambiguationData":[TD([subQ62])],"derivedFrom":subQ11})])]}),makeQuery(id+"F47.opFillet","BLEND_FACE",FACE,{"disambiguationData":[OSD([subQ0,subQ9]),TDD([makeQuery(id+"F42.boolean.opBoolean","COPY",EDGE,{"disambiguationData":[TD([subQ56])],"derivedFrom":subQ11})])]}),makeQuery(id+"F47.opFillet","BLEND_FACE",FACE,{"disambiguationData":[OSD([subQ0,subQ9]),TDD([makeQuery(id+"F42.boolean.opBoolean","COPY",EDGE,{"disambiguationData":[TD([subQ49])],"derivedFrom":subQ11})])]}),makeQuery(id+"F47.opFillet","BLEND_FACE",FACE,{"disambiguationData":[OSD([subQ0,subQ9]),TDD([makeQuery(id+"F42.boolean.opBoolean","COPY",EDGE,{"disambiguationData":[TD([makeQuery(id+"F33.opLoft","SWEPT_FACE",FACE,{"disambiguationData":[OSD([subQ41,subQ40,subQ38,sQuery(id+"F22.wireOp",EDGE,"E28.10.1"),subQ37,subQ36])]})])],"derivedFrom":subQ11})])]}),makeQuery(id+"F47.opFillet","BLEND_FACE",FACE,{"disambiguationData":[OSD([subQ0,subQ9]),TDD([makeQuery(id+"F42.boolean.opBoolean","COPY",EDGE,{"disambiguationData":[TD([makeQuery(id+"F34.opLoft","SWEPT_FACE",FACE,{"disambiguationData":[OSD([subQ35,subQ34,subQ32,sQuery(id+"F22.wireOp",EDGE,"E28.11.1"),subQ31,subQ30])]})])],"derivedFrom":subQ11})])]}),makeQuery(id+"F47.opFillet","BLEND_FACE",FACE,{"disambiguationData":[OSD([subQ0,subQ9]),TDD([makeQuery(id+"F42.boolean.opBoolean","COPY",EDGE,{"disambiguationData":[TD([makeQuery(id+"F35.opLoft","SWEPT_FACE",FACE,{"disambiguationData":[OSD([subQ29,subQ28,subQ26,sQuery(id+"F22.wireOp",EDGE,"E28.12.1"),subQ25,subQ24])]})])],"derivedFrom":subQ11})])]}),makeQuery(id+"F47.opFillet","BLEND_FACE",FACE,{"disambiguationData":[OSD([subQ0,subQ9]),TDD([makeQuery(id+"F42.boolean.opBoolean","COPY",EDGE,{"disambiguationData":[TD([makeQuery(id+"F36.opLoft","SWEPT_FACE",FACE,{"disambiguationData":[OSD([subQ23,subQ22,subQ20,sQuery(id+"F22.wireOp",EDGE,"E28.13.1"),subQ19,subQ18])]})])],"derivedFrom":subQ11})])]}),makeQuery(id+"F47.opFillet","BLEND_FACE",FACE,{"disambiguationData":[OSD([subQ0,subQ9]),TDD([makeQuery(id+"F42.boolean.opBoolean","COPY",EDGE,{"disambiguationData":[TD([makeQuery(id+"F37.opLoft","SWEPT_FACE",FACE,{"disambiguationData":[OSD([subQ16,subQ15,subQ14,sQuery(id+"F22.wireOp",EDGE,"E28.14.1"),subQ13,subQ12])]})])],"derivedFrom":subQ11})])]}),makeQuery(id+"F47.opFillet","BLEND_FACE",FACE,{"disambiguationData":[OSD([subQ0,subQ9]),TDD([makeQuery(id+"F42.boolean.opBoolean","COPY",EDGE,{"disambiguationData":[TD([makeQuery(id+"F38.opLoft","SWEPT_FACE",FACE,{"disambiguationData":[OSD([subQ8,subQ7,subQ5,sQuery(id+"F22.wireOp",EDGE,"E28.15.1"),subQ4,subQ3])]})])],"derivedFrom":subQ11})])]})]});}
            var Q15;
            {var subQ0=sQuery(id+"F41.wireOp",EDGE,"E37");var subQ1=makeQuery(id+"F42.opRevolve","SWEPT_FACE",FACE,{"disambiguationData":[OSD([subQ0])]});var subQ2=makeQuery(id+"F40.opExtrude","CAP_FACE",FACE,{"disambiguationData":[OSD([sQuery(id+"F39.wireOp",EDGE,"E29"),sQuery(id+"F39.wireOp",EDGE,"E30")])],"isStart":true});var subQ3=sQuery(id+"F22.wireOp",EDGE,"E28.15.3");var subQ4=sQuery(id+"F22.wireOp",EDGE,"E28.15.2");var subQ5=sQuery(id+"F3.wireOp",EDGE,"E20.7.3");var subQ7=sQuery(id+"F3.wireOp",EDGE,"E20.7.1");var subQ8=sQuery(id+"F3.wireOp",EDGE,"E20.7.0");var subQ9=sQuery(id+"F41.wireOp",EDGE,"E38");var subQ10=makeQuery(id+"F42.opRevolve","SWEPT_FACE",FACE,{"disambiguationData":[OSD([subQ9])]});var subQ11=makeQuery(id+"F42.opRevolve","SWEPT_EDGE",EDGE,{"disambiguationData":[OSD([subQ0,subQ9])]});var subQ12=sQuery(id+"F22.wireOp",EDGE,"E28.14.3");var subQ13=sQuery(id+"F22.wireOp",EDGE,"E28.14.2");var subQ14=sQuery(id+"F3.wireOp",EDGE,"E20.6.3");var subQ15=sQuery(id+"F3.wireOp",EDGE,"E20.6.1");var subQ16=sQuery(id+"F3.wireOp",EDGE,"E20.6.0");var subQ18=sQuery(id+"F22.wireOp",EDGE,"E28.13.3");var subQ19=sQuery(id+"F22.wireOp",EDGE,"E28.13.2");var subQ20=sQuery(id+"F3.wireOp",EDGE,"E20.5.3");var subQ22=sQuery(id+"F3.wireOp",EDGE,"E20.5.1");var subQ23=sQuery(id+"F3.wireOp",EDGE,"E20.5.0");var subQ24=sQuery(id+"F22.wireOp",EDGE,"E28.12.3");var subQ25=sQuery(id+"F22.wireOp",EDGE,"E28.12.2");var subQ26=sQuery(id+"F3.wireOp",EDGE,"E20.4.3");var subQ28=sQuery(id+"F3.wireOp",EDGE,"E20.4.1");var subQ29=sQuery(id+"F3.wireOp",EDGE,"E20.4.0");var subQ30=sQuery(id+"F22.wireOp",EDGE,"E28.11.3");var subQ31=sQuery(id+"F22.wireOp",EDGE,"E28.11.2");var subQ32=sQuery(id+"F3.wireOp",EDGE,"E20.3.3");var subQ34=sQuery(id+"F3.wireOp",EDGE,"E20.3.1");var subQ35=sQuery(id+"F3.wireOp",EDGE,"E20.3.0");var subQ36=sQuery(id+"F22.wireOp",EDGE,"E28.10.3");var subQ37=sQuery(id+"F22.wireOp",EDGE,"E28.10.2");var subQ38=sQuery(id+"F3.wireOp",EDGE,"E20.2.3");var subQ40=sQuery(id+"F3.wireOp",EDGE,"E20.2.1");var subQ41=sQuery(id+"F3.wireOp",EDGE,"E20.2.0");var subQ42=sQuery(id+"F22.wireOp",EDGE,"E28.9.3");var subQ43=sQuery(id+"F22.wireOp",EDGE,"E28.9.2");var subQ44=sQuery(id+"F3.wireOp",EDGE,"E20.1.3");var subQ46=sQuery(id+"F3.wireOp",EDGE,"E20.1.1");var subQ47=sQuery(id+"F3.wireOp",EDGE,"E20.1.0");var subQ48=sQuery(id+"F22.wireOp",EDGE,"E28.8.3");var subQ49=sQuery(id+"F22.wireOp",EDGE,"E28.8.2");var subQ51=sQuery(id+"F3.wireOp",EDGE,"E18.top");var subQ52=sQuery(id+"F3.wireOp",EDGE,"E18.bottom");var subQ54=sQuery(id+"F3.wireOp",EDGE,"E18.left");var subQ55=makeQuery(id+"F31.opLoft","SWEPT_FACE",FACE,{"disambiguationData":[OSD([subQ52,subQ51,subQ54,sQuery(id+"F22.wireOp",EDGE,"E28.8.1"),subQ49,subQ48])]});var subQ56=sQuery(id+"F22.wireOp",EDGE,"E28.7.3");var subQ57=sQuery(id+"F22.wireOp",EDGE,"E28.7.2");var subQ58=sQuery(id+"F3.wireOp",EDGE,"E20.15.3");var subQ59=sQuery(id+"F3.wireOp",EDGE,"E20.15.1");var subQ60=sQuery(id+"F3.wireOp",EDGE,"E20.15.0");var subQ61=makeQuery(id+"F30.opLoft","SWEPT_FACE",FACE,{"disambiguationData":[OSD([subQ60,subQ59,subQ58,sQuery(id+"F22.wireOp",EDGE,"E28.7.1"),subQ57,subQ56])]});var subQ63=sQuery(id+"F22.wireOp",EDGE,"E28.6.3");var subQ64=sQuery(id+"F22.wireOp",EDGE,"E28.6.2");var subQ65=sQuery(id+"F3.wireOp",EDGE,"E20.14.3");var subQ67=sQuery(id+"F3.wireOp",EDGE,"E20.14.1");var subQ68=sQuery(id+"F3.wireOp",EDGE,"E20.14.0");var subQ69=makeQuery(id+"F29.opLoft","SWEPT_FACE",FACE,{"disambiguationData":[OSD([subQ68,subQ67,subQ65,sQuery(id+"F22.wireOp",EDGE,"E28.6.1"),subQ64,subQ63])]});var subQ70=sQuery(id+"F22.wireOp",EDGE,"E28.5.3");var subQ71=sQuery(id+"F22.wireOp",EDGE,"E28.5.2");var subQ72=sQuery(id+"F3.wireOp",EDGE,"E20.13.3");var subQ74=sQuery(id+"F3.wireOp",EDGE,"E20.13.1");var subQ75=sQuery(id+"F3.wireOp",EDGE,"E20.13.0");var subQ76=makeQuery(id+"F28.opLoft","SWEPT_FACE",FACE,{"disambiguationData":[OSD([subQ75,subQ74,subQ72,sQuery(id+"F22.wireOp",EDGE,"E28.5.1"),subQ71,subQ70])]});var subQ77=sQuery(id+"F22.wireOp",EDGE,"E28.4.3");var subQ78=sQuery(id+"F22.wireOp",EDGE,"E28.4.2");var subQ79=sQuery(id+"F3.wireOp",EDGE,"E20.12.3");var subQ81=sQuery(id+"F3.wireOp",EDGE,"E20.12.1");var subQ82=sQuery(id+"F3.wireOp",EDGE,"E20.12.0");var subQ83=makeQuery(id+"F27.opLoft","SWEPT_FACE",FACE,{"disambiguationData":[OSD([subQ82,subQ81,subQ79,sQuery(id+"F22.wireOp",EDGE,"E28.4.1"),subQ78,subQ77])]});var subQ84=sQuery(id+"F22.wireOp",EDGE,"E28.3.3");var subQ85=sQuery(id+"F22.wireOp",EDGE,"E28.3.2");var subQ86=sQuery(id+"F3.wireOp",EDGE,"E20.11.3");var subQ88=sQuery(id+"F3.wireOp",EDGE,"E20.11.1");var subQ89=sQuery(id+"F3.wireOp",EDGE,"E20.11.0");var subQ90=makeQuery(id+"F26.opLoft","SWEPT_FACE",FACE,{"disambiguationData":[OSD([subQ89,subQ88,subQ86,sQuery(id+"F22.wireOp",EDGE,"E28.3.1"),subQ85,subQ84])]});var subQ91=sQuery(id+"F22.wireOp",EDGE,"E28.2.3");var subQ92=sQuery(id+"F22.wireOp",EDGE,"E28.2.2");var subQ93=sQuery(id+"F3.wireOp",EDGE,"E20.10.3");var subQ94=sQuery(id+"F3.wireOp",EDGE,"E20.10.1");var subQ95=sQuery(id+"F3.wireOp",EDGE,"E20.10.0");var subQ96=makeQuery(id+"F25.opLoft","SWEPT_FACE",FACE,{"disambiguationData":[OSD([subQ95,subQ94,subQ93,sQuery(id+"F22.wireOp",EDGE,"E28.2.1"),subQ92,subQ91])]});var subQ98=sQuery(id+"F22.wireOp",EDGE,"E28.1.3");var subQ99=sQuery(id+"F22.wireOp",EDGE,"E28.1.2");var subQ100=sQuery(id+"F3.wireOp",EDGE,"E20.9.3");var subQ101=sQuery(id+"F3.wireOp",EDGE,"E20.9.1");var subQ102=sQuery(id+"F3.wireOp",EDGE,"E20.9.0");var subQ103=makeQuery(id+"F24.opLoft","SWEPT_FACE",FACE,{"disambiguationData":[OSD([subQ102,subQ101,subQ100,sQuery(id+"F22.wireOp",EDGE,"E28.1.1"),subQ99,subQ98])]});var subQ104=sQuery(id+"F22.wireOp",EDGE,"E27.top");var subQ105=sQuery(id+"F22.wireOp",EDGE,"E27.bottom");var subQ106=sQuery(id+"F3.wireOp",EDGE,"E20.8.3");var subQ108=sQuery(id+"F3.wireOp",EDGE,"E20.8.1");var subQ112=makeQuery(id+"F42.boolean.opBoolean","COPY",FACE,{"disambiguationData":[TD([subQ55])],"derivedFrom":subQ10});var subQ138=makeQuery(id+"F5.opLoft","CAP_FACE",FACE,{"disambiguationData":[OSD([makeQuery(id+"F3.imprint","IMPRINT",FACE,{"disambiguationData":[TD([[makeQuery(id+"F3.imprint","IMPRINT",EDGE,{"derivedFrom":subQ52}),1.0]])]})])],"isStart":true});var subQ184=makeQuery(id+"F31.boolean.opBoolean","INTERSECT",EDGE,{"derivedFrom":[makeQuery(id+"F30.boolean.opBoolean","SPLIT",FACE,{"disambiguationData":[TD([subQ138])],"derivedFrom":makeQuery(id+"F29.boolean.opBoolean","SPLIT",FACE,{"disambiguationData":[TD([subQ138])],"derivedFrom":makeQuery(id+"F28.boolean.opBoolean","SPLIT",FACE,{"disambiguationData":[TD([subQ138])],"derivedFrom":makeQuery(id+"F27.boolean.opBoolean","SPLIT",FACE,{"disambiguationData":[TD([subQ138])],"derivedFrom":makeQuery(id+"F26.boolean.opBoolean","SPLIT",FACE,{"disambiguationData":[TD([subQ138])],"derivedFrom":makeQuery(id+"F25.boolean.opBoolean","SPLIT",FACE,{"disambiguationData":[TD([subQ138])],"derivedFrom":makeQuery(id+"F24.boolean.opBoolean","SPLIT",FACE,{"disambiguationData":[TD([subQ138])],"derivedFrom":makeQuery(id+"F1.opRevolve","SWEPT_FACE",FACE,{"disambiguationData":[OSD([sQuery(id+"F0.wireOp",EDGE,"E13")])]})})})})})})})}),subQ55]});Q15=makeQuery(id+"F48.opFillet","BLEND_EDGE",EDGE,{"blendedFrom":[makeQuery(id+"F47.opFillet","TWEAK_EDGE",EDGE,{"derivedFrom":[makeQuery(id+"F45.opFillet","BLEND_VERTEX",VERTEX,{"blendedFrom":[subQ184,subQ55,subQ112],"blendedInto":[subQ55,subQ112]}),makeQuery(id+"F45.opFillet","BLEND_VERTEX",VERTEX,{"blendedFrom":[subQ184,makeQuery(id+"F42.boolean.opBoolean","MERGE",FACE,{"derivedFrom":[subQ2,subQ1]}),subQ112],"blendedInto":[makeQuery(id+"F42.boolean.opBoolean","MERGE",FACE,{"derivedFrom":[subQ2,subQ1]}),subQ112]})]}),makeQuery(id+"F47.opFillet","BLEND_FACE",FACE,{"disambiguationData":[OSD([subQ0,subQ9]),TDD([makeQuery(id+"F42.boolean.opBoolean","COPY",EDGE,{"disambiguationData":[TD([makeQuery(id+"F23.opLoft","SWEPT_FACE",FACE,{"disambiguationData":[OSD([sQuery(id+"F3.wireOp",EDGE,"E20.8.0"),subQ108,subQ106,subQ105,subQ104,sQuery(id+"F22.wireOp",EDGE,"E27.right")])]})])],"derivedFrom":subQ11})])]}),makeQuery(id+"F47.opFillet","BLEND_FACE",FACE,{"disambiguationData":[OSD([subQ0,subQ9]),TDD([makeQuery(id+"F42.boolean.opBoolean","COPY",EDGE,{"disambiguationData":[TD([subQ103])],"derivedFrom":subQ11})])]}),makeQuery(id+"F47.opFillet","BLEND_FACE",FACE,{"disambiguationData":[OSD([subQ0,subQ9]),TDD([makeQuery(id+"F42.boolean.opBoolean","COPY",EDGE,{"disambiguationData":[TD([subQ96])],"derivedFrom":subQ11})])]}),makeQuery(id+"F47.opFillet","BLEND_FACE",FACE,{"disambiguationData":[OSD([subQ0,subQ9]),TDD([makeQuery(id+"F42.boolean.opBoolean","COPY",EDGE,{"disambiguationData":[TD([subQ90])],"derivedFrom":subQ11})])]}),makeQuery(id+"F47.opFillet","BLEND_FACE",FACE,{"disambiguationData":[OSD([subQ0,subQ9]),TDD([makeQuery(id+"F42.boolean.opBoolean","COPY",EDGE,{"disambiguationData":[TD([subQ83])],"derivedFrom":subQ11})])]}),makeQuery(id+"F47.opFillet","BLEND_FACE",FACE,{"disambiguationData":[OSD([subQ0,subQ9]),TDD([makeQuery(id+"F42.boolean.opBoolean","COPY",EDGE,{"disambiguationData":[TD([subQ76])],"derivedFrom":subQ11})])]}),makeQuery(id+"F47.opFillet","BLEND_FACE",FACE,{"disambiguationData":[OSD([subQ0,subQ9]),TDD([makeQuery(id+"F42.boolean.opBoolean","COPY",EDGE,{"disambiguationData":[TD([subQ69])],"derivedFrom":subQ11})])]}),makeQuery(id+"F47.opFillet","BLEND_FACE",FACE,{"disambiguationData":[OSD([subQ0,subQ9]),TDD([makeQuery(id+"F42.boolean.opBoolean","COPY",EDGE,{"disambiguationData":[TD([subQ61])],"derivedFrom":subQ11})])]}),makeQuery(id+"F47.opFillet","BLEND_FACE",FACE,{"disambiguationData":[OSD([subQ0,subQ9]),TDD([makeQuery(id+"F42.boolean.opBoolean","COPY",EDGE,{"disambiguationData":[TD([subQ55])],"derivedFrom":subQ11})])]}),makeQuery(id+"F47.opFillet","BLEND_FACE",FACE,{"disambiguationData":[OSD([subQ0,subQ9]),TDD([makeQuery(id+"F42.boolean.opBoolean","COPY",EDGE,{"disambiguationData":[TD([makeQuery(id+"F32.opLoft","SWEPT_FACE",FACE,{"disambiguationData":[OSD([subQ47,subQ46,subQ44,sQuery(id+"F22.wireOp",EDGE,"E28.9.1"),subQ43,subQ42])]})])],"derivedFrom":subQ11})])]}),makeQuery(id+"F47.opFillet","BLEND_FACE",FACE,{"disambiguationData":[OSD([subQ0,subQ9]),TDD([makeQuery(id+"F42.boolean.opBoolean","COPY",EDGE,{"disambiguationData":[TD([makeQuery(id+"F33.opLoft","SWEPT_FACE",FACE,{"disambiguationData":[OSD([subQ41,subQ40,subQ38,sQuery(id+"F22.wireOp",EDGE,"E28.10.1"),subQ37,subQ36])]})])],"derivedFrom":subQ11})])]}),makeQuery(id+"F47.opFillet","BLEND_FACE",FACE,{"disambiguationData":[OSD([subQ0,subQ9]),TDD([makeQuery(id+"F42.boolean.opBoolean","COPY",EDGE,{"disambiguationData":[TD([makeQuery(id+"F34.opLoft","SWEPT_FACE",FACE,{"disambiguationData":[OSD([subQ35,subQ34,subQ32,sQuery(id+"F22.wireOp",EDGE,"E28.11.1"),subQ31,subQ30])]})])],"derivedFrom":subQ11})])]}),makeQuery(id+"F47.opFillet","BLEND_FACE",FACE,{"disambiguationData":[OSD([subQ0,subQ9]),TDD([makeQuery(id+"F42.boolean.opBoolean","COPY",EDGE,{"disambiguationData":[TD([makeQuery(id+"F35.opLoft","SWEPT_FACE",FACE,{"disambiguationData":[OSD([subQ29,subQ28,subQ26,sQuery(id+"F22.wireOp",EDGE,"E28.12.1"),subQ25,subQ24])]})])],"derivedFrom":subQ11})])]}),makeQuery(id+"F47.opFillet","BLEND_FACE",FACE,{"disambiguationData":[OSD([subQ0,subQ9]),TDD([makeQuery(id+"F42.boolean.opBoolean","COPY",EDGE,{"disambiguationData":[TD([makeQuery(id+"F36.opLoft","SWEPT_FACE",FACE,{"disambiguationData":[OSD([subQ23,subQ22,subQ20,sQuery(id+"F22.wireOp",EDGE,"E28.13.1"),subQ19,subQ18])]})])],"derivedFrom":subQ11})])]}),makeQuery(id+"F47.opFillet","BLEND_FACE",FACE,{"disambiguationData":[OSD([subQ0,subQ9]),TDD([makeQuery(id+"F42.boolean.opBoolean","COPY",EDGE,{"disambiguationData":[TD([makeQuery(id+"F37.opLoft","SWEPT_FACE",FACE,{"disambiguationData":[OSD([subQ16,subQ15,subQ14,sQuery(id+"F22.wireOp",EDGE,"E28.14.1"),subQ13,subQ12])]})])],"derivedFrom":subQ11})])]}),makeQuery(id+"F47.opFillet","BLEND_FACE",FACE,{"disambiguationData":[OSD([subQ0,subQ9]),TDD([makeQuery(id+"F42.boolean.opBoolean","COPY",EDGE,{"disambiguationData":[TD([makeQuery(id+"F38.opLoft","SWEPT_FACE",FACE,{"disambiguationData":[OSD([subQ8,subQ7,subQ5,sQuery(id+"F22.wireOp",EDGE,"E28.15.1"),subQ4,subQ3])]})])],"derivedFrom":subQ11})])]})],"blendedInto":[makeQuery(id+"F47.opFillet","BLEND_FACE",FACE,{"disambiguationData":[OSD([subQ0,subQ9]),TDD([makeQuery(id+"F42.boolean.opBoolean","COPY",EDGE,{"disambiguationData":[TD([makeQuery(id+"F23.opLoft","SWEPT_FACE",FACE,{"disambiguationData":[OSD([sQuery(id+"F3.wireOp",EDGE,"E20.8.0"),subQ108,subQ106,subQ105,subQ104,sQuery(id+"F22.wireOp",EDGE,"E27.right")])]})])],"derivedFrom":subQ11})])]}),makeQuery(id+"F47.opFillet","BLEND_FACE",FACE,{"disambiguationData":[OSD([subQ0,subQ9]),TDD([makeQuery(id+"F42.boolean.opBoolean","COPY",EDGE,{"disambiguationData":[TD([subQ103])],"derivedFrom":subQ11})])]}),makeQuery(id+"F47.opFillet","BLEND_FACE",FACE,{"disambiguationData":[OSD([subQ0,subQ9]),TDD([makeQuery(id+"F42.boolean.opBoolean","COPY",EDGE,{"disambiguationData":[TD([subQ96])],"derivedFrom":subQ11})])]}),makeQuery(id+"F47.opFillet","BLEND_FACE",FACE,{"disambiguationData":[OSD([subQ0,subQ9]),TDD([makeQuery(id+"F42.boolean.opBoolean","COPY",EDGE,{"disambiguationData":[TD([subQ90])],"derivedFrom":subQ11})])]}),makeQuery(id+"F47.opFillet","BLEND_FACE",FACE,{"disambiguationData":[OSD([subQ0,subQ9]),TDD([makeQuery(id+"F42.boolean.opBoolean","COPY",EDGE,{"disambiguationData":[TD([subQ83])],"derivedFrom":subQ11})])]}),makeQuery(id+"F47.opFillet","BLEND_FACE",FACE,{"disambiguationData":[OSD([subQ0,subQ9]),TDD([makeQuery(id+"F42.boolean.opBoolean","COPY",EDGE,{"disambiguationData":[TD([subQ76])],"derivedFrom":subQ11})])]}),makeQuery(id+"F47.opFillet","BLEND_FACE",FACE,{"disambiguationData":[OSD([subQ0,subQ9]),TDD([makeQuery(id+"F42.boolean.opBoolean","COPY",EDGE,{"disambiguationData":[TD([subQ69])],"derivedFrom":subQ11})])]}),makeQuery(id+"F47.opFillet","BLEND_FACE",FACE,{"disambiguationData":[OSD([subQ0,subQ9]),TDD([makeQuery(id+"F42.boolean.opBoolean","COPY",EDGE,{"disambiguationData":[TD([subQ61])],"derivedFrom":subQ11})])]}),makeQuery(id+"F47.opFillet","BLEND_FACE",FACE,{"disambiguationData":[OSD([subQ0,subQ9]),TDD([makeQuery(id+"F42.boolean.opBoolean","COPY",EDGE,{"disambiguationData":[TD([subQ55])],"derivedFrom":subQ11})])]}),makeQuery(id+"F47.opFillet","BLEND_FACE",FACE,{"disambiguationData":[OSD([subQ0,subQ9]),TDD([makeQuery(id+"F42.boolean.opBoolean","COPY",EDGE,{"disambiguationData":[TD([makeQuery(id+"F32.opLoft","SWEPT_FACE",FACE,{"disambiguationData":[OSD([subQ47,subQ46,subQ44,sQuery(id+"F22.wireOp",EDGE,"E28.9.1"),subQ43,subQ42])]})])],"derivedFrom":subQ11})])]}),makeQuery(id+"F47.opFillet","BLEND_FACE",FACE,{"disambiguationData":[OSD([subQ0,subQ9]),TDD([makeQuery(id+"F42.boolean.opBoolean","COPY",EDGE,{"disambiguationData":[TD([makeQuery(id+"F33.opLoft","SWEPT_FACE",FACE,{"disambiguationData":[OSD([subQ41,subQ40,subQ38,sQuery(id+"F22.wireOp",EDGE,"E28.10.1"),subQ37,subQ36])]})])],"derivedFrom":subQ11})])]}),makeQuery(id+"F47.opFillet","BLEND_FACE",FACE,{"disambiguationData":[OSD([subQ0,subQ9]),TDD([makeQuery(id+"F42.boolean.opBoolean","COPY",EDGE,{"disambiguationData":[TD([makeQuery(id+"F34.opLoft","SWEPT_FACE",FACE,{"disambiguationData":[OSD([subQ35,subQ34,subQ32,sQuery(id+"F22.wireOp",EDGE,"E28.11.1"),subQ31,subQ30])]})])],"derivedFrom":subQ11})])]}),makeQuery(id+"F47.opFillet","BLEND_FACE",FACE,{"disambiguationData":[OSD([subQ0,subQ9]),TDD([makeQuery(id+"F42.boolean.opBoolean","COPY",EDGE,{"disambiguationData":[TD([makeQuery(id+"F35.opLoft","SWEPT_FACE",FACE,{"disambiguationData":[OSD([subQ29,subQ28,subQ26,sQuery(id+"F22.wireOp",EDGE,"E28.12.1"),subQ25,subQ24])]})])],"derivedFrom":subQ11})])]}),makeQuery(id+"F47.opFillet","BLEND_FACE",FACE,{"disambiguationData":[OSD([subQ0,subQ9]),TDD([makeQuery(id+"F42.boolean.opBoolean","COPY",EDGE,{"disambiguationData":[TD([makeQuery(id+"F36.opLoft","SWEPT_FACE",FACE,{"disambiguationData":[OSD([subQ23,subQ22,subQ20,sQuery(id+"F22.wireOp",EDGE,"E28.13.1"),subQ19,subQ18])]})])],"derivedFrom":subQ11})])]}),makeQuery(id+"F47.opFillet","BLEND_FACE",FACE,{"disambiguationData":[OSD([subQ0,subQ9]),TDD([makeQuery(id+"F42.boolean.opBoolean","COPY",EDGE,{"disambiguationData":[TD([makeQuery(id+"F37.opLoft","SWEPT_FACE",FACE,{"disambiguationData":[OSD([subQ16,subQ15,subQ14,sQuery(id+"F22.wireOp",EDGE,"E28.14.1"),subQ13,subQ12])]})])],"derivedFrom":subQ11})])]}),makeQuery(id+"F47.opFillet","BLEND_FACE",FACE,{"disambiguationData":[OSD([subQ0,subQ9]),TDD([makeQuery(id+"F42.boolean.opBoolean","COPY",EDGE,{"disambiguationData":[TD([makeQuery(id+"F38.opLoft","SWEPT_FACE",FACE,{"disambiguationData":[OSD([subQ8,subQ7,subQ5,sQuery(id+"F22.wireOp",EDGE,"E28.15.1"),subQ4,subQ3])]})])],"derivedFrom":subQ11})])]})]});}
            var Q16;
            {var subQ0=sQuery(id+"F22.wireOp",EDGE,"E28.9.3");var subQ1=sQuery(id+"F22.wireOp",EDGE,"E28.9.2");var subQ2=sQuery(id+"F22.wireOp",EDGE,"E28.9.1");var subQ3=sQuery(id+"F3.wireOp",EDGE,"E20.1.3");var subQ4=sQuery(id+"F3.wireOp",EDGE,"E20.1.1");var subQ5=sQuery(id+"F22.wireOp",EDGE,"E28.9.0");var subQ6=makeQuery(id+"F32.opLoft","SWEPT_FACE",FACE,{"disambiguationData":[OSD([subQ4,sQuery(id+"F3.wireOp",EDGE,"E20.1.2"),subQ3,subQ5,subQ1,subQ0])]});var subQ7=sQuery(id+"F41.wireOp",EDGE,"E34");var subQ8=sQuery(id+"F41.wireOp",EDGE,"E32");Q16=makeQuery(id+"F44.opFillet","BLEND_EDGE",EDGE,{"blendedFrom":[makeQuery(id+"F40.boolean.opBoolean","INTERSECT",EDGE,{"derivedFrom":[subQ6,makeQuery(id+"F40.opExtrude","CAP_FACE",FACE,{"disambiguationData":[OSD([sQuery(id+"F39.wireOp",EDGE,"E29"),sQuery(id+"F39.wireOp",EDGE,"E30")])],"isStart":true})]}),makeQuery(id+"F42.boolean.opBoolean","COPY",FACE,{"disambiguationData":[TD([makeQuery(id+"F32.opLoft","SWEPT_FACE",FACE,{"disambiguationData":[OSD([sQuery(id+"F3.wireOp",EDGE,"E20.1.0"),subQ4,subQ3,subQ2,subQ1,subQ0])]})])],"derivedFrom":makeQuery(id+"F42.opRevolve","SWEPT_FACE",FACE,{"disambiguationData":[OSD([subQ8]),TDD([makeQuery(id+"F41.imprint","IMPRINT",EDGE,{"disambiguationData":[TD([[makeQuery(id+"F41.imprint","INTERSECT",VERTEX,{"disambiguationData":[OD(0.0)],"derivedFrom":[subQ8,subQ7]}),-1.0]])],"derivedFrom":subQ8})])]})})],"blendedInto":[makeQuery(id+"F42.boolean.opBoolean","COPY",FACE,{"disambiguationData":[TD([makeQuery(id+"F32.opLoft","SWEPT_FACE",FACE,{"disambiguationData":[OSD([sQuery(id+"F3.wireOp",EDGE,"E20.1.0"),subQ4,subQ3,subQ2,subQ1,subQ0])]})])],"derivedFrom":makeQuery(id+"F42.opRevolve","SWEPT_FACE",FACE,{"disambiguationData":[OSD([subQ8]),TDD([makeQuery(id+"F41.imprint","IMPRINT",EDGE,{"disambiguationData":[TD([[makeQuery(id+"F41.imprint","INTERSECT",VERTEX,{"disambiguationData":[OD(0.0)],"derivedFrom":[subQ8,subQ7]}),-1.0]])],"derivedFrom":subQ8})])]})})]});}
            var Q17;
            {var subQ0=sQuery(id+"F41.wireOp",EDGE,"E34");var subQ1=sQuery(id+"F41.wireOp",EDGE,"E32");Q17=makeQuery(id+"F42.boolean.opBoolean","INTERSECT",EDGE,{"derivedFrom":[makeQuery(id+"F31.opLoft","SWEPT_FACE",FACE,{"disambiguationData":[OSD([sQuery(id+"F3.wireOp",EDGE,"E18.bottom"),sQuery(id+"F3.wireOp",EDGE,"E18.top"),sQuery(id+"F3.wireOp",EDGE,"E18.left"),sQuery(id+"F22.wireOp",EDGE,"E28.8.1"),sQuery(id+"F22.wireOp",EDGE,"E28.8.2"),sQuery(id+"F22.wireOp",EDGE,"E28.8.3")])]}),makeQuery(id+"F42.opRevolve","SWEPT_FACE",FACE,{"disambiguationData":[OSD([subQ1]),TDD([makeQuery(id+"F41.imprint","IMPRINT",EDGE,{"disambiguationData":[TD([[makeQuery(id+"F41.imprint","INTERSECT",VERTEX,{"disambiguationData":[OD(0.0)],"derivedFrom":[subQ1,subQ0]}),-1.0]])],"derivedFrom":subQ1})])]})]});}
            var Q18;
            {var subQ0=sQuery(id+"F22.wireOp",EDGE,"E28.8.3");var subQ1=sQuery(id+"F22.wireOp",EDGE,"E28.8.2");var subQ2=sQuery(id+"F22.wireOp",EDGE,"E28.8.1");var subQ3=sQuery(id+"F3.wireOp",EDGE,"E18.top");var subQ4=sQuery(id+"F3.wireOp",EDGE,"E18.bottom");var subQ5=sQuery(id+"F22.wireOp",EDGE,"E28.8.0");var subQ6=makeQuery(id+"F31.opLoft","SWEPT_FACE",FACE,{"disambiguationData":[OSD([subQ4,subQ3,sQuery(id+"F3.wireOp",EDGE,"E18.right"),subQ5,subQ1,subQ0])]});var subQ7=sQuery(id+"F41.wireOp",EDGE,"E34");var subQ8=sQuery(id+"F41.wireOp",EDGE,"E32");Q18=makeQuery(id+"F44.opFillet","BLEND_EDGE",EDGE,{"blendedFrom":[makeQuery(id+"F40.boolean.opBoolean","INTERSECT",EDGE,{"derivedFrom":[subQ6,makeQuery(id+"F40.opExtrude","CAP_FACE",FACE,{"disambiguationData":[OSD([sQuery(id+"F39.wireOp",EDGE,"E29"),sQuery(id+"F39.wireOp",EDGE,"E30")])],"isStart":true})]}),makeQuery(id+"F42.boolean.opBoolean","COPY",FACE,{"disambiguationData":[TD([makeQuery(id+"F31.opLoft","SWEPT_FACE",FACE,{"disambiguationData":[OSD([subQ4,subQ3,sQuery(id+"F3.wireOp",EDGE,"E18.left"),subQ2,subQ1,subQ0])]})])],"derivedFrom":makeQuery(id+"F42.opRevolve","SWEPT_FACE",FACE,{"disambiguationData":[OSD([subQ8]),TDD([makeQuery(id+"F41.imprint","IMPRINT",EDGE,{"disambiguationData":[TD([[makeQuery(id+"F41.imprint","INTERSECT",VERTEX,{"disambiguationData":[OD(0.0)],"derivedFrom":[subQ8,subQ7]}),-1.0]])],"derivedFrom":subQ8})])]})})],"blendedInto":[makeQuery(id+"F42.boolean.opBoolean","COPY",FACE,{"disambiguationData":[TD([makeQuery(id+"F31.opLoft","SWEPT_FACE",FACE,{"disambiguationData":[OSD([subQ4,subQ3,sQuery(id+"F3.wireOp",EDGE,"E18.left"),subQ2,subQ1,subQ0])]})])],"derivedFrom":makeQuery(id+"F42.opRevolve","SWEPT_FACE",FACE,{"disambiguationData":[OSD([subQ8]),TDD([makeQuery(id+"F41.imprint","IMPRINT",EDGE,{"disambiguationData":[TD([[makeQuery(id+"F41.imprint","INTERSECT",VERTEX,{"disambiguationData":[OD(0.0)],"derivedFrom":[subQ8,subQ7]}),-1.0]])],"derivedFrom":subQ8})])]})})]});}
            var Q19;
            {var subQ0=sQuery(id+"F41.wireOp",EDGE,"E37");var subQ1=makeQuery(id+"F42.opRevolve","SWEPT_FACE",FACE,{"disambiguationData":[OSD([subQ0])]});var subQ2=makeQuery(id+"F40.opExtrude","CAP_FACE",FACE,{"disambiguationData":[OSD([sQuery(id+"F39.wireOp",EDGE,"E29"),sQuery(id+"F39.wireOp",EDGE,"E30")])],"isStart":true});var subQ3=sQuery(id+"F22.wireOp",EDGE,"E28.15.3");var subQ4=sQuery(id+"F22.wireOp",EDGE,"E28.15.2");var subQ5=sQuery(id+"F3.wireOp",EDGE,"E20.7.3");var subQ7=sQuery(id+"F3.wireOp",EDGE,"E20.7.1");var subQ8=sQuery(id+"F3.wireOp",EDGE,"E20.7.0");var subQ9=sQuery(id+"F41.wireOp",EDGE,"E38");var subQ10=makeQuery(id+"F42.opRevolve","SWEPT_FACE",FACE,{"disambiguationData":[OSD([subQ9])]});var subQ11=makeQuery(id+"F42.opRevolve","SWEPT_EDGE",EDGE,{"disambiguationData":[OSD([subQ0,subQ9])]});var subQ12=sQuery(id+"F22.wireOp",EDGE,"E28.14.3");var subQ13=sQuery(id+"F22.wireOp",EDGE,"E28.14.2");var subQ14=sQuery(id+"F3.wireOp",EDGE,"E20.6.3");var subQ15=sQuery(id+"F3.wireOp",EDGE,"E20.6.1");var subQ16=sQuery(id+"F3.wireOp",EDGE,"E20.6.0");var subQ18=sQuery(id+"F22.wireOp",EDGE,"E28.13.3");var subQ19=sQuery(id+"F22.wireOp",EDGE,"E28.13.2");var subQ20=sQuery(id+"F3.wireOp",EDGE,"E20.5.3");var subQ22=sQuery(id+"F3.wireOp",EDGE,"E20.5.1");var subQ23=sQuery(id+"F3.wireOp",EDGE,"E20.5.0");var subQ24=sQuery(id+"F22.wireOp",EDGE,"E28.12.3");var subQ25=sQuery(id+"F22.wireOp",EDGE,"E28.12.2");var subQ26=sQuery(id+"F3.wireOp",EDGE,"E20.4.3");var subQ28=sQuery(id+"F3.wireOp",EDGE,"E20.4.1");var subQ29=sQuery(id+"F3.wireOp",EDGE,"E20.4.0");var subQ30=sQuery(id+"F22.wireOp",EDGE,"E28.11.3");var subQ31=sQuery(id+"F22.wireOp",EDGE,"E28.11.2");var subQ32=sQuery(id+"F3.wireOp",EDGE,"E20.3.3");var subQ34=sQuery(id+"F3.wireOp",EDGE,"E20.3.1");var subQ35=sQuery(id+"F3.wireOp",EDGE,"E20.3.0");var subQ36=sQuery(id+"F22.wireOp",EDGE,"E28.10.3");var subQ37=sQuery(id+"F22.wireOp",EDGE,"E28.10.2");var subQ38=sQuery(id+"F3.wireOp",EDGE,"E20.2.3");var subQ40=sQuery(id+"F3.wireOp",EDGE,"E20.2.1");var subQ41=sQuery(id+"F3.wireOp",EDGE,"E20.2.0");var subQ42=sQuery(id+"F22.wireOp",EDGE,"E28.9.3");var subQ43=sQuery(id+"F22.wireOp",EDGE,"E28.9.2");var subQ44=sQuery(id+"F3.wireOp",EDGE,"E20.1.3");var subQ46=sQuery(id+"F3.wireOp",EDGE,"E20.1.1");var subQ47=sQuery(id+"F3.wireOp",EDGE,"E20.1.0");var subQ48=sQuery(id+"F22.wireOp",EDGE,"E28.8.3");var subQ49=sQuery(id+"F22.wireOp",EDGE,"E28.8.2");var subQ51=sQuery(id+"F3.wireOp",EDGE,"E18.top");var subQ52=sQuery(id+"F3.wireOp",EDGE,"E18.bottom");var subQ53=sQuery(id+"F3.wireOp",EDGE,"E18.left");var subQ54=sQuery(id+"F22.wireOp",EDGE,"E28.7.3");var subQ55=sQuery(id+"F22.wireOp",EDGE,"E28.7.2");var subQ56=sQuery(id+"F3.wireOp",EDGE,"E20.15.3");var subQ57=sQuery(id+"F3.wireOp",EDGE,"E20.15.1");var subQ58=sQuery(id+"F3.wireOp",EDGE,"E20.15.0");var subQ59=makeQuery(id+"F30.opLoft","SWEPT_FACE",FACE,{"disambiguationData":[OSD([subQ58,subQ57,subQ56,sQuery(id+"F22.wireOp",EDGE,"E28.7.1"),subQ55,subQ54])]});var subQ62=sQuery(id+"F22.wireOp",EDGE,"E28.6.3");var subQ63=sQuery(id+"F22.wireOp",EDGE,"E28.6.2");var subQ64=sQuery(id+"F3.wireOp",EDGE,"E20.14.3");var subQ66=sQuery(id+"F3.wireOp",EDGE,"E20.14.1");var subQ67=sQuery(id+"F3.wireOp",EDGE,"E20.14.0");var subQ68=makeQuery(id+"F29.opLoft","SWEPT_FACE",FACE,{"disambiguationData":[OSD([subQ67,subQ66,subQ64,sQuery(id+"F22.wireOp",EDGE,"E28.6.1"),subQ63,subQ62])]});var subQ69=sQuery(id+"F22.wireOp",EDGE,"E28.5.3");var subQ70=sQuery(id+"F22.wireOp",EDGE,"E28.5.2");var subQ71=sQuery(id+"F3.wireOp",EDGE,"E20.13.3");var subQ73=sQuery(id+"F3.wireOp",EDGE,"E20.13.1");var subQ74=sQuery(id+"F3.wireOp",EDGE,"E20.13.0");var subQ75=makeQuery(id+"F28.opLoft","SWEPT_FACE",FACE,{"disambiguationData":[OSD([subQ74,subQ73,subQ71,sQuery(id+"F22.wireOp",EDGE,"E28.5.1"),subQ70,subQ69])]});var subQ76=sQuery(id+"F22.wireOp",EDGE,"E28.4.3");var subQ77=sQuery(id+"F22.wireOp",EDGE,"E28.4.2");var subQ78=sQuery(id+"F3.wireOp",EDGE,"E20.12.3");var subQ80=sQuery(id+"F3.wireOp",EDGE,"E20.12.1");var subQ81=sQuery(id+"F3.wireOp",EDGE,"E20.12.0");var subQ82=makeQuery(id+"F27.opLoft","SWEPT_FACE",FACE,{"disambiguationData":[OSD([subQ81,subQ80,subQ78,sQuery(id+"F22.wireOp",EDGE,"E28.4.1"),subQ77,subQ76])]});var subQ83=sQuery(id+"F22.wireOp",EDGE,"E28.3.3");var subQ84=sQuery(id+"F22.wireOp",EDGE,"E28.3.2");var subQ85=sQuery(id+"F3.wireOp",EDGE,"E20.11.3");var subQ87=sQuery(id+"F3.wireOp",EDGE,"E20.11.1");var subQ88=sQuery(id+"F3.wireOp",EDGE,"E20.11.0");var subQ89=makeQuery(id+"F26.opLoft","SWEPT_FACE",FACE,{"disambiguationData":[OSD([subQ88,subQ87,subQ85,sQuery(id+"F22.wireOp",EDGE,"E28.3.1"),subQ84,subQ83])]});var subQ90=sQuery(id+"F22.wireOp",EDGE,"E28.2.3");var subQ91=sQuery(id+"F22.wireOp",EDGE,"E28.2.2");var subQ92=sQuery(id+"F3.wireOp",EDGE,"E20.10.3");var subQ93=sQuery(id+"F3.wireOp",EDGE,"E20.10.1");var subQ94=sQuery(id+"F3.wireOp",EDGE,"E20.10.0");var subQ95=makeQuery(id+"F25.opLoft","SWEPT_FACE",FACE,{"disambiguationData":[OSD([subQ94,subQ93,subQ92,sQuery(id+"F22.wireOp",EDGE,"E28.2.1"),subQ91,subQ90])]});var subQ97=sQuery(id+"F22.wireOp",EDGE,"E28.1.3");var subQ98=sQuery(id+"F22.wireOp",EDGE,"E28.1.2");var subQ99=sQuery(id+"F3.wireOp",EDGE,"E20.9.3");var subQ100=sQuery(id+"F3.wireOp",EDGE,"E20.9.1");var subQ101=sQuery(id+"F3.wireOp",EDGE,"E20.9.0");var subQ102=makeQuery(id+"F24.opLoft","SWEPT_FACE",FACE,{"disambiguationData":[OSD([subQ101,subQ100,subQ99,sQuery(id+"F22.wireOp",EDGE,"E28.1.1"),subQ98,subQ97])]});var subQ103=sQuery(id+"F22.wireOp",EDGE,"E27.top");var subQ104=sQuery(id+"F22.wireOp",EDGE,"E27.bottom");var subQ105=sQuery(id+"F3.wireOp",EDGE,"E20.8.3");var subQ107=sQuery(id+"F3.wireOp",EDGE,"E20.8.1");var subQ111=makeQuery(id+"F42.boolean.opBoolean","COPY",FACE,{"disambiguationData":[TD([subQ59])],"derivedFrom":subQ10});var subQ127=makeQuery(id+"F5.opLoft","CAP_FACE",FACE,{"disambiguationData":[OSD([makeQuery(id+"F3.imprint","IMPRINT",FACE,{"disambiguationData":[TD([[makeQuery(id+"F3.imprint","IMPRINT",EDGE,{"derivedFrom":subQ52}),1.0]])]})])],"isStart":true});var subQ183=makeQuery(id+"F30.boolean.opBoolean","INTERSECT",EDGE,{"derivedFrom":[makeQuery(id+"F29.boolean.opBoolean","SPLIT",FACE,{"disambiguationData":[TD([subQ127])],"derivedFrom":makeQuery(id+"F28.boolean.opBoolean","SPLIT",FACE,{"disambiguationData":[TD([subQ127])],"derivedFrom":makeQuery(id+"F27.boolean.opBoolean","SPLIT",FACE,{"disambiguationData":[TD([subQ127])],"derivedFrom":makeQuery(id+"F26.boolean.opBoolean","SPLIT",FACE,{"disambiguationData":[TD([subQ127])],"derivedFrom":makeQuery(id+"F25.boolean.opBoolean","SPLIT",FACE,{"disambiguationData":[TD([subQ127])],"derivedFrom":makeQuery(id+"F24.boolean.opBoolean","SPLIT",FACE,{"disambiguationData":[TD([subQ127])],"derivedFrom":makeQuery(id+"F1.opRevolve","SWEPT_FACE",FACE,{"disambiguationData":[OSD([sQuery(id+"F0.wireOp",EDGE,"E13")])]})})})})})})}),subQ59]});Q19=makeQuery(id+"F48.opFillet","BLEND_EDGE",EDGE,{"blendedFrom":[makeQuery(id+"F47.opFillet","TWEAK_EDGE",EDGE,{"derivedFrom":[makeQuery(id+"F45.opFillet","BLEND_VERTEX",VERTEX,{"blendedFrom":[subQ183,subQ59,subQ111],"blendedInto":[subQ59,subQ111]}),makeQuery(id+"F45.opFillet","BLEND_VERTEX",VERTEX,{"blendedFrom":[subQ183,makeQuery(id+"F42.boolean.opBoolean","MERGE",FACE,{"derivedFrom":[subQ2,subQ1]}),subQ111],"blendedInto":[makeQuery(id+"F42.boolean.opBoolean","MERGE",FACE,{"derivedFrom":[subQ2,subQ1]}),subQ111]})]}),makeQuery(id+"F47.opFillet","BLEND_FACE",FACE,{"disambiguationData":[OSD([subQ0,subQ9]),TDD([makeQuery(id+"F42.boolean.opBoolean","COPY",EDGE,{"disambiguationData":[TD([makeQuery(id+"F23.opLoft","SWEPT_FACE",FACE,{"disambiguationData":[OSD([sQuery(id+"F3.wireOp",EDGE,"E20.8.0"),subQ107,subQ105,subQ104,subQ103,sQuery(id+"F22.wireOp",EDGE,"E27.right")])]})])],"derivedFrom":subQ11})])]}),makeQuery(id+"F47.opFillet","BLEND_FACE",FACE,{"disambiguationData":[OSD([subQ0,subQ9]),TDD([makeQuery(id+"F42.boolean.opBoolean","COPY",EDGE,{"disambiguationData":[TD([subQ102])],"derivedFrom":subQ11})])]}),makeQuery(id+"F47.opFillet","BLEND_FACE",FACE,{"disambiguationData":[OSD([subQ0,subQ9]),TDD([makeQuery(id+"F42.boolean.opBoolean","COPY",EDGE,{"disambiguationData":[TD([subQ95])],"derivedFrom":subQ11})])]}),makeQuery(id+"F47.opFillet","BLEND_FACE",FACE,{"disambiguationData":[OSD([subQ0,subQ9]),TDD([makeQuery(id+"F42.boolean.opBoolean","COPY",EDGE,{"disambiguationData":[TD([subQ89])],"derivedFrom":subQ11})])]}),makeQuery(id+"F47.opFillet","BLEND_FACE",FACE,{"disambiguationData":[OSD([subQ0,subQ9]),TDD([makeQuery(id+"F42.boolean.opBoolean","COPY",EDGE,{"disambiguationData":[TD([subQ82])],"derivedFrom":subQ11})])]}),makeQuery(id+"F47.opFillet","BLEND_FACE",FACE,{"disambiguationData":[OSD([subQ0,subQ9]),TDD([makeQuery(id+"F42.boolean.opBoolean","COPY",EDGE,{"disambiguationData":[TD([subQ75])],"derivedFrom":subQ11})])]}),makeQuery(id+"F47.opFillet","BLEND_FACE",FACE,{"disambiguationData":[OSD([subQ0,subQ9]),TDD([makeQuery(id+"F42.boolean.opBoolean","COPY",EDGE,{"disambiguationData":[TD([subQ68])],"derivedFrom":subQ11})])]}),makeQuery(id+"F47.opFillet","BLEND_FACE",FACE,{"disambiguationData":[OSD([subQ0,subQ9]),TDD([makeQuery(id+"F42.boolean.opBoolean","COPY",EDGE,{"disambiguationData":[TD([subQ59])],"derivedFrom":subQ11})])]}),makeQuery(id+"F47.opFillet","BLEND_FACE",FACE,{"disambiguationData":[OSD([subQ0,subQ9]),TDD([makeQuery(id+"F42.boolean.opBoolean","COPY",EDGE,{"disambiguationData":[TD([makeQuery(id+"F31.opLoft","SWEPT_FACE",FACE,{"disambiguationData":[OSD([subQ52,subQ51,subQ53,sQuery(id+"F22.wireOp",EDGE,"E28.8.1"),subQ49,subQ48])]})])],"derivedFrom":subQ11})])]}),makeQuery(id+"F47.opFillet","BLEND_FACE",FACE,{"disambiguationData":[OSD([subQ0,subQ9]),TDD([makeQuery(id+"F42.boolean.opBoolean","COPY",EDGE,{"disambiguationData":[TD([makeQuery(id+"F32.opLoft","SWEPT_FACE",FACE,{"disambiguationData":[OSD([subQ47,subQ46,subQ44,sQuery(id+"F22.wireOp",EDGE,"E28.9.1"),subQ43,subQ42])]})])],"derivedFrom":subQ11})])]}),makeQuery(id+"F47.opFillet","BLEND_FACE",FACE,{"disambiguationData":[OSD([subQ0,subQ9]),TDD([makeQuery(id+"F42.boolean.opBoolean","COPY",EDGE,{"disambiguationData":[TD([makeQuery(id+"F33.opLoft","SWEPT_FACE",FACE,{"disambiguationData":[OSD([subQ41,subQ40,subQ38,sQuery(id+"F22.wireOp",EDGE,"E28.10.1"),subQ37,subQ36])]})])],"derivedFrom":subQ11})])]}),makeQuery(id+"F47.opFillet","BLEND_FACE",FACE,{"disambiguationData":[OSD([subQ0,subQ9]),TDD([makeQuery(id+"F42.boolean.opBoolean","COPY",EDGE,{"disambiguationData":[TD([makeQuery(id+"F34.opLoft","SWEPT_FACE",FACE,{"disambiguationData":[OSD([subQ35,subQ34,subQ32,sQuery(id+"F22.wireOp",EDGE,"E28.11.1"),subQ31,subQ30])]})])],"derivedFrom":subQ11})])]}),makeQuery(id+"F47.opFillet","BLEND_FACE",FACE,{"disambiguationData":[OSD([subQ0,subQ9]),TDD([makeQuery(id+"F42.boolean.opBoolean","COPY",EDGE,{"disambiguationData":[TD([makeQuery(id+"F35.opLoft","SWEPT_FACE",FACE,{"disambiguationData":[OSD([subQ29,subQ28,subQ26,sQuery(id+"F22.wireOp",EDGE,"E28.12.1"),subQ25,subQ24])]})])],"derivedFrom":subQ11})])]}),makeQuery(id+"F47.opFillet","BLEND_FACE",FACE,{"disambiguationData":[OSD([subQ0,subQ9]),TDD([makeQuery(id+"F42.boolean.opBoolean","COPY",EDGE,{"disambiguationData":[TD([makeQuery(id+"F36.opLoft","SWEPT_FACE",FACE,{"disambiguationData":[OSD([subQ23,subQ22,subQ20,sQuery(id+"F22.wireOp",EDGE,"E28.13.1"),subQ19,subQ18])]})])],"derivedFrom":subQ11})])]}),makeQuery(id+"F47.opFillet","BLEND_FACE",FACE,{"disambiguationData":[OSD([subQ0,subQ9]),TDD([makeQuery(id+"F42.boolean.opBoolean","COPY",EDGE,{"disambiguationData":[TD([makeQuery(id+"F37.opLoft","SWEPT_FACE",FACE,{"disambiguationData":[OSD([subQ16,subQ15,subQ14,sQuery(id+"F22.wireOp",EDGE,"E28.14.1"),subQ13,subQ12])]})])],"derivedFrom":subQ11})])]}),makeQuery(id+"F47.opFillet","BLEND_FACE",FACE,{"disambiguationData":[OSD([subQ0,subQ9]),TDD([makeQuery(id+"F42.boolean.opBoolean","COPY",EDGE,{"disambiguationData":[TD([makeQuery(id+"F38.opLoft","SWEPT_FACE",FACE,{"disambiguationData":[OSD([subQ8,subQ7,subQ5,sQuery(id+"F22.wireOp",EDGE,"E28.15.1"),subQ4,subQ3])]})])],"derivedFrom":subQ11})])]})],"blendedInto":[makeQuery(id+"F47.opFillet","BLEND_FACE",FACE,{"disambiguationData":[OSD([subQ0,subQ9]),TDD([makeQuery(id+"F42.boolean.opBoolean","COPY",EDGE,{"disambiguationData":[TD([makeQuery(id+"F23.opLoft","SWEPT_FACE",FACE,{"disambiguationData":[OSD([sQuery(id+"F3.wireOp",EDGE,"E20.8.0"),subQ107,subQ105,subQ104,subQ103,sQuery(id+"F22.wireOp",EDGE,"E27.right")])]})])],"derivedFrom":subQ11})])]}),makeQuery(id+"F47.opFillet","BLEND_FACE",FACE,{"disambiguationData":[OSD([subQ0,subQ9]),TDD([makeQuery(id+"F42.boolean.opBoolean","COPY",EDGE,{"disambiguationData":[TD([subQ102])],"derivedFrom":subQ11})])]}),makeQuery(id+"F47.opFillet","BLEND_FACE",FACE,{"disambiguationData":[OSD([subQ0,subQ9]),TDD([makeQuery(id+"F42.boolean.opBoolean","COPY",EDGE,{"disambiguationData":[TD([subQ95])],"derivedFrom":subQ11})])]}),makeQuery(id+"F47.opFillet","BLEND_FACE",FACE,{"disambiguationData":[OSD([subQ0,subQ9]),TDD([makeQuery(id+"F42.boolean.opBoolean","COPY",EDGE,{"disambiguationData":[TD([subQ89])],"derivedFrom":subQ11})])]}),makeQuery(id+"F47.opFillet","BLEND_FACE",FACE,{"disambiguationData":[OSD([subQ0,subQ9]),TDD([makeQuery(id+"F42.boolean.opBoolean","COPY",EDGE,{"disambiguationData":[TD([subQ82])],"derivedFrom":subQ11})])]}),makeQuery(id+"F47.opFillet","BLEND_FACE",FACE,{"disambiguationData":[OSD([subQ0,subQ9]),TDD([makeQuery(id+"F42.boolean.opBoolean","COPY",EDGE,{"disambiguationData":[TD([subQ75])],"derivedFrom":subQ11})])]}),makeQuery(id+"F47.opFillet","BLEND_FACE",FACE,{"disambiguationData":[OSD([subQ0,subQ9]),TDD([makeQuery(id+"F42.boolean.opBoolean","COPY",EDGE,{"disambiguationData":[TD([subQ68])],"derivedFrom":subQ11})])]}),makeQuery(id+"F47.opFillet","BLEND_FACE",FACE,{"disambiguationData":[OSD([subQ0,subQ9]),TDD([makeQuery(id+"F42.boolean.opBoolean","COPY",EDGE,{"disambiguationData":[TD([subQ59])],"derivedFrom":subQ11})])]}),makeQuery(id+"F47.opFillet","BLEND_FACE",FACE,{"disambiguationData":[OSD([subQ0,subQ9]),TDD([makeQuery(id+"F42.boolean.opBoolean","COPY",EDGE,{"disambiguationData":[TD([makeQuery(id+"F31.opLoft","SWEPT_FACE",FACE,{"disambiguationData":[OSD([subQ52,subQ51,subQ53,sQuery(id+"F22.wireOp",EDGE,"E28.8.1"),subQ49,subQ48])]})])],"derivedFrom":subQ11})])]}),makeQuery(id+"F47.opFillet","BLEND_FACE",FACE,{"disambiguationData":[OSD([subQ0,subQ9]),TDD([makeQuery(id+"F42.boolean.opBoolean","COPY",EDGE,{"disambiguationData":[TD([makeQuery(id+"F32.opLoft","SWEPT_FACE",FACE,{"disambiguationData":[OSD([subQ47,subQ46,subQ44,sQuery(id+"F22.wireOp",EDGE,"E28.9.1"),subQ43,subQ42])]})])],"derivedFrom":subQ11})])]}),makeQuery(id+"F47.opFillet","BLEND_FACE",FACE,{"disambiguationData":[OSD([subQ0,subQ9]),TDD([makeQuery(id+"F42.boolean.opBoolean","COPY",EDGE,{"disambiguationData":[TD([makeQuery(id+"F33.opLoft","SWEPT_FACE",FACE,{"disambiguationData":[OSD([subQ41,subQ40,subQ38,sQuery(id+"F22.wireOp",EDGE,"E28.10.1"),subQ37,subQ36])]})])],"derivedFrom":subQ11})])]}),makeQuery(id+"F47.opFillet","BLEND_FACE",FACE,{"disambiguationData":[OSD([subQ0,subQ9]),TDD([makeQuery(id+"F42.boolean.opBoolean","COPY",EDGE,{"disambiguationData":[TD([makeQuery(id+"F34.opLoft","SWEPT_FACE",FACE,{"disambiguationData":[OSD([subQ35,subQ34,subQ32,sQuery(id+"F22.wireOp",EDGE,"E28.11.1"),subQ31,subQ30])]})])],"derivedFrom":subQ11})])]}),makeQuery(id+"F47.opFillet","BLEND_FACE",FACE,{"disambiguationData":[OSD([subQ0,subQ9]),TDD([makeQuery(id+"F42.boolean.opBoolean","COPY",EDGE,{"disambiguationData":[TD([makeQuery(id+"F35.opLoft","SWEPT_FACE",FACE,{"disambiguationData":[OSD([subQ29,subQ28,subQ26,sQuery(id+"F22.wireOp",EDGE,"E28.12.1"),subQ25,subQ24])]})])],"derivedFrom":subQ11})])]}),makeQuery(id+"F47.opFillet","BLEND_FACE",FACE,{"disambiguationData":[OSD([subQ0,subQ9]),TDD([makeQuery(id+"F42.boolean.opBoolean","COPY",EDGE,{"disambiguationData":[TD([makeQuery(id+"F36.opLoft","SWEPT_FACE",FACE,{"disambiguationData":[OSD([subQ23,subQ22,subQ20,sQuery(id+"F22.wireOp",EDGE,"E28.13.1"),subQ19,subQ18])]})])],"derivedFrom":subQ11})])]}),makeQuery(id+"F47.opFillet","BLEND_FACE",FACE,{"disambiguationData":[OSD([subQ0,subQ9]),TDD([makeQuery(id+"F42.boolean.opBoolean","COPY",EDGE,{"disambiguationData":[TD([makeQuery(id+"F37.opLoft","SWEPT_FACE",FACE,{"disambiguationData":[OSD([subQ16,subQ15,subQ14,sQuery(id+"F22.wireOp",EDGE,"E28.14.1"),subQ13,subQ12])]})])],"derivedFrom":subQ11})])]}),makeQuery(id+"F47.opFillet","BLEND_FACE",FACE,{"disambiguationData":[OSD([subQ0,subQ9]),TDD([makeQuery(id+"F42.boolean.opBoolean","COPY",EDGE,{"disambiguationData":[TD([makeQuery(id+"F38.opLoft","SWEPT_FACE",FACE,{"disambiguationData":[OSD([subQ8,subQ7,subQ5,sQuery(id+"F22.wireOp",EDGE,"E28.15.1"),subQ4,subQ3])]})])],"derivedFrom":subQ11})])]})]});}
            var Q20;
            {var subQ0=sQuery(id+"F41.wireOp",EDGE,"E34");var subQ1=sQuery(id+"F41.wireOp",EDGE,"E32");Q20=makeQuery(id+"F42.boolean.opBoolean","INTERSECT",EDGE,{"derivedFrom":[makeQuery(id+"F30.opLoft","SWEPT_FACE",FACE,{"disambiguationData":[OSD([sQuery(id+"F3.wireOp",EDGE,"E20.15.0"),sQuery(id+"F3.wireOp",EDGE,"E20.15.1"),sQuery(id+"F3.wireOp",EDGE,"E20.15.3"),sQuery(id+"F22.wireOp",EDGE,"E28.7.1"),sQuery(id+"F22.wireOp",EDGE,"E28.7.2"),sQuery(id+"F22.wireOp",EDGE,"E28.7.3")])]}),makeQuery(id+"F42.opRevolve","SWEPT_FACE",FACE,{"disambiguationData":[OSD([subQ1]),TDD([makeQuery(id+"F41.imprint","IMPRINT",EDGE,{"disambiguationData":[TD([[makeQuery(id+"F41.imprint","INTERSECT",VERTEX,{"disambiguationData":[OD(0.0)],"derivedFrom":[subQ1,subQ0]}),-1.0]])],"derivedFrom":subQ1})])]})]});}
            var Q21;
            {var subQ0=sQuery(id+"F22.wireOp",EDGE,"E28.7.3");var subQ1=sQuery(id+"F22.wireOp",EDGE,"E28.7.2");var subQ2=sQuery(id+"F22.wireOp",EDGE,"E28.7.0");var subQ3=sQuery(id+"F3.wireOp",EDGE,"E20.15.3");var subQ4=sQuery(id+"F3.wireOp",EDGE,"E20.15.1");var subQ5=makeQuery(id+"F30.opLoft","SWEPT_FACE",FACE,{"disambiguationData":[OSD([subQ4,sQuery(id+"F3.wireOp",EDGE,"E20.15.2"),subQ3,subQ2,subQ1,subQ0])]});var subQ6=sQuery(id+"F22.wireOp",EDGE,"E28.7.1");var subQ7=sQuery(id+"F41.wireOp",EDGE,"E34");var subQ8=sQuery(id+"F41.wireOp",EDGE,"E32");Q21=makeQuery(id+"F44.opFillet","BLEND_EDGE",EDGE,{"blendedFrom":[makeQuery(id+"F40.boolean.opBoolean","INTERSECT",EDGE,{"derivedFrom":[subQ5,makeQuery(id+"F40.opExtrude","CAP_FACE",FACE,{"disambiguationData":[OSD([sQuery(id+"F39.wireOp",EDGE,"E29"),sQuery(id+"F39.wireOp",EDGE,"E30")])],"isStart":true})]}),makeQuery(id+"F42.boolean.opBoolean","COPY",FACE,{"disambiguationData":[TD([makeQuery(id+"F30.opLoft","SWEPT_FACE",FACE,{"disambiguationData":[OSD([sQuery(id+"F3.wireOp",EDGE,"E20.15.0"),subQ4,subQ3,subQ6,subQ1,subQ0])]})])],"derivedFrom":makeQuery(id+"F42.opRevolve","SWEPT_FACE",FACE,{"disambiguationData":[OSD([subQ8]),TDD([makeQuery(id+"F41.imprint","IMPRINT",EDGE,{"disambiguationData":[TD([[makeQuery(id+"F41.imprint","INTERSECT",VERTEX,{"disambiguationData":[OD(0.0)],"derivedFrom":[subQ8,subQ7]}),-1.0]])],"derivedFrom":subQ8})])]})})],"blendedInto":[makeQuery(id+"F42.boolean.opBoolean","COPY",FACE,{"disambiguationData":[TD([makeQuery(id+"F30.opLoft","SWEPT_FACE",FACE,{"disambiguationData":[OSD([sQuery(id+"F3.wireOp",EDGE,"E20.15.0"),subQ4,subQ3,subQ6,subQ1,subQ0])]})])],"derivedFrom":makeQuery(id+"F42.opRevolve","SWEPT_FACE",FACE,{"disambiguationData":[OSD([subQ8]),TDD([makeQuery(id+"F41.imprint","IMPRINT",EDGE,{"disambiguationData":[TD([[makeQuery(id+"F41.imprint","INTERSECT",VERTEX,{"disambiguationData":[OD(0.0)],"derivedFrom":[subQ8,subQ7]}),-1.0]])],"derivedFrom":subQ8})])]})})]});}
            var Q22;
            {var subQ0=sQuery(id+"F41.wireOp",EDGE,"E34");var subQ1=sQuery(id+"F41.wireOp",EDGE,"E32");Q22=makeQuery(id+"F42.boolean.opBoolean","INTERSECT",EDGE,{"derivedFrom":[makeQuery(id+"F29.opLoft","SWEPT_FACE",FACE,{"disambiguationData":[OSD([sQuery(id+"F3.wireOp",EDGE,"E20.14.0"),sQuery(id+"F3.wireOp",EDGE,"E20.14.1"),sQuery(id+"F3.wireOp",EDGE,"E20.14.3"),sQuery(id+"F22.wireOp",EDGE,"E28.6.1"),sQuery(id+"F22.wireOp",EDGE,"E28.6.2"),sQuery(id+"F22.wireOp",EDGE,"E28.6.3")])]}),makeQuery(id+"F42.opRevolve","SWEPT_FACE",FACE,{"disambiguationData":[OSD([subQ1]),TDD([makeQuery(id+"F41.imprint","IMPRINT",EDGE,{"disambiguationData":[TD([[makeQuery(id+"F41.imprint","INTERSECT",VERTEX,{"disambiguationData":[OD(0.0)],"derivedFrom":[subQ1,subQ0]}),-1.0]])],"derivedFrom":subQ1})])]})]});}
            var Q23;
            {var subQ0=sQuery(id+"F41.wireOp",EDGE,"E37");var subQ1=makeQuery(id+"F42.opRevolve","SWEPT_FACE",FACE,{"disambiguationData":[OSD([subQ0])]});var subQ2=makeQuery(id+"F40.opExtrude","CAP_FACE",FACE,{"disambiguationData":[OSD([sQuery(id+"F39.wireOp",EDGE,"E29"),sQuery(id+"F39.wireOp",EDGE,"E30")])],"isStart":true});var subQ3=sQuery(id+"F22.wireOp",EDGE,"E28.15.3");var subQ4=sQuery(id+"F22.wireOp",EDGE,"E28.15.2");var subQ5=sQuery(id+"F3.wireOp",EDGE,"E20.7.3");var subQ7=sQuery(id+"F3.wireOp",EDGE,"E20.7.1");var subQ8=sQuery(id+"F3.wireOp",EDGE,"E20.7.0");var subQ9=sQuery(id+"F41.wireOp",EDGE,"E38");var subQ10=makeQuery(id+"F42.opRevolve","SWEPT_FACE",FACE,{"disambiguationData":[OSD([subQ9])]});var subQ11=makeQuery(id+"F42.opRevolve","SWEPT_EDGE",EDGE,{"disambiguationData":[OSD([subQ0,subQ9])]});var subQ12=sQuery(id+"F22.wireOp",EDGE,"E28.14.3");var subQ13=sQuery(id+"F22.wireOp",EDGE,"E28.14.2");var subQ14=sQuery(id+"F3.wireOp",EDGE,"E20.6.3");var subQ15=sQuery(id+"F3.wireOp",EDGE,"E20.6.1");var subQ16=sQuery(id+"F3.wireOp",EDGE,"E20.6.0");var subQ18=sQuery(id+"F22.wireOp",EDGE,"E28.13.3");var subQ19=sQuery(id+"F22.wireOp",EDGE,"E28.13.2");var subQ20=sQuery(id+"F3.wireOp",EDGE,"E20.5.3");var subQ22=sQuery(id+"F3.wireOp",EDGE,"E20.5.1");var subQ23=sQuery(id+"F3.wireOp",EDGE,"E20.5.0");var subQ24=sQuery(id+"F22.wireOp",EDGE,"E28.12.3");var subQ25=sQuery(id+"F22.wireOp",EDGE,"E28.12.2");var subQ26=sQuery(id+"F3.wireOp",EDGE,"E20.4.3");var subQ28=sQuery(id+"F3.wireOp",EDGE,"E20.4.1");var subQ29=sQuery(id+"F3.wireOp",EDGE,"E20.4.0");var subQ30=sQuery(id+"F22.wireOp",EDGE,"E28.11.3");var subQ31=sQuery(id+"F22.wireOp",EDGE,"E28.11.2");var subQ32=sQuery(id+"F3.wireOp",EDGE,"E20.3.3");var subQ34=sQuery(id+"F3.wireOp",EDGE,"E20.3.1");var subQ35=sQuery(id+"F3.wireOp",EDGE,"E20.3.0");var subQ36=sQuery(id+"F22.wireOp",EDGE,"E28.10.3");var subQ37=sQuery(id+"F22.wireOp",EDGE,"E28.10.2");var subQ38=sQuery(id+"F3.wireOp",EDGE,"E20.2.3");var subQ40=sQuery(id+"F3.wireOp",EDGE,"E20.2.1");var subQ41=sQuery(id+"F3.wireOp",EDGE,"E20.2.0");var subQ42=sQuery(id+"F22.wireOp",EDGE,"E28.9.3");var subQ43=sQuery(id+"F22.wireOp",EDGE,"E28.9.2");var subQ44=sQuery(id+"F3.wireOp",EDGE,"E20.1.3");var subQ46=sQuery(id+"F3.wireOp",EDGE,"E20.1.1");var subQ47=sQuery(id+"F3.wireOp",EDGE,"E20.1.0");var subQ48=sQuery(id+"F22.wireOp",EDGE,"E28.8.3");var subQ49=sQuery(id+"F22.wireOp",EDGE,"E28.8.2");var subQ51=sQuery(id+"F3.wireOp",EDGE,"E18.top");var subQ52=sQuery(id+"F3.wireOp",EDGE,"E18.bottom");var subQ53=sQuery(id+"F3.wireOp",EDGE,"E18.left");var subQ54=sQuery(id+"F22.wireOp",EDGE,"E28.7.3");var subQ55=sQuery(id+"F22.wireOp",EDGE,"E28.7.2");var subQ56=sQuery(id+"F3.wireOp",EDGE,"E20.15.3");var subQ57=sQuery(id+"F3.wireOp",EDGE,"E20.15.1");var subQ58=sQuery(id+"F3.wireOp",EDGE,"E20.15.0");var subQ60=sQuery(id+"F22.wireOp",EDGE,"E28.6.3");var subQ61=sQuery(id+"F22.wireOp",EDGE,"E28.6.2");var subQ62=sQuery(id+"F3.wireOp",EDGE,"E20.14.3");var subQ64=sQuery(id+"F3.wireOp",EDGE,"E20.14.1");var subQ66=sQuery(id+"F3.wireOp",EDGE,"E20.14.0");var subQ67=makeQuery(id+"F29.opLoft","SWEPT_FACE",FACE,{"disambiguationData":[OSD([subQ66,subQ64,subQ62,sQuery(id+"F22.wireOp",EDGE,"E28.6.1"),subQ61,subQ60])]});var subQ68=sQuery(id+"F22.wireOp",EDGE,"E28.5.3");var subQ69=sQuery(id+"F22.wireOp",EDGE,"E28.5.2");var subQ70=sQuery(id+"F3.wireOp",EDGE,"E20.13.3");var subQ72=sQuery(id+"F3.wireOp",EDGE,"E20.13.1");var subQ73=sQuery(id+"F3.wireOp",EDGE,"E20.13.0");var subQ74=makeQuery(id+"F28.opLoft","SWEPT_FACE",FACE,{"disambiguationData":[OSD([subQ73,subQ72,subQ70,sQuery(id+"F22.wireOp",EDGE,"E28.5.1"),subQ69,subQ68])]});var subQ75=sQuery(id+"F22.wireOp",EDGE,"E28.4.3");var subQ76=sQuery(id+"F22.wireOp",EDGE,"E28.4.2");var subQ77=sQuery(id+"F3.wireOp",EDGE,"E20.12.3");var subQ79=sQuery(id+"F3.wireOp",EDGE,"E20.12.1");var subQ80=sQuery(id+"F3.wireOp",EDGE,"E20.12.0");var subQ81=makeQuery(id+"F27.opLoft","SWEPT_FACE",FACE,{"disambiguationData":[OSD([subQ80,subQ79,subQ77,sQuery(id+"F22.wireOp",EDGE,"E28.4.1"),subQ76,subQ75])]});var subQ82=sQuery(id+"F22.wireOp",EDGE,"E28.3.3");var subQ83=sQuery(id+"F22.wireOp",EDGE,"E28.3.2");var subQ84=sQuery(id+"F3.wireOp",EDGE,"E20.11.3");var subQ86=sQuery(id+"F3.wireOp",EDGE,"E20.11.1");var subQ87=sQuery(id+"F3.wireOp",EDGE,"E20.11.0");var subQ88=makeQuery(id+"F26.opLoft","SWEPT_FACE",FACE,{"disambiguationData":[OSD([subQ87,subQ86,subQ84,sQuery(id+"F22.wireOp",EDGE,"E28.3.1"),subQ83,subQ82])]});var subQ89=sQuery(id+"F22.wireOp",EDGE,"E28.2.3");var subQ90=sQuery(id+"F22.wireOp",EDGE,"E28.2.2");var subQ91=sQuery(id+"F3.wireOp",EDGE,"E20.10.3");var subQ92=sQuery(id+"F3.wireOp",EDGE,"E20.10.1");var subQ93=sQuery(id+"F3.wireOp",EDGE,"E20.10.0");var subQ94=makeQuery(id+"F25.opLoft","SWEPT_FACE",FACE,{"disambiguationData":[OSD([subQ93,subQ92,subQ91,sQuery(id+"F22.wireOp",EDGE,"E28.2.1"),subQ90,subQ89])]});var subQ96=sQuery(id+"F22.wireOp",EDGE,"E28.1.3");var subQ97=sQuery(id+"F22.wireOp",EDGE,"E28.1.2");var subQ98=sQuery(id+"F3.wireOp",EDGE,"E20.9.3");var subQ99=sQuery(id+"F3.wireOp",EDGE,"E20.9.1");var subQ100=sQuery(id+"F3.wireOp",EDGE,"E20.9.0");var subQ101=makeQuery(id+"F24.opLoft","SWEPT_FACE",FACE,{"disambiguationData":[OSD([subQ100,subQ99,subQ98,sQuery(id+"F22.wireOp",EDGE,"E28.1.1"),subQ97,subQ96])]});var subQ102=sQuery(id+"F22.wireOp",EDGE,"E27.top");var subQ103=sQuery(id+"F22.wireOp",EDGE,"E27.bottom");var subQ104=sQuery(id+"F3.wireOp",EDGE,"E20.8.3");var subQ106=sQuery(id+"F3.wireOp",EDGE,"E20.8.1");var subQ110=makeQuery(id+"F42.boolean.opBoolean","COPY",FACE,{"disambiguationData":[TD([subQ67])],"derivedFrom":subQ10});var subQ130=makeQuery(id+"F5.opLoft","CAP_FACE",FACE,{"disambiguationData":[OSD([makeQuery(id+"F3.imprint","IMPRINT",FACE,{"disambiguationData":[TD([[makeQuery(id+"F3.imprint","IMPRINT",EDGE,{"derivedFrom":subQ52}),1.0]])]})])],"isStart":true});var subQ182=makeQuery(id+"F29.boolean.opBoolean","INTERSECT",EDGE,{"derivedFrom":[makeQuery(id+"F28.boolean.opBoolean","SPLIT",FACE,{"disambiguationData":[TD([subQ130])],"derivedFrom":makeQuery(id+"F27.boolean.opBoolean","SPLIT",FACE,{"disambiguationData":[TD([subQ130])],"derivedFrom":makeQuery(id+"F26.boolean.opBoolean","SPLIT",FACE,{"disambiguationData":[TD([subQ130])],"derivedFrom":makeQuery(id+"F25.boolean.opBoolean","SPLIT",FACE,{"disambiguationData":[TD([subQ130])],"derivedFrom":makeQuery(id+"F24.boolean.opBoolean","SPLIT",FACE,{"disambiguationData":[TD([subQ130])],"derivedFrom":makeQuery(id+"F1.opRevolve","SWEPT_FACE",FACE,{"disambiguationData":[OSD([sQuery(id+"F0.wireOp",EDGE,"E13")])]})})})})})}),subQ67]});Q23=makeQuery(id+"F48.opFillet","BLEND_EDGE",EDGE,{"blendedFrom":[makeQuery(id+"F47.opFillet","TWEAK_EDGE",EDGE,{"derivedFrom":[makeQuery(id+"F45.opFillet","BLEND_VERTEX",VERTEX,{"blendedFrom":[subQ182,subQ67,subQ110],"blendedInto":[subQ67,subQ110]}),makeQuery(id+"F45.opFillet","BLEND_VERTEX",VERTEX,{"blendedFrom":[subQ182,makeQuery(id+"F42.boolean.opBoolean","MERGE",FACE,{"derivedFrom":[subQ2,subQ1]}),subQ110],"blendedInto":[makeQuery(id+"F42.boolean.opBoolean","MERGE",FACE,{"derivedFrom":[subQ2,subQ1]}),subQ110]})]}),makeQuery(id+"F47.opFillet","BLEND_FACE",FACE,{"disambiguationData":[OSD([subQ0,subQ9]),TDD([makeQuery(id+"F42.boolean.opBoolean","COPY",EDGE,{"disambiguationData":[TD([makeQuery(id+"F23.opLoft","SWEPT_FACE",FACE,{"disambiguationData":[OSD([sQuery(id+"F3.wireOp",EDGE,"E20.8.0"),subQ106,subQ104,subQ103,subQ102,sQuery(id+"F22.wireOp",EDGE,"E27.right")])]})])],"derivedFrom":subQ11})])]}),makeQuery(id+"F47.opFillet","BLEND_FACE",FACE,{"disambiguationData":[OSD([subQ0,subQ9]),TDD([makeQuery(id+"F42.boolean.opBoolean","COPY",EDGE,{"disambiguationData":[TD([subQ101])],"derivedFrom":subQ11})])]}),makeQuery(id+"F47.opFillet","BLEND_FACE",FACE,{"disambiguationData":[OSD([subQ0,subQ9]),TDD([makeQuery(id+"F42.boolean.opBoolean","COPY",EDGE,{"disambiguationData":[TD([subQ94])],"derivedFrom":subQ11})])]}),makeQuery(id+"F47.opFillet","BLEND_FACE",FACE,{"disambiguationData":[OSD([subQ0,subQ9]),TDD([makeQuery(id+"F42.boolean.opBoolean","COPY",EDGE,{"disambiguationData":[TD([subQ88])],"derivedFrom":subQ11})])]}),makeQuery(id+"F47.opFillet","BLEND_FACE",FACE,{"disambiguationData":[OSD([subQ0,subQ9]),TDD([makeQuery(id+"F42.boolean.opBoolean","COPY",EDGE,{"disambiguationData":[TD([subQ81])],"derivedFrom":subQ11})])]}),makeQuery(id+"F47.opFillet","BLEND_FACE",FACE,{"disambiguationData":[OSD([subQ0,subQ9]),TDD([makeQuery(id+"F42.boolean.opBoolean","COPY",EDGE,{"disambiguationData":[TD([subQ74])],"derivedFrom":subQ11})])]}),makeQuery(id+"F47.opFillet","BLEND_FACE",FACE,{"disambiguationData":[OSD([subQ0,subQ9]),TDD([makeQuery(id+"F42.boolean.opBoolean","COPY",EDGE,{"disambiguationData":[TD([subQ67])],"derivedFrom":subQ11})])]}),makeQuery(id+"F47.opFillet","BLEND_FACE",FACE,{"disambiguationData":[OSD([subQ0,subQ9]),TDD([makeQuery(id+"F42.boolean.opBoolean","COPY",EDGE,{"disambiguationData":[TD([makeQuery(id+"F30.opLoft","SWEPT_FACE",FACE,{"disambiguationData":[OSD([subQ58,subQ57,subQ56,sQuery(id+"F22.wireOp",EDGE,"E28.7.1"),subQ55,subQ54])]})])],"derivedFrom":subQ11})])]}),makeQuery(id+"F47.opFillet","BLEND_FACE",FACE,{"disambiguationData":[OSD([subQ0,subQ9]),TDD([makeQuery(id+"F42.boolean.opBoolean","COPY",EDGE,{"disambiguationData":[TD([makeQuery(id+"F31.opLoft","SWEPT_FACE",FACE,{"disambiguationData":[OSD([subQ52,subQ51,subQ53,sQuery(id+"F22.wireOp",EDGE,"E28.8.1"),subQ49,subQ48])]})])],"derivedFrom":subQ11})])]}),makeQuery(id+"F47.opFillet","BLEND_FACE",FACE,{"disambiguationData":[OSD([subQ0,subQ9]),TDD([makeQuery(id+"F42.boolean.opBoolean","COPY",EDGE,{"disambiguationData":[TD([makeQuery(id+"F32.opLoft","SWEPT_FACE",FACE,{"disambiguationData":[OSD([subQ47,subQ46,subQ44,sQuery(id+"F22.wireOp",EDGE,"E28.9.1"),subQ43,subQ42])]})])],"derivedFrom":subQ11})])]}),makeQuery(id+"F47.opFillet","BLEND_FACE",FACE,{"disambiguationData":[OSD([subQ0,subQ9]),TDD([makeQuery(id+"F42.boolean.opBoolean","COPY",EDGE,{"disambiguationData":[TD([makeQuery(id+"F33.opLoft","SWEPT_FACE",FACE,{"disambiguationData":[OSD([subQ41,subQ40,subQ38,sQuery(id+"F22.wireOp",EDGE,"E28.10.1"),subQ37,subQ36])]})])],"derivedFrom":subQ11})])]}),makeQuery(id+"F47.opFillet","BLEND_FACE",FACE,{"disambiguationData":[OSD([subQ0,subQ9]),TDD([makeQuery(id+"F42.boolean.opBoolean","COPY",EDGE,{"disambiguationData":[TD([makeQuery(id+"F34.opLoft","SWEPT_FACE",FACE,{"disambiguationData":[OSD([subQ35,subQ34,subQ32,sQuery(id+"F22.wireOp",EDGE,"E28.11.1"),subQ31,subQ30])]})])],"derivedFrom":subQ11})])]}),makeQuery(id+"F47.opFillet","BLEND_FACE",FACE,{"disambiguationData":[OSD([subQ0,subQ9]),TDD([makeQuery(id+"F42.boolean.opBoolean","COPY",EDGE,{"disambiguationData":[TD([makeQuery(id+"F35.opLoft","SWEPT_FACE",FACE,{"disambiguationData":[OSD([subQ29,subQ28,subQ26,sQuery(id+"F22.wireOp",EDGE,"E28.12.1"),subQ25,subQ24])]})])],"derivedFrom":subQ11})])]}),makeQuery(id+"F47.opFillet","BLEND_FACE",FACE,{"disambiguationData":[OSD([subQ0,subQ9]),TDD([makeQuery(id+"F42.boolean.opBoolean","COPY",EDGE,{"disambiguationData":[TD([makeQuery(id+"F36.opLoft","SWEPT_FACE",FACE,{"disambiguationData":[OSD([subQ23,subQ22,subQ20,sQuery(id+"F22.wireOp",EDGE,"E28.13.1"),subQ19,subQ18])]})])],"derivedFrom":subQ11})])]}),makeQuery(id+"F47.opFillet","BLEND_FACE",FACE,{"disambiguationData":[OSD([subQ0,subQ9]),TDD([makeQuery(id+"F42.boolean.opBoolean","COPY",EDGE,{"disambiguationData":[TD([makeQuery(id+"F37.opLoft","SWEPT_FACE",FACE,{"disambiguationData":[OSD([subQ16,subQ15,subQ14,sQuery(id+"F22.wireOp",EDGE,"E28.14.1"),subQ13,subQ12])]})])],"derivedFrom":subQ11})])]}),makeQuery(id+"F47.opFillet","BLEND_FACE",FACE,{"disambiguationData":[OSD([subQ0,subQ9]),TDD([makeQuery(id+"F42.boolean.opBoolean","COPY",EDGE,{"disambiguationData":[TD([makeQuery(id+"F38.opLoft","SWEPT_FACE",FACE,{"disambiguationData":[OSD([subQ8,subQ7,subQ5,sQuery(id+"F22.wireOp",EDGE,"E28.15.1"),subQ4,subQ3])]})])],"derivedFrom":subQ11})])]})],"blendedInto":[makeQuery(id+"F47.opFillet","BLEND_FACE",FACE,{"disambiguationData":[OSD([subQ0,subQ9]),TDD([makeQuery(id+"F42.boolean.opBoolean","COPY",EDGE,{"disambiguationData":[TD([makeQuery(id+"F23.opLoft","SWEPT_FACE",FACE,{"disambiguationData":[OSD([sQuery(id+"F3.wireOp",EDGE,"E20.8.0"),subQ106,subQ104,subQ103,subQ102,sQuery(id+"F22.wireOp",EDGE,"E27.right")])]})])],"derivedFrom":subQ11})])]}),makeQuery(id+"F47.opFillet","BLEND_FACE",FACE,{"disambiguationData":[OSD([subQ0,subQ9]),TDD([makeQuery(id+"F42.boolean.opBoolean","COPY",EDGE,{"disambiguationData":[TD([subQ101])],"derivedFrom":subQ11})])]}),makeQuery(id+"F47.opFillet","BLEND_FACE",FACE,{"disambiguationData":[OSD([subQ0,subQ9]),TDD([makeQuery(id+"F42.boolean.opBoolean","COPY",EDGE,{"disambiguationData":[TD([subQ94])],"derivedFrom":subQ11})])]}),makeQuery(id+"F47.opFillet","BLEND_FACE",FACE,{"disambiguationData":[OSD([subQ0,subQ9]),TDD([makeQuery(id+"F42.boolean.opBoolean","COPY",EDGE,{"disambiguationData":[TD([subQ88])],"derivedFrom":subQ11})])]}),makeQuery(id+"F47.opFillet","BLEND_FACE",FACE,{"disambiguationData":[OSD([subQ0,subQ9]),TDD([makeQuery(id+"F42.boolean.opBoolean","COPY",EDGE,{"disambiguationData":[TD([subQ81])],"derivedFrom":subQ11})])]}),makeQuery(id+"F47.opFillet","BLEND_FACE",FACE,{"disambiguationData":[OSD([subQ0,subQ9]),TDD([makeQuery(id+"F42.boolean.opBoolean","COPY",EDGE,{"disambiguationData":[TD([subQ74])],"derivedFrom":subQ11})])]}),makeQuery(id+"F47.opFillet","BLEND_FACE",FACE,{"disambiguationData":[OSD([subQ0,subQ9]),TDD([makeQuery(id+"F42.boolean.opBoolean","COPY",EDGE,{"disambiguationData":[TD([subQ67])],"derivedFrom":subQ11})])]}),makeQuery(id+"F47.opFillet","BLEND_FACE",FACE,{"disambiguationData":[OSD([subQ0,subQ9]),TDD([makeQuery(id+"F42.boolean.opBoolean","COPY",EDGE,{"disambiguationData":[TD([makeQuery(id+"F30.opLoft","SWEPT_FACE",FACE,{"disambiguationData":[OSD([subQ58,subQ57,subQ56,sQuery(id+"F22.wireOp",EDGE,"E28.7.1"),subQ55,subQ54])]})])],"derivedFrom":subQ11})])]}),makeQuery(id+"F47.opFillet","BLEND_FACE",FACE,{"disambiguationData":[OSD([subQ0,subQ9]),TDD([makeQuery(id+"F42.boolean.opBoolean","COPY",EDGE,{"disambiguationData":[TD([makeQuery(id+"F31.opLoft","SWEPT_FACE",FACE,{"disambiguationData":[OSD([subQ52,subQ51,subQ53,sQuery(id+"F22.wireOp",EDGE,"E28.8.1"),subQ49,subQ48])]})])],"derivedFrom":subQ11})])]}),makeQuery(id+"F47.opFillet","BLEND_FACE",FACE,{"disambiguationData":[OSD([subQ0,subQ9]),TDD([makeQuery(id+"F42.boolean.opBoolean","COPY",EDGE,{"disambiguationData":[TD([makeQuery(id+"F32.opLoft","SWEPT_FACE",FACE,{"disambiguationData":[OSD([subQ47,subQ46,subQ44,sQuery(id+"F22.wireOp",EDGE,"E28.9.1"),subQ43,subQ42])]})])],"derivedFrom":subQ11})])]}),makeQuery(id+"F47.opFillet","BLEND_FACE",FACE,{"disambiguationData":[OSD([subQ0,subQ9]),TDD([makeQuery(id+"F42.boolean.opBoolean","COPY",EDGE,{"disambiguationData":[TD([makeQuery(id+"F33.opLoft","SWEPT_FACE",FACE,{"disambiguationData":[OSD([subQ41,subQ40,subQ38,sQuery(id+"F22.wireOp",EDGE,"E28.10.1"),subQ37,subQ36])]})])],"derivedFrom":subQ11})])]}),makeQuery(id+"F47.opFillet","BLEND_FACE",FACE,{"disambiguationData":[OSD([subQ0,subQ9]),TDD([makeQuery(id+"F42.boolean.opBoolean","COPY",EDGE,{"disambiguationData":[TD([makeQuery(id+"F34.opLoft","SWEPT_FACE",FACE,{"disambiguationData":[OSD([subQ35,subQ34,subQ32,sQuery(id+"F22.wireOp",EDGE,"E28.11.1"),subQ31,subQ30])]})])],"derivedFrom":subQ11})])]}),makeQuery(id+"F47.opFillet","BLEND_FACE",FACE,{"disambiguationData":[OSD([subQ0,subQ9]),TDD([makeQuery(id+"F42.boolean.opBoolean","COPY",EDGE,{"disambiguationData":[TD([makeQuery(id+"F35.opLoft","SWEPT_FACE",FACE,{"disambiguationData":[OSD([subQ29,subQ28,subQ26,sQuery(id+"F22.wireOp",EDGE,"E28.12.1"),subQ25,subQ24])]})])],"derivedFrom":subQ11})])]}),makeQuery(id+"F47.opFillet","BLEND_FACE",FACE,{"disambiguationData":[OSD([subQ0,subQ9]),TDD([makeQuery(id+"F42.boolean.opBoolean","COPY",EDGE,{"disambiguationData":[TD([makeQuery(id+"F36.opLoft","SWEPT_FACE",FACE,{"disambiguationData":[OSD([subQ23,subQ22,subQ20,sQuery(id+"F22.wireOp",EDGE,"E28.13.1"),subQ19,subQ18])]})])],"derivedFrom":subQ11})])]}),makeQuery(id+"F47.opFillet","BLEND_FACE",FACE,{"disambiguationData":[OSD([subQ0,subQ9]),TDD([makeQuery(id+"F42.boolean.opBoolean","COPY",EDGE,{"disambiguationData":[TD([makeQuery(id+"F37.opLoft","SWEPT_FACE",FACE,{"disambiguationData":[OSD([subQ16,subQ15,subQ14,sQuery(id+"F22.wireOp",EDGE,"E28.14.1"),subQ13,subQ12])]})])],"derivedFrom":subQ11})])]}),makeQuery(id+"F47.opFillet","BLEND_FACE",FACE,{"disambiguationData":[OSD([subQ0,subQ9]),TDD([makeQuery(id+"F42.boolean.opBoolean","COPY",EDGE,{"disambiguationData":[TD([makeQuery(id+"F38.opLoft","SWEPT_FACE",FACE,{"disambiguationData":[OSD([subQ8,subQ7,subQ5,sQuery(id+"F22.wireOp",EDGE,"E28.15.1"),subQ4,subQ3])]})])],"derivedFrom":subQ11})])]})]});}
            var Q24;
            {var subQ0=sQuery(id+"F41.wireOp",EDGE,"E34");var subQ1=sQuery(id+"F41.wireOp",EDGE,"E32");Q24=makeQuery(id+"F42.boolean.opBoolean","INTERSECT",EDGE,{"derivedFrom":[makeQuery(id+"F28.opLoft","SWEPT_FACE",FACE,{"disambiguationData":[OSD([sQuery(id+"F3.wireOp",EDGE,"E20.13.0"),sQuery(id+"F3.wireOp",EDGE,"E20.13.1"),sQuery(id+"F3.wireOp",EDGE,"E20.13.3"),sQuery(id+"F22.wireOp",EDGE,"E28.5.1"),sQuery(id+"F22.wireOp",EDGE,"E28.5.2"),sQuery(id+"F22.wireOp",EDGE,"E28.5.3")])]}),makeQuery(id+"F42.opRevolve","SWEPT_FACE",FACE,{"disambiguationData":[OSD([subQ1]),TDD([makeQuery(id+"F41.imprint","IMPRINT",EDGE,{"disambiguationData":[TD([[makeQuery(id+"F41.imprint","INTERSECT",VERTEX,{"disambiguationData":[OD(0.0)],"derivedFrom":[subQ1,subQ0]}),-1.0]])],"derivedFrom":subQ1})])]})]});}
            var Q25;
            {var subQ0=sQuery(id+"F22.wireOp",EDGE,"E28.6.3");var subQ1=sQuery(id+"F22.wireOp",EDGE,"E28.6.2");var subQ2=sQuery(id+"F22.wireOp",EDGE,"E28.6.0");var subQ3=sQuery(id+"F3.wireOp",EDGE,"E20.14.3");var subQ4=sQuery(id+"F3.wireOp",EDGE,"E20.14.1");var subQ5=makeQuery(id+"F29.opLoft","SWEPT_FACE",FACE,{"disambiguationData":[OSD([subQ4,sQuery(id+"F3.wireOp",EDGE,"E20.14.2"),subQ3,subQ2,subQ1,subQ0])]});var subQ6=sQuery(id+"F22.wireOp",EDGE,"E28.6.1");var subQ7=sQuery(id+"F41.wireOp",EDGE,"E34");var subQ8=sQuery(id+"F41.wireOp",EDGE,"E32");Q25=makeQuery(id+"F44.opFillet","BLEND_EDGE",EDGE,{"blendedFrom":[makeQuery(id+"F40.boolean.opBoolean","INTERSECT",EDGE,{"derivedFrom":[subQ5,makeQuery(id+"F40.opExtrude","CAP_FACE",FACE,{"disambiguationData":[OSD([sQuery(id+"F39.wireOp",EDGE,"E29"),sQuery(id+"F39.wireOp",EDGE,"E30")])],"isStart":true})]}),makeQuery(id+"F42.boolean.opBoolean","COPY",FACE,{"disambiguationData":[TD([makeQuery(id+"F29.opLoft","SWEPT_FACE",FACE,{"disambiguationData":[OSD([sQuery(id+"F3.wireOp",EDGE,"E20.14.0"),subQ4,subQ3,subQ6,subQ1,subQ0])]})])],"derivedFrom":makeQuery(id+"F42.opRevolve","SWEPT_FACE",FACE,{"disambiguationData":[OSD([subQ8]),TDD([makeQuery(id+"F41.imprint","IMPRINT",EDGE,{"disambiguationData":[TD([[makeQuery(id+"F41.imprint","INTERSECT",VERTEX,{"disambiguationData":[OD(0.0)],"derivedFrom":[subQ8,subQ7]}),-1.0]])],"derivedFrom":subQ8})])]})})],"blendedInto":[makeQuery(id+"F42.boolean.opBoolean","COPY",FACE,{"disambiguationData":[TD([makeQuery(id+"F29.opLoft","SWEPT_FACE",FACE,{"disambiguationData":[OSD([sQuery(id+"F3.wireOp",EDGE,"E20.14.0"),subQ4,subQ3,subQ6,subQ1,subQ0])]})])],"derivedFrom":makeQuery(id+"F42.opRevolve","SWEPT_FACE",FACE,{"disambiguationData":[OSD([subQ8]),TDD([makeQuery(id+"F41.imprint","IMPRINT",EDGE,{"disambiguationData":[TD([[makeQuery(id+"F41.imprint","INTERSECT",VERTEX,{"disambiguationData":[OD(0.0)],"derivedFrom":[subQ8,subQ7]}),-1.0]])],"derivedFrom":subQ8})])]})})]});}
            var Q26;
            {var subQ0=sQuery(id+"F41.wireOp",EDGE,"E37");var subQ1=makeQuery(id+"F42.opRevolve","SWEPT_FACE",FACE,{"disambiguationData":[OSD([subQ0])]});var subQ2=makeQuery(id+"F40.opExtrude","CAP_FACE",FACE,{"disambiguationData":[OSD([sQuery(id+"F39.wireOp",EDGE,"E29"),sQuery(id+"F39.wireOp",EDGE,"E30")])],"isStart":true});var subQ3=sQuery(id+"F22.wireOp",EDGE,"E28.15.3");var subQ4=sQuery(id+"F22.wireOp",EDGE,"E28.15.2");var subQ5=sQuery(id+"F3.wireOp",EDGE,"E20.7.3");var subQ7=sQuery(id+"F3.wireOp",EDGE,"E20.7.1");var subQ8=sQuery(id+"F3.wireOp",EDGE,"E20.7.0");var subQ9=sQuery(id+"F41.wireOp",EDGE,"E38");var subQ10=makeQuery(id+"F42.opRevolve","SWEPT_FACE",FACE,{"disambiguationData":[OSD([subQ9])]});var subQ11=makeQuery(id+"F42.opRevolve","SWEPT_EDGE",EDGE,{"disambiguationData":[OSD([subQ0,subQ9])]});var subQ12=sQuery(id+"F22.wireOp",EDGE,"E28.14.3");var subQ13=sQuery(id+"F22.wireOp",EDGE,"E28.14.2");var subQ14=sQuery(id+"F3.wireOp",EDGE,"E20.6.3");var subQ15=sQuery(id+"F3.wireOp",EDGE,"E20.6.1");var subQ16=sQuery(id+"F3.wireOp",EDGE,"E20.6.0");var subQ18=sQuery(id+"F22.wireOp",EDGE,"E28.13.3");var subQ19=sQuery(id+"F22.wireOp",EDGE,"E28.13.2");var subQ20=sQuery(id+"F3.wireOp",EDGE,"E20.5.3");var subQ22=sQuery(id+"F3.wireOp",EDGE,"E20.5.1");var subQ23=sQuery(id+"F3.wireOp",EDGE,"E20.5.0");var subQ24=sQuery(id+"F22.wireOp",EDGE,"E28.12.3");var subQ25=sQuery(id+"F22.wireOp",EDGE,"E28.12.2");var subQ26=sQuery(id+"F3.wireOp",EDGE,"E20.4.3");var subQ28=sQuery(id+"F3.wireOp",EDGE,"E20.4.1");var subQ29=sQuery(id+"F3.wireOp",EDGE,"E20.4.0");var subQ30=sQuery(id+"F22.wireOp",EDGE,"E28.11.3");var subQ31=sQuery(id+"F22.wireOp",EDGE,"E28.11.2");var subQ32=sQuery(id+"F3.wireOp",EDGE,"E20.3.3");var subQ34=sQuery(id+"F3.wireOp",EDGE,"E20.3.1");var subQ35=sQuery(id+"F3.wireOp",EDGE,"E20.3.0");var subQ36=sQuery(id+"F22.wireOp",EDGE,"E28.10.3");var subQ37=sQuery(id+"F22.wireOp",EDGE,"E28.10.2");var subQ38=sQuery(id+"F3.wireOp",EDGE,"E20.2.3");var subQ40=sQuery(id+"F3.wireOp",EDGE,"E20.2.1");var subQ41=sQuery(id+"F3.wireOp",EDGE,"E20.2.0");var subQ42=sQuery(id+"F22.wireOp",EDGE,"E28.9.3");var subQ43=sQuery(id+"F22.wireOp",EDGE,"E28.9.2");var subQ44=sQuery(id+"F3.wireOp",EDGE,"E20.1.3");var subQ46=sQuery(id+"F3.wireOp",EDGE,"E20.1.1");var subQ47=sQuery(id+"F3.wireOp",EDGE,"E20.1.0");var subQ48=sQuery(id+"F22.wireOp",EDGE,"E28.8.3");var subQ49=sQuery(id+"F22.wireOp",EDGE,"E28.8.2");var subQ51=sQuery(id+"F3.wireOp",EDGE,"E18.top");var subQ52=sQuery(id+"F3.wireOp",EDGE,"E18.bottom");var subQ53=sQuery(id+"F3.wireOp",EDGE,"E18.left");var subQ54=sQuery(id+"F22.wireOp",EDGE,"E28.7.3");var subQ55=sQuery(id+"F22.wireOp",EDGE,"E28.7.2");var subQ56=sQuery(id+"F3.wireOp",EDGE,"E20.15.3");var subQ57=sQuery(id+"F3.wireOp",EDGE,"E20.15.1");var subQ58=sQuery(id+"F3.wireOp",EDGE,"E20.15.0");var subQ60=sQuery(id+"F22.wireOp",EDGE,"E28.6.3");var subQ61=sQuery(id+"F22.wireOp",EDGE,"E28.6.2");var subQ62=sQuery(id+"F3.wireOp",EDGE,"E20.14.3");var subQ64=sQuery(id+"F3.wireOp",EDGE,"E20.14.1");var subQ65=sQuery(id+"F3.wireOp",EDGE,"E20.14.0");var subQ66=sQuery(id+"F22.wireOp",EDGE,"E28.5.3");var subQ67=sQuery(id+"F22.wireOp",EDGE,"E28.5.2");var subQ68=sQuery(id+"F3.wireOp",EDGE,"E20.13.3");var subQ70=sQuery(id+"F3.wireOp",EDGE,"E20.13.1");var subQ72=sQuery(id+"F3.wireOp",EDGE,"E20.13.0");var subQ73=makeQuery(id+"F28.opLoft","SWEPT_FACE",FACE,{"disambiguationData":[OSD([subQ72,subQ70,subQ68,sQuery(id+"F22.wireOp",EDGE,"E28.5.1"),subQ67,subQ66])]});var subQ74=sQuery(id+"F22.wireOp",EDGE,"E28.4.3");var subQ75=sQuery(id+"F22.wireOp",EDGE,"E28.4.2");var subQ76=sQuery(id+"F3.wireOp",EDGE,"E20.12.3");var subQ78=sQuery(id+"F3.wireOp",EDGE,"E20.12.1");var subQ79=sQuery(id+"F3.wireOp",EDGE,"E20.12.0");var subQ80=makeQuery(id+"F27.opLoft","SWEPT_FACE",FACE,{"disambiguationData":[OSD([subQ79,subQ78,subQ76,sQuery(id+"F22.wireOp",EDGE,"E28.4.1"),subQ75,subQ74])]});var subQ81=sQuery(id+"F22.wireOp",EDGE,"E28.3.3");var subQ82=sQuery(id+"F22.wireOp",EDGE,"E28.3.2");var subQ83=sQuery(id+"F3.wireOp",EDGE,"E20.11.3");var subQ85=sQuery(id+"F3.wireOp",EDGE,"E20.11.1");var subQ86=sQuery(id+"F3.wireOp",EDGE,"E20.11.0");var subQ87=makeQuery(id+"F26.opLoft","SWEPT_FACE",FACE,{"disambiguationData":[OSD([subQ86,subQ85,subQ83,sQuery(id+"F22.wireOp",EDGE,"E28.3.1"),subQ82,subQ81])]});var subQ88=sQuery(id+"F22.wireOp",EDGE,"E28.2.3");var subQ89=sQuery(id+"F22.wireOp",EDGE,"E28.2.2");var subQ90=sQuery(id+"F3.wireOp",EDGE,"E20.10.3");var subQ91=sQuery(id+"F3.wireOp",EDGE,"E20.10.1");var subQ92=sQuery(id+"F3.wireOp",EDGE,"E20.10.0");var subQ93=makeQuery(id+"F25.opLoft","SWEPT_FACE",FACE,{"disambiguationData":[OSD([subQ92,subQ91,subQ90,sQuery(id+"F22.wireOp",EDGE,"E28.2.1"),subQ89,subQ88])]});var subQ95=sQuery(id+"F22.wireOp",EDGE,"E28.1.3");var subQ96=sQuery(id+"F22.wireOp",EDGE,"E28.1.2");var subQ97=sQuery(id+"F3.wireOp",EDGE,"E20.9.3");var subQ98=sQuery(id+"F3.wireOp",EDGE,"E20.9.1");var subQ99=sQuery(id+"F3.wireOp",EDGE,"E20.9.0");var subQ100=makeQuery(id+"F24.opLoft","SWEPT_FACE",FACE,{"disambiguationData":[OSD([subQ99,subQ98,subQ97,sQuery(id+"F22.wireOp",EDGE,"E28.1.1"),subQ96,subQ95])]});var subQ101=sQuery(id+"F22.wireOp",EDGE,"E27.top");var subQ102=sQuery(id+"F22.wireOp",EDGE,"E27.bottom");var subQ103=sQuery(id+"F3.wireOp",EDGE,"E20.8.3");var subQ105=sQuery(id+"F3.wireOp",EDGE,"E20.8.1");var subQ109=makeQuery(id+"F42.boolean.opBoolean","COPY",FACE,{"disambiguationData":[TD([subQ73])],"derivedFrom":subQ10});var subQ135=makeQuery(id+"F5.opLoft","CAP_FACE",FACE,{"disambiguationData":[OSD([makeQuery(id+"F3.imprint","IMPRINT",FACE,{"disambiguationData":[TD([[makeQuery(id+"F3.imprint","IMPRINT",EDGE,{"derivedFrom":subQ52}),1.0]])]})])],"isStart":true});var subQ181=makeQuery(id+"F28.boolean.opBoolean","INTERSECT",EDGE,{"derivedFrom":[makeQuery(id+"F27.boolean.opBoolean","SPLIT",FACE,{"disambiguationData":[TD([subQ135])],"derivedFrom":makeQuery(id+"F26.boolean.opBoolean","SPLIT",FACE,{"disambiguationData":[TD([subQ135])],"derivedFrom":makeQuery(id+"F25.boolean.opBoolean","SPLIT",FACE,{"disambiguationData":[TD([subQ135])],"derivedFrom":makeQuery(id+"F24.boolean.opBoolean","SPLIT",FACE,{"disambiguationData":[TD([subQ135])],"derivedFrom":makeQuery(id+"F1.opRevolve","SWEPT_FACE",FACE,{"disambiguationData":[OSD([sQuery(id+"F0.wireOp",EDGE,"E13")])]})})})})}),subQ73]});Q26=makeQuery(id+"F48.opFillet","BLEND_EDGE",EDGE,{"blendedFrom":[makeQuery(id+"F47.opFillet","TWEAK_EDGE",EDGE,{"derivedFrom":[makeQuery(id+"F45.opFillet","BLEND_VERTEX",VERTEX,{"blendedFrom":[subQ181,subQ73,subQ109],"blendedInto":[subQ73,subQ109]}),makeQuery(id+"F45.opFillet","BLEND_VERTEX",VERTEX,{"blendedFrom":[subQ181,makeQuery(id+"F42.boolean.opBoolean","MERGE",FACE,{"derivedFrom":[subQ2,subQ1]}),subQ109],"blendedInto":[makeQuery(id+"F42.boolean.opBoolean","MERGE",FACE,{"derivedFrom":[subQ2,subQ1]}),subQ109]})]}),makeQuery(id+"F47.opFillet","BLEND_FACE",FACE,{"disambiguationData":[OSD([subQ0,subQ9]),TDD([makeQuery(id+"F42.boolean.opBoolean","COPY",EDGE,{"disambiguationData":[TD([makeQuery(id+"F23.opLoft","SWEPT_FACE",FACE,{"disambiguationData":[OSD([sQuery(id+"F3.wireOp",EDGE,"E20.8.0"),subQ105,subQ103,subQ102,subQ101,sQuery(id+"F22.wireOp",EDGE,"E27.right")])]})])],"derivedFrom":subQ11})])]}),makeQuery(id+"F47.opFillet","BLEND_FACE",FACE,{"disambiguationData":[OSD([subQ0,subQ9]),TDD([makeQuery(id+"F42.boolean.opBoolean","COPY",EDGE,{"disambiguationData":[TD([subQ100])],"derivedFrom":subQ11})])]}),makeQuery(id+"F47.opFillet","BLEND_FACE",FACE,{"disambiguationData":[OSD([subQ0,subQ9]),TDD([makeQuery(id+"F42.boolean.opBoolean","COPY",EDGE,{"disambiguationData":[TD([subQ93])],"derivedFrom":subQ11})])]}),makeQuery(id+"F47.opFillet","BLEND_FACE",FACE,{"disambiguationData":[OSD([subQ0,subQ9]),TDD([makeQuery(id+"F42.boolean.opBoolean","COPY",EDGE,{"disambiguationData":[TD([subQ87])],"derivedFrom":subQ11})])]}),makeQuery(id+"F47.opFillet","BLEND_FACE",FACE,{"disambiguationData":[OSD([subQ0,subQ9]),TDD([makeQuery(id+"F42.boolean.opBoolean","COPY",EDGE,{"disambiguationData":[TD([subQ80])],"derivedFrom":subQ11})])]}),makeQuery(id+"F47.opFillet","BLEND_FACE",FACE,{"disambiguationData":[OSD([subQ0,subQ9]),TDD([makeQuery(id+"F42.boolean.opBoolean","COPY",EDGE,{"disambiguationData":[TD([subQ73])],"derivedFrom":subQ11})])]}),makeQuery(id+"F47.opFillet","BLEND_FACE",FACE,{"disambiguationData":[OSD([subQ0,subQ9]),TDD([makeQuery(id+"F42.boolean.opBoolean","COPY",EDGE,{"disambiguationData":[TD([makeQuery(id+"F29.opLoft","SWEPT_FACE",FACE,{"disambiguationData":[OSD([subQ65,subQ64,subQ62,sQuery(id+"F22.wireOp",EDGE,"E28.6.1"),subQ61,subQ60])]})])],"derivedFrom":subQ11})])]}),makeQuery(id+"F47.opFillet","BLEND_FACE",FACE,{"disambiguationData":[OSD([subQ0,subQ9]),TDD([makeQuery(id+"F42.boolean.opBoolean","COPY",EDGE,{"disambiguationData":[TD([makeQuery(id+"F30.opLoft","SWEPT_FACE",FACE,{"disambiguationData":[OSD([subQ58,subQ57,subQ56,sQuery(id+"F22.wireOp",EDGE,"E28.7.1"),subQ55,subQ54])]})])],"derivedFrom":subQ11})])]}),makeQuery(id+"F47.opFillet","BLEND_FACE",FACE,{"disambiguationData":[OSD([subQ0,subQ9]),TDD([makeQuery(id+"F42.boolean.opBoolean","COPY",EDGE,{"disambiguationData":[TD([makeQuery(id+"F31.opLoft","SWEPT_FACE",FACE,{"disambiguationData":[OSD([subQ52,subQ51,subQ53,sQuery(id+"F22.wireOp",EDGE,"E28.8.1"),subQ49,subQ48])]})])],"derivedFrom":subQ11})])]}),makeQuery(id+"F47.opFillet","BLEND_FACE",FACE,{"disambiguationData":[OSD([subQ0,subQ9]),TDD([makeQuery(id+"F42.boolean.opBoolean","COPY",EDGE,{"disambiguationData":[TD([makeQuery(id+"F32.opLoft","SWEPT_FACE",FACE,{"disambiguationData":[OSD([subQ47,subQ46,subQ44,sQuery(id+"F22.wireOp",EDGE,"E28.9.1"),subQ43,subQ42])]})])],"derivedFrom":subQ11})])]}),makeQuery(id+"F47.opFillet","BLEND_FACE",FACE,{"disambiguationData":[OSD([subQ0,subQ9]),TDD([makeQuery(id+"F42.boolean.opBoolean","COPY",EDGE,{"disambiguationData":[TD([makeQuery(id+"F33.opLoft","SWEPT_FACE",FACE,{"disambiguationData":[OSD([subQ41,subQ40,subQ38,sQuery(id+"F22.wireOp",EDGE,"E28.10.1"),subQ37,subQ36])]})])],"derivedFrom":subQ11})])]}),makeQuery(id+"F47.opFillet","BLEND_FACE",FACE,{"disambiguationData":[OSD([subQ0,subQ9]),TDD([makeQuery(id+"F42.boolean.opBoolean","COPY",EDGE,{"disambiguationData":[TD([makeQuery(id+"F34.opLoft","SWEPT_FACE",FACE,{"disambiguationData":[OSD([subQ35,subQ34,subQ32,sQuery(id+"F22.wireOp",EDGE,"E28.11.1"),subQ31,subQ30])]})])],"derivedFrom":subQ11})])]}),makeQuery(id+"F47.opFillet","BLEND_FACE",FACE,{"disambiguationData":[OSD([subQ0,subQ9]),TDD([makeQuery(id+"F42.boolean.opBoolean","COPY",EDGE,{"disambiguationData":[TD([makeQuery(id+"F35.opLoft","SWEPT_FACE",FACE,{"disambiguationData":[OSD([subQ29,subQ28,subQ26,sQuery(id+"F22.wireOp",EDGE,"E28.12.1"),subQ25,subQ24])]})])],"derivedFrom":subQ11})])]}),makeQuery(id+"F47.opFillet","BLEND_FACE",FACE,{"disambiguationData":[OSD([subQ0,subQ9]),TDD([makeQuery(id+"F42.boolean.opBoolean","COPY",EDGE,{"disambiguationData":[TD([makeQuery(id+"F36.opLoft","SWEPT_FACE",FACE,{"disambiguationData":[OSD([subQ23,subQ22,subQ20,sQuery(id+"F22.wireOp",EDGE,"E28.13.1"),subQ19,subQ18])]})])],"derivedFrom":subQ11})])]}),makeQuery(id+"F47.opFillet","BLEND_FACE",FACE,{"disambiguationData":[OSD([subQ0,subQ9]),TDD([makeQuery(id+"F42.boolean.opBoolean","COPY",EDGE,{"disambiguationData":[TD([makeQuery(id+"F37.opLoft","SWEPT_FACE",FACE,{"disambiguationData":[OSD([subQ16,subQ15,subQ14,sQuery(id+"F22.wireOp",EDGE,"E28.14.1"),subQ13,subQ12])]})])],"derivedFrom":subQ11})])]}),makeQuery(id+"F47.opFillet","BLEND_FACE",FACE,{"disambiguationData":[OSD([subQ0,subQ9]),TDD([makeQuery(id+"F42.boolean.opBoolean","COPY",EDGE,{"disambiguationData":[TD([makeQuery(id+"F38.opLoft","SWEPT_FACE",FACE,{"disambiguationData":[OSD([subQ8,subQ7,subQ5,sQuery(id+"F22.wireOp",EDGE,"E28.15.1"),subQ4,subQ3])]})])],"derivedFrom":subQ11})])]})],"blendedInto":[makeQuery(id+"F47.opFillet","BLEND_FACE",FACE,{"disambiguationData":[OSD([subQ0,subQ9]),TDD([makeQuery(id+"F42.boolean.opBoolean","COPY",EDGE,{"disambiguationData":[TD([makeQuery(id+"F23.opLoft","SWEPT_FACE",FACE,{"disambiguationData":[OSD([sQuery(id+"F3.wireOp",EDGE,"E20.8.0"),subQ105,subQ103,subQ102,subQ101,sQuery(id+"F22.wireOp",EDGE,"E27.right")])]})])],"derivedFrom":subQ11})])]}),makeQuery(id+"F47.opFillet","BLEND_FACE",FACE,{"disambiguationData":[OSD([subQ0,subQ9]),TDD([makeQuery(id+"F42.boolean.opBoolean","COPY",EDGE,{"disambiguationData":[TD([subQ100])],"derivedFrom":subQ11})])]}),makeQuery(id+"F47.opFillet","BLEND_FACE",FACE,{"disambiguationData":[OSD([subQ0,subQ9]),TDD([makeQuery(id+"F42.boolean.opBoolean","COPY",EDGE,{"disambiguationData":[TD([subQ93])],"derivedFrom":subQ11})])]}),makeQuery(id+"F47.opFillet","BLEND_FACE",FACE,{"disambiguationData":[OSD([subQ0,subQ9]),TDD([makeQuery(id+"F42.boolean.opBoolean","COPY",EDGE,{"disambiguationData":[TD([subQ87])],"derivedFrom":subQ11})])]}),makeQuery(id+"F47.opFillet","BLEND_FACE",FACE,{"disambiguationData":[OSD([subQ0,subQ9]),TDD([makeQuery(id+"F42.boolean.opBoolean","COPY",EDGE,{"disambiguationData":[TD([subQ80])],"derivedFrom":subQ11})])]}),makeQuery(id+"F47.opFillet","BLEND_FACE",FACE,{"disambiguationData":[OSD([subQ0,subQ9]),TDD([makeQuery(id+"F42.boolean.opBoolean","COPY",EDGE,{"disambiguationData":[TD([subQ73])],"derivedFrom":subQ11})])]}),makeQuery(id+"F47.opFillet","BLEND_FACE",FACE,{"disambiguationData":[OSD([subQ0,subQ9]),TDD([makeQuery(id+"F42.boolean.opBoolean","COPY",EDGE,{"disambiguationData":[TD([makeQuery(id+"F29.opLoft","SWEPT_FACE",FACE,{"disambiguationData":[OSD([subQ65,subQ64,subQ62,sQuery(id+"F22.wireOp",EDGE,"E28.6.1"),subQ61,subQ60])]})])],"derivedFrom":subQ11})])]}),makeQuery(id+"F47.opFillet","BLEND_FACE",FACE,{"disambiguationData":[OSD([subQ0,subQ9]),TDD([makeQuery(id+"F42.boolean.opBoolean","COPY",EDGE,{"disambiguationData":[TD([makeQuery(id+"F30.opLoft","SWEPT_FACE",FACE,{"disambiguationData":[OSD([subQ58,subQ57,subQ56,sQuery(id+"F22.wireOp",EDGE,"E28.7.1"),subQ55,subQ54])]})])],"derivedFrom":subQ11})])]}),makeQuery(id+"F47.opFillet","BLEND_FACE",FACE,{"disambiguationData":[OSD([subQ0,subQ9]),TDD([makeQuery(id+"F42.boolean.opBoolean","COPY",EDGE,{"disambiguationData":[TD([makeQuery(id+"F31.opLoft","SWEPT_FACE",FACE,{"disambiguationData":[OSD([subQ52,subQ51,subQ53,sQuery(id+"F22.wireOp",EDGE,"E28.8.1"),subQ49,subQ48])]})])],"derivedFrom":subQ11})])]}),makeQuery(id+"F47.opFillet","BLEND_FACE",FACE,{"disambiguationData":[OSD([subQ0,subQ9]),TDD([makeQuery(id+"F42.boolean.opBoolean","COPY",EDGE,{"disambiguationData":[TD([makeQuery(id+"F32.opLoft","SWEPT_FACE",FACE,{"disambiguationData":[OSD([subQ47,subQ46,subQ44,sQuery(id+"F22.wireOp",EDGE,"E28.9.1"),subQ43,subQ42])]})])],"derivedFrom":subQ11})])]}),makeQuery(id+"F47.opFillet","BLEND_FACE",FACE,{"disambiguationData":[OSD([subQ0,subQ9]),TDD([makeQuery(id+"F42.boolean.opBoolean","COPY",EDGE,{"disambiguationData":[TD([makeQuery(id+"F33.opLoft","SWEPT_FACE",FACE,{"disambiguationData":[OSD([subQ41,subQ40,subQ38,sQuery(id+"F22.wireOp",EDGE,"E28.10.1"),subQ37,subQ36])]})])],"derivedFrom":subQ11})])]}),makeQuery(id+"F47.opFillet","BLEND_FACE",FACE,{"disambiguationData":[OSD([subQ0,subQ9]),TDD([makeQuery(id+"F42.boolean.opBoolean","COPY",EDGE,{"disambiguationData":[TD([makeQuery(id+"F34.opLoft","SWEPT_FACE",FACE,{"disambiguationData":[OSD([subQ35,subQ34,subQ32,sQuery(id+"F22.wireOp",EDGE,"E28.11.1"),subQ31,subQ30])]})])],"derivedFrom":subQ11})])]}),makeQuery(id+"F47.opFillet","BLEND_FACE",FACE,{"disambiguationData":[OSD([subQ0,subQ9]),TDD([makeQuery(id+"F42.boolean.opBoolean","COPY",EDGE,{"disambiguationData":[TD([makeQuery(id+"F35.opLoft","SWEPT_FACE",FACE,{"disambiguationData":[OSD([subQ29,subQ28,subQ26,sQuery(id+"F22.wireOp",EDGE,"E28.12.1"),subQ25,subQ24])]})])],"derivedFrom":subQ11})])]}),makeQuery(id+"F47.opFillet","BLEND_FACE",FACE,{"disambiguationData":[OSD([subQ0,subQ9]),TDD([makeQuery(id+"F42.boolean.opBoolean","COPY",EDGE,{"disambiguationData":[TD([makeQuery(id+"F36.opLoft","SWEPT_FACE",FACE,{"disambiguationData":[OSD([subQ23,subQ22,subQ20,sQuery(id+"F22.wireOp",EDGE,"E28.13.1"),subQ19,subQ18])]})])],"derivedFrom":subQ11})])]}),makeQuery(id+"F47.opFillet","BLEND_FACE",FACE,{"disambiguationData":[OSD([subQ0,subQ9]),TDD([makeQuery(id+"F42.boolean.opBoolean","COPY",EDGE,{"disambiguationData":[TD([makeQuery(id+"F37.opLoft","SWEPT_FACE",FACE,{"disambiguationData":[OSD([subQ16,subQ15,subQ14,sQuery(id+"F22.wireOp",EDGE,"E28.14.1"),subQ13,subQ12])]})])],"derivedFrom":subQ11})])]}),makeQuery(id+"F47.opFillet","BLEND_FACE",FACE,{"disambiguationData":[OSD([subQ0,subQ9]),TDD([makeQuery(id+"F42.boolean.opBoolean","COPY",EDGE,{"disambiguationData":[TD([makeQuery(id+"F38.opLoft","SWEPT_FACE",FACE,{"disambiguationData":[OSD([subQ8,subQ7,subQ5,sQuery(id+"F22.wireOp",EDGE,"E28.15.1"),subQ4,subQ3])]})])],"derivedFrom":subQ11})])]})]});}
            var Q27;
            {var subQ0=sQuery(id+"F22.wireOp",EDGE,"E28.5.3");var subQ1=sQuery(id+"F22.wireOp",EDGE,"E28.5.2");var subQ2=sQuery(id+"F22.wireOp",EDGE,"E28.5.0");var subQ3=sQuery(id+"F3.wireOp",EDGE,"E20.13.3");var subQ4=sQuery(id+"F3.wireOp",EDGE,"E20.13.1");var subQ5=makeQuery(id+"F28.opLoft","SWEPT_FACE",FACE,{"disambiguationData":[OSD([subQ4,sQuery(id+"F3.wireOp",EDGE,"E20.13.2"),subQ3,subQ2,subQ1,subQ0])]});var subQ6=sQuery(id+"F22.wireOp",EDGE,"E28.5.1");var subQ7=sQuery(id+"F41.wireOp",EDGE,"E34");var subQ8=sQuery(id+"F41.wireOp",EDGE,"E32");Q27=makeQuery(id+"F44.opFillet","BLEND_EDGE",EDGE,{"blendedFrom":[makeQuery(id+"F40.boolean.opBoolean","INTERSECT",EDGE,{"derivedFrom":[subQ5,makeQuery(id+"F40.opExtrude","CAP_FACE",FACE,{"disambiguationData":[OSD([sQuery(id+"F39.wireOp",EDGE,"E29"),sQuery(id+"F39.wireOp",EDGE,"E30")])],"isStart":true})]}),makeQuery(id+"F42.boolean.opBoolean","COPY",FACE,{"disambiguationData":[TD([makeQuery(id+"F28.opLoft","SWEPT_FACE",FACE,{"disambiguationData":[OSD([sQuery(id+"F3.wireOp",EDGE,"E20.13.0"),subQ4,subQ3,subQ6,subQ1,subQ0])]})])],"derivedFrom":makeQuery(id+"F42.opRevolve","SWEPT_FACE",FACE,{"disambiguationData":[OSD([subQ8]),TDD([makeQuery(id+"F41.imprint","IMPRINT",EDGE,{"disambiguationData":[TD([[makeQuery(id+"F41.imprint","INTERSECT",VERTEX,{"disambiguationData":[OD(0.0)],"derivedFrom":[subQ8,subQ7]}),-1.0]])],"derivedFrom":subQ8})])]})})],"blendedInto":[makeQuery(id+"F42.boolean.opBoolean","COPY",FACE,{"disambiguationData":[TD([makeQuery(id+"F28.opLoft","SWEPT_FACE",FACE,{"disambiguationData":[OSD([sQuery(id+"F3.wireOp",EDGE,"E20.13.0"),subQ4,subQ3,subQ6,subQ1,subQ0])]})])],"derivedFrom":makeQuery(id+"F42.opRevolve","SWEPT_FACE",FACE,{"disambiguationData":[OSD([subQ8]),TDD([makeQuery(id+"F41.imprint","IMPRINT",EDGE,{"disambiguationData":[TD([[makeQuery(id+"F41.imprint","INTERSECT",VERTEX,{"disambiguationData":[OD(0.0)],"derivedFrom":[subQ8,subQ7]}),-1.0]])],"derivedFrom":subQ8})])]})})]});}
            var Q28;
            {var subQ0=sQuery(id+"F41.wireOp",EDGE,"E34");var subQ1=sQuery(id+"F41.wireOp",EDGE,"E32");Q28=makeQuery(id+"F42.boolean.opBoolean","INTERSECT",EDGE,{"derivedFrom":[makeQuery(id+"F27.opLoft","SWEPT_FACE",FACE,{"disambiguationData":[OSD([sQuery(id+"F3.wireOp",EDGE,"E20.12.0"),sQuery(id+"F3.wireOp",EDGE,"E20.12.1"),sQuery(id+"F3.wireOp",EDGE,"E20.12.3"),sQuery(id+"F22.wireOp",EDGE,"E28.4.1"),sQuery(id+"F22.wireOp",EDGE,"E28.4.2"),sQuery(id+"F22.wireOp",EDGE,"E28.4.3")])]}),makeQuery(id+"F42.opRevolve","SWEPT_FACE",FACE,{"disambiguationData":[OSD([subQ1]),TDD([makeQuery(id+"F41.imprint","IMPRINT",EDGE,{"disambiguationData":[TD([[makeQuery(id+"F41.imprint","INTERSECT",VERTEX,{"disambiguationData":[OD(0.0)],"derivedFrom":[subQ1,subQ0]}),-1.0]])],"derivedFrom":subQ1})])]})]});}
            var Q29;
            {var subQ0=sQuery(id+"F41.wireOp",EDGE,"E37");var subQ1=makeQuery(id+"F42.opRevolve","SWEPT_FACE",FACE,{"disambiguationData":[OSD([subQ0])]});var subQ2=makeQuery(id+"F40.opExtrude","CAP_FACE",FACE,{"disambiguationData":[OSD([sQuery(id+"F39.wireOp",EDGE,"E29"),sQuery(id+"F39.wireOp",EDGE,"E30")])],"isStart":true});var subQ3=sQuery(id+"F22.wireOp",EDGE,"E28.15.3");var subQ4=sQuery(id+"F22.wireOp",EDGE,"E28.15.2");var subQ5=sQuery(id+"F3.wireOp",EDGE,"E20.7.3");var subQ7=sQuery(id+"F3.wireOp",EDGE,"E20.7.1");var subQ8=sQuery(id+"F3.wireOp",EDGE,"E20.7.0");var subQ9=sQuery(id+"F41.wireOp",EDGE,"E38");var subQ10=makeQuery(id+"F42.opRevolve","SWEPT_FACE",FACE,{"disambiguationData":[OSD([subQ9])]});var subQ11=makeQuery(id+"F42.opRevolve","SWEPT_EDGE",EDGE,{"disambiguationData":[OSD([subQ0,subQ9])]});var subQ12=sQuery(id+"F22.wireOp",EDGE,"E28.14.3");var subQ13=sQuery(id+"F22.wireOp",EDGE,"E28.14.2");var subQ14=sQuery(id+"F3.wireOp",EDGE,"E20.6.3");var subQ15=sQuery(id+"F3.wireOp",EDGE,"E20.6.1");var subQ16=sQuery(id+"F3.wireOp",EDGE,"E20.6.0");var subQ18=sQuery(id+"F22.wireOp",EDGE,"E28.13.3");var subQ19=sQuery(id+"F22.wireOp",EDGE,"E28.13.2");var subQ20=sQuery(id+"F3.wireOp",EDGE,"E20.5.3");var subQ22=sQuery(id+"F3.wireOp",EDGE,"E20.5.1");var subQ23=sQuery(id+"F3.wireOp",EDGE,"E20.5.0");var subQ24=sQuery(id+"F22.wireOp",EDGE,"E28.12.3");var subQ25=sQuery(id+"F22.wireOp",EDGE,"E28.12.2");var subQ26=sQuery(id+"F3.wireOp",EDGE,"E20.4.3");var subQ28=sQuery(id+"F3.wireOp",EDGE,"E20.4.1");var subQ29=sQuery(id+"F3.wireOp",EDGE,"E20.4.0");var subQ30=sQuery(id+"F22.wireOp",EDGE,"E28.11.3");var subQ31=sQuery(id+"F22.wireOp",EDGE,"E28.11.2");var subQ32=sQuery(id+"F3.wireOp",EDGE,"E20.3.3");var subQ34=sQuery(id+"F3.wireOp",EDGE,"E20.3.1");var subQ35=sQuery(id+"F3.wireOp",EDGE,"E20.3.0");var subQ36=sQuery(id+"F22.wireOp",EDGE,"E28.10.3");var subQ37=sQuery(id+"F22.wireOp",EDGE,"E28.10.2");var subQ38=sQuery(id+"F3.wireOp",EDGE,"E20.2.3");var subQ40=sQuery(id+"F3.wireOp",EDGE,"E20.2.1");var subQ41=sQuery(id+"F3.wireOp",EDGE,"E20.2.0");var subQ42=sQuery(id+"F22.wireOp",EDGE,"E28.9.3");var subQ43=sQuery(id+"F22.wireOp",EDGE,"E28.9.2");var subQ44=sQuery(id+"F3.wireOp",EDGE,"E20.1.3");var subQ46=sQuery(id+"F3.wireOp",EDGE,"E20.1.1");var subQ47=sQuery(id+"F3.wireOp",EDGE,"E20.1.0");var subQ48=sQuery(id+"F22.wireOp",EDGE,"E28.8.3");var subQ49=sQuery(id+"F22.wireOp",EDGE,"E28.8.2");var subQ51=sQuery(id+"F3.wireOp",EDGE,"E18.top");var subQ52=sQuery(id+"F3.wireOp",EDGE,"E18.bottom");var subQ53=sQuery(id+"F3.wireOp",EDGE,"E18.left");var subQ54=sQuery(id+"F22.wireOp",EDGE,"E28.7.3");var subQ55=sQuery(id+"F22.wireOp",EDGE,"E28.7.2");var subQ56=sQuery(id+"F3.wireOp",EDGE,"E20.15.3");var subQ57=sQuery(id+"F3.wireOp",EDGE,"E20.15.1");var subQ58=sQuery(id+"F3.wireOp",EDGE,"E20.15.0");var subQ60=sQuery(id+"F22.wireOp",EDGE,"E28.6.3");var subQ61=sQuery(id+"F22.wireOp",EDGE,"E28.6.2");var subQ62=sQuery(id+"F3.wireOp",EDGE,"E20.14.3");var subQ64=sQuery(id+"F3.wireOp",EDGE,"E20.14.1");var subQ65=sQuery(id+"F3.wireOp",EDGE,"E20.14.0");var subQ66=sQuery(id+"F22.wireOp",EDGE,"E28.5.3");var subQ67=sQuery(id+"F22.wireOp",EDGE,"E28.5.2");var subQ68=sQuery(id+"F3.wireOp",EDGE,"E20.13.3");var subQ70=sQuery(id+"F3.wireOp",EDGE,"E20.13.1");var subQ71=sQuery(id+"F3.wireOp",EDGE,"E20.13.0");var subQ72=sQuery(id+"F22.wireOp",EDGE,"E28.4.3");var subQ73=sQuery(id+"F22.wireOp",EDGE,"E28.4.2");var subQ74=sQuery(id+"F3.wireOp",EDGE,"E20.12.3");var subQ76=sQuery(id+"F3.wireOp",EDGE,"E20.12.1");var subQ78=sQuery(id+"F3.wireOp",EDGE,"E20.12.0");var subQ79=makeQuery(id+"F27.opLoft","SWEPT_FACE",FACE,{"disambiguationData":[OSD([subQ78,subQ76,subQ74,sQuery(id+"F22.wireOp",EDGE,"E28.4.1"),subQ73,subQ72])]});var subQ80=sQuery(id+"F22.wireOp",EDGE,"E28.3.3");var subQ81=sQuery(id+"F22.wireOp",EDGE,"E28.3.2");var subQ82=sQuery(id+"F3.wireOp",EDGE,"E20.11.3");var subQ84=sQuery(id+"F3.wireOp",EDGE,"E20.11.1");var subQ85=sQuery(id+"F3.wireOp",EDGE,"E20.11.0");var subQ86=makeQuery(id+"F26.opLoft","SWEPT_FACE",FACE,{"disambiguationData":[OSD([subQ85,subQ84,subQ82,sQuery(id+"F22.wireOp",EDGE,"E28.3.1"),subQ81,subQ80])]});var subQ87=sQuery(id+"F22.wireOp",EDGE,"E28.2.3");var subQ88=sQuery(id+"F22.wireOp",EDGE,"E28.2.2");var subQ89=sQuery(id+"F3.wireOp",EDGE,"E20.10.3");var subQ90=sQuery(id+"F3.wireOp",EDGE,"E20.10.1");var subQ91=sQuery(id+"F3.wireOp",EDGE,"E20.10.0");var subQ92=makeQuery(id+"F25.opLoft","SWEPT_FACE",FACE,{"disambiguationData":[OSD([subQ91,subQ90,subQ89,sQuery(id+"F22.wireOp",EDGE,"E28.2.1"),subQ88,subQ87])]});var subQ94=sQuery(id+"F22.wireOp",EDGE,"E28.1.3");var subQ95=sQuery(id+"F22.wireOp",EDGE,"E28.1.2");var subQ96=sQuery(id+"F3.wireOp",EDGE,"E20.9.3");var subQ97=sQuery(id+"F3.wireOp",EDGE,"E20.9.1");var subQ98=sQuery(id+"F3.wireOp",EDGE,"E20.9.0");var subQ99=makeQuery(id+"F24.opLoft","SWEPT_FACE",FACE,{"disambiguationData":[OSD([subQ98,subQ97,subQ96,sQuery(id+"F22.wireOp",EDGE,"E28.1.1"),subQ95,subQ94])]});var subQ100=sQuery(id+"F22.wireOp",EDGE,"E27.top");var subQ101=sQuery(id+"F22.wireOp",EDGE,"E27.bottom");var subQ102=sQuery(id+"F3.wireOp",EDGE,"E20.8.3");var subQ104=sQuery(id+"F3.wireOp",EDGE,"E20.8.1");var subQ108=makeQuery(id+"F42.boolean.opBoolean","COPY",FACE,{"disambiguationData":[TD([subQ79])],"derivedFrom":subQ10});var subQ142=makeQuery(id+"F5.opLoft","CAP_FACE",FACE,{"disambiguationData":[OSD([makeQuery(id+"F3.imprint","IMPRINT",FACE,{"disambiguationData":[TD([[makeQuery(id+"F3.imprint","IMPRINT",EDGE,{"derivedFrom":subQ52}),1.0]])]})])],"isStart":true});var subQ180=makeQuery(id+"F27.boolean.opBoolean","INTERSECT",EDGE,{"derivedFrom":[makeQuery(id+"F26.boolean.opBoolean","SPLIT",FACE,{"disambiguationData":[TD([subQ142])],"derivedFrom":makeQuery(id+"F25.boolean.opBoolean","SPLIT",FACE,{"disambiguationData":[TD([subQ142])],"derivedFrom":makeQuery(id+"F24.boolean.opBoolean","SPLIT",FACE,{"disambiguationData":[TD([subQ142])],"derivedFrom":makeQuery(id+"F1.opRevolve","SWEPT_FACE",FACE,{"disambiguationData":[OSD([sQuery(id+"F0.wireOp",EDGE,"E13")])]})})})}),subQ79]});Q29=makeQuery(id+"F48.opFillet","BLEND_EDGE",EDGE,{"blendedFrom":[makeQuery(id+"F47.opFillet","TWEAK_EDGE",EDGE,{"derivedFrom":[makeQuery(id+"F45.opFillet","BLEND_VERTEX",VERTEX,{"blendedFrom":[subQ180,subQ79,subQ108],"blendedInto":[subQ79,subQ108]}),makeQuery(id+"F45.opFillet","BLEND_VERTEX",VERTEX,{"blendedFrom":[subQ180,makeQuery(id+"F42.boolean.opBoolean","MERGE",FACE,{"derivedFrom":[subQ2,subQ1]}),subQ108],"blendedInto":[makeQuery(id+"F42.boolean.opBoolean","MERGE",FACE,{"derivedFrom":[subQ2,subQ1]}),subQ108]})]}),makeQuery(id+"F47.opFillet","BLEND_FACE",FACE,{"disambiguationData":[OSD([subQ0,subQ9]),TDD([makeQuery(id+"F42.boolean.opBoolean","COPY",EDGE,{"disambiguationData":[TD([makeQuery(id+"F23.opLoft","SWEPT_FACE",FACE,{"disambiguationData":[OSD([sQuery(id+"F3.wireOp",EDGE,"E20.8.0"),subQ104,subQ102,subQ101,subQ100,sQuery(id+"F22.wireOp",EDGE,"E27.right")])]})])],"derivedFrom":subQ11})])]}),makeQuery(id+"F47.opFillet","BLEND_FACE",FACE,{"disambiguationData":[OSD([subQ0,subQ9]),TDD([makeQuery(id+"F42.boolean.opBoolean","COPY",EDGE,{"disambiguationData":[TD([subQ99])],"derivedFrom":subQ11})])]}),makeQuery(id+"F47.opFillet","BLEND_FACE",FACE,{"disambiguationData":[OSD([subQ0,subQ9]),TDD([makeQuery(id+"F42.boolean.opBoolean","COPY",EDGE,{"disambiguationData":[TD([subQ92])],"derivedFrom":subQ11})])]}),makeQuery(id+"F47.opFillet","BLEND_FACE",FACE,{"disambiguationData":[OSD([subQ0,subQ9]),TDD([makeQuery(id+"F42.boolean.opBoolean","COPY",EDGE,{"disambiguationData":[TD([subQ86])],"derivedFrom":subQ11})])]}),makeQuery(id+"F47.opFillet","BLEND_FACE",FACE,{"disambiguationData":[OSD([subQ0,subQ9]),TDD([makeQuery(id+"F42.boolean.opBoolean","COPY",EDGE,{"disambiguationData":[TD([subQ79])],"derivedFrom":subQ11})])]}),makeQuery(id+"F47.opFillet","BLEND_FACE",FACE,{"disambiguationData":[OSD([subQ0,subQ9]),TDD([makeQuery(id+"F42.boolean.opBoolean","COPY",EDGE,{"disambiguationData":[TD([makeQuery(id+"F28.opLoft","SWEPT_FACE",FACE,{"disambiguationData":[OSD([subQ71,subQ70,subQ68,sQuery(id+"F22.wireOp",EDGE,"E28.5.1"),subQ67,subQ66])]})])],"derivedFrom":subQ11})])]}),makeQuery(id+"F47.opFillet","BLEND_FACE",FACE,{"disambiguationData":[OSD([subQ0,subQ9]),TDD([makeQuery(id+"F42.boolean.opBoolean","COPY",EDGE,{"disambiguationData":[TD([makeQuery(id+"F29.opLoft","SWEPT_FACE",FACE,{"disambiguationData":[OSD([subQ65,subQ64,subQ62,sQuery(id+"F22.wireOp",EDGE,"E28.6.1"),subQ61,subQ60])]})])],"derivedFrom":subQ11})])]}),makeQuery(id+"F47.opFillet","BLEND_FACE",FACE,{"disambiguationData":[OSD([subQ0,subQ9]),TDD([makeQuery(id+"F42.boolean.opBoolean","COPY",EDGE,{"disambiguationData":[TD([makeQuery(id+"F30.opLoft","SWEPT_FACE",FACE,{"disambiguationData":[OSD([subQ58,subQ57,subQ56,sQuery(id+"F22.wireOp",EDGE,"E28.7.1"),subQ55,subQ54])]})])],"derivedFrom":subQ11})])]}),makeQuery(id+"F47.opFillet","BLEND_FACE",FACE,{"disambiguationData":[OSD([subQ0,subQ9]),TDD([makeQuery(id+"F42.boolean.opBoolean","COPY",EDGE,{"disambiguationData":[TD([makeQuery(id+"F31.opLoft","SWEPT_FACE",FACE,{"disambiguationData":[OSD([subQ52,subQ51,subQ53,sQuery(id+"F22.wireOp",EDGE,"E28.8.1"),subQ49,subQ48])]})])],"derivedFrom":subQ11})])]}),makeQuery(id+"F47.opFillet","BLEND_FACE",FACE,{"disambiguationData":[OSD([subQ0,subQ9]),TDD([makeQuery(id+"F42.boolean.opBoolean","COPY",EDGE,{"disambiguationData":[TD([makeQuery(id+"F32.opLoft","SWEPT_FACE",FACE,{"disambiguationData":[OSD([subQ47,subQ46,subQ44,sQuery(id+"F22.wireOp",EDGE,"E28.9.1"),subQ43,subQ42])]})])],"derivedFrom":subQ11})])]}),makeQuery(id+"F47.opFillet","BLEND_FACE",FACE,{"disambiguationData":[OSD([subQ0,subQ9]),TDD([makeQuery(id+"F42.boolean.opBoolean","COPY",EDGE,{"disambiguationData":[TD([makeQuery(id+"F33.opLoft","SWEPT_FACE",FACE,{"disambiguationData":[OSD([subQ41,subQ40,subQ38,sQuery(id+"F22.wireOp",EDGE,"E28.10.1"),subQ37,subQ36])]})])],"derivedFrom":subQ11})])]}),makeQuery(id+"F47.opFillet","BLEND_FACE",FACE,{"disambiguationData":[OSD([subQ0,subQ9]),TDD([makeQuery(id+"F42.boolean.opBoolean","COPY",EDGE,{"disambiguationData":[TD([makeQuery(id+"F34.opLoft","SWEPT_FACE",FACE,{"disambiguationData":[OSD([subQ35,subQ34,subQ32,sQuery(id+"F22.wireOp",EDGE,"E28.11.1"),subQ31,subQ30])]})])],"derivedFrom":subQ11})])]}),makeQuery(id+"F47.opFillet","BLEND_FACE",FACE,{"disambiguationData":[OSD([subQ0,subQ9]),TDD([makeQuery(id+"F42.boolean.opBoolean","COPY",EDGE,{"disambiguationData":[TD([makeQuery(id+"F35.opLoft","SWEPT_FACE",FACE,{"disambiguationData":[OSD([subQ29,subQ28,subQ26,sQuery(id+"F22.wireOp",EDGE,"E28.12.1"),subQ25,subQ24])]})])],"derivedFrom":subQ11})])]}),makeQuery(id+"F47.opFillet","BLEND_FACE",FACE,{"disambiguationData":[OSD([subQ0,subQ9]),TDD([makeQuery(id+"F42.boolean.opBoolean","COPY",EDGE,{"disambiguationData":[TD([makeQuery(id+"F36.opLoft","SWEPT_FACE",FACE,{"disambiguationData":[OSD([subQ23,subQ22,subQ20,sQuery(id+"F22.wireOp",EDGE,"E28.13.1"),subQ19,subQ18])]})])],"derivedFrom":subQ11})])]}),makeQuery(id+"F47.opFillet","BLEND_FACE",FACE,{"disambiguationData":[OSD([subQ0,subQ9]),TDD([makeQuery(id+"F42.boolean.opBoolean","COPY",EDGE,{"disambiguationData":[TD([makeQuery(id+"F37.opLoft","SWEPT_FACE",FACE,{"disambiguationData":[OSD([subQ16,subQ15,subQ14,sQuery(id+"F22.wireOp",EDGE,"E28.14.1"),subQ13,subQ12])]})])],"derivedFrom":subQ11})])]}),makeQuery(id+"F47.opFillet","BLEND_FACE",FACE,{"disambiguationData":[OSD([subQ0,subQ9]),TDD([makeQuery(id+"F42.boolean.opBoolean","COPY",EDGE,{"disambiguationData":[TD([makeQuery(id+"F38.opLoft","SWEPT_FACE",FACE,{"disambiguationData":[OSD([subQ8,subQ7,subQ5,sQuery(id+"F22.wireOp",EDGE,"E28.15.1"),subQ4,subQ3])]})])],"derivedFrom":subQ11})])]})],"blendedInto":[makeQuery(id+"F47.opFillet","BLEND_FACE",FACE,{"disambiguationData":[OSD([subQ0,subQ9]),TDD([makeQuery(id+"F42.boolean.opBoolean","COPY",EDGE,{"disambiguationData":[TD([makeQuery(id+"F23.opLoft","SWEPT_FACE",FACE,{"disambiguationData":[OSD([sQuery(id+"F3.wireOp",EDGE,"E20.8.0"),subQ104,subQ102,subQ101,subQ100,sQuery(id+"F22.wireOp",EDGE,"E27.right")])]})])],"derivedFrom":subQ11})])]}),makeQuery(id+"F47.opFillet","BLEND_FACE",FACE,{"disambiguationData":[OSD([subQ0,subQ9]),TDD([makeQuery(id+"F42.boolean.opBoolean","COPY",EDGE,{"disambiguationData":[TD([subQ99])],"derivedFrom":subQ11})])]}),makeQuery(id+"F47.opFillet","BLEND_FACE",FACE,{"disambiguationData":[OSD([subQ0,subQ9]),TDD([makeQuery(id+"F42.boolean.opBoolean","COPY",EDGE,{"disambiguationData":[TD([subQ92])],"derivedFrom":subQ11})])]}),makeQuery(id+"F47.opFillet","BLEND_FACE",FACE,{"disambiguationData":[OSD([subQ0,subQ9]),TDD([makeQuery(id+"F42.boolean.opBoolean","COPY",EDGE,{"disambiguationData":[TD([subQ86])],"derivedFrom":subQ11})])]}),makeQuery(id+"F47.opFillet","BLEND_FACE",FACE,{"disambiguationData":[OSD([subQ0,subQ9]),TDD([makeQuery(id+"F42.boolean.opBoolean","COPY",EDGE,{"disambiguationData":[TD([subQ79])],"derivedFrom":subQ11})])]}),makeQuery(id+"F47.opFillet","BLEND_FACE",FACE,{"disambiguationData":[OSD([subQ0,subQ9]),TDD([makeQuery(id+"F42.boolean.opBoolean","COPY",EDGE,{"disambiguationData":[TD([makeQuery(id+"F28.opLoft","SWEPT_FACE",FACE,{"disambiguationData":[OSD([subQ71,subQ70,subQ68,sQuery(id+"F22.wireOp",EDGE,"E28.5.1"),subQ67,subQ66])]})])],"derivedFrom":subQ11})])]}),makeQuery(id+"F47.opFillet","BLEND_FACE",FACE,{"disambiguationData":[OSD([subQ0,subQ9]),TDD([makeQuery(id+"F42.boolean.opBoolean","COPY",EDGE,{"disambiguationData":[TD([makeQuery(id+"F29.opLoft","SWEPT_FACE",FACE,{"disambiguationData":[OSD([subQ65,subQ64,subQ62,sQuery(id+"F22.wireOp",EDGE,"E28.6.1"),subQ61,subQ60])]})])],"derivedFrom":subQ11})])]}),makeQuery(id+"F47.opFillet","BLEND_FACE",FACE,{"disambiguationData":[OSD([subQ0,subQ9]),TDD([makeQuery(id+"F42.boolean.opBoolean","COPY",EDGE,{"disambiguationData":[TD([makeQuery(id+"F30.opLoft","SWEPT_FACE",FACE,{"disambiguationData":[OSD([subQ58,subQ57,subQ56,sQuery(id+"F22.wireOp",EDGE,"E28.7.1"),subQ55,subQ54])]})])],"derivedFrom":subQ11})])]}),makeQuery(id+"F47.opFillet","BLEND_FACE",FACE,{"disambiguationData":[OSD([subQ0,subQ9]),TDD([makeQuery(id+"F42.boolean.opBoolean","COPY",EDGE,{"disambiguationData":[TD([makeQuery(id+"F31.opLoft","SWEPT_FACE",FACE,{"disambiguationData":[OSD([subQ52,subQ51,subQ53,sQuery(id+"F22.wireOp",EDGE,"E28.8.1"),subQ49,subQ48])]})])],"derivedFrom":subQ11})])]}),makeQuery(id+"F47.opFillet","BLEND_FACE",FACE,{"disambiguationData":[OSD([subQ0,subQ9]),TDD([makeQuery(id+"F42.boolean.opBoolean","COPY",EDGE,{"disambiguationData":[TD([makeQuery(id+"F32.opLoft","SWEPT_FACE",FACE,{"disambiguationData":[OSD([subQ47,subQ46,subQ44,sQuery(id+"F22.wireOp",EDGE,"E28.9.1"),subQ43,subQ42])]})])],"derivedFrom":subQ11})])]}),makeQuery(id+"F47.opFillet","BLEND_FACE",FACE,{"disambiguationData":[OSD([subQ0,subQ9]),TDD([makeQuery(id+"F42.boolean.opBoolean","COPY",EDGE,{"disambiguationData":[TD([makeQuery(id+"F33.opLoft","SWEPT_FACE",FACE,{"disambiguationData":[OSD([subQ41,subQ40,subQ38,sQuery(id+"F22.wireOp",EDGE,"E28.10.1"),subQ37,subQ36])]})])],"derivedFrom":subQ11})])]}),makeQuery(id+"F47.opFillet","BLEND_FACE",FACE,{"disambiguationData":[OSD([subQ0,subQ9]),TDD([makeQuery(id+"F42.boolean.opBoolean","COPY",EDGE,{"disambiguationData":[TD([makeQuery(id+"F34.opLoft","SWEPT_FACE",FACE,{"disambiguationData":[OSD([subQ35,subQ34,subQ32,sQuery(id+"F22.wireOp",EDGE,"E28.11.1"),subQ31,subQ30])]})])],"derivedFrom":subQ11})])]}),makeQuery(id+"F47.opFillet","BLEND_FACE",FACE,{"disambiguationData":[OSD([subQ0,subQ9]),TDD([makeQuery(id+"F42.boolean.opBoolean","COPY",EDGE,{"disambiguationData":[TD([makeQuery(id+"F35.opLoft","SWEPT_FACE",FACE,{"disambiguationData":[OSD([subQ29,subQ28,subQ26,sQuery(id+"F22.wireOp",EDGE,"E28.12.1"),subQ25,subQ24])]})])],"derivedFrom":subQ11})])]}),makeQuery(id+"F47.opFillet","BLEND_FACE",FACE,{"disambiguationData":[OSD([subQ0,subQ9]),TDD([makeQuery(id+"F42.boolean.opBoolean","COPY",EDGE,{"disambiguationData":[TD([makeQuery(id+"F36.opLoft","SWEPT_FACE",FACE,{"disambiguationData":[OSD([subQ23,subQ22,subQ20,sQuery(id+"F22.wireOp",EDGE,"E28.13.1"),subQ19,subQ18])]})])],"derivedFrom":subQ11})])]}),makeQuery(id+"F47.opFillet","BLEND_FACE",FACE,{"disambiguationData":[OSD([subQ0,subQ9]),TDD([makeQuery(id+"F42.boolean.opBoolean","COPY",EDGE,{"disambiguationData":[TD([makeQuery(id+"F37.opLoft","SWEPT_FACE",FACE,{"disambiguationData":[OSD([subQ16,subQ15,subQ14,sQuery(id+"F22.wireOp",EDGE,"E28.14.1"),subQ13,subQ12])]})])],"derivedFrom":subQ11})])]}),makeQuery(id+"F47.opFillet","BLEND_FACE",FACE,{"disambiguationData":[OSD([subQ0,subQ9]),TDD([makeQuery(id+"F42.boolean.opBoolean","COPY",EDGE,{"disambiguationData":[TD([makeQuery(id+"F38.opLoft","SWEPT_FACE",FACE,{"disambiguationData":[OSD([subQ8,subQ7,subQ5,sQuery(id+"F22.wireOp",EDGE,"E28.15.1"),subQ4,subQ3])]})])],"derivedFrom":subQ11})])]})]});}
            var Q30;
            {var subQ0=sQuery(id+"F22.wireOp",EDGE,"E28.4.3");var subQ1=sQuery(id+"F22.wireOp",EDGE,"E28.4.2");var subQ2=sQuery(id+"F22.wireOp",EDGE,"E28.4.0");var subQ3=sQuery(id+"F3.wireOp",EDGE,"E20.12.3");var subQ4=sQuery(id+"F3.wireOp",EDGE,"E20.12.1");var subQ5=makeQuery(id+"F27.opLoft","SWEPT_FACE",FACE,{"disambiguationData":[OSD([subQ4,sQuery(id+"F3.wireOp",EDGE,"E20.12.2"),subQ3,subQ2,subQ1,subQ0])]});var subQ6=sQuery(id+"F22.wireOp",EDGE,"E28.4.1");var subQ7=sQuery(id+"F41.wireOp",EDGE,"E34");var subQ8=sQuery(id+"F41.wireOp",EDGE,"E32");Q30=makeQuery(id+"F44.opFillet","BLEND_EDGE",EDGE,{"blendedFrom":[makeQuery(id+"F40.boolean.opBoolean","INTERSECT",EDGE,{"derivedFrom":[subQ5,makeQuery(id+"F40.opExtrude","CAP_FACE",FACE,{"disambiguationData":[OSD([sQuery(id+"F39.wireOp",EDGE,"E29"),sQuery(id+"F39.wireOp",EDGE,"E30")])],"isStart":true})]}),makeQuery(id+"F42.boolean.opBoolean","COPY",FACE,{"disambiguationData":[TD([makeQuery(id+"F27.opLoft","SWEPT_FACE",FACE,{"disambiguationData":[OSD([sQuery(id+"F3.wireOp",EDGE,"E20.12.0"),subQ4,subQ3,subQ6,subQ1,subQ0])]})])],"derivedFrom":makeQuery(id+"F42.opRevolve","SWEPT_FACE",FACE,{"disambiguationData":[OSD([subQ8]),TDD([makeQuery(id+"F41.imprint","IMPRINT",EDGE,{"disambiguationData":[TD([[makeQuery(id+"F41.imprint","INTERSECT",VERTEX,{"disambiguationData":[OD(0.0)],"derivedFrom":[subQ8,subQ7]}),-1.0]])],"derivedFrom":subQ8})])]})})],"blendedInto":[makeQuery(id+"F42.boolean.opBoolean","COPY",FACE,{"disambiguationData":[TD([makeQuery(id+"F27.opLoft","SWEPT_FACE",FACE,{"disambiguationData":[OSD([sQuery(id+"F3.wireOp",EDGE,"E20.12.0"),subQ4,subQ3,subQ6,subQ1,subQ0])]})])],"derivedFrom":makeQuery(id+"F42.opRevolve","SWEPT_FACE",FACE,{"disambiguationData":[OSD([subQ8]),TDD([makeQuery(id+"F41.imprint","IMPRINT",EDGE,{"disambiguationData":[TD([[makeQuery(id+"F41.imprint","INTERSECT",VERTEX,{"disambiguationData":[OD(0.0)],"derivedFrom":[subQ8,subQ7]}),-1.0]])],"derivedFrom":subQ8})])]})})]});}
            var Q31;
            {var subQ0=sQuery(id+"F41.wireOp",EDGE,"E34");var subQ1=sQuery(id+"F41.wireOp",EDGE,"E32");Q31=makeQuery(id+"F42.boolean.opBoolean","INTERSECT",EDGE,{"derivedFrom":[makeQuery(id+"F26.opLoft","SWEPT_FACE",FACE,{"disambiguationData":[OSD([sQuery(id+"F3.wireOp",EDGE,"E20.11.0"),sQuery(id+"F3.wireOp",EDGE,"E20.11.1"),sQuery(id+"F3.wireOp",EDGE,"E20.11.3"),sQuery(id+"F22.wireOp",EDGE,"E28.3.1"),sQuery(id+"F22.wireOp",EDGE,"E28.3.2"),sQuery(id+"F22.wireOp",EDGE,"E28.3.3")])]}),makeQuery(id+"F42.opRevolve","SWEPT_FACE",FACE,{"disambiguationData":[OSD([subQ1]),TDD([makeQuery(id+"F41.imprint","IMPRINT",EDGE,{"disambiguationData":[TD([[makeQuery(id+"F41.imprint","INTERSECT",VERTEX,{"disambiguationData":[OD(0.0)],"derivedFrom":[subQ1,subQ0]}),-1.0]])],"derivedFrom":subQ1})])]})]});}
            var Q32;
            {var subQ0=sQuery(id+"F41.wireOp",EDGE,"E37");var subQ1=makeQuery(id+"F42.opRevolve","SWEPT_FACE",FACE,{"disambiguationData":[OSD([subQ0])]});var subQ2=makeQuery(id+"F40.opExtrude","CAP_FACE",FACE,{"disambiguationData":[OSD([sQuery(id+"F39.wireOp",EDGE,"E29"),sQuery(id+"F39.wireOp",EDGE,"E30")])],"isStart":true});var subQ3=sQuery(id+"F22.wireOp",EDGE,"E28.15.3");var subQ4=sQuery(id+"F22.wireOp",EDGE,"E28.15.2");var subQ5=sQuery(id+"F3.wireOp",EDGE,"E20.7.3");var subQ7=sQuery(id+"F3.wireOp",EDGE,"E20.7.1");var subQ8=sQuery(id+"F3.wireOp",EDGE,"E20.7.0");var subQ9=sQuery(id+"F41.wireOp",EDGE,"E38");var subQ10=makeQuery(id+"F42.opRevolve","SWEPT_FACE",FACE,{"disambiguationData":[OSD([subQ9])]});var subQ11=makeQuery(id+"F42.opRevolve","SWEPT_EDGE",EDGE,{"disambiguationData":[OSD([subQ0,subQ9])]});var subQ12=sQuery(id+"F22.wireOp",EDGE,"E28.14.3");var subQ13=sQuery(id+"F22.wireOp",EDGE,"E28.14.2");var subQ14=sQuery(id+"F3.wireOp",EDGE,"E20.6.3");var subQ15=sQuery(id+"F3.wireOp",EDGE,"E20.6.1");var subQ16=sQuery(id+"F3.wireOp",EDGE,"E20.6.0");var subQ18=sQuery(id+"F22.wireOp",EDGE,"E28.13.3");var subQ19=sQuery(id+"F22.wireOp",EDGE,"E28.13.2");var subQ20=sQuery(id+"F3.wireOp",EDGE,"E20.5.3");var subQ22=sQuery(id+"F3.wireOp",EDGE,"E20.5.1");var subQ23=sQuery(id+"F3.wireOp",EDGE,"E20.5.0");var subQ24=sQuery(id+"F22.wireOp",EDGE,"E28.12.3");var subQ25=sQuery(id+"F22.wireOp",EDGE,"E28.12.2");var subQ26=sQuery(id+"F3.wireOp",EDGE,"E20.4.3");var subQ28=sQuery(id+"F3.wireOp",EDGE,"E20.4.1");var subQ29=sQuery(id+"F3.wireOp",EDGE,"E20.4.0");var subQ30=sQuery(id+"F22.wireOp",EDGE,"E28.11.3");var subQ31=sQuery(id+"F22.wireOp",EDGE,"E28.11.2");var subQ32=sQuery(id+"F3.wireOp",EDGE,"E20.3.3");var subQ34=sQuery(id+"F3.wireOp",EDGE,"E20.3.1");var subQ35=sQuery(id+"F3.wireOp",EDGE,"E20.3.0");var subQ36=sQuery(id+"F22.wireOp",EDGE,"E28.10.3");var subQ37=sQuery(id+"F22.wireOp",EDGE,"E28.10.2");var subQ38=sQuery(id+"F3.wireOp",EDGE,"E20.2.3");var subQ40=sQuery(id+"F3.wireOp",EDGE,"E20.2.1");var subQ41=sQuery(id+"F3.wireOp",EDGE,"E20.2.0");var subQ42=sQuery(id+"F22.wireOp",EDGE,"E28.9.3");var subQ43=sQuery(id+"F22.wireOp",EDGE,"E28.9.2");var subQ44=sQuery(id+"F3.wireOp",EDGE,"E20.1.3");var subQ46=sQuery(id+"F3.wireOp",EDGE,"E20.1.1");var subQ47=sQuery(id+"F3.wireOp",EDGE,"E20.1.0");var subQ48=sQuery(id+"F22.wireOp",EDGE,"E28.8.3");var subQ49=sQuery(id+"F22.wireOp",EDGE,"E28.8.2");var subQ51=sQuery(id+"F3.wireOp",EDGE,"E18.top");var subQ52=sQuery(id+"F3.wireOp",EDGE,"E18.bottom");var subQ53=sQuery(id+"F3.wireOp",EDGE,"E18.left");var subQ54=sQuery(id+"F22.wireOp",EDGE,"E28.7.3");var subQ55=sQuery(id+"F22.wireOp",EDGE,"E28.7.2");var subQ56=sQuery(id+"F3.wireOp",EDGE,"E20.15.3");var subQ57=sQuery(id+"F3.wireOp",EDGE,"E20.15.1");var subQ58=sQuery(id+"F3.wireOp",EDGE,"E20.15.0");var subQ60=sQuery(id+"F22.wireOp",EDGE,"E28.6.3");var subQ61=sQuery(id+"F22.wireOp",EDGE,"E28.6.2");var subQ62=sQuery(id+"F3.wireOp",EDGE,"E20.14.3");var subQ64=sQuery(id+"F3.wireOp",EDGE,"E20.14.1");var subQ65=sQuery(id+"F3.wireOp",EDGE,"E20.14.0");var subQ66=sQuery(id+"F22.wireOp",EDGE,"E28.5.3");var subQ67=sQuery(id+"F22.wireOp",EDGE,"E28.5.2");var subQ68=sQuery(id+"F3.wireOp",EDGE,"E20.13.3");var subQ70=sQuery(id+"F3.wireOp",EDGE,"E20.13.1");var subQ71=sQuery(id+"F3.wireOp",EDGE,"E20.13.0");var subQ72=sQuery(id+"F22.wireOp",EDGE,"E28.4.3");var subQ73=sQuery(id+"F22.wireOp",EDGE,"E28.4.2");var subQ74=sQuery(id+"F3.wireOp",EDGE,"E20.12.3");var subQ76=sQuery(id+"F3.wireOp",EDGE,"E20.12.1");var subQ77=sQuery(id+"F3.wireOp",EDGE,"E20.12.0");var subQ78=sQuery(id+"F22.wireOp",EDGE,"E28.3.3");var subQ79=sQuery(id+"F22.wireOp",EDGE,"E28.3.2");var subQ80=sQuery(id+"F3.wireOp",EDGE,"E20.11.3");var subQ82=sQuery(id+"F3.wireOp",EDGE,"E20.11.1");var subQ84=sQuery(id+"F3.wireOp",EDGE,"E20.11.0");var subQ85=makeQuery(id+"F26.opLoft","SWEPT_FACE",FACE,{"disambiguationData":[OSD([subQ84,subQ82,subQ80,sQuery(id+"F22.wireOp",EDGE,"E28.3.1"),subQ79,subQ78])]});var subQ86=sQuery(id+"F22.wireOp",EDGE,"E28.2.3");var subQ87=sQuery(id+"F22.wireOp",EDGE,"E28.2.2");var subQ88=sQuery(id+"F3.wireOp",EDGE,"E20.10.3");var subQ89=sQuery(id+"F3.wireOp",EDGE,"E20.10.1");var subQ90=sQuery(id+"F3.wireOp",EDGE,"E20.10.0");var subQ91=makeQuery(id+"F25.opLoft","SWEPT_FACE",FACE,{"disambiguationData":[OSD([subQ90,subQ89,subQ88,sQuery(id+"F22.wireOp",EDGE,"E28.2.1"),subQ87,subQ86])]});var subQ93=sQuery(id+"F22.wireOp",EDGE,"E28.1.3");var subQ94=sQuery(id+"F22.wireOp",EDGE,"E28.1.2");var subQ95=sQuery(id+"F3.wireOp",EDGE,"E20.9.3");var subQ96=sQuery(id+"F3.wireOp",EDGE,"E20.9.1");var subQ97=sQuery(id+"F3.wireOp",EDGE,"E20.9.0");var subQ98=makeQuery(id+"F24.opLoft","SWEPT_FACE",FACE,{"disambiguationData":[OSD([subQ97,subQ96,subQ95,sQuery(id+"F22.wireOp",EDGE,"E28.1.1"),subQ94,subQ93])]});var subQ99=sQuery(id+"F22.wireOp",EDGE,"E27.top");var subQ100=sQuery(id+"F22.wireOp",EDGE,"E27.bottom");var subQ101=sQuery(id+"F3.wireOp",EDGE,"E20.8.3");var subQ103=sQuery(id+"F3.wireOp",EDGE,"E20.8.1");var subQ107=makeQuery(id+"F42.boolean.opBoolean","COPY",FACE,{"disambiguationData":[TD([subQ85])],"derivedFrom":subQ10});var subQ141=makeQuery(id+"F5.opLoft","CAP_FACE",FACE,{"disambiguationData":[OSD([makeQuery(id+"F3.imprint","IMPRINT",FACE,{"disambiguationData":[TD([[makeQuery(id+"F3.imprint","IMPRINT",EDGE,{"derivedFrom":subQ52}),1.0]])]})])],"isStart":true});var subQ179=makeQuery(id+"F26.boolean.opBoolean","INTERSECT",EDGE,{"derivedFrom":[makeQuery(id+"F25.boolean.opBoolean","SPLIT",FACE,{"disambiguationData":[TD([subQ141])],"derivedFrom":makeQuery(id+"F24.boolean.opBoolean","SPLIT",FACE,{"disambiguationData":[TD([subQ141])],"derivedFrom":makeQuery(id+"F1.opRevolve","SWEPT_FACE",FACE,{"disambiguationData":[OSD([sQuery(id+"F0.wireOp",EDGE,"E13")])]})})}),subQ85]});Q32=makeQuery(id+"F48.opFillet","BLEND_EDGE",EDGE,{"blendedFrom":[makeQuery(id+"F47.opFillet","TWEAK_EDGE",EDGE,{"derivedFrom":[makeQuery(id+"F45.opFillet","BLEND_VERTEX",VERTEX,{"blendedFrom":[subQ179,subQ85,subQ107],"blendedInto":[subQ85,subQ107]}),makeQuery(id+"F45.opFillet","BLEND_VERTEX",VERTEX,{"blendedFrom":[subQ179,makeQuery(id+"F42.boolean.opBoolean","MERGE",FACE,{"derivedFrom":[subQ2,subQ1]}),subQ107],"blendedInto":[makeQuery(id+"F42.boolean.opBoolean","MERGE",FACE,{"derivedFrom":[subQ2,subQ1]}),subQ107]})]}),makeQuery(id+"F47.opFillet","BLEND_FACE",FACE,{"disambiguationData":[OSD([subQ0,subQ9]),TDD([makeQuery(id+"F42.boolean.opBoolean","COPY",EDGE,{"disambiguationData":[TD([makeQuery(id+"F23.opLoft","SWEPT_FACE",FACE,{"disambiguationData":[OSD([sQuery(id+"F3.wireOp",EDGE,"E20.8.0"),subQ103,subQ101,subQ100,subQ99,sQuery(id+"F22.wireOp",EDGE,"E27.right")])]})])],"derivedFrom":subQ11})])]}),makeQuery(id+"F47.opFillet","BLEND_FACE",FACE,{"disambiguationData":[OSD([subQ0,subQ9]),TDD([makeQuery(id+"F42.boolean.opBoolean","COPY",EDGE,{"disambiguationData":[TD([subQ98])],"derivedFrom":subQ11})])]}),makeQuery(id+"F47.opFillet","BLEND_FACE",FACE,{"disambiguationData":[OSD([subQ0,subQ9]),TDD([makeQuery(id+"F42.boolean.opBoolean","COPY",EDGE,{"disambiguationData":[TD([subQ91])],"derivedFrom":subQ11})])]}),makeQuery(id+"F47.opFillet","BLEND_FACE",FACE,{"disambiguationData":[OSD([subQ0,subQ9]),TDD([makeQuery(id+"F42.boolean.opBoolean","COPY",EDGE,{"disambiguationData":[TD([subQ85])],"derivedFrom":subQ11})])]}),makeQuery(id+"F47.opFillet","BLEND_FACE",FACE,{"disambiguationData":[OSD([subQ0,subQ9]),TDD([makeQuery(id+"F42.boolean.opBoolean","COPY",EDGE,{"disambiguationData":[TD([makeQuery(id+"F27.opLoft","SWEPT_FACE",FACE,{"disambiguationData":[OSD([subQ77,subQ76,subQ74,sQuery(id+"F22.wireOp",EDGE,"E28.4.1"),subQ73,subQ72])]})])],"derivedFrom":subQ11})])]}),makeQuery(id+"F47.opFillet","BLEND_FACE",FACE,{"disambiguationData":[OSD([subQ0,subQ9]),TDD([makeQuery(id+"F42.boolean.opBoolean","COPY",EDGE,{"disambiguationData":[TD([makeQuery(id+"F28.opLoft","SWEPT_FACE",FACE,{"disambiguationData":[OSD([subQ71,subQ70,subQ68,sQuery(id+"F22.wireOp",EDGE,"E28.5.1"),subQ67,subQ66])]})])],"derivedFrom":subQ11})])]}),makeQuery(id+"F47.opFillet","BLEND_FACE",FACE,{"disambiguationData":[OSD([subQ0,subQ9]),TDD([makeQuery(id+"F42.boolean.opBoolean","COPY",EDGE,{"disambiguationData":[TD([makeQuery(id+"F29.opLoft","SWEPT_FACE",FACE,{"disambiguationData":[OSD([subQ65,subQ64,subQ62,sQuery(id+"F22.wireOp",EDGE,"E28.6.1"),subQ61,subQ60])]})])],"derivedFrom":subQ11})])]}),makeQuery(id+"F47.opFillet","BLEND_FACE",FACE,{"disambiguationData":[OSD([subQ0,subQ9]),TDD([makeQuery(id+"F42.boolean.opBoolean","COPY",EDGE,{"disambiguationData":[TD([makeQuery(id+"F30.opLoft","SWEPT_FACE",FACE,{"disambiguationData":[OSD([subQ58,subQ57,subQ56,sQuery(id+"F22.wireOp",EDGE,"E28.7.1"),subQ55,subQ54])]})])],"derivedFrom":subQ11})])]}),makeQuery(id+"F47.opFillet","BLEND_FACE",FACE,{"disambiguationData":[OSD([subQ0,subQ9]),TDD([makeQuery(id+"F42.boolean.opBoolean","COPY",EDGE,{"disambiguationData":[TD([makeQuery(id+"F31.opLoft","SWEPT_FACE",FACE,{"disambiguationData":[OSD([subQ52,subQ51,subQ53,sQuery(id+"F22.wireOp",EDGE,"E28.8.1"),subQ49,subQ48])]})])],"derivedFrom":subQ11})])]}),makeQuery(id+"F47.opFillet","BLEND_FACE",FACE,{"disambiguationData":[OSD([subQ0,subQ9]),TDD([makeQuery(id+"F42.boolean.opBoolean","COPY",EDGE,{"disambiguationData":[TD([makeQuery(id+"F32.opLoft","SWEPT_FACE",FACE,{"disambiguationData":[OSD([subQ47,subQ46,subQ44,sQuery(id+"F22.wireOp",EDGE,"E28.9.1"),subQ43,subQ42])]})])],"derivedFrom":subQ11})])]}),makeQuery(id+"F47.opFillet","BLEND_FACE",FACE,{"disambiguationData":[OSD([subQ0,subQ9]),TDD([makeQuery(id+"F42.boolean.opBoolean","COPY",EDGE,{"disambiguationData":[TD([makeQuery(id+"F33.opLoft","SWEPT_FACE",FACE,{"disambiguationData":[OSD([subQ41,subQ40,subQ38,sQuery(id+"F22.wireOp",EDGE,"E28.10.1"),subQ37,subQ36])]})])],"derivedFrom":subQ11})])]}),makeQuery(id+"F47.opFillet","BLEND_FACE",FACE,{"disambiguationData":[OSD([subQ0,subQ9]),TDD([makeQuery(id+"F42.boolean.opBoolean","COPY",EDGE,{"disambiguationData":[TD([makeQuery(id+"F34.opLoft","SWEPT_FACE",FACE,{"disambiguationData":[OSD([subQ35,subQ34,subQ32,sQuery(id+"F22.wireOp",EDGE,"E28.11.1"),subQ31,subQ30])]})])],"derivedFrom":subQ11})])]}),makeQuery(id+"F47.opFillet","BLEND_FACE",FACE,{"disambiguationData":[OSD([subQ0,subQ9]),TDD([makeQuery(id+"F42.boolean.opBoolean","COPY",EDGE,{"disambiguationData":[TD([makeQuery(id+"F35.opLoft","SWEPT_FACE",FACE,{"disambiguationData":[OSD([subQ29,subQ28,subQ26,sQuery(id+"F22.wireOp",EDGE,"E28.12.1"),subQ25,subQ24])]})])],"derivedFrom":subQ11})])]}),makeQuery(id+"F47.opFillet","BLEND_FACE",FACE,{"disambiguationData":[OSD([subQ0,subQ9]),TDD([makeQuery(id+"F42.boolean.opBoolean","COPY",EDGE,{"disambiguationData":[TD([makeQuery(id+"F36.opLoft","SWEPT_FACE",FACE,{"disambiguationData":[OSD([subQ23,subQ22,subQ20,sQuery(id+"F22.wireOp",EDGE,"E28.13.1"),subQ19,subQ18])]})])],"derivedFrom":subQ11})])]}),makeQuery(id+"F47.opFillet","BLEND_FACE",FACE,{"disambiguationData":[OSD([subQ0,subQ9]),TDD([makeQuery(id+"F42.boolean.opBoolean","COPY",EDGE,{"disambiguationData":[TD([makeQuery(id+"F37.opLoft","SWEPT_FACE",FACE,{"disambiguationData":[OSD([subQ16,subQ15,subQ14,sQuery(id+"F22.wireOp",EDGE,"E28.14.1"),subQ13,subQ12])]})])],"derivedFrom":subQ11})])]}),makeQuery(id+"F47.opFillet","BLEND_FACE",FACE,{"disambiguationData":[OSD([subQ0,subQ9]),TDD([makeQuery(id+"F42.boolean.opBoolean","COPY",EDGE,{"disambiguationData":[TD([makeQuery(id+"F38.opLoft","SWEPT_FACE",FACE,{"disambiguationData":[OSD([subQ8,subQ7,subQ5,sQuery(id+"F22.wireOp",EDGE,"E28.15.1"),subQ4,subQ3])]})])],"derivedFrom":subQ11})])]})],"blendedInto":[makeQuery(id+"F47.opFillet","BLEND_FACE",FACE,{"disambiguationData":[OSD([subQ0,subQ9]),TDD([makeQuery(id+"F42.boolean.opBoolean","COPY",EDGE,{"disambiguationData":[TD([makeQuery(id+"F23.opLoft","SWEPT_FACE",FACE,{"disambiguationData":[OSD([sQuery(id+"F3.wireOp",EDGE,"E20.8.0"),subQ103,subQ101,subQ100,subQ99,sQuery(id+"F22.wireOp",EDGE,"E27.right")])]})])],"derivedFrom":subQ11})])]}),makeQuery(id+"F47.opFillet","BLEND_FACE",FACE,{"disambiguationData":[OSD([subQ0,subQ9]),TDD([makeQuery(id+"F42.boolean.opBoolean","COPY",EDGE,{"disambiguationData":[TD([subQ98])],"derivedFrom":subQ11})])]}),makeQuery(id+"F47.opFillet","BLEND_FACE",FACE,{"disambiguationData":[OSD([subQ0,subQ9]),TDD([makeQuery(id+"F42.boolean.opBoolean","COPY",EDGE,{"disambiguationData":[TD([subQ91])],"derivedFrom":subQ11})])]}),makeQuery(id+"F47.opFillet","BLEND_FACE",FACE,{"disambiguationData":[OSD([subQ0,subQ9]),TDD([makeQuery(id+"F42.boolean.opBoolean","COPY",EDGE,{"disambiguationData":[TD([subQ85])],"derivedFrom":subQ11})])]}),makeQuery(id+"F47.opFillet","BLEND_FACE",FACE,{"disambiguationData":[OSD([subQ0,subQ9]),TDD([makeQuery(id+"F42.boolean.opBoolean","COPY",EDGE,{"disambiguationData":[TD([makeQuery(id+"F27.opLoft","SWEPT_FACE",FACE,{"disambiguationData":[OSD([subQ77,subQ76,subQ74,sQuery(id+"F22.wireOp",EDGE,"E28.4.1"),subQ73,subQ72])]})])],"derivedFrom":subQ11})])]}),makeQuery(id+"F47.opFillet","BLEND_FACE",FACE,{"disambiguationData":[OSD([subQ0,subQ9]),TDD([makeQuery(id+"F42.boolean.opBoolean","COPY",EDGE,{"disambiguationData":[TD([makeQuery(id+"F28.opLoft","SWEPT_FACE",FACE,{"disambiguationData":[OSD([subQ71,subQ70,subQ68,sQuery(id+"F22.wireOp",EDGE,"E28.5.1"),subQ67,subQ66])]})])],"derivedFrom":subQ11})])]}),makeQuery(id+"F47.opFillet","BLEND_FACE",FACE,{"disambiguationData":[OSD([subQ0,subQ9]),TDD([makeQuery(id+"F42.boolean.opBoolean","COPY",EDGE,{"disambiguationData":[TD([makeQuery(id+"F29.opLoft","SWEPT_FACE",FACE,{"disambiguationData":[OSD([subQ65,subQ64,subQ62,sQuery(id+"F22.wireOp",EDGE,"E28.6.1"),subQ61,subQ60])]})])],"derivedFrom":subQ11})])]}),makeQuery(id+"F47.opFillet","BLEND_FACE",FACE,{"disambiguationData":[OSD([subQ0,subQ9]),TDD([makeQuery(id+"F42.boolean.opBoolean","COPY",EDGE,{"disambiguationData":[TD([makeQuery(id+"F30.opLoft","SWEPT_FACE",FACE,{"disambiguationData":[OSD([subQ58,subQ57,subQ56,sQuery(id+"F22.wireOp",EDGE,"E28.7.1"),subQ55,subQ54])]})])],"derivedFrom":subQ11})])]}),makeQuery(id+"F47.opFillet","BLEND_FACE",FACE,{"disambiguationData":[OSD([subQ0,subQ9]),TDD([makeQuery(id+"F42.boolean.opBoolean","COPY",EDGE,{"disambiguationData":[TD([makeQuery(id+"F31.opLoft","SWEPT_FACE",FACE,{"disambiguationData":[OSD([subQ52,subQ51,subQ53,sQuery(id+"F22.wireOp",EDGE,"E28.8.1"),subQ49,subQ48])]})])],"derivedFrom":subQ11})])]}),makeQuery(id+"F47.opFillet","BLEND_FACE",FACE,{"disambiguationData":[OSD([subQ0,subQ9]),TDD([makeQuery(id+"F42.boolean.opBoolean","COPY",EDGE,{"disambiguationData":[TD([makeQuery(id+"F32.opLoft","SWEPT_FACE",FACE,{"disambiguationData":[OSD([subQ47,subQ46,subQ44,sQuery(id+"F22.wireOp",EDGE,"E28.9.1"),subQ43,subQ42])]})])],"derivedFrom":subQ11})])]}),makeQuery(id+"F47.opFillet","BLEND_FACE",FACE,{"disambiguationData":[OSD([subQ0,subQ9]),TDD([makeQuery(id+"F42.boolean.opBoolean","COPY",EDGE,{"disambiguationData":[TD([makeQuery(id+"F33.opLoft","SWEPT_FACE",FACE,{"disambiguationData":[OSD([subQ41,subQ40,subQ38,sQuery(id+"F22.wireOp",EDGE,"E28.10.1"),subQ37,subQ36])]})])],"derivedFrom":subQ11})])]}),makeQuery(id+"F47.opFillet","BLEND_FACE",FACE,{"disambiguationData":[OSD([subQ0,subQ9]),TDD([makeQuery(id+"F42.boolean.opBoolean","COPY",EDGE,{"disambiguationData":[TD([makeQuery(id+"F34.opLoft","SWEPT_FACE",FACE,{"disambiguationData":[OSD([subQ35,subQ34,subQ32,sQuery(id+"F22.wireOp",EDGE,"E28.11.1"),subQ31,subQ30])]})])],"derivedFrom":subQ11})])]}),makeQuery(id+"F47.opFillet","BLEND_FACE",FACE,{"disambiguationData":[OSD([subQ0,subQ9]),TDD([makeQuery(id+"F42.boolean.opBoolean","COPY",EDGE,{"disambiguationData":[TD([makeQuery(id+"F35.opLoft","SWEPT_FACE",FACE,{"disambiguationData":[OSD([subQ29,subQ28,subQ26,sQuery(id+"F22.wireOp",EDGE,"E28.12.1"),subQ25,subQ24])]})])],"derivedFrom":subQ11})])]}),makeQuery(id+"F47.opFillet","BLEND_FACE",FACE,{"disambiguationData":[OSD([subQ0,subQ9]),TDD([makeQuery(id+"F42.boolean.opBoolean","COPY",EDGE,{"disambiguationData":[TD([makeQuery(id+"F36.opLoft","SWEPT_FACE",FACE,{"disambiguationData":[OSD([subQ23,subQ22,subQ20,sQuery(id+"F22.wireOp",EDGE,"E28.13.1"),subQ19,subQ18])]})])],"derivedFrom":subQ11})])]}),makeQuery(id+"F47.opFillet","BLEND_FACE",FACE,{"disambiguationData":[OSD([subQ0,subQ9]),TDD([makeQuery(id+"F42.boolean.opBoolean","COPY",EDGE,{"disambiguationData":[TD([makeQuery(id+"F37.opLoft","SWEPT_FACE",FACE,{"disambiguationData":[OSD([subQ16,subQ15,subQ14,sQuery(id+"F22.wireOp",EDGE,"E28.14.1"),subQ13,subQ12])]})])],"derivedFrom":subQ11})])]}),makeQuery(id+"F47.opFillet","BLEND_FACE",FACE,{"disambiguationData":[OSD([subQ0,subQ9]),TDD([makeQuery(id+"F42.boolean.opBoolean","COPY",EDGE,{"disambiguationData":[TD([makeQuery(id+"F38.opLoft","SWEPT_FACE",FACE,{"disambiguationData":[OSD([subQ8,subQ7,subQ5,sQuery(id+"F22.wireOp",EDGE,"E28.15.1"),subQ4,subQ3])]})])],"derivedFrom":subQ11})])]})]});}
            var Q33;
            {var subQ0=sQuery(id+"F41.wireOp",EDGE,"E34");var subQ1=sQuery(id+"F41.wireOp",EDGE,"E32");Q33=makeQuery(id+"F42.boolean.opBoolean","INTERSECT",EDGE,{"derivedFrom":[makeQuery(id+"F25.opLoft","SWEPT_FACE",FACE,{"disambiguationData":[OSD([sQuery(id+"F3.wireOp",EDGE,"E20.10.0"),sQuery(id+"F3.wireOp",EDGE,"E20.10.1"),sQuery(id+"F3.wireOp",EDGE,"E20.10.3"),sQuery(id+"F22.wireOp",EDGE,"E28.2.1"),sQuery(id+"F22.wireOp",EDGE,"E28.2.2"),sQuery(id+"F22.wireOp",EDGE,"E28.2.3")])]}),makeQuery(id+"F42.opRevolve","SWEPT_FACE",FACE,{"disambiguationData":[OSD([subQ1]),TDD([makeQuery(id+"F41.imprint","IMPRINT",EDGE,{"disambiguationData":[TD([[makeQuery(id+"F41.imprint","INTERSECT",VERTEX,{"disambiguationData":[OD(0.0)],"derivedFrom":[subQ1,subQ0]}),-1.0]])],"derivedFrom":subQ1})])]})]});}
            var Q34;
            {var subQ0=sQuery(id+"F22.wireOp",EDGE,"E28.3.0");var subQ1=sQuery(id+"F22.wireOp",EDGE,"E28.3.1");var subQ2=sQuery(id+"F22.wireOp",EDGE,"E28.3.2");var subQ3=sQuery(id+"F22.wireOp",EDGE,"E28.3.3");var subQ4=sQuery(id+"F3.wireOp",EDGE,"E20.11.3");var subQ5=sQuery(id+"F3.wireOp",EDGE,"E20.11.1");var subQ6=makeQuery(id+"F26.opLoft","SWEPT_FACE",FACE,{"disambiguationData":[OSD([subQ5,sQuery(id+"F3.wireOp",EDGE,"E20.11.2"),subQ4,subQ0,subQ2,subQ3])]});var subQ7=sQuery(id+"F41.wireOp",EDGE,"E34");var subQ8=sQuery(id+"F41.wireOp",EDGE,"E32");Q34=makeQuery(id+"F44.opFillet","BLEND_EDGE",EDGE,{"blendedFrom":[makeQuery(id+"F40.boolean.opBoolean","INTERSECT",EDGE,{"derivedFrom":[subQ6,makeQuery(id+"F40.opExtrude","CAP_FACE",FACE,{"disambiguationData":[OSD([sQuery(id+"F39.wireOp",EDGE,"E29"),sQuery(id+"F39.wireOp",EDGE,"E30")])],"isStart":true})]}),makeQuery(id+"F42.boolean.opBoolean","COPY",FACE,{"disambiguationData":[TD([makeQuery(id+"F26.opLoft","SWEPT_FACE",FACE,{"disambiguationData":[OSD([sQuery(id+"F3.wireOp",EDGE,"E20.11.0"),subQ5,subQ4,subQ1,subQ2,subQ3])]})])],"derivedFrom":makeQuery(id+"F42.opRevolve","SWEPT_FACE",FACE,{"disambiguationData":[OSD([subQ8]),TDD([makeQuery(id+"F41.imprint","IMPRINT",EDGE,{"disambiguationData":[TD([[makeQuery(id+"F41.imprint","INTERSECT",VERTEX,{"disambiguationData":[OD(0.0)],"derivedFrom":[subQ8,subQ7]}),-1.0]])],"derivedFrom":subQ8})])]})})],"blendedInto":[makeQuery(id+"F42.boolean.opBoolean","COPY",FACE,{"disambiguationData":[TD([makeQuery(id+"F26.opLoft","SWEPT_FACE",FACE,{"disambiguationData":[OSD([sQuery(id+"F3.wireOp",EDGE,"E20.11.0"),subQ5,subQ4,subQ1,subQ2,subQ3])]})])],"derivedFrom":makeQuery(id+"F42.opRevolve","SWEPT_FACE",FACE,{"disambiguationData":[OSD([subQ8]),TDD([makeQuery(id+"F41.imprint","IMPRINT",EDGE,{"disambiguationData":[TD([[makeQuery(id+"F41.imprint","INTERSECT",VERTEX,{"disambiguationData":[OD(0.0)],"derivedFrom":[subQ8,subQ7]}),-1.0]])],"derivedFrom":subQ8})])]})})]});}
            var Q35;
            {var subQ0=sQuery(id+"F41.wireOp",EDGE,"E37");var subQ1=makeQuery(id+"F42.opRevolve","SWEPT_FACE",FACE,{"disambiguationData":[OSD([subQ0])]});var subQ2=makeQuery(id+"F40.opExtrude","CAP_FACE",FACE,{"disambiguationData":[OSD([sQuery(id+"F39.wireOp",EDGE,"E29"),sQuery(id+"F39.wireOp",EDGE,"E30")])],"isStart":true});var subQ3=sQuery(id+"F22.wireOp",EDGE,"E28.15.3");var subQ4=sQuery(id+"F22.wireOp",EDGE,"E28.15.2");var subQ5=sQuery(id+"F3.wireOp",EDGE,"E20.7.3");var subQ7=sQuery(id+"F3.wireOp",EDGE,"E20.7.1");var subQ8=sQuery(id+"F3.wireOp",EDGE,"E20.7.0");var subQ9=sQuery(id+"F41.wireOp",EDGE,"E38");var subQ10=makeQuery(id+"F42.opRevolve","SWEPT_FACE",FACE,{"disambiguationData":[OSD([subQ9])]});var subQ11=makeQuery(id+"F42.opRevolve","SWEPT_EDGE",EDGE,{"disambiguationData":[OSD([subQ0,subQ9])]});var subQ12=sQuery(id+"F22.wireOp",EDGE,"E28.14.3");var subQ13=sQuery(id+"F22.wireOp",EDGE,"E28.14.2");var subQ14=sQuery(id+"F3.wireOp",EDGE,"E20.6.3");var subQ15=sQuery(id+"F3.wireOp",EDGE,"E20.6.1");var subQ16=sQuery(id+"F3.wireOp",EDGE,"E20.6.0");var subQ18=sQuery(id+"F22.wireOp",EDGE,"E28.13.3");var subQ19=sQuery(id+"F22.wireOp",EDGE,"E28.13.2");var subQ20=sQuery(id+"F3.wireOp",EDGE,"E20.5.3");var subQ22=sQuery(id+"F3.wireOp",EDGE,"E20.5.1");var subQ23=sQuery(id+"F3.wireOp",EDGE,"E20.5.0");var subQ24=sQuery(id+"F22.wireOp",EDGE,"E28.12.3");var subQ25=sQuery(id+"F22.wireOp",EDGE,"E28.12.2");var subQ26=sQuery(id+"F3.wireOp",EDGE,"E20.4.3");var subQ28=sQuery(id+"F3.wireOp",EDGE,"E20.4.1");var subQ29=sQuery(id+"F3.wireOp",EDGE,"E20.4.0");var subQ30=sQuery(id+"F22.wireOp",EDGE,"E28.11.3");var subQ31=sQuery(id+"F22.wireOp",EDGE,"E28.11.2");var subQ32=sQuery(id+"F3.wireOp",EDGE,"E20.3.3");var subQ34=sQuery(id+"F3.wireOp",EDGE,"E20.3.1");var subQ35=sQuery(id+"F3.wireOp",EDGE,"E20.3.0");var subQ36=sQuery(id+"F22.wireOp",EDGE,"E28.10.3");var subQ37=sQuery(id+"F22.wireOp",EDGE,"E28.10.2");var subQ38=sQuery(id+"F3.wireOp",EDGE,"E20.2.3");var subQ40=sQuery(id+"F3.wireOp",EDGE,"E20.2.1");var subQ41=sQuery(id+"F3.wireOp",EDGE,"E20.2.0");var subQ42=sQuery(id+"F22.wireOp",EDGE,"E28.9.3");var subQ43=sQuery(id+"F22.wireOp",EDGE,"E28.9.2");var subQ44=sQuery(id+"F3.wireOp",EDGE,"E20.1.3");var subQ46=sQuery(id+"F3.wireOp",EDGE,"E20.1.1");var subQ47=sQuery(id+"F3.wireOp",EDGE,"E20.1.0");var subQ48=sQuery(id+"F22.wireOp",EDGE,"E28.8.3");var subQ49=sQuery(id+"F22.wireOp",EDGE,"E28.8.2");var subQ51=sQuery(id+"F3.wireOp",EDGE,"E18.top");var subQ52=sQuery(id+"F3.wireOp",EDGE,"E18.bottom");var subQ53=sQuery(id+"F3.wireOp",EDGE,"E18.left");var subQ54=sQuery(id+"F22.wireOp",EDGE,"E28.7.3");var subQ55=sQuery(id+"F22.wireOp",EDGE,"E28.7.2");var subQ56=sQuery(id+"F3.wireOp",EDGE,"E20.15.3");var subQ57=sQuery(id+"F3.wireOp",EDGE,"E20.15.1");var subQ58=sQuery(id+"F3.wireOp",EDGE,"E20.15.0");var subQ60=sQuery(id+"F22.wireOp",EDGE,"E28.6.3");var subQ61=sQuery(id+"F22.wireOp",EDGE,"E28.6.2");var subQ62=sQuery(id+"F3.wireOp",EDGE,"E20.14.3");var subQ64=sQuery(id+"F3.wireOp",EDGE,"E20.14.1");var subQ65=sQuery(id+"F3.wireOp",EDGE,"E20.14.0");var subQ66=sQuery(id+"F22.wireOp",EDGE,"E28.5.3");var subQ67=sQuery(id+"F22.wireOp",EDGE,"E28.5.2");var subQ68=sQuery(id+"F3.wireOp",EDGE,"E20.13.3");var subQ70=sQuery(id+"F3.wireOp",EDGE,"E20.13.1");var subQ71=sQuery(id+"F3.wireOp",EDGE,"E20.13.0");var subQ72=sQuery(id+"F22.wireOp",EDGE,"E28.4.3");var subQ73=sQuery(id+"F22.wireOp",EDGE,"E28.4.2");var subQ74=sQuery(id+"F3.wireOp",EDGE,"E20.12.3");var subQ76=sQuery(id+"F3.wireOp",EDGE,"E20.12.1");var subQ77=sQuery(id+"F3.wireOp",EDGE,"E20.12.0");var subQ78=sQuery(id+"F22.wireOp",EDGE,"E28.3.3");var subQ79=sQuery(id+"F22.wireOp",EDGE,"E28.3.2");var subQ80=sQuery(id+"F3.wireOp",EDGE,"E20.11.3");var subQ82=sQuery(id+"F3.wireOp",EDGE,"E20.11.1");var subQ83=sQuery(id+"F3.wireOp",EDGE,"E20.11.0");var subQ84=sQuery(id+"F22.wireOp",EDGE,"E28.2.3");var subQ85=sQuery(id+"F22.wireOp",EDGE,"E28.2.2");var subQ86=sQuery(id+"F3.wireOp",EDGE,"E20.10.3");var subQ87=sQuery(id+"F3.wireOp",EDGE,"E20.10.1");var subQ88=sQuery(id+"F3.wireOp",EDGE,"E20.10.0");var subQ89=makeQuery(id+"F25.opLoft","SWEPT_FACE",FACE,{"disambiguationData":[OSD([subQ88,subQ87,subQ86,sQuery(id+"F22.wireOp",EDGE,"E28.2.1"),subQ85,subQ84])]});var subQ92=sQuery(id+"F22.wireOp",EDGE,"E28.1.3");var subQ93=sQuery(id+"F22.wireOp",EDGE,"E28.1.2");var subQ94=sQuery(id+"F3.wireOp",EDGE,"E20.9.3");var subQ95=sQuery(id+"F3.wireOp",EDGE,"E20.9.1");var subQ96=sQuery(id+"F3.wireOp",EDGE,"E20.9.0");var subQ97=makeQuery(id+"F24.opLoft","SWEPT_FACE",FACE,{"disambiguationData":[OSD([subQ96,subQ95,subQ94,sQuery(id+"F22.wireOp",EDGE,"E28.1.1"),subQ93,subQ92])]});var subQ98=sQuery(id+"F22.wireOp",EDGE,"E27.top");var subQ99=sQuery(id+"F22.wireOp",EDGE,"E27.bottom");var subQ100=sQuery(id+"F3.wireOp",EDGE,"E20.8.3");var subQ102=sQuery(id+"F3.wireOp",EDGE,"E20.8.1");var subQ106=makeQuery(id+"F42.boolean.opBoolean","COPY",FACE,{"disambiguationData":[TD([subQ89])],"derivedFrom":subQ10});var subQ135=makeQuery(id+"F25.boolean.opBoolean","INTERSECT",EDGE,{"derivedFrom":[makeQuery(id+"F24.boolean.opBoolean","SPLIT",FACE,{"disambiguationData":[TD([makeQuery(id+"F5.opLoft","CAP_FACE",FACE,{"disambiguationData":[OSD([makeQuery(id+"F3.imprint","IMPRINT",FACE,{"disambiguationData":[TD([[makeQuery(id+"F3.imprint","IMPRINT",EDGE,{"derivedFrom":subQ52}),1.0]])]})])],"isStart":true})])],"derivedFrom":makeQuery(id+"F1.opRevolve","SWEPT_FACE",FACE,{"disambiguationData":[OSD([sQuery(id+"F0.wireOp",EDGE,"E13")])]})}),subQ89]});Q35=makeQuery(id+"F48.opFillet","BLEND_EDGE",EDGE,{"blendedFrom":[makeQuery(id+"F47.opFillet","TWEAK_EDGE",EDGE,{"derivedFrom":[makeQuery(id+"F45.opFillet","BLEND_VERTEX",VERTEX,{"blendedFrom":[subQ135,subQ89,subQ106],"blendedInto":[subQ89,subQ106]}),makeQuery(id+"F45.opFillet","BLEND_VERTEX",VERTEX,{"blendedFrom":[subQ135,makeQuery(id+"F42.boolean.opBoolean","MERGE",FACE,{"derivedFrom":[subQ2,subQ1]}),subQ106],"blendedInto":[makeQuery(id+"F42.boolean.opBoolean","MERGE",FACE,{"derivedFrom":[subQ2,subQ1]}),subQ106]})]}),makeQuery(id+"F47.opFillet","BLEND_FACE",FACE,{"disambiguationData":[OSD([subQ0,subQ9]),TDD([makeQuery(id+"F42.boolean.opBoolean","COPY",EDGE,{"disambiguationData":[TD([makeQuery(id+"F23.opLoft","SWEPT_FACE",FACE,{"disambiguationData":[OSD([sQuery(id+"F3.wireOp",EDGE,"E20.8.0"),subQ102,subQ100,subQ99,subQ98,sQuery(id+"F22.wireOp",EDGE,"E27.right")])]})])],"derivedFrom":subQ11})])]}),makeQuery(id+"F47.opFillet","BLEND_FACE",FACE,{"disambiguationData":[OSD([subQ0,subQ9]),TDD([makeQuery(id+"F42.boolean.opBoolean","COPY",EDGE,{"disambiguationData":[TD([subQ97])],"derivedFrom":subQ11})])]}),makeQuery(id+"F47.opFillet","BLEND_FACE",FACE,{"disambiguationData":[OSD([subQ0,subQ9]),TDD([makeQuery(id+"F42.boolean.opBoolean","COPY",EDGE,{"disambiguationData":[TD([subQ89])],"derivedFrom":subQ11})])]}),makeQuery(id+"F47.opFillet","BLEND_FACE",FACE,{"disambiguationData":[OSD([subQ0,subQ9]),TDD([makeQuery(id+"F42.boolean.opBoolean","COPY",EDGE,{"disambiguationData":[TD([makeQuery(id+"F26.opLoft","SWEPT_FACE",FACE,{"disambiguationData":[OSD([subQ83,subQ82,subQ80,sQuery(id+"F22.wireOp",EDGE,"E28.3.1"),subQ79,subQ78])]})])],"derivedFrom":subQ11})])]}),makeQuery(id+"F47.opFillet","BLEND_FACE",FACE,{"disambiguationData":[OSD([subQ0,subQ9]),TDD([makeQuery(id+"F42.boolean.opBoolean","COPY",EDGE,{"disambiguationData":[TD([makeQuery(id+"F27.opLoft","SWEPT_FACE",FACE,{"disambiguationData":[OSD([subQ77,subQ76,subQ74,sQuery(id+"F22.wireOp",EDGE,"E28.4.1"),subQ73,subQ72])]})])],"derivedFrom":subQ11})])]}),makeQuery(id+"F47.opFillet","BLEND_FACE",FACE,{"disambiguationData":[OSD([subQ0,subQ9]),TDD([makeQuery(id+"F42.boolean.opBoolean","COPY",EDGE,{"disambiguationData":[TD([makeQuery(id+"F28.opLoft","SWEPT_FACE",FACE,{"disambiguationData":[OSD([subQ71,subQ70,subQ68,sQuery(id+"F22.wireOp",EDGE,"E28.5.1"),subQ67,subQ66])]})])],"derivedFrom":subQ11})])]}),makeQuery(id+"F47.opFillet","BLEND_FACE",FACE,{"disambiguationData":[OSD([subQ0,subQ9]),TDD([makeQuery(id+"F42.boolean.opBoolean","COPY",EDGE,{"disambiguationData":[TD([makeQuery(id+"F29.opLoft","SWEPT_FACE",FACE,{"disambiguationData":[OSD([subQ65,subQ64,subQ62,sQuery(id+"F22.wireOp",EDGE,"E28.6.1"),subQ61,subQ60])]})])],"derivedFrom":subQ11})])]}),makeQuery(id+"F47.opFillet","BLEND_FACE",FACE,{"disambiguationData":[OSD([subQ0,subQ9]),TDD([makeQuery(id+"F42.boolean.opBoolean","COPY",EDGE,{"disambiguationData":[TD([makeQuery(id+"F30.opLoft","SWEPT_FACE",FACE,{"disambiguationData":[OSD([subQ58,subQ57,subQ56,sQuery(id+"F22.wireOp",EDGE,"E28.7.1"),subQ55,subQ54])]})])],"derivedFrom":subQ11})])]}),makeQuery(id+"F47.opFillet","BLEND_FACE",FACE,{"disambiguationData":[OSD([subQ0,subQ9]),TDD([makeQuery(id+"F42.boolean.opBoolean","COPY",EDGE,{"disambiguationData":[TD([makeQuery(id+"F31.opLoft","SWEPT_FACE",FACE,{"disambiguationData":[OSD([subQ52,subQ51,subQ53,sQuery(id+"F22.wireOp",EDGE,"E28.8.1"),subQ49,subQ48])]})])],"derivedFrom":subQ11})])]}),makeQuery(id+"F47.opFillet","BLEND_FACE",FACE,{"disambiguationData":[OSD([subQ0,subQ9]),TDD([makeQuery(id+"F42.boolean.opBoolean","COPY",EDGE,{"disambiguationData":[TD([makeQuery(id+"F32.opLoft","SWEPT_FACE",FACE,{"disambiguationData":[OSD([subQ47,subQ46,subQ44,sQuery(id+"F22.wireOp",EDGE,"E28.9.1"),subQ43,subQ42])]})])],"derivedFrom":subQ11})])]}),makeQuery(id+"F47.opFillet","BLEND_FACE",FACE,{"disambiguationData":[OSD([subQ0,subQ9]),TDD([makeQuery(id+"F42.boolean.opBoolean","COPY",EDGE,{"disambiguationData":[TD([makeQuery(id+"F33.opLoft","SWEPT_FACE",FACE,{"disambiguationData":[OSD([subQ41,subQ40,subQ38,sQuery(id+"F22.wireOp",EDGE,"E28.10.1"),subQ37,subQ36])]})])],"derivedFrom":subQ11})])]}),makeQuery(id+"F47.opFillet","BLEND_FACE",FACE,{"disambiguationData":[OSD([subQ0,subQ9]),TDD([makeQuery(id+"F42.boolean.opBoolean","COPY",EDGE,{"disambiguationData":[TD([makeQuery(id+"F34.opLoft","SWEPT_FACE",FACE,{"disambiguationData":[OSD([subQ35,subQ34,subQ32,sQuery(id+"F22.wireOp",EDGE,"E28.11.1"),subQ31,subQ30])]})])],"derivedFrom":subQ11})])]}),makeQuery(id+"F47.opFillet","BLEND_FACE",FACE,{"disambiguationData":[OSD([subQ0,subQ9]),TDD([makeQuery(id+"F42.boolean.opBoolean","COPY",EDGE,{"disambiguationData":[TD([makeQuery(id+"F35.opLoft","SWEPT_FACE",FACE,{"disambiguationData":[OSD([subQ29,subQ28,subQ26,sQuery(id+"F22.wireOp",EDGE,"E28.12.1"),subQ25,subQ24])]})])],"derivedFrom":subQ11})])]}),makeQuery(id+"F47.opFillet","BLEND_FACE",FACE,{"disambiguationData":[OSD([subQ0,subQ9]),TDD([makeQuery(id+"F42.boolean.opBoolean","COPY",EDGE,{"disambiguationData":[TD([makeQuery(id+"F36.opLoft","SWEPT_FACE",FACE,{"disambiguationData":[OSD([subQ23,subQ22,subQ20,sQuery(id+"F22.wireOp",EDGE,"E28.13.1"),subQ19,subQ18])]})])],"derivedFrom":subQ11})])]}),makeQuery(id+"F47.opFillet","BLEND_FACE",FACE,{"disambiguationData":[OSD([subQ0,subQ9]),TDD([makeQuery(id+"F42.boolean.opBoolean","COPY",EDGE,{"disambiguationData":[TD([makeQuery(id+"F37.opLoft","SWEPT_FACE",FACE,{"disambiguationData":[OSD([subQ16,subQ15,subQ14,sQuery(id+"F22.wireOp",EDGE,"E28.14.1"),subQ13,subQ12])]})])],"derivedFrom":subQ11})])]}),makeQuery(id+"F47.opFillet","BLEND_FACE",FACE,{"disambiguationData":[OSD([subQ0,subQ9]),TDD([makeQuery(id+"F42.boolean.opBoolean","COPY",EDGE,{"disambiguationData":[TD([makeQuery(id+"F38.opLoft","SWEPT_FACE",FACE,{"disambiguationData":[OSD([subQ8,subQ7,subQ5,sQuery(id+"F22.wireOp",EDGE,"E28.15.1"),subQ4,subQ3])]})])],"derivedFrom":subQ11})])]})],"blendedInto":[makeQuery(id+"F47.opFillet","BLEND_FACE",FACE,{"disambiguationData":[OSD([subQ0,subQ9]),TDD([makeQuery(id+"F42.boolean.opBoolean","COPY",EDGE,{"disambiguationData":[TD([makeQuery(id+"F23.opLoft","SWEPT_FACE",FACE,{"disambiguationData":[OSD([sQuery(id+"F3.wireOp",EDGE,"E20.8.0"),subQ102,subQ100,subQ99,subQ98,sQuery(id+"F22.wireOp",EDGE,"E27.right")])]})])],"derivedFrom":subQ11})])]}),makeQuery(id+"F47.opFillet","BLEND_FACE",FACE,{"disambiguationData":[OSD([subQ0,subQ9]),TDD([makeQuery(id+"F42.boolean.opBoolean","COPY",EDGE,{"disambiguationData":[TD([subQ97])],"derivedFrom":subQ11})])]}),makeQuery(id+"F47.opFillet","BLEND_FACE",FACE,{"disambiguationData":[OSD([subQ0,subQ9]),TDD([makeQuery(id+"F42.boolean.opBoolean","COPY",EDGE,{"disambiguationData":[TD([subQ89])],"derivedFrom":subQ11})])]}),makeQuery(id+"F47.opFillet","BLEND_FACE",FACE,{"disambiguationData":[OSD([subQ0,subQ9]),TDD([makeQuery(id+"F42.boolean.opBoolean","COPY",EDGE,{"disambiguationData":[TD([makeQuery(id+"F26.opLoft","SWEPT_FACE",FACE,{"disambiguationData":[OSD([subQ83,subQ82,subQ80,sQuery(id+"F22.wireOp",EDGE,"E28.3.1"),subQ79,subQ78])]})])],"derivedFrom":subQ11})])]}),makeQuery(id+"F47.opFillet","BLEND_FACE",FACE,{"disambiguationData":[OSD([subQ0,subQ9]),TDD([makeQuery(id+"F42.boolean.opBoolean","COPY",EDGE,{"disambiguationData":[TD([makeQuery(id+"F27.opLoft","SWEPT_FACE",FACE,{"disambiguationData":[OSD([subQ77,subQ76,subQ74,sQuery(id+"F22.wireOp",EDGE,"E28.4.1"),subQ73,subQ72])]})])],"derivedFrom":subQ11})])]}),makeQuery(id+"F47.opFillet","BLEND_FACE",FACE,{"disambiguationData":[OSD([subQ0,subQ9]),TDD([makeQuery(id+"F42.boolean.opBoolean","COPY",EDGE,{"disambiguationData":[TD([makeQuery(id+"F28.opLoft","SWEPT_FACE",FACE,{"disambiguationData":[OSD([subQ71,subQ70,subQ68,sQuery(id+"F22.wireOp",EDGE,"E28.5.1"),subQ67,subQ66])]})])],"derivedFrom":subQ11})])]}),makeQuery(id+"F47.opFillet","BLEND_FACE",FACE,{"disambiguationData":[OSD([subQ0,subQ9]),TDD([makeQuery(id+"F42.boolean.opBoolean","COPY",EDGE,{"disambiguationData":[TD([makeQuery(id+"F29.opLoft","SWEPT_FACE",FACE,{"disambiguationData":[OSD([subQ65,subQ64,subQ62,sQuery(id+"F22.wireOp",EDGE,"E28.6.1"),subQ61,subQ60])]})])],"derivedFrom":subQ11})])]}),makeQuery(id+"F47.opFillet","BLEND_FACE",FACE,{"disambiguationData":[OSD([subQ0,subQ9]),TDD([makeQuery(id+"F42.boolean.opBoolean","COPY",EDGE,{"disambiguationData":[TD([makeQuery(id+"F30.opLoft","SWEPT_FACE",FACE,{"disambiguationData":[OSD([subQ58,subQ57,subQ56,sQuery(id+"F22.wireOp",EDGE,"E28.7.1"),subQ55,subQ54])]})])],"derivedFrom":subQ11})])]}),makeQuery(id+"F47.opFillet","BLEND_FACE",FACE,{"disambiguationData":[OSD([subQ0,subQ9]),TDD([makeQuery(id+"F42.boolean.opBoolean","COPY",EDGE,{"disambiguationData":[TD([makeQuery(id+"F31.opLoft","SWEPT_FACE",FACE,{"disambiguationData":[OSD([subQ52,subQ51,subQ53,sQuery(id+"F22.wireOp",EDGE,"E28.8.1"),subQ49,subQ48])]})])],"derivedFrom":subQ11})])]}),makeQuery(id+"F47.opFillet","BLEND_FACE",FACE,{"disambiguationData":[OSD([subQ0,subQ9]),TDD([makeQuery(id+"F42.boolean.opBoolean","COPY",EDGE,{"disambiguationData":[TD([makeQuery(id+"F32.opLoft","SWEPT_FACE",FACE,{"disambiguationData":[OSD([subQ47,subQ46,subQ44,sQuery(id+"F22.wireOp",EDGE,"E28.9.1"),subQ43,subQ42])]})])],"derivedFrom":subQ11})])]}),makeQuery(id+"F47.opFillet","BLEND_FACE",FACE,{"disambiguationData":[OSD([subQ0,subQ9]),TDD([makeQuery(id+"F42.boolean.opBoolean","COPY",EDGE,{"disambiguationData":[TD([makeQuery(id+"F33.opLoft","SWEPT_FACE",FACE,{"disambiguationData":[OSD([subQ41,subQ40,subQ38,sQuery(id+"F22.wireOp",EDGE,"E28.10.1"),subQ37,subQ36])]})])],"derivedFrom":subQ11})])]}),makeQuery(id+"F47.opFillet","BLEND_FACE",FACE,{"disambiguationData":[OSD([subQ0,subQ9]),TDD([makeQuery(id+"F42.boolean.opBoolean","COPY",EDGE,{"disambiguationData":[TD([makeQuery(id+"F34.opLoft","SWEPT_FACE",FACE,{"disambiguationData":[OSD([subQ35,subQ34,subQ32,sQuery(id+"F22.wireOp",EDGE,"E28.11.1"),subQ31,subQ30])]})])],"derivedFrom":subQ11})])]}),makeQuery(id+"F47.opFillet","BLEND_FACE",FACE,{"disambiguationData":[OSD([subQ0,subQ9]),TDD([makeQuery(id+"F42.boolean.opBoolean","COPY",EDGE,{"disambiguationData":[TD([makeQuery(id+"F35.opLoft","SWEPT_FACE",FACE,{"disambiguationData":[OSD([subQ29,subQ28,subQ26,sQuery(id+"F22.wireOp",EDGE,"E28.12.1"),subQ25,subQ24])]})])],"derivedFrom":subQ11})])]}),makeQuery(id+"F47.opFillet","BLEND_FACE",FACE,{"disambiguationData":[OSD([subQ0,subQ9]),TDD([makeQuery(id+"F42.boolean.opBoolean","COPY",EDGE,{"disambiguationData":[TD([makeQuery(id+"F36.opLoft","SWEPT_FACE",FACE,{"disambiguationData":[OSD([subQ23,subQ22,subQ20,sQuery(id+"F22.wireOp",EDGE,"E28.13.1"),subQ19,subQ18])]})])],"derivedFrom":subQ11})])]}),makeQuery(id+"F47.opFillet","BLEND_FACE",FACE,{"disambiguationData":[OSD([subQ0,subQ9]),TDD([makeQuery(id+"F42.boolean.opBoolean","COPY",EDGE,{"disambiguationData":[TD([makeQuery(id+"F37.opLoft","SWEPT_FACE",FACE,{"disambiguationData":[OSD([subQ16,subQ15,subQ14,sQuery(id+"F22.wireOp",EDGE,"E28.14.1"),subQ13,subQ12])]})])],"derivedFrom":subQ11})])]}),makeQuery(id+"F47.opFillet","BLEND_FACE",FACE,{"disambiguationData":[OSD([subQ0,subQ9]),TDD([makeQuery(id+"F42.boolean.opBoolean","COPY",EDGE,{"disambiguationData":[TD([makeQuery(id+"F38.opLoft","SWEPT_FACE",FACE,{"disambiguationData":[OSD([subQ8,subQ7,subQ5,sQuery(id+"F22.wireOp",EDGE,"E28.15.1"),subQ4,subQ3])]})])],"derivedFrom":subQ11})])]})]});}
            var Q36;
            {var subQ0=sQuery(id+"F22.wireOp",EDGE,"E28.2.3");var subQ1=sQuery(id+"F22.wireOp",EDGE,"E28.2.2");var subQ2=sQuery(id+"F22.wireOp",EDGE,"E28.2.1");var subQ3=sQuery(id+"F3.wireOp",EDGE,"E20.10.3");var subQ4=sQuery(id+"F3.wireOp",EDGE,"E20.10.1");var subQ5=sQuery(id+"F22.wireOp",EDGE,"E28.2.0");var subQ6=makeQuery(id+"F25.opLoft","SWEPT_FACE",FACE,{"disambiguationData":[OSD([subQ4,sQuery(id+"F3.wireOp",EDGE,"E20.10.2"),subQ3,subQ5,subQ1,subQ0])]});var subQ7=sQuery(id+"F41.wireOp",EDGE,"E34");var subQ8=sQuery(id+"F41.wireOp",EDGE,"E32");Q36=makeQuery(id+"F44.opFillet","BLEND_EDGE",EDGE,{"blendedFrom":[makeQuery(id+"F40.boolean.opBoolean","INTERSECT",EDGE,{"derivedFrom":[subQ6,makeQuery(id+"F40.opExtrude","CAP_FACE",FACE,{"disambiguationData":[OSD([sQuery(id+"F39.wireOp",EDGE,"E29"),sQuery(id+"F39.wireOp",EDGE,"E30")])],"isStart":true})]}),makeQuery(id+"F42.boolean.opBoolean","COPY",FACE,{"disambiguationData":[TD([makeQuery(id+"F25.opLoft","SWEPT_FACE",FACE,{"disambiguationData":[OSD([sQuery(id+"F3.wireOp",EDGE,"E20.10.0"),subQ4,subQ3,subQ2,subQ1,subQ0])]})])],"derivedFrom":makeQuery(id+"F42.opRevolve","SWEPT_FACE",FACE,{"disambiguationData":[OSD([subQ8]),TDD([makeQuery(id+"F41.imprint","IMPRINT",EDGE,{"disambiguationData":[TD([[makeQuery(id+"F41.imprint","INTERSECT",VERTEX,{"disambiguationData":[OD(0.0)],"derivedFrom":[subQ8,subQ7]}),-1.0]])],"derivedFrom":subQ8})])]})})],"blendedInto":[makeQuery(id+"F42.boolean.opBoolean","COPY",FACE,{"disambiguationData":[TD([makeQuery(id+"F25.opLoft","SWEPT_FACE",FACE,{"disambiguationData":[OSD([sQuery(id+"F3.wireOp",EDGE,"E20.10.0"),subQ4,subQ3,subQ2,subQ1,subQ0])]})])],"derivedFrom":makeQuery(id+"F42.opRevolve","SWEPT_FACE",FACE,{"disambiguationData":[OSD([subQ8]),TDD([makeQuery(id+"F41.imprint","IMPRINT",EDGE,{"disambiguationData":[TD([[makeQuery(id+"F41.imprint","INTERSECT",VERTEX,{"disambiguationData":[OD(0.0)],"derivedFrom":[subQ8,subQ7]}),-1.0]])],"derivedFrom":subQ8})])]})})]});}
            var Q37;
            {var subQ0=sQuery(id+"F41.wireOp",EDGE,"E34");var subQ1=sQuery(id+"F41.wireOp",EDGE,"E32");Q37=makeQuery(id+"F42.boolean.opBoolean","INTERSECT",EDGE,{"derivedFrom":[makeQuery(id+"F24.opLoft","SWEPT_FACE",FACE,{"disambiguationData":[OSD([sQuery(id+"F3.wireOp",EDGE,"E20.9.0"),sQuery(id+"F3.wireOp",EDGE,"E20.9.1"),sQuery(id+"F3.wireOp",EDGE,"E20.9.3"),sQuery(id+"F22.wireOp",EDGE,"E28.1.1"),sQuery(id+"F22.wireOp",EDGE,"E28.1.2"),sQuery(id+"F22.wireOp",EDGE,"E28.1.3")])]}),makeQuery(id+"F42.opRevolve","SWEPT_FACE",FACE,{"disambiguationData":[OSD([subQ1]),TDD([makeQuery(id+"F41.imprint","IMPRINT",EDGE,{"disambiguationData":[TD([[makeQuery(id+"F41.imprint","INTERSECT",VERTEX,{"disambiguationData":[OD(0.0)],"derivedFrom":[subQ1,subQ0]}),-1.0]])],"derivedFrom":subQ1})])]})]});}
            var Q38;
            {var subQ0=sQuery(id+"F41.wireOp",EDGE,"E37");var subQ1=makeQuery(id+"F42.opRevolve","SWEPT_FACE",FACE,{"disambiguationData":[OSD([subQ0])]});var subQ2=makeQuery(id+"F40.opExtrude","CAP_FACE",FACE,{"disambiguationData":[OSD([sQuery(id+"F39.wireOp",EDGE,"E29"),sQuery(id+"F39.wireOp",EDGE,"E30")])],"isStart":true});var subQ3=sQuery(id+"F22.wireOp",EDGE,"E28.15.3");var subQ4=sQuery(id+"F22.wireOp",EDGE,"E28.15.2");var subQ5=sQuery(id+"F3.wireOp",EDGE,"E20.7.3");var subQ6=sQuery(id+"F3.wireOp",EDGE,"E20.7.1");var subQ7=sQuery(id+"F41.wireOp",EDGE,"E38");var subQ8=makeQuery(id+"F42.opRevolve","SWEPT_FACE",FACE,{"disambiguationData":[OSD([subQ7])]});var subQ9=makeQuery(id+"F42.opRevolve","SWEPT_EDGE",EDGE,{"disambiguationData":[OSD([subQ0,subQ7])]});var subQ10=sQuery(id+"F22.wireOp",EDGE,"E28.14.3");var subQ11=sQuery(id+"F22.wireOp",EDGE,"E28.14.2");var subQ12=sQuery(id+"F3.wireOp",EDGE,"E20.6.3");var subQ13=sQuery(id+"F3.wireOp",EDGE,"E20.6.1");var subQ14=sQuery(id+"F22.wireOp",EDGE,"E28.13.3");var subQ15=sQuery(id+"F22.wireOp",EDGE,"E28.13.2");var subQ16=sQuery(id+"F3.wireOp",EDGE,"E20.5.3");var subQ17=sQuery(id+"F3.wireOp",EDGE,"E20.5.1");var subQ18=sQuery(id+"F22.wireOp",EDGE,"E28.12.3");var subQ19=sQuery(id+"F22.wireOp",EDGE,"E28.12.2");var subQ20=sQuery(id+"F3.wireOp",EDGE,"E20.4.3");var subQ21=sQuery(id+"F3.wireOp",EDGE,"E20.4.1");var subQ22=sQuery(id+"F22.wireOp",EDGE,"E28.11.3");var subQ23=sQuery(id+"F22.wireOp",EDGE,"E28.11.2");var subQ24=sQuery(id+"F3.wireOp",EDGE,"E20.3.3");var subQ25=sQuery(id+"F3.wireOp",EDGE,"E20.3.1");var subQ26=sQuery(id+"F22.wireOp",EDGE,"E28.10.3");var subQ27=sQuery(id+"F22.wireOp",EDGE,"E28.10.2");var subQ28=sQuery(id+"F3.wireOp",EDGE,"E20.2.3");var subQ29=sQuery(id+"F3.wireOp",EDGE,"E20.2.1");var subQ30=sQuery(id+"F22.wireOp",EDGE,"E28.9.3");var subQ31=sQuery(id+"F22.wireOp",EDGE,"E28.9.2");var subQ32=sQuery(id+"F3.wireOp",EDGE,"E20.1.3");var subQ33=sQuery(id+"F3.wireOp",EDGE,"E20.1.1");var subQ34=sQuery(id+"F22.wireOp",EDGE,"E28.8.3");var subQ35=sQuery(id+"F22.wireOp",EDGE,"E28.8.2");var subQ36=sQuery(id+"F3.wireOp",EDGE,"E18.top");var subQ37=sQuery(id+"F3.wireOp",EDGE,"E18.bottom");var subQ38=sQuery(id+"F22.wireOp",EDGE,"E28.7.3");var subQ39=sQuery(id+"F22.wireOp",EDGE,"E28.7.2");var subQ40=sQuery(id+"F3.wireOp",EDGE,"E20.15.3");var subQ41=sQuery(id+"F3.wireOp",EDGE,"E20.15.1");var subQ42=sQuery(id+"F22.wireOp",EDGE,"E28.6.3");var subQ43=sQuery(id+"F22.wireOp",EDGE,"E28.6.2");var subQ44=sQuery(id+"F3.wireOp",EDGE,"E20.14.3");var subQ45=sQuery(id+"F3.wireOp",EDGE,"E20.14.1");var subQ46=sQuery(id+"F22.wireOp",EDGE,"E28.5.3");var subQ47=sQuery(id+"F22.wireOp",EDGE,"E28.5.2");var subQ48=sQuery(id+"F3.wireOp",EDGE,"E20.13.3");var subQ49=sQuery(id+"F3.wireOp",EDGE,"E20.13.1");var subQ50=sQuery(id+"F22.wireOp",EDGE,"E28.4.3");var subQ51=sQuery(id+"F22.wireOp",EDGE,"E28.4.2");var subQ52=sQuery(id+"F3.wireOp",EDGE,"E20.12.3");var subQ53=sQuery(id+"F3.wireOp",EDGE,"E20.12.1");var subQ54=sQuery(id+"F22.wireOp",EDGE,"E28.3.3");var subQ55=sQuery(id+"F22.wireOp",EDGE,"E28.3.2");var subQ56=sQuery(id+"F3.wireOp",EDGE,"E20.11.3");var subQ57=sQuery(id+"F3.wireOp",EDGE,"E20.11.1");var subQ58=sQuery(id+"F22.wireOp",EDGE,"E28.2.3");var subQ59=sQuery(id+"F22.wireOp",EDGE,"E28.2.2");var subQ60=sQuery(id+"F3.wireOp",EDGE,"E20.10.3");var subQ61=sQuery(id+"F3.wireOp",EDGE,"E20.10.1");var subQ62=sQuery(id+"F22.wireOp",EDGE,"E28.1.3");var subQ63=sQuery(id+"F22.wireOp",EDGE,"E28.1.2");var subQ64=sQuery(id+"F3.wireOp",EDGE,"E20.9.3");var subQ65=sQuery(id+"F3.wireOp",EDGE,"E20.9.1");var subQ67=makeQuery(id+"F24.opLoft","SWEPT_FACE",FACE,{"disambiguationData":[OSD([sQuery(id+"F3.wireOp",EDGE,"E20.9.0"),subQ65,subQ64,sQuery(id+"F22.wireOp",EDGE,"E28.1.1"),subQ63,subQ62])]});var subQ68=sQuery(id+"F22.wireOp",EDGE,"E27.top");var subQ69=sQuery(id+"F22.wireOp",EDGE,"E27.bottom");var subQ70=sQuery(id+"F3.wireOp",EDGE,"E20.8.3");var subQ71=sQuery(id+"F3.wireOp",EDGE,"E20.8.1");var subQ74=makeQuery(id+"F42.boolean.opBoolean","COPY",FACE,{"disambiguationData":[TD([subQ67])],"derivedFrom":subQ8});var subQ75=makeQuery(id+"F24.boolean.opBoolean","INTERSECT",EDGE,{"derivedFrom":[makeQuery(id+"F1.opRevolve","SWEPT_FACE",FACE,{"disambiguationData":[OSD([sQuery(id+"F0.wireOp",EDGE,"E13")])]}),subQ67]});Q38=makeQuery(id+"F48.opFillet","BLEND_EDGE",EDGE,{"blendedFrom":[makeQuery(id+"F47.opFillet","TWEAK_EDGE",EDGE,{"derivedFrom":[makeQuery(id+"F45.opFillet","BLEND_VERTEX",VERTEX,{"blendedFrom":[subQ75,subQ67,subQ74],"blendedInto":[subQ67,subQ74]}),makeQuery(id+"F45.opFillet","BLEND_VERTEX",VERTEX,{"blendedFrom":[subQ75,makeQuery(id+"F42.boolean.opBoolean","MERGE",FACE,{"derivedFrom":[subQ2,subQ1]}),subQ74],"blendedInto":[makeQuery(id+"F42.boolean.opBoolean","MERGE",FACE,{"derivedFrom":[subQ2,subQ1]}),subQ74]})]}),makeQuery(id+"F47.opFillet","BLEND_FACE",FACE,{"disambiguationData":[OSD([subQ0,subQ7]),TDD([makeQuery(id+"F42.boolean.opBoolean","COPY",EDGE,{"disambiguationData":[TD([makeQuery(id+"F23.opLoft","SWEPT_FACE",FACE,{"disambiguationData":[OSD([sQuery(id+"F3.wireOp",EDGE,"E20.8.0"),subQ71,subQ70,subQ69,subQ68,sQuery(id+"F22.wireOp",EDGE,"E27.right")])]})])],"derivedFrom":subQ9})])]}),makeQuery(id+"F47.opFillet","BLEND_FACE",FACE,{"disambiguationData":[OSD([subQ0,subQ7]),TDD([makeQuery(id+"F42.boolean.opBoolean","COPY",EDGE,{"disambiguationData":[TD([subQ67])],"derivedFrom":subQ9})])]}),makeQuery(id+"F47.opFillet","BLEND_FACE",FACE,{"disambiguationData":[OSD([subQ0,subQ7]),TDD([makeQuery(id+"F42.boolean.opBoolean","COPY",EDGE,{"disambiguationData":[TD([makeQuery(id+"F25.opLoft","SWEPT_FACE",FACE,{"disambiguationData":[OSD([sQuery(id+"F3.wireOp",EDGE,"E20.10.0"),subQ61,subQ60,sQuery(id+"F22.wireOp",EDGE,"E28.2.1"),subQ59,subQ58])]})])],"derivedFrom":subQ9})])]}),makeQuery(id+"F47.opFillet","BLEND_FACE",FACE,{"disambiguationData":[OSD([subQ0,subQ7]),TDD([makeQuery(id+"F42.boolean.opBoolean","COPY",EDGE,{"disambiguationData":[TD([makeQuery(id+"F26.opLoft","SWEPT_FACE",FACE,{"disambiguationData":[OSD([sQuery(id+"F3.wireOp",EDGE,"E20.11.0"),subQ57,subQ56,sQuery(id+"F22.wireOp",EDGE,"E28.3.1"),subQ55,subQ54])]})])],"derivedFrom":subQ9})])]}),makeQuery(id+"F47.opFillet","BLEND_FACE",FACE,{"disambiguationData":[OSD([subQ0,subQ7]),TDD([makeQuery(id+"F42.boolean.opBoolean","COPY",EDGE,{"disambiguationData":[TD([makeQuery(id+"F27.opLoft","SWEPT_FACE",FACE,{"disambiguationData":[OSD([sQuery(id+"F3.wireOp",EDGE,"E20.12.0"),subQ53,subQ52,sQuery(id+"F22.wireOp",EDGE,"E28.4.1"),subQ51,subQ50])]})])],"derivedFrom":subQ9})])]}),makeQuery(id+"F47.opFillet","BLEND_FACE",FACE,{"disambiguationData":[OSD([subQ0,subQ7]),TDD([makeQuery(id+"F42.boolean.opBoolean","COPY",EDGE,{"disambiguationData":[TD([makeQuery(id+"F28.opLoft","SWEPT_FACE",FACE,{"disambiguationData":[OSD([sQuery(id+"F3.wireOp",EDGE,"E20.13.0"),subQ49,subQ48,sQuery(id+"F22.wireOp",EDGE,"E28.5.1"),subQ47,subQ46])]})])],"derivedFrom":subQ9})])]}),makeQuery(id+"F47.opFillet","BLEND_FACE",FACE,{"disambiguationData":[OSD([subQ0,subQ7]),TDD([makeQuery(id+"F42.boolean.opBoolean","COPY",EDGE,{"disambiguationData":[TD([makeQuery(id+"F29.opLoft","SWEPT_FACE",FACE,{"disambiguationData":[OSD([sQuery(id+"F3.wireOp",EDGE,"E20.14.0"),subQ45,subQ44,sQuery(id+"F22.wireOp",EDGE,"E28.6.1"),subQ43,subQ42])]})])],"derivedFrom":subQ9})])]}),makeQuery(id+"F47.opFillet","BLEND_FACE",FACE,{"disambiguationData":[OSD([subQ0,subQ7]),TDD([makeQuery(id+"F42.boolean.opBoolean","COPY",EDGE,{"disambiguationData":[TD([makeQuery(id+"F30.opLoft","SWEPT_FACE",FACE,{"disambiguationData":[OSD([sQuery(id+"F3.wireOp",EDGE,"E20.15.0"),subQ41,subQ40,sQuery(id+"F22.wireOp",EDGE,"E28.7.1"),subQ39,subQ38])]})])],"derivedFrom":subQ9})])]}),makeQuery(id+"F47.opFillet","BLEND_FACE",FACE,{"disambiguationData":[OSD([subQ0,subQ7]),TDD([makeQuery(id+"F42.boolean.opBoolean","COPY",EDGE,{"disambiguationData":[TD([makeQuery(id+"F31.opLoft","SWEPT_FACE",FACE,{"disambiguationData":[OSD([subQ37,subQ36,sQuery(id+"F3.wireOp",EDGE,"E18.left"),sQuery(id+"F22.wireOp",EDGE,"E28.8.1"),subQ35,subQ34])]})])],"derivedFrom":subQ9})])]}),makeQuery(id+"F47.opFillet","BLEND_FACE",FACE,{"disambiguationData":[OSD([subQ0,subQ7]),TDD([makeQuery(id+"F42.boolean.opBoolean","COPY",EDGE,{"disambiguationData":[TD([makeQuery(id+"F32.opLoft","SWEPT_FACE",FACE,{"disambiguationData":[OSD([sQuery(id+"F3.wireOp",EDGE,"E20.1.0"),subQ33,subQ32,sQuery(id+"F22.wireOp",EDGE,"E28.9.1"),subQ31,subQ30])]})])],"derivedFrom":subQ9})])]}),makeQuery(id+"F47.opFillet","BLEND_FACE",FACE,{"disambiguationData":[OSD([subQ0,subQ7]),TDD([makeQuery(id+"F42.boolean.opBoolean","COPY",EDGE,{"disambiguationData":[TD([makeQuery(id+"F33.opLoft","SWEPT_FACE",FACE,{"disambiguationData":[OSD([sQuery(id+"F3.wireOp",EDGE,"E20.2.0"),subQ29,subQ28,sQuery(id+"F22.wireOp",EDGE,"E28.10.1"),subQ27,subQ26])]})])],"derivedFrom":subQ9})])]}),makeQuery(id+"F47.opFillet","BLEND_FACE",FACE,{"disambiguationData":[OSD([subQ0,subQ7]),TDD([makeQuery(id+"F42.boolean.opBoolean","COPY",EDGE,{"disambiguationData":[TD([makeQuery(id+"F34.opLoft","SWEPT_FACE",FACE,{"disambiguationData":[OSD([sQuery(id+"F3.wireOp",EDGE,"E20.3.0"),subQ25,subQ24,sQuery(id+"F22.wireOp",EDGE,"E28.11.1"),subQ23,subQ22])]})])],"derivedFrom":subQ9})])]}),makeQuery(id+"F47.opFillet","BLEND_FACE",FACE,{"disambiguationData":[OSD([subQ0,subQ7]),TDD([makeQuery(id+"F42.boolean.opBoolean","COPY",EDGE,{"disambiguationData":[TD([makeQuery(id+"F35.opLoft","SWEPT_FACE",FACE,{"disambiguationData":[OSD([sQuery(id+"F3.wireOp",EDGE,"E20.4.0"),subQ21,subQ20,sQuery(id+"F22.wireOp",EDGE,"E28.12.1"),subQ19,subQ18])]})])],"derivedFrom":subQ9})])]}),makeQuery(id+"F47.opFillet","BLEND_FACE",FACE,{"disambiguationData":[OSD([subQ0,subQ7]),TDD([makeQuery(id+"F42.boolean.opBoolean","COPY",EDGE,{"disambiguationData":[TD([makeQuery(id+"F36.opLoft","SWEPT_FACE",FACE,{"disambiguationData":[OSD([sQuery(id+"F3.wireOp",EDGE,"E20.5.0"),subQ17,subQ16,sQuery(id+"F22.wireOp",EDGE,"E28.13.1"),subQ15,subQ14])]})])],"derivedFrom":subQ9})])]}),makeQuery(id+"F47.opFillet","BLEND_FACE",FACE,{"disambiguationData":[OSD([subQ0,subQ7]),TDD([makeQuery(id+"F42.boolean.opBoolean","COPY",EDGE,{"disambiguationData":[TD([makeQuery(id+"F37.opLoft","SWEPT_FACE",FACE,{"disambiguationData":[OSD([sQuery(id+"F3.wireOp",EDGE,"E20.6.0"),subQ13,subQ12,sQuery(id+"F22.wireOp",EDGE,"E28.14.1"),subQ11,subQ10])]})])],"derivedFrom":subQ9})])]}),makeQuery(id+"F47.opFillet","BLEND_FACE",FACE,{"disambiguationData":[OSD([subQ0,subQ7]),TDD([makeQuery(id+"F42.boolean.opBoolean","COPY",EDGE,{"disambiguationData":[TD([makeQuery(id+"F38.opLoft","SWEPT_FACE",FACE,{"disambiguationData":[OSD([sQuery(id+"F3.wireOp",EDGE,"E20.7.0"),subQ6,subQ5,sQuery(id+"F22.wireOp",EDGE,"E28.15.1"),subQ4,subQ3])]})])],"derivedFrom":subQ9})])]})],"blendedInto":[makeQuery(id+"F47.opFillet","BLEND_FACE",FACE,{"disambiguationData":[OSD([subQ0,subQ7]),TDD([makeQuery(id+"F42.boolean.opBoolean","COPY",EDGE,{"disambiguationData":[TD([makeQuery(id+"F23.opLoft","SWEPT_FACE",FACE,{"disambiguationData":[OSD([sQuery(id+"F3.wireOp",EDGE,"E20.8.0"),subQ71,subQ70,subQ69,subQ68,sQuery(id+"F22.wireOp",EDGE,"E27.right")])]})])],"derivedFrom":subQ9})])]}),makeQuery(id+"F47.opFillet","BLEND_FACE",FACE,{"disambiguationData":[OSD([subQ0,subQ7]),TDD([makeQuery(id+"F42.boolean.opBoolean","COPY",EDGE,{"disambiguationData":[TD([subQ67])],"derivedFrom":subQ9})])]}),makeQuery(id+"F47.opFillet","BLEND_FACE",FACE,{"disambiguationData":[OSD([subQ0,subQ7]),TDD([makeQuery(id+"F42.boolean.opBoolean","COPY",EDGE,{"disambiguationData":[TD([makeQuery(id+"F25.opLoft","SWEPT_FACE",FACE,{"disambiguationData":[OSD([sQuery(id+"F3.wireOp",EDGE,"E20.10.0"),subQ61,subQ60,sQuery(id+"F22.wireOp",EDGE,"E28.2.1"),subQ59,subQ58])]})])],"derivedFrom":subQ9})])]}),makeQuery(id+"F47.opFillet","BLEND_FACE",FACE,{"disambiguationData":[OSD([subQ0,subQ7]),TDD([makeQuery(id+"F42.boolean.opBoolean","COPY",EDGE,{"disambiguationData":[TD([makeQuery(id+"F26.opLoft","SWEPT_FACE",FACE,{"disambiguationData":[OSD([sQuery(id+"F3.wireOp",EDGE,"E20.11.0"),subQ57,subQ56,sQuery(id+"F22.wireOp",EDGE,"E28.3.1"),subQ55,subQ54])]})])],"derivedFrom":subQ9})])]}),makeQuery(id+"F47.opFillet","BLEND_FACE",FACE,{"disambiguationData":[OSD([subQ0,subQ7]),TDD([makeQuery(id+"F42.boolean.opBoolean","COPY",EDGE,{"disambiguationData":[TD([makeQuery(id+"F27.opLoft","SWEPT_FACE",FACE,{"disambiguationData":[OSD([sQuery(id+"F3.wireOp",EDGE,"E20.12.0"),subQ53,subQ52,sQuery(id+"F22.wireOp",EDGE,"E28.4.1"),subQ51,subQ50])]})])],"derivedFrom":subQ9})])]}),makeQuery(id+"F47.opFillet","BLEND_FACE",FACE,{"disambiguationData":[OSD([subQ0,subQ7]),TDD([makeQuery(id+"F42.boolean.opBoolean","COPY",EDGE,{"disambiguationData":[TD([makeQuery(id+"F28.opLoft","SWEPT_FACE",FACE,{"disambiguationData":[OSD([sQuery(id+"F3.wireOp",EDGE,"E20.13.0"),subQ49,subQ48,sQuery(id+"F22.wireOp",EDGE,"E28.5.1"),subQ47,subQ46])]})])],"derivedFrom":subQ9})])]}),makeQuery(id+"F47.opFillet","BLEND_FACE",FACE,{"disambiguationData":[OSD([subQ0,subQ7]),TDD([makeQuery(id+"F42.boolean.opBoolean","COPY",EDGE,{"disambiguationData":[TD([makeQuery(id+"F29.opLoft","SWEPT_FACE",FACE,{"disambiguationData":[OSD([sQuery(id+"F3.wireOp",EDGE,"E20.14.0"),subQ45,subQ44,sQuery(id+"F22.wireOp",EDGE,"E28.6.1"),subQ43,subQ42])]})])],"derivedFrom":subQ9})])]}),makeQuery(id+"F47.opFillet","BLEND_FACE",FACE,{"disambiguationData":[OSD([subQ0,subQ7]),TDD([makeQuery(id+"F42.boolean.opBoolean","COPY",EDGE,{"disambiguationData":[TD([makeQuery(id+"F30.opLoft","SWEPT_FACE",FACE,{"disambiguationData":[OSD([sQuery(id+"F3.wireOp",EDGE,"E20.15.0"),subQ41,subQ40,sQuery(id+"F22.wireOp",EDGE,"E28.7.1"),subQ39,subQ38])]})])],"derivedFrom":subQ9})])]}),makeQuery(id+"F47.opFillet","BLEND_FACE",FACE,{"disambiguationData":[OSD([subQ0,subQ7]),TDD([makeQuery(id+"F42.boolean.opBoolean","COPY",EDGE,{"disambiguationData":[TD([makeQuery(id+"F31.opLoft","SWEPT_FACE",FACE,{"disambiguationData":[OSD([subQ37,subQ36,sQuery(id+"F3.wireOp",EDGE,"E18.left"),sQuery(id+"F22.wireOp",EDGE,"E28.8.1"),subQ35,subQ34])]})])],"derivedFrom":subQ9})])]}),makeQuery(id+"F47.opFillet","BLEND_FACE",FACE,{"disambiguationData":[OSD([subQ0,subQ7]),TDD([makeQuery(id+"F42.boolean.opBoolean","COPY",EDGE,{"disambiguationData":[TD([makeQuery(id+"F32.opLoft","SWEPT_FACE",FACE,{"disambiguationData":[OSD([sQuery(id+"F3.wireOp",EDGE,"E20.1.0"),subQ33,subQ32,sQuery(id+"F22.wireOp",EDGE,"E28.9.1"),subQ31,subQ30])]})])],"derivedFrom":subQ9})])]}),makeQuery(id+"F47.opFillet","BLEND_FACE",FACE,{"disambiguationData":[OSD([subQ0,subQ7]),TDD([makeQuery(id+"F42.boolean.opBoolean","COPY",EDGE,{"disambiguationData":[TD([makeQuery(id+"F33.opLoft","SWEPT_FACE",FACE,{"disambiguationData":[OSD([sQuery(id+"F3.wireOp",EDGE,"E20.2.0"),subQ29,subQ28,sQuery(id+"F22.wireOp",EDGE,"E28.10.1"),subQ27,subQ26])]})])],"derivedFrom":subQ9})])]}),makeQuery(id+"F47.opFillet","BLEND_FACE",FACE,{"disambiguationData":[OSD([subQ0,subQ7]),TDD([makeQuery(id+"F42.boolean.opBoolean","COPY",EDGE,{"disambiguationData":[TD([makeQuery(id+"F34.opLoft","SWEPT_FACE",FACE,{"disambiguationData":[OSD([sQuery(id+"F3.wireOp",EDGE,"E20.3.0"),subQ25,subQ24,sQuery(id+"F22.wireOp",EDGE,"E28.11.1"),subQ23,subQ22])]})])],"derivedFrom":subQ9})])]}),makeQuery(id+"F47.opFillet","BLEND_FACE",FACE,{"disambiguationData":[OSD([subQ0,subQ7]),TDD([makeQuery(id+"F42.boolean.opBoolean","COPY",EDGE,{"disambiguationData":[TD([makeQuery(id+"F35.opLoft","SWEPT_FACE",FACE,{"disambiguationData":[OSD([sQuery(id+"F3.wireOp",EDGE,"E20.4.0"),subQ21,subQ20,sQuery(id+"F22.wireOp",EDGE,"E28.12.1"),subQ19,subQ18])]})])],"derivedFrom":subQ9})])]}),makeQuery(id+"F47.opFillet","BLEND_FACE",FACE,{"disambiguationData":[OSD([subQ0,subQ7]),TDD([makeQuery(id+"F42.boolean.opBoolean","COPY",EDGE,{"disambiguationData":[TD([makeQuery(id+"F36.opLoft","SWEPT_FACE",FACE,{"disambiguationData":[OSD([sQuery(id+"F3.wireOp",EDGE,"E20.5.0"),subQ17,subQ16,sQuery(id+"F22.wireOp",EDGE,"E28.13.1"),subQ15,subQ14])]})])],"derivedFrom":subQ9})])]}),makeQuery(id+"F47.opFillet","BLEND_FACE",FACE,{"disambiguationData":[OSD([subQ0,subQ7]),TDD([makeQuery(id+"F42.boolean.opBoolean","COPY",EDGE,{"disambiguationData":[TD([makeQuery(id+"F37.opLoft","SWEPT_FACE",FACE,{"disambiguationData":[OSD([sQuery(id+"F3.wireOp",EDGE,"E20.6.0"),subQ13,subQ12,sQuery(id+"F22.wireOp",EDGE,"E28.14.1"),subQ11,subQ10])]})])],"derivedFrom":subQ9})])]}),makeQuery(id+"F47.opFillet","BLEND_FACE",FACE,{"disambiguationData":[OSD([subQ0,subQ7]),TDD([makeQuery(id+"F42.boolean.opBoolean","COPY",EDGE,{"disambiguationData":[TD([makeQuery(id+"F38.opLoft","SWEPT_FACE",FACE,{"disambiguationData":[OSD([sQuery(id+"F3.wireOp",EDGE,"E20.7.0"),subQ6,subQ5,sQuery(id+"F22.wireOp",EDGE,"E28.15.1"),subQ4,subQ3])]})])],"derivedFrom":subQ9})])]})]});}
            var Q39;
            {var subQ0=sQuery(id+"F22.wireOp",EDGE,"E28.1.0");var subQ1=sQuery(id+"F22.wireOp",EDGE,"E28.1.1");var subQ2=sQuery(id+"F22.wireOp",EDGE,"E28.1.2");var subQ3=sQuery(id+"F22.wireOp",EDGE,"E28.1.3");var subQ4=sQuery(id+"F3.wireOp",EDGE,"E20.9.3");var subQ5=sQuery(id+"F3.wireOp",EDGE,"E20.9.1");var subQ6=makeQuery(id+"F24.opLoft","SWEPT_FACE",FACE,{"disambiguationData":[OSD([subQ5,sQuery(id+"F3.wireOp",EDGE,"E20.9.2"),subQ4,subQ0,subQ2,subQ3])]});var subQ7=sQuery(id+"F41.wireOp",EDGE,"E34");var subQ8=sQuery(id+"F41.wireOp",EDGE,"E32");Q39=makeQuery(id+"F44.opFillet","BLEND_EDGE",EDGE,{"blendedFrom":[makeQuery(id+"F40.boolean.opBoolean","INTERSECT",EDGE,{"derivedFrom":[subQ6,makeQuery(id+"F40.opExtrude","CAP_FACE",FACE,{"disambiguationData":[OSD([sQuery(id+"F39.wireOp",EDGE,"E29"),sQuery(id+"F39.wireOp",EDGE,"E30")])],"isStart":true})]}),makeQuery(id+"F42.boolean.opBoolean","COPY",FACE,{"disambiguationData":[TD([makeQuery(id+"F24.opLoft","SWEPT_FACE",FACE,{"disambiguationData":[OSD([sQuery(id+"F3.wireOp",EDGE,"E20.9.0"),subQ5,subQ4,subQ1,subQ2,subQ3])]})])],"derivedFrom":makeQuery(id+"F42.opRevolve","SWEPT_FACE",FACE,{"disambiguationData":[OSD([subQ8]),TDD([makeQuery(id+"F41.imprint","IMPRINT",EDGE,{"disambiguationData":[TD([[makeQuery(id+"F41.imprint","INTERSECT",VERTEX,{"disambiguationData":[OD(0.0)],"derivedFrom":[subQ8,subQ7]}),-1.0]])],"derivedFrom":subQ8})])]})})],"blendedInto":[makeQuery(id+"F42.boolean.opBoolean","COPY",FACE,{"disambiguationData":[TD([makeQuery(id+"F24.opLoft","SWEPT_FACE",FACE,{"disambiguationData":[OSD([sQuery(id+"F3.wireOp",EDGE,"E20.9.0"),subQ5,subQ4,subQ1,subQ2,subQ3])]})])],"derivedFrom":makeQuery(id+"F42.opRevolve","SWEPT_FACE",FACE,{"disambiguationData":[OSD([subQ8]),TDD([makeQuery(id+"F41.imprint","IMPRINT",EDGE,{"disambiguationData":[TD([[makeQuery(id+"F41.imprint","INTERSECT",VERTEX,{"disambiguationData":[OD(0.0)],"derivedFrom":[subQ8,subQ7]}),-1.0]])],"derivedFrom":subQ8})])]})})]});}
            var Q40;
            {var subQ0=sQuery(id+"F41.wireOp",EDGE,"E34");var subQ1=sQuery(id+"F41.wireOp",EDGE,"E32");Q40=makeQuery(id+"F42.boolean.opBoolean","INTERSECT",EDGE,{"derivedFrom":[makeQuery(id+"F23.opLoft","SWEPT_FACE",FACE,{"disambiguationData":[OSD([sQuery(id+"F3.wireOp",EDGE,"E20.8.0"),sQuery(id+"F3.wireOp",EDGE,"E20.8.1"),sQuery(id+"F3.wireOp",EDGE,"E20.8.3"),sQuery(id+"F22.wireOp",EDGE,"E27.bottom"),sQuery(id+"F22.wireOp",EDGE,"E27.top"),sQuery(id+"F22.wireOp",EDGE,"E27.right")])]}),makeQuery(id+"F42.opRevolve","SWEPT_FACE",FACE,{"disambiguationData":[OSD([subQ1]),TDD([makeQuery(id+"F41.imprint","IMPRINT",EDGE,{"disambiguationData":[TD([[makeQuery(id+"F41.imprint","INTERSECT",VERTEX,{"disambiguationData":[OD(0.0)],"derivedFrom":[subQ1,subQ0]}),-1.0]])],"derivedFrom":subQ1})])]})]});}
            var Q41;
            {var subQ0=sQuery(id+"F41.wireOp",EDGE,"E37");var subQ1=makeQuery(id+"F42.opRevolve","SWEPT_FACE",FACE,{"disambiguationData":[OSD([subQ0])]});var subQ2=makeQuery(id+"F40.opExtrude","CAP_FACE",FACE,{"disambiguationData":[OSD([sQuery(id+"F39.wireOp",EDGE,"E29"),sQuery(id+"F39.wireOp",EDGE,"E30")])],"isStart":true});var subQ3=sQuery(id+"F22.wireOp",EDGE,"E28.15.3");var subQ4=sQuery(id+"F22.wireOp",EDGE,"E28.15.2");var subQ5=sQuery(id+"F3.wireOp",EDGE,"E20.7.3");var subQ6=sQuery(id+"F3.wireOp",EDGE,"E20.7.1");var subQ7=sQuery(id+"F41.wireOp",EDGE,"E38");var subQ8=makeQuery(id+"F42.opRevolve","SWEPT_FACE",FACE,{"disambiguationData":[OSD([subQ7])]});var subQ9=makeQuery(id+"F42.opRevolve","SWEPT_EDGE",EDGE,{"disambiguationData":[OSD([subQ0,subQ7])]});var subQ10=sQuery(id+"F22.wireOp",EDGE,"E28.14.3");var subQ11=sQuery(id+"F22.wireOp",EDGE,"E28.14.2");var subQ12=sQuery(id+"F3.wireOp",EDGE,"E20.6.3");var subQ13=sQuery(id+"F3.wireOp",EDGE,"E20.6.1");var subQ14=sQuery(id+"F22.wireOp",EDGE,"E28.13.3");var subQ15=sQuery(id+"F22.wireOp",EDGE,"E28.13.2");var subQ16=sQuery(id+"F3.wireOp",EDGE,"E20.5.3");var subQ17=sQuery(id+"F3.wireOp",EDGE,"E20.5.1");var subQ18=sQuery(id+"F22.wireOp",EDGE,"E28.12.3");var subQ19=sQuery(id+"F22.wireOp",EDGE,"E28.12.2");var subQ20=sQuery(id+"F3.wireOp",EDGE,"E20.4.3");var subQ21=sQuery(id+"F3.wireOp",EDGE,"E20.4.1");var subQ22=sQuery(id+"F22.wireOp",EDGE,"E28.11.3");var subQ23=sQuery(id+"F22.wireOp",EDGE,"E28.11.2");var subQ24=sQuery(id+"F3.wireOp",EDGE,"E20.3.3");var subQ25=sQuery(id+"F3.wireOp",EDGE,"E20.3.1");var subQ26=sQuery(id+"F22.wireOp",EDGE,"E28.10.3");var subQ27=sQuery(id+"F22.wireOp",EDGE,"E28.10.2");var subQ28=sQuery(id+"F3.wireOp",EDGE,"E20.2.3");var subQ29=sQuery(id+"F3.wireOp",EDGE,"E20.2.1");var subQ30=sQuery(id+"F22.wireOp",EDGE,"E28.9.3");var subQ31=sQuery(id+"F22.wireOp",EDGE,"E28.9.2");var subQ32=sQuery(id+"F3.wireOp",EDGE,"E20.1.3");var subQ33=sQuery(id+"F3.wireOp",EDGE,"E20.1.1");var subQ34=sQuery(id+"F22.wireOp",EDGE,"E28.8.3");var subQ35=sQuery(id+"F22.wireOp",EDGE,"E28.8.2");var subQ36=sQuery(id+"F3.wireOp",EDGE,"E18.top");var subQ37=sQuery(id+"F3.wireOp",EDGE,"E18.bottom");var subQ38=sQuery(id+"F22.wireOp",EDGE,"E28.7.3");var subQ39=sQuery(id+"F22.wireOp",EDGE,"E28.7.2");var subQ40=sQuery(id+"F3.wireOp",EDGE,"E20.15.3");var subQ41=sQuery(id+"F3.wireOp",EDGE,"E20.15.1");var subQ42=sQuery(id+"F22.wireOp",EDGE,"E28.6.3");var subQ43=sQuery(id+"F22.wireOp",EDGE,"E28.6.2");var subQ44=sQuery(id+"F3.wireOp",EDGE,"E20.14.3");var subQ45=sQuery(id+"F3.wireOp",EDGE,"E20.14.1");var subQ46=sQuery(id+"F22.wireOp",EDGE,"E28.5.3");var subQ47=sQuery(id+"F22.wireOp",EDGE,"E28.5.2");var subQ48=sQuery(id+"F3.wireOp",EDGE,"E20.13.3");var subQ49=sQuery(id+"F3.wireOp",EDGE,"E20.13.1");var subQ50=sQuery(id+"F22.wireOp",EDGE,"E28.4.3");var subQ51=sQuery(id+"F22.wireOp",EDGE,"E28.4.2");var subQ52=sQuery(id+"F3.wireOp",EDGE,"E20.12.3");var subQ53=sQuery(id+"F3.wireOp",EDGE,"E20.12.1");var subQ54=sQuery(id+"F22.wireOp",EDGE,"E28.3.3");var subQ55=sQuery(id+"F22.wireOp",EDGE,"E28.3.2");var subQ56=sQuery(id+"F3.wireOp",EDGE,"E20.11.3");var subQ57=sQuery(id+"F3.wireOp",EDGE,"E20.11.1");var subQ58=sQuery(id+"F22.wireOp",EDGE,"E28.2.3");var subQ59=sQuery(id+"F22.wireOp",EDGE,"E28.2.2");var subQ60=sQuery(id+"F3.wireOp",EDGE,"E20.10.3");var subQ61=sQuery(id+"F3.wireOp",EDGE,"E20.10.1");var subQ62=sQuery(id+"F22.wireOp",EDGE,"E28.1.3");var subQ63=sQuery(id+"F22.wireOp",EDGE,"E28.1.2");var subQ64=sQuery(id+"F3.wireOp",EDGE,"E20.9.3");var subQ65=sQuery(id+"F3.wireOp",EDGE,"E20.9.1");var subQ66=sQuery(id+"F22.wireOp",EDGE,"E27.top");var subQ67=sQuery(id+"F22.wireOp",EDGE,"E27.bottom");var subQ68=sQuery(id+"F3.wireOp",EDGE,"E20.8.3");var subQ69=sQuery(id+"F3.wireOp",EDGE,"E20.8.1");var subQ71=makeQuery(id+"F23.opLoft","SWEPT_FACE",FACE,{"disambiguationData":[OSD([sQuery(id+"F3.wireOp",EDGE,"E20.8.0"),subQ69,subQ68,subQ67,subQ66,sQuery(id+"F22.wireOp",EDGE,"E27.right")])]});var subQ74=makeQuery(id+"F42.boolean.opBoolean","COPY",FACE,{"disambiguationData":[TD([subQ71])],"derivedFrom":subQ8});var subQ75=makeQuery(id+"F23.boolean.opBoolean","INTERSECT",EDGE,{"derivedFrom":[makeQuery(id+"F1.opRevolve","SWEPT_FACE",FACE,{"disambiguationData":[OSD([sQuery(id+"F0.wireOp",EDGE,"E13")])]}),subQ71]});Q41=makeQuery(id+"F48.opFillet","BLEND_EDGE",EDGE,{"blendedFrom":[makeQuery(id+"F47.opFillet","TWEAK_EDGE",EDGE,{"derivedFrom":[makeQuery(id+"F45.opFillet","BLEND_VERTEX",VERTEX,{"blendedFrom":[subQ75,subQ71,subQ74],"blendedInto":[subQ71,subQ74]}),makeQuery(id+"F45.opFillet","BLEND_VERTEX",VERTEX,{"blendedFrom":[subQ75,makeQuery(id+"F42.boolean.opBoolean","MERGE",FACE,{"derivedFrom":[subQ2,subQ1]}),subQ74],"blendedInto":[makeQuery(id+"F42.boolean.opBoolean","MERGE",FACE,{"derivedFrom":[subQ2,subQ1]}),subQ74]})]}),makeQuery(id+"F47.opFillet","BLEND_FACE",FACE,{"disambiguationData":[OSD([subQ0,subQ7]),TDD([makeQuery(id+"F42.boolean.opBoolean","COPY",EDGE,{"disambiguationData":[TD([subQ71])],"derivedFrom":subQ9})])]}),makeQuery(id+"F47.opFillet","BLEND_FACE",FACE,{"disambiguationData":[OSD([subQ0,subQ7]),TDD([makeQuery(id+"F42.boolean.opBoolean","COPY",EDGE,{"disambiguationData":[TD([makeQuery(id+"F24.opLoft","SWEPT_FACE",FACE,{"disambiguationData":[OSD([sQuery(id+"F3.wireOp",EDGE,"E20.9.0"),subQ65,subQ64,sQuery(id+"F22.wireOp",EDGE,"E28.1.1"),subQ63,subQ62])]})])],"derivedFrom":subQ9})])]}),makeQuery(id+"F47.opFillet","BLEND_FACE",FACE,{"disambiguationData":[OSD([subQ0,subQ7]),TDD([makeQuery(id+"F42.boolean.opBoolean","COPY",EDGE,{"disambiguationData":[TD([makeQuery(id+"F25.opLoft","SWEPT_FACE",FACE,{"disambiguationData":[OSD([sQuery(id+"F3.wireOp",EDGE,"E20.10.0"),subQ61,subQ60,sQuery(id+"F22.wireOp",EDGE,"E28.2.1"),subQ59,subQ58])]})])],"derivedFrom":subQ9})])]}),makeQuery(id+"F47.opFillet","BLEND_FACE",FACE,{"disambiguationData":[OSD([subQ0,subQ7]),TDD([makeQuery(id+"F42.boolean.opBoolean","COPY",EDGE,{"disambiguationData":[TD([makeQuery(id+"F26.opLoft","SWEPT_FACE",FACE,{"disambiguationData":[OSD([sQuery(id+"F3.wireOp",EDGE,"E20.11.0"),subQ57,subQ56,sQuery(id+"F22.wireOp",EDGE,"E28.3.1"),subQ55,subQ54])]})])],"derivedFrom":subQ9})])]}),makeQuery(id+"F47.opFillet","BLEND_FACE",FACE,{"disambiguationData":[OSD([subQ0,subQ7]),TDD([makeQuery(id+"F42.boolean.opBoolean","COPY",EDGE,{"disambiguationData":[TD([makeQuery(id+"F27.opLoft","SWEPT_FACE",FACE,{"disambiguationData":[OSD([sQuery(id+"F3.wireOp",EDGE,"E20.12.0"),subQ53,subQ52,sQuery(id+"F22.wireOp",EDGE,"E28.4.1"),subQ51,subQ50])]})])],"derivedFrom":subQ9})])]}),makeQuery(id+"F47.opFillet","BLEND_FACE",FACE,{"disambiguationData":[OSD([subQ0,subQ7]),TDD([makeQuery(id+"F42.boolean.opBoolean","COPY",EDGE,{"disambiguationData":[TD([makeQuery(id+"F28.opLoft","SWEPT_FACE",FACE,{"disambiguationData":[OSD([sQuery(id+"F3.wireOp",EDGE,"E20.13.0"),subQ49,subQ48,sQuery(id+"F22.wireOp",EDGE,"E28.5.1"),subQ47,subQ46])]})])],"derivedFrom":subQ9})])]}),makeQuery(id+"F47.opFillet","BLEND_FACE",FACE,{"disambiguationData":[OSD([subQ0,subQ7]),TDD([makeQuery(id+"F42.boolean.opBoolean","COPY",EDGE,{"disambiguationData":[TD([makeQuery(id+"F29.opLoft","SWEPT_FACE",FACE,{"disambiguationData":[OSD([sQuery(id+"F3.wireOp",EDGE,"E20.14.0"),subQ45,subQ44,sQuery(id+"F22.wireOp",EDGE,"E28.6.1"),subQ43,subQ42])]})])],"derivedFrom":subQ9})])]}),makeQuery(id+"F47.opFillet","BLEND_FACE",FACE,{"disambiguationData":[OSD([subQ0,subQ7]),TDD([makeQuery(id+"F42.boolean.opBoolean","COPY",EDGE,{"disambiguationData":[TD([makeQuery(id+"F30.opLoft","SWEPT_FACE",FACE,{"disambiguationData":[OSD([sQuery(id+"F3.wireOp",EDGE,"E20.15.0"),subQ41,subQ40,sQuery(id+"F22.wireOp",EDGE,"E28.7.1"),subQ39,subQ38])]})])],"derivedFrom":subQ9})])]}),makeQuery(id+"F47.opFillet","BLEND_FACE",FACE,{"disambiguationData":[OSD([subQ0,subQ7]),TDD([makeQuery(id+"F42.boolean.opBoolean","COPY",EDGE,{"disambiguationData":[TD([makeQuery(id+"F31.opLoft","SWEPT_FACE",FACE,{"disambiguationData":[OSD([subQ37,subQ36,sQuery(id+"F3.wireOp",EDGE,"E18.left"),sQuery(id+"F22.wireOp",EDGE,"E28.8.1"),subQ35,subQ34])]})])],"derivedFrom":subQ9})])]}),makeQuery(id+"F47.opFillet","BLEND_FACE",FACE,{"disambiguationData":[OSD([subQ0,subQ7]),TDD([makeQuery(id+"F42.boolean.opBoolean","COPY",EDGE,{"disambiguationData":[TD([makeQuery(id+"F32.opLoft","SWEPT_FACE",FACE,{"disambiguationData":[OSD([sQuery(id+"F3.wireOp",EDGE,"E20.1.0"),subQ33,subQ32,sQuery(id+"F22.wireOp",EDGE,"E28.9.1"),subQ31,subQ30])]})])],"derivedFrom":subQ9})])]}),makeQuery(id+"F47.opFillet","BLEND_FACE",FACE,{"disambiguationData":[OSD([subQ0,subQ7]),TDD([makeQuery(id+"F42.boolean.opBoolean","COPY",EDGE,{"disambiguationData":[TD([makeQuery(id+"F33.opLoft","SWEPT_FACE",FACE,{"disambiguationData":[OSD([sQuery(id+"F3.wireOp",EDGE,"E20.2.0"),subQ29,subQ28,sQuery(id+"F22.wireOp",EDGE,"E28.10.1"),subQ27,subQ26])]})])],"derivedFrom":subQ9})])]}),makeQuery(id+"F47.opFillet","BLEND_FACE",FACE,{"disambiguationData":[OSD([subQ0,subQ7]),TDD([makeQuery(id+"F42.boolean.opBoolean","COPY",EDGE,{"disambiguationData":[TD([makeQuery(id+"F34.opLoft","SWEPT_FACE",FACE,{"disambiguationData":[OSD([sQuery(id+"F3.wireOp",EDGE,"E20.3.0"),subQ25,subQ24,sQuery(id+"F22.wireOp",EDGE,"E28.11.1"),subQ23,subQ22])]})])],"derivedFrom":subQ9})])]}),makeQuery(id+"F47.opFillet","BLEND_FACE",FACE,{"disambiguationData":[OSD([subQ0,subQ7]),TDD([makeQuery(id+"F42.boolean.opBoolean","COPY",EDGE,{"disambiguationData":[TD([makeQuery(id+"F35.opLoft","SWEPT_FACE",FACE,{"disambiguationData":[OSD([sQuery(id+"F3.wireOp",EDGE,"E20.4.0"),subQ21,subQ20,sQuery(id+"F22.wireOp",EDGE,"E28.12.1"),subQ19,subQ18])]})])],"derivedFrom":subQ9})])]}),makeQuery(id+"F47.opFillet","BLEND_FACE",FACE,{"disambiguationData":[OSD([subQ0,subQ7]),TDD([makeQuery(id+"F42.boolean.opBoolean","COPY",EDGE,{"disambiguationData":[TD([makeQuery(id+"F36.opLoft","SWEPT_FACE",FACE,{"disambiguationData":[OSD([sQuery(id+"F3.wireOp",EDGE,"E20.5.0"),subQ17,subQ16,sQuery(id+"F22.wireOp",EDGE,"E28.13.1"),subQ15,subQ14])]})])],"derivedFrom":subQ9})])]}),makeQuery(id+"F47.opFillet","BLEND_FACE",FACE,{"disambiguationData":[OSD([subQ0,subQ7]),TDD([makeQuery(id+"F42.boolean.opBoolean","COPY",EDGE,{"disambiguationData":[TD([makeQuery(id+"F37.opLoft","SWEPT_FACE",FACE,{"disambiguationData":[OSD([sQuery(id+"F3.wireOp",EDGE,"E20.6.0"),subQ13,subQ12,sQuery(id+"F22.wireOp",EDGE,"E28.14.1"),subQ11,subQ10])]})])],"derivedFrom":subQ9})])]}),makeQuery(id+"F47.opFillet","BLEND_FACE",FACE,{"disambiguationData":[OSD([subQ0,subQ7]),TDD([makeQuery(id+"F42.boolean.opBoolean","COPY",EDGE,{"disambiguationData":[TD([makeQuery(id+"F38.opLoft","SWEPT_FACE",FACE,{"disambiguationData":[OSD([sQuery(id+"F3.wireOp",EDGE,"E20.7.0"),subQ6,subQ5,sQuery(id+"F22.wireOp",EDGE,"E28.15.1"),subQ4,subQ3])]})])],"derivedFrom":subQ9})])]})],"blendedInto":[makeQuery(id+"F47.opFillet","BLEND_FACE",FACE,{"disambiguationData":[OSD([subQ0,subQ7]),TDD([makeQuery(id+"F42.boolean.opBoolean","COPY",EDGE,{"disambiguationData":[TD([subQ71])],"derivedFrom":subQ9})])]}),makeQuery(id+"F47.opFillet","BLEND_FACE",FACE,{"disambiguationData":[OSD([subQ0,subQ7]),TDD([makeQuery(id+"F42.boolean.opBoolean","COPY",EDGE,{"disambiguationData":[TD([makeQuery(id+"F24.opLoft","SWEPT_FACE",FACE,{"disambiguationData":[OSD([sQuery(id+"F3.wireOp",EDGE,"E20.9.0"),subQ65,subQ64,sQuery(id+"F22.wireOp",EDGE,"E28.1.1"),subQ63,subQ62])]})])],"derivedFrom":subQ9})])]}),makeQuery(id+"F47.opFillet","BLEND_FACE",FACE,{"disambiguationData":[OSD([subQ0,subQ7]),TDD([makeQuery(id+"F42.boolean.opBoolean","COPY",EDGE,{"disambiguationData":[TD([makeQuery(id+"F25.opLoft","SWEPT_FACE",FACE,{"disambiguationData":[OSD([sQuery(id+"F3.wireOp",EDGE,"E20.10.0"),subQ61,subQ60,sQuery(id+"F22.wireOp",EDGE,"E28.2.1"),subQ59,subQ58])]})])],"derivedFrom":subQ9})])]}),makeQuery(id+"F47.opFillet","BLEND_FACE",FACE,{"disambiguationData":[OSD([subQ0,subQ7]),TDD([makeQuery(id+"F42.boolean.opBoolean","COPY",EDGE,{"disambiguationData":[TD([makeQuery(id+"F26.opLoft","SWEPT_FACE",FACE,{"disambiguationData":[OSD([sQuery(id+"F3.wireOp",EDGE,"E20.11.0"),subQ57,subQ56,sQuery(id+"F22.wireOp",EDGE,"E28.3.1"),subQ55,subQ54])]})])],"derivedFrom":subQ9})])]}),makeQuery(id+"F47.opFillet","BLEND_FACE",FACE,{"disambiguationData":[OSD([subQ0,subQ7]),TDD([makeQuery(id+"F42.boolean.opBoolean","COPY",EDGE,{"disambiguationData":[TD([makeQuery(id+"F27.opLoft","SWEPT_FACE",FACE,{"disambiguationData":[OSD([sQuery(id+"F3.wireOp",EDGE,"E20.12.0"),subQ53,subQ52,sQuery(id+"F22.wireOp",EDGE,"E28.4.1"),subQ51,subQ50])]})])],"derivedFrom":subQ9})])]}),makeQuery(id+"F47.opFillet","BLEND_FACE",FACE,{"disambiguationData":[OSD([subQ0,subQ7]),TDD([makeQuery(id+"F42.boolean.opBoolean","COPY",EDGE,{"disambiguationData":[TD([makeQuery(id+"F28.opLoft","SWEPT_FACE",FACE,{"disambiguationData":[OSD([sQuery(id+"F3.wireOp",EDGE,"E20.13.0"),subQ49,subQ48,sQuery(id+"F22.wireOp",EDGE,"E28.5.1"),subQ47,subQ46])]})])],"derivedFrom":subQ9})])]}),makeQuery(id+"F47.opFillet","BLEND_FACE",FACE,{"disambiguationData":[OSD([subQ0,subQ7]),TDD([makeQuery(id+"F42.boolean.opBoolean","COPY",EDGE,{"disambiguationData":[TD([makeQuery(id+"F29.opLoft","SWEPT_FACE",FACE,{"disambiguationData":[OSD([sQuery(id+"F3.wireOp",EDGE,"E20.14.0"),subQ45,subQ44,sQuery(id+"F22.wireOp",EDGE,"E28.6.1"),subQ43,subQ42])]})])],"derivedFrom":subQ9})])]}),makeQuery(id+"F47.opFillet","BLEND_FACE",FACE,{"disambiguationData":[OSD([subQ0,subQ7]),TDD([makeQuery(id+"F42.boolean.opBoolean","COPY",EDGE,{"disambiguationData":[TD([makeQuery(id+"F30.opLoft","SWEPT_FACE",FACE,{"disambiguationData":[OSD([sQuery(id+"F3.wireOp",EDGE,"E20.15.0"),subQ41,subQ40,sQuery(id+"F22.wireOp",EDGE,"E28.7.1"),subQ39,subQ38])]})])],"derivedFrom":subQ9})])]}),makeQuery(id+"F47.opFillet","BLEND_FACE",FACE,{"disambiguationData":[OSD([subQ0,subQ7]),TDD([makeQuery(id+"F42.boolean.opBoolean","COPY",EDGE,{"disambiguationData":[TD([makeQuery(id+"F31.opLoft","SWEPT_FACE",FACE,{"disambiguationData":[OSD([subQ37,subQ36,sQuery(id+"F3.wireOp",EDGE,"E18.left"),sQuery(id+"F22.wireOp",EDGE,"E28.8.1"),subQ35,subQ34])]})])],"derivedFrom":subQ9})])]}),makeQuery(id+"F47.opFillet","BLEND_FACE",FACE,{"disambiguationData":[OSD([subQ0,subQ7]),TDD([makeQuery(id+"F42.boolean.opBoolean","COPY",EDGE,{"disambiguationData":[TD([makeQuery(id+"F32.opLoft","SWEPT_FACE",FACE,{"disambiguationData":[OSD([sQuery(id+"F3.wireOp",EDGE,"E20.1.0"),subQ33,subQ32,sQuery(id+"F22.wireOp",EDGE,"E28.9.1"),subQ31,subQ30])]})])],"derivedFrom":subQ9})])]}),makeQuery(id+"F47.opFillet","BLEND_FACE",FACE,{"disambiguationData":[OSD([subQ0,subQ7]),TDD([makeQuery(id+"F42.boolean.opBoolean","COPY",EDGE,{"disambiguationData":[TD([makeQuery(id+"F33.opLoft","SWEPT_FACE",FACE,{"disambiguationData":[OSD([sQuery(id+"F3.wireOp",EDGE,"E20.2.0"),subQ29,subQ28,sQuery(id+"F22.wireOp",EDGE,"E28.10.1"),subQ27,subQ26])]})])],"derivedFrom":subQ9})])]}),makeQuery(id+"F47.opFillet","BLEND_FACE",FACE,{"disambiguationData":[OSD([subQ0,subQ7]),TDD([makeQuery(id+"F42.boolean.opBoolean","COPY",EDGE,{"disambiguationData":[TD([makeQuery(id+"F34.opLoft","SWEPT_FACE",FACE,{"disambiguationData":[OSD([sQuery(id+"F3.wireOp",EDGE,"E20.3.0"),subQ25,subQ24,sQuery(id+"F22.wireOp",EDGE,"E28.11.1"),subQ23,subQ22])]})])],"derivedFrom":subQ9})])]}),makeQuery(id+"F47.opFillet","BLEND_FACE",FACE,{"disambiguationData":[OSD([subQ0,subQ7]),TDD([makeQuery(id+"F42.boolean.opBoolean","COPY",EDGE,{"disambiguationData":[TD([makeQuery(id+"F35.opLoft","SWEPT_FACE",FACE,{"disambiguationData":[OSD([sQuery(id+"F3.wireOp",EDGE,"E20.4.0"),subQ21,subQ20,sQuery(id+"F22.wireOp",EDGE,"E28.12.1"),subQ19,subQ18])]})])],"derivedFrom":subQ9})])]}),makeQuery(id+"F47.opFillet","BLEND_FACE",FACE,{"disambiguationData":[OSD([subQ0,subQ7]),TDD([makeQuery(id+"F42.boolean.opBoolean","COPY",EDGE,{"disambiguationData":[TD([makeQuery(id+"F36.opLoft","SWEPT_FACE",FACE,{"disambiguationData":[OSD([sQuery(id+"F3.wireOp",EDGE,"E20.5.0"),subQ17,subQ16,sQuery(id+"F22.wireOp",EDGE,"E28.13.1"),subQ15,subQ14])]})])],"derivedFrom":subQ9})])]}),makeQuery(id+"F47.opFillet","BLEND_FACE",FACE,{"disambiguationData":[OSD([subQ0,subQ7]),TDD([makeQuery(id+"F42.boolean.opBoolean","COPY",EDGE,{"disambiguationData":[TD([makeQuery(id+"F37.opLoft","SWEPT_FACE",FACE,{"disambiguationData":[OSD([sQuery(id+"F3.wireOp",EDGE,"E20.6.0"),subQ13,subQ12,sQuery(id+"F22.wireOp",EDGE,"E28.14.1"),subQ11,subQ10])]})])],"derivedFrom":subQ9})])]}),makeQuery(id+"F47.opFillet","BLEND_FACE",FACE,{"disambiguationData":[OSD([subQ0,subQ7]),TDD([makeQuery(id+"F42.boolean.opBoolean","COPY",EDGE,{"disambiguationData":[TD([makeQuery(id+"F38.opLoft","SWEPT_FACE",FACE,{"disambiguationData":[OSD([sQuery(id+"F3.wireOp",EDGE,"E20.7.0"),subQ6,subQ5,sQuery(id+"F22.wireOp",EDGE,"E28.15.1"),subQ4,subQ3])]})])],"derivedFrom":subQ9})])]})]});}
            var Q42;
            {var subQ0=sQuery(id+"F22.wireOp",EDGE,"E27.left");var subQ1=sQuery(id+"F22.wireOp",EDGE,"E27.top");var subQ2=sQuery(id+"F22.wireOp",EDGE,"E27.bottom");var subQ3=sQuery(id+"F3.wireOp",EDGE,"E20.8.3");var subQ4=sQuery(id+"F3.wireOp",EDGE,"E20.8.1");var subQ5=makeQuery(id+"F23.opLoft","SWEPT_FACE",FACE,{"disambiguationData":[OSD([subQ4,sQuery(id+"F3.wireOp",EDGE,"E20.8.2"),subQ3,subQ2,subQ1,subQ0])]});var subQ6=sQuery(id+"F22.wireOp",EDGE,"E27.right");var subQ7=sQuery(id+"F41.wireOp",EDGE,"E34");var subQ8=sQuery(id+"F41.wireOp",EDGE,"E32");Q42=makeQuery(id+"F44.opFillet","BLEND_EDGE",EDGE,{"blendedFrom":[makeQuery(id+"F40.boolean.opBoolean","INTERSECT",EDGE,{"derivedFrom":[subQ5,makeQuery(id+"F40.opExtrude","CAP_FACE",FACE,{"disambiguationData":[OSD([sQuery(id+"F39.wireOp",EDGE,"E29"),sQuery(id+"F39.wireOp",EDGE,"E30")])],"isStart":true})]}),makeQuery(id+"F42.boolean.opBoolean","COPY",FACE,{"disambiguationData":[TD([makeQuery(id+"F23.opLoft","SWEPT_FACE",FACE,{"disambiguationData":[OSD([sQuery(id+"F3.wireOp",EDGE,"E20.8.0"),subQ4,subQ3,subQ2,subQ1,subQ6])]})])],"derivedFrom":makeQuery(id+"F42.opRevolve","SWEPT_FACE",FACE,{"disambiguationData":[OSD([subQ8]),TDD([makeQuery(id+"F41.imprint","IMPRINT",EDGE,{"disambiguationData":[TD([[makeQuery(id+"F41.imprint","INTERSECT",VERTEX,{"disambiguationData":[OD(0.0)],"derivedFrom":[subQ8,subQ7]}),-1.0]])],"derivedFrom":subQ8})])]})})],"blendedInto":[makeQuery(id+"F42.boolean.opBoolean","COPY",FACE,{"disambiguationData":[TD([makeQuery(id+"F23.opLoft","SWEPT_FACE",FACE,{"disambiguationData":[OSD([sQuery(id+"F3.wireOp",EDGE,"E20.8.0"),subQ4,subQ3,subQ2,subQ1,subQ6])]})])],"derivedFrom":makeQuery(id+"F42.opRevolve","SWEPT_FACE",FACE,{"disambiguationData":[OSD([subQ8]),TDD([makeQuery(id+"F41.imprint","IMPRINT",EDGE,{"disambiguationData":[TD([[makeQuery(id+"F41.imprint","INTERSECT",VERTEX,{"disambiguationData":[OD(0.0)],"derivedFrom":[subQ8,subQ7]}),-1.0]])],"derivedFrom":subQ8})])]})})]});}
            var Q43;
            {var subQ0=sQuery(id+"F41.wireOp",EDGE,"E34");var subQ1=sQuery(id+"F41.wireOp",EDGE,"E32");Q43=makeQuery(id+"F42.boolean.opBoolean","INTERSECT",EDGE,{"derivedFrom":[makeQuery(id+"F38.opLoft","SWEPT_FACE",FACE,{"disambiguationData":[OSD([sQuery(id+"F3.wireOp",EDGE,"E20.7.0"),sQuery(id+"F3.wireOp",EDGE,"E20.7.1"),sQuery(id+"F3.wireOp",EDGE,"E20.7.3"),sQuery(id+"F22.wireOp",EDGE,"E28.15.1"),sQuery(id+"F22.wireOp",EDGE,"E28.15.2"),sQuery(id+"F22.wireOp",EDGE,"E28.15.3")])]}),makeQuery(id+"F42.opRevolve","SWEPT_FACE",FACE,{"disambiguationData":[OSD([subQ1]),TDD([makeQuery(id+"F41.imprint","IMPRINT",EDGE,{"disambiguationData":[TD([[makeQuery(id+"F41.imprint","INTERSECT",VERTEX,{"disambiguationData":[OD(0.0)],"derivedFrom":[subQ1,subQ0]}),-1.0]])],"derivedFrom":subQ1})])]})]});}
            var Q44;
            {var subQ0=sQuery(id+"F41.wireOp",EDGE,"E37");var subQ1=makeQuery(id+"F42.opRevolve","SWEPT_FACE",FACE,{"disambiguationData":[OSD([subQ0])]});var subQ2=makeQuery(id+"F40.opExtrude","CAP_FACE",FACE,{"disambiguationData":[OSD([sQuery(id+"F39.wireOp",EDGE,"E29"),sQuery(id+"F39.wireOp",EDGE,"E30")])],"isStart":true});var subQ3=sQuery(id+"F22.wireOp",EDGE,"E28.15.3");var subQ4=sQuery(id+"F22.wireOp",EDGE,"E28.15.2");var subQ5=sQuery(id+"F3.wireOp",EDGE,"E20.7.3");var subQ7=sQuery(id+"F3.wireOp",EDGE,"E20.7.1");var subQ9=sQuery(id+"F3.wireOp",EDGE,"E20.7.0");var subQ10=makeQuery(id+"F38.opLoft","SWEPT_FACE",FACE,{"disambiguationData":[OSD([subQ9,subQ7,subQ5,sQuery(id+"F22.wireOp",EDGE,"E28.15.1"),subQ4,subQ3])]});var subQ11=sQuery(id+"F41.wireOp",EDGE,"E38");var subQ12=makeQuery(id+"F42.opRevolve","SWEPT_FACE",FACE,{"disambiguationData":[OSD([subQ11])]});var subQ13=makeQuery(id+"F42.opRevolve","SWEPT_EDGE",EDGE,{"disambiguationData":[OSD([subQ0,subQ11])]});var subQ14=sQuery(id+"F22.wireOp",EDGE,"E28.14.3");var subQ15=sQuery(id+"F22.wireOp",EDGE,"E28.14.2");var subQ16=sQuery(id+"F3.wireOp",EDGE,"E20.6.3");var subQ17=sQuery(id+"F3.wireOp",EDGE,"E20.6.1");var subQ18=sQuery(id+"F3.wireOp",EDGE,"E20.6.0");var subQ19=makeQuery(id+"F37.opLoft","SWEPT_FACE",FACE,{"disambiguationData":[OSD([subQ18,subQ17,subQ16,sQuery(id+"F22.wireOp",EDGE,"E28.14.1"),subQ15,subQ14])]});var subQ21=sQuery(id+"F22.wireOp",EDGE,"E28.13.3");var subQ22=sQuery(id+"F22.wireOp",EDGE,"E28.13.2");var subQ23=sQuery(id+"F3.wireOp",EDGE,"E20.5.3");var subQ25=sQuery(id+"F3.wireOp",EDGE,"E20.5.1");var subQ26=sQuery(id+"F3.wireOp",EDGE,"E20.5.0");var subQ27=makeQuery(id+"F36.opLoft","SWEPT_FACE",FACE,{"disambiguationData":[OSD([subQ26,subQ25,subQ23,sQuery(id+"F22.wireOp",EDGE,"E28.13.1"),subQ22,subQ21])]});var subQ28=sQuery(id+"F22.wireOp",EDGE,"E28.12.3");var subQ29=sQuery(id+"F22.wireOp",EDGE,"E28.12.2");var subQ30=sQuery(id+"F3.wireOp",EDGE,"E20.4.3");var subQ32=sQuery(id+"F3.wireOp",EDGE,"E20.4.1");var subQ33=sQuery(id+"F3.wireOp",EDGE,"E20.4.0");var subQ34=makeQuery(id+"F35.opLoft","SWEPT_FACE",FACE,{"disambiguationData":[OSD([subQ33,subQ32,subQ30,sQuery(id+"F22.wireOp",EDGE,"E28.12.1"),subQ29,subQ28])]});var subQ35=sQuery(id+"F22.wireOp",EDGE,"E28.11.3");var subQ36=sQuery(id+"F22.wireOp",EDGE,"E28.11.2");var subQ37=sQuery(id+"F3.wireOp",EDGE,"E20.3.3");var subQ39=sQuery(id+"F3.wireOp",EDGE,"E20.3.1");var subQ40=sQuery(id+"F3.wireOp",EDGE,"E20.3.0");var subQ41=makeQuery(id+"F34.opLoft","SWEPT_FACE",FACE,{"disambiguationData":[OSD([subQ40,subQ39,subQ37,sQuery(id+"F22.wireOp",EDGE,"E28.11.1"),subQ36,subQ35])]});var subQ42=sQuery(id+"F22.wireOp",EDGE,"E28.10.3");var subQ43=sQuery(id+"F22.wireOp",EDGE,"E28.10.2");var subQ44=sQuery(id+"F3.wireOp",EDGE,"E20.2.3");var subQ46=sQuery(id+"F3.wireOp",EDGE,"E20.2.1");var subQ47=sQuery(id+"F3.wireOp",EDGE,"E20.2.0");var subQ48=makeQuery(id+"F33.opLoft","SWEPT_FACE",FACE,{"disambiguationData":[OSD([subQ47,subQ46,subQ44,sQuery(id+"F22.wireOp",EDGE,"E28.10.1"),subQ43,subQ42])]});var subQ49=sQuery(id+"F22.wireOp",EDGE,"E28.9.3");var subQ50=sQuery(id+"F22.wireOp",EDGE,"E28.9.2");var subQ51=sQuery(id+"F3.wireOp",EDGE,"E20.1.3");var subQ53=sQuery(id+"F3.wireOp",EDGE,"E20.1.1");var subQ54=sQuery(id+"F3.wireOp",EDGE,"E20.1.0");var subQ55=makeQuery(id+"F32.opLoft","SWEPT_FACE",FACE,{"disambiguationData":[OSD([subQ54,subQ53,subQ51,sQuery(id+"F22.wireOp",EDGE,"E28.9.1"),subQ50,subQ49])]});var subQ56=sQuery(id+"F22.wireOp",EDGE,"E28.8.3");var subQ57=sQuery(id+"F22.wireOp",EDGE,"E28.8.2");var subQ59=sQuery(id+"F3.wireOp",EDGE,"E18.top");var subQ60=sQuery(id+"F3.wireOp",EDGE,"E18.bottom");var subQ61=sQuery(id+"F3.wireOp",EDGE,"E18.left");var subQ62=makeQuery(id+"F31.opLoft","SWEPT_FACE",FACE,{"disambiguationData":[OSD([subQ60,subQ59,subQ61,sQuery(id+"F22.wireOp",EDGE,"E28.8.1"),subQ57,subQ56])]});var subQ63=sQuery(id+"F22.wireOp",EDGE,"E28.7.3");var subQ64=sQuery(id+"F22.wireOp",EDGE,"E28.7.2");var subQ65=sQuery(id+"F3.wireOp",EDGE,"E20.15.3");var subQ66=sQuery(id+"F3.wireOp",EDGE,"E20.15.1");var subQ67=sQuery(id+"F3.wireOp",EDGE,"E20.15.0");var subQ68=makeQuery(id+"F30.opLoft","SWEPT_FACE",FACE,{"disambiguationData":[OSD([subQ67,subQ66,subQ65,sQuery(id+"F22.wireOp",EDGE,"E28.7.1"),subQ64,subQ63])]});var subQ70=sQuery(id+"F22.wireOp",EDGE,"E28.6.3");var subQ71=sQuery(id+"F22.wireOp",EDGE,"E28.6.2");var subQ72=sQuery(id+"F3.wireOp",EDGE,"E20.14.3");var subQ74=sQuery(id+"F3.wireOp",EDGE,"E20.14.1");var subQ75=sQuery(id+"F3.wireOp",EDGE,"E20.14.0");var subQ76=makeQuery(id+"F29.opLoft","SWEPT_FACE",FACE,{"disambiguationData":[OSD([subQ75,subQ74,subQ72,sQuery(id+"F22.wireOp",EDGE,"E28.6.1"),subQ71,subQ70])]});var subQ77=sQuery(id+"F22.wireOp",EDGE,"E28.5.3");var subQ78=sQuery(id+"F22.wireOp",EDGE,"E28.5.2");var subQ79=sQuery(id+"F3.wireOp",EDGE,"E20.13.3");var subQ81=sQuery(id+"F3.wireOp",EDGE,"E20.13.1");var subQ82=sQuery(id+"F3.wireOp",EDGE,"E20.13.0");var subQ83=makeQuery(id+"F28.opLoft","SWEPT_FACE",FACE,{"disambiguationData":[OSD([subQ82,subQ81,subQ79,sQuery(id+"F22.wireOp",EDGE,"E28.5.1"),subQ78,subQ77])]});var subQ84=sQuery(id+"F22.wireOp",EDGE,"E28.4.3");var subQ85=sQuery(id+"F22.wireOp",EDGE,"E28.4.2");var subQ86=sQuery(id+"F3.wireOp",EDGE,"E20.12.3");var subQ88=sQuery(id+"F3.wireOp",EDGE,"E20.12.1");var subQ89=sQuery(id+"F3.wireOp",EDGE,"E20.12.0");var subQ90=makeQuery(id+"F27.opLoft","SWEPT_FACE",FACE,{"disambiguationData":[OSD([subQ89,subQ88,subQ86,sQuery(id+"F22.wireOp",EDGE,"E28.4.1"),subQ85,subQ84])]});var subQ91=sQuery(id+"F22.wireOp",EDGE,"E28.3.3");var subQ92=sQuery(id+"F22.wireOp",EDGE,"E28.3.2");var subQ93=sQuery(id+"F3.wireOp",EDGE,"E20.11.3");var subQ95=sQuery(id+"F3.wireOp",EDGE,"E20.11.1");var subQ96=sQuery(id+"F3.wireOp",EDGE,"E20.11.0");var subQ97=makeQuery(id+"F26.opLoft","SWEPT_FACE",FACE,{"disambiguationData":[OSD([subQ96,subQ95,subQ93,sQuery(id+"F22.wireOp",EDGE,"E28.3.1"),subQ92,subQ91])]});var subQ98=sQuery(id+"F22.wireOp",EDGE,"E28.2.3");var subQ99=sQuery(id+"F22.wireOp",EDGE,"E28.2.2");var subQ100=sQuery(id+"F3.wireOp",EDGE,"E20.10.3");var subQ101=sQuery(id+"F3.wireOp",EDGE,"E20.10.1");var subQ102=sQuery(id+"F3.wireOp",EDGE,"E20.10.0");var subQ103=makeQuery(id+"F25.opLoft","SWEPT_FACE",FACE,{"disambiguationData":[OSD([subQ102,subQ101,subQ100,sQuery(id+"F22.wireOp",EDGE,"E28.2.1"),subQ99,subQ98])]});var subQ105=sQuery(id+"F22.wireOp",EDGE,"E28.1.3");var subQ106=sQuery(id+"F22.wireOp",EDGE,"E28.1.2");var subQ107=sQuery(id+"F3.wireOp",EDGE,"E20.9.3");var subQ108=sQuery(id+"F3.wireOp",EDGE,"E20.9.1");var subQ109=sQuery(id+"F3.wireOp",EDGE,"E20.9.0");var subQ110=makeQuery(id+"F24.opLoft","SWEPT_FACE",FACE,{"disambiguationData":[OSD([subQ109,subQ108,subQ107,sQuery(id+"F22.wireOp",EDGE,"E28.1.1"),subQ106,subQ105])]});var subQ111=sQuery(id+"F22.wireOp",EDGE,"E27.top");var subQ112=sQuery(id+"F22.wireOp",EDGE,"E27.bottom");var subQ113=sQuery(id+"F3.wireOp",EDGE,"E20.8.3");var subQ115=sQuery(id+"F3.wireOp",EDGE,"E20.8.1");var subQ119=makeQuery(id+"F42.boolean.opBoolean","COPY",FACE,{"disambiguationData":[TD([subQ10])],"derivedFrom":subQ12});var subQ127=makeQuery(id+"F14.opLoft","CAP_FACE",FACE,{"disambiguationData":[OSD([makeQuery(id+"F3.imprint","IMPRINT",FACE,{"disambiguationData":[TD([[makeQuery(id+"F3.imprint","IMPRINT",EDGE,{"derivedFrom":subQ9}),-1.0]])]})])],"isStart":true});var subQ162=makeQuery(id+"F5.opLoft","CAP_FACE",FACE,{"disambiguationData":[OSD([makeQuery(id+"F3.imprint","IMPRINT",FACE,{"disambiguationData":[TD([[makeQuery(id+"F3.imprint","IMPRINT",EDGE,{"derivedFrom":subQ60}),1.0]])]})])],"isStart":true});var subQ191=makeQuery(id+"F38.boolean.opBoolean","INTERSECT",EDGE,{"derivedFrom":[makeQuery(id+"F37.boolean.opBoolean","SPLIT",FACE,{"disambiguationData":[TD([subQ127])],"derivedFrom":makeQuery(id+"F36.boolean.opBoolean","SPLIT",FACE,{"disambiguationData":[TD([subQ127])],"derivedFrom":makeQuery(id+"F35.boolean.opBoolean","SPLIT",FACE,{"disambiguationData":[TD([subQ127])],"derivedFrom":makeQuery(id+"F34.boolean.opBoolean","SPLIT",FACE,{"disambiguationData":[TD([subQ127])],"derivedFrom":makeQuery(id+"F33.boolean.opBoolean","SPLIT",FACE,{"disambiguationData":[TD([subQ127])],"derivedFrom":makeQuery(id+"F32.boolean.opBoolean","SPLIT",FACE,{"disambiguationData":[TD([subQ127])],"derivedFrom":makeQuery(id+"F31.boolean.opBoolean","SPLIT",FACE,{"disambiguationData":[TD([subQ127])],"derivedFrom":makeQuery(id+"F30.boolean.opBoolean","SPLIT",FACE,{"disambiguationData":[TD([subQ162])],"derivedFrom":makeQuery(id+"F29.boolean.opBoolean","SPLIT",FACE,{"disambiguationData":[TD([subQ162])],"derivedFrom":makeQuery(id+"F28.boolean.opBoolean","SPLIT",FACE,{"disambiguationData":[TD([subQ162])],"derivedFrom":makeQuery(id+"F27.boolean.opBoolean","SPLIT",FACE,{"disambiguationData":[TD([subQ162])],"derivedFrom":makeQuery(id+"F26.boolean.opBoolean","SPLIT",FACE,{"disambiguationData":[TD([subQ162])],"derivedFrom":makeQuery(id+"F25.boolean.opBoolean","SPLIT",FACE,{"disambiguationData":[TD([subQ162])],"derivedFrom":makeQuery(id+"F24.boolean.opBoolean","SPLIT",FACE,{"disambiguationData":[TD([subQ162])],"derivedFrom":makeQuery(id+"F1.opRevolve","SWEPT_FACE",FACE,{"disambiguationData":[OSD([sQuery(id+"F0.wireOp",EDGE,"E13")])]})})})})})})})})})})})})})})}),subQ10]});Q44=makeQuery(id+"F48.opFillet","BLEND_EDGE",EDGE,{"blendedFrom":[makeQuery(id+"F47.opFillet","TWEAK_EDGE",EDGE,{"derivedFrom":[makeQuery(id+"F45.opFillet","BLEND_VERTEX",VERTEX,{"blendedFrom":[subQ191,subQ10,subQ119],"blendedInto":[subQ10,subQ119]}),makeQuery(id+"F45.opFillet","BLEND_VERTEX",VERTEX,{"blendedFrom":[subQ191,makeQuery(id+"F42.boolean.opBoolean","MERGE",FACE,{"derivedFrom":[subQ2,subQ1]}),subQ119],"blendedInto":[makeQuery(id+"F42.boolean.opBoolean","MERGE",FACE,{"derivedFrom":[subQ2,subQ1]}),subQ119]})]}),makeQuery(id+"F47.opFillet","BLEND_FACE",FACE,{"disambiguationData":[OSD([subQ0,subQ11]),TDD([makeQuery(id+"F42.boolean.opBoolean","COPY",EDGE,{"disambiguationData":[TD([makeQuery(id+"F23.opLoft","SWEPT_FACE",FACE,{"disambiguationData":[OSD([sQuery(id+"F3.wireOp",EDGE,"E20.8.0"),subQ115,subQ113,subQ112,subQ111,sQuery(id+"F22.wireOp",EDGE,"E27.right")])]})])],"derivedFrom":subQ13})])]}),makeQuery(id+"F47.opFillet","BLEND_FACE",FACE,{"disambiguationData":[OSD([subQ0,subQ11]),TDD([makeQuery(id+"F42.boolean.opBoolean","COPY",EDGE,{"disambiguationData":[TD([subQ110])],"derivedFrom":subQ13})])]}),makeQuery(id+"F47.opFillet","BLEND_FACE",FACE,{"disambiguationData":[OSD([subQ0,subQ11]),TDD([makeQuery(id+"F42.boolean.opBoolean","COPY",EDGE,{"disambiguationData":[TD([subQ103])],"derivedFrom":subQ13})])]}),makeQuery(id+"F47.opFillet","BLEND_FACE",FACE,{"disambiguationData":[OSD([subQ0,subQ11]),TDD([makeQuery(id+"F42.boolean.opBoolean","COPY",EDGE,{"disambiguationData":[TD([subQ97])],"derivedFrom":subQ13})])]}),makeQuery(id+"F47.opFillet","BLEND_FACE",FACE,{"disambiguationData":[OSD([subQ0,subQ11]),TDD([makeQuery(id+"F42.boolean.opBoolean","COPY",EDGE,{"disambiguationData":[TD([subQ90])],"derivedFrom":subQ13})])]}),makeQuery(id+"F47.opFillet","BLEND_FACE",FACE,{"disambiguationData":[OSD([subQ0,subQ11]),TDD([makeQuery(id+"F42.boolean.opBoolean","COPY",EDGE,{"disambiguationData":[TD([subQ83])],"derivedFrom":subQ13})])]}),makeQuery(id+"F47.opFillet","BLEND_FACE",FACE,{"disambiguationData":[OSD([subQ0,subQ11]),TDD([makeQuery(id+"F42.boolean.opBoolean","COPY",EDGE,{"disambiguationData":[TD([subQ76])],"derivedFrom":subQ13})])]}),makeQuery(id+"F47.opFillet","BLEND_FACE",FACE,{"disambiguationData":[OSD([subQ0,subQ11]),TDD([makeQuery(id+"F42.boolean.opBoolean","COPY",EDGE,{"disambiguationData":[TD([subQ68])],"derivedFrom":subQ13})])]}),makeQuery(id+"F47.opFillet","BLEND_FACE",FACE,{"disambiguationData":[OSD([subQ0,subQ11]),TDD([makeQuery(id+"F42.boolean.opBoolean","COPY",EDGE,{"disambiguationData":[TD([subQ62])],"derivedFrom":subQ13})])]}),makeQuery(id+"F47.opFillet","BLEND_FACE",FACE,{"disambiguationData":[OSD([subQ0,subQ11]),TDD([makeQuery(id+"F42.boolean.opBoolean","COPY",EDGE,{"disambiguationData":[TD([subQ55])],"derivedFrom":subQ13})])]}),makeQuery(id+"F47.opFillet","BLEND_FACE",FACE,{"disambiguationData":[OSD([subQ0,subQ11]),TDD([makeQuery(id+"F42.boolean.opBoolean","COPY",EDGE,{"disambiguationData":[TD([subQ48])],"derivedFrom":subQ13})])]}),makeQuery(id+"F47.opFillet","BLEND_FACE",FACE,{"disambiguationData":[OSD([subQ0,subQ11]),TDD([makeQuery(id+"F42.boolean.opBoolean","COPY",EDGE,{"disambiguationData":[TD([subQ41])],"derivedFrom":subQ13})])]}),makeQuery(id+"F47.opFillet","BLEND_FACE",FACE,{"disambiguationData":[OSD([subQ0,subQ11]),TDD([makeQuery(id+"F42.boolean.opBoolean","COPY",EDGE,{"disambiguationData":[TD([subQ34])],"derivedFrom":subQ13})])]}),makeQuery(id+"F47.opFillet","BLEND_FACE",FACE,{"disambiguationData":[OSD([subQ0,subQ11]),TDD([makeQuery(id+"F42.boolean.opBoolean","COPY",EDGE,{"disambiguationData":[TD([subQ27])],"derivedFrom":subQ13})])]}),makeQuery(id+"F47.opFillet","BLEND_FACE",FACE,{"disambiguationData":[OSD([subQ0,subQ11]),TDD([makeQuery(id+"F42.boolean.opBoolean","COPY",EDGE,{"disambiguationData":[TD([subQ19])],"derivedFrom":subQ13})])]}),makeQuery(id+"F47.opFillet","BLEND_FACE",FACE,{"disambiguationData":[OSD([subQ0,subQ11]),TDD([makeQuery(id+"F42.boolean.opBoolean","COPY",EDGE,{"disambiguationData":[TD([subQ10])],"derivedFrom":subQ13})])]})],"blendedInto":[makeQuery(id+"F47.opFillet","BLEND_FACE",FACE,{"disambiguationData":[OSD([subQ0,subQ11]),TDD([makeQuery(id+"F42.boolean.opBoolean","COPY",EDGE,{"disambiguationData":[TD([makeQuery(id+"F23.opLoft","SWEPT_FACE",FACE,{"disambiguationData":[OSD([sQuery(id+"F3.wireOp",EDGE,"E20.8.0"),subQ115,subQ113,subQ112,subQ111,sQuery(id+"F22.wireOp",EDGE,"E27.right")])]})])],"derivedFrom":subQ13})])]}),makeQuery(id+"F47.opFillet","BLEND_FACE",FACE,{"disambiguationData":[OSD([subQ0,subQ11]),TDD([makeQuery(id+"F42.boolean.opBoolean","COPY",EDGE,{"disambiguationData":[TD([subQ110])],"derivedFrom":subQ13})])]}),makeQuery(id+"F47.opFillet","BLEND_FACE",FACE,{"disambiguationData":[OSD([subQ0,subQ11]),TDD([makeQuery(id+"F42.boolean.opBoolean","COPY",EDGE,{"disambiguationData":[TD([subQ103])],"derivedFrom":subQ13})])]}),makeQuery(id+"F47.opFillet","BLEND_FACE",FACE,{"disambiguationData":[OSD([subQ0,subQ11]),TDD([makeQuery(id+"F42.boolean.opBoolean","COPY",EDGE,{"disambiguationData":[TD([subQ97])],"derivedFrom":subQ13})])]}),makeQuery(id+"F47.opFillet","BLEND_FACE",FACE,{"disambiguationData":[OSD([subQ0,subQ11]),TDD([makeQuery(id+"F42.boolean.opBoolean","COPY",EDGE,{"disambiguationData":[TD([subQ90])],"derivedFrom":subQ13})])]}),makeQuery(id+"F47.opFillet","BLEND_FACE",FACE,{"disambiguationData":[OSD([subQ0,subQ11]),TDD([makeQuery(id+"F42.boolean.opBoolean","COPY",EDGE,{"disambiguationData":[TD([subQ83])],"derivedFrom":subQ13})])]}),makeQuery(id+"F47.opFillet","BLEND_FACE",FACE,{"disambiguationData":[OSD([subQ0,subQ11]),TDD([makeQuery(id+"F42.boolean.opBoolean","COPY",EDGE,{"disambiguationData":[TD([subQ76])],"derivedFrom":subQ13})])]}),makeQuery(id+"F47.opFillet","BLEND_FACE",FACE,{"disambiguationData":[OSD([subQ0,subQ11]),TDD([makeQuery(id+"F42.boolean.opBoolean","COPY",EDGE,{"disambiguationData":[TD([subQ68])],"derivedFrom":subQ13})])]}),makeQuery(id+"F47.opFillet","BLEND_FACE",FACE,{"disambiguationData":[OSD([subQ0,subQ11]),TDD([makeQuery(id+"F42.boolean.opBoolean","COPY",EDGE,{"disambiguationData":[TD([subQ62])],"derivedFrom":subQ13})])]}),makeQuery(id+"F47.opFillet","BLEND_FACE",FACE,{"disambiguationData":[OSD([subQ0,subQ11]),TDD([makeQuery(id+"F42.boolean.opBoolean","COPY",EDGE,{"disambiguationData":[TD([subQ55])],"derivedFrom":subQ13})])]}),makeQuery(id+"F47.opFillet","BLEND_FACE",FACE,{"disambiguationData":[OSD([subQ0,subQ11]),TDD([makeQuery(id+"F42.boolean.opBoolean","COPY",EDGE,{"disambiguationData":[TD([subQ48])],"derivedFrom":subQ13})])]}),makeQuery(id+"F47.opFillet","BLEND_FACE",FACE,{"disambiguationData":[OSD([subQ0,subQ11]),TDD([makeQuery(id+"F42.boolean.opBoolean","COPY",EDGE,{"disambiguationData":[TD([subQ41])],"derivedFrom":subQ13})])]}),makeQuery(id+"F47.opFillet","BLEND_FACE",FACE,{"disambiguationData":[OSD([subQ0,subQ11]),TDD([makeQuery(id+"F42.boolean.opBoolean","COPY",EDGE,{"disambiguationData":[TD([subQ34])],"derivedFrom":subQ13})])]}),makeQuery(id+"F47.opFillet","BLEND_FACE",FACE,{"disambiguationData":[OSD([subQ0,subQ11]),TDD([makeQuery(id+"F42.boolean.opBoolean","COPY",EDGE,{"disambiguationData":[TD([subQ27])],"derivedFrom":subQ13})])]}),makeQuery(id+"F47.opFillet","BLEND_FACE",FACE,{"disambiguationData":[OSD([subQ0,subQ11]),TDD([makeQuery(id+"F42.boolean.opBoolean","COPY",EDGE,{"disambiguationData":[TD([subQ19])],"derivedFrom":subQ13})])]}),makeQuery(id+"F47.opFillet","BLEND_FACE",FACE,{"disambiguationData":[OSD([subQ0,subQ11]),TDD([makeQuery(id+"F42.boolean.opBoolean","COPY",EDGE,{"disambiguationData":[TD([subQ10])],"derivedFrom":subQ13})])]})]});}
            var Q45;
            {var subQ0=sQuery(id+"F41.wireOp",EDGE,"E34");var subQ1=sQuery(id+"F41.wireOp",EDGE,"E32");Q45=makeQuery(id+"F42.boolean.opBoolean","INTERSECT",EDGE,{"derivedFrom":[makeQuery(id+"F37.opLoft","SWEPT_FACE",FACE,{"disambiguationData":[OSD([sQuery(id+"F3.wireOp",EDGE,"E20.6.0"),sQuery(id+"F3.wireOp",EDGE,"E20.6.1"),sQuery(id+"F3.wireOp",EDGE,"E20.6.3"),sQuery(id+"F22.wireOp",EDGE,"E28.14.1"),sQuery(id+"F22.wireOp",EDGE,"E28.14.2"),sQuery(id+"F22.wireOp",EDGE,"E28.14.3")])]}),makeQuery(id+"F42.opRevolve","SWEPT_FACE",FACE,{"disambiguationData":[OSD([subQ1]),TDD([makeQuery(id+"F41.imprint","IMPRINT",EDGE,{"disambiguationData":[TD([[makeQuery(id+"F41.imprint","INTERSECT",VERTEX,{"disambiguationData":[OD(0.0)],"derivedFrom":[subQ1,subQ0]}),-1.0]])],"derivedFrom":subQ1})])]})]});}
            var Q46;
            {var subQ0=sQuery(id+"F22.wireOp",EDGE,"E28.15.3");var subQ1=sQuery(id+"F22.wireOp",EDGE,"E28.15.2");var subQ2=sQuery(id+"F22.wireOp",EDGE,"E28.15.1");var subQ3=sQuery(id+"F3.wireOp",EDGE,"E20.7.3");var subQ4=sQuery(id+"F3.wireOp",EDGE,"E20.7.1");var subQ5=sQuery(id+"F22.wireOp",EDGE,"E28.15.0");var subQ6=makeQuery(id+"F38.opLoft","SWEPT_FACE",FACE,{"disambiguationData":[OSD([subQ4,sQuery(id+"F3.wireOp",EDGE,"E20.7.2"),subQ3,subQ5,subQ1,subQ0])]});var subQ7=sQuery(id+"F41.wireOp",EDGE,"E34");var subQ8=sQuery(id+"F41.wireOp",EDGE,"E32");Q46=makeQuery(id+"F44.opFillet","BLEND_EDGE",EDGE,{"blendedFrom":[makeQuery(id+"F40.boolean.opBoolean","INTERSECT",EDGE,{"derivedFrom":[subQ6,makeQuery(id+"F40.opExtrude","CAP_FACE",FACE,{"disambiguationData":[OSD([sQuery(id+"F39.wireOp",EDGE,"E29"),sQuery(id+"F39.wireOp",EDGE,"E30")])],"isStart":true})]}),makeQuery(id+"F42.boolean.opBoolean","COPY",FACE,{"disambiguationData":[TD([makeQuery(id+"F38.opLoft","SWEPT_FACE",FACE,{"disambiguationData":[OSD([sQuery(id+"F3.wireOp",EDGE,"E20.7.0"),subQ4,subQ3,subQ2,subQ1,subQ0])]})])],"derivedFrom":makeQuery(id+"F42.opRevolve","SWEPT_FACE",FACE,{"disambiguationData":[OSD([subQ8]),TDD([makeQuery(id+"F41.imprint","IMPRINT",EDGE,{"disambiguationData":[TD([[makeQuery(id+"F41.imprint","INTERSECT",VERTEX,{"disambiguationData":[OD(0.0)],"derivedFrom":[subQ8,subQ7]}),-1.0]])],"derivedFrom":subQ8})])]})})],"blendedInto":[makeQuery(id+"F42.boolean.opBoolean","COPY",FACE,{"disambiguationData":[TD([makeQuery(id+"F38.opLoft","SWEPT_FACE",FACE,{"disambiguationData":[OSD([sQuery(id+"F3.wireOp",EDGE,"E20.7.0"),subQ4,subQ3,subQ2,subQ1,subQ0])]})])],"derivedFrom":makeQuery(id+"F42.opRevolve","SWEPT_FACE",FACE,{"disambiguationData":[OSD([subQ8]),TDD([makeQuery(id+"F41.imprint","IMPRINT",EDGE,{"disambiguationData":[TD([[makeQuery(id+"F41.imprint","INTERSECT",VERTEX,{"disambiguationData":[OD(0.0)],"derivedFrom":[subQ8,subQ7]}),-1.0]])],"derivedFrom":subQ8})])]})})]});}
            var Q47;
            {var subQ0=sQuery(id+"F41.wireOp",EDGE,"E37");var subQ1=makeQuery(id+"F42.opRevolve","SWEPT_FACE",FACE,{"disambiguationData":[OSD([subQ0])]});var subQ2=makeQuery(id+"F40.opExtrude","CAP_FACE",FACE,{"disambiguationData":[OSD([sQuery(id+"F39.wireOp",EDGE,"E29"),sQuery(id+"F39.wireOp",EDGE,"E30")])],"isStart":true});var subQ3=sQuery(id+"F22.wireOp",EDGE,"E28.15.3");var subQ4=sQuery(id+"F22.wireOp",EDGE,"E28.15.2");var subQ5=sQuery(id+"F3.wireOp",EDGE,"E20.7.3");var subQ7=sQuery(id+"F3.wireOp",EDGE,"E20.7.1");var subQ8=sQuery(id+"F3.wireOp",EDGE,"E20.7.0");var subQ9=sQuery(id+"F41.wireOp",EDGE,"E38");var subQ10=makeQuery(id+"F42.opRevolve","SWEPT_FACE",FACE,{"disambiguationData":[OSD([subQ9])]});var subQ11=makeQuery(id+"F42.opRevolve","SWEPT_EDGE",EDGE,{"disambiguationData":[OSD([subQ0,subQ9])]});var subQ12=sQuery(id+"F22.wireOp",EDGE,"E28.14.3");var subQ13=sQuery(id+"F22.wireOp",EDGE,"E28.14.2");var subQ14=sQuery(id+"F3.wireOp",EDGE,"E20.6.3");var subQ15=sQuery(id+"F3.wireOp",EDGE,"E20.6.1");var subQ16=sQuery(id+"F3.wireOp",EDGE,"E20.6.0");var subQ17=makeQuery(id+"F37.opLoft","SWEPT_FACE",FACE,{"disambiguationData":[OSD([subQ16,subQ15,subQ14,sQuery(id+"F22.wireOp",EDGE,"E28.14.1"),subQ13,subQ12])]});var subQ20=sQuery(id+"F22.wireOp",EDGE,"E28.13.3");var subQ21=sQuery(id+"F22.wireOp",EDGE,"E28.13.2");var subQ22=sQuery(id+"F3.wireOp",EDGE,"E20.5.3");var subQ24=sQuery(id+"F3.wireOp",EDGE,"E20.5.1");var subQ25=sQuery(id+"F3.wireOp",EDGE,"E20.5.0");var subQ26=makeQuery(id+"F36.opLoft","SWEPT_FACE",FACE,{"disambiguationData":[OSD([subQ25,subQ24,subQ22,sQuery(id+"F22.wireOp",EDGE,"E28.13.1"),subQ21,subQ20])]});var subQ27=sQuery(id+"F22.wireOp",EDGE,"E28.12.3");var subQ28=sQuery(id+"F22.wireOp",EDGE,"E28.12.2");var subQ29=sQuery(id+"F3.wireOp",EDGE,"E20.4.3");var subQ31=sQuery(id+"F3.wireOp",EDGE,"E20.4.1");var subQ32=sQuery(id+"F3.wireOp",EDGE,"E20.4.0");var subQ33=makeQuery(id+"F35.opLoft","SWEPT_FACE",FACE,{"disambiguationData":[OSD([subQ32,subQ31,subQ29,sQuery(id+"F22.wireOp",EDGE,"E28.12.1"),subQ28,subQ27])]});var subQ34=sQuery(id+"F22.wireOp",EDGE,"E28.11.3");var subQ35=sQuery(id+"F22.wireOp",EDGE,"E28.11.2");var subQ36=sQuery(id+"F3.wireOp",EDGE,"E20.3.3");var subQ38=sQuery(id+"F3.wireOp",EDGE,"E20.3.1");var subQ39=sQuery(id+"F3.wireOp",EDGE,"E20.3.0");var subQ40=makeQuery(id+"F34.opLoft","SWEPT_FACE",FACE,{"disambiguationData":[OSD([subQ39,subQ38,subQ36,sQuery(id+"F22.wireOp",EDGE,"E28.11.1"),subQ35,subQ34])]});var subQ41=sQuery(id+"F22.wireOp",EDGE,"E28.10.3");var subQ42=sQuery(id+"F22.wireOp",EDGE,"E28.10.2");var subQ43=sQuery(id+"F3.wireOp",EDGE,"E20.2.3");var subQ45=sQuery(id+"F3.wireOp",EDGE,"E20.2.1");var subQ46=sQuery(id+"F3.wireOp",EDGE,"E20.2.0");var subQ47=makeQuery(id+"F33.opLoft","SWEPT_FACE",FACE,{"disambiguationData":[OSD([subQ46,subQ45,subQ43,sQuery(id+"F22.wireOp",EDGE,"E28.10.1"),subQ42,subQ41])]});var subQ48=sQuery(id+"F22.wireOp",EDGE,"E28.9.3");var subQ49=sQuery(id+"F22.wireOp",EDGE,"E28.9.2");var subQ50=sQuery(id+"F3.wireOp",EDGE,"E20.1.3");var subQ52=sQuery(id+"F3.wireOp",EDGE,"E20.1.1");var subQ53=sQuery(id+"F3.wireOp",EDGE,"E20.1.0");var subQ54=makeQuery(id+"F32.opLoft","SWEPT_FACE",FACE,{"disambiguationData":[OSD([subQ53,subQ52,subQ50,sQuery(id+"F22.wireOp",EDGE,"E28.9.1"),subQ49,subQ48])]});var subQ55=sQuery(id+"F22.wireOp",EDGE,"E28.8.3");var subQ56=sQuery(id+"F22.wireOp",EDGE,"E28.8.2");var subQ58=sQuery(id+"F3.wireOp",EDGE,"E18.top");var subQ59=sQuery(id+"F3.wireOp",EDGE,"E18.bottom");var subQ60=sQuery(id+"F3.wireOp",EDGE,"E18.left");var subQ61=makeQuery(id+"F31.opLoft","SWEPT_FACE",FACE,{"disambiguationData":[OSD([subQ59,subQ58,subQ60,sQuery(id+"F22.wireOp",EDGE,"E28.8.1"),subQ56,subQ55])]});var subQ62=sQuery(id+"F22.wireOp",EDGE,"E28.7.3");var subQ63=sQuery(id+"F22.wireOp",EDGE,"E28.7.2");var subQ64=sQuery(id+"F3.wireOp",EDGE,"E20.15.3");var subQ65=sQuery(id+"F3.wireOp",EDGE,"E20.15.1");var subQ66=sQuery(id+"F3.wireOp",EDGE,"E20.15.0");var subQ67=makeQuery(id+"F30.opLoft","SWEPT_FACE",FACE,{"disambiguationData":[OSD([subQ66,subQ65,subQ64,sQuery(id+"F22.wireOp",EDGE,"E28.7.1"),subQ63,subQ62])]});var subQ69=sQuery(id+"F22.wireOp",EDGE,"E28.6.3");var subQ70=sQuery(id+"F22.wireOp",EDGE,"E28.6.2");var subQ71=sQuery(id+"F3.wireOp",EDGE,"E20.14.3");var subQ73=sQuery(id+"F3.wireOp",EDGE,"E20.14.1");var subQ74=sQuery(id+"F3.wireOp",EDGE,"E20.14.0");var subQ75=makeQuery(id+"F29.opLoft","SWEPT_FACE",FACE,{"disambiguationData":[OSD([subQ74,subQ73,subQ71,sQuery(id+"F22.wireOp",EDGE,"E28.6.1"),subQ70,subQ69])]});var subQ76=sQuery(id+"F22.wireOp",EDGE,"E28.5.3");var subQ77=sQuery(id+"F22.wireOp",EDGE,"E28.5.2");var subQ78=sQuery(id+"F3.wireOp",EDGE,"E20.13.3");var subQ80=sQuery(id+"F3.wireOp",EDGE,"E20.13.1");var subQ81=sQuery(id+"F3.wireOp",EDGE,"E20.13.0");var subQ82=makeQuery(id+"F28.opLoft","SWEPT_FACE",FACE,{"disambiguationData":[OSD([subQ81,subQ80,subQ78,sQuery(id+"F22.wireOp",EDGE,"E28.5.1"),subQ77,subQ76])]});var subQ83=sQuery(id+"F22.wireOp",EDGE,"E28.4.3");var subQ84=sQuery(id+"F22.wireOp",EDGE,"E28.4.2");var subQ85=sQuery(id+"F3.wireOp",EDGE,"E20.12.3");var subQ87=sQuery(id+"F3.wireOp",EDGE,"E20.12.1");var subQ88=sQuery(id+"F3.wireOp",EDGE,"E20.12.0");var subQ89=makeQuery(id+"F27.opLoft","SWEPT_FACE",FACE,{"disambiguationData":[OSD([subQ88,subQ87,subQ85,sQuery(id+"F22.wireOp",EDGE,"E28.4.1"),subQ84,subQ83])]});var subQ90=sQuery(id+"F22.wireOp",EDGE,"E28.3.3");var subQ91=sQuery(id+"F22.wireOp",EDGE,"E28.3.2");var subQ92=sQuery(id+"F3.wireOp",EDGE,"E20.11.3");var subQ94=sQuery(id+"F3.wireOp",EDGE,"E20.11.1");var subQ95=sQuery(id+"F3.wireOp",EDGE,"E20.11.0");var subQ96=makeQuery(id+"F26.opLoft","SWEPT_FACE",FACE,{"disambiguationData":[OSD([subQ95,subQ94,subQ92,sQuery(id+"F22.wireOp",EDGE,"E28.3.1"),subQ91,subQ90])]});var subQ97=sQuery(id+"F22.wireOp",EDGE,"E28.2.3");var subQ98=sQuery(id+"F22.wireOp",EDGE,"E28.2.2");var subQ99=sQuery(id+"F3.wireOp",EDGE,"E20.10.3");var subQ100=sQuery(id+"F3.wireOp",EDGE,"E20.10.1");var subQ101=sQuery(id+"F3.wireOp",EDGE,"E20.10.0");var subQ102=makeQuery(id+"F25.opLoft","SWEPT_FACE",FACE,{"disambiguationData":[OSD([subQ101,subQ100,subQ99,sQuery(id+"F22.wireOp",EDGE,"E28.2.1"),subQ98,subQ97])]});var subQ104=sQuery(id+"F22.wireOp",EDGE,"E28.1.3");var subQ105=sQuery(id+"F22.wireOp",EDGE,"E28.1.2");var subQ106=sQuery(id+"F3.wireOp",EDGE,"E20.9.3");var subQ107=sQuery(id+"F3.wireOp",EDGE,"E20.9.1");var subQ108=sQuery(id+"F3.wireOp",EDGE,"E20.9.0");var subQ109=makeQuery(id+"F24.opLoft","SWEPT_FACE",FACE,{"disambiguationData":[OSD([subQ108,subQ107,subQ106,sQuery(id+"F22.wireOp",EDGE,"E28.1.1"),subQ105,subQ104])]});var subQ110=sQuery(id+"F22.wireOp",EDGE,"E27.top");var subQ111=sQuery(id+"F22.wireOp",EDGE,"E27.bottom");var subQ112=sQuery(id+"F3.wireOp",EDGE,"E20.8.3");var subQ114=sQuery(id+"F3.wireOp",EDGE,"E20.8.1");var subQ118=makeQuery(id+"F42.boolean.opBoolean","COPY",FACE,{"disambiguationData":[TD([subQ17])],"derivedFrom":subQ10});var subQ126=makeQuery(id+"F14.opLoft","CAP_FACE",FACE,{"disambiguationData":[OSD([makeQuery(id+"F3.imprint","IMPRINT",FACE,{"disambiguationData":[TD([[makeQuery(id+"F3.imprint","IMPRINT",EDGE,{"derivedFrom":subQ8}),-1.0]])]})])],"isStart":true});var subQ161=makeQuery(id+"F5.opLoft","CAP_FACE",FACE,{"disambiguationData":[OSD([makeQuery(id+"F3.imprint","IMPRINT",FACE,{"disambiguationData":[TD([[makeQuery(id+"F3.imprint","IMPRINT",EDGE,{"derivedFrom":subQ59}),1.0]])]})])],"isStart":true});var subQ190=makeQuery(id+"F37.boolean.opBoolean","INTERSECT",EDGE,{"derivedFrom":[makeQuery(id+"F36.boolean.opBoolean","SPLIT",FACE,{"disambiguationData":[TD([subQ126])],"derivedFrom":makeQuery(id+"F35.boolean.opBoolean","SPLIT",FACE,{"disambiguationData":[TD([subQ126])],"derivedFrom":makeQuery(id+"F34.boolean.opBoolean","SPLIT",FACE,{"disambiguationData":[TD([subQ126])],"derivedFrom":makeQuery(id+"F33.boolean.opBoolean","SPLIT",FACE,{"disambiguationData":[TD([subQ126])],"derivedFrom":makeQuery(id+"F32.boolean.opBoolean","SPLIT",FACE,{"disambiguationData":[TD([subQ126])],"derivedFrom":makeQuery(id+"F31.boolean.opBoolean","SPLIT",FACE,{"disambiguationData":[TD([subQ126])],"derivedFrom":makeQuery(id+"F30.boolean.opBoolean","SPLIT",FACE,{"disambiguationData":[TD([subQ161])],"derivedFrom":makeQuery(id+"F29.boolean.opBoolean","SPLIT",FACE,{"disambiguationData":[TD([subQ161])],"derivedFrom":makeQuery(id+"F28.boolean.opBoolean","SPLIT",FACE,{"disambiguationData":[TD([subQ161])],"derivedFrom":makeQuery(id+"F27.boolean.opBoolean","SPLIT",FACE,{"disambiguationData":[TD([subQ161])],"derivedFrom":makeQuery(id+"F26.boolean.opBoolean","SPLIT",FACE,{"disambiguationData":[TD([subQ161])],"derivedFrom":makeQuery(id+"F25.boolean.opBoolean","SPLIT",FACE,{"disambiguationData":[TD([subQ161])],"derivedFrom":makeQuery(id+"F24.boolean.opBoolean","SPLIT",FACE,{"disambiguationData":[TD([subQ161])],"derivedFrom":makeQuery(id+"F1.opRevolve","SWEPT_FACE",FACE,{"disambiguationData":[OSD([sQuery(id+"F0.wireOp",EDGE,"E13")])]})})})})})})})})})})})})})}),subQ17]});Q47=makeQuery(id+"F48.opFillet","BLEND_EDGE",EDGE,{"blendedFrom":[makeQuery(id+"F47.opFillet","TWEAK_EDGE",EDGE,{"derivedFrom":[makeQuery(id+"F45.opFillet","BLEND_VERTEX",VERTEX,{"blendedFrom":[subQ190,subQ17,subQ118],"blendedInto":[subQ17,subQ118]}),makeQuery(id+"F45.opFillet","BLEND_VERTEX",VERTEX,{"blendedFrom":[subQ190,makeQuery(id+"F42.boolean.opBoolean","MERGE",FACE,{"derivedFrom":[subQ2,subQ1]}),subQ118],"blendedInto":[makeQuery(id+"F42.boolean.opBoolean","MERGE",FACE,{"derivedFrom":[subQ2,subQ1]}),subQ118]})]}),makeQuery(id+"F47.opFillet","BLEND_FACE",FACE,{"disambiguationData":[OSD([subQ0,subQ9]),TDD([makeQuery(id+"F42.boolean.opBoolean","COPY",EDGE,{"disambiguationData":[TD([makeQuery(id+"F23.opLoft","SWEPT_FACE",FACE,{"disambiguationData":[OSD([sQuery(id+"F3.wireOp",EDGE,"E20.8.0"),subQ114,subQ112,subQ111,subQ110,sQuery(id+"F22.wireOp",EDGE,"E27.right")])]})])],"derivedFrom":subQ11})])]}),makeQuery(id+"F47.opFillet","BLEND_FACE",FACE,{"disambiguationData":[OSD([subQ0,subQ9]),TDD([makeQuery(id+"F42.boolean.opBoolean","COPY",EDGE,{"disambiguationData":[TD([subQ109])],"derivedFrom":subQ11})])]}),makeQuery(id+"F47.opFillet","BLEND_FACE",FACE,{"disambiguationData":[OSD([subQ0,subQ9]),TDD([makeQuery(id+"F42.boolean.opBoolean","COPY",EDGE,{"disambiguationData":[TD([subQ102])],"derivedFrom":subQ11})])]}),makeQuery(id+"F47.opFillet","BLEND_FACE",FACE,{"disambiguationData":[OSD([subQ0,subQ9]),TDD([makeQuery(id+"F42.boolean.opBoolean","COPY",EDGE,{"disambiguationData":[TD([subQ96])],"derivedFrom":subQ11})])]}),makeQuery(id+"F47.opFillet","BLEND_FACE",FACE,{"disambiguationData":[OSD([subQ0,subQ9]),TDD([makeQuery(id+"F42.boolean.opBoolean","COPY",EDGE,{"disambiguationData":[TD([subQ89])],"derivedFrom":subQ11})])]}),makeQuery(id+"F47.opFillet","BLEND_FACE",FACE,{"disambiguationData":[OSD([subQ0,subQ9]),TDD([makeQuery(id+"F42.boolean.opBoolean","COPY",EDGE,{"disambiguationData":[TD([subQ82])],"derivedFrom":subQ11})])]}),makeQuery(id+"F47.opFillet","BLEND_FACE",FACE,{"disambiguationData":[OSD([subQ0,subQ9]),TDD([makeQuery(id+"F42.boolean.opBoolean","COPY",EDGE,{"disambiguationData":[TD([subQ75])],"derivedFrom":subQ11})])]}),makeQuery(id+"F47.opFillet","BLEND_FACE",FACE,{"disambiguationData":[OSD([subQ0,subQ9]),TDD([makeQuery(id+"F42.boolean.opBoolean","COPY",EDGE,{"disambiguationData":[TD([subQ67])],"derivedFrom":subQ11})])]}),makeQuery(id+"F47.opFillet","BLEND_FACE",FACE,{"disambiguationData":[OSD([subQ0,subQ9]),TDD([makeQuery(id+"F42.boolean.opBoolean","COPY",EDGE,{"disambiguationData":[TD([subQ61])],"derivedFrom":subQ11})])]}),makeQuery(id+"F47.opFillet","BLEND_FACE",FACE,{"disambiguationData":[OSD([subQ0,subQ9]),TDD([makeQuery(id+"F42.boolean.opBoolean","COPY",EDGE,{"disambiguationData":[TD([subQ54])],"derivedFrom":subQ11})])]}),makeQuery(id+"F47.opFillet","BLEND_FACE",FACE,{"disambiguationData":[OSD([subQ0,subQ9]),TDD([makeQuery(id+"F42.boolean.opBoolean","COPY",EDGE,{"disambiguationData":[TD([subQ47])],"derivedFrom":subQ11})])]}),makeQuery(id+"F47.opFillet","BLEND_FACE",FACE,{"disambiguationData":[OSD([subQ0,subQ9]),TDD([makeQuery(id+"F42.boolean.opBoolean","COPY",EDGE,{"disambiguationData":[TD([subQ40])],"derivedFrom":subQ11})])]}),makeQuery(id+"F47.opFillet","BLEND_FACE",FACE,{"disambiguationData":[OSD([subQ0,subQ9]),TDD([makeQuery(id+"F42.boolean.opBoolean","COPY",EDGE,{"disambiguationData":[TD([subQ33])],"derivedFrom":subQ11})])]}),makeQuery(id+"F47.opFillet","BLEND_FACE",FACE,{"disambiguationData":[OSD([subQ0,subQ9]),TDD([makeQuery(id+"F42.boolean.opBoolean","COPY",EDGE,{"disambiguationData":[TD([subQ26])],"derivedFrom":subQ11})])]}),makeQuery(id+"F47.opFillet","BLEND_FACE",FACE,{"disambiguationData":[OSD([subQ0,subQ9]),TDD([makeQuery(id+"F42.boolean.opBoolean","COPY",EDGE,{"disambiguationData":[TD([subQ17])],"derivedFrom":subQ11})])]}),makeQuery(id+"F47.opFillet","BLEND_FACE",FACE,{"disambiguationData":[OSD([subQ0,subQ9]),TDD([makeQuery(id+"F42.boolean.opBoolean","COPY",EDGE,{"disambiguationData":[TD([makeQuery(id+"F38.opLoft","SWEPT_FACE",FACE,{"disambiguationData":[OSD([subQ8,subQ7,subQ5,sQuery(id+"F22.wireOp",EDGE,"E28.15.1"),subQ4,subQ3])]})])],"derivedFrom":subQ11})])]})],"blendedInto":[makeQuery(id+"F47.opFillet","BLEND_FACE",FACE,{"disambiguationData":[OSD([subQ0,subQ9]),TDD([makeQuery(id+"F42.boolean.opBoolean","COPY",EDGE,{"disambiguationData":[TD([makeQuery(id+"F23.opLoft","SWEPT_FACE",FACE,{"disambiguationData":[OSD([sQuery(id+"F3.wireOp",EDGE,"E20.8.0"),subQ114,subQ112,subQ111,subQ110,sQuery(id+"F22.wireOp",EDGE,"E27.right")])]})])],"derivedFrom":subQ11})])]}),makeQuery(id+"F47.opFillet","BLEND_FACE",FACE,{"disambiguationData":[OSD([subQ0,subQ9]),TDD([makeQuery(id+"F42.boolean.opBoolean","COPY",EDGE,{"disambiguationData":[TD([subQ109])],"derivedFrom":subQ11})])]}),makeQuery(id+"F47.opFillet","BLEND_FACE",FACE,{"disambiguationData":[OSD([subQ0,subQ9]),TDD([makeQuery(id+"F42.boolean.opBoolean","COPY",EDGE,{"disambiguationData":[TD([subQ102])],"derivedFrom":subQ11})])]}),makeQuery(id+"F47.opFillet","BLEND_FACE",FACE,{"disambiguationData":[OSD([subQ0,subQ9]),TDD([makeQuery(id+"F42.boolean.opBoolean","COPY",EDGE,{"disambiguationData":[TD([subQ96])],"derivedFrom":subQ11})])]}),makeQuery(id+"F47.opFillet","BLEND_FACE",FACE,{"disambiguationData":[OSD([subQ0,subQ9]),TDD([makeQuery(id+"F42.boolean.opBoolean","COPY",EDGE,{"disambiguationData":[TD([subQ89])],"derivedFrom":subQ11})])]}),makeQuery(id+"F47.opFillet","BLEND_FACE",FACE,{"disambiguationData":[OSD([subQ0,subQ9]),TDD([makeQuery(id+"F42.boolean.opBoolean","COPY",EDGE,{"disambiguationData":[TD([subQ82])],"derivedFrom":subQ11})])]}),makeQuery(id+"F47.opFillet","BLEND_FACE",FACE,{"disambiguationData":[OSD([subQ0,subQ9]),TDD([makeQuery(id+"F42.boolean.opBoolean","COPY",EDGE,{"disambiguationData":[TD([subQ75])],"derivedFrom":subQ11})])]}),makeQuery(id+"F47.opFillet","BLEND_FACE",FACE,{"disambiguationData":[OSD([subQ0,subQ9]),TDD([makeQuery(id+"F42.boolean.opBoolean","COPY",EDGE,{"disambiguationData":[TD([subQ67])],"derivedFrom":subQ11})])]}),makeQuery(id+"F47.opFillet","BLEND_FACE",FACE,{"disambiguationData":[OSD([subQ0,subQ9]),TDD([makeQuery(id+"F42.boolean.opBoolean","COPY",EDGE,{"disambiguationData":[TD([subQ61])],"derivedFrom":subQ11})])]}),makeQuery(id+"F47.opFillet","BLEND_FACE",FACE,{"disambiguationData":[OSD([subQ0,subQ9]),TDD([makeQuery(id+"F42.boolean.opBoolean","COPY",EDGE,{"disambiguationData":[TD([subQ54])],"derivedFrom":subQ11})])]}),makeQuery(id+"F47.opFillet","BLEND_FACE",FACE,{"disambiguationData":[OSD([subQ0,subQ9]),TDD([makeQuery(id+"F42.boolean.opBoolean","COPY",EDGE,{"disambiguationData":[TD([subQ47])],"derivedFrom":subQ11})])]}),makeQuery(id+"F47.opFillet","BLEND_FACE",FACE,{"disambiguationData":[OSD([subQ0,subQ9]),TDD([makeQuery(id+"F42.boolean.opBoolean","COPY",EDGE,{"disambiguationData":[TD([subQ40])],"derivedFrom":subQ11})])]}),makeQuery(id+"F47.opFillet","BLEND_FACE",FACE,{"disambiguationData":[OSD([subQ0,subQ9]),TDD([makeQuery(id+"F42.boolean.opBoolean","COPY",EDGE,{"disambiguationData":[TD([subQ33])],"derivedFrom":subQ11})])]}),makeQuery(id+"F47.opFillet","BLEND_FACE",FACE,{"disambiguationData":[OSD([subQ0,subQ9]),TDD([makeQuery(id+"F42.boolean.opBoolean","COPY",EDGE,{"disambiguationData":[TD([subQ26])],"derivedFrom":subQ11})])]}),makeQuery(id+"F47.opFillet","BLEND_FACE",FACE,{"disambiguationData":[OSD([subQ0,subQ9]),TDD([makeQuery(id+"F42.boolean.opBoolean","COPY",EDGE,{"disambiguationData":[TD([subQ17])],"derivedFrom":subQ11})])]}),makeQuery(id+"F47.opFillet","BLEND_FACE",FACE,{"disambiguationData":[OSD([subQ0,subQ9]),TDD([makeQuery(id+"F42.boolean.opBoolean","COPY",EDGE,{"disambiguationData":[TD([makeQuery(id+"F38.opLoft","SWEPT_FACE",FACE,{"disambiguationData":[OSD([subQ8,subQ7,subQ5,sQuery(id+"F22.wireOp",EDGE,"E28.15.1"),subQ4,subQ3])]})])],"derivedFrom":subQ11})])]})]});}
            var Q48;
            {var subQ0=makeQuery(id+"F40.opExtrude","CAP_FACE",FACE,{"disambiguationData":[OSD([sQuery(id+"F39.wireOp",EDGE,"E29"),sQuery(id+"F39.wireOp",EDGE,"E30")])],"isStart":false});var subQ1=sQuery(id+"F4.wireOp",EDGE,"E26.1.3");var subQ2=sQuery(id+"F4.wireOp",EDGE,"E26.1.2");var subQ3=sQuery(id+"F3.wireOp",EDGE,"E20.1.3");var subQ4=sQuery(id+"F3.wireOp",EDGE,"E20.1.1");var subQ5=sQuery(id+"F41.wireOp",EDGE,"E35");var subQ6=makeQuery(id+"F42.opRevolve","SWEPT_FACE",FACE,{"disambiguationData":[OSD([subQ5])]});var subQ7=sQuery(id+"F41.wireOp",EDGE,"E36");var subQ8=makeQuery(id+"F42.opRevolve","SWEPT_FACE",FACE,{"disambiguationData":[OSD([subQ7])]});var subQ9=makeQuery(id+"F42.opRevolve","SWEPT_EDGE",EDGE,{"disambiguationData":[OSD([subQ5,subQ7])]});var subQ10=sQuery(id+"F4.wireOp",EDGE,"E26.2.3");var subQ11=sQuery(id+"F4.wireOp",EDGE,"E26.2.2");var subQ12=sQuery(id+"F3.wireOp",EDGE,"E20.2.3");var subQ13=sQuery(id+"F3.wireOp",EDGE,"E20.2.1");var subQ14=sQuery(id+"F4.wireOp",EDGE,"E26.3.3");var subQ15=sQuery(id+"F4.wireOp",EDGE,"E26.3.2");var subQ16=sQuery(id+"F3.wireOp",EDGE,"E20.3.3");var subQ17=sQuery(id+"F3.wireOp",EDGE,"E20.3.1");var subQ18=sQuery(id+"F4.wireOp",EDGE,"E26.4.3");var subQ19=sQuery(id+"F4.wireOp",EDGE,"E26.4.2");var subQ20=sQuery(id+"F3.wireOp",EDGE,"E20.4.3");var subQ21=sQuery(id+"F3.wireOp",EDGE,"E20.4.1");var subQ22=sQuery(id+"F4.wireOp",EDGE,"E26.5.3");var subQ23=sQuery(id+"F4.wireOp",EDGE,"E26.5.2");var subQ24=sQuery(id+"F3.wireOp",EDGE,"E20.5.3");var subQ25=sQuery(id+"F3.wireOp",EDGE,"E20.5.1");var subQ26=sQuery(id+"F4.wireOp",EDGE,"E26.6.3");var subQ27=sQuery(id+"F4.wireOp",EDGE,"E26.6.2");var subQ28=sQuery(id+"F3.wireOp",EDGE,"E20.6.3");var subQ29=sQuery(id+"F3.wireOp",EDGE,"E20.6.1");var subQ31=makeQuery(id+"F15.opLoft","SWEPT_FACE",FACE,{"disambiguationData":[OSD([sQuery(id+"F3.wireOp",EDGE,"E20.6.0"),subQ29,subQ28,sQuery(id+"F4.wireOp",EDGE,"E26.6.0"),subQ27,subQ26])]});var subQ32=sQuery(id+"F4.wireOp",EDGE,"E26.7.3");var subQ33=sQuery(id+"F4.wireOp",EDGE,"E26.7.2");var subQ34=sQuery(id+"F3.wireOp",EDGE,"E20.7.3");var subQ35=sQuery(id+"F3.wireOp",EDGE,"E20.7.1");var subQ36=sQuery(id+"F4.wireOp",EDGE,"E26.8.3");var subQ37=sQuery(id+"F4.wireOp",EDGE,"E26.8.2");var subQ38=sQuery(id+"F3.wireOp",EDGE,"E20.8.3");var subQ39=sQuery(id+"F3.wireOp",EDGE,"E20.8.1");var subQ40=sQuery(id+"F4.wireOp",EDGE,"E26.9.3");var subQ41=sQuery(id+"F4.wireOp",EDGE,"E26.9.2");var subQ42=sQuery(id+"F3.wireOp",EDGE,"E20.9.3");var subQ43=sQuery(id+"F3.wireOp",EDGE,"E20.9.1");var subQ44=sQuery(id+"F4.wireOp",EDGE,"E26.10.3");var subQ45=sQuery(id+"F4.wireOp",EDGE,"E26.10.2");var subQ46=sQuery(id+"F3.wireOp",EDGE,"E20.10.3");var subQ47=sQuery(id+"F3.wireOp",EDGE,"E20.10.1");var subQ48=sQuery(id+"F4.wireOp",EDGE,"E26.11.3");var subQ49=sQuery(id+"F4.wireOp",EDGE,"E26.11.2");var subQ50=sQuery(id+"F3.wireOp",EDGE,"E20.11.3");var subQ51=sQuery(id+"F3.wireOp",EDGE,"E20.11.1");var subQ52=sQuery(id+"F4.wireOp",EDGE,"E26.12.3");var subQ53=sQuery(id+"F4.wireOp",EDGE,"E26.12.2");var subQ54=sQuery(id+"F3.wireOp",EDGE,"E20.12.3");var subQ55=sQuery(id+"F3.wireOp",EDGE,"E20.12.1");var subQ56=sQuery(id+"F4.wireOp",EDGE,"E26.13.3");var subQ57=sQuery(id+"F4.wireOp",EDGE,"E26.13.2");var subQ58=sQuery(id+"F3.wireOp",EDGE,"E20.13.3");var subQ59=sQuery(id+"F3.wireOp",EDGE,"E20.13.1");var subQ60=sQuery(id+"F4.wireOp",EDGE,"E26.14.3");var subQ61=sQuery(id+"F4.wireOp",EDGE,"E26.14.2");var subQ62=sQuery(id+"F3.wireOp",EDGE,"E20.14.3");var subQ63=sQuery(id+"F3.wireOp",EDGE,"E20.14.1");var subQ64=sQuery(id+"F4.wireOp",EDGE,"E26.15.3");var subQ65=sQuery(id+"F4.wireOp",EDGE,"E26.15.2");var subQ66=sQuery(id+"F3.wireOp",EDGE,"E20.15.3");var subQ67=sQuery(id+"F3.wireOp",EDGE,"E20.15.1");var subQ68=sQuery(id+"F4.wireOp",EDGE,"E23");var subQ69=sQuery(id+"F4.wireOp",EDGE,"E22");var subQ70=sQuery(id+"F3.wireOp",EDGE,"E18.top");var subQ71=sQuery(id+"F3.wireOp",EDGE,"E18.bottom");var subQ74=makeQuery(id+"F42.boolean.opBoolean","COPY",FACE,{"disambiguationData":[TD([subQ31])],"derivedFrom":subQ6});var subQ75=makeQuery(id+"F15.boolean.opBoolean","INTERSECT",EDGE,{"derivedFrom":[makeQuery(id+"F1.opRevolve","SWEPT_FACE",FACE,{"disambiguationData":[OSD([sQuery(id+"F0.wireOp",EDGE,"E13")])]}),subQ31]});Q48=makeQuery(id+"F48.opFillet","BLEND_EDGE",EDGE,{"blendedFrom":[makeQuery(id+"F47.opFillet","TWEAK_EDGE",EDGE,{"derivedFrom":[makeQuery(id+"F45.opFillet","BLEND_VERTEX",VERTEX,{"blendedFrom":[subQ75,subQ31,subQ74],"blendedInto":[subQ31,subQ74]}),makeQuery(id+"F45.opFillet","BLEND_VERTEX",VERTEX,{"blendedFrom":[subQ75,makeQuery(id+"F42.boolean.opBoolean","MERGE",FACE,{"derivedFrom":[subQ0,subQ8]}),subQ74],"blendedInto":[makeQuery(id+"F42.boolean.opBoolean","MERGE",FACE,{"derivedFrom":[subQ0,subQ8]}),subQ74]})]}),makeQuery(id+"F47.opFillet","BLEND_FACE",FACE,{"disambiguationData":[OSD([subQ5,subQ7]),TDD([makeQuery(id+"F42.boolean.opBoolean","COPY",EDGE,{"disambiguationData":[TD([makeQuery(id+"F5.opLoft","SWEPT_FACE",FACE,{"disambiguationData":[OSD([subQ71,subQ70,sQuery(id+"F3.wireOp",EDGE,"E18.left"),sQuery(id+"F4.wireOp",EDGE,"E21"),subQ69,subQ68])]})])],"derivedFrom":subQ9})])]}),makeQuery(id+"F47.opFillet","BLEND_FACE",FACE,{"disambiguationData":[OSD([subQ5,subQ7]),TDD([makeQuery(id+"F42.boolean.opBoolean","COPY",EDGE,{"disambiguationData":[TD([makeQuery(id+"F6.opLoft","SWEPT_FACE",FACE,{"disambiguationData":[OSD([sQuery(id+"F3.wireOp",EDGE,"E20.15.0"),subQ67,subQ66,sQuery(id+"F4.wireOp",EDGE,"E26.15.0"),subQ65,subQ64])]})])],"derivedFrom":subQ9})])]}),makeQuery(id+"F47.opFillet","BLEND_FACE",FACE,{"disambiguationData":[OSD([subQ5,subQ7]),TDD([makeQuery(id+"F42.boolean.opBoolean","COPY",EDGE,{"disambiguationData":[TD([makeQuery(id+"F7.opLoft","SWEPT_FACE",FACE,{"disambiguationData":[OSD([sQuery(id+"F3.wireOp",EDGE,"E20.14.0"),subQ63,subQ62,sQuery(id+"F4.wireOp",EDGE,"E26.14.0"),subQ61,subQ60])]})])],"derivedFrom":subQ9})])]}),makeQuery(id+"F47.opFillet","BLEND_FACE",FACE,{"disambiguationData":[OSD([subQ5,subQ7]),TDD([makeQuery(id+"F42.boolean.opBoolean","COPY",EDGE,{"disambiguationData":[TD([makeQuery(id+"F8.opLoft","SWEPT_FACE",FACE,{"disambiguationData":[OSD([sQuery(id+"F3.wireOp",EDGE,"E20.13.0"),subQ59,subQ58,sQuery(id+"F4.wireOp",EDGE,"E26.13.0"),subQ57,subQ56])]})])],"derivedFrom":subQ9})])]}),makeQuery(id+"F47.opFillet","BLEND_FACE",FACE,{"disambiguationData":[OSD([subQ5,subQ7]),TDD([makeQuery(id+"F42.boolean.opBoolean","COPY",EDGE,{"disambiguationData":[TD([makeQuery(id+"F9.opLoft","SWEPT_FACE",FACE,{"disambiguationData":[OSD([sQuery(id+"F3.wireOp",EDGE,"E20.12.0"),subQ55,subQ54,sQuery(id+"F4.wireOp",EDGE,"E26.12.0"),subQ53,subQ52])]})])],"derivedFrom":subQ9})])]}),makeQuery(id+"F47.opFillet","BLEND_FACE",FACE,{"disambiguationData":[OSD([subQ5,subQ7]),TDD([makeQuery(id+"F42.boolean.opBoolean","COPY",EDGE,{"disambiguationData":[TD([makeQuery(id+"F10.opLoft","SWEPT_FACE",FACE,{"disambiguationData":[OSD([sQuery(id+"F3.wireOp",EDGE,"E20.11.0"),subQ51,subQ50,sQuery(id+"F4.wireOp",EDGE,"E26.11.0"),subQ49,subQ48])]})])],"derivedFrom":subQ9})])]}),makeQuery(id+"F47.opFillet","BLEND_FACE",FACE,{"disambiguationData":[OSD([subQ5,subQ7]),TDD([makeQuery(id+"F42.boolean.opBoolean","COPY",EDGE,{"disambiguationData":[TD([makeQuery(id+"F11.opLoft","SWEPT_FACE",FACE,{"disambiguationData":[OSD([sQuery(id+"F3.wireOp",EDGE,"E20.10.0"),subQ47,subQ46,sQuery(id+"F4.wireOp",EDGE,"E26.10.0"),subQ45,subQ44])]})])],"derivedFrom":subQ9})])]}),makeQuery(id+"F47.opFillet","BLEND_FACE",FACE,{"disambiguationData":[OSD([subQ5,subQ7]),TDD([makeQuery(id+"F42.boolean.opBoolean","COPY",EDGE,{"disambiguationData":[TD([makeQuery(id+"F12.opLoft","SWEPT_FACE",FACE,{"disambiguationData":[OSD([sQuery(id+"F3.wireOp",EDGE,"E20.9.0"),subQ43,subQ42,sQuery(id+"F4.wireOp",EDGE,"E26.9.0"),subQ41,subQ40])]})])],"derivedFrom":subQ9})])]}),makeQuery(id+"F47.opFillet","BLEND_FACE",FACE,{"disambiguationData":[OSD([subQ5,subQ7]),TDD([makeQuery(id+"F42.boolean.opBoolean","COPY",EDGE,{"disambiguationData":[TD([makeQuery(id+"F13.opLoft","SWEPT_FACE",FACE,{"disambiguationData":[OSD([sQuery(id+"F3.wireOp",EDGE,"E20.8.0"),subQ39,subQ38,sQuery(id+"F4.wireOp",EDGE,"E26.8.0"),subQ37,subQ36])]})])],"derivedFrom":subQ9})])]}),makeQuery(id+"F47.opFillet","BLEND_FACE",FACE,{"disambiguationData":[OSD([subQ5,subQ7]),TDD([makeQuery(id+"F42.boolean.opBoolean","COPY",EDGE,{"disambiguationData":[TD([makeQuery(id+"F14.opLoft","SWEPT_FACE",FACE,{"disambiguationData":[OSD([sQuery(id+"F3.wireOp",EDGE,"E20.7.0"),subQ35,subQ34,sQuery(id+"F4.wireOp",EDGE,"E26.7.0"),subQ33,subQ32])]})])],"derivedFrom":subQ9})])]}),makeQuery(id+"F47.opFillet","BLEND_FACE",FACE,{"disambiguationData":[OSD([subQ5,subQ7]),TDD([makeQuery(id+"F42.boolean.opBoolean","COPY",EDGE,{"disambiguationData":[TD([subQ31])],"derivedFrom":subQ9})])]}),makeQuery(id+"F47.opFillet","BLEND_FACE",FACE,{"disambiguationData":[OSD([subQ5,subQ7]),TDD([makeQuery(id+"F42.boolean.opBoolean","COPY",EDGE,{"disambiguationData":[TD([makeQuery(id+"F16.opLoft","SWEPT_FACE",FACE,{"disambiguationData":[OSD([sQuery(id+"F3.wireOp",EDGE,"E20.5.0"),subQ25,subQ24,sQuery(id+"F4.wireOp",EDGE,"E26.5.0"),subQ23,subQ22])]})])],"derivedFrom":subQ9})])]}),makeQuery(id+"F47.opFillet","BLEND_FACE",FACE,{"disambiguationData":[OSD([subQ5,subQ7]),TDD([makeQuery(id+"F42.boolean.opBoolean","COPY",EDGE,{"disambiguationData":[TD([makeQuery(id+"F17.opLoft","SWEPT_FACE",FACE,{"disambiguationData":[OSD([sQuery(id+"F3.wireOp",EDGE,"E20.4.0"),subQ21,subQ20,sQuery(id+"F4.wireOp",EDGE,"E26.4.0"),subQ19,subQ18])]})])],"derivedFrom":subQ9})])]}),makeQuery(id+"F47.opFillet","BLEND_FACE",FACE,{"disambiguationData":[OSD([subQ5,subQ7]),TDD([makeQuery(id+"F42.boolean.opBoolean","COPY",EDGE,{"disambiguationData":[TD([makeQuery(id+"F18.opLoft","SWEPT_FACE",FACE,{"disambiguationData":[OSD([sQuery(id+"F3.wireOp",EDGE,"E20.3.0"),subQ17,subQ16,sQuery(id+"F4.wireOp",EDGE,"E26.3.0"),subQ15,subQ14])]})])],"derivedFrom":subQ9})])]}),makeQuery(id+"F47.opFillet","BLEND_FACE",FACE,{"disambiguationData":[OSD([subQ5,subQ7]),TDD([makeQuery(id+"F42.boolean.opBoolean","COPY",EDGE,{"disambiguationData":[TD([makeQuery(id+"F19.opLoft","SWEPT_FACE",FACE,{"disambiguationData":[OSD([sQuery(id+"F3.wireOp",EDGE,"E20.2.0"),subQ13,subQ12,sQuery(id+"F4.wireOp",EDGE,"E26.2.0"),subQ11,subQ10])]})])],"derivedFrom":subQ9})])]}),makeQuery(id+"F47.opFillet","BLEND_FACE",FACE,{"disambiguationData":[OSD([subQ5,subQ7]),TDD([makeQuery(id+"F42.boolean.opBoolean","COPY",EDGE,{"disambiguationData":[TD([makeQuery(id+"F20.opLoft","SWEPT_FACE",FACE,{"disambiguationData":[OSD([sQuery(id+"F3.wireOp",EDGE,"E20.1.0"),subQ4,subQ3,sQuery(id+"F4.wireOp",EDGE,"E26.1.0"),subQ2,subQ1])]})])],"derivedFrom":subQ9})])]})],"blendedInto":[makeQuery(id+"F47.opFillet","BLEND_FACE",FACE,{"disambiguationData":[OSD([subQ5,subQ7]),TDD([makeQuery(id+"F42.boolean.opBoolean","COPY",EDGE,{"disambiguationData":[TD([makeQuery(id+"F5.opLoft","SWEPT_FACE",FACE,{"disambiguationData":[OSD([subQ71,subQ70,sQuery(id+"F3.wireOp",EDGE,"E18.left"),sQuery(id+"F4.wireOp",EDGE,"E21"),subQ69,subQ68])]})])],"derivedFrom":subQ9})])]}),makeQuery(id+"F47.opFillet","BLEND_FACE",FACE,{"disambiguationData":[OSD([subQ5,subQ7]),TDD([makeQuery(id+"F42.boolean.opBoolean","COPY",EDGE,{"disambiguationData":[TD([makeQuery(id+"F6.opLoft","SWEPT_FACE",FACE,{"disambiguationData":[OSD([sQuery(id+"F3.wireOp",EDGE,"E20.15.0"),subQ67,subQ66,sQuery(id+"F4.wireOp",EDGE,"E26.15.0"),subQ65,subQ64])]})])],"derivedFrom":subQ9})])]}),makeQuery(id+"F47.opFillet","BLEND_FACE",FACE,{"disambiguationData":[OSD([subQ5,subQ7]),TDD([makeQuery(id+"F42.boolean.opBoolean","COPY",EDGE,{"disambiguationData":[TD([makeQuery(id+"F7.opLoft","SWEPT_FACE",FACE,{"disambiguationData":[OSD([sQuery(id+"F3.wireOp",EDGE,"E20.14.0"),subQ63,subQ62,sQuery(id+"F4.wireOp",EDGE,"E26.14.0"),subQ61,subQ60])]})])],"derivedFrom":subQ9})])]}),makeQuery(id+"F47.opFillet","BLEND_FACE",FACE,{"disambiguationData":[OSD([subQ5,subQ7]),TDD([makeQuery(id+"F42.boolean.opBoolean","COPY",EDGE,{"disambiguationData":[TD([makeQuery(id+"F8.opLoft","SWEPT_FACE",FACE,{"disambiguationData":[OSD([sQuery(id+"F3.wireOp",EDGE,"E20.13.0"),subQ59,subQ58,sQuery(id+"F4.wireOp",EDGE,"E26.13.0"),subQ57,subQ56])]})])],"derivedFrom":subQ9})])]}),makeQuery(id+"F47.opFillet","BLEND_FACE",FACE,{"disambiguationData":[OSD([subQ5,subQ7]),TDD([makeQuery(id+"F42.boolean.opBoolean","COPY",EDGE,{"disambiguationData":[TD([makeQuery(id+"F9.opLoft","SWEPT_FACE",FACE,{"disambiguationData":[OSD([sQuery(id+"F3.wireOp",EDGE,"E20.12.0"),subQ55,subQ54,sQuery(id+"F4.wireOp",EDGE,"E26.12.0"),subQ53,subQ52])]})])],"derivedFrom":subQ9})])]}),makeQuery(id+"F47.opFillet","BLEND_FACE",FACE,{"disambiguationData":[OSD([subQ5,subQ7]),TDD([makeQuery(id+"F42.boolean.opBoolean","COPY",EDGE,{"disambiguationData":[TD([makeQuery(id+"F10.opLoft","SWEPT_FACE",FACE,{"disambiguationData":[OSD([sQuery(id+"F3.wireOp",EDGE,"E20.11.0"),subQ51,subQ50,sQuery(id+"F4.wireOp",EDGE,"E26.11.0"),subQ49,subQ48])]})])],"derivedFrom":subQ9})])]}),makeQuery(id+"F47.opFillet","BLEND_FACE",FACE,{"disambiguationData":[OSD([subQ5,subQ7]),TDD([makeQuery(id+"F42.boolean.opBoolean","COPY",EDGE,{"disambiguationData":[TD([makeQuery(id+"F11.opLoft","SWEPT_FACE",FACE,{"disambiguationData":[OSD([sQuery(id+"F3.wireOp",EDGE,"E20.10.0"),subQ47,subQ46,sQuery(id+"F4.wireOp",EDGE,"E26.10.0"),subQ45,subQ44])]})])],"derivedFrom":subQ9})])]}),makeQuery(id+"F47.opFillet","BLEND_FACE",FACE,{"disambiguationData":[OSD([subQ5,subQ7]),TDD([makeQuery(id+"F42.boolean.opBoolean","COPY",EDGE,{"disambiguationData":[TD([makeQuery(id+"F12.opLoft","SWEPT_FACE",FACE,{"disambiguationData":[OSD([sQuery(id+"F3.wireOp",EDGE,"E20.9.0"),subQ43,subQ42,sQuery(id+"F4.wireOp",EDGE,"E26.9.0"),subQ41,subQ40])]})])],"derivedFrom":subQ9})])]}),makeQuery(id+"F47.opFillet","BLEND_FACE",FACE,{"disambiguationData":[OSD([subQ5,subQ7]),TDD([makeQuery(id+"F42.boolean.opBoolean","COPY",EDGE,{"disambiguationData":[TD([makeQuery(id+"F13.opLoft","SWEPT_FACE",FACE,{"disambiguationData":[OSD([sQuery(id+"F3.wireOp",EDGE,"E20.8.0"),subQ39,subQ38,sQuery(id+"F4.wireOp",EDGE,"E26.8.0"),subQ37,subQ36])]})])],"derivedFrom":subQ9})])]}),makeQuery(id+"F47.opFillet","BLEND_FACE",FACE,{"disambiguationData":[OSD([subQ5,subQ7]),TDD([makeQuery(id+"F42.boolean.opBoolean","COPY",EDGE,{"disambiguationData":[TD([makeQuery(id+"F14.opLoft","SWEPT_FACE",FACE,{"disambiguationData":[OSD([sQuery(id+"F3.wireOp",EDGE,"E20.7.0"),subQ35,subQ34,sQuery(id+"F4.wireOp",EDGE,"E26.7.0"),subQ33,subQ32])]})])],"derivedFrom":subQ9})])]}),makeQuery(id+"F47.opFillet","BLEND_FACE",FACE,{"disambiguationData":[OSD([subQ5,subQ7]),TDD([makeQuery(id+"F42.boolean.opBoolean","COPY",EDGE,{"disambiguationData":[TD([subQ31])],"derivedFrom":subQ9})])]}),makeQuery(id+"F47.opFillet","BLEND_FACE",FACE,{"disambiguationData":[OSD([subQ5,subQ7]),TDD([makeQuery(id+"F42.boolean.opBoolean","COPY",EDGE,{"disambiguationData":[TD([makeQuery(id+"F16.opLoft","SWEPT_FACE",FACE,{"disambiguationData":[OSD([sQuery(id+"F3.wireOp",EDGE,"E20.5.0"),subQ25,subQ24,sQuery(id+"F4.wireOp",EDGE,"E26.5.0"),subQ23,subQ22])]})])],"derivedFrom":subQ9})])]}),makeQuery(id+"F47.opFillet","BLEND_FACE",FACE,{"disambiguationData":[OSD([subQ5,subQ7]),TDD([makeQuery(id+"F42.boolean.opBoolean","COPY",EDGE,{"disambiguationData":[TD([makeQuery(id+"F17.opLoft","SWEPT_FACE",FACE,{"disambiguationData":[OSD([sQuery(id+"F3.wireOp",EDGE,"E20.4.0"),subQ21,subQ20,sQuery(id+"F4.wireOp",EDGE,"E26.4.0"),subQ19,subQ18])]})])],"derivedFrom":subQ9})])]}),makeQuery(id+"F47.opFillet","BLEND_FACE",FACE,{"disambiguationData":[OSD([subQ5,subQ7]),TDD([makeQuery(id+"F42.boolean.opBoolean","COPY",EDGE,{"disambiguationData":[TD([makeQuery(id+"F18.opLoft","SWEPT_FACE",FACE,{"disambiguationData":[OSD([sQuery(id+"F3.wireOp",EDGE,"E20.3.0"),subQ17,subQ16,sQuery(id+"F4.wireOp",EDGE,"E26.3.0"),subQ15,subQ14])]})])],"derivedFrom":subQ9})])]}),makeQuery(id+"F47.opFillet","BLEND_FACE",FACE,{"disambiguationData":[OSD([subQ5,subQ7]),TDD([makeQuery(id+"F42.boolean.opBoolean","COPY",EDGE,{"disambiguationData":[TD([makeQuery(id+"F19.opLoft","SWEPT_FACE",FACE,{"disambiguationData":[OSD([sQuery(id+"F3.wireOp",EDGE,"E20.2.0"),subQ13,subQ12,sQuery(id+"F4.wireOp",EDGE,"E26.2.0"),subQ11,subQ10])]})])],"derivedFrom":subQ9})])]}),makeQuery(id+"F47.opFillet","BLEND_FACE",FACE,{"disambiguationData":[OSD([subQ5,subQ7]),TDD([makeQuery(id+"F42.boolean.opBoolean","COPY",EDGE,{"disambiguationData":[TD([makeQuery(id+"F20.opLoft","SWEPT_FACE",FACE,{"disambiguationData":[OSD([sQuery(id+"F3.wireOp",EDGE,"E20.1.0"),subQ4,subQ3,sQuery(id+"F4.wireOp",EDGE,"E26.1.0"),subQ2,subQ1])]})])],"derivedFrom":subQ9})])]})]});}
            var Q49;
            {var subQ0=makeQuery(id+"F40.opExtrude","CAP_FACE",FACE,{"disambiguationData":[OSD([sQuery(id+"F39.wireOp",EDGE,"E29"),sQuery(id+"F39.wireOp",EDGE,"E30")])],"isStart":false});var subQ1=sQuery(id+"F4.wireOp",EDGE,"E26.1.3");var subQ2=sQuery(id+"F4.wireOp",EDGE,"E26.1.2");var subQ3=sQuery(id+"F3.wireOp",EDGE,"E20.1.3");var subQ4=sQuery(id+"F3.wireOp",EDGE,"E20.1.1");var subQ5=sQuery(id+"F41.wireOp",EDGE,"E35");var subQ6=makeQuery(id+"F42.opRevolve","SWEPT_FACE",FACE,{"disambiguationData":[OSD([subQ5])]});var subQ7=sQuery(id+"F41.wireOp",EDGE,"E36");var subQ8=makeQuery(id+"F42.opRevolve","SWEPT_FACE",FACE,{"disambiguationData":[OSD([subQ7])]});var subQ9=makeQuery(id+"F42.opRevolve","SWEPT_EDGE",EDGE,{"disambiguationData":[OSD([subQ5,subQ7])]});var subQ10=sQuery(id+"F4.wireOp",EDGE,"E26.2.3");var subQ11=sQuery(id+"F4.wireOp",EDGE,"E26.2.2");var subQ12=sQuery(id+"F3.wireOp",EDGE,"E20.2.3");var subQ13=sQuery(id+"F3.wireOp",EDGE,"E20.2.1");var subQ14=sQuery(id+"F4.wireOp",EDGE,"E26.3.3");var subQ15=sQuery(id+"F4.wireOp",EDGE,"E26.3.2");var subQ16=sQuery(id+"F3.wireOp",EDGE,"E20.3.3");var subQ17=sQuery(id+"F3.wireOp",EDGE,"E20.3.1");var subQ18=sQuery(id+"F4.wireOp",EDGE,"E26.4.3");var subQ19=sQuery(id+"F4.wireOp",EDGE,"E26.4.2");var subQ20=sQuery(id+"F3.wireOp",EDGE,"E20.4.3");var subQ21=sQuery(id+"F3.wireOp",EDGE,"E20.4.1");var subQ22=sQuery(id+"F4.wireOp",EDGE,"E26.5.3");var subQ23=sQuery(id+"F4.wireOp",EDGE,"E26.5.2");var subQ24=sQuery(id+"F3.wireOp",EDGE,"E20.5.3");var subQ25=sQuery(id+"F3.wireOp",EDGE,"E20.5.1");var subQ27=makeQuery(id+"F16.opLoft","SWEPT_FACE",FACE,{"disambiguationData":[OSD([sQuery(id+"F3.wireOp",EDGE,"E20.5.0"),subQ25,subQ24,sQuery(id+"F4.wireOp",EDGE,"E26.5.0"),subQ23,subQ22])]});var subQ28=sQuery(id+"F4.wireOp",EDGE,"E26.6.3");var subQ29=sQuery(id+"F4.wireOp",EDGE,"E26.6.2");var subQ30=sQuery(id+"F3.wireOp",EDGE,"E20.6.3");var subQ31=sQuery(id+"F3.wireOp",EDGE,"E20.6.1");var subQ32=sQuery(id+"F4.wireOp",EDGE,"E26.7.3");var subQ33=sQuery(id+"F4.wireOp",EDGE,"E26.7.2");var subQ34=sQuery(id+"F3.wireOp",EDGE,"E20.7.3");var subQ35=sQuery(id+"F3.wireOp",EDGE,"E20.7.1");var subQ36=sQuery(id+"F4.wireOp",EDGE,"E26.8.3");var subQ37=sQuery(id+"F4.wireOp",EDGE,"E26.8.2");var subQ38=sQuery(id+"F3.wireOp",EDGE,"E20.8.3");var subQ39=sQuery(id+"F3.wireOp",EDGE,"E20.8.1");var subQ40=sQuery(id+"F4.wireOp",EDGE,"E26.9.3");var subQ41=sQuery(id+"F4.wireOp",EDGE,"E26.9.2");var subQ42=sQuery(id+"F3.wireOp",EDGE,"E20.9.3");var subQ43=sQuery(id+"F3.wireOp",EDGE,"E20.9.1");var subQ44=sQuery(id+"F4.wireOp",EDGE,"E26.10.3");var subQ45=sQuery(id+"F4.wireOp",EDGE,"E26.10.2");var subQ46=sQuery(id+"F3.wireOp",EDGE,"E20.10.3");var subQ47=sQuery(id+"F3.wireOp",EDGE,"E20.10.1");var subQ48=sQuery(id+"F4.wireOp",EDGE,"E26.11.3");var subQ49=sQuery(id+"F4.wireOp",EDGE,"E26.11.2");var subQ50=sQuery(id+"F3.wireOp",EDGE,"E20.11.3");var subQ51=sQuery(id+"F3.wireOp",EDGE,"E20.11.1");var subQ52=sQuery(id+"F4.wireOp",EDGE,"E26.12.3");var subQ53=sQuery(id+"F4.wireOp",EDGE,"E26.12.2");var subQ54=sQuery(id+"F3.wireOp",EDGE,"E20.12.3");var subQ55=sQuery(id+"F3.wireOp",EDGE,"E20.12.1");var subQ56=sQuery(id+"F4.wireOp",EDGE,"E26.13.3");var subQ57=sQuery(id+"F4.wireOp",EDGE,"E26.13.2");var subQ58=sQuery(id+"F3.wireOp",EDGE,"E20.13.3");var subQ59=sQuery(id+"F3.wireOp",EDGE,"E20.13.1");var subQ60=sQuery(id+"F4.wireOp",EDGE,"E26.14.3");var subQ61=sQuery(id+"F4.wireOp",EDGE,"E26.14.2");var subQ62=sQuery(id+"F3.wireOp",EDGE,"E20.14.3");var subQ63=sQuery(id+"F3.wireOp",EDGE,"E20.14.1");var subQ64=sQuery(id+"F4.wireOp",EDGE,"E26.15.3");var subQ65=sQuery(id+"F4.wireOp",EDGE,"E26.15.2");var subQ66=sQuery(id+"F3.wireOp",EDGE,"E20.15.3");var subQ67=sQuery(id+"F3.wireOp",EDGE,"E20.15.1");var subQ68=sQuery(id+"F4.wireOp",EDGE,"E23");var subQ69=sQuery(id+"F4.wireOp",EDGE,"E22");var subQ70=sQuery(id+"F3.wireOp",EDGE,"E18.top");var subQ71=sQuery(id+"F3.wireOp",EDGE,"E18.bottom");var subQ74=makeQuery(id+"F42.boolean.opBoolean","COPY",FACE,{"disambiguationData":[TD([subQ27])],"derivedFrom":subQ6});var subQ75=makeQuery(id+"F16.boolean.opBoolean","INTERSECT",EDGE,{"derivedFrom":[makeQuery(id+"F1.opRevolve","SWEPT_FACE",FACE,{"disambiguationData":[OSD([sQuery(id+"F0.wireOp",EDGE,"E13")])]}),subQ27]});Q49=makeQuery(id+"F48.opFillet","BLEND_EDGE",EDGE,{"blendedFrom":[makeQuery(id+"F47.opFillet","TWEAK_EDGE",EDGE,{"derivedFrom":[makeQuery(id+"F45.opFillet","BLEND_VERTEX",VERTEX,{"blendedFrom":[subQ75,subQ27,subQ74],"blendedInto":[subQ27,subQ74]}),makeQuery(id+"F45.opFillet","BLEND_VERTEX",VERTEX,{"blendedFrom":[subQ75,makeQuery(id+"F42.boolean.opBoolean","MERGE",FACE,{"derivedFrom":[subQ0,subQ8]}),subQ74],"blendedInto":[makeQuery(id+"F42.boolean.opBoolean","MERGE",FACE,{"derivedFrom":[subQ0,subQ8]}),subQ74]})]}),makeQuery(id+"F47.opFillet","BLEND_FACE",FACE,{"disambiguationData":[OSD([subQ5,subQ7]),TDD([makeQuery(id+"F42.boolean.opBoolean","COPY",EDGE,{"disambiguationData":[TD([makeQuery(id+"F5.opLoft","SWEPT_FACE",FACE,{"disambiguationData":[OSD([subQ71,subQ70,sQuery(id+"F3.wireOp",EDGE,"E18.left"),sQuery(id+"F4.wireOp",EDGE,"E21"),subQ69,subQ68])]})])],"derivedFrom":subQ9})])]}),makeQuery(id+"F47.opFillet","BLEND_FACE",FACE,{"disambiguationData":[OSD([subQ5,subQ7]),TDD([makeQuery(id+"F42.boolean.opBoolean","COPY",EDGE,{"disambiguationData":[TD([makeQuery(id+"F6.opLoft","SWEPT_FACE",FACE,{"disambiguationData":[OSD([sQuery(id+"F3.wireOp",EDGE,"E20.15.0"),subQ67,subQ66,sQuery(id+"F4.wireOp",EDGE,"E26.15.0"),subQ65,subQ64])]})])],"derivedFrom":subQ9})])]}),makeQuery(id+"F47.opFillet","BLEND_FACE",FACE,{"disambiguationData":[OSD([subQ5,subQ7]),TDD([makeQuery(id+"F42.boolean.opBoolean","COPY",EDGE,{"disambiguationData":[TD([makeQuery(id+"F7.opLoft","SWEPT_FACE",FACE,{"disambiguationData":[OSD([sQuery(id+"F3.wireOp",EDGE,"E20.14.0"),subQ63,subQ62,sQuery(id+"F4.wireOp",EDGE,"E26.14.0"),subQ61,subQ60])]})])],"derivedFrom":subQ9})])]}),makeQuery(id+"F47.opFillet","BLEND_FACE",FACE,{"disambiguationData":[OSD([subQ5,subQ7]),TDD([makeQuery(id+"F42.boolean.opBoolean","COPY",EDGE,{"disambiguationData":[TD([makeQuery(id+"F8.opLoft","SWEPT_FACE",FACE,{"disambiguationData":[OSD([sQuery(id+"F3.wireOp",EDGE,"E20.13.0"),subQ59,subQ58,sQuery(id+"F4.wireOp",EDGE,"E26.13.0"),subQ57,subQ56])]})])],"derivedFrom":subQ9})])]}),makeQuery(id+"F47.opFillet","BLEND_FACE",FACE,{"disambiguationData":[OSD([subQ5,subQ7]),TDD([makeQuery(id+"F42.boolean.opBoolean","COPY",EDGE,{"disambiguationData":[TD([makeQuery(id+"F9.opLoft","SWEPT_FACE",FACE,{"disambiguationData":[OSD([sQuery(id+"F3.wireOp",EDGE,"E20.12.0"),subQ55,subQ54,sQuery(id+"F4.wireOp",EDGE,"E26.12.0"),subQ53,subQ52])]})])],"derivedFrom":subQ9})])]}),makeQuery(id+"F47.opFillet","BLEND_FACE",FACE,{"disambiguationData":[OSD([subQ5,subQ7]),TDD([makeQuery(id+"F42.boolean.opBoolean","COPY",EDGE,{"disambiguationData":[TD([makeQuery(id+"F10.opLoft","SWEPT_FACE",FACE,{"disambiguationData":[OSD([sQuery(id+"F3.wireOp",EDGE,"E20.11.0"),subQ51,subQ50,sQuery(id+"F4.wireOp",EDGE,"E26.11.0"),subQ49,subQ48])]})])],"derivedFrom":subQ9})])]}),makeQuery(id+"F47.opFillet","BLEND_FACE",FACE,{"disambiguationData":[OSD([subQ5,subQ7]),TDD([makeQuery(id+"F42.boolean.opBoolean","COPY",EDGE,{"disambiguationData":[TD([makeQuery(id+"F11.opLoft","SWEPT_FACE",FACE,{"disambiguationData":[OSD([sQuery(id+"F3.wireOp",EDGE,"E20.10.0"),subQ47,subQ46,sQuery(id+"F4.wireOp",EDGE,"E26.10.0"),subQ45,subQ44])]})])],"derivedFrom":subQ9})])]}),makeQuery(id+"F47.opFillet","BLEND_FACE",FACE,{"disambiguationData":[OSD([subQ5,subQ7]),TDD([makeQuery(id+"F42.boolean.opBoolean","COPY",EDGE,{"disambiguationData":[TD([makeQuery(id+"F12.opLoft","SWEPT_FACE",FACE,{"disambiguationData":[OSD([sQuery(id+"F3.wireOp",EDGE,"E20.9.0"),subQ43,subQ42,sQuery(id+"F4.wireOp",EDGE,"E26.9.0"),subQ41,subQ40])]})])],"derivedFrom":subQ9})])]}),makeQuery(id+"F47.opFillet","BLEND_FACE",FACE,{"disambiguationData":[OSD([subQ5,subQ7]),TDD([makeQuery(id+"F42.boolean.opBoolean","COPY",EDGE,{"disambiguationData":[TD([makeQuery(id+"F13.opLoft","SWEPT_FACE",FACE,{"disambiguationData":[OSD([sQuery(id+"F3.wireOp",EDGE,"E20.8.0"),subQ39,subQ38,sQuery(id+"F4.wireOp",EDGE,"E26.8.0"),subQ37,subQ36])]})])],"derivedFrom":subQ9})])]}),makeQuery(id+"F47.opFillet","BLEND_FACE",FACE,{"disambiguationData":[OSD([subQ5,subQ7]),TDD([makeQuery(id+"F42.boolean.opBoolean","COPY",EDGE,{"disambiguationData":[TD([makeQuery(id+"F14.opLoft","SWEPT_FACE",FACE,{"disambiguationData":[OSD([sQuery(id+"F3.wireOp",EDGE,"E20.7.0"),subQ35,subQ34,sQuery(id+"F4.wireOp",EDGE,"E26.7.0"),subQ33,subQ32])]})])],"derivedFrom":subQ9})])]}),makeQuery(id+"F47.opFillet","BLEND_FACE",FACE,{"disambiguationData":[OSD([subQ5,subQ7]),TDD([makeQuery(id+"F42.boolean.opBoolean","COPY",EDGE,{"disambiguationData":[TD([makeQuery(id+"F15.opLoft","SWEPT_FACE",FACE,{"disambiguationData":[OSD([sQuery(id+"F3.wireOp",EDGE,"E20.6.0"),subQ31,subQ30,sQuery(id+"F4.wireOp",EDGE,"E26.6.0"),subQ29,subQ28])]})])],"derivedFrom":subQ9})])]}),makeQuery(id+"F47.opFillet","BLEND_FACE",FACE,{"disambiguationData":[OSD([subQ5,subQ7]),TDD([makeQuery(id+"F42.boolean.opBoolean","COPY",EDGE,{"disambiguationData":[TD([subQ27])],"derivedFrom":subQ9})])]}),makeQuery(id+"F47.opFillet","BLEND_FACE",FACE,{"disambiguationData":[OSD([subQ5,subQ7]),TDD([makeQuery(id+"F42.boolean.opBoolean","COPY",EDGE,{"disambiguationData":[TD([makeQuery(id+"F17.opLoft","SWEPT_FACE",FACE,{"disambiguationData":[OSD([sQuery(id+"F3.wireOp",EDGE,"E20.4.0"),subQ21,subQ20,sQuery(id+"F4.wireOp",EDGE,"E26.4.0"),subQ19,subQ18])]})])],"derivedFrom":subQ9})])]}),makeQuery(id+"F47.opFillet","BLEND_FACE",FACE,{"disambiguationData":[OSD([subQ5,subQ7]),TDD([makeQuery(id+"F42.boolean.opBoolean","COPY",EDGE,{"disambiguationData":[TD([makeQuery(id+"F18.opLoft","SWEPT_FACE",FACE,{"disambiguationData":[OSD([sQuery(id+"F3.wireOp",EDGE,"E20.3.0"),subQ17,subQ16,sQuery(id+"F4.wireOp",EDGE,"E26.3.0"),subQ15,subQ14])]})])],"derivedFrom":subQ9})])]}),makeQuery(id+"F47.opFillet","BLEND_FACE",FACE,{"disambiguationData":[OSD([subQ5,subQ7]),TDD([makeQuery(id+"F42.boolean.opBoolean","COPY",EDGE,{"disambiguationData":[TD([makeQuery(id+"F19.opLoft","SWEPT_FACE",FACE,{"disambiguationData":[OSD([sQuery(id+"F3.wireOp",EDGE,"E20.2.0"),subQ13,subQ12,sQuery(id+"F4.wireOp",EDGE,"E26.2.0"),subQ11,subQ10])]})])],"derivedFrom":subQ9})])]}),makeQuery(id+"F47.opFillet","BLEND_FACE",FACE,{"disambiguationData":[OSD([subQ5,subQ7]),TDD([makeQuery(id+"F42.boolean.opBoolean","COPY",EDGE,{"disambiguationData":[TD([makeQuery(id+"F20.opLoft","SWEPT_FACE",FACE,{"disambiguationData":[OSD([sQuery(id+"F3.wireOp",EDGE,"E20.1.0"),subQ4,subQ3,sQuery(id+"F4.wireOp",EDGE,"E26.1.0"),subQ2,subQ1])]})])],"derivedFrom":subQ9})])]})],"blendedInto":[makeQuery(id+"F47.opFillet","BLEND_FACE",FACE,{"disambiguationData":[OSD([subQ5,subQ7]),TDD([makeQuery(id+"F42.boolean.opBoolean","COPY",EDGE,{"disambiguationData":[TD([makeQuery(id+"F5.opLoft","SWEPT_FACE",FACE,{"disambiguationData":[OSD([subQ71,subQ70,sQuery(id+"F3.wireOp",EDGE,"E18.left"),sQuery(id+"F4.wireOp",EDGE,"E21"),subQ69,subQ68])]})])],"derivedFrom":subQ9})])]}),makeQuery(id+"F47.opFillet","BLEND_FACE",FACE,{"disambiguationData":[OSD([subQ5,subQ7]),TDD([makeQuery(id+"F42.boolean.opBoolean","COPY",EDGE,{"disambiguationData":[TD([makeQuery(id+"F6.opLoft","SWEPT_FACE",FACE,{"disambiguationData":[OSD([sQuery(id+"F3.wireOp",EDGE,"E20.15.0"),subQ67,subQ66,sQuery(id+"F4.wireOp",EDGE,"E26.15.0"),subQ65,subQ64])]})])],"derivedFrom":subQ9})])]}),makeQuery(id+"F47.opFillet","BLEND_FACE",FACE,{"disambiguationData":[OSD([subQ5,subQ7]),TDD([makeQuery(id+"F42.boolean.opBoolean","COPY",EDGE,{"disambiguationData":[TD([makeQuery(id+"F7.opLoft","SWEPT_FACE",FACE,{"disambiguationData":[OSD([sQuery(id+"F3.wireOp",EDGE,"E20.14.0"),subQ63,subQ62,sQuery(id+"F4.wireOp",EDGE,"E26.14.0"),subQ61,subQ60])]})])],"derivedFrom":subQ9})])]}),makeQuery(id+"F47.opFillet","BLEND_FACE",FACE,{"disambiguationData":[OSD([subQ5,subQ7]),TDD([makeQuery(id+"F42.boolean.opBoolean","COPY",EDGE,{"disambiguationData":[TD([makeQuery(id+"F8.opLoft","SWEPT_FACE",FACE,{"disambiguationData":[OSD([sQuery(id+"F3.wireOp",EDGE,"E20.13.0"),subQ59,subQ58,sQuery(id+"F4.wireOp",EDGE,"E26.13.0"),subQ57,subQ56])]})])],"derivedFrom":subQ9})])]}),makeQuery(id+"F47.opFillet","BLEND_FACE",FACE,{"disambiguationData":[OSD([subQ5,subQ7]),TDD([makeQuery(id+"F42.boolean.opBoolean","COPY",EDGE,{"disambiguationData":[TD([makeQuery(id+"F9.opLoft","SWEPT_FACE",FACE,{"disambiguationData":[OSD([sQuery(id+"F3.wireOp",EDGE,"E20.12.0"),subQ55,subQ54,sQuery(id+"F4.wireOp",EDGE,"E26.12.0"),subQ53,subQ52])]})])],"derivedFrom":subQ9})])]}),makeQuery(id+"F47.opFillet","BLEND_FACE",FACE,{"disambiguationData":[OSD([subQ5,subQ7]),TDD([makeQuery(id+"F42.boolean.opBoolean","COPY",EDGE,{"disambiguationData":[TD([makeQuery(id+"F10.opLoft","SWEPT_FACE",FACE,{"disambiguationData":[OSD([sQuery(id+"F3.wireOp",EDGE,"E20.11.0"),subQ51,subQ50,sQuery(id+"F4.wireOp",EDGE,"E26.11.0"),subQ49,subQ48])]})])],"derivedFrom":subQ9})])]}),makeQuery(id+"F47.opFillet","BLEND_FACE",FACE,{"disambiguationData":[OSD([subQ5,subQ7]),TDD([makeQuery(id+"F42.boolean.opBoolean","COPY",EDGE,{"disambiguationData":[TD([makeQuery(id+"F11.opLoft","SWEPT_FACE",FACE,{"disambiguationData":[OSD([sQuery(id+"F3.wireOp",EDGE,"E20.10.0"),subQ47,subQ46,sQuery(id+"F4.wireOp",EDGE,"E26.10.0"),subQ45,subQ44])]})])],"derivedFrom":subQ9})])]}),makeQuery(id+"F47.opFillet","BLEND_FACE",FACE,{"disambiguationData":[OSD([subQ5,subQ7]),TDD([makeQuery(id+"F42.boolean.opBoolean","COPY",EDGE,{"disambiguationData":[TD([makeQuery(id+"F12.opLoft","SWEPT_FACE",FACE,{"disambiguationData":[OSD([sQuery(id+"F3.wireOp",EDGE,"E20.9.0"),subQ43,subQ42,sQuery(id+"F4.wireOp",EDGE,"E26.9.0"),subQ41,subQ40])]})])],"derivedFrom":subQ9})])]}),makeQuery(id+"F47.opFillet","BLEND_FACE",FACE,{"disambiguationData":[OSD([subQ5,subQ7]),TDD([makeQuery(id+"F42.boolean.opBoolean","COPY",EDGE,{"disambiguationData":[TD([makeQuery(id+"F13.opLoft","SWEPT_FACE",FACE,{"disambiguationData":[OSD([sQuery(id+"F3.wireOp",EDGE,"E20.8.0"),subQ39,subQ38,sQuery(id+"F4.wireOp",EDGE,"E26.8.0"),subQ37,subQ36])]})])],"derivedFrom":subQ9})])]}),makeQuery(id+"F47.opFillet","BLEND_FACE",FACE,{"disambiguationData":[OSD([subQ5,subQ7]),TDD([makeQuery(id+"F42.boolean.opBoolean","COPY",EDGE,{"disambiguationData":[TD([makeQuery(id+"F14.opLoft","SWEPT_FACE",FACE,{"disambiguationData":[OSD([sQuery(id+"F3.wireOp",EDGE,"E20.7.0"),subQ35,subQ34,sQuery(id+"F4.wireOp",EDGE,"E26.7.0"),subQ33,subQ32])]})])],"derivedFrom":subQ9})])]}),makeQuery(id+"F47.opFillet","BLEND_FACE",FACE,{"disambiguationData":[OSD([subQ5,subQ7]),TDD([makeQuery(id+"F42.boolean.opBoolean","COPY",EDGE,{"disambiguationData":[TD([makeQuery(id+"F15.opLoft","SWEPT_FACE",FACE,{"disambiguationData":[OSD([sQuery(id+"F3.wireOp",EDGE,"E20.6.0"),subQ31,subQ30,sQuery(id+"F4.wireOp",EDGE,"E26.6.0"),subQ29,subQ28])]})])],"derivedFrom":subQ9})])]}),makeQuery(id+"F47.opFillet","BLEND_FACE",FACE,{"disambiguationData":[OSD([subQ5,subQ7]),TDD([makeQuery(id+"F42.boolean.opBoolean","COPY",EDGE,{"disambiguationData":[TD([subQ27])],"derivedFrom":subQ9})])]}),makeQuery(id+"F47.opFillet","BLEND_FACE",FACE,{"disambiguationData":[OSD([subQ5,subQ7]),TDD([makeQuery(id+"F42.boolean.opBoolean","COPY",EDGE,{"disambiguationData":[TD([makeQuery(id+"F17.opLoft","SWEPT_FACE",FACE,{"disambiguationData":[OSD([sQuery(id+"F3.wireOp",EDGE,"E20.4.0"),subQ21,subQ20,sQuery(id+"F4.wireOp",EDGE,"E26.4.0"),subQ19,subQ18])]})])],"derivedFrom":subQ9})])]}),makeQuery(id+"F47.opFillet","BLEND_FACE",FACE,{"disambiguationData":[OSD([subQ5,subQ7]),TDD([makeQuery(id+"F42.boolean.opBoolean","COPY",EDGE,{"disambiguationData":[TD([makeQuery(id+"F18.opLoft","SWEPT_FACE",FACE,{"disambiguationData":[OSD([sQuery(id+"F3.wireOp",EDGE,"E20.3.0"),subQ17,subQ16,sQuery(id+"F4.wireOp",EDGE,"E26.3.0"),subQ15,subQ14])]})])],"derivedFrom":subQ9})])]}),makeQuery(id+"F47.opFillet","BLEND_FACE",FACE,{"disambiguationData":[OSD([subQ5,subQ7]),TDD([makeQuery(id+"F42.boolean.opBoolean","COPY",EDGE,{"disambiguationData":[TD([makeQuery(id+"F19.opLoft","SWEPT_FACE",FACE,{"disambiguationData":[OSD([sQuery(id+"F3.wireOp",EDGE,"E20.2.0"),subQ13,subQ12,sQuery(id+"F4.wireOp",EDGE,"E26.2.0"),subQ11,subQ10])]})])],"derivedFrom":subQ9})])]}),makeQuery(id+"F47.opFillet","BLEND_FACE",FACE,{"disambiguationData":[OSD([subQ5,subQ7]),TDD([makeQuery(id+"F42.boolean.opBoolean","COPY",EDGE,{"disambiguationData":[TD([makeQuery(id+"F20.opLoft","SWEPT_FACE",FACE,{"disambiguationData":[OSD([sQuery(id+"F3.wireOp",EDGE,"E20.1.0"),subQ4,subQ3,sQuery(id+"F4.wireOp",EDGE,"E26.1.0"),subQ2,subQ1])]})])],"derivedFrom":subQ9})])]})]});}
            var Q50;
            {var subQ0=makeQuery(id+"F40.opExtrude","CAP_FACE",FACE,{"disambiguationData":[OSD([sQuery(id+"F39.wireOp",EDGE,"E29"),sQuery(id+"F39.wireOp",EDGE,"E30")])],"isStart":false});var subQ1=sQuery(id+"F4.wireOp",EDGE,"E26.1.3");var subQ2=sQuery(id+"F4.wireOp",EDGE,"E26.1.2");var subQ3=sQuery(id+"F3.wireOp",EDGE,"E20.1.3");var subQ4=sQuery(id+"F3.wireOp",EDGE,"E20.1.1");var subQ5=sQuery(id+"F41.wireOp",EDGE,"E35");var subQ6=makeQuery(id+"F42.opRevolve","SWEPT_FACE",FACE,{"disambiguationData":[OSD([subQ5])]});var subQ7=sQuery(id+"F41.wireOp",EDGE,"E36");var subQ8=makeQuery(id+"F42.opRevolve","SWEPT_FACE",FACE,{"disambiguationData":[OSD([subQ7])]});var subQ9=makeQuery(id+"F42.opRevolve","SWEPT_EDGE",EDGE,{"disambiguationData":[OSD([subQ5,subQ7])]});var subQ10=sQuery(id+"F4.wireOp",EDGE,"E26.2.3");var subQ11=sQuery(id+"F4.wireOp",EDGE,"E26.2.2");var subQ12=sQuery(id+"F3.wireOp",EDGE,"E20.2.3");var subQ13=sQuery(id+"F3.wireOp",EDGE,"E20.2.1");var subQ14=sQuery(id+"F4.wireOp",EDGE,"E26.3.3");var subQ15=sQuery(id+"F4.wireOp",EDGE,"E26.3.2");var subQ16=sQuery(id+"F3.wireOp",EDGE,"E20.3.3");var subQ17=sQuery(id+"F3.wireOp",EDGE,"E20.3.1");var subQ18=sQuery(id+"F4.wireOp",EDGE,"E26.4.3");var subQ19=sQuery(id+"F4.wireOp",EDGE,"E26.4.2");var subQ20=sQuery(id+"F3.wireOp",EDGE,"E20.4.3");var subQ21=sQuery(id+"F3.wireOp",EDGE,"E20.4.1");var subQ23=makeQuery(id+"F17.opLoft","SWEPT_FACE",FACE,{"disambiguationData":[OSD([sQuery(id+"F3.wireOp",EDGE,"E20.4.0"),subQ21,subQ20,sQuery(id+"F4.wireOp",EDGE,"E26.4.0"),subQ19,subQ18])]});var subQ24=sQuery(id+"F4.wireOp",EDGE,"E26.5.3");var subQ25=sQuery(id+"F4.wireOp",EDGE,"E26.5.2");var subQ26=sQuery(id+"F3.wireOp",EDGE,"E20.5.3");var subQ27=sQuery(id+"F3.wireOp",EDGE,"E20.5.1");var subQ28=sQuery(id+"F4.wireOp",EDGE,"E26.6.3");var subQ29=sQuery(id+"F4.wireOp",EDGE,"E26.6.2");var subQ30=sQuery(id+"F3.wireOp",EDGE,"E20.6.3");var subQ31=sQuery(id+"F3.wireOp",EDGE,"E20.6.1");var subQ32=sQuery(id+"F4.wireOp",EDGE,"E26.7.3");var subQ33=sQuery(id+"F4.wireOp",EDGE,"E26.7.2");var subQ34=sQuery(id+"F3.wireOp",EDGE,"E20.7.3");var subQ35=sQuery(id+"F3.wireOp",EDGE,"E20.7.1");var subQ36=sQuery(id+"F4.wireOp",EDGE,"E26.8.3");var subQ37=sQuery(id+"F4.wireOp",EDGE,"E26.8.2");var subQ38=sQuery(id+"F3.wireOp",EDGE,"E20.8.3");var subQ39=sQuery(id+"F3.wireOp",EDGE,"E20.8.1");var subQ40=sQuery(id+"F4.wireOp",EDGE,"E26.9.3");var subQ41=sQuery(id+"F4.wireOp",EDGE,"E26.9.2");var subQ42=sQuery(id+"F3.wireOp",EDGE,"E20.9.3");var subQ43=sQuery(id+"F3.wireOp",EDGE,"E20.9.1");var subQ44=sQuery(id+"F4.wireOp",EDGE,"E26.10.3");var subQ45=sQuery(id+"F4.wireOp",EDGE,"E26.10.2");var subQ46=sQuery(id+"F3.wireOp",EDGE,"E20.10.3");var subQ47=sQuery(id+"F3.wireOp",EDGE,"E20.10.1");var subQ48=sQuery(id+"F4.wireOp",EDGE,"E26.11.3");var subQ49=sQuery(id+"F4.wireOp",EDGE,"E26.11.2");var subQ50=sQuery(id+"F3.wireOp",EDGE,"E20.11.3");var subQ51=sQuery(id+"F3.wireOp",EDGE,"E20.11.1");var subQ52=sQuery(id+"F4.wireOp",EDGE,"E26.12.3");var subQ53=sQuery(id+"F4.wireOp",EDGE,"E26.12.2");var subQ54=sQuery(id+"F3.wireOp",EDGE,"E20.12.3");var subQ55=sQuery(id+"F3.wireOp",EDGE,"E20.12.1");var subQ56=sQuery(id+"F4.wireOp",EDGE,"E26.13.3");var subQ57=sQuery(id+"F4.wireOp",EDGE,"E26.13.2");var subQ58=sQuery(id+"F3.wireOp",EDGE,"E20.13.3");var subQ59=sQuery(id+"F3.wireOp",EDGE,"E20.13.1");var subQ60=sQuery(id+"F4.wireOp",EDGE,"E26.14.3");var subQ61=sQuery(id+"F4.wireOp",EDGE,"E26.14.2");var subQ62=sQuery(id+"F3.wireOp",EDGE,"E20.14.3");var subQ63=sQuery(id+"F3.wireOp",EDGE,"E20.14.1");var subQ64=sQuery(id+"F4.wireOp",EDGE,"E26.15.3");var subQ65=sQuery(id+"F4.wireOp",EDGE,"E26.15.2");var subQ66=sQuery(id+"F3.wireOp",EDGE,"E20.15.3");var subQ67=sQuery(id+"F3.wireOp",EDGE,"E20.15.1");var subQ68=sQuery(id+"F4.wireOp",EDGE,"E23");var subQ69=sQuery(id+"F4.wireOp",EDGE,"E22");var subQ70=sQuery(id+"F3.wireOp",EDGE,"E18.top");var subQ71=sQuery(id+"F3.wireOp",EDGE,"E18.bottom");var subQ74=makeQuery(id+"F42.boolean.opBoolean","COPY",FACE,{"disambiguationData":[TD([subQ23])],"derivedFrom":subQ6});var subQ75=makeQuery(id+"F17.boolean.opBoolean","INTERSECT",EDGE,{"derivedFrom":[makeQuery(id+"F1.opRevolve","SWEPT_FACE",FACE,{"disambiguationData":[OSD([sQuery(id+"F0.wireOp",EDGE,"E13")])]}),subQ23]});Q50=makeQuery(id+"F48.opFillet","BLEND_EDGE",EDGE,{"blendedFrom":[makeQuery(id+"F47.opFillet","TWEAK_EDGE",EDGE,{"derivedFrom":[makeQuery(id+"F45.opFillet","BLEND_VERTEX",VERTEX,{"blendedFrom":[subQ75,subQ23,subQ74],"blendedInto":[subQ23,subQ74]}),makeQuery(id+"F45.opFillet","BLEND_VERTEX",VERTEX,{"blendedFrom":[subQ75,makeQuery(id+"F42.boolean.opBoolean","MERGE",FACE,{"derivedFrom":[subQ0,subQ8]}),subQ74],"blendedInto":[makeQuery(id+"F42.boolean.opBoolean","MERGE",FACE,{"derivedFrom":[subQ0,subQ8]}),subQ74]})]}),makeQuery(id+"F47.opFillet","BLEND_FACE",FACE,{"disambiguationData":[OSD([subQ5,subQ7]),TDD([makeQuery(id+"F42.boolean.opBoolean","COPY",EDGE,{"disambiguationData":[TD([makeQuery(id+"F5.opLoft","SWEPT_FACE",FACE,{"disambiguationData":[OSD([subQ71,subQ70,sQuery(id+"F3.wireOp",EDGE,"E18.left"),sQuery(id+"F4.wireOp",EDGE,"E21"),subQ69,subQ68])]})])],"derivedFrom":subQ9})])]}),makeQuery(id+"F47.opFillet","BLEND_FACE",FACE,{"disambiguationData":[OSD([subQ5,subQ7]),TDD([makeQuery(id+"F42.boolean.opBoolean","COPY",EDGE,{"disambiguationData":[TD([makeQuery(id+"F6.opLoft","SWEPT_FACE",FACE,{"disambiguationData":[OSD([sQuery(id+"F3.wireOp",EDGE,"E20.15.0"),subQ67,subQ66,sQuery(id+"F4.wireOp",EDGE,"E26.15.0"),subQ65,subQ64])]})])],"derivedFrom":subQ9})])]}),makeQuery(id+"F47.opFillet","BLEND_FACE",FACE,{"disambiguationData":[OSD([subQ5,subQ7]),TDD([makeQuery(id+"F42.boolean.opBoolean","COPY",EDGE,{"disambiguationData":[TD([makeQuery(id+"F7.opLoft","SWEPT_FACE",FACE,{"disambiguationData":[OSD([sQuery(id+"F3.wireOp",EDGE,"E20.14.0"),subQ63,subQ62,sQuery(id+"F4.wireOp",EDGE,"E26.14.0"),subQ61,subQ60])]})])],"derivedFrom":subQ9})])]}),makeQuery(id+"F47.opFillet","BLEND_FACE",FACE,{"disambiguationData":[OSD([subQ5,subQ7]),TDD([makeQuery(id+"F42.boolean.opBoolean","COPY",EDGE,{"disambiguationData":[TD([makeQuery(id+"F8.opLoft","SWEPT_FACE",FACE,{"disambiguationData":[OSD([sQuery(id+"F3.wireOp",EDGE,"E20.13.0"),subQ59,subQ58,sQuery(id+"F4.wireOp",EDGE,"E26.13.0"),subQ57,subQ56])]})])],"derivedFrom":subQ9})])]}),makeQuery(id+"F47.opFillet","BLEND_FACE",FACE,{"disambiguationData":[OSD([subQ5,subQ7]),TDD([makeQuery(id+"F42.boolean.opBoolean","COPY",EDGE,{"disambiguationData":[TD([makeQuery(id+"F9.opLoft","SWEPT_FACE",FACE,{"disambiguationData":[OSD([sQuery(id+"F3.wireOp",EDGE,"E20.12.0"),subQ55,subQ54,sQuery(id+"F4.wireOp",EDGE,"E26.12.0"),subQ53,subQ52])]})])],"derivedFrom":subQ9})])]}),makeQuery(id+"F47.opFillet","BLEND_FACE",FACE,{"disambiguationData":[OSD([subQ5,subQ7]),TDD([makeQuery(id+"F42.boolean.opBoolean","COPY",EDGE,{"disambiguationData":[TD([makeQuery(id+"F10.opLoft","SWEPT_FACE",FACE,{"disambiguationData":[OSD([sQuery(id+"F3.wireOp",EDGE,"E20.11.0"),subQ51,subQ50,sQuery(id+"F4.wireOp",EDGE,"E26.11.0"),subQ49,subQ48])]})])],"derivedFrom":subQ9})])]}),makeQuery(id+"F47.opFillet","BLEND_FACE",FACE,{"disambiguationData":[OSD([subQ5,subQ7]),TDD([makeQuery(id+"F42.boolean.opBoolean","COPY",EDGE,{"disambiguationData":[TD([makeQuery(id+"F11.opLoft","SWEPT_FACE",FACE,{"disambiguationData":[OSD([sQuery(id+"F3.wireOp",EDGE,"E20.10.0"),subQ47,subQ46,sQuery(id+"F4.wireOp",EDGE,"E26.10.0"),subQ45,subQ44])]})])],"derivedFrom":subQ9})])]}),makeQuery(id+"F47.opFillet","BLEND_FACE",FACE,{"disambiguationData":[OSD([subQ5,subQ7]),TDD([makeQuery(id+"F42.boolean.opBoolean","COPY",EDGE,{"disambiguationData":[TD([makeQuery(id+"F12.opLoft","SWEPT_FACE",FACE,{"disambiguationData":[OSD([sQuery(id+"F3.wireOp",EDGE,"E20.9.0"),subQ43,subQ42,sQuery(id+"F4.wireOp",EDGE,"E26.9.0"),subQ41,subQ40])]})])],"derivedFrom":subQ9})])]}),makeQuery(id+"F47.opFillet","BLEND_FACE",FACE,{"disambiguationData":[OSD([subQ5,subQ7]),TDD([makeQuery(id+"F42.boolean.opBoolean","COPY",EDGE,{"disambiguationData":[TD([makeQuery(id+"F13.opLoft","SWEPT_FACE",FACE,{"disambiguationData":[OSD([sQuery(id+"F3.wireOp",EDGE,"E20.8.0"),subQ39,subQ38,sQuery(id+"F4.wireOp",EDGE,"E26.8.0"),subQ37,subQ36])]})])],"derivedFrom":subQ9})])]}),makeQuery(id+"F47.opFillet","BLEND_FACE",FACE,{"disambiguationData":[OSD([subQ5,subQ7]),TDD([makeQuery(id+"F42.boolean.opBoolean","COPY",EDGE,{"disambiguationData":[TD([makeQuery(id+"F14.opLoft","SWEPT_FACE",FACE,{"disambiguationData":[OSD([sQuery(id+"F3.wireOp",EDGE,"E20.7.0"),subQ35,subQ34,sQuery(id+"F4.wireOp",EDGE,"E26.7.0"),subQ33,subQ32])]})])],"derivedFrom":subQ9})])]}),makeQuery(id+"F47.opFillet","BLEND_FACE",FACE,{"disambiguationData":[OSD([subQ5,subQ7]),TDD([makeQuery(id+"F42.boolean.opBoolean","COPY",EDGE,{"disambiguationData":[TD([makeQuery(id+"F15.opLoft","SWEPT_FACE",FACE,{"disambiguationData":[OSD([sQuery(id+"F3.wireOp",EDGE,"E20.6.0"),subQ31,subQ30,sQuery(id+"F4.wireOp",EDGE,"E26.6.0"),subQ29,subQ28])]})])],"derivedFrom":subQ9})])]}),makeQuery(id+"F47.opFillet","BLEND_FACE",FACE,{"disambiguationData":[OSD([subQ5,subQ7]),TDD([makeQuery(id+"F42.boolean.opBoolean","COPY",EDGE,{"disambiguationData":[TD([makeQuery(id+"F16.opLoft","SWEPT_FACE",FACE,{"disambiguationData":[OSD([sQuery(id+"F3.wireOp",EDGE,"E20.5.0"),subQ27,subQ26,sQuery(id+"F4.wireOp",EDGE,"E26.5.0"),subQ25,subQ24])]})])],"derivedFrom":subQ9})])]}),makeQuery(id+"F47.opFillet","BLEND_FACE",FACE,{"disambiguationData":[OSD([subQ5,subQ7]),TDD([makeQuery(id+"F42.boolean.opBoolean","COPY",EDGE,{"disambiguationData":[TD([subQ23])],"derivedFrom":subQ9})])]}),makeQuery(id+"F47.opFillet","BLEND_FACE",FACE,{"disambiguationData":[OSD([subQ5,subQ7]),TDD([makeQuery(id+"F42.boolean.opBoolean","COPY",EDGE,{"disambiguationData":[TD([makeQuery(id+"F18.opLoft","SWEPT_FACE",FACE,{"disambiguationData":[OSD([sQuery(id+"F3.wireOp",EDGE,"E20.3.0"),subQ17,subQ16,sQuery(id+"F4.wireOp",EDGE,"E26.3.0"),subQ15,subQ14])]})])],"derivedFrom":subQ9})])]}),makeQuery(id+"F47.opFillet","BLEND_FACE",FACE,{"disambiguationData":[OSD([subQ5,subQ7]),TDD([makeQuery(id+"F42.boolean.opBoolean","COPY",EDGE,{"disambiguationData":[TD([makeQuery(id+"F19.opLoft","SWEPT_FACE",FACE,{"disambiguationData":[OSD([sQuery(id+"F3.wireOp",EDGE,"E20.2.0"),subQ13,subQ12,sQuery(id+"F4.wireOp",EDGE,"E26.2.0"),subQ11,subQ10])]})])],"derivedFrom":subQ9})])]}),makeQuery(id+"F47.opFillet","BLEND_FACE",FACE,{"disambiguationData":[OSD([subQ5,subQ7]),TDD([makeQuery(id+"F42.boolean.opBoolean","COPY",EDGE,{"disambiguationData":[TD([makeQuery(id+"F20.opLoft","SWEPT_FACE",FACE,{"disambiguationData":[OSD([sQuery(id+"F3.wireOp",EDGE,"E20.1.0"),subQ4,subQ3,sQuery(id+"F4.wireOp",EDGE,"E26.1.0"),subQ2,subQ1])]})])],"derivedFrom":subQ9})])]})],"blendedInto":[makeQuery(id+"F47.opFillet","BLEND_FACE",FACE,{"disambiguationData":[OSD([subQ5,subQ7]),TDD([makeQuery(id+"F42.boolean.opBoolean","COPY",EDGE,{"disambiguationData":[TD([makeQuery(id+"F5.opLoft","SWEPT_FACE",FACE,{"disambiguationData":[OSD([subQ71,subQ70,sQuery(id+"F3.wireOp",EDGE,"E18.left"),sQuery(id+"F4.wireOp",EDGE,"E21"),subQ69,subQ68])]})])],"derivedFrom":subQ9})])]}),makeQuery(id+"F47.opFillet","BLEND_FACE",FACE,{"disambiguationData":[OSD([subQ5,subQ7]),TDD([makeQuery(id+"F42.boolean.opBoolean","COPY",EDGE,{"disambiguationData":[TD([makeQuery(id+"F6.opLoft","SWEPT_FACE",FACE,{"disambiguationData":[OSD([sQuery(id+"F3.wireOp",EDGE,"E20.15.0"),subQ67,subQ66,sQuery(id+"F4.wireOp",EDGE,"E26.15.0"),subQ65,subQ64])]})])],"derivedFrom":subQ9})])]}),makeQuery(id+"F47.opFillet","BLEND_FACE",FACE,{"disambiguationData":[OSD([subQ5,subQ7]),TDD([makeQuery(id+"F42.boolean.opBoolean","COPY",EDGE,{"disambiguationData":[TD([makeQuery(id+"F7.opLoft","SWEPT_FACE",FACE,{"disambiguationData":[OSD([sQuery(id+"F3.wireOp",EDGE,"E20.14.0"),subQ63,subQ62,sQuery(id+"F4.wireOp",EDGE,"E26.14.0"),subQ61,subQ60])]})])],"derivedFrom":subQ9})])]}),makeQuery(id+"F47.opFillet","BLEND_FACE",FACE,{"disambiguationData":[OSD([subQ5,subQ7]),TDD([makeQuery(id+"F42.boolean.opBoolean","COPY",EDGE,{"disambiguationData":[TD([makeQuery(id+"F8.opLoft","SWEPT_FACE",FACE,{"disambiguationData":[OSD([sQuery(id+"F3.wireOp",EDGE,"E20.13.0"),subQ59,subQ58,sQuery(id+"F4.wireOp",EDGE,"E26.13.0"),subQ57,subQ56])]})])],"derivedFrom":subQ9})])]}),makeQuery(id+"F47.opFillet","BLEND_FACE",FACE,{"disambiguationData":[OSD([subQ5,subQ7]),TDD([makeQuery(id+"F42.boolean.opBoolean","COPY",EDGE,{"disambiguationData":[TD([makeQuery(id+"F9.opLoft","SWEPT_FACE",FACE,{"disambiguationData":[OSD([sQuery(id+"F3.wireOp",EDGE,"E20.12.0"),subQ55,subQ54,sQuery(id+"F4.wireOp",EDGE,"E26.12.0"),subQ53,subQ52])]})])],"derivedFrom":subQ9})])]}),makeQuery(id+"F47.opFillet","BLEND_FACE",FACE,{"disambiguationData":[OSD([subQ5,subQ7]),TDD([makeQuery(id+"F42.boolean.opBoolean","COPY",EDGE,{"disambiguationData":[TD([makeQuery(id+"F10.opLoft","SWEPT_FACE",FACE,{"disambiguationData":[OSD([sQuery(id+"F3.wireOp",EDGE,"E20.11.0"),subQ51,subQ50,sQuery(id+"F4.wireOp",EDGE,"E26.11.0"),subQ49,subQ48])]})])],"derivedFrom":subQ9})])]}),makeQuery(id+"F47.opFillet","BLEND_FACE",FACE,{"disambiguationData":[OSD([subQ5,subQ7]),TDD([makeQuery(id+"F42.boolean.opBoolean","COPY",EDGE,{"disambiguationData":[TD([makeQuery(id+"F11.opLoft","SWEPT_FACE",FACE,{"disambiguationData":[OSD([sQuery(id+"F3.wireOp",EDGE,"E20.10.0"),subQ47,subQ46,sQuery(id+"F4.wireOp",EDGE,"E26.10.0"),subQ45,subQ44])]})])],"derivedFrom":subQ9})])]}),makeQuery(id+"F47.opFillet","BLEND_FACE",FACE,{"disambiguationData":[OSD([subQ5,subQ7]),TDD([makeQuery(id+"F42.boolean.opBoolean","COPY",EDGE,{"disambiguationData":[TD([makeQuery(id+"F12.opLoft","SWEPT_FACE",FACE,{"disambiguationData":[OSD([sQuery(id+"F3.wireOp",EDGE,"E20.9.0"),subQ43,subQ42,sQuery(id+"F4.wireOp",EDGE,"E26.9.0"),subQ41,subQ40])]})])],"derivedFrom":subQ9})])]}),makeQuery(id+"F47.opFillet","BLEND_FACE",FACE,{"disambiguationData":[OSD([subQ5,subQ7]),TDD([makeQuery(id+"F42.boolean.opBoolean","COPY",EDGE,{"disambiguationData":[TD([makeQuery(id+"F13.opLoft","SWEPT_FACE",FACE,{"disambiguationData":[OSD([sQuery(id+"F3.wireOp",EDGE,"E20.8.0"),subQ39,subQ38,sQuery(id+"F4.wireOp",EDGE,"E26.8.0"),subQ37,subQ36])]})])],"derivedFrom":subQ9})])]}),makeQuery(id+"F47.opFillet","BLEND_FACE",FACE,{"disambiguationData":[OSD([subQ5,subQ7]),TDD([makeQuery(id+"F42.boolean.opBoolean","COPY",EDGE,{"disambiguationData":[TD([makeQuery(id+"F14.opLoft","SWEPT_FACE",FACE,{"disambiguationData":[OSD([sQuery(id+"F3.wireOp",EDGE,"E20.7.0"),subQ35,subQ34,sQuery(id+"F4.wireOp",EDGE,"E26.7.0"),subQ33,subQ32])]})])],"derivedFrom":subQ9})])]}),makeQuery(id+"F47.opFillet","BLEND_FACE",FACE,{"disambiguationData":[OSD([subQ5,subQ7]),TDD([makeQuery(id+"F42.boolean.opBoolean","COPY",EDGE,{"disambiguationData":[TD([makeQuery(id+"F15.opLoft","SWEPT_FACE",FACE,{"disambiguationData":[OSD([sQuery(id+"F3.wireOp",EDGE,"E20.6.0"),subQ31,subQ30,sQuery(id+"F4.wireOp",EDGE,"E26.6.0"),subQ29,subQ28])]})])],"derivedFrom":subQ9})])]}),makeQuery(id+"F47.opFillet","BLEND_FACE",FACE,{"disambiguationData":[OSD([subQ5,subQ7]),TDD([makeQuery(id+"F42.boolean.opBoolean","COPY",EDGE,{"disambiguationData":[TD([makeQuery(id+"F16.opLoft","SWEPT_FACE",FACE,{"disambiguationData":[OSD([sQuery(id+"F3.wireOp",EDGE,"E20.5.0"),subQ27,subQ26,sQuery(id+"F4.wireOp",EDGE,"E26.5.0"),subQ25,subQ24])]})])],"derivedFrom":subQ9})])]}),makeQuery(id+"F47.opFillet","BLEND_FACE",FACE,{"disambiguationData":[OSD([subQ5,subQ7]),TDD([makeQuery(id+"F42.boolean.opBoolean","COPY",EDGE,{"disambiguationData":[TD([subQ23])],"derivedFrom":subQ9})])]}),makeQuery(id+"F47.opFillet","BLEND_FACE",FACE,{"disambiguationData":[OSD([subQ5,subQ7]),TDD([makeQuery(id+"F42.boolean.opBoolean","COPY",EDGE,{"disambiguationData":[TD([makeQuery(id+"F18.opLoft","SWEPT_FACE",FACE,{"disambiguationData":[OSD([sQuery(id+"F3.wireOp",EDGE,"E20.3.0"),subQ17,subQ16,sQuery(id+"F4.wireOp",EDGE,"E26.3.0"),subQ15,subQ14])]})])],"derivedFrom":subQ9})])]}),makeQuery(id+"F47.opFillet","BLEND_FACE",FACE,{"disambiguationData":[OSD([subQ5,subQ7]),TDD([makeQuery(id+"F42.boolean.opBoolean","COPY",EDGE,{"disambiguationData":[TD([makeQuery(id+"F19.opLoft","SWEPT_FACE",FACE,{"disambiguationData":[OSD([sQuery(id+"F3.wireOp",EDGE,"E20.2.0"),subQ13,subQ12,sQuery(id+"F4.wireOp",EDGE,"E26.2.0"),subQ11,subQ10])]})])],"derivedFrom":subQ9})])]}),makeQuery(id+"F47.opFillet","BLEND_FACE",FACE,{"disambiguationData":[OSD([subQ5,subQ7]),TDD([makeQuery(id+"F42.boolean.opBoolean","COPY",EDGE,{"disambiguationData":[TD([makeQuery(id+"F20.opLoft","SWEPT_FACE",FACE,{"disambiguationData":[OSD([sQuery(id+"F3.wireOp",EDGE,"E20.1.0"),subQ4,subQ3,sQuery(id+"F4.wireOp",EDGE,"E26.1.0"),subQ2,subQ1])]})])],"derivedFrom":subQ9})])]})]});}
            var Q51;
            {var subQ0=makeQuery(id+"F40.opExtrude","CAP_FACE",FACE,{"disambiguationData":[OSD([sQuery(id+"F39.wireOp",EDGE,"E29"),sQuery(id+"F39.wireOp",EDGE,"E30")])],"isStart":false});var subQ1=sQuery(id+"F4.wireOp",EDGE,"E26.1.3");var subQ2=sQuery(id+"F4.wireOp",EDGE,"E26.1.2");var subQ3=sQuery(id+"F3.wireOp",EDGE,"E20.1.3");var subQ4=sQuery(id+"F3.wireOp",EDGE,"E20.1.1");var subQ5=sQuery(id+"F41.wireOp",EDGE,"E35");var subQ6=makeQuery(id+"F42.opRevolve","SWEPT_FACE",FACE,{"disambiguationData":[OSD([subQ5])]});var subQ7=sQuery(id+"F41.wireOp",EDGE,"E36");var subQ8=makeQuery(id+"F42.opRevolve","SWEPT_FACE",FACE,{"disambiguationData":[OSD([subQ7])]});var subQ9=makeQuery(id+"F42.opRevolve","SWEPT_EDGE",EDGE,{"disambiguationData":[OSD([subQ5,subQ7])]});var subQ10=sQuery(id+"F4.wireOp",EDGE,"E26.2.3");var subQ11=sQuery(id+"F4.wireOp",EDGE,"E26.2.2");var subQ12=sQuery(id+"F3.wireOp",EDGE,"E20.2.3");var subQ13=sQuery(id+"F3.wireOp",EDGE,"E20.2.1");var subQ14=sQuery(id+"F4.wireOp",EDGE,"E26.3.3");var subQ15=sQuery(id+"F4.wireOp",EDGE,"E26.3.2");var subQ16=sQuery(id+"F3.wireOp",EDGE,"E20.3.3");var subQ17=sQuery(id+"F3.wireOp",EDGE,"E20.3.1");var subQ18=makeQuery(id+"F18.opLoft","SWEPT_FACE",FACE,{"disambiguationData":[OSD([sQuery(id+"F3.wireOp",EDGE,"E20.3.0"),subQ17,subQ16,sQuery(id+"F4.wireOp",EDGE,"E26.3.0"),subQ15,subQ14])]});var subQ20=sQuery(id+"F4.wireOp",EDGE,"E26.4.3");var subQ21=sQuery(id+"F4.wireOp",EDGE,"E26.4.2");var subQ22=sQuery(id+"F3.wireOp",EDGE,"E20.4.3");var subQ23=sQuery(id+"F3.wireOp",EDGE,"E20.4.1");var subQ24=sQuery(id+"F4.wireOp",EDGE,"E26.5.3");var subQ25=sQuery(id+"F4.wireOp",EDGE,"E26.5.2");var subQ26=sQuery(id+"F3.wireOp",EDGE,"E20.5.3");var subQ27=sQuery(id+"F3.wireOp",EDGE,"E20.5.1");var subQ28=sQuery(id+"F4.wireOp",EDGE,"E26.6.3");var subQ29=sQuery(id+"F4.wireOp",EDGE,"E26.6.2");var subQ30=sQuery(id+"F3.wireOp",EDGE,"E20.6.3");var subQ31=sQuery(id+"F3.wireOp",EDGE,"E20.6.1");var subQ32=sQuery(id+"F4.wireOp",EDGE,"E26.7.3");var subQ33=sQuery(id+"F4.wireOp",EDGE,"E26.7.2");var subQ34=sQuery(id+"F3.wireOp",EDGE,"E20.7.3");var subQ35=sQuery(id+"F3.wireOp",EDGE,"E20.7.1");var subQ36=sQuery(id+"F4.wireOp",EDGE,"E26.8.3");var subQ37=sQuery(id+"F4.wireOp",EDGE,"E26.8.2");var subQ38=sQuery(id+"F3.wireOp",EDGE,"E20.8.3");var subQ39=sQuery(id+"F3.wireOp",EDGE,"E20.8.1");var subQ40=sQuery(id+"F4.wireOp",EDGE,"E26.9.3");var subQ41=sQuery(id+"F4.wireOp",EDGE,"E26.9.2");var subQ42=sQuery(id+"F3.wireOp",EDGE,"E20.9.3");var subQ43=sQuery(id+"F3.wireOp",EDGE,"E20.9.1");var subQ44=sQuery(id+"F4.wireOp",EDGE,"E26.10.3");var subQ45=sQuery(id+"F4.wireOp",EDGE,"E26.10.2");var subQ46=sQuery(id+"F3.wireOp",EDGE,"E20.10.3");var subQ47=sQuery(id+"F3.wireOp",EDGE,"E20.10.1");var subQ48=sQuery(id+"F4.wireOp",EDGE,"E26.11.3");var subQ49=sQuery(id+"F4.wireOp",EDGE,"E26.11.2");var subQ50=sQuery(id+"F3.wireOp",EDGE,"E20.11.3");var subQ51=sQuery(id+"F3.wireOp",EDGE,"E20.11.1");var subQ52=sQuery(id+"F4.wireOp",EDGE,"E26.12.3");var subQ53=sQuery(id+"F4.wireOp",EDGE,"E26.12.2");var subQ54=sQuery(id+"F3.wireOp",EDGE,"E20.12.3");var subQ55=sQuery(id+"F3.wireOp",EDGE,"E20.12.1");var subQ56=sQuery(id+"F4.wireOp",EDGE,"E26.13.3");var subQ57=sQuery(id+"F4.wireOp",EDGE,"E26.13.2");var subQ58=sQuery(id+"F3.wireOp",EDGE,"E20.13.3");var subQ59=sQuery(id+"F3.wireOp",EDGE,"E20.13.1");var subQ60=sQuery(id+"F4.wireOp",EDGE,"E26.14.3");var subQ61=sQuery(id+"F4.wireOp",EDGE,"E26.14.2");var subQ62=sQuery(id+"F3.wireOp",EDGE,"E20.14.3");var subQ63=sQuery(id+"F3.wireOp",EDGE,"E20.14.1");var subQ64=sQuery(id+"F4.wireOp",EDGE,"E26.15.3");var subQ65=sQuery(id+"F4.wireOp",EDGE,"E26.15.2");var subQ66=sQuery(id+"F3.wireOp",EDGE,"E20.15.3");var subQ67=sQuery(id+"F3.wireOp",EDGE,"E20.15.1");var subQ68=sQuery(id+"F4.wireOp",EDGE,"E23");var subQ69=sQuery(id+"F4.wireOp",EDGE,"E22");var subQ70=sQuery(id+"F3.wireOp",EDGE,"E18.top");var subQ71=sQuery(id+"F3.wireOp",EDGE,"E18.bottom");var subQ74=makeQuery(id+"F42.boolean.opBoolean","COPY",FACE,{"disambiguationData":[TD([subQ18])],"derivedFrom":subQ6});var subQ75=makeQuery(id+"F18.boolean.opBoolean","INTERSECT",EDGE,{"derivedFrom":[makeQuery(id+"F1.opRevolve","SWEPT_FACE",FACE,{"disambiguationData":[OSD([sQuery(id+"F0.wireOp",EDGE,"E13")])]}),subQ18]});Q51=makeQuery(id+"F48.opFillet","BLEND_EDGE",EDGE,{"blendedFrom":[makeQuery(id+"F47.opFillet","TWEAK_EDGE",EDGE,{"derivedFrom":[makeQuery(id+"F45.opFillet","BLEND_VERTEX",VERTEX,{"blendedFrom":[subQ75,subQ18,subQ74],"blendedInto":[subQ18,subQ74]}),makeQuery(id+"F45.opFillet","BLEND_VERTEX",VERTEX,{"blendedFrom":[subQ75,makeQuery(id+"F42.boolean.opBoolean","MERGE",FACE,{"derivedFrom":[subQ0,subQ8]}),subQ74],"blendedInto":[makeQuery(id+"F42.boolean.opBoolean","MERGE",FACE,{"derivedFrom":[subQ0,subQ8]}),subQ74]})]}),makeQuery(id+"F47.opFillet","BLEND_FACE",FACE,{"disambiguationData":[OSD([subQ5,subQ7]),TDD([makeQuery(id+"F42.boolean.opBoolean","COPY",EDGE,{"disambiguationData":[TD([makeQuery(id+"F5.opLoft","SWEPT_FACE",FACE,{"disambiguationData":[OSD([subQ71,subQ70,sQuery(id+"F3.wireOp",EDGE,"E18.left"),sQuery(id+"F4.wireOp",EDGE,"E21"),subQ69,subQ68])]})])],"derivedFrom":subQ9})])]}),makeQuery(id+"F47.opFillet","BLEND_FACE",FACE,{"disambiguationData":[OSD([subQ5,subQ7]),TDD([makeQuery(id+"F42.boolean.opBoolean","COPY",EDGE,{"disambiguationData":[TD([makeQuery(id+"F6.opLoft","SWEPT_FACE",FACE,{"disambiguationData":[OSD([sQuery(id+"F3.wireOp",EDGE,"E20.15.0"),subQ67,subQ66,sQuery(id+"F4.wireOp",EDGE,"E26.15.0"),subQ65,subQ64])]})])],"derivedFrom":subQ9})])]}),makeQuery(id+"F47.opFillet","BLEND_FACE",FACE,{"disambiguationData":[OSD([subQ5,subQ7]),TDD([makeQuery(id+"F42.boolean.opBoolean","COPY",EDGE,{"disambiguationData":[TD([makeQuery(id+"F7.opLoft","SWEPT_FACE",FACE,{"disambiguationData":[OSD([sQuery(id+"F3.wireOp",EDGE,"E20.14.0"),subQ63,subQ62,sQuery(id+"F4.wireOp",EDGE,"E26.14.0"),subQ61,subQ60])]})])],"derivedFrom":subQ9})])]}),makeQuery(id+"F47.opFillet","BLEND_FACE",FACE,{"disambiguationData":[OSD([subQ5,subQ7]),TDD([makeQuery(id+"F42.boolean.opBoolean","COPY",EDGE,{"disambiguationData":[TD([makeQuery(id+"F8.opLoft","SWEPT_FACE",FACE,{"disambiguationData":[OSD([sQuery(id+"F3.wireOp",EDGE,"E20.13.0"),subQ59,subQ58,sQuery(id+"F4.wireOp",EDGE,"E26.13.0"),subQ57,subQ56])]})])],"derivedFrom":subQ9})])]}),makeQuery(id+"F47.opFillet","BLEND_FACE",FACE,{"disambiguationData":[OSD([subQ5,subQ7]),TDD([makeQuery(id+"F42.boolean.opBoolean","COPY",EDGE,{"disambiguationData":[TD([makeQuery(id+"F9.opLoft","SWEPT_FACE",FACE,{"disambiguationData":[OSD([sQuery(id+"F3.wireOp",EDGE,"E20.12.0"),subQ55,subQ54,sQuery(id+"F4.wireOp",EDGE,"E26.12.0"),subQ53,subQ52])]})])],"derivedFrom":subQ9})])]}),makeQuery(id+"F47.opFillet","BLEND_FACE",FACE,{"disambiguationData":[OSD([subQ5,subQ7]),TDD([makeQuery(id+"F42.boolean.opBoolean","COPY",EDGE,{"disambiguationData":[TD([makeQuery(id+"F10.opLoft","SWEPT_FACE",FACE,{"disambiguationData":[OSD([sQuery(id+"F3.wireOp",EDGE,"E20.11.0"),subQ51,subQ50,sQuery(id+"F4.wireOp",EDGE,"E26.11.0"),subQ49,subQ48])]})])],"derivedFrom":subQ9})])]}),makeQuery(id+"F47.opFillet","BLEND_FACE",FACE,{"disambiguationData":[OSD([subQ5,subQ7]),TDD([makeQuery(id+"F42.boolean.opBoolean","COPY",EDGE,{"disambiguationData":[TD([makeQuery(id+"F11.opLoft","SWEPT_FACE",FACE,{"disambiguationData":[OSD([sQuery(id+"F3.wireOp",EDGE,"E20.10.0"),subQ47,subQ46,sQuery(id+"F4.wireOp",EDGE,"E26.10.0"),subQ45,subQ44])]})])],"derivedFrom":subQ9})])]}),makeQuery(id+"F47.opFillet","BLEND_FACE",FACE,{"disambiguationData":[OSD([subQ5,subQ7]),TDD([makeQuery(id+"F42.boolean.opBoolean","COPY",EDGE,{"disambiguationData":[TD([makeQuery(id+"F12.opLoft","SWEPT_FACE",FACE,{"disambiguationData":[OSD([sQuery(id+"F3.wireOp",EDGE,"E20.9.0"),subQ43,subQ42,sQuery(id+"F4.wireOp",EDGE,"E26.9.0"),subQ41,subQ40])]})])],"derivedFrom":subQ9})])]}),makeQuery(id+"F47.opFillet","BLEND_FACE",FACE,{"disambiguationData":[OSD([subQ5,subQ7]),TDD([makeQuery(id+"F42.boolean.opBoolean","COPY",EDGE,{"disambiguationData":[TD([makeQuery(id+"F13.opLoft","SWEPT_FACE",FACE,{"disambiguationData":[OSD([sQuery(id+"F3.wireOp",EDGE,"E20.8.0"),subQ39,subQ38,sQuery(id+"F4.wireOp",EDGE,"E26.8.0"),subQ37,subQ36])]})])],"derivedFrom":subQ9})])]}),makeQuery(id+"F47.opFillet","BLEND_FACE",FACE,{"disambiguationData":[OSD([subQ5,subQ7]),TDD([makeQuery(id+"F42.boolean.opBoolean","COPY",EDGE,{"disambiguationData":[TD([makeQuery(id+"F14.opLoft","SWEPT_FACE",FACE,{"disambiguationData":[OSD([sQuery(id+"F3.wireOp",EDGE,"E20.7.0"),subQ35,subQ34,sQuery(id+"F4.wireOp",EDGE,"E26.7.0"),subQ33,subQ32])]})])],"derivedFrom":subQ9})])]}),makeQuery(id+"F47.opFillet","BLEND_FACE",FACE,{"disambiguationData":[OSD([subQ5,subQ7]),TDD([makeQuery(id+"F42.boolean.opBoolean","COPY",EDGE,{"disambiguationData":[TD([makeQuery(id+"F15.opLoft","SWEPT_FACE",FACE,{"disambiguationData":[OSD([sQuery(id+"F3.wireOp",EDGE,"E20.6.0"),subQ31,subQ30,sQuery(id+"F4.wireOp",EDGE,"E26.6.0"),subQ29,subQ28])]})])],"derivedFrom":subQ9})])]}),makeQuery(id+"F47.opFillet","BLEND_FACE",FACE,{"disambiguationData":[OSD([subQ5,subQ7]),TDD([makeQuery(id+"F42.boolean.opBoolean","COPY",EDGE,{"disambiguationData":[TD([makeQuery(id+"F16.opLoft","SWEPT_FACE",FACE,{"disambiguationData":[OSD([sQuery(id+"F3.wireOp",EDGE,"E20.5.0"),subQ27,subQ26,sQuery(id+"F4.wireOp",EDGE,"E26.5.0"),subQ25,subQ24])]})])],"derivedFrom":subQ9})])]}),makeQuery(id+"F47.opFillet","BLEND_FACE",FACE,{"disambiguationData":[OSD([subQ5,subQ7]),TDD([makeQuery(id+"F42.boolean.opBoolean","COPY",EDGE,{"disambiguationData":[TD([makeQuery(id+"F17.opLoft","SWEPT_FACE",FACE,{"disambiguationData":[OSD([sQuery(id+"F3.wireOp",EDGE,"E20.4.0"),subQ23,subQ22,sQuery(id+"F4.wireOp",EDGE,"E26.4.0"),subQ21,subQ20])]})])],"derivedFrom":subQ9})])]}),makeQuery(id+"F47.opFillet","BLEND_FACE",FACE,{"disambiguationData":[OSD([subQ5,subQ7]),TDD([makeQuery(id+"F42.boolean.opBoolean","COPY",EDGE,{"disambiguationData":[TD([subQ18])],"derivedFrom":subQ9})])]}),makeQuery(id+"F47.opFillet","BLEND_FACE",FACE,{"disambiguationData":[OSD([subQ5,subQ7]),TDD([makeQuery(id+"F42.boolean.opBoolean","COPY",EDGE,{"disambiguationData":[TD([makeQuery(id+"F19.opLoft","SWEPT_FACE",FACE,{"disambiguationData":[OSD([sQuery(id+"F3.wireOp",EDGE,"E20.2.0"),subQ13,subQ12,sQuery(id+"F4.wireOp",EDGE,"E26.2.0"),subQ11,subQ10])]})])],"derivedFrom":subQ9})])]}),makeQuery(id+"F47.opFillet","BLEND_FACE",FACE,{"disambiguationData":[OSD([subQ5,subQ7]),TDD([makeQuery(id+"F42.boolean.opBoolean","COPY",EDGE,{"disambiguationData":[TD([makeQuery(id+"F20.opLoft","SWEPT_FACE",FACE,{"disambiguationData":[OSD([sQuery(id+"F3.wireOp",EDGE,"E20.1.0"),subQ4,subQ3,sQuery(id+"F4.wireOp",EDGE,"E26.1.0"),subQ2,subQ1])]})])],"derivedFrom":subQ9})])]})],"blendedInto":[makeQuery(id+"F47.opFillet","BLEND_FACE",FACE,{"disambiguationData":[OSD([subQ5,subQ7]),TDD([makeQuery(id+"F42.boolean.opBoolean","COPY",EDGE,{"disambiguationData":[TD([makeQuery(id+"F5.opLoft","SWEPT_FACE",FACE,{"disambiguationData":[OSD([subQ71,subQ70,sQuery(id+"F3.wireOp",EDGE,"E18.left"),sQuery(id+"F4.wireOp",EDGE,"E21"),subQ69,subQ68])]})])],"derivedFrom":subQ9})])]}),makeQuery(id+"F47.opFillet","BLEND_FACE",FACE,{"disambiguationData":[OSD([subQ5,subQ7]),TDD([makeQuery(id+"F42.boolean.opBoolean","COPY",EDGE,{"disambiguationData":[TD([makeQuery(id+"F6.opLoft","SWEPT_FACE",FACE,{"disambiguationData":[OSD([sQuery(id+"F3.wireOp",EDGE,"E20.15.0"),subQ67,subQ66,sQuery(id+"F4.wireOp",EDGE,"E26.15.0"),subQ65,subQ64])]})])],"derivedFrom":subQ9})])]}),makeQuery(id+"F47.opFillet","BLEND_FACE",FACE,{"disambiguationData":[OSD([subQ5,subQ7]),TDD([makeQuery(id+"F42.boolean.opBoolean","COPY",EDGE,{"disambiguationData":[TD([makeQuery(id+"F7.opLoft","SWEPT_FACE",FACE,{"disambiguationData":[OSD([sQuery(id+"F3.wireOp",EDGE,"E20.14.0"),subQ63,subQ62,sQuery(id+"F4.wireOp",EDGE,"E26.14.0"),subQ61,subQ60])]})])],"derivedFrom":subQ9})])]}),makeQuery(id+"F47.opFillet","BLEND_FACE",FACE,{"disambiguationData":[OSD([subQ5,subQ7]),TDD([makeQuery(id+"F42.boolean.opBoolean","COPY",EDGE,{"disambiguationData":[TD([makeQuery(id+"F8.opLoft","SWEPT_FACE",FACE,{"disambiguationData":[OSD([sQuery(id+"F3.wireOp",EDGE,"E20.13.0"),subQ59,subQ58,sQuery(id+"F4.wireOp",EDGE,"E26.13.0"),subQ57,subQ56])]})])],"derivedFrom":subQ9})])]}),makeQuery(id+"F47.opFillet","BLEND_FACE",FACE,{"disambiguationData":[OSD([subQ5,subQ7]),TDD([makeQuery(id+"F42.boolean.opBoolean","COPY",EDGE,{"disambiguationData":[TD([makeQuery(id+"F9.opLoft","SWEPT_FACE",FACE,{"disambiguationData":[OSD([sQuery(id+"F3.wireOp",EDGE,"E20.12.0"),subQ55,subQ54,sQuery(id+"F4.wireOp",EDGE,"E26.12.0"),subQ53,subQ52])]})])],"derivedFrom":subQ9})])]}),makeQuery(id+"F47.opFillet","BLEND_FACE",FACE,{"disambiguationData":[OSD([subQ5,subQ7]),TDD([makeQuery(id+"F42.boolean.opBoolean","COPY",EDGE,{"disambiguationData":[TD([makeQuery(id+"F10.opLoft","SWEPT_FACE",FACE,{"disambiguationData":[OSD([sQuery(id+"F3.wireOp",EDGE,"E20.11.0"),subQ51,subQ50,sQuery(id+"F4.wireOp",EDGE,"E26.11.0"),subQ49,subQ48])]})])],"derivedFrom":subQ9})])]}),makeQuery(id+"F47.opFillet","BLEND_FACE",FACE,{"disambiguationData":[OSD([subQ5,subQ7]),TDD([makeQuery(id+"F42.boolean.opBoolean","COPY",EDGE,{"disambiguationData":[TD([makeQuery(id+"F11.opLoft","SWEPT_FACE",FACE,{"disambiguationData":[OSD([sQuery(id+"F3.wireOp",EDGE,"E20.10.0"),subQ47,subQ46,sQuery(id+"F4.wireOp",EDGE,"E26.10.0"),subQ45,subQ44])]})])],"derivedFrom":subQ9})])]}),makeQuery(id+"F47.opFillet","BLEND_FACE",FACE,{"disambiguationData":[OSD([subQ5,subQ7]),TDD([makeQuery(id+"F42.boolean.opBoolean","COPY",EDGE,{"disambiguationData":[TD([makeQuery(id+"F12.opLoft","SWEPT_FACE",FACE,{"disambiguationData":[OSD([sQuery(id+"F3.wireOp",EDGE,"E20.9.0"),subQ43,subQ42,sQuery(id+"F4.wireOp",EDGE,"E26.9.0"),subQ41,subQ40])]})])],"derivedFrom":subQ9})])]}),makeQuery(id+"F47.opFillet","BLEND_FACE",FACE,{"disambiguationData":[OSD([subQ5,subQ7]),TDD([makeQuery(id+"F42.boolean.opBoolean","COPY",EDGE,{"disambiguationData":[TD([makeQuery(id+"F13.opLoft","SWEPT_FACE",FACE,{"disambiguationData":[OSD([sQuery(id+"F3.wireOp",EDGE,"E20.8.0"),subQ39,subQ38,sQuery(id+"F4.wireOp",EDGE,"E26.8.0"),subQ37,subQ36])]})])],"derivedFrom":subQ9})])]}),makeQuery(id+"F47.opFillet","BLEND_FACE",FACE,{"disambiguationData":[OSD([subQ5,subQ7]),TDD([makeQuery(id+"F42.boolean.opBoolean","COPY",EDGE,{"disambiguationData":[TD([makeQuery(id+"F14.opLoft","SWEPT_FACE",FACE,{"disambiguationData":[OSD([sQuery(id+"F3.wireOp",EDGE,"E20.7.0"),subQ35,subQ34,sQuery(id+"F4.wireOp",EDGE,"E26.7.0"),subQ33,subQ32])]})])],"derivedFrom":subQ9})])]}),makeQuery(id+"F47.opFillet","BLEND_FACE",FACE,{"disambiguationData":[OSD([subQ5,subQ7]),TDD([makeQuery(id+"F42.boolean.opBoolean","COPY",EDGE,{"disambiguationData":[TD([makeQuery(id+"F15.opLoft","SWEPT_FACE",FACE,{"disambiguationData":[OSD([sQuery(id+"F3.wireOp",EDGE,"E20.6.0"),subQ31,subQ30,sQuery(id+"F4.wireOp",EDGE,"E26.6.0"),subQ29,subQ28])]})])],"derivedFrom":subQ9})])]}),makeQuery(id+"F47.opFillet","BLEND_FACE",FACE,{"disambiguationData":[OSD([subQ5,subQ7]),TDD([makeQuery(id+"F42.boolean.opBoolean","COPY",EDGE,{"disambiguationData":[TD([makeQuery(id+"F16.opLoft","SWEPT_FACE",FACE,{"disambiguationData":[OSD([sQuery(id+"F3.wireOp",EDGE,"E20.5.0"),subQ27,subQ26,sQuery(id+"F4.wireOp",EDGE,"E26.5.0"),subQ25,subQ24])]})])],"derivedFrom":subQ9})])]}),makeQuery(id+"F47.opFillet","BLEND_FACE",FACE,{"disambiguationData":[OSD([subQ5,subQ7]),TDD([makeQuery(id+"F42.boolean.opBoolean","COPY",EDGE,{"disambiguationData":[TD([makeQuery(id+"F17.opLoft","SWEPT_FACE",FACE,{"disambiguationData":[OSD([sQuery(id+"F3.wireOp",EDGE,"E20.4.0"),subQ23,subQ22,sQuery(id+"F4.wireOp",EDGE,"E26.4.0"),subQ21,subQ20])]})])],"derivedFrom":subQ9})])]}),makeQuery(id+"F47.opFillet","BLEND_FACE",FACE,{"disambiguationData":[OSD([subQ5,subQ7]),TDD([makeQuery(id+"F42.boolean.opBoolean","COPY",EDGE,{"disambiguationData":[TD([subQ18])],"derivedFrom":subQ9})])]}),makeQuery(id+"F47.opFillet","BLEND_FACE",FACE,{"disambiguationData":[OSD([subQ5,subQ7]),TDD([makeQuery(id+"F42.boolean.opBoolean","COPY",EDGE,{"disambiguationData":[TD([makeQuery(id+"F19.opLoft","SWEPT_FACE",FACE,{"disambiguationData":[OSD([sQuery(id+"F3.wireOp",EDGE,"E20.2.0"),subQ13,subQ12,sQuery(id+"F4.wireOp",EDGE,"E26.2.0"),subQ11,subQ10])]})])],"derivedFrom":subQ9})])]}),makeQuery(id+"F47.opFillet","BLEND_FACE",FACE,{"disambiguationData":[OSD([subQ5,subQ7]),TDD([makeQuery(id+"F42.boolean.opBoolean","COPY",EDGE,{"disambiguationData":[TD([makeQuery(id+"F20.opLoft","SWEPT_FACE",FACE,{"disambiguationData":[OSD([sQuery(id+"F3.wireOp",EDGE,"E20.1.0"),subQ4,subQ3,sQuery(id+"F4.wireOp",EDGE,"E26.1.0"),subQ2,subQ1])]})])],"derivedFrom":subQ9})])]})]});}
            var Q52;
            {var subQ0=makeQuery(id+"F40.opExtrude","CAP_FACE",FACE,{"disambiguationData":[OSD([sQuery(id+"F39.wireOp",EDGE,"E29"),sQuery(id+"F39.wireOp",EDGE,"E30")])],"isStart":false});var subQ1=sQuery(id+"F4.wireOp",EDGE,"E26.1.3");var subQ2=sQuery(id+"F4.wireOp",EDGE,"E26.1.2");var subQ3=sQuery(id+"F3.wireOp",EDGE,"E20.1.3");var subQ4=sQuery(id+"F3.wireOp",EDGE,"E20.1.1");var subQ5=sQuery(id+"F41.wireOp",EDGE,"E35");var subQ6=makeQuery(id+"F42.opRevolve","SWEPT_FACE",FACE,{"disambiguationData":[OSD([subQ5])]});var subQ7=sQuery(id+"F41.wireOp",EDGE,"E36");var subQ8=makeQuery(id+"F42.opRevolve","SWEPT_FACE",FACE,{"disambiguationData":[OSD([subQ7])]});var subQ9=makeQuery(id+"F42.opRevolve","SWEPT_EDGE",EDGE,{"disambiguationData":[OSD([subQ5,subQ7])]});var subQ10=sQuery(id+"F4.wireOp",EDGE,"E26.2.3");var subQ11=sQuery(id+"F4.wireOp",EDGE,"E26.2.2");var subQ12=sQuery(id+"F3.wireOp",EDGE,"E20.2.3");var subQ13=sQuery(id+"F3.wireOp",EDGE,"E20.2.1");var subQ15=makeQuery(id+"F19.opLoft","SWEPT_FACE",FACE,{"disambiguationData":[OSD([sQuery(id+"F3.wireOp",EDGE,"E20.2.0"),subQ13,subQ12,sQuery(id+"F4.wireOp",EDGE,"E26.2.0"),subQ11,subQ10])]});var subQ16=sQuery(id+"F4.wireOp",EDGE,"E26.3.3");var subQ17=sQuery(id+"F4.wireOp",EDGE,"E26.3.2");var subQ18=sQuery(id+"F3.wireOp",EDGE,"E20.3.3");var subQ19=sQuery(id+"F3.wireOp",EDGE,"E20.3.1");var subQ20=sQuery(id+"F4.wireOp",EDGE,"E26.4.3");var subQ21=sQuery(id+"F4.wireOp",EDGE,"E26.4.2");var subQ22=sQuery(id+"F3.wireOp",EDGE,"E20.4.3");var subQ23=sQuery(id+"F3.wireOp",EDGE,"E20.4.1");var subQ24=sQuery(id+"F4.wireOp",EDGE,"E26.5.3");var subQ25=sQuery(id+"F4.wireOp",EDGE,"E26.5.2");var subQ26=sQuery(id+"F3.wireOp",EDGE,"E20.5.3");var subQ27=sQuery(id+"F3.wireOp",EDGE,"E20.5.1");var subQ28=sQuery(id+"F4.wireOp",EDGE,"E26.6.3");var subQ29=sQuery(id+"F4.wireOp",EDGE,"E26.6.2");var subQ30=sQuery(id+"F3.wireOp",EDGE,"E20.6.3");var subQ31=sQuery(id+"F3.wireOp",EDGE,"E20.6.1");var subQ32=sQuery(id+"F4.wireOp",EDGE,"E26.7.3");var subQ33=sQuery(id+"F4.wireOp",EDGE,"E26.7.2");var subQ34=sQuery(id+"F3.wireOp",EDGE,"E20.7.3");var subQ35=sQuery(id+"F3.wireOp",EDGE,"E20.7.1");var subQ36=sQuery(id+"F4.wireOp",EDGE,"E26.8.3");var subQ37=sQuery(id+"F4.wireOp",EDGE,"E26.8.2");var subQ38=sQuery(id+"F3.wireOp",EDGE,"E20.8.3");var subQ39=sQuery(id+"F3.wireOp",EDGE,"E20.8.1");var subQ40=sQuery(id+"F4.wireOp",EDGE,"E26.9.3");var subQ41=sQuery(id+"F4.wireOp",EDGE,"E26.9.2");var subQ42=sQuery(id+"F3.wireOp",EDGE,"E20.9.3");var subQ43=sQuery(id+"F3.wireOp",EDGE,"E20.9.1");var subQ44=sQuery(id+"F4.wireOp",EDGE,"E26.10.3");var subQ45=sQuery(id+"F4.wireOp",EDGE,"E26.10.2");var subQ46=sQuery(id+"F3.wireOp",EDGE,"E20.10.3");var subQ47=sQuery(id+"F3.wireOp",EDGE,"E20.10.1");var subQ48=sQuery(id+"F4.wireOp",EDGE,"E26.11.3");var subQ49=sQuery(id+"F4.wireOp",EDGE,"E26.11.2");var subQ50=sQuery(id+"F3.wireOp",EDGE,"E20.11.3");var subQ51=sQuery(id+"F3.wireOp",EDGE,"E20.11.1");var subQ52=sQuery(id+"F4.wireOp",EDGE,"E26.12.3");var subQ53=sQuery(id+"F4.wireOp",EDGE,"E26.12.2");var subQ54=sQuery(id+"F3.wireOp",EDGE,"E20.12.3");var subQ55=sQuery(id+"F3.wireOp",EDGE,"E20.12.1");var subQ56=sQuery(id+"F4.wireOp",EDGE,"E26.13.3");var subQ57=sQuery(id+"F4.wireOp",EDGE,"E26.13.2");var subQ58=sQuery(id+"F3.wireOp",EDGE,"E20.13.3");var subQ59=sQuery(id+"F3.wireOp",EDGE,"E20.13.1");var subQ60=sQuery(id+"F4.wireOp",EDGE,"E26.14.3");var subQ61=sQuery(id+"F4.wireOp",EDGE,"E26.14.2");var subQ62=sQuery(id+"F3.wireOp",EDGE,"E20.14.3");var subQ63=sQuery(id+"F3.wireOp",EDGE,"E20.14.1");var subQ64=sQuery(id+"F4.wireOp",EDGE,"E26.15.3");var subQ65=sQuery(id+"F4.wireOp",EDGE,"E26.15.2");var subQ66=sQuery(id+"F3.wireOp",EDGE,"E20.15.3");var subQ67=sQuery(id+"F3.wireOp",EDGE,"E20.15.1");var subQ68=sQuery(id+"F4.wireOp",EDGE,"E23");var subQ69=sQuery(id+"F4.wireOp",EDGE,"E22");var subQ70=sQuery(id+"F3.wireOp",EDGE,"E18.top");var subQ71=sQuery(id+"F3.wireOp",EDGE,"E18.bottom");var subQ74=makeQuery(id+"F42.boolean.opBoolean","COPY",FACE,{"disambiguationData":[TD([subQ15])],"derivedFrom":subQ6});var subQ75=makeQuery(id+"F19.boolean.opBoolean","INTERSECT",EDGE,{"derivedFrom":[makeQuery(id+"F1.opRevolve","SWEPT_FACE",FACE,{"disambiguationData":[OSD([sQuery(id+"F0.wireOp",EDGE,"E13")])]}),subQ15]});Q52=makeQuery(id+"F48.opFillet","BLEND_EDGE",EDGE,{"blendedFrom":[makeQuery(id+"F47.opFillet","TWEAK_EDGE",EDGE,{"derivedFrom":[makeQuery(id+"F45.opFillet","BLEND_VERTEX",VERTEX,{"blendedFrom":[subQ75,subQ15,subQ74],"blendedInto":[subQ15,subQ74]}),makeQuery(id+"F45.opFillet","BLEND_VERTEX",VERTEX,{"blendedFrom":[subQ75,makeQuery(id+"F42.boolean.opBoolean","MERGE",FACE,{"derivedFrom":[subQ0,subQ8]}),subQ74],"blendedInto":[makeQuery(id+"F42.boolean.opBoolean","MERGE",FACE,{"derivedFrom":[subQ0,subQ8]}),subQ74]})]}),makeQuery(id+"F47.opFillet","BLEND_FACE",FACE,{"disambiguationData":[OSD([subQ5,subQ7]),TDD([makeQuery(id+"F42.boolean.opBoolean","COPY",EDGE,{"disambiguationData":[TD([makeQuery(id+"F5.opLoft","SWEPT_FACE",FACE,{"disambiguationData":[OSD([subQ71,subQ70,sQuery(id+"F3.wireOp",EDGE,"E18.left"),sQuery(id+"F4.wireOp",EDGE,"E21"),subQ69,subQ68])]})])],"derivedFrom":subQ9})])]}),makeQuery(id+"F47.opFillet","BLEND_FACE",FACE,{"disambiguationData":[OSD([subQ5,subQ7]),TDD([makeQuery(id+"F42.boolean.opBoolean","COPY",EDGE,{"disambiguationData":[TD([makeQuery(id+"F6.opLoft","SWEPT_FACE",FACE,{"disambiguationData":[OSD([sQuery(id+"F3.wireOp",EDGE,"E20.15.0"),subQ67,subQ66,sQuery(id+"F4.wireOp",EDGE,"E26.15.0"),subQ65,subQ64])]})])],"derivedFrom":subQ9})])]}),makeQuery(id+"F47.opFillet","BLEND_FACE",FACE,{"disambiguationData":[OSD([subQ5,subQ7]),TDD([makeQuery(id+"F42.boolean.opBoolean","COPY",EDGE,{"disambiguationData":[TD([makeQuery(id+"F7.opLoft","SWEPT_FACE",FACE,{"disambiguationData":[OSD([sQuery(id+"F3.wireOp",EDGE,"E20.14.0"),subQ63,subQ62,sQuery(id+"F4.wireOp",EDGE,"E26.14.0"),subQ61,subQ60])]})])],"derivedFrom":subQ9})])]}),makeQuery(id+"F47.opFillet","BLEND_FACE",FACE,{"disambiguationData":[OSD([subQ5,subQ7]),TDD([makeQuery(id+"F42.boolean.opBoolean","COPY",EDGE,{"disambiguationData":[TD([makeQuery(id+"F8.opLoft","SWEPT_FACE",FACE,{"disambiguationData":[OSD([sQuery(id+"F3.wireOp",EDGE,"E20.13.0"),subQ59,subQ58,sQuery(id+"F4.wireOp",EDGE,"E26.13.0"),subQ57,subQ56])]})])],"derivedFrom":subQ9})])]}),makeQuery(id+"F47.opFillet","BLEND_FACE",FACE,{"disambiguationData":[OSD([subQ5,subQ7]),TDD([makeQuery(id+"F42.boolean.opBoolean","COPY",EDGE,{"disambiguationData":[TD([makeQuery(id+"F9.opLoft","SWEPT_FACE",FACE,{"disambiguationData":[OSD([sQuery(id+"F3.wireOp",EDGE,"E20.12.0"),subQ55,subQ54,sQuery(id+"F4.wireOp",EDGE,"E26.12.0"),subQ53,subQ52])]})])],"derivedFrom":subQ9})])]}),makeQuery(id+"F47.opFillet","BLEND_FACE",FACE,{"disambiguationData":[OSD([subQ5,subQ7]),TDD([makeQuery(id+"F42.boolean.opBoolean","COPY",EDGE,{"disambiguationData":[TD([makeQuery(id+"F10.opLoft","SWEPT_FACE",FACE,{"disambiguationData":[OSD([sQuery(id+"F3.wireOp",EDGE,"E20.11.0"),subQ51,subQ50,sQuery(id+"F4.wireOp",EDGE,"E26.11.0"),subQ49,subQ48])]})])],"derivedFrom":subQ9})])]}),makeQuery(id+"F47.opFillet","BLEND_FACE",FACE,{"disambiguationData":[OSD([subQ5,subQ7]),TDD([makeQuery(id+"F42.boolean.opBoolean","COPY",EDGE,{"disambiguationData":[TD([makeQuery(id+"F11.opLoft","SWEPT_FACE",FACE,{"disambiguationData":[OSD([sQuery(id+"F3.wireOp",EDGE,"E20.10.0"),subQ47,subQ46,sQuery(id+"F4.wireOp",EDGE,"E26.10.0"),subQ45,subQ44])]})])],"derivedFrom":subQ9})])]}),makeQuery(id+"F47.opFillet","BLEND_FACE",FACE,{"disambiguationData":[OSD([subQ5,subQ7]),TDD([makeQuery(id+"F42.boolean.opBoolean","COPY",EDGE,{"disambiguationData":[TD([makeQuery(id+"F12.opLoft","SWEPT_FACE",FACE,{"disambiguationData":[OSD([sQuery(id+"F3.wireOp",EDGE,"E20.9.0"),subQ43,subQ42,sQuery(id+"F4.wireOp",EDGE,"E26.9.0"),subQ41,subQ40])]})])],"derivedFrom":subQ9})])]}),makeQuery(id+"F47.opFillet","BLEND_FACE",FACE,{"disambiguationData":[OSD([subQ5,subQ7]),TDD([makeQuery(id+"F42.boolean.opBoolean","COPY",EDGE,{"disambiguationData":[TD([makeQuery(id+"F13.opLoft","SWEPT_FACE",FACE,{"disambiguationData":[OSD([sQuery(id+"F3.wireOp",EDGE,"E20.8.0"),subQ39,subQ38,sQuery(id+"F4.wireOp",EDGE,"E26.8.0"),subQ37,subQ36])]})])],"derivedFrom":subQ9})])]}),makeQuery(id+"F47.opFillet","BLEND_FACE",FACE,{"disambiguationData":[OSD([subQ5,subQ7]),TDD([makeQuery(id+"F42.boolean.opBoolean","COPY",EDGE,{"disambiguationData":[TD([makeQuery(id+"F14.opLoft","SWEPT_FACE",FACE,{"disambiguationData":[OSD([sQuery(id+"F3.wireOp",EDGE,"E20.7.0"),subQ35,subQ34,sQuery(id+"F4.wireOp",EDGE,"E26.7.0"),subQ33,subQ32])]})])],"derivedFrom":subQ9})])]}),makeQuery(id+"F47.opFillet","BLEND_FACE",FACE,{"disambiguationData":[OSD([subQ5,subQ7]),TDD([makeQuery(id+"F42.boolean.opBoolean","COPY",EDGE,{"disambiguationData":[TD([makeQuery(id+"F15.opLoft","SWEPT_FACE",FACE,{"disambiguationData":[OSD([sQuery(id+"F3.wireOp",EDGE,"E20.6.0"),subQ31,subQ30,sQuery(id+"F4.wireOp",EDGE,"E26.6.0"),subQ29,subQ28])]})])],"derivedFrom":subQ9})])]}),makeQuery(id+"F47.opFillet","BLEND_FACE",FACE,{"disambiguationData":[OSD([subQ5,subQ7]),TDD([makeQuery(id+"F42.boolean.opBoolean","COPY",EDGE,{"disambiguationData":[TD([makeQuery(id+"F16.opLoft","SWEPT_FACE",FACE,{"disambiguationData":[OSD([sQuery(id+"F3.wireOp",EDGE,"E20.5.0"),subQ27,subQ26,sQuery(id+"F4.wireOp",EDGE,"E26.5.0"),subQ25,subQ24])]})])],"derivedFrom":subQ9})])]}),makeQuery(id+"F47.opFillet","BLEND_FACE",FACE,{"disambiguationData":[OSD([subQ5,subQ7]),TDD([makeQuery(id+"F42.boolean.opBoolean","COPY",EDGE,{"disambiguationData":[TD([makeQuery(id+"F17.opLoft","SWEPT_FACE",FACE,{"disambiguationData":[OSD([sQuery(id+"F3.wireOp",EDGE,"E20.4.0"),subQ23,subQ22,sQuery(id+"F4.wireOp",EDGE,"E26.4.0"),subQ21,subQ20])]})])],"derivedFrom":subQ9})])]}),makeQuery(id+"F47.opFillet","BLEND_FACE",FACE,{"disambiguationData":[OSD([subQ5,subQ7]),TDD([makeQuery(id+"F42.boolean.opBoolean","COPY",EDGE,{"disambiguationData":[TD([makeQuery(id+"F18.opLoft","SWEPT_FACE",FACE,{"disambiguationData":[OSD([sQuery(id+"F3.wireOp",EDGE,"E20.3.0"),subQ19,subQ18,sQuery(id+"F4.wireOp",EDGE,"E26.3.0"),subQ17,subQ16])]})])],"derivedFrom":subQ9})])]}),makeQuery(id+"F47.opFillet","BLEND_FACE",FACE,{"disambiguationData":[OSD([subQ5,subQ7]),TDD([makeQuery(id+"F42.boolean.opBoolean","COPY",EDGE,{"disambiguationData":[TD([subQ15])],"derivedFrom":subQ9})])]}),makeQuery(id+"F47.opFillet","BLEND_FACE",FACE,{"disambiguationData":[OSD([subQ5,subQ7]),TDD([makeQuery(id+"F42.boolean.opBoolean","COPY",EDGE,{"disambiguationData":[TD([makeQuery(id+"F20.opLoft","SWEPT_FACE",FACE,{"disambiguationData":[OSD([sQuery(id+"F3.wireOp",EDGE,"E20.1.0"),subQ4,subQ3,sQuery(id+"F4.wireOp",EDGE,"E26.1.0"),subQ2,subQ1])]})])],"derivedFrom":subQ9})])]})],"blendedInto":[makeQuery(id+"F47.opFillet","BLEND_FACE",FACE,{"disambiguationData":[OSD([subQ5,subQ7]),TDD([makeQuery(id+"F42.boolean.opBoolean","COPY",EDGE,{"disambiguationData":[TD([makeQuery(id+"F5.opLoft","SWEPT_FACE",FACE,{"disambiguationData":[OSD([subQ71,subQ70,sQuery(id+"F3.wireOp",EDGE,"E18.left"),sQuery(id+"F4.wireOp",EDGE,"E21"),subQ69,subQ68])]})])],"derivedFrom":subQ9})])]}),makeQuery(id+"F47.opFillet","BLEND_FACE",FACE,{"disambiguationData":[OSD([subQ5,subQ7]),TDD([makeQuery(id+"F42.boolean.opBoolean","COPY",EDGE,{"disambiguationData":[TD([makeQuery(id+"F6.opLoft","SWEPT_FACE",FACE,{"disambiguationData":[OSD([sQuery(id+"F3.wireOp",EDGE,"E20.15.0"),subQ67,subQ66,sQuery(id+"F4.wireOp",EDGE,"E26.15.0"),subQ65,subQ64])]})])],"derivedFrom":subQ9})])]}),makeQuery(id+"F47.opFillet","BLEND_FACE",FACE,{"disambiguationData":[OSD([subQ5,subQ7]),TDD([makeQuery(id+"F42.boolean.opBoolean","COPY",EDGE,{"disambiguationData":[TD([makeQuery(id+"F7.opLoft","SWEPT_FACE",FACE,{"disambiguationData":[OSD([sQuery(id+"F3.wireOp",EDGE,"E20.14.0"),subQ63,subQ62,sQuery(id+"F4.wireOp",EDGE,"E26.14.0"),subQ61,subQ60])]})])],"derivedFrom":subQ9})])]}),makeQuery(id+"F47.opFillet","BLEND_FACE",FACE,{"disambiguationData":[OSD([subQ5,subQ7]),TDD([makeQuery(id+"F42.boolean.opBoolean","COPY",EDGE,{"disambiguationData":[TD([makeQuery(id+"F8.opLoft","SWEPT_FACE",FACE,{"disambiguationData":[OSD([sQuery(id+"F3.wireOp",EDGE,"E20.13.0"),subQ59,subQ58,sQuery(id+"F4.wireOp",EDGE,"E26.13.0"),subQ57,subQ56])]})])],"derivedFrom":subQ9})])]}),makeQuery(id+"F47.opFillet","BLEND_FACE",FACE,{"disambiguationData":[OSD([subQ5,subQ7]),TDD([makeQuery(id+"F42.boolean.opBoolean","COPY",EDGE,{"disambiguationData":[TD([makeQuery(id+"F9.opLoft","SWEPT_FACE",FACE,{"disambiguationData":[OSD([sQuery(id+"F3.wireOp",EDGE,"E20.12.0"),subQ55,subQ54,sQuery(id+"F4.wireOp",EDGE,"E26.12.0"),subQ53,subQ52])]})])],"derivedFrom":subQ9})])]}),makeQuery(id+"F47.opFillet","BLEND_FACE",FACE,{"disambiguationData":[OSD([subQ5,subQ7]),TDD([makeQuery(id+"F42.boolean.opBoolean","COPY",EDGE,{"disambiguationData":[TD([makeQuery(id+"F10.opLoft","SWEPT_FACE",FACE,{"disambiguationData":[OSD([sQuery(id+"F3.wireOp",EDGE,"E20.11.0"),subQ51,subQ50,sQuery(id+"F4.wireOp",EDGE,"E26.11.0"),subQ49,subQ48])]})])],"derivedFrom":subQ9})])]}),makeQuery(id+"F47.opFillet","BLEND_FACE",FACE,{"disambiguationData":[OSD([subQ5,subQ7]),TDD([makeQuery(id+"F42.boolean.opBoolean","COPY",EDGE,{"disambiguationData":[TD([makeQuery(id+"F11.opLoft","SWEPT_FACE",FACE,{"disambiguationData":[OSD([sQuery(id+"F3.wireOp",EDGE,"E20.10.0"),subQ47,subQ46,sQuery(id+"F4.wireOp",EDGE,"E26.10.0"),subQ45,subQ44])]})])],"derivedFrom":subQ9})])]}),makeQuery(id+"F47.opFillet","BLEND_FACE",FACE,{"disambiguationData":[OSD([subQ5,subQ7]),TDD([makeQuery(id+"F42.boolean.opBoolean","COPY",EDGE,{"disambiguationData":[TD([makeQuery(id+"F12.opLoft","SWEPT_FACE",FACE,{"disambiguationData":[OSD([sQuery(id+"F3.wireOp",EDGE,"E20.9.0"),subQ43,subQ42,sQuery(id+"F4.wireOp",EDGE,"E26.9.0"),subQ41,subQ40])]})])],"derivedFrom":subQ9})])]}),makeQuery(id+"F47.opFillet","BLEND_FACE",FACE,{"disambiguationData":[OSD([subQ5,subQ7]),TDD([makeQuery(id+"F42.boolean.opBoolean","COPY",EDGE,{"disambiguationData":[TD([makeQuery(id+"F13.opLoft","SWEPT_FACE",FACE,{"disambiguationData":[OSD([sQuery(id+"F3.wireOp",EDGE,"E20.8.0"),subQ39,subQ38,sQuery(id+"F4.wireOp",EDGE,"E26.8.0"),subQ37,subQ36])]})])],"derivedFrom":subQ9})])]}),makeQuery(id+"F47.opFillet","BLEND_FACE",FACE,{"disambiguationData":[OSD([subQ5,subQ7]),TDD([makeQuery(id+"F42.boolean.opBoolean","COPY",EDGE,{"disambiguationData":[TD([makeQuery(id+"F14.opLoft","SWEPT_FACE",FACE,{"disambiguationData":[OSD([sQuery(id+"F3.wireOp",EDGE,"E20.7.0"),subQ35,subQ34,sQuery(id+"F4.wireOp",EDGE,"E26.7.0"),subQ33,subQ32])]})])],"derivedFrom":subQ9})])]}),makeQuery(id+"F47.opFillet","BLEND_FACE",FACE,{"disambiguationData":[OSD([subQ5,subQ7]),TDD([makeQuery(id+"F42.boolean.opBoolean","COPY",EDGE,{"disambiguationData":[TD([makeQuery(id+"F15.opLoft","SWEPT_FACE",FACE,{"disambiguationData":[OSD([sQuery(id+"F3.wireOp",EDGE,"E20.6.0"),subQ31,subQ30,sQuery(id+"F4.wireOp",EDGE,"E26.6.0"),subQ29,subQ28])]})])],"derivedFrom":subQ9})])]}),makeQuery(id+"F47.opFillet","BLEND_FACE",FACE,{"disambiguationData":[OSD([subQ5,subQ7]),TDD([makeQuery(id+"F42.boolean.opBoolean","COPY",EDGE,{"disambiguationData":[TD([makeQuery(id+"F16.opLoft","SWEPT_FACE",FACE,{"disambiguationData":[OSD([sQuery(id+"F3.wireOp",EDGE,"E20.5.0"),subQ27,subQ26,sQuery(id+"F4.wireOp",EDGE,"E26.5.0"),subQ25,subQ24])]})])],"derivedFrom":subQ9})])]}),makeQuery(id+"F47.opFillet","BLEND_FACE",FACE,{"disambiguationData":[OSD([subQ5,subQ7]),TDD([makeQuery(id+"F42.boolean.opBoolean","COPY",EDGE,{"disambiguationData":[TD([makeQuery(id+"F17.opLoft","SWEPT_FACE",FACE,{"disambiguationData":[OSD([sQuery(id+"F3.wireOp",EDGE,"E20.4.0"),subQ23,subQ22,sQuery(id+"F4.wireOp",EDGE,"E26.4.0"),subQ21,subQ20])]})])],"derivedFrom":subQ9})])]}),makeQuery(id+"F47.opFillet","BLEND_FACE",FACE,{"disambiguationData":[OSD([subQ5,subQ7]),TDD([makeQuery(id+"F42.boolean.opBoolean","COPY",EDGE,{"disambiguationData":[TD([makeQuery(id+"F18.opLoft","SWEPT_FACE",FACE,{"disambiguationData":[OSD([sQuery(id+"F3.wireOp",EDGE,"E20.3.0"),subQ19,subQ18,sQuery(id+"F4.wireOp",EDGE,"E26.3.0"),subQ17,subQ16])]})])],"derivedFrom":subQ9})])]}),makeQuery(id+"F47.opFillet","BLEND_FACE",FACE,{"disambiguationData":[OSD([subQ5,subQ7]),TDD([makeQuery(id+"F42.boolean.opBoolean","COPY",EDGE,{"disambiguationData":[TD([subQ15])],"derivedFrom":subQ9})])]}),makeQuery(id+"F47.opFillet","BLEND_FACE",FACE,{"disambiguationData":[OSD([subQ5,subQ7]),TDD([makeQuery(id+"F42.boolean.opBoolean","COPY",EDGE,{"disambiguationData":[TD([makeQuery(id+"F20.opLoft","SWEPT_FACE",FACE,{"disambiguationData":[OSD([sQuery(id+"F3.wireOp",EDGE,"E20.1.0"),subQ4,subQ3,sQuery(id+"F4.wireOp",EDGE,"E26.1.0"),subQ2,subQ1])]})])],"derivedFrom":subQ9})])]})]});}
            var Q53;
            {var subQ0=makeQuery(id+"F40.opExtrude","CAP_FACE",FACE,{"disambiguationData":[OSD([sQuery(id+"F39.wireOp",EDGE,"E29"),sQuery(id+"F39.wireOp",EDGE,"E30")])],"isStart":false});var subQ1=sQuery(id+"F4.wireOp",EDGE,"E26.1.3");var subQ2=sQuery(id+"F4.wireOp",EDGE,"E26.1.2");var subQ3=sQuery(id+"F3.wireOp",EDGE,"E20.1.3");var subQ4=sQuery(id+"F3.wireOp",EDGE,"E20.1.1");var subQ6=sQuery(id+"F41.wireOp",EDGE,"E35");var subQ7=makeQuery(id+"F42.opRevolve","SWEPT_FACE",FACE,{"disambiguationData":[OSD([subQ6])]});var subQ8=makeQuery(id+"F20.opLoft","SWEPT_FACE",FACE,{"disambiguationData":[OSD([sQuery(id+"F3.wireOp",EDGE,"E20.1.0"),subQ4,subQ3,sQuery(id+"F4.wireOp",EDGE,"E26.1.0"),subQ2,subQ1])]});var subQ9=sQuery(id+"F41.wireOp",EDGE,"E36");var subQ10=makeQuery(id+"F42.opRevolve","SWEPT_FACE",FACE,{"disambiguationData":[OSD([subQ9])]});var subQ11=makeQuery(id+"F42.opRevolve","SWEPT_EDGE",EDGE,{"disambiguationData":[OSD([subQ6,subQ9])]});var subQ12=sQuery(id+"F4.wireOp",EDGE,"E26.2.3");var subQ13=sQuery(id+"F4.wireOp",EDGE,"E26.2.2");var subQ14=sQuery(id+"F3.wireOp",EDGE,"E20.2.3");var subQ15=sQuery(id+"F3.wireOp",EDGE,"E20.2.1");var subQ16=sQuery(id+"F4.wireOp",EDGE,"E26.3.3");var subQ17=sQuery(id+"F4.wireOp",EDGE,"E26.3.2");var subQ18=sQuery(id+"F3.wireOp",EDGE,"E20.3.3");var subQ19=sQuery(id+"F3.wireOp",EDGE,"E20.3.1");var subQ20=sQuery(id+"F4.wireOp",EDGE,"E26.4.3");var subQ21=sQuery(id+"F4.wireOp",EDGE,"E26.4.2");var subQ22=sQuery(id+"F3.wireOp",EDGE,"E20.4.3");var subQ23=sQuery(id+"F3.wireOp",EDGE,"E20.4.1");var subQ24=sQuery(id+"F4.wireOp",EDGE,"E26.5.3");var subQ25=sQuery(id+"F4.wireOp",EDGE,"E26.5.2");var subQ26=sQuery(id+"F3.wireOp",EDGE,"E20.5.3");var subQ27=sQuery(id+"F3.wireOp",EDGE,"E20.5.1");var subQ28=sQuery(id+"F4.wireOp",EDGE,"E26.6.3");var subQ29=sQuery(id+"F4.wireOp",EDGE,"E26.6.2");var subQ30=sQuery(id+"F3.wireOp",EDGE,"E20.6.3");var subQ31=sQuery(id+"F3.wireOp",EDGE,"E20.6.1");var subQ32=sQuery(id+"F4.wireOp",EDGE,"E26.7.3");var subQ33=sQuery(id+"F4.wireOp",EDGE,"E26.7.2");var subQ34=sQuery(id+"F3.wireOp",EDGE,"E20.7.3");var subQ35=sQuery(id+"F3.wireOp",EDGE,"E20.7.1");var subQ36=sQuery(id+"F4.wireOp",EDGE,"E26.8.3");var subQ37=sQuery(id+"F4.wireOp",EDGE,"E26.8.2");var subQ38=sQuery(id+"F3.wireOp",EDGE,"E20.8.3");var subQ39=sQuery(id+"F3.wireOp",EDGE,"E20.8.1");var subQ40=sQuery(id+"F4.wireOp",EDGE,"E26.9.3");var subQ41=sQuery(id+"F4.wireOp",EDGE,"E26.9.2");var subQ42=sQuery(id+"F3.wireOp",EDGE,"E20.9.3");var subQ43=sQuery(id+"F3.wireOp",EDGE,"E20.9.1");var subQ44=sQuery(id+"F4.wireOp",EDGE,"E26.10.3");var subQ45=sQuery(id+"F4.wireOp",EDGE,"E26.10.2");var subQ46=sQuery(id+"F3.wireOp",EDGE,"E20.10.3");var subQ47=sQuery(id+"F3.wireOp",EDGE,"E20.10.1");var subQ48=sQuery(id+"F4.wireOp",EDGE,"E26.11.3");var subQ49=sQuery(id+"F4.wireOp",EDGE,"E26.11.2");var subQ50=sQuery(id+"F3.wireOp",EDGE,"E20.11.3");var subQ51=sQuery(id+"F3.wireOp",EDGE,"E20.11.1");var subQ52=sQuery(id+"F4.wireOp",EDGE,"E26.12.3");var subQ53=sQuery(id+"F4.wireOp",EDGE,"E26.12.2");var subQ54=sQuery(id+"F3.wireOp",EDGE,"E20.12.3");var subQ55=sQuery(id+"F3.wireOp",EDGE,"E20.12.1");var subQ56=sQuery(id+"F4.wireOp",EDGE,"E26.13.3");var subQ57=sQuery(id+"F4.wireOp",EDGE,"E26.13.2");var subQ58=sQuery(id+"F3.wireOp",EDGE,"E20.13.3");var subQ59=sQuery(id+"F3.wireOp",EDGE,"E20.13.1");var subQ60=sQuery(id+"F4.wireOp",EDGE,"E26.14.3");var subQ61=sQuery(id+"F4.wireOp",EDGE,"E26.14.2");var subQ62=sQuery(id+"F3.wireOp",EDGE,"E20.14.3");var subQ63=sQuery(id+"F3.wireOp",EDGE,"E20.14.1");var subQ64=sQuery(id+"F4.wireOp",EDGE,"E26.15.3");var subQ65=sQuery(id+"F4.wireOp",EDGE,"E26.15.2");var subQ66=sQuery(id+"F3.wireOp",EDGE,"E20.15.3");var subQ67=sQuery(id+"F3.wireOp",EDGE,"E20.15.1");var subQ68=sQuery(id+"F4.wireOp",EDGE,"E23");var subQ69=sQuery(id+"F4.wireOp",EDGE,"E22");var subQ70=sQuery(id+"F3.wireOp",EDGE,"E18.top");var subQ71=sQuery(id+"F3.wireOp",EDGE,"E18.bottom");var subQ74=makeQuery(id+"F42.boolean.opBoolean","COPY",FACE,{"disambiguationData":[TD([subQ8])],"derivedFrom":subQ7});var subQ75=makeQuery(id+"F20.boolean.opBoolean","INTERSECT",EDGE,{"derivedFrom":[makeQuery(id+"F1.opRevolve","SWEPT_FACE",FACE,{"disambiguationData":[OSD([sQuery(id+"F0.wireOp",EDGE,"E13")])]}),subQ8]});Q53=makeQuery(id+"F48.opFillet","BLEND_EDGE",EDGE,{"blendedFrom":[makeQuery(id+"F47.opFillet","TWEAK_EDGE",EDGE,{"derivedFrom":[makeQuery(id+"F45.opFillet","BLEND_VERTEX",VERTEX,{"blendedFrom":[subQ75,subQ8,subQ74],"blendedInto":[subQ8,subQ74]}),makeQuery(id+"F45.opFillet","BLEND_VERTEX",VERTEX,{"blendedFrom":[subQ75,makeQuery(id+"F42.boolean.opBoolean","MERGE",FACE,{"derivedFrom":[subQ0,subQ10]}),subQ74],"blendedInto":[makeQuery(id+"F42.boolean.opBoolean","MERGE",FACE,{"derivedFrom":[subQ0,subQ10]}),subQ74]})]}),makeQuery(id+"F47.opFillet","BLEND_FACE",FACE,{"disambiguationData":[OSD([subQ6,subQ9]),TDD([makeQuery(id+"F42.boolean.opBoolean","COPY",EDGE,{"disambiguationData":[TD([makeQuery(id+"F5.opLoft","SWEPT_FACE",FACE,{"disambiguationData":[OSD([subQ71,subQ70,sQuery(id+"F3.wireOp",EDGE,"E18.left"),sQuery(id+"F4.wireOp",EDGE,"E21"),subQ69,subQ68])]})])],"derivedFrom":subQ11})])]}),makeQuery(id+"F47.opFillet","BLEND_FACE",FACE,{"disambiguationData":[OSD([subQ6,subQ9]),TDD([makeQuery(id+"F42.boolean.opBoolean","COPY",EDGE,{"disambiguationData":[TD([makeQuery(id+"F6.opLoft","SWEPT_FACE",FACE,{"disambiguationData":[OSD([sQuery(id+"F3.wireOp",EDGE,"E20.15.0"),subQ67,subQ66,sQuery(id+"F4.wireOp",EDGE,"E26.15.0"),subQ65,subQ64])]})])],"derivedFrom":subQ11})])]}),makeQuery(id+"F47.opFillet","BLEND_FACE",FACE,{"disambiguationData":[OSD([subQ6,subQ9]),TDD([makeQuery(id+"F42.boolean.opBoolean","COPY",EDGE,{"disambiguationData":[TD([makeQuery(id+"F7.opLoft","SWEPT_FACE",FACE,{"disambiguationData":[OSD([sQuery(id+"F3.wireOp",EDGE,"E20.14.0"),subQ63,subQ62,sQuery(id+"F4.wireOp",EDGE,"E26.14.0"),subQ61,subQ60])]})])],"derivedFrom":subQ11})])]}),makeQuery(id+"F47.opFillet","BLEND_FACE",FACE,{"disambiguationData":[OSD([subQ6,subQ9]),TDD([makeQuery(id+"F42.boolean.opBoolean","COPY",EDGE,{"disambiguationData":[TD([makeQuery(id+"F8.opLoft","SWEPT_FACE",FACE,{"disambiguationData":[OSD([sQuery(id+"F3.wireOp",EDGE,"E20.13.0"),subQ59,subQ58,sQuery(id+"F4.wireOp",EDGE,"E26.13.0"),subQ57,subQ56])]})])],"derivedFrom":subQ11})])]}),makeQuery(id+"F47.opFillet","BLEND_FACE",FACE,{"disambiguationData":[OSD([subQ6,subQ9]),TDD([makeQuery(id+"F42.boolean.opBoolean","COPY",EDGE,{"disambiguationData":[TD([makeQuery(id+"F9.opLoft","SWEPT_FACE",FACE,{"disambiguationData":[OSD([sQuery(id+"F3.wireOp",EDGE,"E20.12.0"),subQ55,subQ54,sQuery(id+"F4.wireOp",EDGE,"E26.12.0"),subQ53,subQ52])]})])],"derivedFrom":subQ11})])]}),makeQuery(id+"F47.opFillet","BLEND_FACE",FACE,{"disambiguationData":[OSD([subQ6,subQ9]),TDD([makeQuery(id+"F42.boolean.opBoolean","COPY",EDGE,{"disambiguationData":[TD([makeQuery(id+"F10.opLoft","SWEPT_FACE",FACE,{"disambiguationData":[OSD([sQuery(id+"F3.wireOp",EDGE,"E20.11.0"),subQ51,subQ50,sQuery(id+"F4.wireOp",EDGE,"E26.11.0"),subQ49,subQ48])]})])],"derivedFrom":subQ11})])]}),makeQuery(id+"F47.opFillet","BLEND_FACE",FACE,{"disambiguationData":[OSD([subQ6,subQ9]),TDD([makeQuery(id+"F42.boolean.opBoolean","COPY",EDGE,{"disambiguationData":[TD([makeQuery(id+"F11.opLoft","SWEPT_FACE",FACE,{"disambiguationData":[OSD([sQuery(id+"F3.wireOp",EDGE,"E20.10.0"),subQ47,subQ46,sQuery(id+"F4.wireOp",EDGE,"E26.10.0"),subQ45,subQ44])]})])],"derivedFrom":subQ11})])]}),makeQuery(id+"F47.opFillet","BLEND_FACE",FACE,{"disambiguationData":[OSD([subQ6,subQ9]),TDD([makeQuery(id+"F42.boolean.opBoolean","COPY",EDGE,{"disambiguationData":[TD([makeQuery(id+"F12.opLoft","SWEPT_FACE",FACE,{"disambiguationData":[OSD([sQuery(id+"F3.wireOp",EDGE,"E20.9.0"),subQ43,subQ42,sQuery(id+"F4.wireOp",EDGE,"E26.9.0"),subQ41,subQ40])]})])],"derivedFrom":subQ11})])]}),makeQuery(id+"F47.opFillet","BLEND_FACE",FACE,{"disambiguationData":[OSD([subQ6,subQ9]),TDD([makeQuery(id+"F42.boolean.opBoolean","COPY",EDGE,{"disambiguationData":[TD([makeQuery(id+"F13.opLoft","SWEPT_FACE",FACE,{"disambiguationData":[OSD([sQuery(id+"F3.wireOp",EDGE,"E20.8.0"),subQ39,subQ38,sQuery(id+"F4.wireOp",EDGE,"E26.8.0"),subQ37,subQ36])]})])],"derivedFrom":subQ11})])]}),makeQuery(id+"F47.opFillet","BLEND_FACE",FACE,{"disambiguationData":[OSD([subQ6,subQ9]),TDD([makeQuery(id+"F42.boolean.opBoolean","COPY",EDGE,{"disambiguationData":[TD([makeQuery(id+"F14.opLoft","SWEPT_FACE",FACE,{"disambiguationData":[OSD([sQuery(id+"F3.wireOp",EDGE,"E20.7.0"),subQ35,subQ34,sQuery(id+"F4.wireOp",EDGE,"E26.7.0"),subQ33,subQ32])]})])],"derivedFrom":subQ11})])]}),makeQuery(id+"F47.opFillet","BLEND_FACE",FACE,{"disambiguationData":[OSD([subQ6,subQ9]),TDD([makeQuery(id+"F42.boolean.opBoolean","COPY",EDGE,{"disambiguationData":[TD([makeQuery(id+"F15.opLoft","SWEPT_FACE",FACE,{"disambiguationData":[OSD([sQuery(id+"F3.wireOp",EDGE,"E20.6.0"),subQ31,subQ30,sQuery(id+"F4.wireOp",EDGE,"E26.6.0"),subQ29,subQ28])]})])],"derivedFrom":subQ11})])]}),makeQuery(id+"F47.opFillet","BLEND_FACE",FACE,{"disambiguationData":[OSD([subQ6,subQ9]),TDD([makeQuery(id+"F42.boolean.opBoolean","COPY",EDGE,{"disambiguationData":[TD([makeQuery(id+"F16.opLoft","SWEPT_FACE",FACE,{"disambiguationData":[OSD([sQuery(id+"F3.wireOp",EDGE,"E20.5.0"),subQ27,subQ26,sQuery(id+"F4.wireOp",EDGE,"E26.5.0"),subQ25,subQ24])]})])],"derivedFrom":subQ11})])]}),makeQuery(id+"F47.opFillet","BLEND_FACE",FACE,{"disambiguationData":[OSD([subQ6,subQ9]),TDD([makeQuery(id+"F42.boolean.opBoolean","COPY",EDGE,{"disambiguationData":[TD([makeQuery(id+"F17.opLoft","SWEPT_FACE",FACE,{"disambiguationData":[OSD([sQuery(id+"F3.wireOp",EDGE,"E20.4.0"),subQ23,subQ22,sQuery(id+"F4.wireOp",EDGE,"E26.4.0"),subQ21,subQ20])]})])],"derivedFrom":subQ11})])]}),makeQuery(id+"F47.opFillet","BLEND_FACE",FACE,{"disambiguationData":[OSD([subQ6,subQ9]),TDD([makeQuery(id+"F42.boolean.opBoolean","COPY",EDGE,{"disambiguationData":[TD([makeQuery(id+"F18.opLoft","SWEPT_FACE",FACE,{"disambiguationData":[OSD([sQuery(id+"F3.wireOp",EDGE,"E20.3.0"),subQ19,subQ18,sQuery(id+"F4.wireOp",EDGE,"E26.3.0"),subQ17,subQ16])]})])],"derivedFrom":subQ11})])]}),makeQuery(id+"F47.opFillet","BLEND_FACE",FACE,{"disambiguationData":[OSD([subQ6,subQ9]),TDD([makeQuery(id+"F42.boolean.opBoolean","COPY",EDGE,{"disambiguationData":[TD([makeQuery(id+"F19.opLoft","SWEPT_FACE",FACE,{"disambiguationData":[OSD([sQuery(id+"F3.wireOp",EDGE,"E20.2.0"),subQ15,subQ14,sQuery(id+"F4.wireOp",EDGE,"E26.2.0"),subQ13,subQ12])]})])],"derivedFrom":subQ11})])]}),makeQuery(id+"F47.opFillet","BLEND_FACE",FACE,{"disambiguationData":[OSD([subQ6,subQ9]),TDD([makeQuery(id+"F42.boolean.opBoolean","COPY",EDGE,{"disambiguationData":[TD([subQ8])],"derivedFrom":subQ11})])]})],"blendedInto":[makeQuery(id+"F47.opFillet","BLEND_FACE",FACE,{"disambiguationData":[OSD([subQ6,subQ9]),TDD([makeQuery(id+"F42.boolean.opBoolean","COPY",EDGE,{"disambiguationData":[TD([makeQuery(id+"F5.opLoft","SWEPT_FACE",FACE,{"disambiguationData":[OSD([subQ71,subQ70,sQuery(id+"F3.wireOp",EDGE,"E18.left"),sQuery(id+"F4.wireOp",EDGE,"E21"),subQ69,subQ68])]})])],"derivedFrom":subQ11})])]}),makeQuery(id+"F47.opFillet","BLEND_FACE",FACE,{"disambiguationData":[OSD([subQ6,subQ9]),TDD([makeQuery(id+"F42.boolean.opBoolean","COPY",EDGE,{"disambiguationData":[TD([makeQuery(id+"F6.opLoft","SWEPT_FACE",FACE,{"disambiguationData":[OSD([sQuery(id+"F3.wireOp",EDGE,"E20.15.0"),subQ67,subQ66,sQuery(id+"F4.wireOp",EDGE,"E26.15.0"),subQ65,subQ64])]})])],"derivedFrom":subQ11})])]}),makeQuery(id+"F47.opFillet","BLEND_FACE",FACE,{"disambiguationData":[OSD([subQ6,subQ9]),TDD([makeQuery(id+"F42.boolean.opBoolean","COPY",EDGE,{"disambiguationData":[TD([makeQuery(id+"F7.opLoft","SWEPT_FACE",FACE,{"disambiguationData":[OSD([sQuery(id+"F3.wireOp",EDGE,"E20.14.0"),subQ63,subQ62,sQuery(id+"F4.wireOp",EDGE,"E26.14.0"),subQ61,subQ60])]})])],"derivedFrom":subQ11})])]}),makeQuery(id+"F47.opFillet","BLEND_FACE",FACE,{"disambiguationData":[OSD([subQ6,subQ9]),TDD([makeQuery(id+"F42.boolean.opBoolean","COPY",EDGE,{"disambiguationData":[TD([makeQuery(id+"F8.opLoft","SWEPT_FACE",FACE,{"disambiguationData":[OSD([sQuery(id+"F3.wireOp",EDGE,"E20.13.0"),subQ59,subQ58,sQuery(id+"F4.wireOp",EDGE,"E26.13.0"),subQ57,subQ56])]})])],"derivedFrom":subQ11})])]}),makeQuery(id+"F47.opFillet","BLEND_FACE",FACE,{"disambiguationData":[OSD([subQ6,subQ9]),TDD([makeQuery(id+"F42.boolean.opBoolean","COPY",EDGE,{"disambiguationData":[TD([makeQuery(id+"F9.opLoft","SWEPT_FACE",FACE,{"disambiguationData":[OSD([sQuery(id+"F3.wireOp",EDGE,"E20.12.0"),subQ55,subQ54,sQuery(id+"F4.wireOp",EDGE,"E26.12.0"),subQ53,subQ52])]})])],"derivedFrom":subQ11})])]}),makeQuery(id+"F47.opFillet","BLEND_FACE",FACE,{"disambiguationData":[OSD([subQ6,subQ9]),TDD([makeQuery(id+"F42.boolean.opBoolean","COPY",EDGE,{"disambiguationData":[TD([makeQuery(id+"F10.opLoft","SWEPT_FACE",FACE,{"disambiguationData":[OSD([sQuery(id+"F3.wireOp",EDGE,"E20.11.0"),subQ51,subQ50,sQuery(id+"F4.wireOp",EDGE,"E26.11.0"),subQ49,subQ48])]})])],"derivedFrom":subQ11})])]}),makeQuery(id+"F47.opFillet","BLEND_FACE",FACE,{"disambiguationData":[OSD([subQ6,subQ9]),TDD([makeQuery(id+"F42.boolean.opBoolean","COPY",EDGE,{"disambiguationData":[TD([makeQuery(id+"F11.opLoft","SWEPT_FACE",FACE,{"disambiguationData":[OSD([sQuery(id+"F3.wireOp",EDGE,"E20.10.0"),subQ47,subQ46,sQuery(id+"F4.wireOp",EDGE,"E26.10.0"),subQ45,subQ44])]})])],"derivedFrom":subQ11})])]}),makeQuery(id+"F47.opFillet","BLEND_FACE",FACE,{"disambiguationData":[OSD([subQ6,subQ9]),TDD([makeQuery(id+"F42.boolean.opBoolean","COPY",EDGE,{"disambiguationData":[TD([makeQuery(id+"F12.opLoft","SWEPT_FACE",FACE,{"disambiguationData":[OSD([sQuery(id+"F3.wireOp",EDGE,"E20.9.0"),subQ43,subQ42,sQuery(id+"F4.wireOp",EDGE,"E26.9.0"),subQ41,subQ40])]})])],"derivedFrom":subQ11})])]}),makeQuery(id+"F47.opFillet","BLEND_FACE",FACE,{"disambiguationData":[OSD([subQ6,subQ9]),TDD([makeQuery(id+"F42.boolean.opBoolean","COPY",EDGE,{"disambiguationData":[TD([makeQuery(id+"F13.opLoft","SWEPT_FACE",FACE,{"disambiguationData":[OSD([sQuery(id+"F3.wireOp",EDGE,"E20.8.0"),subQ39,subQ38,sQuery(id+"F4.wireOp",EDGE,"E26.8.0"),subQ37,subQ36])]})])],"derivedFrom":subQ11})])]}),makeQuery(id+"F47.opFillet","BLEND_FACE",FACE,{"disambiguationData":[OSD([subQ6,subQ9]),TDD([makeQuery(id+"F42.boolean.opBoolean","COPY",EDGE,{"disambiguationData":[TD([makeQuery(id+"F14.opLoft","SWEPT_FACE",FACE,{"disambiguationData":[OSD([sQuery(id+"F3.wireOp",EDGE,"E20.7.0"),subQ35,subQ34,sQuery(id+"F4.wireOp",EDGE,"E26.7.0"),subQ33,subQ32])]})])],"derivedFrom":subQ11})])]}),makeQuery(id+"F47.opFillet","BLEND_FACE",FACE,{"disambiguationData":[OSD([subQ6,subQ9]),TDD([makeQuery(id+"F42.boolean.opBoolean","COPY",EDGE,{"disambiguationData":[TD([makeQuery(id+"F15.opLoft","SWEPT_FACE",FACE,{"disambiguationData":[OSD([sQuery(id+"F3.wireOp",EDGE,"E20.6.0"),subQ31,subQ30,sQuery(id+"F4.wireOp",EDGE,"E26.6.0"),subQ29,subQ28])]})])],"derivedFrom":subQ11})])]}),makeQuery(id+"F47.opFillet","BLEND_FACE",FACE,{"disambiguationData":[OSD([subQ6,subQ9]),TDD([makeQuery(id+"F42.boolean.opBoolean","COPY",EDGE,{"disambiguationData":[TD([makeQuery(id+"F16.opLoft","SWEPT_FACE",FACE,{"disambiguationData":[OSD([sQuery(id+"F3.wireOp",EDGE,"E20.5.0"),subQ27,subQ26,sQuery(id+"F4.wireOp",EDGE,"E26.5.0"),subQ25,subQ24])]})])],"derivedFrom":subQ11})])]}),makeQuery(id+"F47.opFillet","BLEND_FACE",FACE,{"disambiguationData":[OSD([subQ6,subQ9]),TDD([makeQuery(id+"F42.boolean.opBoolean","COPY",EDGE,{"disambiguationData":[TD([makeQuery(id+"F17.opLoft","SWEPT_FACE",FACE,{"disambiguationData":[OSD([sQuery(id+"F3.wireOp",EDGE,"E20.4.0"),subQ23,subQ22,sQuery(id+"F4.wireOp",EDGE,"E26.4.0"),subQ21,subQ20])]})])],"derivedFrom":subQ11})])]}),makeQuery(id+"F47.opFillet","BLEND_FACE",FACE,{"disambiguationData":[OSD([subQ6,subQ9]),TDD([makeQuery(id+"F42.boolean.opBoolean","COPY",EDGE,{"disambiguationData":[TD([makeQuery(id+"F18.opLoft","SWEPT_FACE",FACE,{"disambiguationData":[OSD([sQuery(id+"F3.wireOp",EDGE,"E20.3.0"),subQ19,subQ18,sQuery(id+"F4.wireOp",EDGE,"E26.3.0"),subQ17,subQ16])]})])],"derivedFrom":subQ11})])]}),makeQuery(id+"F47.opFillet","BLEND_FACE",FACE,{"disambiguationData":[OSD([subQ6,subQ9]),TDD([makeQuery(id+"F42.boolean.opBoolean","COPY",EDGE,{"disambiguationData":[TD([makeQuery(id+"F19.opLoft","SWEPT_FACE",FACE,{"disambiguationData":[OSD([sQuery(id+"F3.wireOp",EDGE,"E20.2.0"),subQ15,subQ14,sQuery(id+"F4.wireOp",EDGE,"E26.2.0"),subQ13,subQ12])]})])],"derivedFrom":subQ11})])]}),makeQuery(id+"F47.opFillet","BLEND_FACE",FACE,{"disambiguationData":[OSD([subQ6,subQ9]),TDD([makeQuery(id+"F42.boolean.opBoolean","COPY",EDGE,{"disambiguationData":[TD([subQ8])],"derivedFrom":subQ11})])]})]});}
            var Q54;
            {var subQ0=makeQuery(id+"F40.opExtrude","CAP_FACE",FACE,{"disambiguationData":[OSD([sQuery(id+"F39.wireOp",EDGE,"E29"),sQuery(id+"F39.wireOp",EDGE,"E30")])],"isStart":false});var subQ1=sQuery(id+"F4.wireOp",EDGE,"E26.1.3");var subQ2=sQuery(id+"F4.wireOp",EDGE,"E26.1.2");var subQ3=sQuery(id+"F3.wireOp",EDGE,"E20.1.3");var subQ4=sQuery(id+"F3.wireOp",EDGE,"E20.1.1");var subQ5=sQuery(id+"F41.wireOp",EDGE,"E35");var subQ6=makeQuery(id+"F42.opRevolve","SWEPT_FACE",FACE,{"disambiguationData":[OSD([subQ5])]});var subQ7=sQuery(id+"F41.wireOp",EDGE,"E36");var subQ8=makeQuery(id+"F42.opRevolve","SWEPT_FACE",FACE,{"disambiguationData":[OSD([subQ7])]});var subQ9=makeQuery(id+"F42.opRevolve","SWEPT_EDGE",EDGE,{"disambiguationData":[OSD([subQ5,subQ7])]});var subQ10=sQuery(id+"F4.wireOp",EDGE,"E26.2.3");var subQ11=sQuery(id+"F4.wireOp",EDGE,"E26.2.2");var subQ12=sQuery(id+"F3.wireOp",EDGE,"E20.2.3");var subQ13=sQuery(id+"F3.wireOp",EDGE,"E20.2.1");var subQ14=sQuery(id+"F4.wireOp",EDGE,"E26.3.3");var subQ15=sQuery(id+"F4.wireOp",EDGE,"E26.3.2");var subQ16=sQuery(id+"F3.wireOp",EDGE,"E20.3.3");var subQ17=sQuery(id+"F3.wireOp",EDGE,"E20.3.1");var subQ18=sQuery(id+"F4.wireOp",EDGE,"E26.4.3");var subQ19=sQuery(id+"F4.wireOp",EDGE,"E26.4.2");var subQ20=sQuery(id+"F3.wireOp",EDGE,"E20.4.3");var subQ21=sQuery(id+"F3.wireOp",EDGE,"E20.4.1");var subQ22=sQuery(id+"F4.wireOp",EDGE,"E26.5.3");var subQ23=sQuery(id+"F4.wireOp",EDGE,"E26.5.2");var subQ24=sQuery(id+"F3.wireOp",EDGE,"E20.5.3");var subQ25=sQuery(id+"F3.wireOp",EDGE,"E20.5.1");var subQ26=sQuery(id+"F4.wireOp",EDGE,"E26.6.3");var subQ27=sQuery(id+"F4.wireOp",EDGE,"E26.6.2");var subQ28=sQuery(id+"F3.wireOp",EDGE,"E20.6.3");var subQ29=sQuery(id+"F3.wireOp",EDGE,"E20.6.1");var subQ30=sQuery(id+"F4.wireOp",EDGE,"E26.7.3");var subQ31=sQuery(id+"F4.wireOp",EDGE,"E26.7.2");var subQ32=sQuery(id+"F3.wireOp",EDGE,"E20.7.3");var subQ33=sQuery(id+"F3.wireOp",EDGE,"E20.7.1");var subQ34=sQuery(id+"F4.wireOp",EDGE,"E26.8.3");var subQ35=sQuery(id+"F4.wireOp",EDGE,"E26.8.2");var subQ36=sQuery(id+"F3.wireOp",EDGE,"E20.8.3");var subQ37=sQuery(id+"F3.wireOp",EDGE,"E20.8.1");var subQ38=sQuery(id+"F4.wireOp",EDGE,"E26.9.3");var subQ39=sQuery(id+"F4.wireOp",EDGE,"E26.9.2");var subQ40=sQuery(id+"F3.wireOp",EDGE,"E20.9.3");var subQ41=sQuery(id+"F3.wireOp",EDGE,"E20.9.1");var subQ42=sQuery(id+"F4.wireOp",EDGE,"E26.10.3");var subQ43=sQuery(id+"F4.wireOp",EDGE,"E26.10.2");var subQ44=sQuery(id+"F3.wireOp",EDGE,"E20.10.3");var subQ45=sQuery(id+"F3.wireOp",EDGE,"E20.10.1");var subQ46=sQuery(id+"F4.wireOp",EDGE,"E26.11.3");var subQ47=sQuery(id+"F4.wireOp",EDGE,"E26.11.2");var subQ48=sQuery(id+"F3.wireOp",EDGE,"E20.11.3");var subQ49=sQuery(id+"F3.wireOp",EDGE,"E20.11.1");var subQ50=sQuery(id+"F4.wireOp",EDGE,"E26.12.3");var subQ51=sQuery(id+"F4.wireOp",EDGE,"E26.12.2");var subQ52=sQuery(id+"F3.wireOp",EDGE,"E20.12.3");var subQ53=sQuery(id+"F3.wireOp",EDGE,"E20.12.1");var subQ54=sQuery(id+"F4.wireOp",EDGE,"E26.13.3");var subQ55=sQuery(id+"F4.wireOp",EDGE,"E26.13.2");var subQ56=sQuery(id+"F3.wireOp",EDGE,"E20.13.3");var subQ57=sQuery(id+"F3.wireOp",EDGE,"E20.13.1");var subQ58=sQuery(id+"F4.wireOp",EDGE,"E26.14.3");var subQ59=sQuery(id+"F4.wireOp",EDGE,"E26.14.2");var subQ60=sQuery(id+"F3.wireOp",EDGE,"E20.14.3");var subQ61=sQuery(id+"F3.wireOp",EDGE,"E20.14.1");var subQ62=sQuery(id+"F4.wireOp",EDGE,"E26.15.3");var subQ63=sQuery(id+"F4.wireOp",EDGE,"E26.15.2");var subQ64=sQuery(id+"F3.wireOp",EDGE,"E20.15.3");var subQ65=sQuery(id+"F3.wireOp",EDGE,"E20.15.1");var subQ66=sQuery(id+"F4.wireOp",EDGE,"E23");var subQ67=sQuery(id+"F4.wireOp",EDGE,"E22");var subQ68=sQuery(id+"F3.wireOp",EDGE,"E18.top");var subQ69=sQuery(id+"F3.wireOp",EDGE,"E18.bottom");var subQ71=makeQuery(id+"F5.opLoft","SWEPT_FACE",FACE,{"disambiguationData":[OSD([subQ69,subQ68,sQuery(id+"F3.wireOp",EDGE,"E18.left"),sQuery(id+"F4.wireOp",EDGE,"E21"),subQ67,subQ66])]});var subQ74=makeQuery(id+"F42.boolean.opBoolean","COPY",FACE,{"disambiguationData":[TD([subQ71])],"derivedFrom":subQ6});var subQ75=makeQuery(id+"F5.boolean.opBoolean","INTERSECT",EDGE,{"derivedFrom":[makeQuery(id+"F1.opRevolve","SWEPT_FACE",FACE,{"disambiguationData":[OSD([sQuery(id+"F0.wireOp",EDGE,"E13")])]}),subQ71]});Q54=makeQuery(id+"F48.opFillet","BLEND_EDGE",EDGE,{"blendedFrom":[makeQuery(id+"F47.opFillet","TWEAK_EDGE",EDGE,{"derivedFrom":[makeQuery(id+"F45.opFillet","BLEND_VERTEX",VERTEX,{"blendedFrom":[subQ75,subQ71,subQ74],"blendedInto":[subQ71,subQ74]}),makeQuery(id+"F45.opFillet","BLEND_VERTEX",VERTEX,{"blendedFrom":[subQ75,makeQuery(id+"F42.boolean.opBoolean","MERGE",FACE,{"derivedFrom":[subQ0,subQ8]}),subQ74],"blendedInto":[makeQuery(id+"F42.boolean.opBoolean","MERGE",FACE,{"derivedFrom":[subQ0,subQ8]}),subQ74]})]}),makeQuery(id+"F47.opFillet","BLEND_FACE",FACE,{"disambiguationData":[OSD([subQ5,subQ7]),TDD([makeQuery(id+"F42.boolean.opBoolean","COPY",EDGE,{"disambiguationData":[TD([subQ71])],"derivedFrom":subQ9})])]}),makeQuery(id+"F47.opFillet","BLEND_FACE",FACE,{"disambiguationData":[OSD([subQ5,subQ7]),TDD([makeQuery(id+"F42.boolean.opBoolean","COPY",EDGE,{"disambiguationData":[TD([makeQuery(id+"F6.opLoft","SWEPT_FACE",FACE,{"disambiguationData":[OSD([sQuery(id+"F3.wireOp",EDGE,"E20.15.0"),subQ65,subQ64,sQuery(id+"F4.wireOp",EDGE,"E26.15.0"),subQ63,subQ62])]})])],"derivedFrom":subQ9})])]}),makeQuery(id+"F47.opFillet","BLEND_FACE",FACE,{"disambiguationData":[OSD([subQ5,subQ7]),TDD([makeQuery(id+"F42.boolean.opBoolean","COPY",EDGE,{"disambiguationData":[TD([makeQuery(id+"F7.opLoft","SWEPT_FACE",FACE,{"disambiguationData":[OSD([sQuery(id+"F3.wireOp",EDGE,"E20.14.0"),subQ61,subQ60,sQuery(id+"F4.wireOp",EDGE,"E26.14.0"),subQ59,subQ58])]})])],"derivedFrom":subQ9})])]}),makeQuery(id+"F47.opFillet","BLEND_FACE",FACE,{"disambiguationData":[OSD([subQ5,subQ7]),TDD([makeQuery(id+"F42.boolean.opBoolean","COPY",EDGE,{"disambiguationData":[TD([makeQuery(id+"F8.opLoft","SWEPT_FACE",FACE,{"disambiguationData":[OSD([sQuery(id+"F3.wireOp",EDGE,"E20.13.0"),subQ57,subQ56,sQuery(id+"F4.wireOp",EDGE,"E26.13.0"),subQ55,subQ54])]})])],"derivedFrom":subQ9})])]}),makeQuery(id+"F47.opFillet","BLEND_FACE",FACE,{"disambiguationData":[OSD([subQ5,subQ7]),TDD([makeQuery(id+"F42.boolean.opBoolean","COPY",EDGE,{"disambiguationData":[TD([makeQuery(id+"F9.opLoft","SWEPT_FACE",FACE,{"disambiguationData":[OSD([sQuery(id+"F3.wireOp",EDGE,"E20.12.0"),subQ53,subQ52,sQuery(id+"F4.wireOp",EDGE,"E26.12.0"),subQ51,subQ50])]})])],"derivedFrom":subQ9})])]}),makeQuery(id+"F47.opFillet","BLEND_FACE",FACE,{"disambiguationData":[OSD([subQ5,subQ7]),TDD([makeQuery(id+"F42.boolean.opBoolean","COPY",EDGE,{"disambiguationData":[TD([makeQuery(id+"F10.opLoft","SWEPT_FACE",FACE,{"disambiguationData":[OSD([sQuery(id+"F3.wireOp",EDGE,"E20.11.0"),subQ49,subQ48,sQuery(id+"F4.wireOp",EDGE,"E26.11.0"),subQ47,subQ46])]})])],"derivedFrom":subQ9})])]}),makeQuery(id+"F47.opFillet","BLEND_FACE",FACE,{"disambiguationData":[OSD([subQ5,subQ7]),TDD([makeQuery(id+"F42.boolean.opBoolean","COPY",EDGE,{"disambiguationData":[TD([makeQuery(id+"F11.opLoft","SWEPT_FACE",FACE,{"disambiguationData":[OSD([sQuery(id+"F3.wireOp",EDGE,"E20.10.0"),subQ45,subQ44,sQuery(id+"F4.wireOp",EDGE,"E26.10.0"),subQ43,subQ42])]})])],"derivedFrom":subQ9})])]}),makeQuery(id+"F47.opFillet","BLEND_FACE",FACE,{"disambiguationData":[OSD([subQ5,subQ7]),TDD([makeQuery(id+"F42.boolean.opBoolean","COPY",EDGE,{"disambiguationData":[TD([makeQuery(id+"F12.opLoft","SWEPT_FACE",FACE,{"disambiguationData":[OSD([sQuery(id+"F3.wireOp",EDGE,"E20.9.0"),subQ41,subQ40,sQuery(id+"F4.wireOp",EDGE,"E26.9.0"),subQ39,subQ38])]})])],"derivedFrom":subQ9})])]}),makeQuery(id+"F47.opFillet","BLEND_FACE",FACE,{"disambiguationData":[OSD([subQ5,subQ7]),TDD([makeQuery(id+"F42.boolean.opBoolean","COPY",EDGE,{"disambiguationData":[TD([makeQuery(id+"F13.opLoft","SWEPT_FACE",FACE,{"disambiguationData":[OSD([sQuery(id+"F3.wireOp",EDGE,"E20.8.0"),subQ37,subQ36,sQuery(id+"F4.wireOp",EDGE,"E26.8.0"),subQ35,subQ34])]})])],"derivedFrom":subQ9})])]}),makeQuery(id+"F47.opFillet","BLEND_FACE",FACE,{"disambiguationData":[OSD([subQ5,subQ7]),TDD([makeQuery(id+"F42.boolean.opBoolean","COPY",EDGE,{"disambiguationData":[TD([makeQuery(id+"F14.opLoft","SWEPT_FACE",FACE,{"disambiguationData":[OSD([sQuery(id+"F3.wireOp",EDGE,"E20.7.0"),subQ33,subQ32,sQuery(id+"F4.wireOp",EDGE,"E26.7.0"),subQ31,subQ30])]})])],"derivedFrom":subQ9})])]}),makeQuery(id+"F47.opFillet","BLEND_FACE",FACE,{"disambiguationData":[OSD([subQ5,subQ7]),TDD([makeQuery(id+"F42.boolean.opBoolean","COPY",EDGE,{"disambiguationData":[TD([makeQuery(id+"F15.opLoft","SWEPT_FACE",FACE,{"disambiguationData":[OSD([sQuery(id+"F3.wireOp",EDGE,"E20.6.0"),subQ29,subQ28,sQuery(id+"F4.wireOp",EDGE,"E26.6.0"),subQ27,subQ26])]})])],"derivedFrom":subQ9})])]}),makeQuery(id+"F47.opFillet","BLEND_FACE",FACE,{"disambiguationData":[OSD([subQ5,subQ7]),TDD([makeQuery(id+"F42.boolean.opBoolean","COPY",EDGE,{"disambiguationData":[TD([makeQuery(id+"F16.opLoft","SWEPT_FACE",FACE,{"disambiguationData":[OSD([sQuery(id+"F3.wireOp",EDGE,"E20.5.0"),subQ25,subQ24,sQuery(id+"F4.wireOp",EDGE,"E26.5.0"),subQ23,subQ22])]})])],"derivedFrom":subQ9})])]}),makeQuery(id+"F47.opFillet","BLEND_FACE",FACE,{"disambiguationData":[OSD([subQ5,subQ7]),TDD([makeQuery(id+"F42.boolean.opBoolean","COPY",EDGE,{"disambiguationData":[TD([makeQuery(id+"F17.opLoft","SWEPT_FACE",FACE,{"disambiguationData":[OSD([sQuery(id+"F3.wireOp",EDGE,"E20.4.0"),subQ21,subQ20,sQuery(id+"F4.wireOp",EDGE,"E26.4.0"),subQ19,subQ18])]})])],"derivedFrom":subQ9})])]}),makeQuery(id+"F47.opFillet","BLEND_FACE",FACE,{"disambiguationData":[OSD([subQ5,subQ7]),TDD([makeQuery(id+"F42.boolean.opBoolean","COPY",EDGE,{"disambiguationData":[TD([makeQuery(id+"F18.opLoft","SWEPT_FACE",FACE,{"disambiguationData":[OSD([sQuery(id+"F3.wireOp",EDGE,"E20.3.0"),subQ17,subQ16,sQuery(id+"F4.wireOp",EDGE,"E26.3.0"),subQ15,subQ14])]})])],"derivedFrom":subQ9})])]}),makeQuery(id+"F47.opFillet","BLEND_FACE",FACE,{"disambiguationData":[OSD([subQ5,subQ7]),TDD([makeQuery(id+"F42.boolean.opBoolean","COPY",EDGE,{"disambiguationData":[TD([makeQuery(id+"F19.opLoft","SWEPT_FACE",FACE,{"disambiguationData":[OSD([sQuery(id+"F3.wireOp",EDGE,"E20.2.0"),subQ13,subQ12,sQuery(id+"F4.wireOp",EDGE,"E26.2.0"),subQ11,subQ10])]})])],"derivedFrom":subQ9})])]}),makeQuery(id+"F47.opFillet","BLEND_FACE",FACE,{"disambiguationData":[OSD([subQ5,subQ7]),TDD([makeQuery(id+"F42.boolean.opBoolean","COPY",EDGE,{"disambiguationData":[TD([makeQuery(id+"F20.opLoft","SWEPT_FACE",FACE,{"disambiguationData":[OSD([sQuery(id+"F3.wireOp",EDGE,"E20.1.0"),subQ4,subQ3,sQuery(id+"F4.wireOp",EDGE,"E26.1.0"),subQ2,subQ1])]})])],"derivedFrom":subQ9})])]})],"blendedInto":[makeQuery(id+"F47.opFillet","BLEND_FACE",FACE,{"disambiguationData":[OSD([subQ5,subQ7]),TDD([makeQuery(id+"F42.boolean.opBoolean","COPY",EDGE,{"disambiguationData":[TD([subQ71])],"derivedFrom":subQ9})])]}),makeQuery(id+"F47.opFillet","BLEND_FACE",FACE,{"disambiguationData":[OSD([subQ5,subQ7]),TDD([makeQuery(id+"F42.boolean.opBoolean","COPY",EDGE,{"disambiguationData":[TD([makeQuery(id+"F6.opLoft","SWEPT_FACE",FACE,{"disambiguationData":[OSD([sQuery(id+"F3.wireOp",EDGE,"E20.15.0"),subQ65,subQ64,sQuery(id+"F4.wireOp",EDGE,"E26.15.0"),subQ63,subQ62])]})])],"derivedFrom":subQ9})])]}),makeQuery(id+"F47.opFillet","BLEND_FACE",FACE,{"disambiguationData":[OSD([subQ5,subQ7]),TDD([makeQuery(id+"F42.boolean.opBoolean","COPY",EDGE,{"disambiguationData":[TD([makeQuery(id+"F7.opLoft","SWEPT_FACE",FACE,{"disambiguationData":[OSD([sQuery(id+"F3.wireOp",EDGE,"E20.14.0"),subQ61,subQ60,sQuery(id+"F4.wireOp",EDGE,"E26.14.0"),subQ59,subQ58])]})])],"derivedFrom":subQ9})])]}),makeQuery(id+"F47.opFillet","BLEND_FACE",FACE,{"disambiguationData":[OSD([subQ5,subQ7]),TDD([makeQuery(id+"F42.boolean.opBoolean","COPY",EDGE,{"disambiguationData":[TD([makeQuery(id+"F8.opLoft","SWEPT_FACE",FACE,{"disambiguationData":[OSD([sQuery(id+"F3.wireOp",EDGE,"E20.13.0"),subQ57,subQ56,sQuery(id+"F4.wireOp",EDGE,"E26.13.0"),subQ55,subQ54])]})])],"derivedFrom":subQ9})])]}),makeQuery(id+"F47.opFillet","BLEND_FACE",FACE,{"disambiguationData":[OSD([subQ5,subQ7]),TDD([makeQuery(id+"F42.boolean.opBoolean","COPY",EDGE,{"disambiguationData":[TD([makeQuery(id+"F9.opLoft","SWEPT_FACE",FACE,{"disambiguationData":[OSD([sQuery(id+"F3.wireOp",EDGE,"E20.12.0"),subQ53,subQ52,sQuery(id+"F4.wireOp",EDGE,"E26.12.0"),subQ51,subQ50])]})])],"derivedFrom":subQ9})])]}),makeQuery(id+"F47.opFillet","BLEND_FACE",FACE,{"disambiguationData":[OSD([subQ5,subQ7]),TDD([makeQuery(id+"F42.boolean.opBoolean","COPY",EDGE,{"disambiguationData":[TD([makeQuery(id+"F10.opLoft","SWEPT_FACE",FACE,{"disambiguationData":[OSD([sQuery(id+"F3.wireOp",EDGE,"E20.11.0"),subQ49,subQ48,sQuery(id+"F4.wireOp",EDGE,"E26.11.0"),subQ47,subQ46])]})])],"derivedFrom":subQ9})])]}),makeQuery(id+"F47.opFillet","BLEND_FACE",FACE,{"disambiguationData":[OSD([subQ5,subQ7]),TDD([makeQuery(id+"F42.boolean.opBoolean","COPY",EDGE,{"disambiguationData":[TD([makeQuery(id+"F11.opLoft","SWEPT_FACE",FACE,{"disambiguationData":[OSD([sQuery(id+"F3.wireOp",EDGE,"E20.10.0"),subQ45,subQ44,sQuery(id+"F4.wireOp",EDGE,"E26.10.0"),subQ43,subQ42])]})])],"derivedFrom":subQ9})])]}),makeQuery(id+"F47.opFillet","BLEND_FACE",FACE,{"disambiguationData":[OSD([subQ5,subQ7]),TDD([makeQuery(id+"F42.boolean.opBoolean","COPY",EDGE,{"disambiguationData":[TD([makeQuery(id+"F12.opLoft","SWEPT_FACE",FACE,{"disambiguationData":[OSD([sQuery(id+"F3.wireOp",EDGE,"E20.9.0"),subQ41,subQ40,sQuery(id+"F4.wireOp",EDGE,"E26.9.0"),subQ39,subQ38])]})])],"derivedFrom":subQ9})])]}),makeQuery(id+"F47.opFillet","BLEND_FACE",FACE,{"disambiguationData":[OSD([subQ5,subQ7]),TDD([makeQuery(id+"F42.boolean.opBoolean","COPY",EDGE,{"disambiguationData":[TD([makeQuery(id+"F13.opLoft","SWEPT_FACE",FACE,{"disambiguationData":[OSD([sQuery(id+"F3.wireOp",EDGE,"E20.8.0"),subQ37,subQ36,sQuery(id+"F4.wireOp",EDGE,"E26.8.0"),subQ35,subQ34])]})])],"derivedFrom":subQ9})])]}),makeQuery(id+"F47.opFillet","BLEND_FACE",FACE,{"disambiguationData":[OSD([subQ5,subQ7]),TDD([makeQuery(id+"F42.boolean.opBoolean","COPY",EDGE,{"disambiguationData":[TD([makeQuery(id+"F14.opLoft","SWEPT_FACE",FACE,{"disambiguationData":[OSD([sQuery(id+"F3.wireOp",EDGE,"E20.7.0"),subQ33,subQ32,sQuery(id+"F4.wireOp",EDGE,"E26.7.0"),subQ31,subQ30])]})])],"derivedFrom":subQ9})])]}),makeQuery(id+"F47.opFillet","BLEND_FACE",FACE,{"disambiguationData":[OSD([subQ5,subQ7]),TDD([makeQuery(id+"F42.boolean.opBoolean","COPY",EDGE,{"disambiguationData":[TD([makeQuery(id+"F15.opLoft","SWEPT_FACE",FACE,{"disambiguationData":[OSD([sQuery(id+"F3.wireOp",EDGE,"E20.6.0"),subQ29,subQ28,sQuery(id+"F4.wireOp",EDGE,"E26.6.0"),subQ27,subQ26])]})])],"derivedFrom":subQ9})])]}),makeQuery(id+"F47.opFillet","BLEND_FACE",FACE,{"disambiguationData":[OSD([subQ5,subQ7]),TDD([makeQuery(id+"F42.boolean.opBoolean","COPY",EDGE,{"disambiguationData":[TD([makeQuery(id+"F16.opLoft","SWEPT_FACE",FACE,{"disambiguationData":[OSD([sQuery(id+"F3.wireOp",EDGE,"E20.5.0"),subQ25,subQ24,sQuery(id+"F4.wireOp",EDGE,"E26.5.0"),subQ23,subQ22])]})])],"derivedFrom":subQ9})])]}),makeQuery(id+"F47.opFillet","BLEND_FACE",FACE,{"disambiguationData":[OSD([subQ5,subQ7]),TDD([makeQuery(id+"F42.boolean.opBoolean","COPY",EDGE,{"disambiguationData":[TD([makeQuery(id+"F17.opLoft","SWEPT_FACE",FACE,{"disambiguationData":[OSD([sQuery(id+"F3.wireOp",EDGE,"E20.4.0"),subQ21,subQ20,sQuery(id+"F4.wireOp",EDGE,"E26.4.0"),subQ19,subQ18])]})])],"derivedFrom":subQ9})])]}),makeQuery(id+"F47.opFillet","BLEND_FACE",FACE,{"disambiguationData":[OSD([subQ5,subQ7]),TDD([makeQuery(id+"F42.boolean.opBoolean","COPY",EDGE,{"disambiguationData":[TD([makeQuery(id+"F18.opLoft","SWEPT_FACE",FACE,{"disambiguationData":[OSD([sQuery(id+"F3.wireOp",EDGE,"E20.3.0"),subQ17,subQ16,sQuery(id+"F4.wireOp",EDGE,"E26.3.0"),subQ15,subQ14])]})])],"derivedFrom":subQ9})])]}),makeQuery(id+"F47.opFillet","BLEND_FACE",FACE,{"disambiguationData":[OSD([subQ5,subQ7]),TDD([makeQuery(id+"F42.boolean.opBoolean","COPY",EDGE,{"disambiguationData":[TD([makeQuery(id+"F19.opLoft","SWEPT_FACE",FACE,{"disambiguationData":[OSD([sQuery(id+"F3.wireOp",EDGE,"E20.2.0"),subQ13,subQ12,sQuery(id+"F4.wireOp",EDGE,"E26.2.0"),subQ11,subQ10])]})])],"derivedFrom":subQ9})])]}),makeQuery(id+"F47.opFillet","BLEND_FACE",FACE,{"disambiguationData":[OSD([subQ5,subQ7]),TDD([makeQuery(id+"F42.boolean.opBoolean","COPY",EDGE,{"disambiguationData":[TD([makeQuery(id+"F20.opLoft","SWEPT_FACE",FACE,{"disambiguationData":[OSD([sQuery(id+"F3.wireOp",EDGE,"E20.1.0"),subQ4,subQ3,sQuery(id+"F4.wireOp",EDGE,"E26.1.0"),subQ2,subQ1])]})])],"derivedFrom":subQ9})])]})]});}
            var Q55;
            {var subQ0=makeQuery(id+"F40.opExtrude","CAP_FACE",FACE,{"disambiguationData":[OSD([sQuery(id+"F39.wireOp",EDGE,"E29"),sQuery(id+"F39.wireOp",EDGE,"E30")])],"isStart":false});var subQ1=sQuery(id+"F4.wireOp",EDGE,"E26.1.3");var subQ2=sQuery(id+"F4.wireOp",EDGE,"E26.1.2");var subQ3=sQuery(id+"F3.wireOp",EDGE,"E20.1.3");var subQ4=sQuery(id+"F3.wireOp",EDGE,"E20.1.1");var subQ5=sQuery(id+"F41.wireOp",EDGE,"E35");var subQ6=makeQuery(id+"F42.opRevolve","SWEPT_FACE",FACE,{"disambiguationData":[OSD([subQ5])]});var subQ7=sQuery(id+"F41.wireOp",EDGE,"E36");var subQ8=makeQuery(id+"F42.opRevolve","SWEPT_FACE",FACE,{"disambiguationData":[OSD([subQ7])]});var subQ9=makeQuery(id+"F42.opRevolve","SWEPT_EDGE",EDGE,{"disambiguationData":[OSD([subQ5,subQ7])]});var subQ10=sQuery(id+"F4.wireOp",EDGE,"E26.2.3");var subQ11=sQuery(id+"F4.wireOp",EDGE,"E26.2.2");var subQ12=sQuery(id+"F3.wireOp",EDGE,"E20.2.3");var subQ13=sQuery(id+"F3.wireOp",EDGE,"E20.2.1");var subQ14=sQuery(id+"F4.wireOp",EDGE,"E26.3.3");var subQ15=sQuery(id+"F4.wireOp",EDGE,"E26.3.2");var subQ16=sQuery(id+"F3.wireOp",EDGE,"E20.3.3");var subQ17=sQuery(id+"F3.wireOp",EDGE,"E20.3.1");var subQ18=sQuery(id+"F4.wireOp",EDGE,"E26.4.3");var subQ19=sQuery(id+"F4.wireOp",EDGE,"E26.4.2");var subQ20=sQuery(id+"F3.wireOp",EDGE,"E20.4.3");var subQ21=sQuery(id+"F3.wireOp",EDGE,"E20.4.1");var subQ22=sQuery(id+"F4.wireOp",EDGE,"E26.5.3");var subQ23=sQuery(id+"F4.wireOp",EDGE,"E26.5.2");var subQ24=sQuery(id+"F3.wireOp",EDGE,"E20.5.3");var subQ25=sQuery(id+"F3.wireOp",EDGE,"E20.5.1");var subQ26=sQuery(id+"F4.wireOp",EDGE,"E26.6.3");var subQ27=sQuery(id+"F4.wireOp",EDGE,"E26.6.2");var subQ28=sQuery(id+"F3.wireOp",EDGE,"E20.6.3");var subQ29=sQuery(id+"F3.wireOp",EDGE,"E20.6.1");var subQ30=sQuery(id+"F4.wireOp",EDGE,"E26.7.3");var subQ31=sQuery(id+"F4.wireOp",EDGE,"E26.7.2");var subQ32=sQuery(id+"F3.wireOp",EDGE,"E20.7.3");var subQ33=sQuery(id+"F3.wireOp",EDGE,"E20.7.1");var subQ34=sQuery(id+"F4.wireOp",EDGE,"E26.8.3");var subQ35=sQuery(id+"F4.wireOp",EDGE,"E26.8.2");var subQ36=sQuery(id+"F3.wireOp",EDGE,"E20.8.3");var subQ37=sQuery(id+"F3.wireOp",EDGE,"E20.8.1");var subQ38=sQuery(id+"F4.wireOp",EDGE,"E26.9.3");var subQ39=sQuery(id+"F4.wireOp",EDGE,"E26.9.2");var subQ40=sQuery(id+"F3.wireOp",EDGE,"E20.9.3");var subQ41=sQuery(id+"F3.wireOp",EDGE,"E20.9.1");var subQ42=sQuery(id+"F4.wireOp",EDGE,"E26.10.3");var subQ43=sQuery(id+"F4.wireOp",EDGE,"E26.10.2");var subQ44=sQuery(id+"F3.wireOp",EDGE,"E20.10.3");var subQ45=sQuery(id+"F3.wireOp",EDGE,"E20.10.1");var subQ46=sQuery(id+"F4.wireOp",EDGE,"E26.11.3");var subQ47=sQuery(id+"F4.wireOp",EDGE,"E26.11.2");var subQ48=sQuery(id+"F3.wireOp",EDGE,"E20.11.3");var subQ49=sQuery(id+"F3.wireOp",EDGE,"E20.11.1");var subQ50=sQuery(id+"F4.wireOp",EDGE,"E26.12.3");var subQ51=sQuery(id+"F4.wireOp",EDGE,"E26.12.2");var subQ52=sQuery(id+"F3.wireOp",EDGE,"E20.12.3");var subQ53=sQuery(id+"F3.wireOp",EDGE,"E20.12.1");var subQ54=sQuery(id+"F4.wireOp",EDGE,"E26.13.3");var subQ55=sQuery(id+"F4.wireOp",EDGE,"E26.13.2");var subQ56=sQuery(id+"F3.wireOp",EDGE,"E20.13.3");var subQ57=sQuery(id+"F3.wireOp",EDGE,"E20.13.1");var subQ58=sQuery(id+"F4.wireOp",EDGE,"E26.14.3");var subQ59=sQuery(id+"F4.wireOp",EDGE,"E26.14.2");var subQ60=sQuery(id+"F3.wireOp",EDGE,"E20.14.3");var subQ61=sQuery(id+"F3.wireOp",EDGE,"E20.14.1");var subQ62=sQuery(id+"F4.wireOp",EDGE,"E26.15.3");var subQ63=sQuery(id+"F4.wireOp",EDGE,"E26.15.2");var subQ64=sQuery(id+"F3.wireOp",EDGE,"E20.15.3");var subQ65=sQuery(id+"F3.wireOp",EDGE,"E20.15.1");var subQ67=makeQuery(id+"F6.opLoft","SWEPT_FACE",FACE,{"disambiguationData":[OSD([sQuery(id+"F3.wireOp",EDGE,"E20.15.0"),subQ65,subQ64,sQuery(id+"F4.wireOp",EDGE,"E26.15.0"),subQ63,subQ62])]});var subQ68=sQuery(id+"F4.wireOp",EDGE,"E23");var subQ69=sQuery(id+"F4.wireOp",EDGE,"E22");var subQ70=sQuery(id+"F3.wireOp",EDGE,"E18.top");var subQ71=sQuery(id+"F3.wireOp",EDGE,"E18.bottom");var subQ74=makeQuery(id+"F42.boolean.opBoolean","COPY",FACE,{"disambiguationData":[TD([subQ67])],"derivedFrom":subQ6});var subQ75=makeQuery(id+"F6.boolean.opBoolean","INTERSECT",EDGE,{"derivedFrom":[makeQuery(id+"F1.opRevolve","SWEPT_FACE",FACE,{"disambiguationData":[OSD([sQuery(id+"F0.wireOp",EDGE,"E13")])]}),subQ67]});Q55=makeQuery(id+"F48.opFillet","BLEND_EDGE",EDGE,{"blendedFrom":[makeQuery(id+"F47.opFillet","TWEAK_EDGE",EDGE,{"derivedFrom":[makeQuery(id+"F45.opFillet","BLEND_VERTEX",VERTEX,{"blendedFrom":[subQ75,subQ67,subQ74],"blendedInto":[subQ67,subQ74]}),makeQuery(id+"F45.opFillet","BLEND_VERTEX",VERTEX,{"blendedFrom":[subQ75,makeQuery(id+"F42.boolean.opBoolean","MERGE",FACE,{"derivedFrom":[subQ0,subQ8]}),subQ74],"blendedInto":[makeQuery(id+"F42.boolean.opBoolean","MERGE",FACE,{"derivedFrom":[subQ0,subQ8]}),subQ74]})]}),makeQuery(id+"F47.opFillet","BLEND_FACE",FACE,{"disambiguationData":[OSD([subQ5,subQ7]),TDD([makeQuery(id+"F42.boolean.opBoolean","COPY",EDGE,{"disambiguationData":[TD([makeQuery(id+"F5.opLoft","SWEPT_FACE",FACE,{"disambiguationData":[OSD([subQ71,subQ70,sQuery(id+"F3.wireOp",EDGE,"E18.left"),sQuery(id+"F4.wireOp",EDGE,"E21"),subQ69,subQ68])]})])],"derivedFrom":subQ9})])]}),makeQuery(id+"F47.opFillet","BLEND_FACE",FACE,{"disambiguationData":[OSD([subQ5,subQ7]),TDD([makeQuery(id+"F42.boolean.opBoolean","COPY",EDGE,{"disambiguationData":[TD([subQ67])],"derivedFrom":subQ9})])]}),makeQuery(id+"F47.opFillet","BLEND_FACE",FACE,{"disambiguationData":[OSD([subQ5,subQ7]),TDD([makeQuery(id+"F42.boolean.opBoolean","COPY",EDGE,{"disambiguationData":[TD([makeQuery(id+"F7.opLoft","SWEPT_FACE",FACE,{"disambiguationData":[OSD([sQuery(id+"F3.wireOp",EDGE,"E20.14.0"),subQ61,subQ60,sQuery(id+"F4.wireOp",EDGE,"E26.14.0"),subQ59,subQ58])]})])],"derivedFrom":subQ9})])]}),makeQuery(id+"F47.opFillet","BLEND_FACE",FACE,{"disambiguationData":[OSD([subQ5,subQ7]),TDD([makeQuery(id+"F42.boolean.opBoolean","COPY",EDGE,{"disambiguationData":[TD([makeQuery(id+"F8.opLoft","SWEPT_FACE",FACE,{"disambiguationData":[OSD([sQuery(id+"F3.wireOp",EDGE,"E20.13.0"),subQ57,subQ56,sQuery(id+"F4.wireOp",EDGE,"E26.13.0"),subQ55,subQ54])]})])],"derivedFrom":subQ9})])]}),makeQuery(id+"F47.opFillet","BLEND_FACE",FACE,{"disambiguationData":[OSD([subQ5,subQ7]),TDD([makeQuery(id+"F42.boolean.opBoolean","COPY",EDGE,{"disambiguationData":[TD([makeQuery(id+"F9.opLoft","SWEPT_FACE",FACE,{"disambiguationData":[OSD([sQuery(id+"F3.wireOp",EDGE,"E20.12.0"),subQ53,subQ52,sQuery(id+"F4.wireOp",EDGE,"E26.12.0"),subQ51,subQ50])]})])],"derivedFrom":subQ9})])]}),makeQuery(id+"F47.opFillet","BLEND_FACE",FACE,{"disambiguationData":[OSD([subQ5,subQ7]),TDD([makeQuery(id+"F42.boolean.opBoolean","COPY",EDGE,{"disambiguationData":[TD([makeQuery(id+"F10.opLoft","SWEPT_FACE",FACE,{"disambiguationData":[OSD([sQuery(id+"F3.wireOp",EDGE,"E20.11.0"),subQ49,subQ48,sQuery(id+"F4.wireOp",EDGE,"E26.11.0"),subQ47,subQ46])]})])],"derivedFrom":subQ9})])]}),makeQuery(id+"F47.opFillet","BLEND_FACE",FACE,{"disambiguationData":[OSD([subQ5,subQ7]),TDD([makeQuery(id+"F42.boolean.opBoolean","COPY",EDGE,{"disambiguationData":[TD([makeQuery(id+"F11.opLoft","SWEPT_FACE",FACE,{"disambiguationData":[OSD([sQuery(id+"F3.wireOp",EDGE,"E20.10.0"),subQ45,subQ44,sQuery(id+"F4.wireOp",EDGE,"E26.10.0"),subQ43,subQ42])]})])],"derivedFrom":subQ9})])]}),makeQuery(id+"F47.opFillet","BLEND_FACE",FACE,{"disambiguationData":[OSD([subQ5,subQ7]),TDD([makeQuery(id+"F42.boolean.opBoolean","COPY",EDGE,{"disambiguationData":[TD([makeQuery(id+"F12.opLoft","SWEPT_FACE",FACE,{"disambiguationData":[OSD([sQuery(id+"F3.wireOp",EDGE,"E20.9.0"),subQ41,subQ40,sQuery(id+"F4.wireOp",EDGE,"E26.9.0"),subQ39,subQ38])]})])],"derivedFrom":subQ9})])]}),makeQuery(id+"F47.opFillet","BLEND_FACE",FACE,{"disambiguationData":[OSD([subQ5,subQ7]),TDD([makeQuery(id+"F42.boolean.opBoolean","COPY",EDGE,{"disambiguationData":[TD([makeQuery(id+"F13.opLoft","SWEPT_FACE",FACE,{"disambiguationData":[OSD([sQuery(id+"F3.wireOp",EDGE,"E20.8.0"),subQ37,subQ36,sQuery(id+"F4.wireOp",EDGE,"E26.8.0"),subQ35,subQ34])]})])],"derivedFrom":subQ9})])]}),makeQuery(id+"F47.opFillet","BLEND_FACE",FACE,{"disambiguationData":[OSD([subQ5,subQ7]),TDD([makeQuery(id+"F42.boolean.opBoolean","COPY",EDGE,{"disambiguationData":[TD([makeQuery(id+"F14.opLoft","SWEPT_FACE",FACE,{"disambiguationData":[OSD([sQuery(id+"F3.wireOp",EDGE,"E20.7.0"),subQ33,subQ32,sQuery(id+"F4.wireOp",EDGE,"E26.7.0"),subQ31,subQ30])]})])],"derivedFrom":subQ9})])]}),makeQuery(id+"F47.opFillet","BLEND_FACE",FACE,{"disambiguationData":[OSD([subQ5,subQ7]),TDD([makeQuery(id+"F42.boolean.opBoolean","COPY",EDGE,{"disambiguationData":[TD([makeQuery(id+"F15.opLoft","SWEPT_FACE",FACE,{"disambiguationData":[OSD([sQuery(id+"F3.wireOp",EDGE,"E20.6.0"),subQ29,subQ28,sQuery(id+"F4.wireOp",EDGE,"E26.6.0"),subQ27,subQ26])]})])],"derivedFrom":subQ9})])]}),makeQuery(id+"F47.opFillet","BLEND_FACE",FACE,{"disambiguationData":[OSD([subQ5,subQ7]),TDD([makeQuery(id+"F42.boolean.opBoolean","COPY",EDGE,{"disambiguationData":[TD([makeQuery(id+"F16.opLoft","SWEPT_FACE",FACE,{"disambiguationData":[OSD([sQuery(id+"F3.wireOp",EDGE,"E20.5.0"),subQ25,subQ24,sQuery(id+"F4.wireOp",EDGE,"E26.5.0"),subQ23,subQ22])]})])],"derivedFrom":subQ9})])]}),makeQuery(id+"F47.opFillet","BLEND_FACE",FACE,{"disambiguationData":[OSD([subQ5,subQ7]),TDD([makeQuery(id+"F42.boolean.opBoolean","COPY",EDGE,{"disambiguationData":[TD([makeQuery(id+"F17.opLoft","SWEPT_FACE",FACE,{"disambiguationData":[OSD([sQuery(id+"F3.wireOp",EDGE,"E20.4.0"),subQ21,subQ20,sQuery(id+"F4.wireOp",EDGE,"E26.4.0"),subQ19,subQ18])]})])],"derivedFrom":subQ9})])]}),makeQuery(id+"F47.opFillet","BLEND_FACE",FACE,{"disambiguationData":[OSD([subQ5,subQ7]),TDD([makeQuery(id+"F42.boolean.opBoolean","COPY",EDGE,{"disambiguationData":[TD([makeQuery(id+"F18.opLoft","SWEPT_FACE",FACE,{"disambiguationData":[OSD([sQuery(id+"F3.wireOp",EDGE,"E20.3.0"),subQ17,subQ16,sQuery(id+"F4.wireOp",EDGE,"E26.3.0"),subQ15,subQ14])]})])],"derivedFrom":subQ9})])]}),makeQuery(id+"F47.opFillet","BLEND_FACE",FACE,{"disambiguationData":[OSD([subQ5,subQ7]),TDD([makeQuery(id+"F42.boolean.opBoolean","COPY",EDGE,{"disambiguationData":[TD([makeQuery(id+"F19.opLoft","SWEPT_FACE",FACE,{"disambiguationData":[OSD([sQuery(id+"F3.wireOp",EDGE,"E20.2.0"),subQ13,subQ12,sQuery(id+"F4.wireOp",EDGE,"E26.2.0"),subQ11,subQ10])]})])],"derivedFrom":subQ9})])]}),makeQuery(id+"F47.opFillet","BLEND_FACE",FACE,{"disambiguationData":[OSD([subQ5,subQ7]),TDD([makeQuery(id+"F42.boolean.opBoolean","COPY",EDGE,{"disambiguationData":[TD([makeQuery(id+"F20.opLoft","SWEPT_FACE",FACE,{"disambiguationData":[OSD([sQuery(id+"F3.wireOp",EDGE,"E20.1.0"),subQ4,subQ3,sQuery(id+"F4.wireOp",EDGE,"E26.1.0"),subQ2,subQ1])]})])],"derivedFrom":subQ9})])]})],"blendedInto":[makeQuery(id+"F47.opFillet","BLEND_FACE",FACE,{"disambiguationData":[OSD([subQ5,subQ7]),TDD([makeQuery(id+"F42.boolean.opBoolean","COPY",EDGE,{"disambiguationData":[TD([makeQuery(id+"F5.opLoft","SWEPT_FACE",FACE,{"disambiguationData":[OSD([subQ71,subQ70,sQuery(id+"F3.wireOp",EDGE,"E18.left"),sQuery(id+"F4.wireOp",EDGE,"E21"),subQ69,subQ68])]})])],"derivedFrom":subQ9})])]}),makeQuery(id+"F47.opFillet","BLEND_FACE",FACE,{"disambiguationData":[OSD([subQ5,subQ7]),TDD([makeQuery(id+"F42.boolean.opBoolean","COPY",EDGE,{"disambiguationData":[TD([subQ67])],"derivedFrom":subQ9})])]}),makeQuery(id+"F47.opFillet","BLEND_FACE",FACE,{"disambiguationData":[OSD([subQ5,subQ7]),TDD([makeQuery(id+"F42.boolean.opBoolean","COPY",EDGE,{"disambiguationData":[TD([makeQuery(id+"F7.opLoft","SWEPT_FACE",FACE,{"disambiguationData":[OSD([sQuery(id+"F3.wireOp",EDGE,"E20.14.0"),subQ61,subQ60,sQuery(id+"F4.wireOp",EDGE,"E26.14.0"),subQ59,subQ58])]})])],"derivedFrom":subQ9})])]}),makeQuery(id+"F47.opFillet","BLEND_FACE",FACE,{"disambiguationData":[OSD([subQ5,subQ7]),TDD([makeQuery(id+"F42.boolean.opBoolean","COPY",EDGE,{"disambiguationData":[TD([makeQuery(id+"F8.opLoft","SWEPT_FACE",FACE,{"disambiguationData":[OSD([sQuery(id+"F3.wireOp",EDGE,"E20.13.0"),subQ57,subQ56,sQuery(id+"F4.wireOp",EDGE,"E26.13.0"),subQ55,subQ54])]})])],"derivedFrom":subQ9})])]}),makeQuery(id+"F47.opFillet","BLEND_FACE",FACE,{"disambiguationData":[OSD([subQ5,subQ7]),TDD([makeQuery(id+"F42.boolean.opBoolean","COPY",EDGE,{"disambiguationData":[TD([makeQuery(id+"F9.opLoft","SWEPT_FACE",FACE,{"disambiguationData":[OSD([sQuery(id+"F3.wireOp",EDGE,"E20.12.0"),subQ53,subQ52,sQuery(id+"F4.wireOp",EDGE,"E26.12.0"),subQ51,subQ50])]})])],"derivedFrom":subQ9})])]}),makeQuery(id+"F47.opFillet","BLEND_FACE",FACE,{"disambiguationData":[OSD([subQ5,subQ7]),TDD([makeQuery(id+"F42.boolean.opBoolean","COPY",EDGE,{"disambiguationData":[TD([makeQuery(id+"F10.opLoft","SWEPT_FACE",FACE,{"disambiguationData":[OSD([sQuery(id+"F3.wireOp",EDGE,"E20.11.0"),subQ49,subQ48,sQuery(id+"F4.wireOp",EDGE,"E26.11.0"),subQ47,subQ46])]})])],"derivedFrom":subQ9})])]}),makeQuery(id+"F47.opFillet","BLEND_FACE",FACE,{"disambiguationData":[OSD([subQ5,subQ7]),TDD([makeQuery(id+"F42.boolean.opBoolean","COPY",EDGE,{"disambiguationData":[TD([makeQuery(id+"F11.opLoft","SWEPT_FACE",FACE,{"disambiguationData":[OSD([sQuery(id+"F3.wireOp",EDGE,"E20.10.0"),subQ45,subQ44,sQuery(id+"F4.wireOp",EDGE,"E26.10.0"),subQ43,subQ42])]})])],"derivedFrom":subQ9})])]}),makeQuery(id+"F47.opFillet","BLEND_FACE",FACE,{"disambiguationData":[OSD([subQ5,subQ7]),TDD([makeQuery(id+"F42.boolean.opBoolean","COPY",EDGE,{"disambiguationData":[TD([makeQuery(id+"F12.opLoft","SWEPT_FACE",FACE,{"disambiguationData":[OSD([sQuery(id+"F3.wireOp",EDGE,"E20.9.0"),subQ41,subQ40,sQuery(id+"F4.wireOp",EDGE,"E26.9.0"),subQ39,subQ38])]})])],"derivedFrom":subQ9})])]}),makeQuery(id+"F47.opFillet","BLEND_FACE",FACE,{"disambiguationData":[OSD([subQ5,subQ7]),TDD([makeQuery(id+"F42.boolean.opBoolean","COPY",EDGE,{"disambiguationData":[TD([makeQuery(id+"F13.opLoft","SWEPT_FACE",FACE,{"disambiguationData":[OSD([sQuery(id+"F3.wireOp",EDGE,"E20.8.0"),subQ37,subQ36,sQuery(id+"F4.wireOp",EDGE,"E26.8.0"),subQ35,subQ34])]})])],"derivedFrom":subQ9})])]}),makeQuery(id+"F47.opFillet","BLEND_FACE",FACE,{"disambiguationData":[OSD([subQ5,subQ7]),TDD([makeQuery(id+"F42.boolean.opBoolean","COPY",EDGE,{"disambiguationData":[TD([makeQuery(id+"F14.opLoft","SWEPT_FACE",FACE,{"disambiguationData":[OSD([sQuery(id+"F3.wireOp",EDGE,"E20.7.0"),subQ33,subQ32,sQuery(id+"F4.wireOp",EDGE,"E26.7.0"),subQ31,subQ30])]})])],"derivedFrom":subQ9})])]}),makeQuery(id+"F47.opFillet","BLEND_FACE",FACE,{"disambiguationData":[OSD([subQ5,subQ7]),TDD([makeQuery(id+"F42.boolean.opBoolean","COPY",EDGE,{"disambiguationData":[TD([makeQuery(id+"F15.opLoft","SWEPT_FACE",FACE,{"disambiguationData":[OSD([sQuery(id+"F3.wireOp",EDGE,"E20.6.0"),subQ29,subQ28,sQuery(id+"F4.wireOp",EDGE,"E26.6.0"),subQ27,subQ26])]})])],"derivedFrom":subQ9})])]}),makeQuery(id+"F47.opFillet","BLEND_FACE",FACE,{"disambiguationData":[OSD([subQ5,subQ7]),TDD([makeQuery(id+"F42.boolean.opBoolean","COPY",EDGE,{"disambiguationData":[TD([makeQuery(id+"F16.opLoft","SWEPT_FACE",FACE,{"disambiguationData":[OSD([sQuery(id+"F3.wireOp",EDGE,"E20.5.0"),subQ25,subQ24,sQuery(id+"F4.wireOp",EDGE,"E26.5.0"),subQ23,subQ22])]})])],"derivedFrom":subQ9})])]}),makeQuery(id+"F47.opFillet","BLEND_FACE",FACE,{"disambiguationData":[OSD([subQ5,subQ7]),TDD([makeQuery(id+"F42.boolean.opBoolean","COPY",EDGE,{"disambiguationData":[TD([makeQuery(id+"F17.opLoft","SWEPT_FACE",FACE,{"disambiguationData":[OSD([sQuery(id+"F3.wireOp",EDGE,"E20.4.0"),subQ21,subQ20,sQuery(id+"F4.wireOp",EDGE,"E26.4.0"),subQ19,subQ18])]})])],"derivedFrom":subQ9})])]}),makeQuery(id+"F47.opFillet","BLEND_FACE",FACE,{"disambiguationData":[OSD([subQ5,subQ7]),TDD([makeQuery(id+"F42.boolean.opBoolean","COPY",EDGE,{"disambiguationData":[TD([makeQuery(id+"F18.opLoft","SWEPT_FACE",FACE,{"disambiguationData":[OSD([sQuery(id+"F3.wireOp",EDGE,"E20.3.0"),subQ17,subQ16,sQuery(id+"F4.wireOp",EDGE,"E26.3.0"),subQ15,subQ14])]})])],"derivedFrom":subQ9})])]}),makeQuery(id+"F47.opFillet","BLEND_FACE",FACE,{"disambiguationData":[OSD([subQ5,subQ7]),TDD([makeQuery(id+"F42.boolean.opBoolean","COPY",EDGE,{"disambiguationData":[TD([makeQuery(id+"F19.opLoft","SWEPT_FACE",FACE,{"disambiguationData":[OSD([sQuery(id+"F3.wireOp",EDGE,"E20.2.0"),subQ13,subQ12,sQuery(id+"F4.wireOp",EDGE,"E26.2.0"),subQ11,subQ10])]})])],"derivedFrom":subQ9})])]}),makeQuery(id+"F47.opFillet","BLEND_FACE",FACE,{"disambiguationData":[OSD([subQ5,subQ7]),TDD([makeQuery(id+"F42.boolean.opBoolean","COPY",EDGE,{"disambiguationData":[TD([makeQuery(id+"F20.opLoft","SWEPT_FACE",FACE,{"disambiguationData":[OSD([sQuery(id+"F3.wireOp",EDGE,"E20.1.0"),subQ4,subQ3,sQuery(id+"F4.wireOp",EDGE,"E26.1.0"),subQ2,subQ1])]})])],"derivedFrom":subQ9})])]})]});}
            var Q56;
            {var subQ0=makeQuery(id+"F40.opExtrude","CAP_FACE",FACE,{"disambiguationData":[OSD([sQuery(id+"F39.wireOp",EDGE,"E29"),sQuery(id+"F39.wireOp",EDGE,"E30")])],"isStart":false});var subQ1=sQuery(id+"F4.wireOp",EDGE,"E26.1.3");var subQ2=sQuery(id+"F4.wireOp",EDGE,"E26.1.2");var subQ3=sQuery(id+"F3.wireOp",EDGE,"E20.1.3");var subQ4=sQuery(id+"F3.wireOp",EDGE,"E20.1.1");var subQ5=sQuery(id+"F41.wireOp",EDGE,"E35");var subQ6=makeQuery(id+"F42.opRevolve","SWEPT_FACE",FACE,{"disambiguationData":[OSD([subQ5])]});var subQ7=sQuery(id+"F41.wireOp",EDGE,"E36");var subQ8=makeQuery(id+"F42.opRevolve","SWEPT_FACE",FACE,{"disambiguationData":[OSD([subQ7])]});var subQ9=makeQuery(id+"F42.opRevolve","SWEPT_EDGE",EDGE,{"disambiguationData":[OSD([subQ5,subQ7])]});var subQ10=sQuery(id+"F4.wireOp",EDGE,"E26.2.3");var subQ11=sQuery(id+"F4.wireOp",EDGE,"E26.2.2");var subQ12=sQuery(id+"F3.wireOp",EDGE,"E20.2.3");var subQ13=sQuery(id+"F3.wireOp",EDGE,"E20.2.1");var subQ14=sQuery(id+"F4.wireOp",EDGE,"E26.3.3");var subQ15=sQuery(id+"F4.wireOp",EDGE,"E26.3.2");var subQ16=sQuery(id+"F3.wireOp",EDGE,"E20.3.3");var subQ17=sQuery(id+"F3.wireOp",EDGE,"E20.3.1");var subQ18=sQuery(id+"F4.wireOp",EDGE,"E26.4.3");var subQ19=sQuery(id+"F4.wireOp",EDGE,"E26.4.2");var subQ20=sQuery(id+"F3.wireOp",EDGE,"E20.4.3");var subQ21=sQuery(id+"F3.wireOp",EDGE,"E20.4.1");var subQ22=sQuery(id+"F4.wireOp",EDGE,"E26.5.3");var subQ23=sQuery(id+"F4.wireOp",EDGE,"E26.5.2");var subQ24=sQuery(id+"F3.wireOp",EDGE,"E20.5.3");var subQ25=sQuery(id+"F3.wireOp",EDGE,"E20.5.1");var subQ26=sQuery(id+"F4.wireOp",EDGE,"E26.6.3");var subQ27=sQuery(id+"F4.wireOp",EDGE,"E26.6.2");var subQ28=sQuery(id+"F3.wireOp",EDGE,"E20.6.3");var subQ29=sQuery(id+"F3.wireOp",EDGE,"E20.6.1");var subQ30=sQuery(id+"F4.wireOp",EDGE,"E26.7.3");var subQ31=sQuery(id+"F4.wireOp",EDGE,"E26.7.2");var subQ32=sQuery(id+"F3.wireOp",EDGE,"E20.7.3");var subQ33=sQuery(id+"F3.wireOp",EDGE,"E20.7.1");var subQ34=sQuery(id+"F4.wireOp",EDGE,"E26.8.3");var subQ35=sQuery(id+"F4.wireOp",EDGE,"E26.8.2");var subQ36=sQuery(id+"F3.wireOp",EDGE,"E20.8.3");var subQ37=sQuery(id+"F3.wireOp",EDGE,"E20.8.1");var subQ38=sQuery(id+"F4.wireOp",EDGE,"E26.9.3");var subQ39=sQuery(id+"F4.wireOp",EDGE,"E26.9.2");var subQ40=sQuery(id+"F3.wireOp",EDGE,"E20.9.3");var subQ41=sQuery(id+"F3.wireOp",EDGE,"E20.9.1");var subQ42=sQuery(id+"F4.wireOp",EDGE,"E26.10.3");var subQ43=sQuery(id+"F4.wireOp",EDGE,"E26.10.2");var subQ44=sQuery(id+"F3.wireOp",EDGE,"E20.10.3");var subQ45=sQuery(id+"F3.wireOp",EDGE,"E20.10.1");var subQ46=sQuery(id+"F4.wireOp",EDGE,"E26.11.3");var subQ47=sQuery(id+"F4.wireOp",EDGE,"E26.11.2");var subQ48=sQuery(id+"F3.wireOp",EDGE,"E20.11.3");var subQ49=sQuery(id+"F3.wireOp",EDGE,"E20.11.1");var subQ50=sQuery(id+"F4.wireOp",EDGE,"E26.12.3");var subQ51=sQuery(id+"F4.wireOp",EDGE,"E26.12.2");var subQ52=sQuery(id+"F3.wireOp",EDGE,"E20.12.3");var subQ53=sQuery(id+"F3.wireOp",EDGE,"E20.12.1");var subQ54=sQuery(id+"F4.wireOp",EDGE,"E26.13.3");var subQ55=sQuery(id+"F4.wireOp",EDGE,"E26.13.2");var subQ56=sQuery(id+"F3.wireOp",EDGE,"E20.13.3");var subQ57=sQuery(id+"F3.wireOp",EDGE,"E20.13.1");var subQ58=sQuery(id+"F4.wireOp",EDGE,"E26.14.3");var subQ59=sQuery(id+"F4.wireOp",EDGE,"E26.14.2");var subQ60=sQuery(id+"F3.wireOp",EDGE,"E20.14.3");var subQ61=sQuery(id+"F3.wireOp",EDGE,"E20.14.1");var subQ63=makeQuery(id+"F7.opLoft","SWEPT_FACE",FACE,{"disambiguationData":[OSD([sQuery(id+"F3.wireOp",EDGE,"E20.14.0"),subQ61,subQ60,sQuery(id+"F4.wireOp",EDGE,"E26.14.0"),subQ59,subQ58])]});var subQ64=sQuery(id+"F4.wireOp",EDGE,"E26.15.3");var subQ65=sQuery(id+"F4.wireOp",EDGE,"E26.15.2");var subQ66=sQuery(id+"F3.wireOp",EDGE,"E20.15.3");var subQ67=sQuery(id+"F3.wireOp",EDGE,"E20.15.1");var subQ68=sQuery(id+"F4.wireOp",EDGE,"E23");var subQ69=sQuery(id+"F4.wireOp",EDGE,"E22");var subQ70=sQuery(id+"F3.wireOp",EDGE,"E18.top");var subQ71=sQuery(id+"F3.wireOp",EDGE,"E18.bottom");var subQ74=makeQuery(id+"F42.boolean.opBoolean","COPY",FACE,{"disambiguationData":[TD([subQ63])],"derivedFrom":subQ6});var subQ75=makeQuery(id+"F7.boolean.opBoolean","INTERSECT",EDGE,{"derivedFrom":[makeQuery(id+"F1.opRevolve","SWEPT_FACE",FACE,{"disambiguationData":[OSD([sQuery(id+"F0.wireOp",EDGE,"E13")])]}),subQ63]});Q56=makeQuery(id+"F48.opFillet","BLEND_EDGE",EDGE,{"blendedFrom":[makeQuery(id+"F47.opFillet","TWEAK_EDGE",EDGE,{"derivedFrom":[makeQuery(id+"F45.opFillet","BLEND_VERTEX",VERTEX,{"blendedFrom":[subQ75,subQ63,subQ74],"blendedInto":[subQ63,subQ74]}),makeQuery(id+"F45.opFillet","BLEND_VERTEX",VERTEX,{"blendedFrom":[subQ75,makeQuery(id+"F42.boolean.opBoolean","MERGE",FACE,{"derivedFrom":[subQ0,subQ8]}),subQ74],"blendedInto":[makeQuery(id+"F42.boolean.opBoolean","MERGE",FACE,{"derivedFrom":[subQ0,subQ8]}),subQ74]})]}),makeQuery(id+"F47.opFillet","BLEND_FACE",FACE,{"disambiguationData":[OSD([subQ5,subQ7]),TDD([makeQuery(id+"F42.boolean.opBoolean","COPY",EDGE,{"disambiguationData":[TD([makeQuery(id+"F5.opLoft","SWEPT_FACE",FACE,{"disambiguationData":[OSD([subQ71,subQ70,sQuery(id+"F3.wireOp",EDGE,"E18.left"),sQuery(id+"F4.wireOp",EDGE,"E21"),subQ69,subQ68])]})])],"derivedFrom":subQ9})])]}),makeQuery(id+"F47.opFillet","BLEND_FACE",FACE,{"disambiguationData":[OSD([subQ5,subQ7]),TDD([makeQuery(id+"F42.boolean.opBoolean","COPY",EDGE,{"disambiguationData":[TD([makeQuery(id+"F6.opLoft","SWEPT_FACE",FACE,{"disambiguationData":[OSD([sQuery(id+"F3.wireOp",EDGE,"E20.15.0"),subQ67,subQ66,sQuery(id+"F4.wireOp",EDGE,"E26.15.0"),subQ65,subQ64])]})])],"derivedFrom":subQ9})])]}),makeQuery(id+"F47.opFillet","BLEND_FACE",FACE,{"disambiguationData":[OSD([subQ5,subQ7]),TDD([makeQuery(id+"F42.boolean.opBoolean","COPY",EDGE,{"disambiguationData":[TD([subQ63])],"derivedFrom":subQ9})])]}),makeQuery(id+"F47.opFillet","BLEND_FACE",FACE,{"disambiguationData":[OSD([subQ5,subQ7]),TDD([makeQuery(id+"F42.boolean.opBoolean","COPY",EDGE,{"disambiguationData":[TD([makeQuery(id+"F8.opLoft","SWEPT_FACE",FACE,{"disambiguationData":[OSD([sQuery(id+"F3.wireOp",EDGE,"E20.13.0"),subQ57,subQ56,sQuery(id+"F4.wireOp",EDGE,"E26.13.0"),subQ55,subQ54])]})])],"derivedFrom":subQ9})])]}),makeQuery(id+"F47.opFillet","BLEND_FACE",FACE,{"disambiguationData":[OSD([subQ5,subQ7]),TDD([makeQuery(id+"F42.boolean.opBoolean","COPY",EDGE,{"disambiguationData":[TD([makeQuery(id+"F9.opLoft","SWEPT_FACE",FACE,{"disambiguationData":[OSD([sQuery(id+"F3.wireOp",EDGE,"E20.12.0"),subQ53,subQ52,sQuery(id+"F4.wireOp",EDGE,"E26.12.0"),subQ51,subQ50])]})])],"derivedFrom":subQ9})])]}),makeQuery(id+"F47.opFillet","BLEND_FACE",FACE,{"disambiguationData":[OSD([subQ5,subQ7]),TDD([makeQuery(id+"F42.boolean.opBoolean","COPY",EDGE,{"disambiguationData":[TD([makeQuery(id+"F10.opLoft","SWEPT_FACE",FACE,{"disambiguationData":[OSD([sQuery(id+"F3.wireOp",EDGE,"E20.11.0"),subQ49,subQ48,sQuery(id+"F4.wireOp",EDGE,"E26.11.0"),subQ47,subQ46])]})])],"derivedFrom":subQ9})])]}),makeQuery(id+"F47.opFillet","BLEND_FACE",FACE,{"disambiguationData":[OSD([subQ5,subQ7]),TDD([makeQuery(id+"F42.boolean.opBoolean","COPY",EDGE,{"disambiguationData":[TD([makeQuery(id+"F11.opLoft","SWEPT_FACE",FACE,{"disambiguationData":[OSD([sQuery(id+"F3.wireOp",EDGE,"E20.10.0"),subQ45,subQ44,sQuery(id+"F4.wireOp",EDGE,"E26.10.0"),subQ43,subQ42])]})])],"derivedFrom":subQ9})])]}),makeQuery(id+"F47.opFillet","BLEND_FACE",FACE,{"disambiguationData":[OSD([subQ5,subQ7]),TDD([makeQuery(id+"F42.boolean.opBoolean","COPY",EDGE,{"disambiguationData":[TD([makeQuery(id+"F12.opLoft","SWEPT_FACE",FACE,{"disambiguationData":[OSD([sQuery(id+"F3.wireOp",EDGE,"E20.9.0"),subQ41,subQ40,sQuery(id+"F4.wireOp",EDGE,"E26.9.0"),subQ39,subQ38])]})])],"derivedFrom":subQ9})])]}),makeQuery(id+"F47.opFillet","BLEND_FACE",FACE,{"disambiguationData":[OSD([subQ5,subQ7]),TDD([makeQuery(id+"F42.boolean.opBoolean","COPY",EDGE,{"disambiguationData":[TD([makeQuery(id+"F13.opLoft","SWEPT_FACE",FACE,{"disambiguationData":[OSD([sQuery(id+"F3.wireOp",EDGE,"E20.8.0"),subQ37,subQ36,sQuery(id+"F4.wireOp",EDGE,"E26.8.0"),subQ35,subQ34])]})])],"derivedFrom":subQ9})])]}),makeQuery(id+"F47.opFillet","BLEND_FACE",FACE,{"disambiguationData":[OSD([subQ5,subQ7]),TDD([makeQuery(id+"F42.boolean.opBoolean","COPY",EDGE,{"disambiguationData":[TD([makeQuery(id+"F14.opLoft","SWEPT_FACE",FACE,{"disambiguationData":[OSD([sQuery(id+"F3.wireOp",EDGE,"E20.7.0"),subQ33,subQ32,sQuery(id+"F4.wireOp",EDGE,"E26.7.0"),subQ31,subQ30])]})])],"derivedFrom":subQ9})])]}),makeQuery(id+"F47.opFillet","BLEND_FACE",FACE,{"disambiguationData":[OSD([subQ5,subQ7]),TDD([makeQuery(id+"F42.boolean.opBoolean","COPY",EDGE,{"disambiguationData":[TD([makeQuery(id+"F15.opLoft","SWEPT_FACE",FACE,{"disambiguationData":[OSD([sQuery(id+"F3.wireOp",EDGE,"E20.6.0"),subQ29,subQ28,sQuery(id+"F4.wireOp",EDGE,"E26.6.0"),subQ27,subQ26])]})])],"derivedFrom":subQ9})])]}),makeQuery(id+"F47.opFillet","BLEND_FACE",FACE,{"disambiguationData":[OSD([subQ5,subQ7]),TDD([makeQuery(id+"F42.boolean.opBoolean","COPY",EDGE,{"disambiguationData":[TD([makeQuery(id+"F16.opLoft","SWEPT_FACE",FACE,{"disambiguationData":[OSD([sQuery(id+"F3.wireOp",EDGE,"E20.5.0"),subQ25,subQ24,sQuery(id+"F4.wireOp",EDGE,"E26.5.0"),subQ23,subQ22])]})])],"derivedFrom":subQ9})])]}),makeQuery(id+"F47.opFillet","BLEND_FACE",FACE,{"disambiguationData":[OSD([subQ5,subQ7]),TDD([makeQuery(id+"F42.boolean.opBoolean","COPY",EDGE,{"disambiguationData":[TD([makeQuery(id+"F17.opLoft","SWEPT_FACE",FACE,{"disambiguationData":[OSD([sQuery(id+"F3.wireOp",EDGE,"E20.4.0"),subQ21,subQ20,sQuery(id+"F4.wireOp",EDGE,"E26.4.0"),subQ19,subQ18])]})])],"derivedFrom":subQ9})])]}),makeQuery(id+"F47.opFillet","BLEND_FACE",FACE,{"disambiguationData":[OSD([subQ5,subQ7]),TDD([makeQuery(id+"F42.boolean.opBoolean","COPY",EDGE,{"disambiguationData":[TD([makeQuery(id+"F18.opLoft","SWEPT_FACE",FACE,{"disambiguationData":[OSD([sQuery(id+"F3.wireOp",EDGE,"E20.3.0"),subQ17,subQ16,sQuery(id+"F4.wireOp",EDGE,"E26.3.0"),subQ15,subQ14])]})])],"derivedFrom":subQ9})])]}),makeQuery(id+"F47.opFillet","BLEND_FACE",FACE,{"disambiguationData":[OSD([subQ5,subQ7]),TDD([makeQuery(id+"F42.boolean.opBoolean","COPY",EDGE,{"disambiguationData":[TD([makeQuery(id+"F19.opLoft","SWEPT_FACE",FACE,{"disambiguationData":[OSD([sQuery(id+"F3.wireOp",EDGE,"E20.2.0"),subQ13,subQ12,sQuery(id+"F4.wireOp",EDGE,"E26.2.0"),subQ11,subQ10])]})])],"derivedFrom":subQ9})])]}),makeQuery(id+"F47.opFillet","BLEND_FACE",FACE,{"disambiguationData":[OSD([subQ5,subQ7]),TDD([makeQuery(id+"F42.boolean.opBoolean","COPY",EDGE,{"disambiguationData":[TD([makeQuery(id+"F20.opLoft","SWEPT_FACE",FACE,{"disambiguationData":[OSD([sQuery(id+"F3.wireOp",EDGE,"E20.1.0"),subQ4,subQ3,sQuery(id+"F4.wireOp",EDGE,"E26.1.0"),subQ2,subQ1])]})])],"derivedFrom":subQ9})])]})],"blendedInto":[makeQuery(id+"F47.opFillet","BLEND_FACE",FACE,{"disambiguationData":[OSD([subQ5,subQ7]),TDD([makeQuery(id+"F42.boolean.opBoolean","COPY",EDGE,{"disambiguationData":[TD([makeQuery(id+"F5.opLoft","SWEPT_FACE",FACE,{"disambiguationData":[OSD([subQ71,subQ70,sQuery(id+"F3.wireOp",EDGE,"E18.left"),sQuery(id+"F4.wireOp",EDGE,"E21"),subQ69,subQ68])]})])],"derivedFrom":subQ9})])]}),makeQuery(id+"F47.opFillet","BLEND_FACE",FACE,{"disambiguationData":[OSD([subQ5,subQ7]),TDD([makeQuery(id+"F42.boolean.opBoolean","COPY",EDGE,{"disambiguationData":[TD([makeQuery(id+"F6.opLoft","SWEPT_FACE",FACE,{"disambiguationData":[OSD([sQuery(id+"F3.wireOp",EDGE,"E20.15.0"),subQ67,subQ66,sQuery(id+"F4.wireOp",EDGE,"E26.15.0"),subQ65,subQ64])]})])],"derivedFrom":subQ9})])]}),makeQuery(id+"F47.opFillet","BLEND_FACE",FACE,{"disambiguationData":[OSD([subQ5,subQ7]),TDD([makeQuery(id+"F42.boolean.opBoolean","COPY",EDGE,{"disambiguationData":[TD([subQ63])],"derivedFrom":subQ9})])]}),makeQuery(id+"F47.opFillet","BLEND_FACE",FACE,{"disambiguationData":[OSD([subQ5,subQ7]),TDD([makeQuery(id+"F42.boolean.opBoolean","COPY",EDGE,{"disambiguationData":[TD([makeQuery(id+"F8.opLoft","SWEPT_FACE",FACE,{"disambiguationData":[OSD([sQuery(id+"F3.wireOp",EDGE,"E20.13.0"),subQ57,subQ56,sQuery(id+"F4.wireOp",EDGE,"E26.13.0"),subQ55,subQ54])]})])],"derivedFrom":subQ9})])]}),makeQuery(id+"F47.opFillet","BLEND_FACE",FACE,{"disambiguationData":[OSD([subQ5,subQ7]),TDD([makeQuery(id+"F42.boolean.opBoolean","COPY",EDGE,{"disambiguationData":[TD([makeQuery(id+"F9.opLoft","SWEPT_FACE",FACE,{"disambiguationData":[OSD([sQuery(id+"F3.wireOp",EDGE,"E20.12.0"),subQ53,subQ52,sQuery(id+"F4.wireOp",EDGE,"E26.12.0"),subQ51,subQ50])]})])],"derivedFrom":subQ9})])]}),makeQuery(id+"F47.opFillet","BLEND_FACE",FACE,{"disambiguationData":[OSD([subQ5,subQ7]),TDD([makeQuery(id+"F42.boolean.opBoolean","COPY",EDGE,{"disambiguationData":[TD([makeQuery(id+"F10.opLoft","SWEPT_FACE",FACE,{"disambiguationData":[OSD([sQuery(id+"F3.wireOp",EDGE,"E20.11.0"),subQ49,subQ48,sQuery(id+"F4.wireOp",EDGE,"E26.11.0"),subQ47,subQ46])]})])],"derivedFrom":subQ9})])]}),makeQuery(id+"F47.opFillet","BLEND_FACE",FACE,{"disambiguationData":[OSD([subQ5,subQ7]),TDD([makeQuery(id+"F42.boolean.opBoolean","COPY",EDGE,{"disambiguationData":[TD([makeQuery(id+"F11.opLoft","SWEPT_FACE",FACE,{"disambiguationData":[OSD([sQuery(id+"F3.wireOp",EDGE,"E20.10.0"),subQ45,subQ44,sQuery(id+"F4.wireOp",EDGE,"E26.10.0"),subQ43,subQ42])]})])],"derivedFrom":subQ9})])]}),makeQuery(id+"F47.opFillet","BLEND_FACE",FACE,{"disambiguationData":[OSD([subQ5,subQ7]),TDD([makeQuery(id+"F42.boolean.opBoolean","COPY",EDGE,{"disambiguationData":[TD([makeQuery(id+"F12.opLoft","SWEPT_FACE",FACE,{"disambiguationData":[OSD([sQuery(id+"F3.wireOp",EDGE,"E20.9.0"),subQ41,subQ40,sQuery(id+"F4.wireOp",EDGE,"E26.9.0"),subQ39,subQ38])]})])],"derivedFrom":subQ9})])]}),makeQuery(id+"F47.opFillet","BLEND_FACE",FACE,{"disambiguationData":[OSD([subQ5,subQ7]),TDD([makeQuery(id+"F42.boolean.opBoolean","COPY",EDGE,{"disambiguationData":[TD([makeQuery(id+"F13.opLoft","SWEPT_FACE",FACE,{"disambiguationData":[OSD([sQuery(id+"F3.wireOp",EDGE,"E20.8.0"),subQ37,subQ36,sQuery(id+"F4.wireOp",EDGE,"E26.8.0"),subQ35,subQ34])]})])],"derivedFrom":subQ9})])]}),makeQuery(id+"F47.opFillet","BLEND_FACE",FACE,{"disambiguationData":[OSD([subQ5,subQ7]),TDD([makeQuery(id+"F42.boolean.opBoolean","COPY",EDGE,{"disambiguationData":[TD([makeQuery(id+"F14.opLoft","SWEPT_FACE",FACE,{"disambiguationData":[OSD([sQuery(id+"F3.wireOp",EDGE,"E20.7.0"),subQ33,subQ32,sQuery(id+"F4.wireOp",EDGE,"E26.7.0"),subQ31,subQ30])]})])],"derivedFrom":subQ9})])]}),makeQuery(id+"F47.opFillet","BLEND_FACE",FACE,{"disambiguationData":[OSD([subQ5,subQ7]),TDD([makeQuery(id+"F42.boolean.opBoolean","COPY",EDGE,{"disambiguationData":[TD([makeQuery(id+"F15.opLoft","SWEPT_FACE",FACE,{"disambiguationData":[OSD([sQuery(id+"F3.wireOp",EDGE,"E20.6.0"),subQ29,subQ28,sQuery(id+"F4.wireOp",EDGE,"E26.6.0"),subQ27,subQ26])]})])],"derivedFrom":subQ9})])]}),makeQuery(id+"F47.opFillet","BLEND_FACE",FACE,{"disambiguationData":[OSD([subQ5,subQ7]),TDD([makeQuery(id+"F42.boolean.opBoolean","COPY",EDGE,{"disambiguationData":[TD([makeQuery(id+"F16.opLoft","SWEPT_FACE",FACE,{"disambiguationData":[OSD([sQuery(id+"F3.wireOp",EDGE,"E20.5.0"),subQ25,subQ24,sQuery(id+"F4.wireOp",EDGE,"E26.5.0"),subQ23,subQ22])]})])],"derivedFrom":subQ9})])]}),makeQuery(id+"F47.opFillet","BLEND_FACE",FACE,{"disambiguationData":[OSD([subQ5,subQ7]),TDD([makeQuery(id+"F42.boolean.opBoolean","COPY",EDGE,{"disambiguationData":[TD([makeQuery(id+"F17.opLoft","SWEPT_FACE",FACE,{"disambiguationData":[OSD([sQuery(id+"F3.wireOp",EDGE,"E20.4.0"),subQ21,subQ20,sQuery(id+"F4.wireOp",EDGE,"E26.4.0"),subQ19,subQ18])]})])],"derivedFrom":subQ9})])]}),makeQuery(id+"F47.opFillet","BLEND_FACE",FACE,{"disambiguationData":[OSD([subQ5,subQ7]),TDD([makeQuery(id+"F42.boolean.opBoolean","COPY",EDGE,{"disambiguationData":[TD([makeQuery(id+"F18.opLoft","SWEPT_FACE",FACE,{"disambiguationData":[OSD([sQuery(id+"F3.wireOp",EDGE,"E20.3.0"),subQ17,subQ16,sQuery(id+"F4.wireOp",EDGE,"E26.3.0"),subQ15,subQ14])]})])],"derivedFrom":subQ9})])]}),makeQuery(id+"F47.opFillet","BLEND_FACE",FACE,{"disambiguationData":[OSD([subQ5,subQ7]),TDD([makeQuery(id+"F42.boolean.opBoolean","COPY",EDGE,{"disambiguationData":[TD([makeQuery(id+"F19.opLoft","SWEPT_FACE",FACE,{"disambiguationData":[OSD([sQuery(id+"F3.wireOp",EDGE,"E20.2.0"),subQ13,subQ12,sQuery(id+"F4.wireOp",EDGE,"E26.2.0"),subQ11,subQ10])]})])],"derivedFrom":subQ9})])]}),makeQuery(id+"F47.opFillet","BLEND_FACE",FACE,{"disambiguationData":[OSD([subQ5,subQ7]),TDD([makeQuery(id+"F42.boolean.opBoolean","COPY",EDGE,{"disambiguationData":[TD([makeQuery(id+"F20.opLoft","SWEPT_FACE",FACE,{"disambiguationData":[OSD([sQuery(id+"F3.wireOp",EDGE,"E20.1.0"),subQ4,subQ3,sQuery(id+"F4.wireOp",EDGE,"E26.1.0"),subQ2,subQ1])]})])],"derivedFrom":subQ9})])]})]});}
            var Q57;
            {var subQ0=makeQuery(id+"F40.opExtrude","CAP_FACE",FACE,{"disambiguationData":[OSD([sQuery(id+"F39.wireOp",EDGE,"E29"),sQuery(id+"F39.wireOp",EDGE,"E30")])],"isStart":false});var subQ1=sQuery(id+"F4.wireOp",EDGE,"E26.1.3");var subQ2=sQuery(id+"F4.wireOp",EDGE,"E26.1.2");var subQ3=sQuery(id+"F3.wireOp",EDGE,"E20.1.3");var subQ4=sQuery(id+"F3.wireOp",EDGE,"E20.1.1");var subQ5=sQuery(id+"F41.wireOp",EDGE,"E35");var subQ6=makeQuery(id+"F42.opRevolve","SWEPT_FACE",FACE,{"disambiguationData":[OSD([subQ5])]});var subQ7=sQuery(id+"F41.wireOp",EDGE,"E36");var subQ8=makeQuery(id+"F42.opRevolve","SWEPT_FACE",FACE,{"disambiguationData":[OSD([subQ7])]});var subQ9=makeQuery(id+"F42.opRevolve","SWEPT_EDGE",EDGE,{"disambiguationData":[OSD([subQ5,subQ7])]});var subQ10=sQuery(id+"F4.wireOp",EDGE,"E26.2.3");var subQ11=sQuery(id+"F4.wireOp",EDGE,"E26.2.2");var subQ12=sQuery(id+"F3.wireOp",EDGE,"E20.2.3");var subQ13=sQuery(id+"F3.wireOp",EDGE,"E20.2.1");var subQ14=sQuery(id+"F4.wireOp",EDGE,"E26.3.3");var subQ15=sQuery(id+"F4.wireOp",EDGE,"E26.3.2");var subQ16=sQuery(id+"F3.wireOp",EDGE,"E20.3.3");var subQ17=sQuery(id+"F3.wireOp",EDGE,"E20.3.1");var subQ18=sQuery(id+"F4.wireOp",EDGE,"E26.4.3");var subQ19=sQuery(id+"F4.wireOp",EDGE,"E26.4.2");var subQ20=sQuery(id+"F3.wireOp",EDGE,"E20.4.3");var subQ21=sQuery(id+"F3.wireOp",EDGE,"E20.4.1");var subQ22=sQuery(id+"F4.wireOp",EDGE,"E26.5.3");var subQ23=sQuery(id+"F4.wireOp",EDGE,"E26.5.2");var subQ24=sQuery(id+"F3.wireOp",EDGE,"E20.5.3");var subQ25=sQuery(id+"F3.wireOp",EDGE,"E20.5.1");var subQ26=sQuery(id+"F4.wireOp",EDGE,"E26.6.3");var subQ27=sQuery(id+"F4.wireOp",EDGE,"E26.6.2");var subQ28=sQuery(id+"F3.wireOp",EDGE,"E20.6.3");var subQ29=sQuery(id+"F3.wireOp",EDGE,"E20.6.1");var subQ30=sQuery(id+"F4.wireOp",EDGE,"E26.7.3");var subQ31=sQuery(id+"F4.wireOp",EDGE,"E26.7.2");var subQ32=sQuery(id+"F3.wireOp",EDGE,"E20.7.3");var subQ33=sQuery(id+"F3.wireOp",EDGE,"E20.7.1");var subQ34=sQuery(id+"F4.wireOp",EDGE,"E26.8.3");var subQ35=sQuery(id+"F4.wireOp",EDGE,"E26.8.2");var subQ36=sQuery(id+"F3.wireOp",EDGE,"E20.8.3");var subQ37=sQuery(id+"F3.wireOp",EDGE,"E20.8.1");var subQ38=sQuery(id+"F4.wireOp",EDGE,"E26.9.3");var subQ39=sQuery(id+"F4.wireOp",EDGE,"E26.9.2");var subQ40=sQuery(id+"F3.wireOp",EDGE,"E20.9.3");var subQ41=sQuery(id+"F3.wireOp",EDGE,"E20.9.1");var subQ42=sQuery(id+"F4.wireOp",EDGE,"E26.10.3");var subQ43=sQuery(id+"F4.wireOp",EDGE,"E26.10.2");var subQ44=sQuery(id+"F3.wireOp",EDGE,"E20.10.3");var subQ45=sQuery(id+"F3.wireOp",EDGE,"E20.10.1");var subQ46=sQuery(id+"F4.wireOp",EDGE,"E26.11.3");var subQ47=sQuery(id+"F4.wireOp",EDGE,"E26.11.2");var subQ48=sQuery(id+"F3.wireOp",EDGE,"E20.11.3");var subQ49=sQuery(id+"F3.wireOp",EDGE,"E20.11.1");var subQ50=sQuery(id+"F4.wireOp",EDGE,"E26.12.3");var subQ51=sQuery(id+"F4.wireOp",EDGE,"E26.12.2");var subQ52=sQuery(id+"F3.wireOp",EDGE,"E20.12.3");var subQ53=sQuery(id+"F3.wireOp",EDGE,"E20.12.1");var subQ54=sQuery(id+"F4.wireOp",EDGE,"E26.13.3");var subQ55=sQuery(id+"F4.wireOp",EDGE,"E26.13.2");var subQ56=sQuery(id+"F3.wireOp",EDGE,"E20.13.3");var subQ57=sQuery(id+"F3.wireOp",EDGE,"E20.13.1");var subQ59=makeQuery(id+"F8.opLoft","SWEPT_FACE",FACE,{"disambiguationData":[OSD([sQuery(id+"F3.wireOp",EDGE,"E20.13.0"),subQ57,subQ56,sQuery(id+"F4.wireOp",EDGE,"E26.13.0"),subQ55,subQ54])]});var subQ60=sQuery(id+"F4.wireOp",EDGE,"E26.14.3");var subQ61=sQuery(id+"F4.wireOp",EDGE,"E26.14.2");var subQ62=sQuery(id+"F3.wireOp",EDGE,"E20.14.3");var subQ63=sQuery(id+"F3.wireOp",EDGE,"E20.14.1");var subQ64=sQuery(id+"F4.wireOp",EDGE,"E26.15.3");var subQ65=sQuery(id+"F4.wireOp",EDGE,"E26.15.2");var subQ66=sQuery(id+"F3.wireOp",EDGE,"E20.15.3");var subQ67=sQuery(id+"F3.wireOp",EDGE,"E20.15.1");var subQ68=sQuery(id+"F4.wireOp",EDGE,"E23");var subQ69=sQuery(id+"F4.wireOp",EDGE,"E22");var subQ70=sQuery(id+"F3.wireOp",EDGE,"E18.top");var subQ71=sQuery(id+"F3.wireOp",EDGE,"E18.bottom");var subQ74=makeQuery(id+"F42.boolean.opBoolean","COPY",FACE,{"disambiguationData":[TD([subQ59])],"derivedFrom":subQ6});var subQ75=makeQuery(id+"F8.boolean.opBoolean","INTERSECT",EDGE,{"derivedFrom":[makeQuery(id+"F1.opRevolve","SWEPT_FACE",FACE,{"disambiguationData":[OSD([sQuery(id+"F0.wireOp",EDGE,"E13")])]}),subQ59]});Q57=makeQuery(id+"F48.opFillet","BLEND_EDGE",EDGE,{"blendedFrom":[makeQuery(id+"F47.opFillet","TWEAK_EDGE",EDGE,{"derivedFrom":[makeQuery(id+"F45.opFillet","BLEND_VERTEX",VERTEX,{"blendedFrom":[subQ75,subQ59,subQ74],"blendedInto":[subQ59,subQ74]}),makeQuery(id+"F45.opFillet","BLEND_VERTEX",VERTEX,{"blendedFrom":[subQ75,makeQuery(id+"F42.boolean.opBoolean","MERGE",FACE,{"derivedFrom":[subQ0,subQ8]}),subQ74],"blendedInto":[makeQuery(id+"F42.boolean.opBoolean","MERGE",FACE,{"derivedFrom":[subQ0,subQ8]}),subQ74]})]}),makeQuery(id+"F47.opFillet","BLEND_FACE",FACE,{"disambiguationData":[OSD([subQ5,subQ7]),TDD([makeQuery(id+"F42.boolean.opBoolean","COPY",EDGE,{"disambiguationData":[TD([makeQuery(id+"F5.opLoft","SWEPT_FACE",FACE,{"disambiguationData":[OSD([subQ71,subQ70,sQuery(id+"F3.wireOp",EDGE,"E18.left"),sQuery(id+"F4.wireOp",EDGE,"E21"),subQ69,subQ68])]})])],"derivedFrom":subQ9})])]}),makeQuery(id+"F47.opFillet","BLEND_FACE",FACE,{"disambiguationData":[OSD([subQ5,subQ7]),TDD([makeQuery(id+"F42.boolean.opBoolean","COPY",EDGE,{"disambiguationData":[TD([makeQuery(id+"F6.opLoft","SWEPT_FACE",FACE,{"disambiguationData":[OSD([sQuery(id+"F3.wireOp",EDGE,"E20.15.0"),subQ67,subQ66,sQuery(id+"F4.wireOp",EDGE,"E26.15.0"),subQ65,subQ64])]})])],"derivedFrom":subQ9})])]}),makeQuery(id+"F47.opFillet","BLEND_FACE",FACE,{"disambiguationData":[OSD([subQ5,subQ7]),TDD([makeQuery(id+"F42.boolean.opBoolean","COPY",EDGE,{"disambiguationData":[TD([makeQuery(id+"F7.opLoft","SWEPT_FACE",FACE,{"disambiguationData":[OSD([sQuery(id+"F3.wireOp",EDGE,"E20.14.0"),subQ63,subQ62,sQuery(id+"F4.wireOp",EDGE,"E26.14.0"),subQ61,subQ60])]})])],"derivedFrom":subQ9})])]}),makeQuery(id+"F47.opFillet","BLEND_FACE",FACE,{"disambiguationData":[OSD([subQ5,subQ7]),TDD([makeQuery(id+"F42.boolean.opBoolean","COPY",EDGE,{"disambiguationData":[TD([subQ59])],"derivedFrom":subQ9})])]}),makeQuery(id+"F47.opFillet","BLEND_FACE",FACE,{"disambiguationData":[OSD([subQ5,subQ7]),TDD([makeQuery(id+"F42.boolean.opBoolean","COPY",EDGE,{"disambiguationData":[TD([makeQuery(id+"F9.opLoft","SWEPT_FACE",FACE,{"disambiguationData":[OSD([sQuery(id+"F3.wireOp",EDGE,"E20.12.0"),subQ53,subQ52,sQuery(id+"F4.wireOp",EDGE,"E26.12.0"),subQ51,subQ50])]})])],"derivedFrom":subQ9})])]}),makeQuery(id+"F47.opFillet","BLEND_FACE",FACE,{"disambiguationData":[OSD([subQ5,subQ7]),TDD([makeQuery(id+"F42.boolean.opBoolean","COPY",EDGE,{"disambiguationData":[TD([makeQuery(id+"F10.opLoft","SWEPT_FACE",FACE,{"disambiguationData":[OSD([sQuery(id+"F3.wireOp",EDGE,"E20.11.0"),subQ49,subQ48,sQuery(id+"F4.wireOp",EDGE,"E26.11.0"),subQ47,subQ46])]})])],"derivedFrom":subQ9})])]}),makeQuery(id+"F47.opFillet","BLEND_FACE",FACE,{"disambiguationData":[OSD([subQ5,subQ7]),TDD([makeQuery(id+"F42.boolean.opBoolean","COPY",EDGE,{"disambiguationData":[TD([makeQuery(id+"F11.opLoft","SWEPT_FACE",FACE,{"disambiguationData":[OSD([sQuery(id+"F3.wireOp",EDGE,"E20.10.0"),subQ45,subQ44,sQuery(id+"F4.wireOp",EDGE,"E26.10.0"),subQ43,subQ42])]})])],"derivedFrom":subQ9})])]}),makeQuery(id+"F47.opFillet","BLEND_FACE",FACE,{"disambiguationData":[OSD([subQ5,subQ7]),TDD([makeQuery(id+"F42.boolean.opBoolean","COPY",EDGE,{"disambiguationData":[TD([makeQuery(id+"F12.opLoft","SWEPT_FACE",FACE,{"disambiguationData":[OSD([sQuery(id+"F3.wireOp",EDGE,"E20.9.0"),subQ41,subQ40,sQuery(id+"F4.wireOp",EDGE,"E26.9.0"),subQ39,subQ38])]})])],"derivedFrom":subQ9})])]}),makeQuery(id+"F47.opFillet","BLEND_FACE",FACE,{"disambiguationData":[OSD([subQ5,subQ7]),TDD([makeQuery(id+"F42.boolean.opBoolean","COPY",EDGE,{"disambiguationData":[TD([makeQuery(id+"F13.opLoft","SWEPT_FACE",FACE,{"disambiguationData":[OSD([sQuery(id+"F3.wireOp",EDGE,"E20.8.0"),subQ37,subQ36,sQuery(id+"F4.wireOp",EDGE,"E26.8.0"),subQ35,subQ34])]})])],"derivedFrom":subQ9})])]}),makeQuery(id+"F47.opFillet","BLEND_FACE",FACE,{"disambiguationData":[OSD([subQ5,subQ7]),TDD([makeQuery(id+"F42.boolean.opBoolean","COPY",EDGE,{"disambiguationData":[TD([makeQuery(id+"F14.opLoft","SWEPT_FACE",FACE,{"disambiguationData":[OSD([sQuery(id+"F3.wireOp",EDGE,"E20.7.0"),subQ33,subQ32,sQuery(id+"F4.wireOp",EDGE,"E26.7.0"),subQ31,subQ30])]})])],"derivedFrom":subQ9})])]}),makeQuery(id+"F47.opFillet","BLEND_FACE",FACE,{"disambiguationData":[OSD([subQ5,subQ7]),TDD([makeQuery(id+"F42.boolean.opBoolean","COPY",EDGE,{"disambiguationData":[TD([makeQuery(id+"F15.opLoft","SWEPT_FACE",FACE,{"disambiguationData":[OSD([sQuery(id+"F3.wireOp",EDGE,"E20.6.0"),subQ29,subQ28,sQuery(id+"F4.wireOp",EDGE,"E26.6.0"),subQ27,subQ26])]})])],"derivedFrom":subQ9})])]}),makeQuery(id+"F47.opFillet","BLEND_FACE",FACE,{"disambiguationData":[OSD([subQ5,subQ7]),TDD([makeQuery(id+"F42.boolean.opBoolean","COPY",EDGE,{"disambiguationData":[TD([makeQuery(id+"F16.opLoft","SWEPT_FACE",FACE,{"disambiguationData":[OSD([sQuery(id+"F3.wireOp",EDGE,"E20.5.0"),subQ25,subQ24,sQuery(id+"F4.wireOp",EDGE,"E26.5.0"),subQ23,subQ22])]})])],"derivedFrom":subQ9})])]}),makeQuery(id+"F47.opFillet","BLEND_FACE",FACE,{"disambiguationData":[OSD([subQ5,subQ7]),TDD([makeQuery(id+"F42.boolean.opBoolean","COPY",EDGE,{"disambiguationData":[TD([makeQuery(id+"F17.opLoft","SWEPT_FACE",FACE,{"disambiguationData":[OSD([sQuery(id+"F3.wireOp",EDGE,"E20.4.0"),subQ21,subQ20,sQuery(id+"F4.wireOp",EDGE,"E26.4.0"),subQ19,subQ18])]})])],"derivedFrom":subQ9})])]}),makeQuery(id+"F47.opFillet","BLEND_FACE",FACE,{"disambiguationData":[OSD([subQ5,subQ7]),TDD([makeQuery(id+"F42.boolean.opBoolean","COPY",EDGE,{"disambiguationData":[TD([makeQuery(id+"F18.opLoft","SWEPT_FACE",FACE,{"disambiguationData":[OSD([sQuery(id+"F3.wireOp",EDGE,"E20.3.0"),subQ17,subQ16,sQuery(id+"F4.wireOp",EDGE,"E26.3.0"),subQ15,subQ14])]})])],"derivedFrom":subQ9})])]}),makeQuery(id+"F47.opFillet","BLEND_FACE",FACE,{"disambiguationData":[OSD([subQ5,subQ7]),TDD([makeQuery(id+"F42.boolean.opBoolean","COPY",EDGE,{"disambiguationData":[TD([makeQuery(id+"F19.opLoft","SWEPT_FACE",FACE,{"disambiguationData":[OSD([sQuery(id+"F3.wireOp",EDGE,"E20.2.0"),subQ13,subQ12,sQuery(id+"F4.wireOp",EDGE,"E26.2.0"),subQ11,subQ10])]})])],"derivedFrom":subQ9})])]}),makeQuery(id+"F47.opFillet","BLEND_FACE",FACE,{"disambiguationData":[OSD([subQ5,subQ7]),TDD([makeQuery(id+"F42.boolean.opBoolean","COPY",EDGE,{"disambiguationData":[TD([makeQuery(id+"F20.opLoft","SWEPT_FACE",FACE,{"disambiguationData":[OSD([sQuery(id+"F3.wireOp",EDGE,"E20.1.0"),subQ4,subQ3,sQuery(id+"F4.wireOp",EDGE,"E26.1.0"),subQ2,subQ1])]})])],"derivedFrom":subQ9})])]})],"blendedInto":[makeQuery(id+"F47.opFillet","BLEND_FACE",FACE,{"disambiguationData":[OSD([subQ5,subQ7]),TDD([makeQuery(id+"F42.boolean.opBoolean","COPY",EDGE,{"disambiguationData":[TD([makeQuery(id+"F5.opLoft","SWEPT_FACE",FACE,{"disambiguationData":[OSD([subQ71,subQ70,sQuery(id+"F3.wireOp",EDGE,"E18.left"),sQuery(id+"F4.wireOp",EDGE,"E21"),subQ69,subQ68])]})])],"derivedFrom":subQ9})])]}),makeQuery(id+"F47.opFillet","BLEND_FACE",FACE,{"disambiguationData":[OSD([subQ5,subQ7]),TDD([makeQuery(id+"F42.boolean.opBoolean","COPY",EDGE,{"disambiguationData":[TD([makeQuery(id+"F6.opLoft","SWEPT_FACE",FACE,{"disambiguationData":[OSD([sQuery(id+"F3.wireOp",EDGE,"E20.15.0"),subQ67,subQ66,sQuery(id+"F4.wireOp",EDGE,"E26.15.0"),subQ65,subQ64])]})])],"derivedFrom":subQ9})])]}),makeQuery(id+"F47.opFillet","BLEND_FACE",FACE,{"disambiguationData":[OSD([subQ5,subQ7]),TDD([makeQuery(id+"F42.boolean.opBoolean","COPY",EDGE,{"disambiguationData":[TD([makeQuery(id+"F7.opLoft","SWEPT_FACE",FACE,{"disambiguationData":[OSD([sQuery(id+"F3.wireOp",EDGE,"E20.14.0"),subQ63,subQ62,sQuery(id+"F4.wireOp",EDGE,"E26.14.0"),subQ61,subQ60])]})])],"derivedFrom":subQ9})])]}),makeQuery(id+"F47.opFillet","BLEND_FACE",FACE,{"disambiguationData":[OSD([subQ5,subQ7]),TDD([makeQuery(id+"F42.boolean.opBoolean","COPY",EDGE,{"disambiguationData":[TD([subQ59])],"derivedFrom":subQ9})])]}),makeQuery(id+"F47.opFillet","BLEND_FACE",FACE,{"disambiguationData":[OSD([subQ5,subQ7]),TDD([makeQuery(id+"F42.boolean.opBoolean","COPY",EDGE,{"disambiguationData":[TD([makeQuery(id+"F9.opLoft","SWEPT_FACE",FACE,{"disambiguationData":[OSD([sQuery(id+"F3.wireOp",EDGE,"E20.12.0"),subQ53,subQ52,sQuery(id+"F4.wireOp",EDGE,"E26.12.0"),subQ51,subQ50])]})])],"derivedFrom":subQ9})])]}),makeQuery(id+"F47.opFillet","BLEND_FACE",FACE,{"disambiguationData":[OSD([subQ5,subQ7]),TDD([makeQuery(id+"F42.boolean.opBoolean","COPY",EDGE,{"disambiguationData":[TD([makeQuery(id+"F10.opLoft","SWEPT_FACE",FACE,{"disambiguationData":[OSD([sQuery(id+"F3.wireOp",EDGE,"E20.11.0"),subQ49,subQ48,sQuery(id+"F4.wireOp",EDGE,"E26.11.0"),subQ47,subQ46])]})])],"derivedFrom":subQ9})])]}),makeQuery(id+"F47.opFillet","BLEND_FACE",FACE,{"disambiguationData":[OSD([subQ5,subQ7]),TDD([makeQuery(id+"F42.boolean.opBoolean","COPY",EDGE,{"disambiguationData":[TD([makeQuery(id+"F11.opLoft","SWEPT_FACE",FACE,{"disambiguationData":[OSD([sQuery(id+"F3.wireOp",EDGE,"E20.10.0"),subQ45,subQ44,sQuery(id+"F4.wireOp",EDGE,"E26.10.0"),subQ43,subQ42])]})])],"derivedFrom":subQ9})])]}),makeQuery(id+"F47.opFillet","BLEND_FACE",FACE,{"disambiguationData":[OSD([subQ5,subQ7]),TDD([makeQuery(id+"F42.boolean.opBoolean","COPY",EDGE,{"disambiguationData":[TD([makeQuery(id+"F12.opLoft","SWEPT_FACE",FACE,{"disambiguationData":[OSD([sQuery(id+"F3.wireOp",EDGE,"E20.9.0"),subQ41,subQ40,sQuery(id+"F4.wireOp",EDGE,"E26.9.0"),subQ39,subQ38])]})])],"derivedFrom":subQ9})])]}),makeQuery(id+"F47.opFillet","BLEND_FACE",FACE,{"disambiguationData":[OSD([subQ5,subQ7]),TDD([makeQuery(id+"F42.boolean.opBoolean","COPY",EDGE,{"disambiguationData":[TD([makeQuery(id+"F13.opLoft","SWEPT_FACE",FACE,{"disambiguationData":[OSD([sQuery(id+"F3.wireOp",EDGE,"E20.8.0"),subQ37,subQ36,sQuery(id+"F4.wireOp",EDGE,"E26.8.0"),subQ35,subQ34])]})])],"derivedFrom":subQ9})])]}),makeQuery(id+"F47.opFillet","BLEND_FACE",FACE,{"disambiguationData":[OSD([subQ5,subQ7]),TDD([makeQuery(id+"F42.boolean.opBoolean","COPY",EDGE,{"disambiguationData":[TD([makeQuery(id+"F14.opLoft","SWEPT_FACE",FACE,{"disambiguationData":[OSD([sQuery(id+"F3.wireOp",EDGE,"E20.7.0"),subQ33,subQ32,sQuery(id+"F4.wireOp",EDGE,"E26.7.0"),subQ31,subQ30])]})])],"derivedFrom":subQ9})])]}),makeQuery(id+"F47.opFillet","BLEND_FACE",FACE,{"disambiguationData":[OSD([subQ5,subQ7]),TDD([makeQuery(id+"F42.boolean.opBoolean","COPY",EDGE,{"disambiguationData":[TD([makeQuery(id+"F15.opLoft","SWEPT_FACE",FACE,{"disambiguationData":[OSD([sQuery(id+"F3.wireOp",EDGE,"E20.6.0"),subQ29,subQ28,sQuery(id+"F4.wireOp",EDGE,"E26.6.0"),subQ27,subQ26])]})])],"derivedFrom":subQ9})])]}),makeQuery(id+"F47.opFillet","BLEND_FACE",FACE,{"disambiguationData":[OSD([subQ5,subQ7]),TDD([makeQuery(id+"F42.boolean.opBoolean","COPY",EDGE,{"disambiguationData":[TD([makeQuery(id+"F16.opLoft","SWEPT_FACE",FACE,{"disambiguationData":[OSD([sQuery(id+"F3.wireOp",EDGE,"E20.5.0"),subQ25,subQ24,sQuery(id+"F4.wireOp",EDGE,"E26.5.0"),subQ23,subQ22])]})])],"derivedFrom":subQ9})])]}),makeQuery(id+"F47.opFillet","BLEND_FACE",FACE,{"disambiguationData":[OSD([subQ5,subQ7]),TDD([makeQuery(id+"F42.boolean.opBoolean","COPY",EDGE,{"disambiguationData":[TD([makeQuery(id+"F17.opLoft","SWEPT_FACE",FACE,{"disambiguationData":[OSD([sQuery(id+"F3.wireOp",EDGE,"E20.4.0"),subQ21,subQ20,sQuery(id+"F4.wireOp",EDGE,"E26.4.0"),subQ19,subQ18])]})])],"derivedFrom":subQ9})])]}),makeQuery(id+"F47.opFillet","BLEND_FACE",FACE,{"disambiguationData":[OSD([subQ5,subQ7]),TDD([makeQuery(id+"F42.boolean.opBoolean","COPY",EDGE,{"disambiguationData":[TD([makeQuery(id+"F18.opLoft","SWEPT_FACE",FACE,{"disambiguationData":[OSD([sQuery(id+"F3.wireOp",EDGE,"E20.3.0"),subQ17,subQ16,sQuery(id+"F4.wireOp",EDGE,"E26.3.0"),subQ15,subQ14])]})])],"derivedFrom":subQ9})])]}),makeQuery(id+"F47.opFillet","BLEND_FACE",FACE,{"disambiguationData":[OSD([subQ5,subQ7]),TDD([makeQuery(id+"F42.boolean.opBoolean","COPY",EDGE,{"disambiguationData":[TD([makeQuery(id+"F19.opLoft","SWEPT_FACE",FACE,{"disambiguationData":[OSD([sQuery(id+"F3.wireOp",EDGE,"E20.2.0"),subQ13,subQ12,sQuery(id+"F4.wireOp",EDGE,"E26.2.0"),subQ11,subQ10])]})])],"derivedFrom":subQ9})])]}),makeQuery(id+"F47.opFillet","BLEND_FACE",FACE,{"disambiguationData":[OSD([subQ5,subQ7]),TDD([makeQuery(id+"F42.boolean.opBoolean","COPY",EDGE,{"disambiguationData":[TD([makeQuery(id+"F20.opLoft","SWEPT_FACE",FACE,{"disambiguationData":[OSD([sQuery(id+"F3.wireOp",EDGE,"E20.1.0"),subQ4,subQ3,sQuery(id+"F4.wireOp",EDGE,"E26.1.0"),subQ2,subQ1])]})])],"derivedFrom":subQ9})])]})]});}
            var Q58;
            {var subQ0=makeQuery(id+"F40.opExtrude","CAP_FACE",FACE,{"disambiguationData":[OSD([sQuery(id+"F39.wireOp",EDGE,"E29"),sQuery(id+"F39.wireOp",EDGE,"E30")])],"isStart":false});var subQ1=sQuery(id+"F4.wireOp",EDGE,"E26.1.3");var subQ2=sQuery(id+"F4.wireOp",EDGE,"E26.1.2");var subQ3=sQuery(id+"F3.wireOp",EDGE,"E20.1.3");var subQ4=sQuery(id+"F3.wireOp",EDGE,"E20.1.1");var subQ5=sQuery(id+"F41.wireOp",EDGE,"E35");var subQ6=makeQuery(id+"F42.opRevolve","SWEPT_FACE",FACE,{"disambiguationData":[OSD([subQ5])]});var subQ7=sQuery(id+"F41.wireOp",EDGE,"E36");var subQ8=makeQuery(id+"F42.opRevolve","SWEPT_FACE",FACE,{"disambiguationData":[OSD([subQ7])]});var subQ9=makeQuery(id+"F42.opRevolve","SWEPT_EDGE",EDGE,{"disambiguationData":[OSD([subQ5,subQ7])]});var subQ10=sQuery(id+"F4.wireOp",EDGE,"E26.2.3");var subQ11=sQuery(id+"F4.wireOp",EDGE,"E26.2.2");var subQ12=sQuery(id+"F3.wireOp",EDGE,"E20.2.3");var subQ13=sQuery(id+"F3.wireOp",EDGE,"E20.2.1");var subQ14=sQuery(id+"F4.wireOp",EDGE,"E26.3.3");var subQ15=sQuery(id+"F4.wireOp",EDGE,"E26.3.2");var subQ16=sQuery(id+"F3.wireOp",EDGE,"E20.3.3");var subQ17=sQuery(id+"F3.wireOp",EDGE,"E20.3.1");var subQ18=sQuery(id+"F4.wireOp",EDGE,"E26.4.3");var subQ19=sQuery(id+"F4.wireOp",EDGE,"E26.4.2");var subQ20=sQuery(id+"F3.wireOp",EDGE,"E20.4.3");var subQ21=sQuery(id+"F3.wireOp",EDGE,"E20.4.1");var subQ22=sQuery(id+"F4.wireOp",EDGE,"E26.5.3");var subQ23=sQuery(id+"F4.wireOp",EDGE,"E26.5.2");var subQ24=sQuery(id+"F3.wireOp",EDGE,"E20.5.3");var subQ25=sQuery(id+"F3.wireOp",EDGE,"E20.5.1");var subQ26=sQuery(id+"F4.wireOp",EDGE,"E26.6.3");var subQ27=sQuery(id+"F4.wireOp",EDGE,"E26.6.2");var subQ28=sQuery(id+"F3.wireOp",EDGE,"E20.6.3");var subQ29=sQuery(id+"F3.wireOp",EDGE,"E20.6.1");var subQ30=sQuery(id+"F4.wireOp",EDGE,"E26.7.3");var subQ31=sQuery(id+"F4.wireOp",EDGE,"E26.7.2");var subQ32=sQuery(id+"F3.wireOp",EDGE,"E20.7.3");var subQ33=sQuery(id+"F3.wireOp",EDGE,"E20.7.1");var subQ34=sQuery(id+"F4.wireOp",EDGE,"E26.8.3");var subQ35=sQuery(id+"F4.wireOp",EDGE,"E26.8.2");var subQ36=sQuery(id+"F3.wireOp",EDGE,"E20.8.3");var subQ37=sQuery(id+"F3.wireOp",EDGE,"E20.8.1");var subQ38=sQuery(id+"F4.wireOp",EDGE,"E26.9.3");var subQ39=sQuery(id+"F4.wireOp",EDGE,"E26.9.2");var subQ40=sQuery(id+"F3.wireOp",EDGE,"E20.9.3");var subQ41=sQuery(id+"F3.wireOp",EDGE,"E20.9.1");var subQ42=sQuery(id+"F4.wireOp",EDGE,"E26.10.3");var subQ43=sQuery(id+"F4.wireOp",EDGE,"E26.10.2");var subQ44=sQuery(id+"F3.wireOp",EDGE,"E20.10.3");var subQ45=sQuery(id+"F3.wireOp",EDGE,"E20.10.1");var subQ46=sQuery(id+"F4.wireOp",EDGE,"E26.11.3");var subQ47=sQuery(id+"F4.wireOp",EDGE,"E26.11.2");var subQ48=sQuery(id+"F3.wireOp",EDGE,"E20.11.3");var subQ49=sQuery(id+"F3.wireOp",EDGE,"E20.11.1");var subQ50=sQuery(id+"F4.wireOp",EDGE,"E26.12.3");var subQ51=sQuery(id+"F4.wireOp",EDGE,"E26.12.2");var subQ52=sQuery(id+"F3.wireOp",EDGE,"E20.12.3");var subQ53=sQuery(id+"F3.wireOp",EDGE,"E20.12.1");var subQ55=makeQuery(id+"F9.opLoft","SWEPT_FACE",FACE,{"disambiguationData":[OSD([sQuery(id+"F3.wireOp",EDGE,"E20.12.0"),subQ53,subQ52,sQuery(id+"F4.wireOp",EDGE,"E26.12.0"),subQ51,subQ50])]});var subQ56=sQuery(id+"F4.wireOp",EDGE,"E26.13.3");var subQ57=sQuery(id+"F4.wireOp",EDGE,"E26.13.2");var subQ58=sQuery(id+"F3.wireOp",EDGE,"E20.13.3");var subQ59=sQuery(id+"F3.wireOp",EDGE,"E20.13.1");var subQ60=sQuery(id+"F4.wireOp",EDGE,"E26.14.3");var subQ61=sQuery(id+"F4.wireOp",EDGE,"E26.14.2");var subQ62=sQuery(id+"F3.wireOp",EDGE,"E20.14.3");var subQ63=sQuery(id+"F3.wireOp",EDGE,"E20.14.1");var subQ64=sQuery(id+"F4.wireOp",EDGE,"E26.15.3");var subQ65=sQuery(id+"F4.wireOp",EDGE,"E26.15.2");var subQ66=sQuery(id+"F3.wireOp",EDGE,"E20.15.3");var subQ67=sQuery(id+"F3.wireOp",EDGE,"E20.15.1");var subQ68=sQuery(id+"F4.wireOp",EDGE,"E23");var subQ69=sQuery(id+"F4.wireOp",EDGE,"E22");var subQ70=sQuery(id+"F3.wireOp",EDGE,"E18.top");var subQ71=sQuery(id+"F3.wireOp",EDGE,"E18.bottom");var subQ74=makeQuery(id+"F42.boolean.opBoolean","COPY",FACE,{"disambiguationData":[TD([subQ55])],"derivedFrom":subQ6});var subQ75=makeQuery(id+"F9.boolean.opBoolean","INTERSECT",EDGE,{"derivedFrom":[makeQuery(id+"F1.opRevolve","SWEPT_FACE",FACE,{"disambiguationData":[OSD([sQuery(id+"F0.wireOp",EDGE,"E13")])]}),subQ55]});Q58=makeQuery(id+"F48.opFillet","BLEND_EDGE",EDGE,{"blendedFrom":[makeQuery(id+"F47.opFillet","TWEAK_EDGE",EDGE,{"derivedFrom":[makeQuery(id+"F45.opFillet","BLEND_VERTEX",VERTEX,{"blendedFrom":[subQ75,subQ55,subQ74],"blendedInto":[subQ55,subQ74]}),makeQuery(id+"F45.opFillet","BLEND_VERTEX",VERTEX,{"blendedFrom":[subQ75,makeQuery(id+"F42.boolean.opBoolean","MERGE",FACE,{"derivedFrom":[subQ0,subQ8]}),subQ74],"blendedInto":[makeQuery(id+"F42.boolean.opBoolean","MERGE",FACE,{"derivedFrom":[subQ0,subQ8]}),subQ74]})]}),makeQuery(id+"F47.opFillet","BLEND_FACE",FACE,{"disambiguationData":[OSD([subQ5,subQ7]),TDD([makeQuery(id+"F42.boolean.opBoolean","COPY",EDGE,{"disambiguationData":[TD([makeQuery(id+"F5.opLoft","SWEPT_FACE",FACE,{"disambiguationData":[OSD([subQ71,subQ70,sQuery(id+"F3.wireOp",EDGE,"E18.left"),sQuery(id+"F4.wireOp",EDGE,"E21"),subQ69,subQ68])]})])],"derivedFrom":subQ9})])]}),makeQuery(id+"F47.opFillet","BLEND_FACE",FACE,{"disambiguationData":[OSD([subQ5,subQ7]),TDD([makeQuery(id+"F42.boolean.opBoolean","COPY",EDGE,{"disambiguationData":[TD([makeQuery(id+"F6.opLoft","SWEPT_FACE",FACE,{"disambiguationData":[OSD([sQuery(id+"F3.wireOp",EDGE,"E20.15.0"),subQ67,subQ66,sQuery(id+"F4.wireOp",EDGE,"E26.15.0"),subQ65,subQ64])]})])],"derivedFrom":subQ9})])]}),makeQuery(id+"F47.opFillet","BLEND_FACE",FACE,{"disambiguationData":[OSD([subQ5,subQ7]),TDD([makeQuery(id+"F42.boolean.opBoolean","COPY",EDGE,{"disambiguationData":[TD([makeQuery(id+"F7.opLoft","SWEPT_FACE",FACE,{"disambiguationData":[OSD([sQuery(id+"F3.wireOp",EDGE,"E20.14.0"),subQ63,subQ62,sQuery(id+"F4.wireOp",EDGE,"E26.14.0"),subQ61,subQ60])]})])],"derivedFrom":subQ9})])]}),makeQuery(id+"F47.opFillet","BLEND_FACE",FACE,{"disambiguationData":[OSD([subQ5,subQ7]),TDD([makeQuery(id+"F42.boolean.opBoolean","COPY",EDGE,{"disambiguationData":[TD([makeQuery(id+"F8.opLoft","SWEPT_FACE",FACE,{"disambiguationData":[OSD([sQuery(id+"F3.wireOp",EDGE,"E20.13.0"),subQ59,subQ58,sQuery(id+"F4.wireOp",EDGE,"E26.13.0"),subQ57,subQ56])]})])],"derivedFrom":subQ9})])]}),makeQuery(id+"F47.opFillet","BLEND_FACE",FACE,{"disambiguationData":[OSD([subQ5,subQ7]),TDD([makeQuery(id+"F42.boolean.opBoolean","COPY",EDGE,{"disambiguationData":[TD([subQ55])],"derivedFrom":subQ9})])]}),makeQuery(id+"F47.opFillet","BLEND_FACE",FACE,{"disambiguationData":[OSD([subQ5,subQ7]),TDD([makeQuery(id+"F42.boolean.opBoolean","COPY",EDGE,{"disambiguationData":[TD([makeQuery(id+"F10.opLoft","SWEPT_FACE",FACE,{"disambiguationData":[OSD([sQuery(id+"F3.wireOp",EDGE,"E20.11.0"),subQ49,subQ48,sQuery(id+"F4.wireOp",EDGE,"E26.11.0"),subQ47,subQ46])]})])],"derivedFrom":subQ9})])]}),makeQuery(id+"F47.opFillet","BLEND_FACE",FACE,{"disambiguationData":[OSD([subQ5,subQ7]),TDD([makeQuery(id+"F42.boolean.opBoolean","COPY",EDGE,{"disambiguationData":[TD([makeQuery(id+"F11.opLoft","SWEPT_FACE",FACE,{"disambiguationData":[OSD([sQuery(id+"F3.wireOp",EDGE,"E20.10.0"),subQ45,subQ44,sQuery(id+"F4.wireOp",EDGE,"E26.10.0"),subQ43,subQ42])]})])],"derivedFrom":subQ9})])]}),makeQuery(id+"F47.opFillet","BLEND_FACE",FACE,{"disambiguationData":[OSD([subQ5,subQ7]),TDD([makeQuery(id+"F42.boolean.opBoolean","COPY",EDGE,{"disambiguationData":[TD([makeQuery(id+"F12.opLoft","SWEPT_FACE",FACE,{"disambiguationData":[OSD([sQuery(id+"F3.wireOp",EDGE,"E20.9.0"),subQ41,subQ40,sQuery(id+"F4.wireOp",EDGE,"E26.9.0"),subQ39,subQ38])]})])],"derivedFrom":subQ9})])]}),makeQuery(id+"F47.opFillet","BLEND_FACE",FACE,{"disambiguationData":[OSD([subQ5,subQ7]),TDD([makeQuery(id+"F42.boolean.opBoolean","COPY",EDGE,{"disambiguationData":[TD([makeQuery(id+"F13.opLoft","SWEPT_FACE",FACE,{"disambiguationData":[OSD([sQuery(id+"F3.wireOp",EDGE,"E20.8.0"),subQ37,subQ36,sQuery(id+"F4.wireOp",EDGE,"E26.8.0"),subQ35,subQ34])]})])],"derivedFrom":subQ9})])]}),makeQuery(id+"F47.opFillet","BLEND_FACE",FACE,{"disambiguationData":[OSD([subQ5,subQ7]),TDD([makeQuery(id+"F42.boolean.opBoolean","COPY",EDGE,{"disambiguationData":[TD([makeQuery(id+"F14.opLoft","SWEPT_FACE",FACE,{"disambiguationData":[OSD([sQuery(id+"F3.wireOp",EDGE,"E20.7.0"),subQ33,subQ32,sQuery(id+"F4.wireOp",EDGE,"E26.7.0"),subQ31,subQ30])]})])],"derivedFrom":subQ9})])]}),makeQuery(id+"F47.opFillet","BLEND_FACE",FACE,{"disambiguationData":[OSD([subQ5,subQ7]),TDD([makeQuery(id+"F42.boolean.opBoolean","COPY",EDGE,{"disambiguationData":[TD([makeQuery(id+"F15.opLoft","SWEPT_FACE",FACE,{"disambiguationData":[OSD([sQuery(id+"F3.wireOp",EDGE,"E20.6.0"),subQ29,subQ28,sQuery(id+"F4.wireOp",EDGE,"E26.6.0"),subQ27,subQ26])]})])],"derivedFrom":subQ9})])]}),makeQuery(id+"F47.opFillet","BLEND_FACE",FACE,{"disambiguationData":[OSD([subQ5,subQ7]),TDD([makeQuery(id+"F42.boolean.opBoolean","COPY",EDGE,{"disambiguationData":[TD([makeQuery(id+"F16.opLoft","SWEPT_FACE",FACE,{"disambiguationData":[OSD([sQuery(id+"F3.wireOp",EDGE,"E20.5.0"),subQ25,subQ24,sQuery(id+"F4.wireOp",EDGE,"E26.5.0"),subQ23,subQ22])]})])],"derivedFrom":subQ9})])]}),makeQuery(id+"F47.opFillet","BLEND_FACE",FACE,{"disambiguationData":[OSD([subQ5,subQ7]),TDD([makeQuery(id+"F42.boolean.opBoolean","COPY",EDGE,{"disambiguationData":[TD([makeQuery(id+"F17.opLoft","SWEPT_FACE",FACE,{"disambiguationData":[OSD([sQuery(id+"F3.wireOp",EDGE,"E20.4.0"),subQ21,subQ20,sQuery(id+"F4.wireOp",EDGE,"E26.4.0"),subQ19,subQ18])]})])],"derivedFrom":subQ9})])]}),makeQuery(id+"F47.opFillet","BLEND_FACE",FACE,{"disambiguationData":[OSD([subQ5,subQ7]),TDD([makeQuery(id+"F42.boolean.opBoolean","COPY",EDGE,{"disambiguationData":[TD([makeQuery(id+"F18.opLoft","SWEPT_FACE",FACE,{"disambiguationData":[OSD([sQuery(id+"F3.wireOp",EDGE,"E20.3.0"),subQ17,subQ16,sQuery(id+"F4.wireOp",EDGE,"E26.3.0"),subQ15,subQ14])]})])],"derivedFrom":subQ9})])]}),makeQuery(id+"F47.opFillet","BLEND_FACE",FACE,{"disambiguationData":[OSD([subQ5,subQ7]),TDD([makeQuery(id+"F42.boolean.opBoolean","COPY",EDGE,{"disambiguationData":[TD([makeQuery(id+"F19.opLoft","SWEPT_FACE",FACE,{"disambiguationData":[OSD([sQuery(id+"F3.wireOp",EDGE,"E20.2.0"),subQ13,subQ12,sQuery(id+"F4.wireOp",EDGE,"E26.2.0"),subQ11,subQ10])]})])],"derivedFrom":subQ9})])]}),makeQuery(id+"F47.opFillet","BLEND_FACE",FACE,{"disambiguationData":[OSD([subQ5,subQ7]),TDD([makeQuery(id+"F42.boolean.opBoolean","COPY",EDGE,{"disambiguationData":[TD([makeQuery(id+"F20.opLoft","SWEPT_FACE",FACE,{"disambiguationData":[OSD([sQuery(id+"F3.wireOp",EDGE,"E20.1.0"),subQ4,subQ3,sQuery(id+"F4.wireOp",EDGE,"E26.1.0"),subQ2,subQ1])]})])],"derivedFrom":subQ9})])]})],"blendedInto":[makeQuery(id+"F47.opFillet","BLEND_FACE",FACE,{"disambiguationData":[OSD([subQ5,subQ7]),TDD([makeQuery(id+"F42.boolean.opBoolean","COPY",EDGE,{"disambiguationData":[TD([makeQuery(id+"F5.opLoft","SWEPT_FACE",FACE,{"disambiguationData":[OSD([subQ71,subQ70,sQuery(id+"F3.wireOp",EDGE,"E18.left"),sQuery(id+"F4.wireOp",EDGE,"E21"),subQ69,subQ68])]})])],"derivedFrom":subQ9})])]}),makeQuery(id+"F47.opFillet","BLEND_FACE",FACE,{"disambiguationData":[OSD([subQ5,subQ7]),TDD([makeQuery(id+"F42.boolean.opBoolean","COPY",EDGE,{"disambiguationData":[TD([makeQuery(id+"F6.opLoft","SWEPT_FACE",FACE,{"disambiguationData":[OSD([sQuery(id+"F3.wireOp",EDGE,"E20.15.0"),subQ67,subQ66,sQuery(id+"F4.wireOp",EDGE,"E26.15.0"),subQ65,subQ64])]})])],"derivedFrom":subQ9})])]}),makeQuery(id+"F47.opFillet","BLEND_FACE",FACE,{"disambiguationData":[OSD([subQ5,subQ7]),TDD([makeQuery(id+"F42.boolean.opBoolean","COPY",EDGE,{"disambiguationData":[TD([makeQuery(id+"F7.opLoft","SWEPT_FACE",FACE,{"disambiguationData":[OSD([sQuery(id+"F3.wireOp",EDGE,"E20.14.0"),subQ63,subQ62,sQuery(id+"F4.wireOp",EDGE,"E26.14.0"),subQ61,subQ60])]})])],"derivedFrom":subQ9})])]}),makeQuery(id+"F47.opFillet","BLEND_FACE",FACE,{"disambiguationData":[OSD([subQ5,subQ7]),TDD([makeQuery(id+"F42.boolean.opBoolean","COPY",EDGE,{"disambiguationData":[TD([makeQuery(id+"F8.opLoft","SWEPT_FACE",FACE,{"disambiguationData":[OSD([sQuery(id+"F3.wireOp",EDGE,"E20.13.0"),subQ59,subQ58,sQuery(id+"F4.wireOp",EDGE,"E26.13.0"),subQ57,subQ56])]})])],"derivedFrom":subQ9})])]}),makeQuery(id+"F47.opFillet","BLEND_FACE",FACE,{"disambiguationData":[OSD([subQ5,subQ7]),TDD([makeQuery(id+"F42.boolean.opBoolean","COPY",EDGE,{"disambiguationData":[TD([subQ55])],"derivedFrom":subQ9})])]}),makeQuery(id+"F47.opFillet","BLEND_FACE",FACE,{"disambiguationData":[OSD([subQ5,subQ7]),TDD([makeQuery(id+"F42.boolean.opBoolean","COPY",EDGE,{"disambiguationData":[TD([makeQuery(id+"F10.opLoft","SWEPT_FACE",FACE,{"disambiguationData":[OSD([sQuery(id+"F3.wireOp",EDGE,"E20.11.0"),subQ49,subQ48,sQuery(id+"F4.wireOp",EDGE,"E26.11.0"),subQ47,subQ46])]})])],"derivedFrom":subQ9})])]}),makeQuery(id+"F47.opFillet","BLEND_FACE",FACE,{"disambiguationData":[OSD([subQ5,subQ7]),TDD([makeQuery(id+"F42.boolean.opBoolean","COPY",EDGE,{"disambiguationData":[TD([makeQuery(id+"F11.opLoft","SWEPT_FACE",FACE,{"disambiguationData":[OSD([sQuery(id+"F3.wireOp",EDGE,"E20.10.0"),subQ45,subQ44,sQuery(id+"F4.wireOp",EDGE,"E26.10.0"),subQ43,subQ42])]})])],"derivedFrom":subQ9})])]}),makeQuery(id+"F47.opFillet","BLEND_FACE",FACE,{"disambiguationData":[OSD([subQ5,subQ7]),TDD([makeQuery(id+"F42.boolean.opBoolean","COPY",EDGE,{"disambiguationData":[TD([makeQuery(id+"F12.opLoft","SWEPT_FACE",FACE,{"disambiguationData":[OSD([sQuery(id+"F3.wireOp",EDGE,"E20.9.0"),subQ41,subQ40,sQuery(id+"F4.wireOp",EDGE,"E26.9.0"),subQ39,subQ38])]})])],"derivedFrom":subQ9})])]}),makeQuery(id+"F47.opFillet","BLEND_FACE",FACE,{"disambiguationData":[OSD([subQ5,subQ7]),TDD([makeQuery(id+"F42.boolean.opBoolean","COPY",EDGE,{"disambiguationData":[TD([makeQuery(id+"F13.opLoft","SWEPT_FACE",FACE,{"disambiguationData":[OSD([sQuery(id+"F3.wireOp",EDGE,"E20.8.0"),subQ37,subQ36,sQuery(id+"F4.wireOp",EDGE,"E26.8.0"),subQ35,subQ34])]})])],"derivedFrom":subQ9})])]}),makeQuery(id+"F47.opFillet","BLEND_FACE",FACE,{"disambiguationData":[OSD([subQ5,subQ7]),TDD([makeQuery(id+"F42.boolean.opBoolean","COPY",EDGE,{"disambiguationData":[TD([makeQuery(id+"F14.opLoft","SWEPT_FACE",FACE,{"disambiguationData":[OSD([sQuery(id+"F3.wireOp",EDGE,"E20.7.0"),subQ33,subQ32,sQuery(id+"F4.wireOp",EDGE,"E26.7.0"),subQ31,subQ30])]})])],"derivedFrom":subQ9})])]}),makeQuery(id+"F47.opFillet","BLEND_FACE",FACE,{"disambiguationData":[OSD([subQ5,subQ7]),TDD([makeQuery(id+"F42.boolean.opBoolean","COPY",EDGE,{"disambiguationData":[TD([makeQuery(id+"F15.opLoft","SWEPT_FACE",FACE,{"disambiguationData":[OSD([sQuery(id+"F3.wireOp",EDGE,"E20.6.0"),subQ29,subQ28,sQuery(id+"F4.wireOp",EDGE,"E26.6.0"),subQ27,subQ26])]})])],"derivedFrom":subQ9})])]}),makeQuery(id+"F47.opFillet","BLEND_FACE",FACE,{"disambiguationData":[OSD([subQ5,subQ7]),TDD([makeQuery(id+"F42.boolean.opBoolean","COPY",EDGE,{"disambiguationData":[TD([makeQuery(id+"F16.opLoft","SWEPT_FACE",FACE,{"disambiguationData":[OSD([sQuery(id+"F3.wireOp",EDGE,"E20.5.0"),subQ25,subQ24,sQuery(id+"F4.wireOp",EDGE,"E26.5.0"),subQ23,subQ22])]})])],"derivedFrom":subQ9})])]}),makeQuery(id+"F47.opFillet","BLEND_FACE",FACE,{"disambiguationData":[OSD([subQ5,subQ7]),TDD([makeQuery(id+"F42.boolean.opBoolean","COPY",EDGE,{"disambiguationData":[TD([makeQuery(id+"F17.opLoft","SWEPT_FACE",FACE,{"disambiguationData":[OSD([sQuery(id+"F3.wireOp",EDGE,"E20.4.0"),subQ21,subQ20,sQuery(id+"F4.wireOp",EDGE,"E26.4.0"),subQ19,subQ18])]})])],"derivedFrom":subQ9})])]}),makeQuery(id+"F47.opFillet","BLEND_FACE",FACE,{"disambiguationData":[OSD([subQ5,subQ7]),TDD([makeQuery(id+"F42.boolean.opBoolean","COPY",EDGE,{"disambiguationData":[TD([makeQuery(id+"F18.opLoft","SWEPT_FACE",FACE,{"disambiguationData":[OSD([sQuery(id+"F3.wireOp",EDGE,"E20.3.0"),subQ17,subQ16,sQuery(id+"F4.wireOp",EDGE,"E26.3.0"),subQ15,subQ14])]})])],"derivedFrom":subQ9})])]}),makeQuery(id+"F47.opFillet","BLEND_FACE",FACE,{"disambiguationData":[OSD([subQ5,subQ7]),TDD([makeQuery(id+"F42.boolean.opBoolean","COPY",EDGE,{"disambiguationData":[TD([makeQuery(id+"F19.opLoft","SWEPT_FACE",FACE,{"disambiguationData":[OSD([sQuery(id+"F3.wireOp",EDGE,"E20.2.0"),subQ13,subQ12,sQuery(id+"F4.wireOp",EDGE,"E26.2.0"),subQ11,subQ10])]})])],"derivedFrom":subQ9})])]}),makeQuery(id+"F47.opFillet","BLEND_FACE",FACE,{"disambiguationData":[OSD([subQ5,subQ7]),TDD([makeQuery(id+"F42.boolean.opBoolean","COPY",EDGE,{"disambiguationData":[TD([makeQuery(id+"F20.opLoft","SWEPT_FACE",FACE,{"disambiguationData":[OSD([sQuery(id+"F3.wireOp",EDGE,"E20.1.0"),subQ4,subQ3,sQuery(id+"F4.wireOp",EDGE,"E26.1.0"),subQ2,subQ1])]})])],"derivedFrom":subQ9})])]})]});}
            var Q59;
            {var subQ0=makeQuery(id+"F40.opExtrude","CAP_FACE",FACE,{"disambiguationData":[OSD([sQuery(id+"F39.wireOp",EDGE,"E29"),sQuery(id+"F39.wireOp",EDGE,"E30")])],"isStart":false});var subQ1=sQuery(id+"F4.wireOp",EDGE,"E26.1.3");var subQ2=sQuery(id+"F4.wireOp",EDGE,"E26.1.2");var subQ3=sQuery(id+"F3.wireOp",EDGE,"E20.1.3");var subQ4=sQuery(id+"F3.wireOp",EDGE,"E20.1.1");var subQ5=sQuery(id+"F41.wireOp",EDGE,"E35");var subQ6=makeQuery(id+"F42.opRevolve","SWEPT_FACE",FACE,{"disambiguationData":[OSD([subQ5])]});var subQ7=sQuery(id+"F41.wireOp",EDGE,"E36");var subQ8=makeQuery(id+"F42.opRevolve","SWEPT_FACE",FACE,{"disambiguationData":[OSD([subQ7])]});var subQ9=makeQuery(id+"F42.opRevolve","SWEPT_EDGE",EDGE,{"disambiguationData":[OSD([subQ5,subQ7])]});var subQ10=sQuery(id+"F4.wireOp",EDGE,"E26.2.3");var subQ11=sQuery(id+"F4.wireOp",EDGE,"E26.2.2");var subQ12=sQuery(id+"F3.wireOp",EDGE,"E20.2.3");var subQ13=sQuery(id+"F3.wireOp",EDGE,"E20.2.1");var subQ14=sQuery(id+"F4.wireOp",EDGE,"E26.3.3");var subQ15=sQuery(id+"F4.wireOp",EDGE,"E26.3.2");var subQ16=sQuery(id+"F3.wireOp",EDGE,"E20.3.3");var subQ17=sQuery(id+"F3.wireOp",EDGE,"E20.3.1");var subQ18=sQuery(id+"F4.wireOp",EDGE,"E26.4.3");var subQ19=sQuery(id+"F4.wireOp",EDGE,"E26.4.2");var subQ20=sQuery(id+"F3.wireOp",EDGE,"E20.4.3");var subQ21=sQuery(id+"F3.wireOp",EDGE,"E20.4.1");var subQ22=sQuery(id+"F4.wireOp",EDGE,"E26.5.3");var subQ23=sQuery(id+"F4.wireOp",EDGE,"E26.5.2");var subQ24=sQuery(id+"F3.wireOp",EDGE,"E20.5.3");var subQ25=sQuery(id+"F3.wireOp",EDGE,"E20.5.1");var subQ26=sQuery(id+"F4.wireOp",EDGE,"E26.6.3");var subQ27=sQuery(id+"F4.wireOp",EDGE,"E26.6.2");var subQ28=sQuery(id+"F3.wireOp",EDGE,"E20.6.3");var subQ29=sQuery(id+"F3.wireOp",EDGE,"E20.6.1");var subQ30=sQuery(id+"F4.wireOp",EDGE,"E26.7.3");var subQ31=sQuery(id+"F4.wireOp",EDGE,"E26.7.2");var subQ32=sQuery(id+"F3.wireOp",EDGE,"E20.7.3");var subQ33=sQuery(id+"F3.wireOp",EDGE,"E20.7.1");var subQ34=sQuery(id+"F4.wireOp",EDGE,"E26.8.3");var subQ35=sQuery(id+"F4.wireOp",EDGE,"E26.8.2");var subQ36=sQuery(id+"F3.wireOp",EDGE,"E20.8.3");var subQ37=sQuery(id+"F3.wireOp",EDGE,"E20.8.1");var subQ38=sQuery(id+"F4.wireOp",EDGE,"E26.9.3");var subQ39=sQuery(id+"F4.wireOp",EDGE,"E26.9.2");var subQ40=sQuery(id+"F3.wireOp",EDGE,"E20.9.3");var subQ41=sQuery(id+"F3.wireOp",EDGE,"E20.9.1");var subQ42=sQuery(id+"F4.wireOp",EDGE,"E26.10.3");var subQ43=sQuery(id+"F4.wireOp",EDGE,"E26.10.2");var subQ44=sQuery(id+"F3.wireOp",EDGE,"E20.10.3");var subQ45=sQuery(id+"F3.wireOp",EDGE,"E20.10.1");var subQ46=sQuery(id+"F4.wireOp",EDGE,"E26.11.3");var subQ47=sQuery(id+"F4.wireOp",EDGE,"E26.11.2");var subQ48=sQuery(id+"F3.wireOp",EDGE,"E20.11.3");var subQ49=sQuery(id+"F3.wireOp",EDGE,"E20.11.1");var subQ51=makeQuery(id+"F10.opLoft","SWEPT_FACE",FACE,{"disambiguationData":[OSD([sQuery(id+"F3.wireOp",EDGE,"E20.11.0"),subQ49,subQ48,sQuery(id+"F4.wireOp",EDGE,"E26.11.0"),subQ47,subQ46])]});var subQ52=sQuery(id+"F4.wireOp",EDGE,"E26.12.3");var subQ53=sQuery(id+"F4.wireOp",EDGE,"E26.12.2");var subQ54=sQuery(id+"F3.wireOp",EDGE,"E20.12.3");var subQ55=sQuery(id+"F3.wireOp",EDGE,"E20.12.1");var subQ56=sQuery(id+"F4.wireOp",EDGE,"E26.13.3");var subQ57=sQuery(id+"F4.wireOp",EDGE,"E26.13.2");var subQ58=sQuery(id+"F3.wireOp",EDGE,"E20.13.3");var subQ59=sQuery(id+"F3.wireOp",EDGE,"E20.13.1");var subQ60=sQuery(id+"F4.wireOp",EDGE,"E26.14.3");var subQ61=sQuery(id+"F4.wireOp",EDGE,"E26.14.2");var subQ62=sQuery(id+"F3.wireOp",EDGE,"E20.14.3");var subQ63=sQuery(id+"F3.wireOp",EDGE,"E20.14.1");var subQ64=sQuery(id+"F4.wireOp",EDGE,"E26.15.3");var subQ65=sQuery(id+"F4.wireOp",EDGE,"E26.15.2");var subQ66=sQuery(id+"F3.wireOp",EDGE,"E20.15.3");var subQ67=sQuery(id+"F3.wireOp",EDGE,"E20.15.1");var subQ68=sQuery(id+"F4.wireOp",EDGE,"E23");var subQ69=sQuery(id+"F4.wireOp",EDGE,"E22");var subQ70=sQuery(id+"F3.wireOp",EDGE,"E18.top");var subQ71=sQuery(id+"F3.wireOp",EDGE,"E18.bottom");var subQ74=makeQuery(id+"F42.boolean.opBoolean","COPY",FACE,{"disambiguationData":[TD([subQ51])],"derivedFrom":subQ6});var subQ75=makeQuery(id+"F10.boolean.opBoolean","INTERSECT",EDGE,{"derivedFrom":[makeQuery(id+"F1.opRevolve","SWEPT_FACE",FACE,{"disambiguationData":[OSD([sQuery(id+"F0.wireOp",EDGE,"E13")])]}),subQ51]});Q59=makeQuery(id+"F48.opFillet","BLEND_EDGE",EDGE,{"blendedFrom":[makeQuery(id+"F47.opFillet","TWEAK_EDGE",EDGE,{"derivedFrom":[makeQuery(id+"F45.opFillet","BLEND_VERTEX",VERTEX,{"blendedFrom":[subQ75,subQ51,subQ74],"blendedInto":[subQ51,subQ74]}),makeQuery(id+"F45.opFillet","BLEND_VERTEX",VERTEX,{"blendedFrom":[subQ75,makeQuery(id+"F42.boolean.opBoolean","MERGE",FACE,{"derivedFrom":[subQ0,subQ8]}),subQ74],"blendedInto":[makeQuery(id+"F42.boolean.opBoolean","MERGE",FACE,{"derivedFrom":[subQ0,subQ8]}),subQ74]})]}),makeQuery(id+"F47.opFillet","BLEND_FACE",FACE,{"disambiguationData":[OSD([subQ5,subQ7]),TDD([makeQuery(id+"F42.boolean.opBoolean","COPY",EDGE,{"disambiguationData":[TD([makeQuery(id+"F5.opLoft","SWEPT_FACE",FACE,{"disambiguationData":[OSD([subQ71,subQ70,sQuery(id+"F3.wireOp",EDGE,"E18.left"),sQuery(id+"F4.wireOp",EDGE,"E21"),subQ69,subQ68])]})])],"derivedFrom":subQ9})])]}),makeQuery(id+"F47.opFillet","BLEND_FACE",FACE,{"disambiguationData":[OSD([subQ5,subQ7]),TDD([makeQuery(id+"F42.boolean.opBoolean","COPY",EDGE,{"disambiguationData":[TD([makeQuery(id+"F6.opLoft","SWEPT_FACE",FACE,{"disambiguationData":[OSD([sQuery(id+"F3.wireOp",EDGE,"E20.15.0"),subQ67,subQ66,sQuery(id+"F4.wireOp",EDGE,"E26.15.0"),subQ65,subQ64])]})])],"derivedFrom":subQ9})])]}),makeQuery(id+"F47.opFillet","BLEND_FACE",FACE,{"disambiguationData":[OSD([subQ5,subQ7]),TDD([makeQuery(id+"F42.boolean.opBoolean","COPY",EDGE,{"disambiguationData":[TD([makeQuery(id+"F7.opLoft","SWEPT_FACE",FACE,{"disambiguationData":[OSD([sQuery(id+"F3.wireOp",EDGE,"E20.14.0"),subQ63,subQ62,sQuery(id+"F4.wireOp",EDGE,"E26.14.0"),subQ61,subQ60])]})])],"derivedFrom":subQ9})])]}),makeQuery(id+"F47.opFillet","BLEND_FACE",FACE,{"disambiguationData":[OSD([subQ5,subQ7]),TDD([makeQuery(id+"F42.boolean.opBoolean","COPY",EDGE,{"disambiguationData":[TD([makeQuery(id+"F8.opLoft","SWEPT_FACE",FACE,{"disambiguationData":[OSD([sQuery(id+"F3.wireOp",EDGE,"E20.13.0"),subQ59,subQ58,sQuery(id+"F4.wireOp",EDGE,"E26.13.0"),subQ57,subQ56])]})])],"derivedFrom":subQ9})])]}),makeQuery(id+"F47.opFillet","BLEND_FACE",FACE,{"disambiguationData":[OSD([subQ5,subQ7]),TDD([makeQuery(id+"F42.boolean.opBoolean","COPY",EDGE,{"disambiguationData":[TD([makeQuery(id+"F9.opLoft","SWEPT_FACE",FACE,{"disambiguationData":[OSD([sQuery(id+"F3.wireOp",EDGE,"E20.12.0"),subQ55,subQ54,sQuery(id+"F4.wireOp",EDGE,"E26.12.0"),subQ53,subQ52])]})])],"derivedFrom":subQ9})])]}),makeQuery(id+"F47.opFillet","BLEND_FACE",FACE,{"disambiguationData":[OSD([subQ5,subQ7]),TDD([makeQuery(id+"F42.boolean.opBoolean","COPY",EDGE,{"disambiguationData":[TD([subQ51])],"derivedFrom":subQ9})])]}),makeQuery(id+"F47.opFillet","BLEND_FACE",FACE,{"disambiguationData":[OSD([subQ5,subQ7]),TDD([makeQuery(id+"F42.boolean.opBoolean","COPY",EDGE,{"disambiguationData":[TD([makeQuery(id+"F11.opLoft","SWEPT_FACE",FACE,{"disambiguationData":[OSD([sQuery(id+"F3.wireOp",EDGE,"E20.10.0"),subQ45,subQ44,sQuery(id+"F4.wireOp",EDGE,"E26.10.0"),subQ43,subQ42])]})])],"derivedFrom":subQ9})])]}),makeQuery(id+"F47.opFillet","BLEND_FACE",FACE,{"disambiguationData":[OSD([subQ5,subQ7]),TDD([makeQuery(id+"F42.boolean.opBoolean","COPY",EDGE,{"disambiguationData":[TD([makeQuery(id+"F12.opLoft","SWEPT_FACE",FACE,{"disambiguationData":[OSD([sQuery(id+"F3.wireOp",EDGE,"E20.9.0"),subQ41,subQ40,sQuery(id+"F4.wireOp",EDGE,"E26.9.0"),subQ39,subQ38])]})])],"derivedFrom":subQ9})])]}),makeQuery(id+"F47.opFillet","BLEND_FACE",FACE,{"disambiguationData":[OSD([subQ5,subQ7]),TDD([makeQuery(id+"F42.boolean.opBoolean","COPY",EDGE,{"disambiguationData":[TD([makeQuery(id+"F13.opLoft","SWEPT_FACE",FACE,{"disambiguationData":[OSD([sQuery(id+"F3.wireOp",EDGE,"E20.8.0"),subQ37,subQ36,sQuery(id+"F4.wireOp",EDGE,"E26.8.0"),subQ35,subQ34])]})])],"derivedFrom":subQ9})])]}),makeQuery(id+"F47.opFillet","BLEND_FACE",FACE,{"disambiguationData":[OSD([subQ5,subQ7]),TDD([makeQuery(id+"F42.boolean.opBoolean","COPY",EDGE,{"disambiguationData":[TD([makeQuery(id+"F14.opLoft","SWEPT_FACE",FACE,{"disambiguationData":[OSD([sQuery(id+"F3.wireOp",EDGE,"E20.7.0"),subQ33,subQ32,sQuery(id+"F4.wireOp",EDGE,"E26.7.0"),subQ31,subQ30])]})])],"derivedFrom":subQ9})])]}),makeQuery(id+"F47.opFillet","BLEND_FACE",FACE,{"disambiguationData":[OSD([subQ5,subQ7]),TDD([makeQuery(id+"F42.boolean.opBoolean","COPY",EDGE,{"disambiguationData":[TD([makeQuery(id+"F15.opLoft","SWEPT_FACE",FACE,{"disambiguationData":[OSD([sQuery(id+"F3.wireOp",EDGE,"E20.6.0"),subQ29,subQ28,sQuery(id+"F4.wireOp",EDGE,"E26.6.0"),subQ27,subQ26])]})])],"derivedFrom":subQ9})])]}),makeQuery(id+"F47.opFillet","BLEND_FACE",FACE,{"disambiguationData":[OSD([subQ5,subQ7]),TDD([makeQuery(id+"F42.boolean.opBoolean","COPY",EDGE,{"disambiguationData":[TD([makeQuery(id+"F16.opLoft","SWEPT_FACE",FACE,{"disambiguationData":[OSD([sQuery(id+"F3.wireOp",EDGE,"E20.5.0"),subQ25,subQ24,sQuery(id+"F4.wireOp",EDGE,"E26.5.0"),subQ23,subQ22])]})])],"derivedFrom":subQ9})])]}),makeQuery(id+"F47.opFillet","BLEND_FACE",FACE,{"disambiguationData":[OSD([subQ5,subQ7]),TDD([makeQuery(id+"F42.boolean.opBoolean","COPY",EDGE,{"disambiguationData":[TD([makeQuery(id+"F17.opLoft","SWEPT_FACE",FACE,{"disambiguationData":[OSD([sQuery(id+"F3.wireOp",EDGE,"E20.4.0"),subQ21,subQ20,sQuery(id+"F4.wireOp",EDGE,"E26.4.0"),subQ19,subQ18])]})])],"derivedFrom":subQ9})])]}),makeQuery(id+"F47.opFillet","BLEND_FACE",FACE,{"disambiguationData":[OSD([subQ5,subQ7]),TDD([makeQuery(id+"F42.boolean.opBoolean","COPY",EDGE,{"disambiguationData":[TD([makeQuery(id+"F18.opLoft","SWEPT_FACE",FACE,{"disambiguationData":[OSD([sQuery(id+"F3.wireOp",EDGE,"E20.3.0"),subQ17,subQ16,sQuery(id+"F4.wireOp",EDGE,"E26.3.0"),subQ15,subQ14])]})])],"derivedFrom":subQ9})])]}),makeQuery(id+"F47.opFillet","BLEND_FACE",FACE,{"disambiguationData":[OSD([subQ5,subQ7]),TDD([makeQuery(id+"F42.boolean.opBoolean","COPY",EDGE,{"disambiguationData":[TD([makeQuery(id+"F19.opLoft","SWEPT_FACE",FACE,{"disambiguationData":[OSD([sQuery(id+"F3.wireOp",EDGE,"E20.2.0"),subQ13,subQ12,sQuery(id+"F4.wireOp",EDGE,"E26.2.0"),subQ11,subQ10])]})])],"derivedFrom":subQ9})])]}),makeQuery(id+"F47.opFillet","BLEND_FACE",FACE,{"disambiguationData":[OSD([subQ5,subQ7]),TDD([makeQuery(id+"F42.boolean.opBoolean","COPY",EDGE,{"disambiguationData":[TD([makeQuery(id+"F20.opLoft","SWEPT_FACE",FACE,{"disambiguationData":[OSD([sQuery(id+"F3.wireOp",EDGE,"E20.1.0"),subQ4,subQ3,sQuery(id+"F4.wireOp",EDGE,"E26.1.0"),subQ2,subQ1])]})])],"derivedFrom":subQ9})])]})],"blendedInto":[makeQuery(id+"F47.opFillet","BLEND_FACE",FACE,{"disambiguationData":[OSD([subQ5,subQ7]),TDD([makeQuery(id+"F42.boolean.opBoolean","COPY",EDGE,{"disambiguationData":[TD([makeQuery(id+"F5.opLoft","SWEPT_FACE",FACE,{"disambiguationData":[OSD([subQ71,subQ70,sQuery(id+"F3.wireOp",EDGE,"E18.left"),sQuery(id+"F4.wireOp",EDGE,"E21"),subQ69,subQ68])]})])],"derivedFrom":subQ9})])]}),makeQuery(id+"F47.opFillet","BLEND_FACE",FACE,{"disambiguationData":[OSD([subQ5,subQ7]),TDD([makeQuery(id+"F42.boolean.opBoolean","COPY",EDGE,{"disambiguationData":[TD([makeQuery(id+"F6.opLoft","SWEPT_FACE",FACE,{"disambiguationData":[OSD([sQuery(id+"F3.wireOp",EDGE,"E20.15.0"),subQ67,subQ66,sQuery(id+"F4.wireOp",EDGE,"E26.15.0"),subQ65,subQ64])]})])],"derivedFrom":subQ9})])]}),makeQuery(id+"F47.opFillet","BLEND_FACE",FACE,{"disambiguationData":[OSD([subQ5,subQ7]),TDD([makeQuery(id+"F42.boolean.opBoolean","COPY",EDGE,{"disambiguationData":[TD([makeQuery(id+"F7.opLoft","SWEPT_FACE",FACE,{"disambiguationData":[OSD([sQuery(id+"F3.wireOp",EDGE,"E20.14.0"),subQ63,subQ62,sQuery(id+"F4.wireOp",EDGE,"E26.14.0"),subQ61,subQ60])]})])],"derivedFrom":subQ9})])]}),makeQuery(id+"F47.opFillet","BLEND_FACE",FACE,{"disambiguationData":[OSD([subQ5,subQ7]),TDD([makeQuery(id+"F42.boolean.opBoolean","COPY",EDGE,{"disambiguationData":[TD([makeQuery(id+"F8.opLoft","SWEPT_FACE",FACE,{"disambiguationData":[OSD([sQuery(id+"F3.wireOp",EDGE,"E20.13.0"),subQ59,subQ58,sQuery(id+"F4.wireOp",EDGE,"E26.13.0"),subQ57,subQ56])]})])],"derivedFrom":subQ9})])]}),makeQuery(id+"F47.opFillet","BLEND_FACE",FACE,{"disambiguationData":[OSD([subQ5,subQ7]),TDD([makeQuery(id+"F42.boolean.opBoolean","COPY",EDGE,{"disambiguationData":[TD([makeQuery(id+"F9.opLoft","SWEPT_FACE",FACE,{"disambiguationData":[OSD([sQuery(id+"F3.wireOp",EDGE,"E20.12.0"),subQ55,subQ54,sQuery(id+"F4.wireOp",EDGE,"E26.12.0"),subQ53,subQ52])]})])],"derivedFrom":subQ9})])]}),makeQuery(id+"F47.opFillet","BLEND_FACE",FACE,{"disambiguationData":[OSD([subQ5,subQ7]),TDD([makeQuery(id+"F42.boolean.opBoolean","COPY",EDGE,{"disambiguationData":[TD([subQ51])],"derivedFrom":subQ9})])]}),makeQuery(id+"F47.opFillet","BLEND_FACE",FACE,{"disambiguationData":[OSD([subQ5,subQ7]),TDD([makeQuery(id+"F42.boolean.opBoolean","COPY",EDGE,{"disambiguationData":[TD([makeQuery(id+"F11.opLoft","SWEPT_FACE",FACE,{"disambiguationData":[OSD([sQuery(id+"F3.wireOp",EDGE,"E20.10.0"),subQ45,subQ44,sQuery(id+"F4.wireOp",EDGE,"E26.10.0"),subQ43,subQ42])]})])],"derivedFrom":subQ9})])]}),makeQuery(id+"F47.opFillet","BLEND_FACE",FACE,{"disambiguationData":[OSD([subQ5,subQ7]),TDD([makeQuery(id+"F42.boolean.opBoolean","COPY",EDGE,{"disambiguationData":[TD([makeQuery(id+"F12.opLoft","SWEPT_FACE",FACE,{"disambiguationData":[OSD([sQuery(id+"F3.wireOp",EDGE,"E20.9.0"),subQ41,subQ40,sQuery(id+"F4.wireOp",EDGE,"E26.9.0"),subQ39,subQ38])]})])],"derivedFrom":subQ9})])]}),makeQuery(id+"F47.opFillet","BLEND_FACE",FACE,{"disambiguationData":[OSD([subQ5,subQ7]),TDD([makeQuery(id+"F42.boolean.opBoolean","COPY",EDGE,{"disambiguationData":[TD([makeQuery(id+"F13.opLoft","SWEPT_FACE",FACE,{"disambiguationData":[OSD([sQuery(id+"F3.wireOp",EDGE,"E20.8.0"),subQ37,subQ36,sQuery(id+"F4.wireOp",EDGE,"E26.8.0"),subQ35,subQ34])]})])],"derivedFrom":subQ9})])]}),makeQuery(id+"F47.opFillet","BLEND_FACE",FACE,{"disambiguationData":[OSD([subQ5,subQ7]),TDD([makeQuery(id+"F42.boolean.opBoolean","COPY",EDGE,{"disambiguationData":[TD([makeQuery(id+"F14.opLoft","SWEPT_FACE",FACE,{"disambiguationData":[OSD([sQuery(id+"F3.wireOp",EDGE,"E20.7.0"),subQ33,subQ32,sQuery(id+"F4.wireOp",EDGE,"E26.7.0"),subQ31,subQ30])]})])],"derivedFrom":subQ9})])]}),makeQuery(id+"F47.opFillet","BLEND_FACE",FACE,{"disambiguationData":[OSD([subQ5,subQ7]),TDD([makeQuery(id+"F42.boolean.opBoolean","COPY",EDGE,{"disambiguationData":[TD([makeQuery(id+"F15.opLoft","SWEPT_FACE",FACE,{"disambiguationData":[OSD([sQuery(id+"F3.wireOp",EDGE,"E20.6.0"),subQ29,subQ28,sQuery(id+"F4.wireOp",EDGE,"E26.6.0"),subQ27,subQ26])]})])],"derivedFrom":subQ9})])]}),makeQuery(id+"F47.opFillet","BLEND_FACE",FACE,{"disambiguationData":[OSD([subQ5,subQ7]),TDD([makeQuery(id+"F42.boolean.opBoolean","COPY",EDGE,{"disambiguationData":[TD([makeQuery(id+"F16.opLoft","SWEPT_FACE",FACE,{"disambiguationData":[OSD([sQuery(id+"F3.wireOp",EDGE,"E20.5.0"),subQ25,subQ24,sQuery(id+"F4.wireOp",EDGE,"E26.5.0"),subQ23,subQ22])]})])],"derivedFrom":subQ9})])]}),makeQuery(id+"F47.opFillet","BLEND_FACE",FACE,{"disambiguationData":[OSD([subQ5,subQ7]),TDD([makeQuery(id+"F42.boolean.opBoolean","COPY",EDGE,{"disambiguationData":[TD([makeQuery(id+"F17.opLoft","SWEPT_FACE",FACE,{"disambiguationData":[OSD([sQuery(id+"F3.wireOp",EDGE,"E20.4.0"),subQ21,subQ20,sQuery(id+"F4.wireOp",EDGE,"E26.4.0"),subQ19,subQ18])]})])],"derivedFrom":subQ9})])]}),makeQuery(id+"F47.opFillet","BLEND_FACE",FACE,{"disambiguationData":[OSD([subQ5,subQ7]),TDD([makeQuery(id+"F42.boolean.opBoolean","COPY",EDGE,{"disambiguationData":[TD([makeQuery(id+"F18.opLoft","SWEPT_FACE",FACE,{"disambiguationData":[OSD([sQuery(id+"F3.wireOp",EDGE,"E20.3.0"),subQ17,subQ16,sQuery(id+"F4.wireOp",EDGE,"E26.3.0"),subQ15,subQ14])]})])],"derivedFrom":subQ9})])]}),makeQuery(id+"F47.opFillet","BLEND_FACE",FACE,{"disambiguationData":[OSD([subQ5,subQ7]),TDD([makeQuery(id+"F42.boolean.opBoolean","COPY",EDGE,{"disambiguationData":[TD([makeQuery(id+"F19.opLoft","SWEPT_FACE",FACE,{"disambiguationData":[OSD([sQuery(id+"F3.wireOp",EDGE,"E20.2.0"),subQ13,subQ12,sQuery(id+"F4.wireOp",EDGE,"E26.2.0"),subQ11,subQ10])]})])],"derivedFrom":subQ9})])]}),makeQuery(id+"F47.opFillet","BLEND_FACE",FACE,{"disambiguationData":[OSD([subQ5,subQ7]),TDD([makeQuery(id+"F42.boolean.opBoolean","COPY",EDGE,{"disambiguationData":[TD([makeQuery(id+"F20.opLoft","SWEPT_FACE",FACE,{"disambiguationData":[OSD([sQuery(id+"F3.wireOp",EDGE,"E20.1.0"),subQ4,subQ3,sQuery(id+"F4.wireOp",EDGE,"E26.1.0"),subQ2,subQ1])]})])],"derivedFrom":subQ9})])]})]});}
            var Q60;
            {var subQ0=makeQuery(id+"F40.opExtrude","CAP_FACE",FACE,{"disambiguationData":[OSD([sQuery(id+"F39.wireOp",EDGE,"E29"),sQuery(id+"F39.wireOp",EDGE,"E30")])],"isStart":false});var subQ1=sQuery(id+"F4.wireOp",EDGE,"E26.1.3");var subQ2=sQuery(id+"F4.wireOp",EDGE,"E26.1.2");var subQ3=sQuery(id+"F3.wireOp",EDGE,"E20.1.3");var subQ4=sQuery(id+"F3.wireOp",EDGE,"E20.1.1");var subQ5=sQuery(id+"F41.wireOp",EDGE,"E35");var subQ6=makeQuery(id+"F42.opRevolve","SWEPT_FACE",FACE,{"disambiguationData":[OSD([subQ5])]});var subQ7=sQuery(id+"F41.wireOp",EDGE,"E36");var subQ8=makeQuery(id+"F42.opRevolve","SWEPT_FACE",FACE,{"disambiguationData":[OSD([subQ7])]});var subQ9=makeQuery(id+"F42.opRevolve","SWEPT_EDGE",EDGE,{"disambiguationData":[OSD([subQ5,subQ7])]});var subQ10=sQuery(id+"F4.wireOp",EDGE,"E26.2.3");var subQ11=sQuery(id+"F4.wireOp",EDGE,"E26.2.2");var subQ12=sQuery(id+"F3.wireOp",EDGE,"E20.2.3");var subQ13=sQuery(id+"F3.wireOp",EDGE,"E20.2.1");var subQ14=sQuery(id+"F4.wireOp",EDGE,"E26.3.3");var subQ15=sQuery(id+"F4.wireOp",EDGE,"E26.3.2");var subQ16=sQuery(id+"F3.wireOp",EDGE,"E20.3.3");var subQ17=sQuery(id+"F3.wireOp",EDGE,"E20.3.1");var subQ18=sQuery(id+"F4.wireOp",EDGE,"E26.4.3");var subQ19=sQuery(id+"F4.wireOp",EDGE,"E26.4.2");var subQ20=sQuery(id+"F3.wireOp",EDGE,"E20.4.3");var subQ21=sQuery(id+"F3.wireOp",EDGE,"E20.4.1");var subQ22=sQuery(id+"F4.wireOp",EDGE,"E26.5.3");var subQ23=sQuery(id+"F4.wireOp",EDGE,"E26.5.2");var subQ24=sQuery(id+"F3.wireOp",EDGE,"E20.5.3");var subQ25=sQuery(id+"F3.wireOp",EDGE,"E20.5.1");var subQ26=sQuery(id+"F4.wireOp",EDGE,"E26.6.3");var subQ27=sQuery(id+"F4.wireOp",EDGE,"E26.6.2");var subQ28=sQuery(id+"F3.wireOp",EDGE,"E20.6.3");var subQ29=sQuery(id+"F3.wireOp",EDGE,"E20.6.1");var subQ30=sQuery(id+"F4.wireOp",EDGE,"E26.7.3");var subQ31=sQuery(id+"F4.wireOp",EDGE,"E26.7.2");var subQ32=sQuery(id+"F3.wireOp",EDGE,"E20.7.3");var subQ33=sQuery(id+"F3.wireOp",EDGE,"E20.7.1");var subQ34=sQuery(id+"F4.wireOp",EDGE,"E26.8.3");var subQ35=sQuery(id+"F4.wireOp",EDGE,"E26.8.2");var subQ36=sQuery(id+"F3.wireOp",EDGE,"E20.8.3");var subQ37=sQuery(id+"F3.wireOp",EDGE,"E20.8.1");var subQ38=sQuery(id+"F4.wireOp",EDGE,"E26.9.3");var subQ39=sQuery(id+"F4.wireOp",EDGE,"E26.9.2");var subQ40=sQuery(id+"F3.wireOp",EDGE,"E20.9.3");var subQ41=sQuery(id+"F3.wireOp",EDGE,"E20.9.1");var subQ42=sQuery(id+"F4.wireOp",EDGE,"E26.10.3");var subQ43=sQuery(id+"F4.wireOp",EDGE,"E26.10.2");var subQ44=sQuery(id+"F3.wireOp",EDGE,"E20.10.3");var subQ45=sQuery(id+"F3.wireOp",EDGE,"E20.10.1");var subQ47=makeQuery(id+"F11.opLoft","SWEPT_FACE",FACE,{"disambiguationData":[OSD([sQuery(id+"F3.wireOp",EDGE,"E20.10.0"),subQ45,subQ44,sQuery(id+"F4.wireOp",EDGE,"E26.10.0"),subQ43,subQ42])]});var subQ48=sQuery(id+"F4.wireOp",EDGE,"E26.11.3");var subQ49=sQuery(id+"F4.wireOp",EDGE,"E26.11.2");var subQ50=sQuery(id+"F3.wireOp",EDGE,"E20.11.3");var subQ51=sQuery(id+"F3.wireOp",EDGE,"E20.11.1");var subQ52=sQuery(id+"F4.wireOp",EDGE,"E26.12.3");var subQ53=sQuery(id+"F4.wireOp",EDGE,"E26.12.2");var subQ54=sQuery(id+"F3.wireOp",EDGE,"E20.12.3");var subQ55=sQuery(id+"F3.wireOp",EDGE,"E20.12.1");var subQ56=sQuery(id+"F4.wireOp",EDGE,"E26.13.3");var subQ57=sQuery(id+"F4.wireOp",EDGE,"E26.13.2");var subQ58=sQuery(id+"F3.wireOp",EDGE,"E20.13.3");var subQ59=sQuery(id+"F3.wireOp",EDGE,"E20.13.1");var subQ60=sQuery(id+"F4.wireOp",EDGE,"E26.14.3");var subQ61=sQuery(id+"F4.wireOp",EDGE,"E26.14.2");var subQ62=sQuery(id+"F3.wireOp",EDGE,"E20.14.3");var subQ63=sQuery(id+"F3.wireOp",EDGE,"E20.14.1");var subQ64=sQuery(id+"F4.wireOp",EDGE,"E26.15.3");var subQ65=sQuery(id+"F4.wireOp",EDGE,"E26.15.2");var subQ66=sQuery(id+"F3.wireOp",EDGE,"E20.15.3");var subQ67=sQuery(id+"F3.wireOp",EDGE,"E20.15.1");var subQ68=sQuery(id+"F4.wireOp",EDGE,"E23");var subQ69=sQuery(id+"F4.wireOp",EDGE,"E22");var subQ70=sQuery(id+"F3.wireOp",EDGE,"E18.top");var subQ71=sQuery(id+"F3.wireOp",EDGE,"E18.bottom");var subQ74=makeQuery(id+"F42.boolean.opBoolean","COPY",FACE,{"disambiguationData":[TD([subQ47])],"derivedFrom":subQ6});var subQ75=makeQuery(id+"F11.boolean.opBoolean","INTERSECT",EDGE,{"derivedFrom":[makeQuery(id+"F1.opRevolve","SWEPT_FACE",FACE,{"disambiguationData":[OSD([sQuery(id+"F0.wireOp",EDGE,"E13")])]}),subQ47]});Q60=makeQuery(id+"F48.opFillet","BLEND_EDGE",EDGE,{"blendedFrom":[makeQuery(id+"F47.opFillet","TWEAK_EDGE",EDGE,{"derivedFrom":[makeQuery(id+"F45.opFillet","BLEND_VERTEX",VERTEX,{"blendedFrom":[subQ75,subQ47,subQ74],"blendedInto":[subQ47,subQ74]}),makeQuery(id+"F45.opFillet","BLEND_VERTEX",VERTEX,{"blendedFrom":[subQ75,makeQuery(id+"F42.boolean.opBoolean","MERGE",FACE,{"derivedFrom":[subQ0,subQ8]}),subQ74],"blendedInto":[makeQuery(id+"F42.boolean.opBoolean","MERGE",FACE,{"derivedFrom":[subQ0,subQ8]}),subQ74]})]}),makeQuery(id+"F47.opFillet","BLEND_FACE",FACE,{"disambiguationData":[OSD([subQ5,subQ7]),TDD([makeQuery(id+"F42.boolean.opBoolean","COPY",EDGE,{"disambiguationData":[TD([makeQuery(id+"F5.opLoft","SWEPT_FACE",FACE,{"disambiguationData":[OSD([subQ71,subQ70,sQuery(id+"F3.wireOp",EDGE,"E18.left"),sQuery(id+"F4.wireOp",EDGE,"E21"),subQ69,subQ68])]})])],"derivedFrom":subQ9})])]}),makeQuery(id+"F47.opFillet","BLEND_FACE",FACE,{"disambiguationData":[OSD([subQ5,subQ7]),TDD([makeQuery(id+"F42.boolean.opBoolean","COPY",EDGE,{"disambiguationData":[TD([makeQuery(id+"F6.opLoft","SWEPT_FACE",FACE,{"disambiguationData":[OSD([sQuery(id+"F3.wireOp",EDGE,"E20.15.0"),subQ67,subQ66,sQuery(id+"F4.wireOp",EDGE,"E26.15.0"),subQ65,subQ64])]})])],"derivedFrom":subQ9})])]}),makeQuery(id+"F47.opFillet","BLEND_FACE",FACE,{"disambiguationData":[OSD([subQ5,subQ7]),TDD([makeQuery(id+"F42.boolean.opBoolean","COPY",EDGE,{"disambiguationData":[TD([makeQuery(id+"F7.opLoft","SWEPT_FACE",FACE,{"disambiguationData":[OSD([sQuery(id+"F3.wireOp",EDGE,"E20.14.0"),subQ63,subQ62,sQuery(id+"F4.wireOp",EDGE,"E26.14.0"),subQ61,subQ60])]})])],"derivedFrom":subQ9})])]}),makeQuery(id+"F47.opFillet","BLEND_FACE",FACE,{"disambiguationData":[OSD([subQ5,subQ7]),TDD([makeQuery(id+"F42.boolean.opBoolean","COPY",EDGE,{"disambiguationData":[TD([makeQuery(id+"F8.opLoft","SWEPT_FACE",FACE,{"disambiguationData":[OSD([sQuery(id+"F3.wireOp",EDGE,"E20.13.0"),subQ59,subQ58,sQuery(id+"F4.wireOp",EDGE,"E26.13.0"),subQ57,subQ56])]})])],"derivedFrom":subQ9})])]}),makeQuery(id+"F47.opFillet","BLEND_FACE",FACE,{"disambiguationData":[OSD([subQ5,subQ7]),TDD([makeQuery(id+"F42.boolean.opBoolean","COPY",EDGE,{"disambiguationData":[TD([makeQuery(id+"F9.opLoft","SWEPT_FACE",FACE,{"disambiguationData":[OSD([sQuery(id+"F3.wireOp",EDGE,"E20.12.0"),subQ55,subQ54,sQuery(id+"F4.wireOp",EDGE,"E26.12.0"),subQ53,subQ52])]})])],"derivedFrom":subQ9})])]}),makeQuery(id+"F47.opFillet","BLEND_FACE",FACE,{"disambiguationData":[OSD([subQ5,subQ7]),TDD([makeQuery(id+"F42.boolean.opBoolean","COPY",EDGE,{"disambiguationData":[TD([makeQuery(id+"F10.opLoft","SWEPT_FACE",FACE,{"disambiguationData":[OSD([sQuery(id+"F3.wireOp",EDGE,"E20.11.0"),subQ51,subQ50,sQuery(id+"F4.wireOp",EDGE,"E26.11.0"),subQ49,subQ48])]})])],"derivedFrom":subQ9})])]}),makeQuery(id+"F47.opFillet","BLEND_FACE",FACE,{"disambiguationData":[OSD([subQ5,subQ7]),TDD([makeQuery(id+"F42.boolean.opBoolean","COPY",EDGE,{"disambiguationData":[TD([subQ47])],"derivedFrom":subQ9})])]}),makeQuery(id+"F47.opFillet","BLEND_FACE",FACE,{"disambiguationData":[OSD([subQ5,subQ7]),TDD([makeQuery(id+"F42.boolean.opBoolean","COPY",EDGE,{"disambiguationData":[TD([makeQuery(id+"F12.opLoft","SWEPT_FACE",FACE,{"disambiguationData":[OSD([sQuery(id+"F3.wireOp",EDGE,"E20.9.0"),subQ41,subQ40,sQuery(id+"F4.wireOp",EDGE,"E26.9.0"),subQ39,subQ38])]})])],"derivedFrom":subQ9})])]}),makeQuery(id+"F47.opFillet","BLEND_FACE",FACE,{"disambiguationData":[OSD([subQ5,subQ7]),TDD([makeQuery(id+"F42.boolean.opBoolean","COPY",EDGE,{"disambiguationData":[TD([makeQuery(id+"F13.opLoft","SWEPT_FACE",FACE,{"disambiguationData":[OSD([sQuery(id+"F3.wireOp",EDGE,"E20.8.0"),subQ37,subQ36,sQuery(id+"F4.wireOp",EDGE,"E26.8.0"),subQ35,subQ34])]})])],"derivedFrom":subQ9})])]}),makeQuery(id+"F47.opFillet","BLEND_FACE",FACE,{"disambiguationData":[OSD([subQ5,subQ7]),TDD([makeQuery(id+"F42.boolean.opBoolean","COPY",EDGE,{"disambiguationData":[TD([makeQuery(id+"F14.opLoft","SWEPT_FACE",FACE,{"disambiguationData":[OSD([sQuery(id+"F3.wireOp",EDGE,"E20.7.0"),subQ33,subQ32,sQuery(id+"F4.wireOp",EDGE,"E26.7.0"),subQ31,subQ30])]})])],"derivedFrom":subQ9})])]}),makeQuery(id+"F47.opFillet","BLEND_FACE",FACE,{"disambiguationData":[OSD([subQ5,subQ7]),TDD([makeQuery(id+"F42.boolean.opBoolean","COPY",EDGE,{"disambiguationData":[TD([makeQuery(id+"F15.opLoft","SWEPT_FACE",FACE,{"disambiguationData":[OSD([sQuery(id+"F3.wireOp",EDGE,"E20.6.0"),subQ29,subQ28,sQuery(id+"F4.wireOp",EDGE,"E26.6.0"),subQ27,subQ26])]})])],"derivedFrom":subQ9})])]}),makeQuery(id+"F47.opFillet","BLEND_FACE",FACE,{"disambiguationData":[OSD([subQ5,subQ7]),TDD([makeQuery(id+"F42.boolean.opBoolean","COPY",EDGE,{"disambiguationData":[TD([makeQuery(id+"F16.opLoft","SWEPT_FACE",FACE,{"disambiguationData":[OSD([sQuery(id+"F3.wireOp",EDGE,"E20.5.0"),subQ25,subQ24,sQuery(id+"F4.wireOp",EDGE,"E26.5.0"),subQ23,subQ22])]})])],"derivedFrom":subQ9})])]}),makeQuery(id+"F47.opFillet","BLEND_FACE",FACE,{"disambiguationData":[OSD([subQ5,subQ7]),TDD([makeQuery(id+"F42.boolean.opBoolean","COPY",EDGE,{"disambiguationData":[TD([makeQuery(id+"F17.opLoft","SWEPT_FACE",FACE,{"disambiguationData":[OSD([sQuery(id+"F3.wireOp",EDGE,"E20.4.0"),subQ21,subQ20,sQuery(id+"F4.wireOp",EDGE,"E26.4.0"),subQ19,subQ18])]})])],"derivedFrom":subQ9})])]}),makeQuery(id+"F47.opFillet","BLEND_FACE",FACE,{"disambiguationData":[OSD([subQ5,subQ7]),TDD([makeQuery(id+"F42.boolean.opBoolean","COPY",EDGE,{"disambiguationData":[TD([makeQuery(id+"F18.opLoft","SWEPT_FACE",FACE,{"disambiguationData":[OSD([sQuery(id+"F3.wireOp",EDGE,"E20.3.0"),subQ17,subQ16,sQuery(id+"F4.wireOp",EDGE,"E26.3.0"),subQ15,subQ14])]})])],"derivedFrom":subQ9})])]}),makeQuery(id+"F47.opFillet","BLEND_FACE",FACE,{"disambiguationData":[OSD([subQ5,subQ7]),TDD([makeQuery(id+"F42.boolean.opBoolean","COPY",EDGE,{"disambiguationData":[TD([makeQuery(id+"F19.opLoft","SWEPT_FACE",FACE,{"disambiguationData":[OSD([sQuery(id+"F3.wireOp",EDGE,"E20.2.0"),subQ13,subQ12,sQuery(id+"F4.wireOp",EDGE,"E26.2.0"),subQ11,subQ10])]})])],"derivedFrom":subQ9})])]}),makeQuery(id+"F47.opFillet","BLEND_FACE",FACE,{"disambiguationData":[OSD([subQ5,subQ7]),TDD([makeQuery(id+"F42.boolean.opBoolean","COPY",EDGE,{"disambiguationData":[TD([makeQuery(id+"F20.opLoft","SWEPT_FACE",FACE,{"disambiguationData":[OSD([sQuery(id+"F3.wireOp",EDGE,"E20.1.0"),subQ4,subQ3,sQuery(id+"F4.wireOp",EDGE,"E26.1.0"),subQ2,subQ1])]})])],"derivedFrom":subQ9})])]})],"blendedInto":[makeQuery(id+"F47.opFillet","BLEND_FACE",FACE,{"disambiguationData":[OSD([subQ5,subQ7]),TDD([makeQuery(id+"F42.boolean.opBoolean","COPY",EDGE,{"disambiguationData":[TD([makeQuery(id+"F5.opLoft","SWEPT_FACE",FACE,{"disambiguationData":[OSD([subQ71,subQ70,sQuery(id+"F3.wireOp",EDGE,"E18.left"),sQuery(id+"F4.wireOp",EDGE,"E21"),subQ69,subQ68])]})])],"derivedFrom":subQ9})])]}),makeQuery(id+"F47.opFillet","BLEND_FACE",FACE,{"disambiguationData":[OSD([subQ5,subQ7]),TDD([makeQuery(id+"F42.boolean.opBoolean","COPY",EDGE,{"disambiguationData":[TD([makeQuery(id+"F6.opLoft","SWEPT_FACE",FACE,{"disambiguationData":[OSD([sQuery(id+"F3.wireOp",EDGE,"E20.15.0"),subQ67,subQ66,sQuery(id+"F4.wireOp",EDGE,"E26.15.0"),subQ65,subQ64])]})])],"derivedFrom":subQ9})])]}),makeQuery(id+"F47.opFillet","BLEND_FACE",FACE,{"disambiguationData":[OSD([subQ5,subQ7]),TDD([makeQuery(id+"F42.boolean.opBoolean","COPY",EDGE,{"disambiguationData":[TD([makeQuery(id+"F7.opLoft","SWEPT_FACE",FACE,{"disambiguationData":[OSD([sQuery(id+"F3.wireOp",EDGE,"E20.14.0"),subQ63,subQ62,sQuery(id+"F4.wireOp",EDGE,"E26.14.0"),subQ61,subQ60])]})])],"derivedFrom":subQ9})])]}),makeQuery(id+"F47.opFillet","BLEND_FACE",FACE,{"disambiguationData":[OSD([subQ5,subQ7]),TDD([makeQuery(id+"F42.boolean.opBoolean","COPY",EDGE,{"disambiguationData":[TD([makeQuery(id+"F8.opLoft","SWEPT_FACE",FACE,{"disambiguationData":[OSD([sQuery(id+"F3.wireOp",EDGE,"E20.13.0"),subQ59,subQ58,sQuery(id+"F4.wireOp",EDGE,"E26.13.0"),subQ57,subQ56])]})])],"derivedFrom":subQ9})])]}),makeQuery(id+"F47.opFillet","BLEND_FACE",FACE,{"disambiguationData":[OSD([subQ5,subQ7]),TDD([makeQuery(id+"F42.boolean.opBoolean","COPY",EDGE,{"disambiguationData":[TD([makeQuery(id+"F9.opLoft","SWEPT_FACE",FACE,{"disambiguationData":[OSD([sQuery(id+"F3.wireOp",EDGE,"E20.12.0"),subQ55,subQ54,sQuery(id+"F4.wireOp",EDGE,"E26.12.0"),subQ53,subQ52])]})])],"derivedFrom":subQ9})])]}),makeQuery(id+"F47.opFillet","BLEND_FACE",FACE,{"disambiguationData":[OSD([subQ5,subQ7]),TDD([makeQuery(id+"F42.boolean.opBoolean","COPY",EDGE,{"disambiguationData":[TD([makeQuery(id+"F10.opLoft","SWEPT_FACE",FACE,{"disambiguationData":[OSD([sQuery(id+"F3.wireOp",EDGE,"E20.11.0"),subQ51,subQ50,sQuery(id+"F4.wireOp",EDGE,"E26.11.0"),subQ49,subQ48])]})])],"derivedFrom":subQ9})])]}),makeQuery(id+"F47.opFillet","BLEND_FACE",FACE,{"disambiguationData":[OSD([subQ5,subQ7]),TDD([makeQuery(id+"F42.boolean.opBoolean","COPY",EDGE,{"disambiguationData":[TD([subQ47])],"derivedFrom":subQ9})])]}),makeQuery(id+"F47.opFillet","BLEND_FACE",FACE,{"disambiguationData":[OSD([subQ5,subQ7]),TDD([makeQuery(id+"F42.boolean.opBoolean","COPY",EDGE,{"disambiguationData":[TD([makeQuery(id+"F12.opLoft","SWEPT_FACE",FACE,{"disambiguationData":[OSD([sQuery(id+"F3.wireOp",EDGE,"E20.9.0"),subQ41,subQ40,sQuery(id+"F4.wireOp",EDGE,"E26.9.0"),subQ39,subQ38])]})])],"derivedFrom":subQ9})])]}),makeQuery(id+"F47.opFillet","BLEND_FACE",FACE,{"disambiguationData":[OSD([subQ5,subQ7]),TDD([makeQuery(id+"F42.boolean.opBoolean","COPY",EDGE,{"disambiguationData":[TD([makeQuery(id+"F13.opLoft","SWEPT_FACE",FACE,{"disambiguationData":[OSD([sQuery(id+"F3.wireOp",EDGE,"E20.8.0"),subQ37,subQ36,sQuery(id+"F4.wireOp",EDGE,"E26.8.0"),subQ35,subQ34])]})])],"derivedFrom":subQ9})])]}),makeQuery(id+"F47.opFillet","BLEND_FACE",FACE,{"disambiguationData":[OSD([subQ5,subQ7]),TDD([makeQuery(id+"F42.boolean.opBoolean","COPY",EDGE,{"disambiguationData":[TD([makeQuery(id+"F14.opLoft","SWEPT_FACE",FACE,{"disambiguationData":[OSD([sQuery(id+"F3.wireOp",EDGE,"E20.7.0"),subQ33,subQ32,sQuery(id+"F4.wireOp",EDGE,"E26.7.0"),subQ31,subQ30])]})])],"derivedFrom":subQ9})])]}),makeQuery(id+"F47.opFillet","BLEND_FACE",FACE,{"disambiguationData":[OSD([subQ5,subQ7]),TDD([makeQuery(id+"F42.boolean.opBoolean","COPY",EDGE,{"disambiguationData":[TD([makeQuery(id+"F15.opLoft","SWEPT_FACE",FACE,{"disambiguationData":[OSD([sQuery(id+"F3.wireOp",EDGE,"E20.6.0"),subQ29,subQ28,sQuery(id+"F4.wireOp",EDGE,"E26.6.0"),subQ27,subQ26])]})])],"derivedFrom":subQ9})])]}),makeQuery(id+"F47.opFillet","BLEND_FACE",FACE,{"disambiguationData":[OSD([subQ5,subQ7]),TDD([makeQuery(id+"F42.boolean.opBoolean","COPY",EDGE,{"disambiguationData":[TD([makeQuery(id+"F16.opLoft","SWEPT_FACE",FACE,{"disambiguationData":[OSD([sQuery(id+"F3.wireOp",EDGE,"E20.5.0"),subQ25,subQ24,sQuery(id+"F4.wireOp",EDGE,"E26.5.0"),subQ23,subQ22])]})])],"derivedFrom":subQ9})])]}),makeQuery(id+"F47.opFillet","BLEND_FACE",FACE,{"disambiguationData":[OSD([subQ5,subQ7]),TDD([makeQuery(id+"F42.boolean.opBoolean","COPY",EDGE,{"disambiguationData":[TD([makeQuery(id+"F17.opLoft","SWEPT_FACE",FACE,{"disambiguationData":[OSD([sQuery(id+"F3.wireOp",EDGE,"E20.4.0"),subQ21,subQ20,sQuery(id+"F4.wireOp",EDGE,"E26.4.0"),subQ19,subQ18])]})])],"derivedFrom":subQ9})])]}),makeQuery(id+"F47.opFillet","BLEND_FACE",FACE,{"disambiguationData":[OSD([subQ5,subQ7]),TDD([makeQuery(id+"F42.boolean.opBoolean","COPY",EDGE,{"disambiguationData":[TD([makeQuery(id+"F18.opLoft","SWEPT_FACE",FACE,{"disambiguationData":[OSD([sQuery(id+"F3.wireOp",EDGE,"E20.3.0"),subQ17,subQ16,sQuery(id+"F4.wireOp",EDGE,"E26.3.0"),subQ15,subQ14])]})])],"derivedFrom":subQ9})])]}),makeQuery(id+"F47.opFillet","BLEND_FACE",FACE,{"disambiguationData":[OSD([subQ5,subQ7]),TDD([makeQuery(id+"F42.boolean.opBoolean","COPY",EDGE,{"disambiguationData":[TD([makeQuery(id+"F19.opLoft","SWEPT_FACE",FACE,{"disambiguationData":[OSD([sQuery(id+"F3.wireOp",EDGE,"E20.2.0"),subQ13,subQ12,sQuery(id+"F4.wireOp",EDGE,"E26.2.0"),subQ11,subQ10])]})])],"derivedFrom":subQ9})])]}),makeQuery(id+"F47.opFillet","BLEND_FACE",FACE,{"disambiguationData":[OSD([subQ5,subQ7]),TDD([makeQuery(id+"F42.boolean.opBoolean","COPY",EDGE,{"disambiguationData":[TD([makeQuery(id+"F20.opLoft","SWEPT_FACE",FACE,{"disambiguationData":[OSD([sQuery(id+"F3.wireOp",EDGE,"E20.1.0"),subQ4,subQ3,sQuery(id+"F4.wireOp",EDGE,"E26.1.0"),subQ2,subQ1])]})])],"derivedFrom":subQ9})])]})]});}
            var Q61;
            {var subQ0=makeQuery(id+"F40.opExtrude","CAP_FACE",FACE,{"disambiguationData":[OSD([sQuery(id+"F39.wireOp",EDGE,"E29"),sQuery(id+"F39.wireOp",EDGE,"E30")])],"isStart":false});var subQ1=sQuery(id+"F4.wireOp",EDGE,"E26.1.3");var subQ2=sQuery(id+"F4.wireOp",EDGE,"E26.1.2");var subQ3=sQuery(id+"F3.wireOp",EDGE,"E20.1.3");var subQ4=sQuery(id+"F3.wireOp",EDGE,"E20.1.1");var subQ5=sQuery(id+"F41.wireOp",EDGE,"E35");var subQ6=makeQuery(id+"F42.opRevolve","SWEPT_FACE",FACE,{"disambiguationData":[OSD([subQ5])]});var subQ7=sQuery(id+"F41.wireOp",EDGE,"E36");var subQ8=makeQuery(id+"F42.opRevolve","SWEPT_FACE",FACE,{"disambiguationData":[OSD([subQ7])]});var subQ9=makeQuery(id+"F42.opRevolve","SWEPT_EDGE",EDGE,{"disambiguationData":[OSD([subQ5,subQ7])]});var subQ10=sQuery(id+"F4.wireOp",EDGE,"E26.2.3");var subQ11=sQuery(id+"F4.wireOp",EDGE,"E26.2.2");var subQ12=sQuery(id+"F3.wireOp",EDGE,"E20.2.3");var subQ13=sQuery(id+"F3.wireOp",EDGE,"E20.2.1");var subQ14=sQuery(id+"F4.wireOp",EDGE,"E26.3.3");var subQ15=sQuery(id+"F4.wireOp",EDGE,"E26.3.2");var subQ16=sQuery(id+"F3.wireOp",EDGE,"E20.3.3");var subQ17=sQuery(id+"F3.wireOp",EDGE,"E20.3.1");var subQ18=sQuery(id+"F4.wireOp",EDGE,"E26.4.3");var subQ19=sQuery(id+"F4.wireOp",EDGE,"E26.4.2");var subQ20=sQuery(id+"F3.wireOp",EDGE,"E20.4.3");var subQ21=sQuery(id+"F3.wireOp",EDGE,"E20.4.1");var subQ22=sQuery(id+"F4.wireOp",EDGE,"E26.5.3");var subQ23=sQuery(id+"F4.wireOp",EDGE,"E26.5.2");var subQ24=sQuery(id+"F3.wireOp",EDGE,"E20.5.3");var subQ25=sQuery(id+"F3.wireOp",EDGE,"E20.5.1");var subQ26=sQuery(id+"F4.wireOp",EDGE,"E26.6.3");var subQ27=sQuery(id+"F4.wireOp",EDGE,"E26.6.2");var subQ28=sQuery(id+"F3.wireOp",EDGE,"E20.6.3");var subQ29=sQuery(id+"F3.wireOp",EDGE,"E20.6.1");var subQ30=sQuery(id+"F4.wireOp",EDGE,"E26.7.3");var subQ31=sQuery(id+"F4.wireOp",EDGE,"E26.7.2");var subQ32=sQuery(id+"F3.wireOp",EDGE,"E20.7.3");var subQ33=sQuery(id+"F3.wireOp",EDGE,"E20.7.1");var subQ34=sQuery(id+"F4.wireOp",EDGE,"E26.8.3");var subQ35=sQuery(id+"F4.wireOp",EDGE,"E26.8.2");var subQ36=sQuery(id+"F3.wireOp",EDGE,"E20.8.3");var subQ37=sQuery(id+"F3.wireOp",EDGE,"E20.8.1");var subQ38=sQuery(id+"F4.wireOp",EDGE,"E26.9.3");var subQ39=sQuery(id+"F4.wireOp",EDGE,"E26.9.2");var subQ40=sQuery(id+"F3.wireOp",EDGE,"E20.9.3");var subQ41=sQuery(id+"F3.wireOp",EDGE,"E20.9.1");var subQ43=makeQuery(id+"F12.opLoft","SWEPT_FACE",FACE,{"disambiguationData":[OSD([sQuery(id+"F3.wireOp",EDGE,"E20.9.0"),subQ41,subQ40,sQuery(id+"F4.wireOp",EDGE,"E26.9.0"),subQ39,subQ38])]});var subQ44=sQuery(id+"F4.wireOp",EDGE,"E26.10.3");var subQ45=sQuery(id+"F4.wireOp",EDGE,"E26.10.2");var subQ46=sQuery(id+"F3.wireOp",EDGE,"E20.10.3");var subQ47=sQuery(id+"F3.wireOp",EDGE,"E20.10.1");var subQ48=sQuery(id+"F4.wireOp",EDGE,"E26.11.3");var subQ49=sQuery(id+"F4.wireOp",EDGE,"E26.11.2");var subQ50=sQuery(id+"F3.wireOp",EDGE,"E20.11.3");var subQ51=sQuery(id+"F3.wireOp",EDGE,"E20.11.1");var subQ52=sQuery(id+"F4.wireOp",EDGE,"E26.12.3");var subQ53=sQuery(id+"F4.wireOp",EDGE,"E26.12.2");var subQ54=sQuery(id+"F3.wireOp",EDGE,"E20.12.3");var subQ55=sQuery(id+"F3.wireOp",EDGE,"E20.12.1");var subQ56=sQuery(id+"F4.wireOp",EDGE,"E26.13.3");var subQ57=sQuery(id+"F4.wireOp",EDGE,"E26.13.2");var subQ58=sQuery(id+"F3.wireOp",EDGE,"E20.13.3");var subQ59=sQuery(id+"F3.wireOp",EDGE,"E20.13.1");var subQ60=sQuery(id+"F4.wireOp",EDGE,"E26.14.3");var subQ61=sQuery(id+"F4.wireOp",EDGE,"E26.14.2");var subQ62=sQuery(id+"F3.wireOp",EDGE,"E20.14.3");var subQ63=sQuery(id+"F3.wireOp",EDGE,"E20.14.1");var subQ64=sQuery(id+"F4.wireOp",EDGE,"E26.15.3");var subQ65=sQuery(id+"F4.wireOp",EDGE,"E26.15.2");var subQ66=sQuery(id+"F3.wireOp",EDGE,"E20.15.3");var subQ67=sQuery(id+"F3.wireOp",EDGE,"E20.15.1");var subQ68=sQuery(id+"F4.wireOp",EDGE,"E23");var subQ69=sQuery(id+"F4.wireOp",EDGE,"E22");var subQ70=sQuery(id+"F3.wireOp",EDGE,"E18.top");var subQ71=sQuery(id+"F3.wireOp",EDGE,"E18.bottom");var subQ74=makeQuery(id+"F42.boolean.opBoolean","COPY",FACE,{"disambiguationData":[TD([subQ43])],"derivedFrom":subQ6});var subQ75=makeQuery(id+"F12.boolean.opBoolean","INTERSECT",EDGE,{"derivedFrom":[makeQuery(id+"F1.opRevolve","SWEPT_FACE",FACE,{"disambiguationData":[OSD([sQuery(id+"F0.wireOp",EDGE,"E13")])]}),subQ43]});Q61=makeQuery(id+"F48.opFillet","BLEND_EDGE",EDGE,{"blendedFrom":[makeQuery(id+"F47.opFillet","TWEAK_EDGE",EDGE,{"derivedFrom":[makeQuery(id+"F45.opFillet","BLEND_VERTEX",VERTEX,{"blendedFrom":[subQ75,subQ43,subQ74],"blendedInto":[subQ43,subQ74]}),makeQuery(id+"F45.opFillet","BLEND_VERTEX",VERTEX,{"blendedFrom":[subQ75,makeQuery(id+"F42.boolean.opBoolean","MERGE",FACE,{"derivedFrom":[subQ0,subQ8]}),subQ74],"blendedInto":[makeQuery(id+"F42.boolean.opBoolean","MERGE",FACE,{"derivedFrom":[subQ0,subQ8]}),subQ74]})]}),makeQuery(id+"F47.opFillet","BLEND_FACE",FACE,{"disambiguationData":[OSD([subQ5,subQ7]),TDD([makeQuery(id+"F42.boolean.opBoolean","COPY",EDGE,{"disambiguationData":[TD([makeQuery(id+"F5.opLoft","SWEPT_FACE",FACE,{"disambiguationData":[OSD([subQ71,subQ70,sQuery(id+"F3.wireOp",EDGE,"E18.left"),sQuery(id+"F4.wireOp",EDGE,"E21"),subQ69,subQ68])]})])],"derivedFrom":subQ9})])]}),makeQuery(id+"F47.opFillet","BLEND_FACE",FACE,{"disambiguationData":[OSD([subQ5,subQ7]),TDD([makeQuery(id+"F42.boolean.opBoolean","COPY",EDGE,{"disambiguationData":[TD([makeQuery(id+"F6.opLoft","SWEPT_FACE",FACE,{"disambiguationData":[OSD([sQuery(id+"F3.wireOp",EDGE,"E20.15.0"),subQ67,subQ66,sQuery(id+"F4.wireOp",EDGE,"E26.15.0"),subQ65,subQ64])]})])],"derivedFrom":subQ9})])]}),makeQuery(id+"F47.opFillet","BLEND_FACE",FACE,{"disambiguationData":[OSD([subQ5,subQ7]),TDD([makeQuery(id+"F42.boolean.opBoolean","COPY",EDGE,{"disambiguationData":[TD([makeQuery(id+"F7.opLoft","SWEPT_FACE",FACE,{"disambiguationData":[OSD([sQuery(id+"F3.wireOp",EDGE,"E20.14.0"),subQ63,subQ62,sQuery(id+"F4.wireOp",EDGE,"E26.14.0"),subQ61,subQ60])]})])],"derivedFrom":subQ9})])]}),makeQuery(id+"F47.opFillet","BLEND_FACE",FACE,{"disambiguationData":[OSD([subQ5,subQ7]),TDD([makeQuery(id+"F42.boolean.opBoolean","COPY",EDGE,{"disambiguationData":[TD([makeQuery(id+"F8.opLoft","SWEPT_FACE",FACE,{"disambiguationData":[OSD([sQuery(id+"F3.wireOp",EDGE,"E20.13.0"),subQ59,subQ58,sQuery(id+"F4.wireOp",EDGE,"E26.13.0"),subQ57,subQ56])]})])],"derivedFrom":subQ9})])]}),makeQuery(id+"F47.opFillet","BLEND_FACE",FACE,{"disambiguationData":[OSD([subQ5,subQ7]),TDD([makeQuery(id+"F42.boolean.opBoolean","COPY",EDGE,{"disambiguationData":[TD([makeQuery(id+"F9.opLoft","SWEPT_FACE",FACE,{"disambiguationData":[OSD([sQuery(id+"F3.wireOp",EDGE,"E20.12.0"),subQ55,subQ54,sQuery(id+"F4.wireOp",EDGE,"E26.12.0"),subQ53,subQ52])]})])],"derivedFrom":subQ9})])]}),makeQuery(id+"F47.opFillet","BLEND_FACE",FACE,{"disambiguationData":[OSD([subQ5,subQ7]),TDD([makeQuery(id+"F42.boolean.opBoolean","COPY",EDGE,{"disambiguationData":[TD([makeQuery(id+"F10.opLoft","SWEPT_FACE",FACE,{"disambiguationData":[OSD([sQuery(id+"F3.wireOp",EDGE,"E20.11.0"),subQ51,subQ50,sQuery(id+"F4.wireOp",EDGE,"E26.11.0"),subQ49,subQ48])]})])],"derivedFrom":subQ9})])]}),makeQuery(id+"F47.opFillet","BLEND_FACE",FACE,{"disambiguationData":[OSD([subQ5,subQ7]),TDD([makeQuery(id+"F42.boolean.opBoolean","COPY",EDGE,{"disambiguationData":[TD([makeQuery(id+"F11.opLoft","SWEPT_FACE",FACE,{"disambiguationData":[OSD([sQuery(id+"F3.wireOp",EDGE,"E20.10.0"),subQ47,subQ46,sQuery(id+"F4.wireOp",EDGE,"E26.10.0"),subQ45,subQ44])]})])],"derivedFrom":subQ9})])]}),makeQuery(id+"F47.opFillet","BLEND_FACE",FACE,{"disambiguationData":[OSD([subQ5,subQ7]),TDD([makeQuery(id+"F42.boolean.opBoolean","COPY",EDGE,{"disambiguationData":[TD([subQ43])],"derivedFrom":subQ9})])]}),makeQuery(id+"F47.opFillet","BLEND_FACE",FACE,{"disambiguationData":[OSD([subQ5,subQ7]),TDD([makeQuery(id+"F42.boolean.opBoolean","COPY",EDGE,{"disambiguationData":[TD([makeQuery(id+"F13.opLoft","SWEPT_FACE",FACE,{"disambiguationData":[OSD([sQuery(id+"F3.wireOp",EDGE,"E20.8.0"),subQ37,subQ36,sQuery(id+"F4.wireOp",EDGE,"E26.8.0"),subQ35,subQ34])]})])],"derivedFrom":subQ9})])]}),makeQuery(id+"F47.opFillet","BLEND_FACE",FACE,{"disambiguationData":[OSD([subQ5,subQ7]),TDD([makeQuery(id+"F42.boolean.opBoolean","COPY",EDGE,{"disambiguationData":[TD([makeQuery(id+"F14.opLoft","SWEPT_FACE",FACE,{"disambiguationData":[OSD([sQuery(id+"F3.wireOp",EDGE,"E20.7.0"),subQ33,subQ32,sQuery(id+"F4.wireOp",EDGE,"E26.7.0"),subQ31,subQ30])]})])],"derivedFrom":subQ9})])]}),makeQuery(id+"F47.opFillet","BLEND_FACE",FACE,{"disambiguationData":[OSD([subQ5,subQ7]),TDD([makeQuery(id+"F42.boolean.opBoolean","COPY",EDGE,{"disambiguationData":[TD([makeQuery(id+"F15.opLoft","SWEPT_FACE",FACE,{"disambiguationData":[OSD([sQuery(id+"F3.wireOp",EDGE,"E20.6.0"),subQ29,subQ28,sQuery(id+"F4.wireOp",EDGE,"E26.6.0"),subQ27,subQ26])]})])],"derivedFrom":subQ9})])]}),makeQuery(id+"F47.opFillet","BLEND_FACE",FACE,{"disambiguationData":[OSD([subQ5,subQ7]),TDD([makeQuery(id+"F42.boolean.opBoolean","COPY",EDGE,{"disambiguationData":[TD([makeQuery(id+"F16.opLoft","SWEPT_FACE",FACE,{"disambiguationData":[OSD([sQuery(id+"F3.wireOp",EDGE,"E20.5.0"),subQ25,subQ24,sQuery(id+"F4.wireOp",EDGE,"E26.5.0"),subQ23,subQ22])]})])],"derivedFrom":subQ9})])]}),makeQuery(id+"F47.opFillet","BLEND_FACE",FACE,{"disambiguationData":[OSD([subQ5,subQ7]),TDD([makeQuery(id+"F42.boolean.opBoolean","COPY",EDGE,{"disambiguationData":[TD([makeQuery(id+"F17.opLoft","SWEPT_FACE",FACE,{"disambiguationData":[OSD([sQuery(id+"F3.wireOp",EDGE,"E20.4.0"),subQ21,subQ20,sQuery(id+"F4.wireOp",EDGE,"E26.4.0"),subQ19,subQ18])]})])],"derivedFrom":subQ9})])]}),makeQuery(id+"F47.opFillet","BLEND_FACE",FACE,{"disambiguationData":[OSD([subQ5,subQ7]),TDD([makeQuery(id+"F42.boolean.opBoolean","COPY",EDGE,{"disambiguationData":[TD([makeQuery(id+"F18.opLoft","SWEPT_FACE",FACE,{"disambiguationData":[OSD([sQuery(id+"F3.wireOp",EDGE,"E20.3.0"),subQ17,subQ16,sQuery(id+"F4.wireOp",EDGE,"E26.3.0"),subQ15,subQ14])]})])],"derivedFrom":subQ9})])]}),makeQuery(id+"F47.opFillet","BLEND_FACE",FACE,{"disambiguationData":[OSD([subQ5,subQ7]),TDD([makeQuery(id+"F42.boolean.opBoolean","COPY",EDGE,{"disambiguationData":[TD([makeQuery(id+"F19.opLoft","SWEPT_FACE",FACE,{"disambiguationData":[OSD([sQuery(id+"F3.wireOp",EDGE,"E20.2.0"),subQ13,subQ12,sQuery(id+"F4.wireOp",EDGE,"E26.2.0"),subQ11,subQ10])]})])],"derivedFrom":subQ9})])]}),makeQuery(id+"F47.opFillet","BLEND_FACE",FACE,{"disambiguationData":[OSD([subQ5,subQ7]),TDD([makeQuery(id+"F42.boolean.opBoolean","COPY",EDGE,{"disambiguationData":[TD([makeQuery(id+"F20.opLoft","SWEPT_FACE",FACE,{"disambiguationData":[OSD([sQuery(id+"F3.wireOp",EDGE,"E20.1.0"),subQ4,subQ3,sQuery(id+"F4.wireOp",EDGE,"E26.1.0"),subQ2,subQ1])]})])],"derivedFrom":subQ9})])]})],"blendedInto":[makeQuery(id+"F47.opFillet","BLEND_FACE",FACE,{"disambiguationData":[OSD([subQ5,subQ7]),TDD([makeQuery(id+"F42.boolean.opBoolean","COPY",EDGE,{"disambiguationData":[TD([makeQuery(id+"F5.opLoft","SWEPT_FACE",FACE,{"disambiguationData":[OSD([subQ71,subQ70,sQuery(id+"F3.wireOp",EDGE,"E18.left"),sQuery(id+"F4.wireOp",EDGE,"E21"),subQ69,subQ68])]})])],"derivedFrom":subQ9})])]}),makeQuery(id+"F47.opFillet","BLEND_FACE",FACE,{"disambiguationData":[OSD([subQ5,subQ7]),TDD([makeQuery(id+"F42.boolean.opBoolean","COPY",EDGE,{"disambiguationData":[TD([makeQuery(id+"F6.opLoft","SWEPT_FACE",FACE,{"disambiguationData":[OSD([sQuery(id+"F3.wireOp",EDGE,"E20.15.0"),subQ67,subQ66,sQuery(id+"F4.wireOp",EDGE,"E26.15.0"),subQ65,subQ64])]})])],"derivedFrom":subQ9})])]}),makeQuery(id+"F47.opFillet","BLEND_FACE",FACE,{"disambiguationData":[OSD([subQ5,subQ7]),TDD([makeQuery(id+"F42.boolean.opBoolean","COPY",EDGE,{"disambiguationData":[TD([makeQuery(id+"F7.opLoft","SWEPT_FACE",FACE,{"disambiguationData":[OSD([sQuery(id+"F3.wireOp",EDGE,"E20.14.0"),subQ63,subQ62,sQuery(id+"F4.wireOp",EDGE,"E26.14.0"),subQ61,subQ60])]})])],"derivedFrom":subQ9})])]}),makeQuery(id+"F47.opFillet","BLEND_FACE",FACE,{"disambiguationData":[OSD([subQ5,subQ7]),TDD([makeQuery(id+"F42.boolean.opBoolean","COPY",EDGE,{"disambiguationData":[TD([makeQuery(id+"F8.opLoft","SWEPT_FACE",FACE,{"disambiguationData":[OSD([sQuery(id+"F3.wireOp",EDGE,"E20.13.0"),subQ59,subQ58,sQuery(id+"F4.wireOp",EDGE,"E26.13.0"),subQ57,subQ56])]})])],"derivedFrom":subQ9})])]}),makeQuery(id+"F47.opFillet","BLEND_FACE",FACE,{"disambiguationData":[OSD([subQ5,subQ7]),TDD([makeQuery(id+"F42.boolean.opBoolean","COPY",EDGE,{"disambiguationData":[TD([makeQuery(id+"F9.opLoft","SWEPT_FACE",FACE,{"disambiguationData":[OSD([sQuery(id+"F3.wireOp",EDGE,"E20.12.0"),subQ55,subQ54,sQuery(id+"F4.wireOp",EDGE,"E26.12.0"),subQ53,subQ52])]})])],"derivedFrom":subQ9})])]}),makeQuery(id+"F47.opFillet","BLEND_FACE",FACE,{"disambiguationData":[OSD([subQ5,subQ7]),TDD([makeQuery(id+"F42.boolean.opBoolean","COPY",EDGE,{"disambiguationData":[TD([makeQuery(id+"F10.opLoft","SWEPT_FACE",FACE,{"disambiguationData":[OSD([sQuery(id+"F3.wireOp",EDGE,"E20.11.0"),subQ51,subQ50,sQuery(id+"F4.wireOp",EDGE,"E26.11.0"),subQ49,subQ48])]})])],"derivedFrom":subQ9})])]}),makeQuery(id+"F47.opFillet","BLEND_FACE",FACE,{"disambiguationData":[OSD([subQ5,subQ7]),TDD([makeQuery(id+"F42.boolean.opBoolean","COPY",EDGE,{"disambiguationData":[TD([makeQuery(id+"F11.opLoft","SWEPT_FACE",FACE,{"disambiguationData":[OSD([sQuery(id+"F3.wireOp",EDGE,"E20.10.0"),subQ47,subQ46,sQuery(id+"F4.wireOp",EDGE,"E26.10.0"),subQ45,subQ44])]})])],"derivedFrom":subQ9})])]}),makeQuery(id+"F47.opFillet","BLEND_FACE",FACE,{"disambiguationData":[OSD([subQ5,subQ7]),TDD([makeQuery(id+"F42.boolean.opBoolean","COPY",EDGE,{"disambiguationData":[TD([subQ43])],"derivedFrom":subQ9})])]}),makeQuery(id+"F47.opFillet","BLEND_FACE",FACE,{"disambiguationData":[OSD([subQ5,subQ7]),TDD([makeQuery(id+"F42.boolean.opBoolean","COPY",EDGE,{"disambiguationData":[TD([makeQuery(id+"F13.opLoft","SWEPT_FACE",FACE,{"disambiguationData":[OSD([sQuery(id+"F3.wireOp",EDGE,"E20.8.0"),subQ37,subQ36,sQuery(id+"F4.wireOp",EDGE,"E26.8.0"),subQ35,subQ34])]})])],"derivedFrom":subQ9})])]}),makeQuery(id+"F47.opFillet","BLEND_FACE",FACE,{"disambiguationData":[OSD([subQ5,subQ7]),TDD([makeQuery(id+"F42.boolean.opBoolean","COPY",EDGE,{"disambiguationData":[TD([makeQuery(id+"F14.opLoft","SWEPT_FACE",FACE,{"disambiguationData":[OSD([sQuery(id+"F3.wireOp",EDGE,"E20.7.0"),subQ33,subQ32,sQuery(id+"F4.wireOp",EDGE,"E26.7.0"),subQ31,subQ30])]})])],"derivedFrom":subQ9})])]}),makeQuery(id+"F47.opFillet","BLEND_FACE",FACE,{"disambiguationData":[OSD([subQ5,subQ7]),TDD([makeQuery(id+"F42.boolean.opBoolean","COPY",EDGE,{"disambiguationData":[TD([makeQuery(id+"F15.opLoft","SWEPT_FACE",FACE,{"disambiguationData":[OSD([sQuery(id+"F3.wireOp",EDGE,"E20.6.0"),subQ29,subQ28,sQuery(id+"F4.wireOp",EDGE,"E26.6.0"),subQ27,subQ26])]})])],"derivedFrom":subQ9})])]}),makeQuery(id+"F47.opFillet","BLEND_FACE",FACE,{"disambiguationData":[OSD([subQ5,subQ7]),TDD([makeQuery(id+"F42.boolean.opBoolean","COPY",EDGE,{"disambiguationData":[TD([makeQuery(id+"F16.opLoft","SWEPT_FACE",FACE,{"disambiguationData":[OSD([sQuery(id+"F3.wireOp",EDGE,"E20.5.0"),subQ25,subQ24,sQuery(id+"F4.wireOp",EDGE,"E26.5.0"),subQ23,subQ22])]})])],"derivedFrom":subQ9})])]}),makeQuery(id+"F47.opFillet","BLEND_FACE",FACE,{"disambiguationData":[OSD([subQ5,subQ7]),TDD([makeQuery(id+"F42.boolean.opBoolean","COPY",EDGE,{"disambiguationData":[TD([makeQuery(id+"F17.opLoft","SWEPT_FACE",FACE,{"disambiguationData":[OSD([sQuery(id+"F3.wireOp",EDGE,"E20.4.0"),subQ21,subQ20,sQuery(id+"F4.wireOp",EDGE,"E26.4.0"),subQ19,subQ18])]})])],"derivedFrom":subQ9})])]}),makeQuery(id+"F47.opFillet","BLEND_FACE",FACE,{"disambiguationData":[OSD([subQ5,subQ7]),TDD([makeQuery(id+"F42.boolean.opBoolean","COPY",EDGE,{"disambiguationData":[TD([makeQuery(id+"F18.opLoft","SWEPT_FACE",FACE,{"disambiguationData":[OSD([sQuery(id+"F3.wireOp",EDGE,"E20.3.0"),subQ17,subQ16,sQuery(id+"F4.wireOp",EDGE,"E26.3.0"),subQ15,subQ14])]})])],"derivedFrom":subQ9})])]}),makeQuery(id+"F47.opFillet","BLEND_FACE",FACE,{"disambiguationData":[OSD([subQ5,subQ7]),TDD([makeQuery(id+"F42.boolean.opBoolean","COPY",EDGE,{"disambiguationData":[TD([makeQuery(id+"F19.opLoft","SWEPT_FACE",FACE,{"disambiguationData":[OSD([sQuery(id+"F3.wireOp",EDGE,"E20.2.0"),subQ13,subQ12,sQuery(id+"F4.wireOp",EDGE,"E26.2.0"),subQ11,subQ10])]})])],"derivedFrom":subQ9})])]}),makeQuery(id+"F47.opFillet","BLEND_FACE",FACE,{"disambiguationData":[OSD([subQ5,subQ7]),TDD([makeQuery(id+"F42.boolean.opBoolean","COPY",EDGE,{"disambiguationData":[TD([makeQuery(id+"F20.opLoft","SWEPT_FACE",FACE,{"disambiguationData":[OSD([sQuery(id+"F3.wireOp",EDGE,"E20.1.0"),subQ4,subQ3,sQuery(id+"F4.wireOp",EDGE,"E26.1.0"),subQ2,subQ1])]})])],"derivedFrom":subQ9})])]})]});}
            var Q62;
            {var subQ0=makeQuery(id+"F40.opExtrude","CAP_FACE",FACE,{"disambiguationData":[OSD([sQuery(id+"F39.wireOp",EDGE,"E29"),sQuery(id+"F39.wireOp",EDGE,"E30")])],"isStart":false});var subQ1=sQuery(id+"F4.wireOp",EDGE,"E26.1.3");var subQ2=sQuery(id+"F4.wireOp",EDGE,"E26.1.2");var subQ3=sQuery(id+"F3.wireOp",EDGE,"E20.1.3");var subQ4=sQuery(id+"F3.wireOp",EDGE,"E20.1.1");var subQ5=sQuery(id+"F41.wireOp",EDGE,"E35");var subQ6=makeQuery(id+"F42.opRevolve","SWEPT_FACE",FACE,{"disambiguationData":[OSD([subQ5])]});var subQ7=sQuery(id+"F41.wireOp",EDGE,"E36");var subQ8=makeQuery(id+"F42.opRevolve","SWEPT_FACE",FACE,{"disambiguationData":[OSD([subQ7])]});var subQ9=makeQuery(id+"F42.opRevolve","SWEPT_EDGE",EDGE,{"disambiguationData":[OSD([subQ5,subQ7])]});var subQ10=sQuery(id+"F4.wireOp",EDGE,"E26.2.3");var subQ11=sQuery(id+"F4.wireOp",EDGE,"E26.2.2");var subQ12=sQuery(id+"F3.wireOp",EDGE,"E20.2.3");var subQ13=sQuery(id+"F3.wireOp",EDGE,"E20.2.1");var subQ14=sQuery(id+"F4.wireOp",EDGE,"E26.3.3");var subQ15=sQuery(id+"F4.wireOp",EDGE,"E26.3.2");var subQ16=sQuery(id+"F3.wireOp",EDGE,"E20.3.3");var subQ17=sQuery(id+"F3.wireOp",EDGE,"E20.3.1");var subQ18=sQuery(id+"F4.wireOp",EDGE,"E26.4.3");var subQ19=sQuery(id+"F4.wireOp",EDGE,"E26.4.2");var subQ20=sQuery(id+"F3.wireOp",EDGE,"E20.4.3");var subQ21=sQuery(id+"F3.wireOp",EDGE,"E20.4.1");var subQ22=sQuery(id+"F4.wireOp",EDGE,"E26.5.3");var subQ23=sQuery(id+"F4.wireOp",EDGE,"E26.5.2");var subQ24=sQuery(id+"F3.wireOp",EDGE,"E20.5.3");var subQ25=sQuery(id+"F3.wireOp",EDGE,"E20.5.1");var subQ26=sQuery(id+"F4.wireOp",EDGE,"E26.6.3");var subQ27=sQuery(id+"F4.wireOp",EDGE,"E26.6.2");var subQ28=sQuery(id+"F3.wireOp",EDGE,"E20.6.3");var subQ29=sQuery(id+"F3.wireOp",EDGE,"E20.6.1");var subQ30=sQuery(id+"F4.wireOp",EDGE,"E26.7.3");var subQ31=sQuery(id+"F4.wireOp",EDGE,"E26.7.2");var subQ32=sQuery(id+"F3.wireOp",EDGE,"E20.7.3");var subQ33=sQuery(id+"F3.wireOp",EDGE,"E20.7.1");var subQ35=makeQuery(id+"F14.opLoft","SWEPT_FACE",FACE,{"disambiguationData":[OSD([sQuery(id+"F3.wireOp",EDGE,"E20.7.0"),subQ33,subQ32,sQuery(id+"F4.wireOp",EDGE,"E26.7.0"),subQ31,subQ30])]});var subQ36=sQuery(id+"F4.wireOp",EDGE,"E26.8.3");var subQ37=sQuery(id+"F4.wireOp",EDGE,"E26.8.2");var subQ38=sQuery(id+"F3.wireOp",EDGE,"E20.8.3");var subQ39=sQuery(id+"F3.wireOp",EDGE,"E20.8.1");var subQ40=sQuery(id+"F4.wireOp",EDGE,"E26.9.3");var subQ41=sQuery(id+"F4.wireOp",EDGE,"E26.9.2");var subQ42=sQuery(id+"F3.wireOp",EDGE,"E20.9.3");var subQ43=sQuery(id+"F3.wireOp",EDGE,"E20.9.1");var subQ44=sQuery(id+"F4.wireOp",EDGE,"E26.10.3");var subQ45=sQuery(id+"F4.wireOp",EDGE,"E26.10.2");var subQ46=sQuery(id+"F3.wireOp",EDGE,"E20.10.3");var subQ47=sQuery(id+"F3.wireOp",EDGE,"E20.10.1");var subQ48=sQuery(id+"F4.wireOp",EDGE,"E26.11.3");var subQ49=sQuery(id+"F4.wireOp",EDGE,"E26.11.2");var subQ50=sQuery(id+"F3.wireOp",EDGE,"E20.11.3");var subQ51=sQuery(id+"F3.wireOp",EDGE,"E20.11.1");var subQ52=sQuery(id+"F4.wireOp",EDGE,"E26.12.3");var subQ53=sQuery(id+"F4.wireOp",EDGE,"E26.12.2");var subQ54=sQuery(id+"F3.wireOp",EDGE,"E20.12.3");var subQ55=sQuery(id+"F3.wireOp",EDGE,"E20.12.1");var subQ56=sQuery(id+"F4.wireOp",EDGE,"E26.13.3");var subQ57=sQuery(id+"F4.wireOp",EDGE,"E26.13.2");var subQ58=sQuery(id+"F3.wireOp",EDGE,"E20.13.3");var subQ59=sQuery(id+"F3.wireOp",EDGE,"E20.13.1");var subQ60=sQuery(id+"F4.wireOp",EDGE,"E26.14.3");var subQ61=sQuery(id+"F4.wireOp",EDGE,"E26.14.2");var subQ62=sQuery(id+"F3.wireOp",EDGE,"E20.14.3");var subQ63=sQuery(id+"F3.wireOp",EDGE,"E20.14.1");var subQ64=sQuery(id+"F4.wireOp",EDGE,"E26.15.3");var subQ65=sQuery(id+"F4.wireOp",EDGE,"E26.15.2");var subQ66=sQuery(id+"F3.wireOp",EDGE,"E20.15.3");var subQ67=sQuery(id+"F3.wireOp",EDGE,"E20.15.1");var subQ68=sQuery(id+"F4.wireOp",EDGE,"E23");var subQ69=sQuery(id+"F4.wireOp",EDGE,"E22");var subQ70=sQuery(id+"F3.wireOp",EDGE,"E18.top");var subQ71=sQuery(id+"F3.wireOp",EDGE,"E18.bottom");var subQ74=makeQuery(id+"F42.boolean.opBoolean","COPY",FACE,{"disambiguationData":[TD([subQ35])],"derivedFrom":subQ6});var subQ75=makeQuery(id+"F14.boolean.opBoolean","INTERSECT",EDGE,{"derivedFrom":[makeQuery(id+"F1.opRevolve","SWEPT_FACE",FACE,{"disambiguationData":[OSD([sQuery(id+"F0.wireOp",EDGE,"E13")])]}),subQ35]});Q62=makeQuery(id+"F48.opFillet","BLEND_EDGE",EDGE,{"blendedFrom":[makeQuery(id+"F47.opFillet","TWEAK_EDGE",EDGE,{"derivedFrom":[makeQuery(id+"F45.opFillet","BLEND_VERTEX",VERTEX,{"blendedFrom":[subQ75,subQ35,subQ74],"blendedInto":[subQ35,subQ74]}),makeQuery(id+"F45.opFillet","BLEND_VERTEX",VERTEX,{"blendedFrom":[subQ75,makeQuery(id+"F42.boolean.opBoolean","MERGE",FACE,{"derivedFrom":[subQ0,subQ8]}),subQ74],"blendedInto":[makeQuery(id+"F42.boolean.opBoolean","MERGE",FACE,{"derivedFrom":[subQ0,subQ8]}),subQ74]})]}),makeQuery(id+"F47.opFillet","BLEND_FACE",FACE,{"disambiguationData":[OSD([subQ5,subQ7]),TDD([makeQuery(id+"F42.boolean.opBoolean","COPY",EDGE,{"disambiguationData":[TD([makeQuery(id+"F5.opLoft","SWEPT_FACE",FACE,{"disambiguationData":[OSD([subQ71,subQ70,sQuery(id+"F3.wireOp",EDGE,"E18.left"),sQuery(id+"F4.wireOp",EDGE,"E21"),subQ69,subQ68])]})])],"derivedFrom":subQ9})])]}),makeQuery(id+"F47.opFillet","BLEND_FACE",FACE,{"disambiguationData":[OSD([subQ5,subQ7]),TDD([makeQuery(id+"F42.boolean.opBoolean","COPY",EDGE,{"disambiguationData":[TD([makeQuery(id+"F6.opLoft","SWEPT_FACE",FACE,{"disambiguationData":[OSD([sQuery(id+"F3.wireOp",EDGE,"E20.15.0"),subQ67,subQ66,sQuery(id+"F4.wireOp",EDGE,"E26.15.0"),subQ65,subQ64])]})])],"derivedFrom":subQ9})])]}),makeQuery(id+"F47.opFillet","BLEND_FACE",FACE,{"disambiguationData":[OSD([subQ5,subQ7]),TDD([makeQuery(id+"F42.boolean.opBoolean","COPY",EDGE,{"disambiguationData":[TD([makeQuery(id+"F7.opLoft","SWEPT_FACE",FACE,{"disambiguationData":[OSD([sQuery(id+"F3.wireOp",EDGE,"E20.14.0"),subQ63,subQ62,sQuery(id+"F4.wireOp",EDGE,"E26.14.0"),subQ61,subQ60])]})])],"derivedFrom":subQ9})])]}),makeQuery(id+"F47.opFillet","BLEND_FACE",FACE,{"disambiguationData":[OSD([subQ5,subQ7]),TDD([makeQuery(id+"F42.boolean.opBoolean","COPY",EDGE,{"disambiguationData":[TD([makeQuery(id+"F8.opLoft","SWEPT_FACE",FACE,{"disambiguationData":[OSD([sQuery(id+"F3.wireOp",EDGE,"E20.13.0"),subQ59,subQ58,sQuery(id+"F4.wireOp",EDGE,"E26.13.0"),subQ57,subQ56])]})])],"derivedFrom":subQ9})])]}),makeQuery(id+"F47.opFillet","BLEND_FACE",FACE,{"disambiguationData":[OSD([subQ5,subQ7]),TDD([makeQuery(id+"F42.boolean.opBoolean","COPY",EDGE,{"disambiguationData":[TD([makeQuery(id+"F9.opLoft","SWEPT_FACE",FACE,{"disambiguationData":[OSD([sQuery(id+"F3.wireOp",EDGE,"E20.12.0"),subQ55,subQ54,sQuery(id+"F4.wireOp",EDGE,"E26.12.0"),subQ53,subQ52])]})])],"derivedFrom":subQ9})])]}),makeQuery(id+"F47.opFillet","BLEND_FACE",FACE,{"disambiguationData":[OSD([subQ5,subQ7]),TDD([makeQuery(id+"F42.boolean.opBoolean","COPY",EDGE,{"disambiguationData":[TD([makeQuery(id+"F10.opLoft","SWEPT_FACE",FACE,{"disambiguationData":[OSD([sQuery(id+"F3.wireOp",EDGE,"E20.11.0"),subQ51,subQ50,sQuery(id+"F4.wireOp",EDGE,"E26.11.0"),subQ49,subQ48])]})])],"derivedFrom":subQ9})])]}),makeQuery(id+"F47.opFillet","BLEND_FACE",FACE,{"disambiguationData":[OSD([subQ5,subQ7]),TDD([makeQuery(id+"F42.boolean.opBoolean","COPY",EDGE,{"disambiguationData":[TD([makeQuery(id+"F11.opLoft","SWEPT_FACE",FACE,{"disambiguationData":[OSD([sQuery(id+"F3.wireOp",EDGE,"E20.10.0"),subQ47,subQ46,sQuery(id+"F4.wireOp",EDGE,"E26.10.0"),subQ45,subQ44])]})])],"derivedFrom":subQ9})])]}),makeQuery(id+"F47.opFillet","BLEND_FACE",FACE,{"disambiguationData":[OSD([subQ5,subQ7]),TDD([makeQuery(id+"F42.boolean.opBoolean","COPY",EDGE,{"disambiguationData":[TD([makeQuery(id+"F12.opLoft","SWEPT_FACE",FACE,{"disambiguationData":[OSD([sQuery(id+"F3.wireOp",EDGE,"E20.9.0"),subQ43,subQ42,sQuery(id+"F4.wireOp",EDGE,"E26.9.0"),subQ41,subQ40])]})])],"derivedFrom":subQ9})])]}),makeQuery(id+"F47.opFillet","BLEND_FACE",FACE,{"disambiguationData":[OSD([subQ5,subQ7]),TDD([makeQuery(id+"F42.boolean.opBoolean","COPY",EDGE,{"disambiguationData":[TD([makeQuery(id+"F13.opLoft","SWEPT_FACE",FACE,{"disambiguationData":[OSD([sQuery(id+"F3.wireOp",EDGE,"E20.8.0"),subQ39,subQ38,sQuery(id+"F4.wireOp",EDGE,"E26.8.0"),subQ37,subQ36])]})])],"derivedFrom":subQ9})])]}),makeQuery(id+"F47.opFillet","BLEND_FACE",FACE,{"disambiguationData":[OSD([subQ5,subQ7]),TDD([makeQuery(id+"F42.boolean.opBoolean","COPY",EDGE,{"disambiguationData":[TD([subQ35])],"derivedFrom":subQ9})])]}),makeQuery(id+"F47.opFillet","BLEND_FACE",FACE,{"disambiguationData":[OSD([subQ5,subQ7]),TDD([makeQuery(id+"F42.boolean.opBoolean","COPY",EDGE,{"disambiguationData":[TD([makeQuery(id+"F15.opLoft","SWEPT_FACE",FACE,{"disambiguationData":[OSD([sQuery(id+"F3.wireOp",EDGE,"E20.6.0"),subQ29,subQ28,sQuery(id+"F4.wireOp",EDGE,"E26.6.0"),subQ27,subQ26])]})])],"derivedFrom":subQ9})])]}),makeQuery(id+"F47.opFillet","BLEND_FACE",FACE,{"disambiguationData":[OSD([subQ5,subQ7]),TDD([makeQuery(id+"F42.boolean.opBoolean","COPY",EDGE,{"disambiguationData":[TD([makeQuery(id+"F16.opLoft","SWEPT_FACE",FACE,{"disambiguationData":[OSD([sQuery(id+"F3.wireOp",EDGE,"E20.5.0"),subQ25,subQ24,sQuery(id+"F4.wireOp",EDGE,"E26.5.0"),subQ23,subQ22])]})])],"derivedFrom":subQ9})])]}),makeQuery(id+"F47.opFillet","BLEND_FACE",FACE,{"disambiguationData":[OSD([subQ5,subQ7]),TDD([makeQuery(id+"F42.boolean.opBoolean","COPY",EDGE,{"disambiguationData":[TD([makeQuery(id+"F17.opLoft","SWEPT_FACE",FACE,{"disambiguationData":[OSD([sQuery(id+"F3.wireOp",EDGE,"E20.4.0"),subQ21,subQ20,sQuery(id+"F4.wireOp",EDGE,"E26.4.0"),subQ19,subQ18])]})])],"derivedFrom":subQ9})])]}),makeQuery(id+"F47.opFillet","BLEND_FACE",FACE,{"disambiguationData":[OSD([subQ5,subQ7]),TDD([makeQuery(id+"F42.boolean.opBoolean","COPY",EDGE,{"disambiguationData":[TD([makeQuery(id+"F18.opLoft","SWEPT_FACE",FACE,{"disambiguationData":[OSD([sQuery(id+"F3.wireOp",EDGE,"E20.3.0"),subQ17,subQ16,sQuery(id+"F4.wireOp",EDGE,"E26.3.0"),subQ15,subQ14])]})])],"derivedFrom":subQ9})])]}),makeQuery(id+"F47.opFillet","BLEND_FACE",FACE,{"disambiguationData":[OSD([subQ5,subQ7]),TDD([makeQuery(id+"F42.boolean.opBoolean","COPY",EDGE,{"disambiguationData":[TD([makeQuery(id+"F19.opLoft","SWEPT_FACE",FACE,{"disambiguationData":[OSD([sQuery(id+"F3.wireOp",EDGE,"E20.2.0"),subQ13,subQ12,sQuery(id+"F4.wireOp",EDGE,"E26.2.0"),subQ11,subQ10])]})])],"derivedFrom":subQ9})])]}),makeQuery(id+"F47.opFillet","BLEND_FACE",FACE,{"disambiguationData":[OSD([subQ5,subQ7]),TDD([makeQuery(id+"F42.boolean.opBoolean","COPY",EDGE,{"disambiguationData":[TD([makeQuery(id+"F20.opLoft","SWEPT_FACE",FACE,{"disambiguationData":[OSD([sQuery(id+"F3.wireOp",EDGE,"E20.1.0"),subQ4,subQ3,sQuery(id+"F4.wireOp",EDGE,"E26.1.0"),subQ2,subQ1])]})])],"derivedFrom":subQ9})])]})],"blendedInto":[makeQuery(id+"F47.opFillet","BLEND_FACE",FACE,{"disambiguationData":[OSD([subQ5,subQ7]),TDD([makeQuery(id+"F42.boolean.opBoolean","COPY",EDGE,{"disambiguationData":[TD([makeQuery(id+"F5.opLoft","SWEPT_FACE",FACE,{"disambiguationData":[OSD([subQ71,subQ70,sQuery(id+"F3.wireOp",EDGE,"E18.left"),sQuery(id+"F4.wireOp",EDGE,"E21"),subQ69,subQ68])]})])],"derivedFrom":subQ9})])]}),makeQuery(id+"F47.opFillet","BLEND_FACE",FACE,{"disambiguationData":[OSD([subQ5,subQ7]),TDD([makeQuery(id+"F42.boolean.opBoolean","COPY",EDGE,{"disambiguationData":[TD([makeQuery(id+"F6.opLoft","SWEPT_FACE",FACE,{"disambiguationData":[OSD([sQuery(id+"F3.wireOp",EDGE,"E20.15.0"),subQ67,subQ66,sQuery(id+"F4.wireOp",EDGE,"E26.15.0"),subQ65,subQ64])]})])],"derivedFrom":subQ9})])]}),makeQuery(id+"F47.opFillet","BLEND_FACE",FACE,{"disambiguationData":[OSD([subQ5,subQ7]),TDD([makeQuery(id+"F42.boolean.opBoolean","COPY",EDGE,{"disambiguationData":[TD([makeQuery(id+"F7.opLoft","SWEPT_FACE",FACE,{"disambiguationData":[OSD([sQuery(id+"F3.wireOp",EDGE,"E20.14.0"),subQ63,subQ62,sQuery(id+"F4.wireOp",EDGE,"E26.14.0"),subQ61,subQ60])]})])],"derivedFrom":subQ9})])]}),makeQuery(id+"F47.opFillet","BLEND_FACE",FACE,{"disambiguationData":[OSD([subQ5,subQ7]),TDD([makeQuery(id+"F42.boolean.opBoolean","COPY",EDGE,{"disambiguationData":[TD([makeQuery(id+"F8.opLoft","SWEPT_FACE",FACE,{"disambiguationData":[OSD([sQuery(id+"F3.wireOp",EDGE,"E20.13.0"),subQ59,subQ58,sQuery(id+"F4.wireOp",EDGE,"E26.13.0"),subQ57,subQ56])]})])],"derivedFrom":subQ9})])]}),makeQuery(id+"F47.opFillet","BLEND_FACE",FACE,{"disambiguationData":[OSD([subQ5,subQ7]),TDD([makeQuery(id+"F42.boolean.opBoolean","COPY",EDGE,{"disambiguationData":[TD([makeQuery(id+"F9.opLoft","SWEPT_FACE",FACE,{"disambiguationData":[OSD([sQuery(id+"F3.wireOp",EDGE,"E20.12.0"),subQ55,subQ54,sQuery(id+"F4.wireOp",EDGE,"E26.12.0"),subQ53,subQ52])]})])],"derivedFrom":subQ9})])]}),makeQuery(id+"F47.opFillet","BLEND_FACE",FACE,{"disambiguationData":[OSD([subQ5,subQ7]),TDD([makeQuery(id+"F42.boolean.opBoolean","COPY",EDGE,{"disambiguationData":[TD([makeQuery(id+"F10.opLoft","SWEPT_FACE",FACE,{"disambiguationData":[OSD([sQuery(id+"F3.wireOp",EDGE,"E20.11.0"),subQ51,subQ50,sQuery(id+"F4.wireOp",EDGE,"E26.11.0"),subQ49,subQ48])]})])],"derivedFrom":subQ9})])]}),makeQuery(id+"F47.opFillet","BLEND_FACE",FACE,{"disambiguationData":[OSD([subQ5,subQ7]),TDD([makeQuery(id+"F42.boolean.opBoolean","COPY",EDGE,{"disambiguationData":[TD([makeQuery(id+"F11.opLoft","SWEPT_FACE",FACE,{"disambiguationData":[OSD([sQuery(id+"F3.wireOp",EDGE,"E20.10.0"),subQ47,subQ46,sQuery(id+"F4.wireOp",EDGE,"E26.10.0"),subQ45,subQ44])]})])],"derivedFrom":subQ9})])]}),makeQuery(id+"F47.opFillet","BLEND_FACE",FACE,{"disambiguationData":[OSD([subQ5,subQ7]),TDD([makeQuery(id+"F42.boolean.opBoolean","COPY",EDGE,{"disambiguationData":[TD([makeQuery(id+"F12.opLoft","SWEPT_FACE",FACE,{"disambiguationData":[OSD([sQuery(id+"F3.wireOp",EDGE,"E20.9.0"),subQ43,subQ42,sQuery(id+"F4.wireOp",EDGE,"E26.9.0"),subQ41,subQ40])]})])],"derivedFrom":subQ9})])]}),makeQuery(id+"F47.opFillet","BLEND_FACE",FACE,{"disambiguationData":[OSD([subQ5,subQ7]),TDD([makeQuery(id+"F42.boolean.opBoolean","COPY",EDGE,{"disambiguationData":[TD([makeQuery(id+"F13.opLoft","SWEPT_FACE",FACE,{"disambiguationData":[OSD([sQuery(id+"F3.wireOp",EDGE,"E20.8.0"),subQ39,subQ38,sQuery(id+"F4.wireOp",EDGE,"E26.8.0"),subQ37,subQ36])]})])],"derivedFrom":subQ9})])]}),makeQuery(id+"F47.opFillet","BLEND_FACE",FACE,{"disambiguationData":[OSD([subQ5,subQ7]),TDD([makeQuery(id+"F42.boolean.opBoolean","COPY",EDGE,{"disambiguationData":[TD([subQ35])],"derivedFrom":subQ9})])]}),makeQuery(id+"F47.opFillet","BLEND_FACE",FACE,{"disambiguationData":[OSD([subQ5,subQ7]),TDD([makeQuery(id+"F42.boolean.opBoolean","COPY",EDGE,{"disambiguationData":[TD([makeQuery(id+"F15.opLoft","SWEPT_FACE",FACE,{"disambiguationData":[OSD([sQuery(id+"F3.wireOp",EDGE,"E20.6.0"),subQ29,subQ28,sQuery(id+"F4.wireOp",EDGE,"E26.6.0"),subQ27,subQ26])]})])],"derivedFrom":subQ9})])]}),makeQuery(id+"F47.opFillet","BLEND_FACE",FACE,{"disambiguationData":[OSD([subQ5,subQ7]),TDD([makeQuery(id+"F42.boolean.opBoolean","COPY",EDGE,{"disambiguationData":[TD([makeQuery(id+"F16.opLoft","SWEPT_FACE",FACE,{"disambiguationData":[OSD([sQuery(id+"F3.wireOp",EDGE,"E20.5.0"),subQ25,subQ24,sQuery(id+"F4.wireOp",EDGE,"E26.5.0"),subQ23,subQ22])]})])],"derivedFrom":subQ9})])]}),makeQuery(id+"F47.opFillet","BLEND_FACE",FACE,{"disambiguationData":[OSD([subQ5,subQ7]),TDD([makeQuery(id+"F42.boolean.opBoolean","COPY",EDGE,{"disambiguationData":[TD([makeQuery(id+"F17.opLoft","SWEPT_FACE",FACE,{"disambiguationData":[OSD([sQuery(id+"F3.wireOp",EDGE,"E20.4.0"),subQ21,subQ20,sQuery(id+"F4.wireOp",EDGE,"E26.4.0"),subQ19,subQ18])]})])],"derivedFrom":subQ9})])]}),makeQuery(id+"F47.opFillet","BLEND_FACE",FACE,{"disambiguationData":[OSD([subQ5,subQ7]),TDD([makeQuery(id+"F42.boolean.opBoolean","COPY",EDGE,{"disambiguationData":[TD([makeQuery(id+"F18.opLoft","SWEPT_FACE",FACE,{"disambiguationData":[OSD([sQuery(id+"F3.wireOp",EDGE,"E20.3.0"),subQ17,subQ16,sQuery(id+"F4.wireOp",EDGE,"E26.3.0"),subQ15,subQ14])]})])],"derivedFrom":subQ9})])]}),makeQuery(id+"F47.opFillet","BLEND_FACE",FACE,{"disambiguationData":[OSD([subQ5,subQ7]),TDD([makeQuery(id+"F42.boolean.opBoolean","COPY",EDGE,{"disambiguationData":[TD([makeQuery(id+"F19.opLoft","SWEPT_FACE",FACE,{"disambiguationData":[OSD([sQuery(id+"F3.wireOp",EDGE,"E20.2.0"),subQ13,subQ12,sQuery(id+"F4.wireOp",EDGE,"E26.2.0"),subQ11,subQ10])]})])],"derivedFrom":subQ9})])]}),makeQuery(id+"F47.opFillet","BLEND_FACE",FACE,{"disambiguationData":[OSD([subQ5,subQ7]),TDD([makeQuery(id+"F42.boolean.opBoolean","COPY",EDGE,{"disambiguationData":[TD([makeQuery(id+"F20.opLoft","SWEPT_FACE",FACE,{"disambiguationData":[OSD([sQuery(id+"F3.wireOp",EDGE,"E20.1.0"),subQ4,subQ3,sQuery(id+"F4.wireOp",EDGE,"E26.1.0"),subQ2,subQ1])]})])],"derivedFrom":subQ9})])]})]});}
            var Q63;
            {var subQ0=makeQuery(id+"F40.opExtrude","CAP_FACE",FACE,{"disambiguationData":[OSD([sQuery(id+"F39.wireOp",EDGE,"E29"),sQuery(id+"F39.wireOp",EDGE,"E30")])],"isStart":false});var subQ1=sQuery(id+"F4.wireOp",EDGE,"E26.1.3");var subQ2=sQuery(id+"F4.wireOp",EDGE,"E26.1.2");var subQ3=sQuery(id+"F3.wireOp",EDGE,"E20.1.3");var subQ4=sQuery(id+"F3.wireOp",EDGE,"E20.1.1");var subQ5=sQuery(id+"F41.wireOp",EDGE,"E35");var subQ6=makeQuery(id+"F42.opRevolve","SWEPT_FACE",FACE,{"disambiguationData":[OSD([subQ5])]});var subQ7=sQuery(id+"F41.wireOp",EDGE,"E36");var subQ8=makeQuery(id+"F42.opRevolve","SWEPT_FACE",FACE,{"disambiguationData":[OSD([subQ7])]});var subQ9=makeQuery(id+"F42.opRevolve","SWEPT_EDGE",EDGE,{"disambiguationData":[OSD([subQ5,subQ7])]});var subQ10=sQuery(id+"F4.wireOp",EDGE,"E26.2.3");var subQ11=sQuery(id+"F4.wireOp",EDGE,"E26.2.2");var subQ12=sQuery(id+"F3.wireOp",EDGE,"E20.2.3");var subQ13=sQuery(id+"F3.wireOp",EDGE,"E20.2.1");var subQ14=sQuery(id+"F4.wireOp",EDGE,"E26.3.3");var subQ15=sQuery(id+"F4.wireOp",EDGE,"E26.3.2");var subQ16=sQuery(id+"F3.wireOp",EDGE,"E20.3.3");var subQ17=sQuery(id+"F3.wireOp",EDGE,"E20.3.1");var subQ18=sQuery(id+"F4.wireOp",EDGE,"E26.4.3");var subQ19=sQuery(id+"F4.wireOp",EDGE,"E26.4.2");var subQ20=sQuery(id+"F3.wireOp",EDGE,"E20.4.3");var subQ21=sQuery(id+"F3.wireOp",EDGE,"E20.4.1");var subQ22=sQuery(id+"F4.wireOp",EDGE,"E26.5.3");var subQ23=sQuery(id+"F4.wireOp",EDGE,"E26.5.2");var subQ24=sQuery(id+"F3.wireOp",EDGE,"E20.5.3");var subQ25=sQuery(id+"F3.wireOp",EDGE,"E20.5.1");var subQ26=sQuery(id+"F4.wireOp",EDGE,"E26.6.3");var subQ27=sQuery(id+"F4.wireOp",EDGE,"E26.6.2");var subQ28=sQuery(id+"F3.wireOp",EDGE,"E20.6.3");var subQ29=sQuery(id+"F3.wireOp",EDGE,"E20.6.1");var subQ30=sQuery(id+"F4.wireOp",EDGE,"E26.7.3");var subQ31=sQuery(id+"F4.wireOp",EDGE,"E26.7.2");var subQ32=sQuery(id+"F3.wireOp",EDGE,"E20.7.3");var subQ33=sQuery(id+"F3.wireOp",EDGE,"E20.7.1");var subQ34=sQuery(id+"F4.wireOp",EDGE,"E26.8.3");var subQ35=sQuery(id+"F4.wireOp",EDGE,"E26.8.2");var subQ36=sQuery(id+"F3.wireOp",EDGE,"E20.8.3");var subQ37=sQuery(id+"F3.wireOp",EDGE,"E20.8.1");var subQ39=makeQuery(id+"F13.opLoft","SWEPT_FACE",FACE,{"disambiguationData":[OSD([sQuery(id+"F3.wireOp",EDGE,"E20.8.0"),subQ37,subQ36,sQuery(id+"F4.wireOp",EDGE,"E26.8.0"),subQ35,subQ34])]});var subQ40=sQuery(id+"F4.wireOp",EDGE,"E26.9.3");var subQ41=sQuery(id+"F4.wireOp",EDGE,"E26.9.2");var subQ42=sQuery(id+"F3.wireOp",EDGE,"E20.9.3");var subQ43=sQuery(id+"F3.wireOp",EDGE,"E20.9.1");var subQ44=sQuery(id+"F4.wireOp",EDGE,"E26.10.3");var subQ45=sQuery(id+"F4.wireOp",EDGE,"E26.10.2");var subQ46=sQuery(id+"F3.wireOp",EDGE,"E20.10.3");var subQ47=sQuery(id+"F3.wireOp",EDGE,"E20.10.1");var subQ48=sQuery(id+"F4.wireOp",EDGE,"E26.11.3");var subQ49=sQuery(id+"F4.wireOp",EDGE,"E26.11.2");var subQ50=sQuery(id+"F3.wireOp",EDGE,"E20.11.3");var subQ51=sQuery(id+"F3.wireOp",EDGE,"E20.11.1");var subQ52=sQuery(id+"F4.wireOp",EDGE,"E26.12.3");var subQ53=sQuery(id+"F4.wireOp",EDGE,"E26.12.2");var subQ54=sQuery(id+"F3.wireOp",EDGE,"E20.12.3");var subQ55=sQuery(id+"F3.wireOp",EDGE,"E20.12.1");var subQ56=sQuery(id+"F4.wireOp",EDGE,"E26.13.3");var subQ57=sQuery(id+"F4.wireOp",EDGE,"E26.13.2");var subQ58=sQuery(id+"F3.wireOp",EDGE,"E20.13.3");var subQ59=sQuery(id+"F3.wireOp",EDGE,"E20.13.1");var subQ60=sQuery(id+"F4.wireOp",EDGE,"E26.14.3");var subQ61=sQuery(id+"F4.wireOp",EDGE,"E26.14.2");var subQ62=sQuery(id+"F3.wireOp",EDGE,"E20.14.3");var subQ63=sQuery(id+"F3.wireOp",EDGE,"E20.14.1");var subQ64=sQuery(id+"F4.wireOp",EDGE,"E26.15.3");var subQ65=sQuery(id+"F4.wireOp",EDGE,"E26.15.2");var subQ66=sQuery(id+"F3.wireOp",EDGE,"E20.15.3");var subQ67=sQuery(id+"F3.wireOp",EDGE,"E20.15.1");var subQ68=sQuery(id+"F4.wireOp",EDGE,"E23");var subQ69=sQuery(id+"F4.wireOp",EDGE,"E22");var subQ70=sQuery(id+"F3.wireOp",EDGE,"E18.top");var subQ71=sQuery(id+"F3.wireOp",EDGE,"E18.bottom");var subQ74=makeQuery(id+"F42.boolean.opBoolean","COPY",FACE,{"disambiguationData":[TD([subQ39])],"derivedFrom":subQ6});var subQ75=makeQuery(id+"F13.boolean.opBoolean","INTERSECT",EDGE,{"derivedFrom":[makeQuery(id+"F1.opRevolve","SWEPT_FACE",FACE,{"disambiguationData":[OSD([sQuery(id+"F0.wireOp",EDGE,"E13")])]}),subQ39]});Q63=makeQuery(id+"F48.opFillet","BLEND_EDGE",EDGE,{"blendedFrom":[makeQuery(id+"F47.opFillet","TWEAK_EDGE",EDGE,{"derivedFrom":[makeQuery(id+"F45.opFillet","BLEND_VERTEX",VERTEX,{"blendedFrom":[subQ75,subQ39,subQ74],"blendedInto":[subQ39,subQ74]}),makeQuery(id+"F45.opFillet","BLEND_VERTEX",VERTEX,{"blendedFrom":[subQ75,makeQuery(id+"F42.boolean.opBoolean","MERGE",FACE,{"derivedFrom":[subQ0,subQ8]}),subQ74],"blendedInto":[makeQuery(id+"F42.boolean.opBoolean","MERGE",FACE,{"derivedFrom":[subQ0,subQ8]}),subQ74]})]}),makeQuery(id+"F47.opFillet","BLEND_FACE",FACE,{"disambiguationData":[OSD([subQ5,subQ7]),TDD([makeQuery(id+"F42.boolean.opBoolean","COPY",EDGE,{"disambiguationData":[TD([makeQuery(id+"F5.opLoft","SWEPT_FACE",FACE,{"disambiguationData":[OSD([subQ71,subQ70,sQuery(id+"F3.wireOp",EDGE,"E18.left"),sQuery(id+"F4.wireOp",EDGE,"E21"),subQ69,subQ68])]})])],"derivedFrom":subQ9})])]}),makeQuery(id+"F47.opFillet","BLEND_FACE",FACE,{"disambiguationData":[OSD([subQ5,subQ7]),TDD([makeQuery(id+"F42.boolean.opBoolean","COPY",EDGE,{"disambiguationData":[TD([makeQuery(id+"F6.opLoft","SWEPT_FACE",FACE,{"disambiguationData":[OSD([sQuery(id+"F3.wireOp",EDGE,"E20.15.0"),subQ67,subQ66,sQuery(id+"F4.wireOp",EDGE,"E26.15.0"),subQ65,subQ64])]})])],"derivedFrom":subQ9})])]}),makeQuery(id+"F47.opFillet","BLEND_FACE",FACE,{"disambiguationData":[OSD([subQ5,subQ7]),TDD([makeQuery(id+"F42.boolean.opBoolean","COPY",EDGE,{"disambiguationData":[TD([makeQuery(id+"F7.opLoft","SWEPT_FACE",FACE,{"disambiguationData":[OSD([sQuery(id+"F3.wireOp",EDGE,"E20.14.0"),subQ63,subQ62,sQuery(id+"F4.wireOp",EDGE,"E26.14.0"),subQ61,subQ60])]})])],"derivedFrom":subQ9})])]}),makeQuery(id+"F47.opFillet","BLEND_FACE",FACE,{"disambiguationData":[OSD([subQ5,subQ7]),TDD([makeQuery(id+"F42.boolean.opBoolean","COPY",EDGE,{"disambiguationData":[TD([makeQuery(id+"F8.opLoft","SWEPT_FACE",FACE,{"disambiguationData":[OSD([sQuery(id+"F3.wireOp",EDGE,"E20.13.0"),subQ59,subQ58,sQuery(id+"F4.wireOp",EDGE,"E26.13.0"),subQ57,subQ56])]})])],"derivedFrom":subQ9})])]}),makeQuery(id+"F47.opFillet","BLEND_FACE",FACE,{"disambiguationData":[OSD([subQ5,subQ7]),TDD([makeQuery(id+"F42.boolean.opBoolean","COPY",EDGE,{"disambiguationData":[TD([makeQuery(id+"F9.opLoft","SWEPT_FACE",FACE,{"disambiguationData":[OSD([sQuery(id+"F3.wireOp",EDGE,"E20.12.0"),subQ55,subQ54,sQuery(id+"F4.wireOp",EDGE,"E26.12.0"),subQ53,subQ52])]})])],"derivedFrom":subQ9})])]}),makeQuery(id+"F47.opFillet","BLEND_FACE",FACE,{"disambiguationData":[OSD([subQ5,subQ7]),TDD([makeQuery(id+"F42.boolean.opBoolean","COPY",EDGE,{"disambiguationData":[TD([makeQuery(id+"F10.opLoft","SWEPT_FACE",FACE,{"disambiguationData":[OSD([sQuery(id+"F3.wireOp",EDGE,"E20.11.0"),subQ51,subQ50,sQuery(id+"F4.wireOp",EDGE,"E26.11.0"),subQ49,subQ48])]})])],"derivedFrom":subQ9})])]}),makeQuery(id+"F47.opFillet","BLEND_FACE",FACE,{"disambiguationData":[OSD([subQ5,subQ7]),TDD([makeQuery(id+"F42.boolean.opBoolean","COPY",EDGE,{"disambiguationData":[TD([makeQuery(id+"F11.opLoft","SWEPT_FACE",FACE,{"disambiguationData":[OSD([sQuery(id+"F3.wireOp",EDGE,"E20.10.0"),subQ47,subQ46,sQuery(id+"F4.wireOp",EDGE,"E26.10.0"),subQ45,subQ44])]})])],"derivedFrom":subQ9})])]}),makeQuery(id+"F47.opFillet","BLEND_FACE",FACE,{"disambiguationData":[OSD([subQ5,subQ7]),TDD([makeQuery(id+"F42.boolean.opBoolean","COPY",EDGE,{"disambiguationData":[TD([makeQuery(id+"F12.opLoft","SWEPT_FACE",FACE,{"disambiguationData":[OSD([sQuery(id+"F3.wireOp",EDGE,"E20.9.0"),subQ43,subQ42,sQuery(id+"F4.wireOp",EDGE,"E26.9.0"),subQ41,subQ40])]})])],"derivedFrom":subQ9})])]}),makeQuery(id+"F47.opFillet","BLEND_FACE",FACE,{"disambiguationData":[OSD([subQ5,subQ7]),TDD([makeQuery(id+"F42.boolean.opBoolean","COPY",EDGE,{"disambiguationData":[TD([subQ39])],"derivedFrom":subQ9})])]}),makeQuery(id+"F47.opFillet","BLEND_FACE",FACE,{"disambiguationData":[OSD([subQ5,subQ7]),TDD([makeQuery(id+"F42.boolean.opBoolean","COPY",EDGE,{"disambiguationData":[TD([makeQuery(id+"F14.opLoft","SWEPT_FACE",FACE,{"disambiguationData":[OSD([sQuery(id+"F3.wireOp",EDGE,"E20.7.0"),subQ33,subQ32,sQuery(id+"F4.wireOp",EDGE,"E26.7.0"),subQ31,subQ30])]})])],"derivedFrom":subQ9})])]}),makeQuery(id+"F47.opFillet","BLEND_FACE",FACE,{"disambiguationData":[OSD([subQ5,subQ7]),TDD([makeQuery(id+"F42.boolean.opBoolean","COPY",EDGE,{"disambiguationData":[TD([makeQuery(id+"F15.opLoft","SWEPT_FACE",FACE,{"disambiguationData":[OSD([sQuery(id+"F3.wireOp",EDGE,"E20.6.0"),subQ29,subQ28,sQuery(id+"F4.wireOp",EDGE,"E26.6.0"),subQ27,subQ26])]})])],"derivedFrom":subQ9})])]}),makeQuery(id+"F47.opFillet","BLEND_FACE",FACE,{"disambiguationData":[OSD([subQ5,subQ7]),TDD([makeQuery(id+"F42.boolean.opBoolean","COPY",EDGE,{"disambiguationData":[TD([makeQuery(id+"F16.opLoft","SWEPT_FACE",FACE,{"disambiguationData":[OSD([sQuery(id+"F3.wireOp",EDGE,"E20.5.0"),subQ25,subQ24,sQuery(id+"F4.wireOp",EDGE,"E26.5.0"),subQ23,subQ22])]})])],"derivedFrom":subQ9})])]}),makeQuery(id+"F47.opFillet","BLEND_FACE",FACE,{"disambiguationData":[OSD([subQ5,subQ7]),TDD([makeQuery(id+"F42.boolean.opBoolean","COPY",EDGE,{"disambiguationData":[TD([makeQuery(id+"F17.opLoft","SWEPT_FACE",FACE,{"disambiguationData":[OSD([sQuery(id+"F3.wireOp",EDGE,"E20.4.0"),subQ21,subQ20,sQuery(id+"F4.wireOp",EDGE,"E26.4.0"),subQ19,subQ18])]})])],"derivedFrom":subQ9})])]}),makeQuery(id+"F47.opFillet","BLEND_FACE",FACE,{"disambiguationData":[OSD([subQ5,subQ7]),TDD([makeQuery(id+"F42.boolean.opBoolean","COPY",EDGE,{"disambiguationData":[TD([makeQuery(id+"F18.opLoft","SWEPT_FACE",FACE,{"disambiguationData":[OSD([sQuery(id+"F3.wireOp",EDGE,"E20.3.0"),subQ17,subQ16,sQuery(id+"F4.wireOp",EDGE,"E26.3.0"),subQ15,subQ14])]})])],"derivedFrom":subQ9})])]}),makeQuery(id+"F47.opFillet","BLEND_FACE",FACE,{"disambiguationData":[OSD([subQ5,subQ7]),TDD([makeQuery(id+"F42.boolean.opBoolean","COPY",EDGE,{"disambiguationData":[TD([makeQuery(id+"F19.opLoft","SWEPT_FACE",FACE,{"disambiguationData":[OSD([sQuery(id+"F3.wireOp",EDGE,"E20.2.0"),subQ13,subQ12,sQuery(id+"F4.wireOp",EDGE,"E26.2.0"),subQ11,subQ10])]})])],"derivedFrom":subQ9})])]}),makeQuery(id+"F47.opFillet","BLEND_FACE",FACE,{"disambiguationData":[OSD([subQ5,subQ7]),TDD([makeQuery(id+"F42.boolean.opBoolean","COPY",EDGE,{"disambiguationData":[TD([makeQuery(id+"F20.opLoft","SWEPT_FACE",FACE,{"disambiguationData":[OSD([sQuery(id+"F3.wireOp",EDGE,"E20.1.0"),subQ4,subQ3,sQuery(id+"F4.wireOp",EDGE,"E26.1.0"),subQ2,subQ1])]})])],"derivedFrom":subQ9})])]})],"blendedInto":[makeQuery(id+"F47.opFillet","BLEND_FACE",FACE,{"disambiguationData":[OSD([subQ5,subQ7]),TDD([makeQuery(id+"F42.boolean.opBoolean","COPY",EDGE,{"disambiguationData":[TD([makeQuery(id+"F5.opLoft","SWEPT_FACE",FACE,{"disambiguationData":[OSD([subQ71,subQ70,sQuery(id+"F3.wireOp",EDGE,"E18.left"),sQuery(id+"F4.wireOp",EDGE,"E21"),subQ69,subQ68])]})])],"derivedFrom":subQ9})])]}),makeQuery(id+"F47.opFillet","BLEND_FACE",FACE,{"disambiguationData":[OSD([subQ5,subQ7]),TDD([makeQuery(id+"F42.boolean.opBoolean","COPY",EDGE,{"disambiguationData":[TD([makeQuery(id+"F6.opLoft","SWEPT_FACE",FACE,{"disambiguationData":[OSD([sQuery(id+"F3.wireOp",EDGE,"E20.15.0"),subQ67,subQ66,sQuery(id+"F4.wireOp",EDGE,"E26.15.0"),subQ65,subQ64])]})])],"derivedFrom":subQ9})])]}),makeQuery(id+"F47.opFillet","BLEND_FACE",FACE,{"disambiguationData":[OSD([subQ5,subQ7]),TDD([makeQuery(id+"F42.boolean.opBoolean","COPY",EDGE,{"disambiguationData":[TD([makeQuery(id+"F7.opLoft","SWEPT_FACE",FACE,{"disambiguationData":[OSD([sQuery(id+"F3.wireOp",EDGE,"E20.14.0"),subQ63,subQ62,sQuery(id+"F4.wireOp",EDGE,"E26.14.0"),subQ61,subQ60])]})])],"derivedFrom":subQ9})])]}),makeQuery(id+"F47.opFillet","BLEND_FACE",FACE,{"disambiguationData":[OSD([subQ5,subQ7]),TDD([makeQuery(id+"F42.boolean.opBoolean","COPY",EDGE,{"disambiguationData":[TD([makeQuery(id+"F8.opLoft","SWEPT_FACE",FACE,{"disambiguationData":[OSD([sQuery(id+"F3.wireOp",EDGE,"E20.13.0"),subQ59,subQ58,sQuery(id+"F4.wireOp",EDGE,"E26.13.0"),subQ57,subQ56])]})])],"derivedFrom":subQ9})])]}),makeQuery(id+"F47.opFillet","BLEND_FACE",FACE,{"disambiguationData":[OSD([subQ5,subQ7]),TDD([makeQuery(id+"F42.boolean.opBoolean","COPY",EDGE,{"disambiguationData":[TD([makeQuery(id+"F9.opLoft","SWEPT_FACE",FACE,{"disambiguationData":[OSD([sQuery(id+"F3.wireOp",EDGE,"E20.12.0"),subQ55,subQ54,sQuery(id+"F4.wireOp",EDGE,"E26.12.0"),subQ53,subQ52])]})])],"derivedFrom":subQ9})])]}),makeQuery(id+"F47.opFillet","BLEND_FACE",FACE,{"disambiguationData":[OSD([subQ5,subQ7]),TDD([makeQuery(id+"F42.boolean.opBoolean","COPY",EDGE,{"disambiguationData":[TD([makeQuery(id+"F10.opLoft","SWEPT_FACE",FACE,{"disambiguationData":[OSD([sQuery(id+"F3.wireOp",EDGE,"E20.11.0"),subQ51,subQ50,sQuery(id+"F4.wireOp",EDGE,"E26.11.0"),subQ49,subQ48])]})])],"derivedFrom":subQ9})])]}),makeQuery(id+"F47.opFillet","BLEND_FACE",FACE,{"disambiguationData":[OSD([subQ5,subQ7]),TDD([makeQuery(id+"F42.boolean.opBoolean","COPY",EDGE,{"disambiguationData":[TD([makeQuery(id+"F11.opLoft","SWEPT_FACE",FACE,{"disambiguationData":[OSD([sQuery(id+"F3.wireOp",EDGE,"E20.10.0"),subQ47,subQ46,sQuery(id+"F4.wireOp",EDGE,"E26.10.0"),subQ45,subQ44])]})])],"derivedFrom":subQ9})])]}),makeQuery(id+"F47.opFillet","BLEND_FACE",FACE,{"disambiguationData":[OSD([subQ5,subQ7]),TDD([makeQuery(id+"F42.boolean.opBoolean","COPY",EDGE,{"disambiguationData":[TD([makeQuery(id+"F12.opLoft","SWEPT_FACE",FACE,{"disambiguationData":[OSD([sQuery(id+"F3.wireOp",EDGE,"E20.9.0"),subQ43,subQ42,sQuery(id+"F4.wireOp",EDGE,"E26.9.0"),subQ41,subQ40])]})])],"derivedFrom":subQ9})])]}),makeQuery(id+"F47.opFillet","BLEND_FACE",FACE,{"disambiguationData":[OSD([subQ5,subQ7]),TDD([makeQuery(id+"F42.boolean.opBoolean","COPY",EDGE,{"disambiguationData":[TD([subQ39])],"derivedFrom":subQ9})])]}),makeQuery(id+"F47.opFillet","BLEND_FACE",FACE,{"disambiguationData":[OSD([subQ5,subQ7]),TDD([makeQuery(id+"F42.boolean.opBoolean","COPY",EDGE,{"disambiguationData":[TD([makeQuery(id+"F14.opLoft","SWEPT_FACE",FACE,{"disambiguationData":[OSD([sQuery(id+"F3.wireOp",EDGE,"E20.7.0"),subQ33,subQ32,sQuery(id+"F4.wireOp",EDGE,"E26.7.0"),subQ31,subQ30])]})])],"derivedFrom":subQ9})])]}),makeQuery(id+"F47.opFillet","BLEND_FACE",FACE,{"disambiguationData":[OSD([subQ5,subQ7]),TDD([makeQuery(id+"F42.boolean.opBoolean","COPY",EDGE,{"disambiguationData":[TD([makeQuery(id+"F15.opLoft","SWEPT_FACE",FACE,{"disambiguationData":[OSD([sQuery(id+"F3.wireOp",EDGE,"E20.6.0"),subQ29,subQ28,sQuery(id+"F4.wireOp",EDGE,"E26.6.0"),subQ27,subQ26])]})])],"derivedFrom":subQ9})])]}),makeQuery(id+"F47.opFillet","BLEND_FACE",FACE,{"disambiguationData":[OSD([subQ5,subQ7]),TDD([makeQuery(id+"F42.boolean.opBoolean","COPY",EDGE,{"disambiguationData":[TD([makeQuery(id+"F16.opLoft","SWEPT_FACE",FACE,{"disambiguationData":[OSD([sQuery(id+"F3.wireOp",EDGE,"E20.5.0"),subQ25,subQ24,sQuery(id+"F4.wireOp",EDGE,"E26.5.0"),subQ23,subQ22])]})])],"derivedFrom":subQ9})])]}),makeQuery(id+"F47.opFillet","BLEND_FACE",FACE,{"disambiguationData":[OSD([subQ5,subQ7]),TDD([makeQuery(id+"F42.boolean.opBoolean","COPY",EDGE,{"disambiguationData":[TD([makeQuery(id+"F17.opLoft","SWEPT_FACE",FACE,{"disambiguationData":[OSD([sQuery(id+"F3.wireOp",EDGE,"E20.4.0"),subQ21,subQ20,sQuery(id+"F4.wireOp",EDGE,"E26.4.0"),subQ19,subQ18])]})])],"derivedFrom":subQ9})])]}),makeQuery(id+"F47.opFillet","BLEND_FACE",FACE,{"disambiguationData":[OSD([subQ5,subQ7]),TDD([makeQuery(id+"F42.boolean.opBoolean","COPY",EDGE,{"disambiguationData":[TD([makeQuery(id+"F18.opLoft","SWEPT_FACE",FACE,{"disambiguationData":[OSD([sQuery(id+"F3.wireOp",EDGE,"E20.3.0"),subQ17,subQ16,sQuery(id+"F4.wireOp",EDGE,"E26.3.0"),subQ15,subQ14])]})])],"derivedFrom":subQ9})])]}),makeQuery(id+"F47.opFillet","BLEND_FACE",FACE,{"disambiguationData":[OSD([subQ5,subQ7]),TDD([makeQuery(id+"F42.boolean.opBoolean","COPY",EDGE,{"disambiguationData":[TD([makeQuery(id+"F19.opLoft","SWEPT_FACE",FACE,{"disambiguationData":[OSD([sQuery(id+"F3.wireOp",EDGE,"E20.2.0"),subQ13,subQ12,sQuery(id+"F4.wireOp",EDGE,"E26.2.0"),subQ11,subQ10])]})])],"derivedFrom":subQ9})])]}),makeQuery(id+"F47.opFillet","BLEND_FACE",FACE,{"disambiguationData":[OSD([subQ5,subQ7]),TDD([makeQuery(id+"F42.boolean.opBoolean","COPY",EDGE,{"disambiguationData":[TD([makeQuery(id+"F20.opLoft","SWEPT_FACE",FACE,{"disambiguationData":[OSD([sQuery(id+"F3.wireOp",EDGE,"E20.1.0"),subQ4,subQ3,sQuery(id+"F4.wireOp",EDGE,"E26.1.0"),subQ2,subQ1])]})])],"derivedFrom":subQ9})])]})]});}
            var Q64;
            {var subQ0=sQuery(id+"F4.wireOp",EDGE,"E26.7.3");var subQ1=sQuery(id+"F4.wireOp",EDGE,"E26.7.2");var subQ2=sQuery(id+"F4.wireOp",EDGE,"E26.7.0");var subQ3=sQuery(id+"F3.wireOp",EDGE,"E20.7.3");var subQ4=sQuery(id+"F3.wireOp",EDGE,"E20.7.1");var subQ5=sQuery(id+"F4.wireOp",EDGE,"E26.7.1");var subQ6=makeQuery(id+"F14.opLoft","SWEPT_FACE",FACE,{"disambiguationData":[OSD([subQ4,sQuery(id+"F3.wireOp",EDGE,"E20.7.2"),subQ3,subQ5,subQ1,subQ0])]});var subQ7=sQuery(id+"F41.wireOp",EDGE,"E34");var subQ8=sQuery(id+"F41.wireOp",EDGE,"E32");Q64=makeQuery(id+"F44.opFillet","BLEND_EDGE",EDGE,{"blendedFrom":[makeQuery(id+"F40.boolean.opBoolean","INTERSECT",EDGE,{"derivedFrom":[subQ6,makeQuery(id+"F40.opExtrude","CAP_FACE",FACE,{"disambiguationData":[OSD([sQuery(id+"F39.wireOp",EDGE,"E29"),sQuery(id+"F39.wireOp",EDGE,"E30")])],"isStart":false})]}),makeQuery(id+"F42.boolean.opBoolean","COPY",FACE,{"disambiguationData":[TD([makeQuery(id+"F14.opLoft","SWEPT_FACE",FACE,{"disambiguationData":[OSD([sQuery(id+"F3.wireOp",EDGE,"E20.7.0"),subQ4,subQ3,subQ2,subQ1,subQ0])]})])],"derivedFrom":makeQuery(id+"F42.opRevolve","SWEPT_FACE",FACE,{"disambiguationData":[OSD([subQ8]),TDD([makeQuery(id+"F41.imprint","IMPRINT",EDGE,{"disambiguationData":[TD([[makeQuery(id+"F41.imprint","INTERSECT",VERTEX,{"disambiguationData":[OD(0.0)],"derivedFrom":[subQ8,subQ7]}),-1.0]])],"derivedFrom":subQ8})])]})})],"blendedInto":[makeQuery(id+"F42.boolean.opBoolean","COPY",FACE,{"disambiguationData":[TD([makeQuery(id+"F14.opLoft","SWEPT_FACE",FACE,{"disambiguationData":[OSD([sQuery(id+"F3.wireOp",EDGE,"E20.7.0"),subQ4,subQ3,subQ2,subQ1,subQ0])]})])],"derivedFrom":makeQuery(id+"F42.opRevolve","SWEPT_FACE",FACE,{"disambiguationData":[OSD([subQ8]),TDD([makeQuery(id+"F41.imprint","IMPRINT",EDGE,{"disambiguationData":[TD([[makeQuery(id+"F41.imprint","INTERSECT",VERTEX,{"disambiguationData":[OD(0.0)],"derivedFrom":[subQ8,subQ7]}),-1.0]])],"derivedFrom":subQ8})])]})})]});}
            var Q65;
            {var subQ0=sQuery(id+"F41.wireOp",EDGE,"E34");var subQ1=sQuery(id+"F41.wireOp",EDGE,"E32");Q65=makeQuery(id+"F42.boolean.opBoolean","INTERSECT",EDGE,{"derivedFrom":[makeQuery(id+"F14.opLoft","SWEPT_FACE",FACE,{"disambiguationData":[OSD([sQuery(id+"F3.wireOp",EDGE,"E20.7.0"),sQuery(id+"F3.wireOp",EDGE,"E20.7.1"),sQuery(id+"F3.wireOp",EDGE,"E20.7.3"),sQuery(id+"F4.wireOp",EDGE,"E26.7.0"),sQuery(id+"F4.wireOp",EDGE,"E26.7.2"),sQuery(id+"F4.wireOp",EDGE,"E26.7.3")])]}),makeQuery(id+"F42.opRevolve","SWEPT_FACE",FACE,{"disambiguationData":[OSD([subQ1]),TDD([makeQuery(id+"F41.imprint","IMPRINT",EDGE,{"disambiguationData":[TD([[makeQuery(id+"F41.imprint","INTERSECT",VERTEX,{"disambiguationData":[OD(0.0)],"derivedFrom":[subQ1,subQ0]}),-1.0]])],"derivedFrom":subQ1})])]})]});}
            var Q66;
            {var subQ0=sQuery(id+"F4.wireOp",EDGE,"E26.8.3");var subQ1=sQuery(id+"F4.wireOp",EDGE,"E26.8.2");var subQ2=sQuery(id+"F4.wireOp",EDGE,"E26.8.0");var subQ3=sQuery(id+"F3.wireOp",EDGE,"E20.8.3");var subQ4=sQuery(id+"F3.wireOp",EDGE,"E20.8.1");var subQ5=sQuery(id+"F4.wireOp",EDGE,"E26.8.1");var subQ6=makeQuery(id+"F13.opLoft","SWEPT_FACE",FACE,{"disambiguationData":[OSD([subQ4,sQuery(id+"F3.wireOp",EDGE,"E20.8.2"),subQ3,subQ5,subQ1,subQ0])]});var subQ7=sQuery(id+"F41.wireOp",EDGE,"E34");var subQ8=sQuery(id+"F41.wireOp",EDGE,"E32");Q66=makeQuery(id+"F44.opFillet","BLEND_EDGE",EDGE,{"blendedFrom":[makeQuery(id+"F40.boolean.opBoolean","INTERSECT",EDGE,{"derivedFrom":[subQ6,makeQuery(id+"F40.opExtrude","CAP_FACE",FACE,{"disambiguationData":[OSD([sQuery(id+"F39.wireOp",EDGE,"E29"),sQuery(id+"F39.wireOp",EDGE,"E30")])],"isStart":false})]}),makeQuery(id+"F42.boolean.opBoolean","COPY",FACE,{"disambiguationData":[TD([makeQuery(id+"F13.opLoft","SWEPT_FACE",FACE,{"disambiguationData":[OSD([sQuery(id+"F3.wireOp",EDGE,"E20.8.0"),subQ4,subQ3,subQ2,subQ1,subQ0])]})])],"derivedFrom":makeQuery(id+"F42.opRevolve","SWEPT_FACE",FACE,{"disambiguationData":[OSD([subQ8]),TDD([makeQuery(id+"F41.imprint","IMPRINT",EDGE,{"disambiguationData":[TD([[makeQuery(id+"F41.imprint","INTERSECT",VERTEX,{"disambiguationData":[OD(0.0)],"derivedFrom":[subQ8,subQ7]}),-1.0]])],"derivedFrom":subQ8})])]})})],"blendedInto":[makeQuery(id+"F42.boolean.opBoolean","COPY",FACE,{"disambiguationData":[TD([makeQuery(id+"F13.opLoft","SWEPT_FACE",FACE,{"disambiguationData":[OSD([sQuery(id+"F3.wireOp",EDGE,"E20.8.0"),subQ4,subQ3,subQ2,subQ1,subQ0])]})])],"derivedFrom":makeQuery(id+"F42.opRevolve","SWEPT_FACE",FACE,{"disambiguationData":[OSD([subQ8]),TDD([makeQuery(id+"F41.imprint","IMPRINT",EDGE,{"disambiguationData":[TD([[makeQuery(id+"F41.imprint","INTERSECT",VERTEX,{"disambiguationData":[OD(0.0)],"derivedFrom":[subQ8,subQ7]}),-1.0]])],"derivedFrom":subQ8})])]})})]});}
            var Q67;
            {var subQ0=sQuery(id+"F41.wireOp",EDGE,"E34");var subQ1=sQuery(id+"F41.wireOp",EDGE,"E32");Q67=makeQuery(id+"F42.boolean.opBoolean","INTERSECT",EDGE,{"derivedFrom":[makeQuery(id+"F13.opLoft","SWEPT_FACE",FACE,{"disambiguationData":[OSD([sQuery(id+"F3.wireOp",EDGE,"E20.8.0"),sQuery(id+"F3.wireOp",EDGE,"E20.8.1"),sQuery(id+"F3.wireOp",EDGE,"E20.8.3"),sQuery(id+"F4.wireOp",EDGE,"E26.8.0"),sQuery(id+"F4.wireOp",EDGE,"E26.8.2"),sQuery(id+"F4.wireOp",EDGE,"E26.8.3")])]}),makeQuery(id+"F42.opRevolve","SWEPT_FACE",FACE,{"disambiguationData":[OSD([subQ1]),TDD([makeQuery(id+"F41.imprint","IMPRINT",EDGE,{"disambiguationData":[TD([[makeQuery(id+"F41.imprint","INTERSECT",VERTEX,{"disambiguationData":[OD(0.0)],"derivedFrom":[subQ1,subQ0]}),-1.0]])],"derivedFrom":subQ1})])]})]});}
            var Q68;
            {var subQ0=sQuery(id+"F4.wireOp",EDGE,"E26.9.3");var subQ1=sQuery(id+"F4.wireOp",EDGE,"E26.9.2");var subQ2=sQuery(id+"F4.wireOp",EDGE,"E26.9.0");var subQ3=sQuery(id+"F3.wireOp",EDGE,"E20.9.3");var subQ4=sQuery(id+"F3.wireOp",EDGE,"E20.9.1");var subQ5=sQuery(id+"F4.wireOp",EDGE,"E26.9.1");var subQ6=makeQuery(id+"F12.opLoft","SWEPT_FACE",FACE,{"disambiguationData":[OSD([subQ4,sQuery(id+"F3.wireOp",EDGE,"E20.9.2"),subQ3,subQ5,subQ1,subQ0])]});var subQ7=sQuery(id+"F41.wireOp",EDGE,"E34");var subQ8=sQuery(id+"F41.wireOp",EDGE,"E32");Q68=makeQuery(id+"F44.opFillet","BLEND_EDGE",EDGE,{"blendedFrom":[makeQuery(id+"F40.boolean.opBoolean","INTERSECT",EDGE,{"derivedFrom":[subQ6,makeQuery(id+"F40.opExtrude","CAP_FACE",FACE,{"disambiguationData":[OSD([sQuery(id+"F39.wireOp",EDGE,"E29"),sQuery(id+"F39.wireOp",EDGE,"E30")])],"isStart":false})]}),makeQuery(id+"F42.boolean.opBoolean","COPY",FACE,{"disambiguationData":[TD([makeQuery(id+"F12.opLoft","SWEPT_FACE",FACE,{"disambiguationData":[OSD([sQuery(id+"F3.wireOp",EDGE,"E20.9.0"),subQ4,subQ3,subQ2,subQ1,subQ0])]})])],"derivedFrom":makeQuery(id+"F42.opRevolve","SWEPT_FACE",FACE,{"disambiguationData":[OSD([subQ8]),TDD([makeQuery(id+"F41.imprint","IMPRINT",EDGE,{"disambiguationData":[TD([[makeQuery(id+"F41.imprint","INTERSECT",VERTEX,{"disambiguationData":[OD(0.0)],"derivedFrom":[subQ8,subQ7]}),-1.0]])],"derivedFrom":subQ8})])]})})],"blendedInto":[makeQuery(id+"F42.boolean.opBoolean","COPY",FACE,{"disambiguationData":[TD([makeQuery(id+"F12.opLoft","SWEPT_FACE",FACE,{"disambiguationData":[OSD([sQuery(id+"F3.wireOp",EDGE,"E20.9.0"),subQ4,subQ3,subQ2,subQ1,subQ0])]})])],"derivedFrom":makeQuery(id+"F42.opRevolve","SWEPT_FACE",FACE,{"disambiguationData":[OSD([subQ8]),TDD([makeQuery(id+"F41.imprint","IMPRINT",EDGE,{"disambiguationData":[TD([[makeQuery(id+"F41.imprint","INTERSECT",VERTEX,{"disambiguationData":[OD(0.0)],"derivedFrom":[subQ8,subQ7]}),-1.0]])],"derivedFrom":subQ8})])]})})]});}
            var Q69;
            {var subQ0=sQuery(id+"F41.wireOp",EDGE,"E34");var subQ1=sQuery(id+"F41.wireOp",EDGE,"E32");Q69=makeQuery(id+"F42.boolean.opBoolean","INTERSECT",EDGE,{"derivedFrom":[makeQuery(id+"F12.opLoft","SWEPT_FACE",FACE,{"disambiguationData":[OSD([sQuery(id+"F3.wireOp",EDGE,"E20.9.0"),sQuery(id+"F3.wireOp",EDGE,"E20.9.1"),sQuery(id+"F3.wireOp",EDGE,"E20.9.3"),sQuery(id+"F4.wireOp",EDGE,"E26.9.0"),sQuery(id+"F4.wireOp",EDGE,"E26.9.2"),sQuery(id+"F4.wireOp",EDGE,"E26.9.3")])]}),makeQuery(id+"F42.opRevolve","SWEPT_FACE",FACE,{"disambiguationData":[OSD([subQ1]),TDD([makeQuery(id+"F41.imprint","IMPRINT",EDGE,{"disambiguationData":[TD([[makeQuery(id+"F41.imprint","INTERSECT",VERTEX,{"disambiguationData":[OD(0.0)],"derivedFrom":[subQ1,subQ0]}),-1.0]])],"derivedFrom":subQ1})])]})]});}
            var Q70;
            {var subQ0=sQuery(id+"F4.wireOp",EDGE,"E26.10.0");var subQ1=sQuery(id+"F4.wireOp",EDGE,"E26.10.1");var subQ2=sQuery(id+"F4.wireOp",EDGE,"E26.10.2");var subQ3=sQuery(id+"F4.wireOp",EDGE,"E26.10.3");var subQ4=sQuery(id+"F3.wireOp",EDGE,"E20.10.3");var subQ5=sQuery(id+"F3.wireOp",EDGE,"E20.10.1");var subQ6=makeQuery(id+"F11.opLoft","SWEPT_FACE",FACE,{"disambiguationData":[OSD([subQ5,sQuery(id+"F3.wireOp",EDGE,"E20.10.2"),subQ4,subQ1,subQ2,subQ3])]});var subQ7=sQuery(id+"F41.wireOp",EDGE,"E34");var subQ8=sQuery(id+"F41.wireOp",EDGE,"E32");Q70=makeQuery(id+"F44.opFillet","BLEND_EDGE",EDGE,{"blendedFrom":[makeQuery(id+"F40.boolean.opBoolean","INTERSECT",EDGE,{"derivedFrom":[subQ6,makeQuery(id+"F40.opExtrude","CAP_FACE",FACE,{"disambiguationData":[OSD([sQuery(id+"F39.wireOp",EDGE,"E29"),sQuery(id+"F39.wireOp",EDGE,"E30")])],"isStart":false})]}),makeQuery(id+"F42.boolean.opBoolean","COPY",FACE,{"disambiguationData":[TD([makeQuery(id+"F11.opLoft","SWEPT_FACE",FACE,{"disambiguationData":[OSD([sQuery(id+"F3.wireOp",EDGE,"E20.10.0"),subQ5,subQ4,subQ0,subQ2,subQ3])]})])],"derivedFrom":makeQuery(id+"F42.opRevolve","SWEPT_FACE",FACE,{"disambiguationData":[OSD([subQ8]),TDD([makeQuery(id+"F41.imprint","IMPRINT",EDGE,{"disambiguationData":[TD([[makeQuery(id+"F41.imprint","INTERSECT",VERTEX,{"disambiguationData":[OD(0.0)],"derivedFrom":[subQ8,subQ7]}),-1.0]])],"derivedFrom":subQ8})])]})})],"blendedInto":[makeQuery(id+"F42.boolean.opBoolean","COPY",FACE,{"disambiguationData":[TD([makeQuery(id+"F11.opLoft","SWEPT_FACE",FACE,{"disambiguationData":[OSD([sQuery(id+"F3.wireOp",EDGE,"E20.10.0"),subQ5,subQ4,subQ0,subQ2,subQ3])]})])],"derivedFrom":makeQuery(id+"F42.opRevolve","SWEPT_FACE",FACE,{"disambiguationData":[OSD([subQ8]),TDD([makeQuery(id+"F41.imprint","IMPRINT",EDGE,{"disambiguationData":[TD([[makeQuery(id+"F41.imprint","INTERSECT",VERTEX,{"disambiguationData":[OD(0.0)],"derivedFrom":[subQ8,subQ7]}),-1.0]])],"derivedFrom":subQ8})])]})})]});}
            var Q71;
            {var subQ0=sQuery(id+"F41.wireOp",EDGE,"E34");var subQ1=sQuery(id+"F41.wireOp",EDGE,"E32");Q71=makeQuery(id+"F42.boolean.opBoolean","INTERSECT",EDGE,{"derivedFrom":[makeQuery(id+"F11.opLoft","SWEPT_FACE",FACE,{"disambiguationData":[OSD([sQuery(id+"F3.wireOp",EDGE,"E20.10.0"),sQuery(id+"F3.wireOp",EDGE,"E20.10.1"),sQuery(id+"F3.wireOp",EDGE,"E20.10.3"),sQuery(id+"F4.wireOp",EDGE,"E26.10.0"),sQuery(id+"F4.wireOp",EDGE,"E26.10.2"),sQuery(id+"F4.wireOp",EDGE,"E26.10.3")])]}),makeQuery(id+"F42.opRevolve","SWEPT_FACE",FACE,{"disambiguationData":[OSD([subQ1]),TDD([makeQuery(id+"F41.imprint","IMPRINT",EDGE,{"disambiguationData":[TD([[makeQuery(id+"F41.imprint","INTERSECT",VERTEX,{"disambiguationData":[OD(0.0)],"derivedFrom":[subQ1,subQ0]}),-1.0]])],"derivedFrom":subQ1})])]})]});}
            var Q72;
            {var subQ0=sQuery(id+"F4.wireOp",EDGE,"E26.11.0");var subQ1=sQuery(id+"F4.wireOp",EDGE,"E26.11.1");var subQ2=sQuery(id+"F4.wireOp",EDGE,"E26.11.2");var subQ3=sQuery(id+"F4.wireOp",EDGE,"E26.11.3");var subQ4=sQuery(id+"F3.wireOp",EDGE,"E20.11.3");var subQ5=sQuery(id+"F3.wireOp",EDGE,"E20.11.1");var subQ6=makeQuery(id+"F10.opLoft","SWEPT_FACE",FACE,{"disambiguationData":[OSD([subQ5,sQuery(id+"F3.wireOp",EDGE,"E20.11.2"),subQ4,subQ1,subQ2,subQ3])]});var subQ7=sQuery(id+"F41.wireOp",EDGE,"E34");var subQ8=sQuery(id+"F41.wireOp",EDGE,"E32");Q72=makeQuery(id+"F44.opFillet","BLEND_EDGE",EDGE,{"blendedFrom":[makeQuery(id+"F40.boolean.opBoolean","INTERSECT",EDGE,{"derivedFrom":[subQ6,makeQuery(id+"F40.opExtrude","CAP_FACE",FACE,{"disambiguationData":[OSD([sQuery(id+"F39.wireOp",EDGE,"E29"),sQuery(id+"F39.wireOp",EDGE,"E30")])],"isStart":false})]}),makeQuery(id+"F42.boolean.opBoolean","COPY",FACE,{"disambiguationData":[TD([makeQuery(id+"F10.opLoft","SWEPT_FACE",FACE,{"disambiguationData":[OSD([sQuery(id+"F3.wireOp",EDGE,"E20.11.0"),subQ5,subQ4,subQ0,subQ2,subQ3])]})])],"derivedFrom":makeQuery(id+"F42.opRevolve","SWEPT_FACE",FACE,{"disambiguationData":[OSD([subQ8]),TDD([makeQuery(id+"F41.imprint","IMPRINT",EDGE,{"disambiguationData":[TD([[makeQuery(id+"F41.imprint","INTERSECT",VERTEX,{"disambiguationData":[OD(0.0)],"derivedFrom":[subQ8,subQ7]}),-1.0]])],"derivedFrom":subQ8})])]})})],"blendedInto":[makeQuery(id+"F42.boolean.opBoolean","COPY",FACE,{"disambiguationData":[TD([makeQuery(id+"F10.opLoft","SWEPT_FACE",FACE,{"disambiguationData":[OSD([sQuery(id+"F3.wireOp",EDGE,"E20.11.0"),subQ5,subQ4,subQ0,subQ2,subQ3])]})])],"derivedFrom":makeQuery(id+"F42.opRevolve","SWEPT_FACE",FACE,{"disambiguationData":[OSD([subQ8]),TDD([makeQuery(id+"F41.imprint","IMPRINT",EDGE,{"disambiguationData":[TD([[makeQuery(id+"F41.imprint","INTERSECT",VERTEX,{"disambiguationData":[OD(0.0)],"derivedFrom":[subQ8,subQ7]}),-1.0]])],"derivedFrom":subQ8})])]})})]});}
            var Q73;
            {var subQ0=sQuery(id+"F41.wireOp",EDGE,"E34");var subQ1=sQuery(id+"F41.wireOp",EDGE,"E32");Q73=makeQuery(id+"F42.boolean.opBoolean","INTERSECT",EDGE,{"derivedFrom":[makeQuery(id+"F10.opLoft","SWEPT_FACE",FACE,{"disambiguationData":[OSD([sQuery(id+"F3.wireOp",EDGE,"E20.11.0"),sQuery(id+"F3.wireOp",EDGE,"E20.11.1"),sQuery(id+"F3.wireOp",EDGE,"E20.11.3"),sQuery(id+"F4.wireOp",EDGE,"E26.11.0"),sQuery(id+"F4.wireOp",EDGE,"E26.11.2"),sQuery(id+"F4.wireOp",EDGE,"E26.11.3")])]}),makeQuery(id+"F42.opRevolve","SWEPT_FACE",FACE,{"disambiguationData":[OSD([subQ1]),TDD([makeQuery(id+"F41.imprint","IMPRINT",EDGE,{"disambiguationData":[TD([[makeQuery(id+"F41.imprint","INTERSECT",VERTEX,{"disambiguationData":[OD(0.0)],"derivedFrom":[subQ1,subQ0]}),-1.0]])],"derivedFrom":subQ1})])]})]});}
            var Q74;
            {var subQ0=sQuery(id+"F4.wireOp",EDGE,"E26.12.0");var subQ1=sQuery(id+"F4.wireOp",EDGE,"E26.12.2");var subQ2=sQuery(id+"F4.wireOp",EDGE,"E26.12.1");var subQ3=sQuery(id+"F4.wireOp",EDGE,"E26.12.3");var subQ4=sQuery(id+"F3.wireOp",EDGE,"E20.12.3");var subQ5=sQuery(id+"F3.wireOp",EDGE,"E20.12.1");var subQ6=makeQuery(id+"F9.opLoft","SWEPT_FACE",FACE,{"disambiguationData":[OSD([subQ5,sQuery(id+"F3.wireOp",EDGE,"E20.12.2"),subQ4,subQ2,subQ1,subQ3])]});var subQ7=sQuery(id+"F41.wireOp",EDGE,"E34");var subQ8=sQuery(id+"F41.wireOp",EDGE,"E32");Q74=makeQuery(id+"F44.opFillet","BLEND_EDGE",EDGE,{"blendedFrom":[makeQuery(id+"F40.boolean.opBoolean","INTERSECT",EDGE,{"derivedFrom":[subQ6,makeQuery(id+"F40.opExtrude","CAP_FACE",FACE,{"disambiguationData":[OSD([sQuery(id+"F39.wireOp",EDGE,"E29"),sQuery(id+"F39.wireOp",EDGE,"E30")])],"isStart":false})]}),makeQuery(id+"F42.boolean.opBoolean","COPY",FACE,{"disambiguationData":[TD([makeQuery(id+"F9.opLoft","SWEPT_FACE",FACE,{"disambiguationData":[OSD([sQuery(id+"F3.wireOp",EDGE,"E20.12.0"),subQ5,subQ4,subQ0,subQ1,subQ3])]})])],"derivedFrom":makeQuery(id+"F42.opRevolve","SWEPT_FACE",FACE,{"disambiguationData":[OSD([subQ8]),TDD([makeQuery(id+"F41.imprint","IMPRINT",EDGE,{"disambiguationData":[TD([[makeQuery(id+"F41.imprint","INTERSECT",VERTEX,{"disambiguationData":[OD(0.0)],"derivedFrom":[subQ8,subQ7]}),-1.0]])],"derivedFrom":subQ8})])]})})],"blendedInto":[makeQuery(id+"F42.boolean.opBoolean","COPY",FACE,{"disambiguationData":[TD([makeQuery(id+"F9.opLoft","SWEPT_FACE",FACE,{"disambiguationData":[OSD([sQuery(id+"F3.wireOp",EDGE,"E20.12.0"),subQ5,subQ4,subQ0,subQ1,subQ3])]})])],"derivedFrom":makeQuery(id+"F42.opRevolve","SWEPT_FACE",FACE,{"disambiguationData":[OSD([subQ8]),TDD([makeQuery(id+"F41.imprint","IMPRINT",EDGE,{"disambiguationData":[TD([[makeQuery(id+"F41.imprint","INTERSECT",VERTEX,{"disambiguationData":[OD(0.0)],"derivedFrom":[subQ8,subQ7]}),-1.0]])],"derivedFrom":subQ8})])]})})]});}
            var Q75;
            {var subQ0=sQuery(id+"F41.wireOp",EDGE,"E34");var subQ1=sQuery(id+"F41.wireOp",EDGE,"E32");Q75=makeQuery(id+"F42.boolean.opBoolean","INTERSECT",EDGE,{"derivedFrom":[makeQuery(id+"F9.opLoft","SWEPT_FACE",FACE,{"disambiguationData":[OSD([sQuery(id+"F3.wireOp",EDGE,"E20.12.0"),sQuery(id+"F3.wireOp",EDGE,"E20.12.1"),sQuery(id+"F3.wireOp",EDGE,"E20.12.3"),sQuery(id+"F4.wireOp",EDGE,"E26.12.0"),sQuery(id+"F4.wireOp",EDGE,"E26.12.2"),sQuery(id+"F4.wireOp",EDGE,"E26.12.3")])]}),makeQuery(id+"F42.opRevolve","SWEPT_FACE",FACE,{"disambiguationData":[OSD([subQ1]),TDD([makeQuery(id+"F41.imprint","IMPRINT",EDGE,{"disambiguationData":[TD([[makeQuery(id+"F41.imprint","INTERSECT",VERTEX,{"disambiguationData":[OD(0.0)],"derivedFrom":[subQ1,subQ0]}),-1.0]])],"derivedFrom":subQ1})])]})]});}
            var Q76;
            {var subQ0=sQuery(id+"F4.wireOp",EDGE,"E26.13.3");var subQ1=sQuery(id+"F4.wireOp",EDGE,"E26.13.2");var subQ2=sQuery(id+"F4.wireOp",EDGE,"E26.13.1");var subQ3=sQuery(id+"F3.wireOp",EDGE,"E20.13.3");var subQ4=sQuery(id+"F3.wireOp",EDGE,"E20.13.1");var subQ5=makeQuery(id+"F8.opLoft","SWEPT_FACE",FACE,{"disambiguationData":[OSD([subQ4,sQuery(id+"F3.wireOp",EDGE,"E20.13.2"),subQ3,subQ2,subQ1,subQ0])]});var subQ6=sQuery(id+"F4.wireOp",EDGE,"E26.13.0");var subQ7=sQuery(id+"F41.wireOp",EDGE,"E34");var subQ8=sQuery(id+"F41.wireOp",EDGE,"E32");Q76=makeQuery(id+"F44.opFillet","BLEND_EDGE",EDGE,{"blendedFrom":[makeQuery(id+"F40.boolean.opBoolean","INTERSECT",EDGE,{"derivedFrom":[subQ5,makeQuery(id+"F40.opExtrude","CAP_FACE",FACE,{"disambiguationData":[OSD([sQuery(id+"F39.wireOp",EDGE,"E29"),sQuery(id+"F39.wireOp",EDGE,"E30")])],"isStart":false})]}),makeQuery(id+"F42.boolean.opBoolean","COPY",FACE,{"disambiguationData":[TD([makeQuery(id+"F8.opLoft","SWEPT_FACE",FACE,{"disambiguationData":[OSD([sQuery(id+"F3.wireOp",EDGE,"E20.13.0"),subQ4,subQ3,subQ6,subQ1,subQ0])]})])],"derivedFrom":makeQuery(id+"F42.opRevolve","SWEPT_FACE",FACE,{"disambiguationData":[OSD([subQ8]),TDD([makeQuery(id+"F41.imprint","IMPRINT",EDGE,{"disambiguationData":[TD([[makeQuery(id+"F41.imprint","INTERSECT",VERTEX,{"disambiguationData":[OD(0.0)],"derivedFrom":[subQ8,subQ7]}),-1.0]])],"derivedFrom":subQ8})])]})})],"blendedInto":[makeQuery(id+"F42.boolean.opBoolean","COPY",FACE,{"disambiguationData":[TD([makeQuery(id+"F8.opLoft","SWEPT_FACE",FACE,{"disambiguationData":[OSD([sQuery(id+"F3.wireOp",EDGE,"E20.13.0"),subQ4,subQ3,subQ6,subQ1,subQ0])]})])],"derivedFrom":makeQuery(id+"F42.opRevolve","SWEPT_FACE",FACE,{"disambiguationData":[OSD([subQ8]),TDD([makeQuery(id+"F41.imprint","IMPRINT",EDGE,{"disambiguationData":[TD([[makeQuery(id+"F41.imprint","INTERSECT",VERTEX,{"disambiguationData":[OD(0.0)],"derivedFrom":[subQ8,subQ7]}),-1.0]])],"derivedFrom":subQ8})])]})})]});}
            var Q77;
            {var subQ0=sQuery(id+"F41.wireOp",EDGE,"E34");var subQ1=sQuery(id+"F41.wireOp",EDGE,"E32");Q77=makeQuery(id+"F42.boolean.opBoolean","INTERSECT",EDGE,{"derivedFrom":[makeQuery(id+"F8.opLoft","SWEPT_FACE",FACE,{"disambiguationData":[OSD([sQuery(id+"F3.wireOp",EDGE,"E20.13.0"),sQuery(id+"F3.wireOp",EDGE,"E20.13.1"),sQuery(id+"F3.wireOp",EDGE,"E20.13.3"),sQuery(id+"F4.wireOp",EDGE,"E26.13.0"),sQuery(id+"F4.wireOp",EDGE,"E26.13.2"),sQuery(id+"F4.wireOp",EDGE,"E26.13.3")])]}),makeQuery(id+"F42.opRevolve","SWEPT_FACE",FACE,{"disambiguationData":[OSD([subQ1]),TDD([makeQuery(id+"F41.imprint","IMPRINT",EDGE,{"disambiguationData":[TD([[makeQuery(id+"F41.imprint","INTERSECT",VERTEX,{"disambiguationData":[OD(0.0)],"derivedFrom":[subQ1,subQ0]}),-1.0]])],"derivedFrom":subQ1})])]})]});}
            var Q78;
            {var subQ0=sQuery(id+"F4.wireOp",EDGE,"E26.14.0");var subQ1=sQuery(id+"F4.wireOp",EDGE,"E26.14.2");var subQ2=sQuery(id+"F4.wireOp",EDGE,"E26.14.1");var subQ3=sQuery(id+"F4.wireOp",EDGE,"E26.14.3");var subQ4=sQuery(id+"F3.wireOp",EDGE,"E20.14.3");var subQ5=sQuery(id+"F3.wireOp",EDGE,"E20.14.1");var subQ6=makeQuery(id+"F7.opLoft","SWEPT_FACE",FACE,{"disambiguationData":[OSD([subQ5,sQuery(id+"F3.wireOp",EDGE,"E20.14.2"),subQ4,subQ2,subQ1,subQ3])]});var subQ7=sQuery(id+"F41.wireOp",EDGE,"E34");var subQ8=sQuery(id+"F41.wireOp",EDGE,"E32");Q78=makeQuery(id+"F44.opFillet","BLEND_EDGE",EDGE,{"blendedFrom":[makeQuery(id+"F40.boolean.opBoolean","INTERSECT",EDGE,{"derivedFrom":[subQ6,makeQuery(id+"F40.opExtrude","CAP_FACE",FACE,{"disambiguationData":[OSD([sQuery(id+"F39.wireOp",EDGE,"E29"),sQuery(id+"F39.wireOp",EDGE,"E30")])],"isStart":false})]}),makeQuery(id+"F42.boolean.opBoolean","COPY",FACE,{"disambiguationData":[TD([makeQuery(id+"F7.opLoft","SWEPT_FACE",FACE,{"disambiguationData":[OSD([sQuery(id+"F3.wireOp",EDGE,"E20.14.0"),subQ5,subQ4,subQ0,subQ1,subQ3])]})])],"derivedFrom":makeQuery(id+"F42.opRevolve","SWEPT_FACE",FACE,{"disambiguationData":[OSD([subQ8]),TDD([makeQuery(id+"F41.imprint","IMPRINT",EDGE,{"disambiguationData":[TD([[makeQuery(id+"F41.imprint","INTERSECT",VERTEX,{"disambiguationData":[OD(0.0)],"derivedFrom":[subQ8,subQ7]}),-1.0]])],"derivedFrom":subQ8})])]})})],"blendedInto":[makeQuery(id+"F42.boolean.opBoolean","COPY",FACE,{"disambiguationData":[TD([makeQuery(id+"F7.opLoft","SWEPT_FACE",FACE,{"disambiguationData":[OSD([sQuery(id+"F3.wireOp",EDGE,"E20.14.0"),subQ5,subQ4,subQ0,subQ1,subQ3])]})])],"derivedFrom":makeQuery(id+"F42.opRevolve","SWEPT_FACE",FACE,{"disambiguationData":[OSD([subQ8]),TDD([makeQuery(id+"F41.imprint","IMPRINT",EDGE,{"disambiguationData":[TD([[makeQuery(id+"F41.imprint","INTERSECT",VERTEX,{"disambiguationData":[OD(0.0)],"derivedFrom":[subQ8,subQ7]}),-1.0]])],"derivedFrom":subQ8})])]})})]});}
            var Q79;
            {var subQ0=sQuery(id+"F41.wireOp",EDGE,"E34");var subQ1=sQuery(id+"F41.wireOp",EDGE,"E32");Q79=makeQuery(id+"F42.boolean.opBoolean","INTERSECT",EDGE,{"derivedFrom":[makeQuery(id+"F7.opLoft","SWEPT_FACE",FACE,{"disambiguationData":[OSD([sQuery(id+"F3.wireOp",EDGE,"E20.14.0"),sQuery(id+"F3.wireOp",EDGE,"E20.14.1"),sQuery(id+"F3.wireOp",EDGE,"E20.14.3"),sQuery(id+"F4.wireOp",EDGE,"E26.14.0"),sQuery(id+"F4.wireOp",EDGE,"E26.14.2"),sQuery(id+"F4.wireOp",EDGE,"E26.14.3")])]}),makeQuery(id+"F42.opRevolve","SWEPT_FACE",FACE,{"disambiguationData":[OSD([subQ1]),TDD([makeQuery(id+"F41.imprint","IMPRINT",EDGE,{"disambiguationData":[TD([[makeQuery(id+"F41.imprint","INTERSECT",VERTEX,{"disambiguationData":[OD(0.0)],"derivedFrom":[subQ1,subQ0]}),-1.0]])],"derivedFrom":subQ1})])]})]});}
            var Q80;
            {var subQ0=sQuery(id+"F4.wireOp",EDGE,"E26.15.3");var subQ1=sQuery(id+"F4.wireOp",EDGE,"E26.15.2");var subQ2=sQuery(id+"F4.wireOp",EDGE,"E26.15.0");var subQ3=sQuery(id+"F3.wireOp",EDGE,"E20.15.3");var subQ4=sQuery(id+"F3.wireOp",EDGE,"E20.15.1");var subQ5=sQuery(id+"F4.wireOp",EDGE,"E26.15.1");var subQ6=makeQuery(id+"F6.opLoft","SWEPT_FACE",FACE,{"disambiguationData":[OSD([subQ4,sQuery(id+"F3.wireOp",EDGE,"E20.15.2"),subQ3,subQ5,subQ1,subQ0])]});var subQ7=sQuery(id+"F41.wireOp",EDGE,"E34");var subQ8=sQuery(id+"F41.wireOp",EDGE,"E32");Q80=makeQuery(id+"F44.opFillet","BLEND_EDGE",EDGE,{"blendedFrom":[makeQuery(id+"F40.boolean.opBoolean","INTERSECT",EDGE,{"derivedFrom":[subQ6,makeQuery(id+"F40.opExtrude","CAP_FACE",FACE,{"disambiguationData":[OSD([sQuery(id+"F39.wireOp",EDGE,"E29"),sQuery(id+"F39.wireOp",EDGE,"E30")])],"isStart":false})]}),makeQuery(id+"F42.boolean.opBoolean","COPY",FACE,{"disambiguationData":[TD([makeQuery(id+"F6.opLoft","SWEPT_FACE",FACE,{"disambiguationData":[OSD([sQuery(id+"F3.wireOp",EDGE,"E20.15.0"),subQ4,subQ3,subQ2,subQ1,subQ0])]})])],"derivedFrom":makeQuery(id+"F42.opRevolve","SWEPT_FACE",FACE,{"disambiguationData":[OSD([subQ8]),TDD([makeQuery(id+"F41.imprint","IMPRINT",EDGE,{"disambiguationData":[TD([[makeQuery(id+"F41.imprint","INTERSECT",VERTEX,{"disambiguationData":[OD(0.0)],"derivedFrom":[subQ8,subQ7]}),-1.0]])],"derivedFrom":subQ8})])]})})],"blendedInto":[makeQuery(id+"F42.boolean.opBoolean","COPY",FACE,{"disambiguationData":[TD([makeQuery(id+"F6.opLoft","SWEPT_FACE",FACE,{"disambiguationData":[OSD([sQuery(id+"F3.wireOp",EDGE,"E20.15.0"),subQ4,subQ3,subQ2,subQ1,subQ0])]})])],"derivedFrom":makeQuery(id+"F42.opRevolve","SWEPT_FACE",FACE,{"disambiguationData":[OSD([subQ8]),TDD([makeQuery(id+"F41.imprint","IMPRINT",EDGE,{"disambiguationData":[TD([[makeQuery(id+"F41.imprint","INTERSECT",VERTEX,{"disambiguationData":[OD(0.0)],"derivedFrom":[subQ8,subQ7]}),-1.0]])],"derivedFrom":subQ8})])]})})]});}
            var Q81;
            {var subQ0=sQuery(id+"F41.wireOp",EDGE,"E34");var subQ1=sQuery(id+"F41.wireOp",EDGE,"E32");Q81=makeQuery(id+"F42.boolean.opBoolean","INTERSECT",EDGE,{"derivedFrom":[makeQuery(id+"F6.opLoft","SWEPT_FACE",FACE,{"disambiguationData":[OSD([sQuery(id+"F3.wireOp",EDGE,"E20.15.0"),sQuery(id+"F3.wireOp",EDGE,"E20.15.1"),sQuery(id+"F3.wireOp",EDGE,"E20.15.3"),sQuery(id+"F4.wireOp",EDGE,"E26.15.0"),sQuery(id+"F4.wireOp",EDGE,"E26.15.2"),sQuery(id+"F4.wireOp",EDGE,"E26.15.3")])]}),makeQuery(id+"F42.opRevolve","SWEPT_FACE",FACE,{"disambiguationData":[OSD([subQ1]),TDD([makeQuery(id+"F41.imprint","IMPRINT",EDGE,{"disambiguationData":[TD([[makeQuery(id+"F41.imprint","INTERSECT",VERTEX,{"disambiguationData":[OD(0.0)],"derivedFrom":[subQ1,subQ0]}),-1.0]])],"derivedFrom":subQ1})])]})]});}
            var Q82;
            {var subQ0=sQuery(id+"F4.wireOp",EDGE,"E23");var subQ1=sQuery(id+"F4.wireOp",EDGE,"E22");var subQ2=sQuery(id+"F4.wireOp",EDGE,"E21");var subQ3=sQuery(id+"F3.wireOp",EDGE,"E18.top");var subQ4=sQuery(id+"F3.wireOp",EDGE,"E18.bottom");var subQ5=sQuery(id+"F4.wireOp",EDGE,"E24");var subQ6=makeQuery(id+"F5.opLoft","SWEPT_FACE",FACE,{"disambiguationData":[OSD([subQ4,subQ3,sQuery(id+"F3.wireOp",EDGE,"E18.right"),subQ1,subQ0,subQ5])]});var subQ7=sQuery(id+"F41.wireOp",EDGE,"E34");var subQ8=sQuery(id+"F41.wireOp",EDGE,"E32");Q82=makeQuery(id+"F44.opFillet","BLEND_EDGE",EDGE,{"blendedFrom":[makeQuery(id+"F40.boolean.opBoolean","INTERSECT",EDGE,{"derivedFrom":[subQ6,makeQuery(id+"F40.opExtrude","CAP_FACE",FACE,{"disambiguationData":[OSD([sQuery(id+"F39.wireOp",EDGE,"E29"),sQuery(id+"F39.wireOp",EDGE,"E30")])],"isStart":false})]}),makeQuery(id+"F42.boolean.opBoolean","COPY",FACE,{"disambiguationData":[TD([makeQuery(id+"F5.opLoft","SWEPT_FACE",FACE,{"disambiguationData":[OSD([subQ4,subQ3,sQuery(id+"F3.wireOp",EDGE,"E18.left"),subQ2,subQ1,subQ0])]})])],"derivedFrom":makeQuery(id+"F42.opRevolve","SWEPT_FACE",FACE,{"disambiguationData":[OSD([subQ8]),TDD([makeQuery(id+"F41.imprint","IMPRINT",EDGE,{"disambiguationData":[TD([[makeQuery(id+"F41.imprint","INTERSECT",VERTEX,{"disambiguationData":[OD(0.0)],"derivedFrom":[subQ8,subQ7]}),-1.0]])],"derivedFrom":subQ8})])]})})],"blendedInto":[makeQuery(id+"F42.boolean.opBoolean","COPY",FACE,{"disambiguationData":[TD([makeQuery(id+"F5.opLoft","SWEPT_FACE",FACE,{"disambiguationData":[OSD([subQ4,subQ3,sQuery(id+"F3.wireOp",EDGE,"E18.left"),subQ2,subQ1,subQ0])]})])],"derivedFrom":makeQuery(id+"F42.opRevolve","SWEPT_FACE",FACE,{"disambiguationData":[OSD([subQ8]),TDD([makeQuery(id+"F41.imprint","IMPRINT",EDGE,{"disambiguationData":[TD([[makeQuery(id+"F41.imprint","INTERSECT",VERTEX,{"disambiguationData":[OD(0.0)],"derivedFrom":[subQ8,subQ7]}),-1.0]])],"derivedFrom":subQ8})])]})})]});}
            var Q83;
            {var subQ0=sQuery(id+"F41.wireOp",EDGE,"E34");var subQ1=sQuery(id+"F41.wireOp",EDGE,"E32");Q83=makeQuery(id+"F42.boolean.opBoolean","INTERSECT",EDGE,{"derivedFrom":[makeQuery(id+"F5.opLoft","SWEPT_FACE",FACE,{"disambiguationData":[OSD([sQuery(id+"F3.wireOp",EDGE,"E18.bottom"),sQuery(id+"F3.wireOp",EDGE,"E18.top"),sQuery(id+"F3.wireOp",EDGE,"E18.left"),sQuery(id+"F4.wireOp",EDGE,"E21"),sQuery(id+"F4.wireOp",EDGE,"E22"),sQuery(id+"F4.wireOp",EDGE,"E23")])]}),makeQuery(id+"F42.opRevolve","SWEPT_FACE",FACE,{"disambiguationData":[OSD([subQ1]),TDD([makeQuery(id+"F41.imprint","IMPRINT",EDGE,{"disambiguationData":[TD([[makeQuery(id+"F41.imprint","INTERSECT",VERTEX,{"disambiguationData":[OD(0.0)],"derivedFrom":[subQ1,subQ0]}),-1.0]])],"derivedFrom":subQ1})])]})]});}
            var Q84;
            {var subQ0=sQuery(id+"F4.wireOp",EDGE,"E26.1.3");var subQ1=sQuery(id+"F4.wireOp",EDGE,"E26.1.2");var subQ2=sQuery(id+"F4.wireOp",EDGE,"E26.1.0");var subQ3=sQuery(id+"F3.wireOp",EDGE,"E20.1.3");var subQ4=sQuery(id+"F3.wireOp",EDGE,"E20.1.1");var subQ5=sQuery(id+"F4.wireOp",EDGE,"E26.1.1");var subQ6=makeQuery(id+"F20.opLoft","SWEPT_FACE",FACE,{"disambiguationData":[OSD([subQ4,sQuery(id+"F3.wireOp",EDGE,"E20.1.2"),subQ3,subQ5,subQ1,subQ0])]});var subQ7=sQuery(id+"F41.wireOp",EDGE,"E34");var subQ8=sQuery(id+"F41.wireOp",EDGE,"E32");Q84=makeQuery(id+"F44.opFillet","BLEND_EDGE",EDGE,{"blendedFrom":[makeQuery(id+"F40.boolean.opBoolean","INTERSECT",EDGE,{"derivedFrom":[subQ6,makeQuery(id+"F40.opExtrude","CAP_FACE",FACE,{"disambiguationData":[OSD([sQuery(id+"F39.wireOp",EDGE,"E29"),sQuery(id+"F39.wireOp",EDGE,"E30")])],"isStart":false})]}),makeQuery(id+"F42.boolean.opBoolean","COPY",FACE,{"disambiguationData":[TD([makeQuery(id+"F20.opLoft","SWEPT_FACE",FACE,{"disambiguationData":[OSD([sQuery(id+"F3.wireOp",EDGE,"E20.1.0"),subQ4,subQ3,subQ2,subQ1,subQ0])]})])],"derivedFrom":makeQuery(id+"F42.opRevolve","SWEPT_FACE",FACE,{"disambiguationData":[OSD([subQ8]),TDD([makeQuery(id+"F41.imprint","IMPRINT",EDGE,{"disambiguationData":[TD([[makeQuery(id+"F41.imprint","INTERSECT",VERTEX,{"disambiguationData":[OD(0.0)],"derivedFrom":[subQ8,subQ7]}),-1.0]])],"derivedFrom":subQ8})])]})})],"blendedInto":[makeQuery(id+"F42.boolean.opBoolean","COPY",FACE,{"disambiguationData":[TD([makeQuery(id+"F20.opLoft","SWEPT_FACE",FACE,{"disambiguationData":[OSD([sQuery(id+"F3.wireOp",EDGE,"E20.1.0"),subQ4,subQ3,subQ2,subQ1,subQ0])]})])],"derivedFrom":makeQuery(id+"F42.opRevolve","SWEPT_FACE",FACE,{"disambiguationData":[OSD([subQ8]),TDD([makeQuery(id+"F41.imprint","IMPRINT",EDGE,{"disambiguationData":[TD([[makeQuery(id+"F41.imprint","INTERSECT",VERTEX,{"disambiguationData":[OD(0.0)],"derivedFrom":[subQ8,subQ7]}),-1.0]])],"derivedFrom":subQ8})])]})})]});}
            var Q85;
            {var subQ0=sQuery(id+"F41.wireOp",EDGE,"E34");var subQ1=sQuery(id+"F41.wireOp",EDGE,"E32");Q85=makeQuery(id+"F42.boolean.opBoolean","INTERSECT",EDGE,{"derivedFrom":[makeQuery(id+"F20.opLoft","SWEPT_FACE",FACE,{"disambiguationData":[OSD([sQuery(id+"F3.wireOp",EDGE,"E20.1.0"),sQuery(id+"F3.wireOp",EDGE,"E20.1.1"),sQuery(id+"F3.wireOp",EDGE,"E20.1.3"),sQuery(id+"F4.wireOp",EDGE,"E26.1.0"),sQuery(id+"F4.wireOp",EDGE,"E26.1.2"),sQuery(id+"F4.wireOp",EDGE,"E26.1.3")])]}),makeQuery(id+"F42.opRevolve","SWEPT_FACE",FACE,{"disambiguationData":[OSD([subQ1]),TDD([makeQuery(id+"F41.imprint","IMPRINT",EDGE,{"disambiguationData":[TD([[makeQuery(id+"F41.imprint","INTERSECT",VERTEX,{"disambiguationData":[OD(0.0)],"derivedFrom":[subQ1,subQ0]}),-1.0]])],"derivedFrom":subQ1})])]})]});}
            var Q86;
            {var subQ0=sQuery(id+"F4.wireOp",EDGE,"E26.2.3");var subQ1=sQuery(id+"F4.wireOp",EDGE,"E26.2.2");var subQ2=sQuery(id+"F4.wireOp",EDGE,"E26.2.1");var subQ3=sQuery(id+"F3.wireOp",EDGE,"E20.2.3");var subQ4=sQuery(id+"F3.wireOp",EDGE,"E20.2.1");var subQ5=makeQuery(id+"F19.opLoft","SWEPT_FACE",FACE,{"disambiguationData":[OSD([subQ4,sQuery(id+"F3.wireOp",EDGE,"E20.2.2"),subQ3,subQ2,subQ1,subQ0])]});var subQ6=sQuery(id+"F4.wireOp",EDGE,"E26.2.0");var subQ7=sQuery(id+"F41.wireOp",EDGE,"E34");var subQ8=sQuery(id+"F41.wireOp",EDGE,"E32");Q86=makeQuery(id+"F44.opFillet","BLEND_EDGE",EDGE,{"blendedFrom":[makeQuery(id+"F40.boolean.opBoolean","INTERSECT",EDGE,{"derivedFrom":[subQ5,makeQuery(id+"F40.opExtrude","CAP_FACE",FACE,{"disambiguationData":[OSD([sQuery(id+"F39.wireOp",EDGE,"E29"),sQuery(id+"F39.wireOp",EDGE,"E30")])],"isStart":false})]}),makeQuery(id+"F42.boolean.opBoolean","COPY",FACE,{"disambiguationData":[TD([makeQuery(id+"F19.opLoft","SWEPT_FACE",FACE,{"disambiguationData":[OSD([sQuery(id+"F3.wireOp",EDGE,"E20.2.0"),subQ4,subQ3,subQ6,subQ1,subQ0])]})])],"derivedFrom":makeQuery(id+"F42.opRevolve","SWEPT_FACE",FACE,{"disambiguationData":[OSD([subQ8]),TDD([makeQuery(id+"F41.imprint","IMPRINT",EDGE,{"disambiguationData":[TD([[makeQuery(id+"F41.imprint","INTERSECT",VERTEX,{"disambiguationData":[OD(0.0)],"derivedFrom":[subQ8,subQ7]}),-1.0]])],"derivedFrom":subQ8})])]})})],"blendedInto":[makeQuery(id+"F42.boolean.opBoolean","COPY",FACE,{"disambiguationData":[TD([makeQuery(id+"F19.opLoft","SWEPT_FACE",FACE,{"disambiguationData":[OSD([sQuery(id+"F3.wireOp",EDGE,"E20.2.0"),subQ4,subQ3,subQ6,subQ1,subQ0])]})])],"derivedFrom":makeQuery(id+"F42.opRevolve","SWEPT_FACE",FACE,{"disambiguationData":[OSD([subQ8]),TDD([makeQuery(id+"F41.imprint","IMPRINT",EDGE,{"disambiguationData":[TD([[makeQuery(id+"F41.imprint","INTERSECT",VERTEX,{"disambiguationData":[OD(0.0)],"derivedFrom":[subQ8,subQ7]}),-1.0]])],"derivedFrom":subQ8})])]})})]});}
            var Q87;
            {var subQ0=sQuery(id+"F41.wireOp",EDGE,"E34");var subQ1=sQuery(id+"F41.wireOp",EDGE,"E32");Q87=makeQuery(id+"F42.boolean.opBoolean","INTERSECT",EDGE,{"derivedFrom":[makeQuery(id+"F19.opLoft","SWEPT_FACE",FACE,{"disambiguationData":[OSD([sQuery(id+"F3.wireOp",EDGE,"E20.2.0"),sQuery(id+"F3.wireOp",EDGE,"E20.2.1"),sQuery(id+"F3.wireOp",EDGE,"E20.2.3"),sQuery(id+"F4.wireOp",EDGE,"E26.2.0"),sQuery(id+"F4.wireOp",EDGE,"E26.2.2"),sQuery(id+"F4.wireOp",EDGE,"E26.2.3")])]}),makeQuery(id+"F42.opRevolve","SWEPT_FACE",FACE,{"disambiguationData":[OSD([subQ1]),TDD([makeQuery(id+"F41.imprint","IMPRINT",EDGE,{"disambiguationData":[TD([[makeQuery(id+"F41.imprint","INTERSECT",VERTEX,{"disambiguationData":[OD(0.0)],"derivedFrom":[subQ1,subQ0]}),-1.0]])],"derivedFrom":subQ1})])]})]});}
            var Q88;
            {var subQ0=sQuery(id+"F4.wireOp",EDGE,"E26.3.0");var subQ1=sQuery(id+"F4.wireOp",EDGE,"E26.3.1");var subQ2=sQuery(id+"F4.wireOp",EDGE,"E26.3.2");var subQ3=sQuery(id+"F4.wireOp",EDGE,"E26.3.3");var subQ4=sQuery(id+"F3.wireOp",EDGE,"E20.3.3");var subQ5=sQuery(id+"F3.wireOp",EDGE,"E20.3.1");var subQ6=makeQuery(id+"F18.opLoft","SWEPT_FACE",FACE,{"disambiguationData":[OSD([subQ5,sQuery(id+"F3.wireOp",EDGE,"E20.3.2"),subQ4,subQ1,subQ2,subQ3])]});var subQ7=sQuery(id+"F41.wireOp",EDGE,"E34");var subQ8=sQuery(id+"F41.wireOp",EDGE,"E32");Q88=makeQuery(id+"F44.opFillet","BLEND_EDGE",EDGE,{"blendedFrom":[makeQuery(id+"F40.boolean.opBoolean","INTERSECT",EDGE,{"derivedFrom":[subQ6,makeQuery(id+"F40.opExtrude","CAP_FACE",FACE,{"disambiguationData":[OSD([sQuery(id+"F39.wireOp",EDGE,"E29"),sQuery(id+"F39.wireOp",EDGE,"E30")])],"isStart":false})]}),makeQuery(id+"F42.boolean.opBoolean","COPY",FACE,{"disambiguationData":[TD([makeQuery(id+"F18.opLoft","SWEPT_FACE",FACE,{"disambiguationData":[OSD([sQuery(id+"F3.wireOp",EDGE,"E20.3.0"),subQ5,subQ4,subQ0,subQ2,subQ3])]})])],"derivedFrom":makeQuery(id+"F42.opRevolve","SWEPT_FACE",FACE,{"disambiguationData":[OSD([subQ8]),TDD([makeQuery(id+"F41.imprint","IMPRINT",EDGE,{"disambiguationData":[TD([[makeQuery(id+"F41.imprint","INTERSECT",VERTEX,{"disambiguationData":[OD(0.0)],"derivedFrom":[subQ8,subQ7]}),-1.0]])],"derivedFrom":subQ8})])]})})],"blendedInto":[makeQuery(id+"F42.boolean.opBoolean","COPY",FACE,{"disambiguationData":[TD([makeQuery(id+"F18.opLoft","SWEPT_FACE",FACE,{"disambiguationData":[OSD([sQuery(id+"F3.wireOp",EDGE,"E20.3.0"),subQ5,subQ4,subQ0,subQ2,subQ3])]})])],"derivedFrom":makeQuery(id+"F42.opRevolve","SWEPT_FACE",FACE,{"disambiguationData":[OSD([subQ8]),TDD([makeQuery(id+"F41.imprint","IMPRINT",EDGE,{"disambiguationData":[TD([[makeQuery(id+"F41.imprint","INTERSECT",VERTEX,{"disambiguationData":[OD(0.0)],"derivedFrom":[subQ8,subQ7]}),-1.0]])],"derivedFrom":subQ8})])]})})]});}
            var Q89;
            {var subQ0=sQuery(id+"F41.wireOp",EDGE,"E34");var subQ1=sQuery(id+"F41.wireOp",EDGE,"E32");Q89=makeQuery(id+"F42.boolean.opBoolean","INTERSECT",EDGE,{"derivedFrom":[makeQuery(id+"F18.opLoft","SWEPT_FACE",FACE,{"disambiguationData":[OSD([sQuery(id+"F3.wireOp",EDGE,"E20.3.0"),sQuery(id+"F3.wireOp",EDGE,"E20.3.1"),sQuery(id+"F3.wireOp",EDGE,"E20.3.3"),sQuery(id+"F4.wireOp",EDGE,"E26.3.0"),sQuery(id+"F4.wireOp",EDGE,"E26.3.2"),sQuery(id+"F4.wireOp",EDGE,"E26.3.3")])]}),makeQuery(id+"F42.opRevolve","SWEPT_FACE",FACE,{"disambiguationData":[OSD([subQ1]),TDD([makeQuery(id+"F41.imprint","IMPRINT",EDGE,{"disambiguationData":[TD([[makeQuery(id+"F41.imprint","INTERSECT",VERTEX,{"disambiguationData":[OD(0.0)],"derivedFrom":[subQ1,subQ0]}),-1.0]])],"derivedFrom":subQ1})])]})]});}
            var Q90;
            {var subQ0=sQuery(id+"F4.wireOp",EDGE,"E26.4.3");var subQ1=sQuery(id+"F4.wireOp",EDGE,"E26.4.2");var subQ2=sQuery(id+"F4.wireOp",EDGE,"E26.4.1");var subQ3=sQuery(id+"F3.wireOp",EDGE,"E20.4.3");var subQ4=sQuery(id+"F3.wireOp",EDGE,"E20.4.1");var subQ5=makeQuery(id+"F17.opLoft","SWEPT_FACE",FACE,{"disambiguationData":[OSD([subQ4,sQuery(id+"F3.wireOp",EDGE,"E20.4.2"),subQ3,subQ2,subQ1,subQ0])]});var subQ6=sQuery(id+"F4.wireOp",EDGE,"E26.4.0");var subQ7=sQuery(id+"F41.wireOp",EDGE,"E34");var subQ8=sQuery(id+"F41.wireOp",EDGE,"E32");Q90=makeQuery(id+"F44.opFillet","BLEND_EDGE",EDGE,{"blendedFrom":[makeQuery(id+"F40.boolean.opBoolean","INTERSECT",EDGE,{"derivedFrom":[subQ5,makeQuery(id+"F40.opExtrude","CAP_FACE",FACE,{"disambiguationData":[OSD([sQuery(id+"F39.wireOp",EDGE,"E29"),sQuery(id+"F39.wireOp",EDGE,"E30")])],"isStart":false})]}),makeQuery(id+"F42.boolean.opBoolean","COPY",FACE,{"disambiguationData":[TD([makeQuery(id+"F17.opLoft","SWEPT_FACE",FACE,{"disambiguationData":[OSD([sQuery(id+"F3.wireOp",EDGE,"E20.4.0"),subQ4,subQ3,subQ6,subQ1,subQ0])]})])],"derivedFrom":makeQuery(id+"F42.opRevolve","SWEPT_FACE",FACE,{"disambiguationData":[OSD([subQ8]),TDD([makeQuery(id+"F41.imprint","IMPRINT",EDGE,{"disambiguationData":[TD([[makeQuery(id+"F41.imprint","INTERSECT",VERTEX,{"disambiguationData":[OD(0.0)],"derivedFrom":[subQ8,subQ7]}),-1.0]])],"derivedFrom":subQ8})])]})})],"blendedInto":[makeQuery(id+"F42.boolean.opBoolean","COPY",FACE,{"disambiguationData":[TD([makeQuery(id+"F17.opLoft","SWEPT_FACE",FACE,{"disambiguationData":[OSD([sQuery(id+"F3.wireOp",EDGE,"E20.4.0"),subQ4,subQ3,subQ6,subQ1,subQ0])]})])],"derivedFrom":makeQuery(id+"F42.opRevolve","SWEPT_FACE",FACE,{"disambiguationData":[OSD([subQ8]),TDD([makeQuery(id+"F41.imprint","IMPRINT",EDGE,{"disambiguationData":[TD([[makeQuery(id+"F41.imprint","INTERSECT",VERTEX,{"disambiguationData":[OD(0.0)],"derivedFrom":[subQ8,subQ7]}),-1.0]])],"derivedFrom":subQ8})])]})})]});}
            var Q91;
            {var subQ0=sQuery(id+"F41.wireOp",EDGE,"E34");var subQ1=sQuery(id+"F41.wireOp",EDGE,"E32");Q91=makeQuery(id+"F42.boolean.opBoolean","INTERSECT",EDGE,{"derivedFrom":[makeQuery(id+"F17.opLoft","SWEPT_FACE",FACE,{"disambiguationData":[OSD([sQuery(id+"F3.wireOp",EDGE,"E20.4.0"),sQuery(id+"F3.wireOp",EDGE,"E20.4.1"),sQuery(id+"F3.wireOp",EDGE,"E20.4.3"),sQuery(id+"F4.wireOp",EDGE,"E26.4.0"),sQuery(id+"F4.wireOp",EDGE,"E26.4.2"),sQuery(id+"F4.wireOp",EDGE,"E26.4.3")])]}),makeQuery(id+"F42.opRevolve","SWEPT_FACE",FACE,{"disambiguationData":[OSD([subQ1]),TDD([makeQuery(id+"F41.imprint","IMPRINT",EDGE,{"disambiguationData":[TD([[makeQuery(id+"F41.imprint","INTERSECT",VERTEX,{"disambiguationData":[OD(0.0)],"derivedFrom":[subQ1,subQ0]}),-1.0]])],"derivedFrom":subQ1})])]})]});}
            var Q92;
            {var subQ0=sQuery(id+"F4.wireOp",EDGE,"E26.5.3");var subQ1=sQuery(id+"F4.wireOp",EDGE,"E26.5.2");var subQ2=sQuery(id+"F4.wireOp",EDGE,"E26.5.1");var subQ3=sQuery(id+"F3.wireOp",EDGE,"E20.5.3");var subQ4=sQuery(id+"F3.wireOp",EDGE,"E20.5.1");var subQ5=makeQuery(id+"F16.opLoft","SWEPT_FACE",FACE,{"disambiguationData":[OSD([subQ4,sQuery(id+"F3.wireOp",EDGE,"E20.5.2"),subQ3,subQ2,subQ1,subQ0])]});var subQ6=sQuery(id+"F4.wireOp",EDGE,"E26.5.0");var subQ7=sQuery(id+"F41.wireOp",EDGE,"E34");var subQ8=sQuery(id+"F41.wireOp",EDGE,"E32");Q92=makeQuery(id+"F44.opFillet","BLEND_EDGE",EDGE,{"blendedFrom":[makeQuery(id+"F40.boolean.opBoolean","INTERSECT",EDGE,{"derivedFrom":[subQ5,makeQuery(id+"F40.opExtrude","CAP_FACE",FACE,{"disambiguationData":[OSD([sQuery(id+"F39.wireOp",EDGE,"E29"),sQuery(id+"F39.wireOp",EDGE,"E30")])],"isStart":false})]}),makeQuery(id+"F42.boolean.opBoolean","COPY",FACE,{"disambiguationData":[TD([makeQuery(id+"F16.opLoft","SWEPT_FACE",FACE,{"disambiguationData":[OSD([sQuery(id+"F3.wireOp",EDGE,"E20.5.0"),subQ4,subQ3,subQ6,subQ1,subQ0])]})])],"derivedFrom":makeQuery(id+"F42.opRevolve","SWEPT_FACE",FACE,{"disambiguationData":[OSD([subQ8]),TDD([makeQuery(id+"F41.imprint","IMPRINT",EDGE,{"disambiguationData":[TD([[makeQuery(id+"F41.imprint","INTERSECT",VERTEX,{"disambiguationData":[OD(0.0)],"derivedFrom":[subQ8,subQ7]}),-1.0]])],"derivedFrom":subQ8})])]})})],"blendedInto":[makeQuery(id+"F42.boolean.opBoolean","COPY",FACE,{"disambiguationData":[TD([makeQuery(id+"F16.opLoft","SWEPT_FACE",FACE,{"disambiguationData":[OSD([sQuery(id+"F3.wireOp",EDGE,"E20.5.0"),subQ4,subQ3,subQ6,subQ1,subQ0])]})])],"derivedFrom":makeQuery(id+"F42.opRevolve","SWEPT_FACE",FACE,{"disambiguationData":[OSD([subQ8]),TDD([makeQuery(id+"F41.imprint","IMPRINT",EDGE,{"disambiguationData":[TD([[makeQuery(id+"F41.imprint","INTERSECT",VERTEX,{"disambiguationData":[OD(0.0)],"derivedFrom":[subQ8,subQ7]}),-1.0]])],"derivedFrom":subQ8})])]})})]});}
            var Q93;
            {var subQ0=sQuery(id+"F41.wireOp",EDGE,"E34");var subQ1=sQuery(id+"F41.wireOp",EDGE,"E32");Q93=makeQuery(id+"F42.boolean.opBoolean","INTERSECT",EDGE,{"derivedFrom":[makeQuery(id+"F16.opLoft","SWEPT_FACE",FACE,{"disambiguationData":[OSD([sQuery(id+"F3.wireOp",EDGE,"E20.5.0"),sQuery(id+"F3.wireOp",EDGE,"E20.5.1"),sQuery(id+"F3.wireOp",EDGE,"E20.5.3"),sQuery(id+"F4.wireOp",EDGE,"E26.5.0"),sQuery(id+"F4.wireOp",EDGE,"E26.5.2"),sQuery(id+"F4.wireOp",EDGE,"E26.5.3")])]}),makeQuery(id+"F42.opRevolve","SWEPT_FACE",FACE,{"disambiguationData":[OSD([subQ1]),TDD([makeQuery(id+"F41.imprint","IMPRINT",EDGE,{"disambiguationData":[TD([[makeQuery(id+"F41.imprint","INTERSECT",VERTEX,{"disambiguationData":[OD(0.0)],"derivedFrom":[subQ1,subQ0]}),-1.0]])],"derivedFrom":subQ1})])]})]});}
            var Q94;
            {var subQ0=sQuery(id+"F4.wireOp",EDGE,"E26.6.3");var subQ1=sQuery(id+"F4.wireOp",EDGE,"E26.6.2");var subQ2=sQuery(id+"F4.wireOp",EDGE,"E26.6.0");var subQ3=sQuery(id+"F3.wireOp",EDGE,"E20.6.3");var subQ4=sQuery(id+"F3.wireOp",EDGE,"E20.6.1");var subQ5=sQuery(id+"F4.wireOp",EDGE,"E26.6.1");var subQ6=makeQuery(id+"F15.opLoft","SWEPT_FACE",FACE,{"disambiguationData":[OSD([subQ4,sQuery(id+"F3.wireOp",EDGE,"E20.6.2"),subQ3,subQ5,subQ1,subQ0])]});var subQ7=sQuery(id+"F41.wireOp",EDGE,"E34");var subQ8=sQuery(id+"F41.wireOp",EDGE,"E32");Q94=makeQuery(id+"F44.opFillet","BLEND_EDGE",EDGE,{"blendedFrom":[makeQuery(id+"F40.boolean.opBoolean","INTERSECT",EDGE,{"derivedFrom":[subQ6,makeQuery(id+"F40.opExtrude","CAP_FACE",FACE,{"disambiguationData":[OSD([sQuery(id+"F39.wireOp",EDGE,"E29"),sQuery(id+"F39.wireOp",EDGE,"E30")])],"isStart":false})]}),makeQuery(id+"F42.boolean.opBoolean","COPY",FACE,{"disambiguationData":[TD([makeQuery(id+"F15.opLoft","SWEPT_FACE",FACE,{"disambiguationData":[OSD([sQuery(id+"F3.wireOp",EDGE,"E20.6.0"),subQ4,subQ3,subQ2,subQ1,subQ0])]})])],"derivedFrom":makeQuery(id+"F42.opRevolve","SWEPT_FACE",FACE,{"disambiguationData":[OSD([subQ8]),TDD([makeQuery(id+"F41.imprint","IMPRINT",EDGE,{"disambiguationData":[TD([[makeQuery(id+"F41.imprint","INTERSECT",VERTEX,{"disambiguationData":[OD(0.0)],"derivedFrom":[subQ8,subQ7]}),-1.0]])],"derivedFrom":subQ8})])]})})],"blendedInto":[makeQuery(id+"F42.boolean.opBoolean","COPY",FACE,{"disambiguationData":[TD([makeQuery(id+"F15.opLoft","SWEPT_FACE",FACE,{"disambiguationData":[OSD([sQuery(id+"F3.wireOp",EDGE,"E20.6.0"),subQ4,subQ3,subQ2,subQ1,subQ0])]})])],"derivedFrom":makeQuery(id+"F42.opRevolve","SWEPT_FACE",FACE,{"disambiguationData":[OSD([subQ8]),TDD([makeQuery(id+"F41.imprint","IMPRINT",EDGE,{"disambiguationData":[TD([[makeQuery(id+"F41.imprint","INTERSECT",VERTEX,{"disambiguationData":[OD(0.0)],"derivedFrom":[subQ8,subQ7]}),-1.0]])],"derivedFrom":subQ8})])]})})]});}
            var Q95;
            {var subQ0=sQuery(id+"F41.wireOp",EDGE,"E34");var subQ1=sQuery(id+"F41.wireOp",EDGE,"E32");Q95=makeQuery(id+"F42.boolean.opBoolean","INTERSECT",EDGE,{"derivedFrom":[makeQuery(id+"F15.opLoft","SWEPT_FACE",FACE,{"disambiguationData":[OSD([sQuery(id+"F3.wireOp",EDGE,"E20.6.0"),sQuery(id+"F3.wireOp",EDGE,"E20.6.1"),sQuery(id+"F3.wireOp",EDGE,"E20.6.3"),sQuery(id+"F4.wireOp",EDGE,"E26.6.0"),sQuery(id+"F4.wireOp",EDGE,"E26.6.2"),sQuery(id+"F4.wireOp",EDGE,"E26.6.3")])]}),makeQuery(id+"F42.opRevolve","SWEPT_FACE",FACE,{"disambiguationData":[OSD([subQ1]),TDD([makeQuery(id+"F41.imprint","IMPRINT",EDGE,{"disambiguationData":[TD([[makeQuery(id+"F41.imprint","INTERSECT",VERTEX,{"disambiguationData":[OD(0.0)],"derivedFrom":[subQ1,subQ0]}),-1.0]])],"derivedFrom":subQ1})])]})]});}
            fillet(context, id + "F49", {"entities" : qUnion([Q0, Q1, Q2, Q3, Q4, Q5, Q6, Q7, Q8, Q9, Q10, Q11, Q12, Q13, Q14, Q15, Q16, Q17, Q18, Q19, Q20, Q21, Q22, Q23, Q24, Q25, Q26, Q27, Q28, Q29, Q30, Q31, Q32, Q33, Q34, Q35, Q36, Q37, Q38, Q39, Q40, Q41, Q42, Q43, Q44, Q45, Q46, Q47, Q48, Q49, Q50, Q51, Q52, Q53, Q54, Q55, Q56, Q57, Q58, Q59, Q60, Q61, Q62, Q63, Q64, Q65, Q66, Q67, Q68, Q69, Q70, Q71, Q72, Q73, Q74, Q75, Q76, Q77, Q78, Q79, Q80, Q81, Q82, Q83, Q84, Q85, Q86, Q87, Q88, Q89, Q90, Q91, Q92, Q93, Q94, Q95]), "radius" : 0.5 * mm, "tangentPropagation" : true, "allowEdgeOverflow" : false});
        }
        {
            var Q0;
            {var subQ0=sQuery(id+"F0.wireOp",EDGE,"E7");Q0=makeQuery(id+"F46.opChamfer","BLEND_EDGE",EDGE,{"blendedFrom":[makeQuery(id+"F1.opRevolve","SWEPT_EDGE",EDGE,{"disambiguationData":[OSD([subQ0,sQuery(id+"F0.wireOp",EDGE,"E15")])]}),makeQuery(id+"F1.opRevolve","SWEPT_FACE",FACE,{"disambiguationData":[OSD([subQ0])]})],"blendedInto":[makeQuery(id+"F1.opRevolve","SWEPT_FACE",FACE,{"disambiguationData":[OSD([subQ0])]})]});}
            var Q1;
            Q1=makeQuery(id+"F1.opRevolve","SWEPT_EDGE",EDGE,{"disambiguationData":[OSD([sQuery(id+"F0.wireOp",EDGE,"E6"),sQuery(id+"F0.wireOp",EDGE,"E7")])]});
            var Q2;
            {var subQ0=sQuery(id+"F0.wireOp",EDGE,"E0");Q2=makeQuery(id+"F46.opChamfer","BLEND_EDGE",EDGE,{"blendedFrom":[makeQuery(id+"F1.opRevolve","SWEPT_EDGE",EDGE,{"disambiguationData":[OSD([subQ0,sQuery(id+"F0.wireOp",EDGE,"E14")])]}),makeQuery(id+"F1.opRevolve","SWEPT_FACE",FACE,{"disambiguationData":[OSD([subQ0])]})],"blendedInto":[makeQuery(id+"F1.opRevolve","SWEPT_FACE",FACE,{"disambiguationData":[OSD([subQ0])]})]});}
            var Q3;
            Q3=makeQuery(id+"F1.opRevolve","SWEPT_EDGE",EDGE,{"disambiguationData":[OSD([sQuery(id+"F0.wireOp",EDGE,"E0"),sQuery(id+"F0.wireOp",EDGE,"E1")])]});
            fillet(context, id + "F50", {"entities" : qUnion([Q0, Q1, Q2, Q3]), "radius" : 0.5 * mm, "tangentPropagation" : true, "allowEdgeOverflow" : false});
        }
    });
